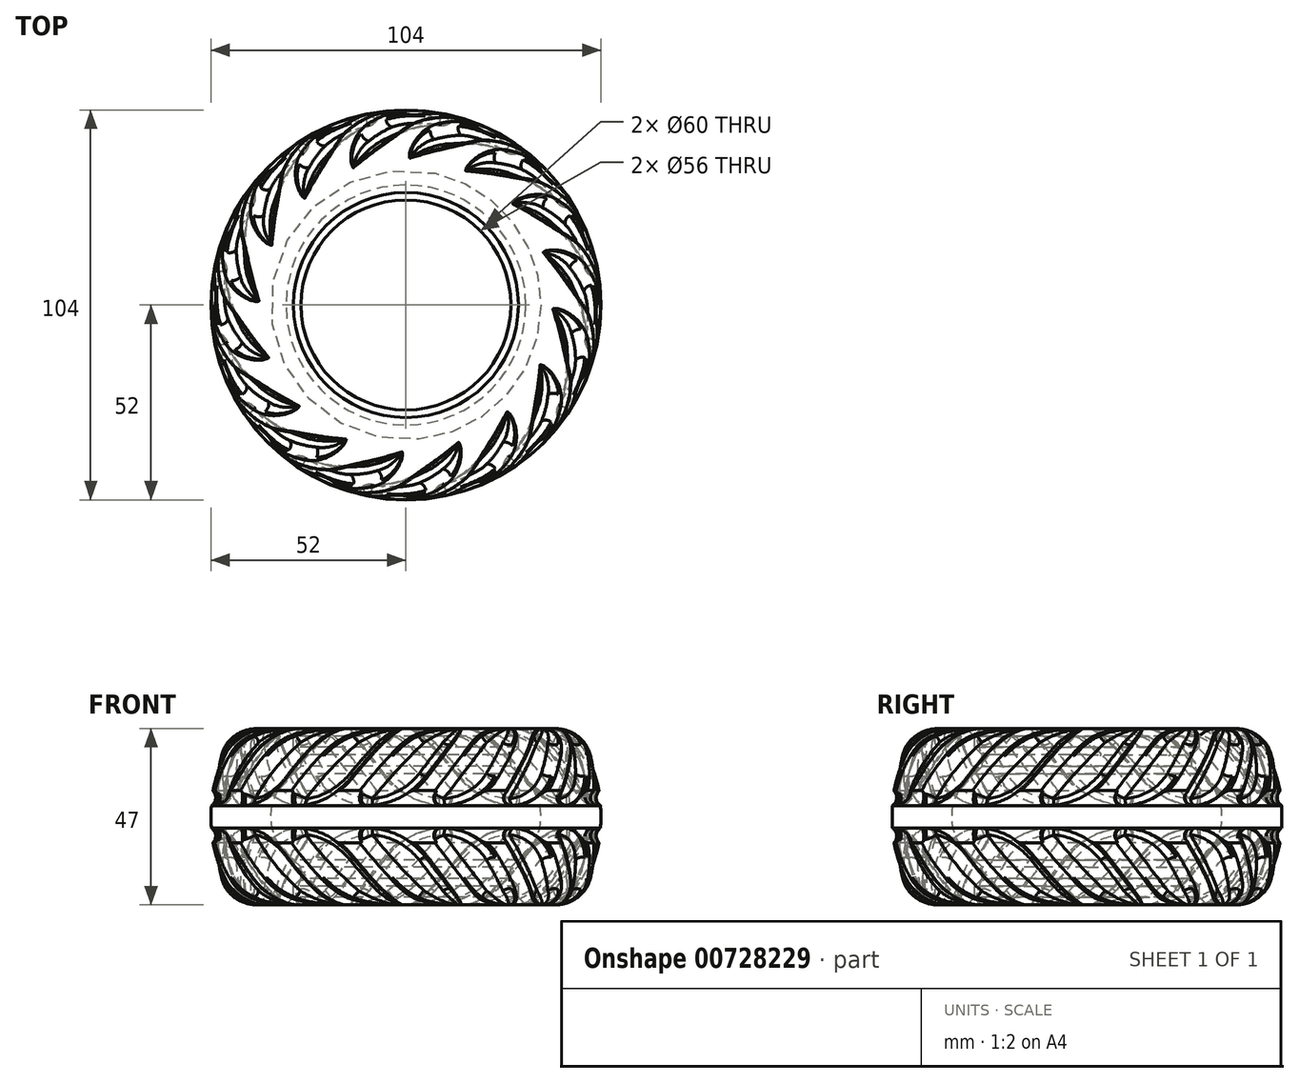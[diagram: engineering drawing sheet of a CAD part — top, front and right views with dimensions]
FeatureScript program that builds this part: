
annotation { "Feature Type Name" : "Feature", "Feature Type Description" : "" }
export const myFeature = defineFeature(function(context is Context, id is Id, definition is map)
    precondition{}
    {
        {
            var Q0;
            Q0=qCreatedBy(makeId("Front.planeOp"),FACE);
            var sketch = newSketch(context, id + "F0", { "sketchPlane" : qUnion([Q0])});
            skLineSegment(sketch, "E0", {"start": v(0, 0) * mm, "end": v(-62.9, 0) * mm, "construction": true});
            skCircle(sketch, "E1", {"center": v(-39.12, 17.25) * mm, "radius": 6.25 * mm});
            skCircle(sketch, "E2", {"center": v(0, 0) * mm, "radius": 55 * mm});
            skCircle(sketch, "E3", {"center": v(-39.12, -17.25) * mm, "radius": 6.25 * mm});
            skCircle(sketch, "E4", {"center": v(0, 0) * mm, "radius": 49 * mm});
            skLineSegment(sketch, "E5", {"start": v(-30, 23.5) * mm, "end": v(-39.12, 23.5) * mm});
            skLineSegment(sketch, "E6", {"start": v(-30, -23.5) * mm, "end": v(-39.12, -23.5) * mm});
            skLineSegment(sketch, "E7", {"start": v(0, 89.19) * mm, "end": v(0, -93.9) * mm, "construction": true});
            skLineSegment(sketch, "E8", {"start": v(-30, 23.5) * mm, "end": v(-30, 18.5) * mm});
            skLineSegment(sketch, "E9", {"start": v(-30, 18.5) * mm, "end": v(-28, 18.5) * mm});
            skLineSegment(sketch, "E10", {"start": v(-28, 18.5) * mm, "end": v(-28, 11.5) * mm});
            skLineSegment(sketch, "E11", {"start": v(-28, 11.5) * mm, "end": v(-30, 11.5) * mm});
            skLineSegment(sketch, "E12", {"start": v(-30, 11.5) * mm, "end": v(-30, -11.5) * mm});
            skLineSegment(sketch, "E13", {"start": v(-30, -11.5) * mm, "end": v(-28, -11.5) * mm});
            skLineSegment(sketch, "E14", {"start": v(-28, -11.5) * mm, "end": v(-28, -18.5) * mm});
            skLineSegment(sketch, "E15", {"start": v(-28, -18.5) * mm, "end": v(-30, -18.5) * mm});
            skLineSegment(sketch, "E16", {"start": v(-30, -18.5) * mm, "end": v(-30, -23.5) * mm});
            skArc(sketch, "E17", {"start": v(-30, 11.5) * mm, "mid": v(-36, 0) * mm, "end": v(-30, -11.5) * mm});
            skSolve(sketch);
        }
        {
            var Q0;
            {var subQ1=sQuery(id+"F0.wireOp",EDGE,"E5");Q0=makeQuery(id+"F0.imprint","IMPRINT",FACE,{"disambiguationData":[TD([[makeQuery(id+"F0.imprint","IMPRINT",EDGE,{"derivedFrom":subQ1}),1.0]])]});}
            var Q1;
            {var subQ0=sQuery(id+"F0.wireOp",EDGE,"E1");var subQ1=makeQuery(id+"F0.imprint","INTERSECT",VERTEX,{"derivedFrom":[subQ0,sQuery(id+"F0.wireOp",EDGE,"E5")]});Q1=makeQuery(id+"F0.imprint","IMPRINT",FACE,{"disambiguationData":[TD([[makeQuery(id+"F0.imprint","IMPRINT",EDGE,{"disambiguationData":[TD([[subQ1,-1.0]])],"derivedFrom":subQ0}),1.0]])]});}
            var Q2;
            {var subQ0=sQuery(id+"F0.wireOp",EDGE,"E3");var subQ1=makeQuery(id+"F0.imprint","INTERSECT",VERTEX,{"derivedFrom":[subQ0,sQuery(id+"F0.wireOp",EDGE,"E6")]});Q2=makeQuery(id+"F0.imprint","IMPRINT",FACE,{"disambiguationData":[TD([[makeQuery(id+"F0.imprint","IMPRINT",EDGE,{"disambiguationData":[TD([[subQ1,1.0]])],"derivedFrom":subQ0}),1.0]])]});}
            var Q3;
            Q3=sQuery(id+"F0.wireOp",EDGE,"E7");
            revolve(context, id + "F1", {"entities" : qUnion([Q0, Q1, Q2]), "axis" : qUnion([Q3]), "revolveType" : RevolveType.FULL});
        }
        {
            var Q0;
            Q0=qCreatedBy(makeId("Top.planeOp"),FACE);
            cPlane(context, id + "F2", {"entities" : qUnion([Q0]), "cplaneType" : CPlaneType.OFFSET, "offset" : 23.5 * mm, "width" : 150 * mm, "height" : 150 * mm});
        }
        {
            var Q0;
            Q0=qCreatedBy(makeId("Top.planeOp"),FACE);
            var sketch = newSketch(context, id + "F3", { "sketchPlane" : qUnion([Q0])});
            skLineSegment(sketch, "E18.bottom", {"start": v(-3, 40) * mm, "end": v(3, 40) * mm});
            skLineSegment(sketch, "E18.top", {"start": v(-3, 66) * mm, "end": v(3, 66) * mm});
            skLineSegment(sketch, "E18.left", {"start": v(-3, 40) * mm, "end": v(-3, 66) * mm});
            skLineSegment(sketch, "E18.right", {"start": v(3, 40) * mm, "end": v(3, 66) * mm});
            skLineSegment(sketch, "E19", {"start": v(0, 113.7) * mm, "end": v(0, -99.56) * mm, "construction": true});
            skLineSegment(sketch, "E20.1.0", {"start": v(-18.08, 35.8) * mm, "end": v(-28.03, 59.83) * mm});
            skLineSegment(sketch, "E20.1.1", {"start": v(-28.03, 59.83) * mm, "end": v(-22.49, 62.12) * mm});
            skLineSegment(sketch, "E20.1.2", {"start": v(-12.54, 38.1) * mm, "end": v(-22.49, 62.12) * mm});
            skLineSegment(sketch, "E20.1.3", {"start": v(-18.08, 35.8) * mm, "end": v(-12.54, 38.1) * mm});
            skLineSegment(sketch, "E20.2.0", {"start": v(-30.4, 26.16) * mm, "end": v(-48.8, 44.55) * mm});
            skLineSegment(sketch, "E20.2.1", {"start": v(-48.8, 44.55) * mm, "end": v(-44.55, 48.8) * mm});
            skLineSegment(sketch, "E20.2.2", {"start": v(-26.16, 30.4) * mm, "end": v(-44.55, 48.8) * mm});
            skLineSegment(sketch, "E20.2.3", {"start": v(-30.4, 26.16) * mm, "end": v(-26.16, 30.4) * mm});
            skLineSegment(sketch, "E20.3.0", {"start": v(-38.1, 12.54) * mm, "end": v(-62.12, 22.49) * mm});
            skLineSegment(sketch, "E20.3.1", {"start": v(-62.12, 22.49) * mm, "end": v(-59.83, 28.03) * mm});
            skLineSegment(sketch, "E20.3.2", {"start": v(-35.8, 18.08) * mm, "end": v(-59.83, 28.03) * mm});
            skLineSegment(sketch, "E20.3.3", {"start": v(-38.1, 12.54) * mm, "end": v(-35.8, 18.08) * mm});
            skLineSegment(sketch, "E20.4.0", {"start": v(-40, -3) * mm, "end": v(-66, -3) * mm});
            skLineSegment(sketch, "E20.4.1", {"start": v(-66, -3) * mm, "end": v(-66, 3) * mm});
            skLineSegment(sketch, "E20.4.2", {"start": v(-40, 3) * mm, "end": v(-66, 3) * mm});
            skLineSegment(sketch, "E20.4.3", {"start": v(-40, -3) * mm, "end": v(-40, 3) * mm});
            skLineSegment(sketch, "E20.5.0", {"start": v(-35.8, -18.08) * mm, "end": v(-59.83, -28.03) * mm});
            skLineSegment(sketch, "E20.5.1", {"start": v(-59.83, -28.03) * mm, "end": v(-62.12, -22.49) * mm});
            skLineSegment(sketch, "E20.5.2", {"start": v(-38.1, -12.54) * mm, "end": v(-62.12, -22.49) * mm});
            skLineSegment(sketch, "E20.5.3", {"start": v(-35.8, -18.08) * mm, "end": v(-38.1, -12.54) * mm});
            skLineSegment(sketch, "E20.6.0", {"start": v(-26.16, -30.4) * mm, "end": v(-44.55, -48.8) * mm});
            skLineSegment(sketch, "E20.6.1", {"start": v(-44.55, -48.8) * mm, "end": v(-48.8, -44.55) * mm});
            skLineSegment(sketch, "E20.6.2", {"start": v(-30.4, -26.16) * mm, "end": v(-48.8, -44.55) * mm});
            skLineSegment(sketch, "E20.6.3", {"start": v(-26.16, -30.4) * mm, "end": v(-30.4, -26.16) * mm});
            skLineSegment(sketch, "E20.7.0", {"start": v(-12.54, -38.1) * mm, "end": v(-22.49, -62.12) * mm});
            skLineSegment(sketch, "E20.7.1", {"start": v(-22.49, -62.12) * mm, "end": v(-28.03, -59.83) * mm});
            skLineSegment(sketch, "E20.7.2", {"start": v(-18.08, -35.8) * mm, "end": v(-28.03, -59.83) * mm});
            skLineSegment(sketch, "E20.7.3", {"start": v(-12.54, -38.1) * mm, "end": v(-18.08, -35.8) * mm});
            skLineSegment(sketch, "E20.8.0", {"start": v(3, -40) * mm, "end": v(3, -66) * mm});
            skLineSegment(sketch, "E20.8.1", {"start": v(3, -66) * mm, "end": v(-3, -66) * mm});
            skLineSegment(sketch, "E20.8.2", {"start": v(-3, -40) * mm, "end": v(-3, -66) * mm});
            skLineSegment(sketch, "E20.8.3", {"start": v(3, -40) * mm, "end": v(-3, -40) * mm});
            skLineSegment(sketch, "E20.9.0", {"start": v(18.08, -35.8) * mm, "end": v(28.03, -59.83) * mm});
            skLineSegment(sketch, "E20.9.1", {"start": v(28.03, -59.83) * mm, "end": v(22.49, -62.12) * mm});
            skLineSegment(sketch, "E20.9.2", {"start": v(12.54, -38.1) * mm, "end": v(22.49, -62.12) * mm});
            skLineSegment(sketch, "E20.9.3", {"start": v(18.08, -35.8) * mm, "end": v(12.54, -38.1) * mm});
            skLineSegment(sketch, "E20.10.0", {"start": v(30.4, -26.16) * mm, "end": v(48.8, -44.55) * mm});
            skLineSegment(sketch, "E20.10.1", {"start": v(48.8, -44.55) * mm, "end": v(44.55, -48.8) * mm});
            skLineSegment(sketch, "E20.10.2", {"start": v(26.16, -30.4) * mm, "end": v(44.55, -48.8) * mm});
            skLineSegment(sketch, "E20.10.3", {"start": v(30.4, -26.16) * mm, "end": v(26.16, -30.4) * mm});
            skLineSegment(sketch, "E20.11.0", {"start": v(38.1, -12.54) * mm, "end": v(62.12, -22.49) * mm});
            skLineSegment(sketch, "E20.11.1", {"start": v(62.12, -22.49) * mm, "end": v(59.83, -28.03) * mm});
            skLineSegment(sketch, "E20.11.2", {"start": v(35.8, -18.08) * mm, "end": v(59.83, -28.03) * mm});
            skLineSegment(sketch, "E20.11.3", {"start": v(38.1, -12.54) * mm, "end": v(35.8, -18.08) * mm});
            skLineSegment(sketch, "E20.12.0", {"start": v(40, 3) * mm, "end": v(66, 3) * mm});
            skLineSegment(sketch, "E20.12.1", {"start": v(66, 3) * mm, "end": v(66, -3) * mm});
            skLineSegment(sketch, "E20.12.2", {"start": v(40, -3) * mm, "end": v(66, -3) * mm});
            skLineSegment(sketch, "E20.12.3", {"start": v(40, 3) * mm, "end": v(40, -3) * mm});
            skLineSegment(sketch, "E20.13.0", {"start": v(35.8, 18.08) * mm, "end": v(59.83, 28.03) * mm});
            skLineSegment(sketch, "E20.13.1", {"start": v(59.83, 28.03) * mm, "end": v(62.12, 22.49) * mm});
            skLineSegment(sketch, "E20.13.2", {"start": v(38.1, 12.54) * mm, "end": v(62.12, 22.49) * mm});
            skLineSegment(sketch, "E20.13.3", {"start": v(35.8, 18.08) * mm, "end": v(38.1, 12.54) * mm});
            skLineSegment(sketch, "E20.14.0", {"start": v(26.16, 30.4) * mm, "end": v(44.55, 48.8) * mm});
            skLineSegment(sketch, "E20.14.1", {"start": v(44.55, 48.8) * mm, "end": v(48.8, 44.55) * mm});
            skLineSegment(sketch, "E20.14.2", {"start": v(30.4, 26.16) * mm, "end": v(48.8, 44.55) * mm});
            skLineSegment(sketch, "E20.14.3", {"start": v(26.16, 30.4) * mm, "end": v(30.4, 26.16) * mm});
            skLineSegment(sketch, "E20.15.0", {"start": v(12.54, 38.1) * mm, "end": v(22.49, 62.12) * mm});
            skLineSegment(sketch, "E20.15.1", {"start": v(22.49, 62.12) * mm, "end": v(28.03, 59.83) * mm});
            skLineSegment(sketch, "E20.15.2", {"start": v(18.08, 35.8) * mm, "end": v(28.03, 59.83) * mm});
            skLineSegment(sketch, "E20.15.3", {"start": v(12.54, 38.1) * mm, "end": v(18.08, 35.8) * mm});
            skPoint(sketch, "E20.center", {"position": v(0, 0) * mm});
            skSolve(sketch);
        }
        {
            var Q0;
            Q0=qCreatedBy(id+"F2.planeOp",FACE);
            var sketch = newSketch(context, id + "F4", { "sketchPlane" : qUnion([Q0])});
            skLineSegment(sketch, "E21", {"start": v(-21, 70) * mm, "end": v(-21, 30) * mm});
            skLineSegment(sketch, "E22", {"start": v(-21, 30) * mm, "end": v(-15, 30) * mm});
            skLineSegment(sketch, "E23", {"start": v(-21, 70) * mm, "end": v(-15, 70) * mm});
            skLineSegment(sketch, "E24", {"start": v(-15, 70) * mm, "end": v(-15, 30) * mm});
            skLineSegment(sketch, "E25", {"start": v(0, 99.7) * mm, "end": v(0, -107.8) * mm, "construction": true});
            skLineSegment(sketch, "E26.1.0", {"start": v(-46.19, 56.64) * mm, "end": v(-30.88, 19.68) * mm});
            skLineSegment(sketch, "E26.1.1", {"start": v(-40.65, 58.93) * mm, "end": v(-25.34, 21.98) * mm});
            skLineSegment(sketch, "E26.1.2", {"start": v(-30.88, 19.68) * mm, "end": v(-25.34, 21.98) * mm});
            skLineSegment(sketch, "E26.1.3", {"start": v(-46.19, 56.64) * mm, "end": v(-40.65, 58.93) * mm});
            skLineSegment(sketch, "E26.2.0", {"start": v(-64.35, 34.65) * mm, "end": v(-36.06, 6.36) * mm});
            skLineSegment(sketch, "E26.2.1", {"start": v(-60.1, 38.9) * mm, "end": v(-31.82, 10.6) * mm});
            skLineSegment(sketch, "E26.2.2", {"start": v(-36.06, 6.36) * mm, "end": v(-31.82, 10.6) * mm});
            skLineSegment(sketch, "E26.2.3", {"start": v(-64.35, 34.65) * mm, "end": v(-60.1, 38.9) * mm});
            skLineSegment(sketch, "E26.3.0", {"start": v(-72.7, 7.39) * mm, "end": v(-35.75, -7.92) * mm});
            skLineSegment(sketch, "E26.3.1", {"start": v(-70.41, 12.93) * mm, "end": v(-33.46, -2.38) * mm});
            skLineSegment(sketch, "E26.3.2", {"start": v(-35.75, -7.92) * mm, "end": v(-33.46, -2.38) * mm});
            skLineSegment(sketch, "E26.3.3", {"start": v(-72.7, 7.39) * mm, "end": v(-70.41, 12.93) * mm});
            skLineSegment(sketch, "E26.4.0", {"start": v(-70, -21) * mm, "end": v(-30, -21) * mm});
            skLineSegment(sketch, "E26.4.1", {"start": v(-70, -15) * mm, "end": v(-30, -15) * mm});
            skLineSegment(sketch, "E26.4.2", {"start": v(-30, -21) * mm, "end": v(-30, -15) * mm});
            skLineSegment(sketch, "E26.4.3", {"start": v(-70, -21) * mm, "end": v(-70, -15) * mm});
            skLineSegment(sketch, "E26.5.0", {"start": v(-56.64, -46.19) * mm, "end": v(-19.68, -30.88) * mm});
            skLineSegment(sketch, "E26.5.1", {"start": v(-58.93, -40.65) * mm, "end": v(-21.98, -25.34) * mm});
            skLineSegment(sketch, "E26.5.2", {"start": v(-19.68, -30.88) * mm, "end": v(-21.98, -25.34) * mm});
            skLineSegment(sketch, "E26.5.3", {"start": v(-56.64, -46.19) * mm, "end": v(-58.93, -40.65) * mm});
            skLineSegment(sketch, "E26.6.0", {"start": v(-34.65, -64.35) * mm, "end": v(-6.36, -36.06) * mm});
            skLineSegment(sketch, "E26.6.1", {"start": v(-38.9, -60.1) * mm, "end": v(-10.6, -31.82) * mm});
            skLineSegment(sketch, "E26.6.2", {"start": v(-6.36, -36.06) * mm, "end": v(-10.6, -31.82) * mm});
            skLineSegment(sketch, "E26.6.3", {"start": v(-34.65, -64.35) * mm, "end": v(-38.9, -60.1) * mm});
            skLineSegment(sketch, "E26.7.0", {"start": v(-7.39, -72.7) * mm, "end": v(7.92, -35.75) * mm});
            skLineSegment(sketch, "E26.7.1", {"start": v(-12.93, -70.41) * mm, "end": v(2.38, -33.46) * mm});
            skLineSegment(sketch, "E26.7.2", {"start": v(7.92, -35.75) * mm, "end": v(2.38, -33.46) * mm});
            skLineSegment(sketch, "E26.7.3", {"start": v(-7.39, -72.7) * mm, "end": v(-12.93, -70.41) * mm});
            skLineSegment(sketch, "E26.8.0", {"start": v(21, -70) * mm, "end": v(21, -30) * mm});
            skLineSegment(sketch, "E26.8.1", {"start": v(15, -70) * mm, "end": v(15, -30) * mm});
            skLineSegment(sketch, "E26.8.2", {"start": v(21, -30) * mm, "end": v(15, -30) * mm});
            skLineSegment(sketch, "E26.8.3", {"start": v(21, -70) * mm, "end": v(15, -70) * mm});
            skLineSegment(sketch, "E26.9.0", {"start": v(46.19, -56.64) * mm, "end": v(30.88, -19.68) * mm});
            skLineSegment(sketch, "E26.9.1", {"start": v(40.65, -58.93) * mm, "end": v(25.34, -21.98) * mm});
            skLineSegment(sketch, "E26.9.2", {"start": v(30.88, -19.68) * mm, "end": v(25.34, -21.98) * mm});
            skLineSegment(sketch, "E26.9.3", {"start": v(46.19, -56.64) * mm, "end": v(40.65, -58.93) * mm});
            skLineSegment(sketch, "E26.10.0", {"start": v(64.35, -34.65) * mm, "end": v(36.06, -6.36) * mm});
            skLineSegment(sketch, "E26.10.1", {"start": v(60.1, -38.9) * mm, "end": v(31.82, -10.6) * mm});
            skLineSegment(sketch, "E26.10.2", {"start": v(36.06, -6.36) * mm, "end": v(31.82, -10.6) * mm});
            skLineSegment(sketch, "E26.10.3", {"start": v(64.35, -34.65) * mm, "end": v(60.1, -38.9) * mm});
            skLineSegment(sketch, "E26.11.0", {"start": v(72.7, -7.39) * mm, "end": v(35.75, 7.92) * mm});
            skLineSegment(sketch, "E26.11.1", {"start": v(70.41, -12.93) * mm, "end": v(33.46, 2.38) * mm});
            skLineSegment(sketch, "E26.11.2", {"start": v(35.75, 7.92) * mm, "end": v(33.46, 2.38) * mm});
            skLineSegment(sketch, "E26.11.3", {"start": v(72.7, -7.39) * mm, "end": v(70.41, -12.93) * mm});
            skLineSegment(sketch, "E26.12.0", {"start": v(70, 21) * mm, "end": v(30, 21) * mm});
            skLineSegment(sketch, "E26.12.1", {"start": v(70, 15) * mm, "end": v(30, 15) * mm});
            skLineSegment(sketch, "E26.12.2", {"start": v(30, 21) * mm, "end": v(30, 15) * mm});
            skLineSegment(sketch, "E26.12.3", {"start": v(70, 21) * mm, "end": v(70, 15) * mm});
            skLineSegment(sketch, "E26.13.0", {"start": v(56.64, 46.19) * mm, "end": v(19.68, 30.88) * mm});
            skLineSegment(sketch, "E26.13.1", {"start": v(58.93, 40.65) * mm, "end": v(21.98, 25.34) * mm});
            skLineSegment(sketch, "E26.13.2", {"start": v(19.68, 30.88) * mm, "end": v(21.98, 25.34) * mm});
            skLineSegment(sketch, "E26.13.3", {"start": v(56.64, 46.19) * mm, "end": v(58.93, 40.65) * mm});
            skLineSegment(sketch, "E26.14.0", {"start": v(34.65, 64.35) * mm, "end": v(6.36, 36.06) * mm});
            skLineSegment(sketch, "E26.14.1", {"start": v(38.9, 60.1) * mm, "end": v(10.6, 31.82) * mm});
            skLineSegment(sketch, "E26.14.2", {"start": v(6.36, 36.06) * mm, "end": v(10.6, 31.82) * mm});
            skLineSegment(sketch, "E26.14.3", {"start": v(34.65, 64.35) * mm, "end": v(38.9, 60.1) * mm});
            skLineSegment(sketch, "E26.15.0", {"start": v(7.39, 72.7) * mm, "end": v(-7.92, 35.75) * mm});
            skLineSegment(sketch, "E26.15.1", {"start": v(12.93, 70.41) * mm, "end": v(-2.38, 33.46) * mm});
            skLineSegment(sketch, "E26.15.2", {"start": v(-7.92, 35.75) * mm, "end": v(-2.38, 33.46) * mm});
            skLineSegment(sketch, "E26.15.3", {"start": v(7.39, 72.7) * mm, "end": v(12.93, 70.41) * mm});
            skPoint(sketch, "E26.center", {"position": v(0, 0) * mm});
            skSolve(sketch);
        }
        {
            var Q2;
            Q2=makeQuery(id+"F3.imprint","IMPRINT",FACE,{"disambiguationData":[TD([[makeQuery(id+"F3.imprint","IMPRINT",EDGE,{"derivedFrom":sQuery(id+"F3.wireOp",EDGE,"E18.bottom")}),1.0]])]});
            var Q3;
            Q3=makeQuery(id+"F4.imprint","IMPRINT",FACE,{"disambiguationData":[TD([[makeQuery(id+"F4.imprint","IMPRINT",EDGE,{"derivedFrom":sQuery(id+"F4.wireOp",EDGE,"E21")}),1.0]])]});
            loft(context, id + "F5", {"operationType" : NewBodyOperationType.ADD, "sheetProfilesArray" : [{ "sheetProfileEntities" : qUnion([Q2]) }, { "sheetProfileEntities" : qUnion([Q3]) }]});
        }
        {
            var Q2;
            Q2=makeQuery(id+"F3.imprint","IMPRINT",FACE,{"disambiguationData":[TD([[makeQuery(id+"F3.imprint","IMPRINT",EDGE,{"derivedFrom":sQuery(id+"F3.wireOp",EDGE,"E20.15.0")}),-1.0]])]});
            var Q3;
            Q3=makeQuery(id+"F4.imprint","IMPRINT",FACE,{"disambiguationData":[TD([[makeQuery(id+"F4.imprint","IMPRINT",EDGE,{"derivedFrom":sQuery(id+"F4.wireOp",EDGE,"E26.15.0")}),1.0]])]});
            loft(context, id + "F6", {"operationType" : NewBodyOperationType.ADD, "sheetProfilesArray" : [{ "sheetProfileEntities" : qUnion([Q2]) }, { "sheetProfileEntities" : qUnion([Q3]) }]});
        }
        {
            var Q1;
            Q1=makeQuery(id+"F3.imprint","IMPRINT",FACE,{"disambiguationData":[TD([[makeQuery(id+"F3.imprint","IMPRINT",EDGE,{"derivedFrom":sQuery(id+"F3.wireOp",EDGE,"E20.14.0")}),-1.0]])]});
            var Q2;
            Q2=makeQuery(id+"F4.imprint","IMPRINT",FACE,{"disambiguationData":[TD([[makeQuery(id+"F4.imprint","IMPRINT",EDGE,{"derivedFrom":sQuery(id+"F4.wireOp",EDGE,"E26.14.0")}),1.0]])]});
            loft(context, id + "F7", {"operationType" : NewBodyOperationType.ADD, "sheetProfilesArray" : [{ "sheetProfileEntities" : qUnion([Q1]) }, { "sheetProfileEntities" : qUnion([Q2]) }]});
        }
        {
            var Q1;
            Q1=makeQuery(id+"F3.imprint","IMPRINT",FACE,{"disambiguationData":[TD([[makeQuery(id+"F3.imprint","IMPRINT",EDGE,{"derivedFrom":sQuery(id+"F3.wireOp",EDGE,"E20.13.0")}),-1.0]])]});
            var Q2;
            Q2=makeQuery(id+"F4.imprint","IMPRINT",FACE,{"disambiguationData":[TD([[makeQuery(id+"F4.imprint","IMPRINT",EDGE,{"derivedFrom":sQuery(id+"F4.wireOp",EDGE,"E26.13.0")}),1.0]])]});
            loft(context, id + "F8", {"operationType" : NewBodyOperationType.ADD, "sheetProfilesArray" : [{ "sheetProfileEntities" : qUnion([Q1]) }, { "sheetProfileEntities" : qUnion([Q2]) }]});
        }
        {
            var Q2;
            Q2=makeQuery(id+"F3.imprint","IMPRINT",FACE,{"disambiguationData":[TD([[makeQuery(id+"F3.imprint","IMPRINT",EDGE,{"derivedFrom":sQuery(id+"F3.wireOp",EDGE,"E20.12.0")}),-1.0]])]});
            var Q3;
            Q3=makeQuery(id+"F4.imprint","IMPRINT",FACE,{"disambiguationData":[TD([[makeQuery(id+"F4.imprint","IMPRINT",EDGE,{"derivedFrom":sQuery(id+"F4.wireOp",EDGE,"E26.12.0")}),1.0]])]});
            loft(context, id + "F9", {"operationType" : NewBodyOperationType.ADD, "sheetProfilesArray" : [{ "sheetProfileEntities" : qUnion([Q2]) }, { "sheetProfileEntities" : qUnion([Q3]) }]});
        }
        {
            var Q2;
            Q2=makeQuery(id+"F3.imprint","IMPRINT",FACE,{"disambiguationData":[TD([[makeQuery(id+"F3.imprint","IMPRINT",EDGE,{"derivedFrom":sQuery(id+"F3.wireOp",EDGE,"E20.11.0")}),-1.0]])]});
            var Q3;
            Q3=makeQuery(id+"F4.imprint","IMPRINT",FACE,{"disambiguationData":[TD([[makeQuery(id+"F4.imprint","IMPRINT",EDGE,{"derivedFrom":sQuery(id+"F4.wireOp",EDGE,"E26.11.0")}),1.0]])]});
            loft(context, id + "F10", {"operationType" : NewBodyOperationType.ADD, "sheetProfilesArray" : [{ "sheetProfileEntities" : qUnion([Q2]) }, { "sheetProfileEntities" : qUnion([Q3]) }]});
        }
        {
            var Q2;
            Q2=makeQuery(id+"F3.imprint","IMPRINT",FACE,{"disambiguationData":[TD([[makeQuery(id+"F3.imprint","IMPRINT",EDGE,{"derivedFrom":sQuery(id+"F3.wireOp",EDGE,"E20.10.0")}),-1.0]])]});
            var Q3;
            Q3=makeQuery(id+"F4.imprint","IMPRINT",FACE,{"disambiguationData":[TD([[makeQuery(id+"F4.imprint","IMPRINT",EDGE,{"derivedFrom":sQuery(id+"F4.wireOp",EDGE,"E26.10.0")}),1.0]])]});
            loft(context, id + "F11", {"operationType" : NewBodyOperationType.ADD, "sheetProfilesArray" : [{ "sheetProfileEntities" : qUnion([Q2]) }, { "sheetProfileEntities" : qUnion([Q3]) }]});
        }
        {
            var Q2;
            Q2=makeQuery(id+"F3.imprint","IMPRINT",FACE,{"disambiguationData":[TD([[makeQuery(id+"F3.imprint","IMPRINT",EDGE,{"derivedFrom":sQuery(id+"F3.wireOp",EDGE,"E20.9.0")}),-1.0]])]});
            var Q3;
            Q3=makeQuery(id+"F4.imprint","IMPRINT",FACE,{"disambiguationData":[TD([[makeQuery(id+"F4.imprint","IMPRINT",EDGE,{"derivedFrom":sQuery(id+"F4.wireOp",EDGE,"E26.9.0")}),1.0]])]});
            loft(context, id + "F12", {"operationType" : NewBodyOperationType.ADD, "sheetProfilesArray" : [{ "sheetProfileEntities" : qUnion([Q2]) }, { "sheetProfileEntities" : qUnion([Q3]) }]});
        }
        {
            var Q2;
            Q2=makeQuery(id+"F3.imprint","IMPRINT",FACE,{"disambiguationData":[TD([[makeQuery(id+"F3.imprint","IMPRINT",EDGE,{"derivedFrom":sQuery(id+"F3.wireOp",EDGE,"E20.8.0")}),-1.0]])]});
            var Q3;
            Q3=makeQuery(id+"F4.imprint","IMPRINT",FACE,{"disambiguationData":[TD([[makeQuery(id+"F4.imprint","IMPRINT",EDGE,{"derivedFrom":sQuery(id+"F4.wireOp",EDGE,"E26.8.0")}),1.0]])]});
            loft(context, id + "F13", {"operationType" : NewBodyOperationType.ADD, "sheetProfilesArray" : [{ "sheetProfileEntities" : qUnion([Q2]) }, { "sheetProfileEntities" : qUnion([Q3]) }]});
        }
        {
            var Q2;
            Q2=makeQuery(id+"F3.imprint","IMPRINT",FACE,{"disambiguationData":[TD([[makeQuery(id+"F3.imprint","IMPRINT",EDGE,{"derivedFrom":sQuery(id+"F3.wireOp",EDGE,"E20.7.0")}),-1.0]])]});
            var Q3;
            Q3=makeQuery(id+"F4.imprint","IMPRINT",FACE,{"disambiguationData":[TD([[makeQuery(id+"F4.imprint","IMPRINT",EDGE,{"derivedFrom":sQuery(id+"F4.wireOp",EDGE,"E26.7.0")}),1.0]])]});
            loft(context, id + "F14", {"operationType" : NewBodyOperationType.ADD, "sheetProfilesArray" : [{ "sheetProfileEntities" : qUnion([Q2]) }, { "sheetProfileEntities" : qUnion([Q3]) }]});
        }
        {
            var Q2;
            Q2=makeQuery(id+"F3.imprint","IMPRINT",FACE,{"disambiguationData":[TD([[makeQuery(id+"F3.imprint","IMPRINT",EDGE,{"derivedFrom":sQuery(id+"F3.wireOp",EDGE,"E20.6.0")}),-1.0]])]});
            var Q3;
            Q3=makeQuery(id+"F4.imprint","IMPRINT",FACE,{"disambiguationData":[TD([[makeQuery(id+"F4.imprint","IMPRINT",EDGE,{"derivedFrom":sQuery(id+"F4.wireOp",EDGE,"E26.6.0")}),1.0]])]});
            loft(context, id + "F15", {"operationType" : NewBodyOperationType.ADD, "sheetProfilesArray" : [{ "sheetProfileEntities" : qUnion([Q2]) }, { "sheetProfileEntities" : qUnion([Q3]) }]});
        }
        {
            var Q2;
            Q2=makeQuery(id+"F3.imprint","IMPRINT",FACE,{"disambiguationData":[TD([[makeQuery(id+"F3.imprint","IMPRINT",EDGE,{"derivedFrom":sQuery(id+"F3.wireOp",EDGE,"E20.5.0")}),-1.0]])]});
            var Q3;
            Q3=makeQuery(id+"F4.imprint","IMPRINT",FACE,{"disambiguationData":[TD([[makeQuery(id+"F4.imprint","IMPRINT",EDGE,{"derivedFrom":sQuery(id+"F4.wireOp",EDGE,"E26.5.0")}),1.0]])]});
            loft(context, id + "F16", {"operationType" : NewBodyOperationType.ADD, "sheetProfilesArray" : [{ "sheetProfileEntities" : qUnion([Q2]) }, { "sheetProfileEntities" : qUnion([Q3]) }]});
        }
        {
            var Q1;
            Q1=makeQuery(id+"F4.imprint","IMPRINT",FACE,{"disambiguationData":[TD([[makeQuery(id+"F4.imprint","IMPRINT",EDGE,{"derivedFrom":sQuery(id+"F4.wireOp",EDGE,"E26.4.0")}),1.0]])]});
            var Q2;
            Q2=makeQuery(id+"F3.imprint","IMPRINT",FACE,{"disambiguationData":[TD([[makeQuery(id+"F3.imprint","IMPRINT",EDGE,{"derivedFrom":sQuery(id+"F3.wireOp",EDGE,"E20.4.0")}),-1.0]])]});
            loft(context, id + "F17", {"operationType" : NewBodyOperationType.ADD, "sheetProfilesArray" : [{ "sheetProfileEntities" : qUnion([Q1]) }, { "sheetProfileEntities" : qUnion([Q2]) }]});
        }
        {
            var Q1;
            Q1=makeQuery(id+"F3.imprint","IMPRINT",FACE,{"disambiguationData":[TD([[makeQuery(id+"F3.imprint","IMPRINT",EDGE,{"derivedFrom":sQuery(id+"F3.wireOp",EDGE,"E20.3.0")}),-1.0]])]});
            var Q2;
            Q2=makeQuery(id+"F4.imprint","IMPRINT",FACE,{"disambiguationData":[TD([[makeQuery(id+"F4.imprint","IMPRINT",EDGE,{"derivedFrom":sQuery(id+"F4.wireOp",EDGE,"E26.3.0")}),1.0]])]});
            loft(context, id + "F18", {"operationType" : NewBodyOperationType.ADD, "sheetProfilesArray" : [{ "sheetProfileEntities" : qUnion([Q1]) }, { "sheetProfileEntities" : qUnion([Q2]) }]});
        }
        {
            var Q1;
            Q1=makeQuery(id+"F3.imprint","IMPRINT",FACE,{"disambiguationData":[TD([[makeQuery(id+"F3.imprint","IMPRINT",EDGE,{"derivedFrom":sQuery(id+"F3.wireOp",EDGE,"E20.2.0")}),-1.0]])]});
            var Q2;
            Q2=makeQuery(id+"F4.imprint","IMPRINT",FACE,{"disambiguationData":[TD([[makeQuery(id+"F4.imprint","IMPRINT",EDGE,{"derivedFrom":sQuery(id+"F4.wireOp",EDGE,"E26.2.0")}),1.0]])]});
            loft(context, id + "F19", {"operationType" : NewBodyOperationType.ADD, "sheetProfilesArray" : [{ "sheetProfileEntities" : qUnion([Q1]) }, { "sheetProfileEntities" : qUnion([Q2]) }]});
        }
        {
            var Q1;
            Q1=makeQuery(id+"F3.imprint","IMPRINT",FACE,{"disambiguationData":[TD([[makeQuery(id+"F3.imprint","IMPRINT",EDGE,{"derivedFrom":sQuery(id+"F3.wireOp",EDGE,"E20.1.0")}),-1.0]])]});
            var Q2;
            Q2=makeQuery(id+"F4.imprint","IMPRINT",FACE,{"disambiguationData":[TD([[makeQuery(id+"F4.imprint","IMPRINT",EDGE,{"derivedFrom":sQuery(id+"F4.wireOp",EDGE,"E26.1.0")}),1.0]])]});
            loft(context, id + "F20", {"operationType" : NewBodyOperationType.ADD, "sheetProfilesArray" : [{ "sheetProfileEntities" : qUnion([Q1]) }, { "sheetProfileEntities" : qUnion([Q2]) }]});
        }
        {
            var Q0;
            Q0=qCreatedBy(makeId("Top.planeOp"),FACE);
            cPlane(context, id + "F21", {"entities" : qUnion([Q0]), "cplaneType" : CPlaneType.OFFSET, "offset" : 23.5 * mm, "oppositeDirection" : true, "width" : 150 * mm, "height" : 150 * mm});
        }
        {
            var Q0;
            Q0=qCreatedBy(id+"F21.planeOp",FACE);
            var sketch = newSketch(context, id + "F22", { "sketchPlane" : qUnion([Q0])});
            skLineSegment(sketch, "E27.bottom", {"start": v(15, -70) * mm, "end": v(21, -70) * mm});
            skLineSegment(sketch, "E27.top", {"start": v(15, -30) * mm, "end": v(21, -30) * mm});
            skLineSegment(sketch, "E27.left", {"start": v(15, -70) * mm, "end": v(15, -30) * mm});
            skLineSegment(sketch, "E27.right", {"start": v(21, -70) * mm, "end": v(21, -30) * mm});
            skLineSegment(sketch, "E28.1.0", {"start": v(40.65, -58.93) * mm, "end": v(25.34, -21.98) * mm});
            skLineSegment(sketch, "E28.1.1", {"start": v(46.19, -56.64) * mm, "end": v(30.88, -19.68) * mm});
            skLineSegment(sketch, "E28.1.2", {"start": v(40.65, -58.93) * mm, "end": v(46.19, -56.64) * mm});
            skLineSegment(sketch, "E28.1.3", {"start": v(25.34, -21.98) * mm, "end": v(30.88, -19.68) * mm});
            skLineSegment(sketch, "E28.2.0", {"start": v(60.1, -38.9) * mm, "end": v(31.82, -10.6) * mm});
            skLineSegment(sketch, "E28.2.1", {"start": v(64.35, -34.65) * mm, "end": v(36.06, -6.36) * mm});
            skLineSegment(sketch, "E28.2.2", {"start": v(60.1, -38.9) * mm, "end": v(64.35, -34.65) * mm});
            skLineSegment(sketch, "E28.2.3", {"start": v(31.82, -10.6) * mm, "end": v(36.06, -6.36) * mm});
            skLineSegment(sketch, "E28.3.0", {"start": v(70.41, -12.93) * mm, "end": v(33.46, 2.38) * mm});
            skLineSegment(sketch, "E28.3.1", {"start": v(72.7, -7.39) * mm, "end": v(35.75, 7.92) * mm});
            skLineSegment(sketch, "E28.3.2", {"start": v(70.41, -12.93) * mm, "end": v(72.7, -7.39) * mm});
            skLineSegment(sketch, "E28.3.3", {"start": v(33.46, 2.38) * mm, "end": v(35.75, 7.92) * mm});
            skLineSegment(sketch, "E28.4.0", {"start": v(70, 15) * mm, "end": v(30, 15) * mm});
            skLineSegment(sketch, "E28.4.1", {"start": v(70, 21) * mm, "end": v(30, 21) * mm});
            skLineSegment(sketch, "E28.4.2", {"start": v(70, 15) * mm, "end": v(70, 21) * mm});
            skLineSegment(sketch, "E28.4.3", {"start": v(30, 15) * mm, "end": v(30, 21) * mm});
            skLineSegment(sketch, "E28.5.0", {"start": v(58.93, 40.65) * mm, "end": v(21.98, 25.34) * mm});
            skLineSegment(sketch, "E28.5.1", {"start": v(56.64, 46.19) * mm, "end": v(19.68, 30.88) * mm});
            skLineSegment(sketch, "E28.5.2", {"start": v(58.93, 40.65) * mm, "end": v(56.64, 46.19) * mm});
            skLineSegment(sketch, "E28.5.3", {"start": v(21.98, 25.34) * mm, "end": v(19.68, 30.88) * mm});
            skLineSegment(sketch, "E28.6.0", {"start": v(38.9, 60.1) * mm, "end": v(10.6, 31.82) * mm});
            skLineSegment(sketch, "E28.6.1", {"start": v(34.65, 64.35) * mm, "end": v(6.36, 36.06) * mm});
            skLineSegment(sketch, "E28.6.2", {"start": v(38.9, 60.1) * mm, "end": v(34.65, 64.35) * mm});
            skLineSegment(sketch, "E28.6.3", {"start": v(10.6, 31.82) * mm, "end": v(6.36, 36.06) * mm});
            skLineSegment(sketch, "E28.7.0", {"start": v(12.93, 70.41) * mm, "end": v(-2.38, 33.46) * mm});
            skLineSegment(sketch, "E28.7.1", {"start": v(7.39, 72.7) * mm, "end": v(-7.92, 35.75) * mm});
            skLineSegment(sketch, "E28.7.2", {"start": v(12.93, 70.41) * mm, "end": v(7.39, 72.7) * mm});
            skLineSegment(sketch, "E28.7.3", {"start": v(-2.38, 33.46) * mm, "end": v(-7.92, 35.75) * mm});
            skLineSegment(sketch, "E28.8.0", {"start": v(-15, 70) * mm, "end": v(-15, 30) * mm});
            skLineSegment(sketch, "E28.8.1", {"start": v(-21, 70) * mm, "end": v(-21, 30) * mm});
            skLineSegment(sketch, "E28.8.2", {"start": v(-15, 70) * mm, "end": v(-21, 70) * mm});
            skLineSegment(sketch, "E28.8.3", {"start": v(-15, 30) * mm, "end": v(-21, 30) * mm});
            skLineSegment(sketch, "E28.9.0", {"start": v(-40.65, 58.93) * mm, "end": v(-25.34, 21.98) * mm});
            skLineSegment(sketch, "E28.9.1", {"start": v(-46.19, 56.64) * mm, "end": v(-30.88, 19.68) * mm});
            skLineSegment(sketch, "E28.9.2", {"start": v(-40.65, 58.93) * mm, "end": v(-46.19, 56.64) * mm});
            skLineSegment(sketch, "E28.9.3", {"start": v(-25.34, 21.98) * mm, "end": v(-30.88, 19.68) * mm});
            skLineSegment(sketch, "E28.10.0", {"start": v(-60.1, 38.9) * mm, "end": v(-31.82, 10.6) * mm});
            skLineSegment(sketch, "E28.10.1", {"start": v(-64.35, 34.65) * mm, "end": v(-36.06, 6.36) * mm});
            skLineSegment(sketch, "E28.10.2", {"start": v(-60.1, 38.9) * mm, "end": v(-64.35, 34.65) * mm});
            skLineSegment(sketch, "E28.10.3", {"start": v(-31.82, 10.6) * mm, "end": v(-36.06, 6.36) * mm});
            skLineSegment(sketch, "E28.11.0", {"start": v(-70.41, 12.93) * mm, "end": v(-33.46, -2.38) * mm});
            skLineSegment(sketch, "E28.11.1", {"start": v(-72.7, 7.39) * mm, "end": v(-35.75, -7.92) * mm});
            skLineSegment(sketch, "E28.11.2", {"start": v(-70.41, 12.93) * mm, "end": v(-72.7, 7.39) * mm});
            skLineSegment(sketch, "E28.11.3", {"start": v(-33.46, -2.38) * mm, "end": v(-35.75, -7.92) * mm});
            skLineSegment(sketch, "E28.12.0", {"start": v(-70, -15) * mm, "end": v(-30, -15) * mm});
            skLineSegment(sketch, "E28.12.1", {"start": v(-70, -21) * mm, "end": v(-30, -21) * mm});
            skLineSegment(sketch, "E28.12.2", {"start": v(-70, -15) * mm, "end": v(-70, -21) * mm});
            skLineSegment(sketch, "E28.12.3", {"start": v(-30, -15) * mm, "end": v(-30, -21) * mm});
            skLineSegment(sketch, "E28.13.0", {"start": v(-58.93, -40.65) * mm, "end": v(-21.98, -25.34) * mm});
            skLineSegment(sketch, "E28.13.1", {"start": v(-56.64, -46.19) * mm, "end": v(-19.68, -30.88) * mm});
            skLineSegment(sketch, "E28.13.2", {"start": v(-58.93, -40.65) * mm, "end": v(-56.64, -46.19) * mm});
            skLineSegment(sketch, "E28.13.3", {"start": v(-21.98, -25.34) * mm, "end": v(-19.68, -30.88) * mm});
            skLineSegment(sketch, "E28.14.0", {"start": v(-38.9, -60.1) * mm, "end": v(-10.6, -31.82) * mm});
            skLineSegment(sketch, "E28.14.1", {"start": v(-34.65, -64.35) * mm, "end": v(-6.36, -36.06) * mm});
            skLineSegment(sketch, "E28.14.2", {"start": v(-38.9, -60.1) * mm, "end": v(-34.65, -64.35) * mm});
            skLineSegment(sketch, "E28.14.3", {"start": v(-10.6, -31.82) * mm, "end": v(-6.36, -36.06) * mm});
            skLineSegment(sketch, "E28.15.0", {"start": v(-12.93, -70.41) * mm, "end": v(2.38, -33.46) * mm});
            skLineSegment(sketch, "E28.15.1", {"start": v(-7.39, -72.7) * mm, "end": v(7.92, -35.75) * mm});
            skLineSegment(sketch, "E28.15.2", {"start": v(-12.93, -70.41) * mm, "end": v(-7.39, -72.7) * mm});
            skLineSegment(sketch, "E28.15.3", {"start": v(2.38, -33.46) * mm, "end": v(7.92, -35.75) * mm});
            skPoint(sketch, "E28.center", {"position": v(0, 0) * mm});
            skSolve(sketch);
        }
        {
            var Q1;
            Q1=makeQuery(id+"F22.imprint","IMPRINT",FACE,{"disambiguationData":[TD([[makeQuery(id+"F22.imprint","IMPRINT",EDGE,{"derivedFrom":sQuery(id+"F22.wireOp",EDGE,"E27.bottom")}),1.0]])]});
            var Q2;
            Q2=makeQuery(id+"F3.imprint","IMPRINT",FACE,{"disambiguationData":[TD([[makeQuery(id+"F3.imprint","IMPRINT",EDGE,{"derivedFrom":sQuery(id+"F3.wireOp",EDGE,"E20.8.0")}),-1.0]])]});
            loft(context, id + "F23", {"operationType" : NewBodyOperationType.ADD, "sheetProfilesArray" : [{ "sheetProfileEntities" : qUnion([Q1]) }, { "sheetProfileEntities" : qUnion([Q2]) }]});
        }
        {
            var Q1;
            Q1=makeQuery(id+"F22.imprint","IMPRINT",FACE,{"disambiguationData":[TD([[makeQuery(id+"F22.imprint","IMPRINT",EDGE,{"derivedFrom":sQuery(id+"F22.wireOp",EDGE,"E28.1.0")}),-1.0]])]});
            var Q2;
            Q2=makeQuery(id+"F3.imprint","IMPRINT",FACE,{"disambiguationData":[TD([[makeQuery(id+"F3.imprint","IMPRINT",EDGE,{"derivedFrom":sQuery(id+"F3.wireOp",EDGE,"E20.9.0")}),-1.0]])]});
            loft(context, id + "F24", {"operationType" : NewBodyOperationType.ADD, "sheetProfilesArray" : [{ "sheetProfileEntities" : qUnion([Q1]) }, { "sheetProfileEntities" : qUnion([Q2]) }]});
        }
        {
            var Q1;
            Q1=makeQuery(id+"F22.imprint","IMPRINT",FACE,{"disambiguationData":[TD([[makeQuery(id+"F22.imprint","IMPRINT",EDGE,{"derivedFrom":sQuery(id+"F22.wireOp",EDGE,"E28.2.0")}),-1.0]])]});
            var Q2;
            Q2=makeQuery(id+"F3.imprint","IMPRINT",FACE,{"disambiguationData":[TD([[makeQuery(id+"F3.imprint","IMPRINT",EDGE,{"derivedFrom":sQuery(id+"F3.wireOp",EDGE,"E20.10.0")}),-1.0]])]});
            loft(context, id + "F25", {"operationType" : NewBodyOperationType.ADD, "sheetProfilesArray" : [{ "sheetProfileEntities" : qUnion([Q1]) }, { "sheetProfileEntities" : qUnion([Q2]) }]});
        }
        {
            var Q1;
            Q1=makeQuery(id+"F22.imprint","IMPRINT",FACE,{"disambiguationData":[TD([[makeQuery(id+"F22.imprint","IMPRINT",EDGE,{"derivedFrom":sQuery(id+"F22.wireOp",EDGE,"E28.3.0")}),-1.0]])]});
            var Q2;
            Q2=makeQuery(id+"F3.imprint","IMPRINT",FACE,{"disambiguationData":[TD([[makeQuery(id+"F3.imprint","IMPRINT",EDGE,{"derivedFrom":sQuery(id+"F3.wireOp",EDGE,"E20.11.0")}),-1.0]])]});
            loft(context, id + "F26", {"operationType" : NewBodyOperationType.ADD, "sheetProfilesArray" : [{ "sheetProfileEntities" : qUnion([Q1]) }, { "sheetProfileEntities" : qUnion([Q2]) }]});
        }
        {
            var Q1;
            Q1=makeQuery(id+"F22.imprint","IMPRINT",FACE,{"disambiguationData":[TD([[makeQuery(id+"F22.imprint","IMPRINT",EDGE,{"derivedFrom":sQuery(id+"F22.wireOp",EDGE,"E28.4.0")}),-1.0]])]});
            var Q2;
            Q2=makeQuery(id+"F3.imprint","IMPRINT",FACE,{"disambiguationData":[TD([[makeQuery(id+"F3.imprint","IMPRINT",EDGE,{"derivedFrom":sQuery(id+"F3.wireOp",EDGE,"E20.12.0")}),-1.0]])]});
            loft(context, id + "F27", {"operationType" : NewBodyOperationType.ADD, "sheetProfilesArray" : [{ "sheetProfileEntities" : qUnion([Q1]) }, { "sheetProfileEntities" : qUnion([Q2]) }]});
        }
        {
            var Q1;
            Q1=makeQuery(id+"F22.imprint","IMPRINT",FACE,{"disambiguationData":[TD([[makeQuery(id+"F22.imprint","IMPRINT",EDGE,{"derivedFrom":sQuery(id+"F22.wireOp",EDGE,"E28.5.0")}),-1.0]])]});
            var Q2;
            Q2=makeQuery(id+"F3.imprint","IMPRINT",FACE,{"disambiguationData":[TD([[makeQuery(id+"F3.imprint","IMPRINT",EDGE,{"derivedFrom":sQuery(id+"F3.wireOp",EDGE,"E20.13.0")}),-1.0]])]});
            loft(context, id + "F28", {"operationType" : NewBodyOperationType.ADD, "sheetProfilesArray" : [{ "sheetProfileEntities" : qUnion([Q1]) }, { "sheetProfileEntities" : qUnion([Q2]) }]});
        }
        {
            var Q1;
            Q1=makeQuery(id+"F22.imprint","IMPRINT",FACE,{"disambiguationData":[TD([[makeQuery(id+"F22.imprint","IMPRINT",EDGE,{"derivedFrom":sQuery(id+"F22.wireOp",EDGE,"E28.6.0")}),-1.0]])]});
            var Q2;
            Q2=makeQuery(id+"F3.imprint","IMPRINT",FACE,{"disambiguationData":[TD([[makeQuery(id+"F3.imprint","IMPRINT",EDGE,{"derivedFrom":sQuery(id+"F3.wireOp",EDGE,"E20.14.0")}),-1.0]])]});
            loft(context, id + "F29", {"operationType" : NewBodyOperationType.ADD, "sheetProfilesArray" : [{ "sheetProfileEntities" : qUnion([Q1]) }, { "sheetProfileEntities" : qUnion([Q2]) }]});
        }
        {
            var Q1;
            Q1=makeQuery(id+"F22.imprint","IMPRINT",FACE,{"disambiguationData":[TD([[makeQuery(id+"F22.imprint","IMPRINT",EDGE,{"derivedFrom":sQuery(id+"F22.wireOp",EDGE,"E28.7.0")}),-1.0]])]});
            var Q2;
            Q2=makeQuery(id+"F3.imprint","IMPRINT",FACE,{"disambiguationData":[TD([[makeQuery(id+"F3.imprint","IMPRINT",EDGE,{"derivedFrom":sQuery(id+"F3.wireOp",EDGE,"E20.15.0")}),-1.0]])]});
            loft(context, id + "F30", {"operationType" : NewBodyOperationType.ADD, "sheetProfilesArray" : [{ "sheetProfileEntities" : qUnion([Q1]) }, { "sheetProfileEntities" : qUnion([Q2]) }]});
        }
        {
            var Q1;
            Q1=makeQuery(id+"F22.imprint","IMPRINT",FACE,{"disambiguationData":[TD([[makeQuery(id+"F22.imprint","IMPRINT",EDGE,{"derivedFrom":sQuery(id+"F22.wireOp",EDGE,"E28.8.0")}),-1.0]])]});
            var Q2;
            Q2=makeQuery(id+"F3.imprint","IMPRINT",FACE,{"disambiguationData":[TD([[makeQuery(id+"F3.imprint","IMPRINT",EDGE,{"derivedFrom":sQuery(id+"F3.wireOp",EDGE,"E18.bottom")}),1.0]])]});
            loft(context, id + "F31", {"operationType" : NewBodyOperationType.ADD, "sheetProfilesArray" : [{ "sheetProfileEntities" : qUnion([Q1]) }, { "sheetProfileEntities" : qUnion([Q2]) }]});
        }
        {
            var Q1;
            Q1=makeQuery(id+"F22.imprint","IMPRINT",FACE,{"disambiguationData":[TD([[makeQuery(id+"F22.imprint","IMPRINT",EDGE,{"derivedFrom":sQuery(id+"F22.wireOp",EDGE,"E28.9.0")}),-1.0]])]});
            var Q2;
            Q2=makeQuery(id+"F3.imprint","IMPRINT",FACE,{"disambiguationData":[TD([[makeQuery(id+"F3.imprint","IMPRINT",EDGE,{"derivedFrom":sQuery(id+"F3.wireOp",EDGE,"E20.1.0")}),-1.0]])]});
            loft(context, id + "F32", {"operationType" : NewBodyOperationType.ADD, "sheetProfilesArray" : [{ "sheetProfileEntities" : qUnion([Q1]) }, { "sheetProfileEntities" : qUnion([Q2]) }]});
        }
        {
            var Q1;
            Q1=makeQuery(id+"F22.imprint","IMPRINT",FACE,{"disambiguationData":[TD([[makeQuery(id+"F22.imprint","IMPRINT",EDGE,{"derivedFrom":sQuery(id+"F22.wireOp",EDGE,"E28.10.0")}),-1.0]])]});
            var Q2;
            Q2=makeQuery(id+"F3.imprint","IMPRINT",FACE,{"disambiguationData":[TD([[makeQuery(id+"F3.imprint","IMPRINT",EDGE,{"derivedFrom":sQuery(id+"F3.wireOp",EDGE,"E20.2.0")}),-1.0]])]});
            loft(context, id + "F33", {"operationType" : NewBodyOperationType.ADD, "sheetProfilesArray" : [{ "sheetProfileEntities" : qUnion([Q1]) }, { "sheetProfileEntities" : qUnion([Q2]) }]});
        }
        {
            var Q1;
            Q1=makeQuery(id+"F22.imprint","IMPRINT",FACE,{"disambiguationData":[TD([[makeQuery(id+"F22.imprint","IMPRINT",EDGE,{"derivedFrom":sQuery(id+"F22.wireOp",EDGE,"E28.11.0")}),-1.0]])]});
            var Q2;
            Q2=makeQuery(id+"F3.imprint","IMPRINT",FACE,{"disambiguationData":[TD([[makeQuery(id+"F3.imprint","IMPRINT",EDGE,{"derivedFrom":sQuery(id+"F3.wireOp",EDGE,"E20.3.0")}),-1.0]])]});
            loft(context, id + "F34", {"operationType" : NewBodyOperationType.ADD, "sheetProfilesArray" : [{ "sheetProfileEntities" : qUnion([Q1]) }, { "sheetProfileEntities" : qUnion([Q2]) }]});
        }
        {
            var Q1;
            Q1=makeQuery(id+"F22.imprint","IMPRINT",FACE,{"disambiguationData":[TD([[makeQuery(id+"F22.imprint","IMPRINT",EDGE,{"derivedFrom":sQuery(id+"F22.wireOp",EDGE,"E28.12.0")}),-1.0]])]});
            var Q2;
            Q2=makeQuery(id+"F3.imprint","IMPRINT",FACE,{"disambiguationData":[TD([[makeQuery(id+"F3.imprint","IMPRINT",EDGE,{"derivedFrom":sQuery(id+"F3.wireOp",EDGE,"E20.4.0")}),-1.0]])]});
            loft(context, id + "F35", {"operationType" : NewBodyOperationType.ADD, "sheetProfilesArray" : [{ "sheetProfileEntities" : qUnion([Q1]) }, { "sheetProfileEntities" : qUnion([Q2]) }]});
        }
        {
            var Q1;
            Q1=makeQuery(id+"F22.imprint","IMPRINT",FACE,{"disambiguationData":[TD([[makeQuery(id+"F22.imprint","IMPRINT",EDGE,{"derivedFrom":sQuery(id+"F22.wireOp",EDGE,"E28.13.0")}),-1.0]])]});
            var Q2;
            Q2=makeQuery(id+"F3.imprint","IMPRINT",FACE,{"disambiguationData":[TD([[makeQuery(id+"F3.imprint","IMPRINT",EDGE,{"derivedFrom":sQuery(id+"F3.wireOp",EDGE,"E20.5.0")}),-1.0]])]});
            loft(context, id + "F36", {"operationType" : NewBodyOperationType.ADD, "sheetProfilesArray" : [{ "sheetProfileEntities" : qUnion([Q1]) }, { "sheetProfileEntities" : qUnion([Q2]) }]});
        }
        {
            var Q1;
            Q1=makeQuery(id+"F22.imprint","IMPRINT",FACE,{"disambiguationData":[TD([[makeQuery(id+"F22.imprint","IMPRINT",EDGE,{"derivedFrom":sQuery(id+"F22.wireOp",EDGE,"E28.14.0")}),-1.0]])]});
            var Q2;
            Q2=makeQuery(id+"F3.imprint","IMPRINT",FACE,{"disambiguationData":[TD([[makeQuery(id+"F3.imprint","IMPRINT",EDGE,{"derivedFrom":sQuery(id+"F3.wireOp",EDGE,"E20.6.0")}),-1.0]])]});
            loft(context, id + "F37", {"operationType" : NewBodyOperationType.ADD, "sheetProfilesArray" : [{ "sheetProfileEntities" : qUnion([Q1]) }, { "sheetProfileEntities" : qUnion([Q2]) }]});
        }
        {
            var Q1;
            Q1=makeQuery(id+"F22.imprint","IMPRINT",FACE,{"disambiguationData":[TD([[makeQuery(id+"F22.imprint","IMPRINT",EDGE,{"derivedFrom":sQuery(id+"F22.wireOp",EDGE,"E28.15.0")}),-1.0]])]});
            var Q2;
            Q2=makeQuery(id+"F3.imprint","IMPRINT",FACE,{"disambiguationData":[TD([[makeQuery(id+"F3.imprint","IMPRINT",EDGE,{"derivedFrom":sQuery(id+"F3.wireOp",EDGE,"E20.7.0")}),-1.0]])]});
            loft(context, id + "F38", {"operationType" : NewBodyOperationType.ADD, "sheetProfilesArray" : [{ "sheetProfileEntities" : qUnion([Q1]) }, { "sheetProfileEntities" : qUnion([Q2]) }]});
        }
        {
            var Q0;
            Q0=qCreatedBy(makeId("Top.planeOp"),FACE);
            var sketch = newSketch(context, id + "F39", { "sketchPlane" : qUnion([Q0])});
            skCircle(sketch, "E29", {"center": v(0, 0) * mm, "radius": 47.5 * mm});
            skCircle(sketch, "E30", {"center": v(0, 0) * mm, "radius": 67.5 * mm});
            skSolve(sketch);
        }
        {
            var Q0;
            Q0=makeQuery(id+"F39.imprint","IMPRINT",FACE,{"disambiguationData":[TD([[makeQuery(id+"F39.imprint","IMPRINT",EDGE,{"derivedFrom":sQuery(id+"F39.wireOp",EDGE,"E29")}),-1.0]])]});
            extrude(context, id + "F40", {"entities" : qUnion([Q0]), "operationType" : NewBodyOperationType.ADD, "endBound" : BoundingType.SYMMETRIC, "depth" : 6 * mm});
        }
        {
            var Q0;
            Q0=qCreatedBy(makeId("Right.planeOp"),FACE);
            var sketch = newSketch(context, id + "F41", { "sketchPlane" : qUnion([Q0])});
            skLineSegment(sketch, "E31", {"start": v(0, 27) * mm, "end": v(0, -23.5) * mm, "construction": true});
            skCircle(sketch, "E32", {"center": v(0, 0) * mm, "radius": 52 * mm});
            skCircle(sketch, "E33", {"center": v(0, 0) * mm, "radius": 85 * mm});
            skLineSegment(sketch, "E34", {"start": v(0, 85) * mm, "end": v(0, -85) * mm});
            skLineSegment(sketch, "E35", {"start": v(51.53, 7) * mm, "end": v(48.91, 3) * mm});
            skLineSegment(sketch, "E36", {"start": v(48.91, 3) * mm, "end": v(51.91, 3) * mm});
            skLineSegment(sketch, "E37", {"start": v(51.91, -3) * mm, "end": v(48.91, -3) * mm});
            skLineSegment(sketch, "E38", {"start": v(48.91, -3) * mm, "end": v(51.53, -7) * mm});
            skSolve(sketch);
        }
        {
            var Q0;
            {var subQ0=sQuery(id+"F41.wireOp",EDGE,"E34");var subQ1=sQuery(id+"F41.wireOp",EDGE,"E32");var subQ2=makeQuery(id+"F41.imprint","INTERSECT",VERTEX,{"disambiguationData":[OD(0.0)],"derivedFrom":[subQ1,subQ0]});Q0=makeQuery(id+"F41.imprint","IMPRINT",FACE,{"disambiguationData":[TD([[makeQuery(id+"F41.imprint","IMPRINT",EDGE,{"disambiguationData":[TD([[subQ2,-1.0]])],"derivedFrom":subQ1}),-1.0]])]});}
            var Q1;
            {var subQ0=sQuery(id+"F41.wireOp",EDGE,"E37");Q1=makeQuery(id+"F41.imprint","IMPRINT",FACE,{"disambiguationData":[TD([[makeQuery(id+"F41.imprint","IMPRINT",EDGE,{"derivedFrom":subQ0}),1.0]])]});}
            var Q2;
            {var subQ0=sQuery(id+"F41.wireOp",EDGE,"E35");Q2=makeQuery(id+"F41.imprint","IMPRINT",FACE,{"disambiguationData":[TD([[makeQuery(id+"F41.imprint","IMPRINT",EDGE,{"derivedFrom":subQ0}),1.0]])]});}
            var Q3;
            Q3=sQuery(id+"F41.wireOp",EDGE,"E31");
            revolve(context, id + "F42", {"operationType" : NewBodyOperationType.REMOVE, "entities" : qUnion([Q0, Q1, Q2]), "axis" : qUnion([Q3]), "revolveType" : RevolveType.FULL, "oppositeDirection" : true});
        }
        {
            var Q0;
            Q0=makeQuery(id+"F42.boolean.opBoolean","INTERSECT",EDGE,{"disambiguationData":[OD(5.0)],"derivedFrom":[makeQuery(id+"F20.boolean.opBoolean","MERGE",FACE,{"derivedFrom":[makeQuery(id+"F19.boolean.opBoolean","MERGE",FACE,{"derivedFrom":[makeQuery(id+"F18.boolean.opBoolean","MERGE",FACE,{"derivedFrom":[makeQuery(id+"F17.boolean.opBoolean","MERGE",FACE,{"derivedFrom":[makeQuery(id+"F16.boolean.opBoolean","MERGE",FACE,{"derivedFrom":[makeQuery(id+"F15.boolean.opBoolean","MERGE",FACE,{"derivedFrom":[makeQuery(id+"F14.boolean.opBoolean","MERGE",FACE,{"derivedFrom":[makeQuery(id+"F13.boolean.opBoolean","MERGE",FACE,{"derivedFrom":[makeQuery(id+"F12.boolean.opBoolean","MERGE",FACE,{"derivedFrom":[makeQuery(id+"F11.boolean.opBoolean","MERGE",FACE,{"derivedFrom":[makeQuery(id+"F10.boolean.opBoolean","MERGE",FACE,{"derivedFrom":[makeQuery(id+"F9.boolean.opBoolean","MERGE",FACE,{"derivedFrom":[makeQuery(id+"F8.boolean.opBoolean","MERGE",FACE,{"derivedFrom":[makeQuery(id+"F7.boolean.opBoolean","MERGE",FACE,{"derivedFrom":[makeQuery(id+"F6.boolean.opBoolean","MERGE",FACE,{"derivedFrom":[makeQuery(id+"F5.boolean.opBoolean","MERGE",FACE,{"derivedFrom":[makeQuery(id+"F1.opRevolve","SWEPT_FACE",FACE,{"disambiguationData":[OSD([sQuery(id+"F0.wireOp",EDGE,"E5")])]}),makeQuery(id+"F5.opLoft","CAP_FACE",FACE,{"disambiguationData":[OSD([makeQuery(id+"F4.imprint","IMPRINT",FACE,{"disambiguationData":[TD([[makeQuery(id+"F4.imprint","IMPRINT",EDGE,{"derivedFrom":sQuery(id+"F4.wireOp",EDGE,"E21")}),1.0]])]})])],"isStart":true})]}),makeQuery(id+"F6.opLoft","CAP_FACE",FACE,{"disambiguationData":[OSD([makeQuery(id+"F4.imprint","IMPRINT",FACE,{"disambiguationData":[TD([[makeQuery(id+"F4.imprint","IMPRINT",EDGE,{"derivedFrom":sQuery(id+"F4.wireOp",EDGE,"E26.15.0")}),1.0]])]})])],"isStart":true})]}),makeQuery(id+"F7.opLoft","CAP_FACE",FACE,{"disambiguationData":[OSD([makeQuery(id+"F4.imprint","IMPRINT",FACE,{"disambiguationData":[TD([[makeQuery(id+"F4.imprint","IMPRINT",EDGE,{"derivedFrom":sQuery(id+"F4.wireOp",EDGE,"E26.14.0")}),1.0]])]})])],"isStart":true})]}),makeQuery(id+"F8.opLoft","CAP_FACE",FACE,{"disambiguationData":[OSD([makeQuery(id+"F4.imprint","IMPRINT",FACE,{"disambiguationData":[TD([[makeQuery(id+"F4.imprint","IMPRINT",EDGE,{"derivedFrom":sQuery(id+"F4.wireOp",EDGE,"E26.13.0")}),1.0]])]})])],"isStart":true})]}),makeQuery(id+"F9.opLoft","CAP_FACE",FACE,{"disambiguationData":[OSD([makeQuery(id+"F4.imprint","IMPRINT",FACE,{"disambiguationData":[TD([[makeQuery(id+"F4.imprint","IMPRINT",EDGE,{"derivedFrom":sQuery(id+"F4.wireOp",EDGE,"E26.12.0")}),1.0]])]})])],"isStart":true})]}),makeQuery(id+"F10.opLoft","CAP_FACE",FACE,{"disambiguationData":[OSD([makeQuery(id+"F4.imprint","IMPRINT",FACE,{"disambiguationData":[TD([[makeQuery(id+"F4.imprint","IMPRINT",EDGE,{"derivedFrom":sQuery(id+"F4.wireOp",EDGE,"E26.11.0")}),1.0]])]})])],"isStart":true})]}),makeQuery(id+"F11.opLoft","CAP_FACE",FACE,{"disambiguationData":[OSD([makeQuery(id+"F4.imprint","IMPRINT",FACE,{"disambiguationData":[TD([[makeQuery(id+"F4.imprint","IMPRINT",EDGE,{"derivedFrom":sQuery(id+"F4.wireOp",EDGE,"E26.10.0")}),1.0]])]})])],"isStart":true})]}),makeQuery(id+"F12.opLoft","CAP_FACE",FACE,{"disambiguationData":[OSD([makeQuery(id+"F4.imprint","IMPRINT",FACE,{"disambiguationData":[TD([[makeQuery(id+"F4.imprint","IMPRINT",EDGE,{"derivedFrom":sQuery(id+"F4.wireOp",EDGE,"E26.9.0")}),1.0]])]})])],"isStart":true})]}),makeQuery(id+"F13.opLoft","CAP_FACE",FACE,{"disambiguationData":[OSD([makeQuery(id+"F4.imprint","IMPRINT",FACE,{"disambiguationData":[TD([[makeQuery(id+"F4.imprint","IMPRINT",EDGE,{"derivedFrom":sQuery(id+"F4.wireOp",EDGE,"E26.8.0")}),1.0]])]})])],"isStart":true})]}),makeQuery(id+"F14.opLoft","CAP_FACE",FACE,{"disambiguationData":[OSD([makeQuery(id+"F4.imprint","IMPRINT",FACE,{"disambiguationData":[TD([[makeQuery(id+"F4.imprint","IMPRINT",EDGE,{"derivedFrom":sQuery(id+"F4.wireOp",EDGE,"E26.7.0")}),1.0]])]})])],"isStart":true})]}),makeQuery(id+"F15.opLoft","CAP_FACE",FACE,{"disambiguationData":[OSD([makeQuery(id+"F4.imprint","IMPRINT",FACE,{"disambiguationData":[TD([[makeQuery(id+"F4.imprint","IMPRINT",EDGE,{"derivedFrom":sQuery(id+"F4.wireOp",EDGE,"E26.6.0")}),1.0]])]})])],"isStart":true})]}),makeQuery(id+"F16.opLoft","CAP_FACE",FACE,{"disambiguationData":[OSD([makeQuery(id+"F4.imprint","IMPRINT",FACE,{"disambiguationData":[TD([[makeQuery(id+"F4.imprint","IMPRINT",EDGE,{"derivedFrom":sQuery(id+"F4.wireOp",EDGE,"E26.5.0")}),1.0]])]})])],"isStart":true})]}),makeQuery(id+"F17.opLoft","CAP_FACE",FACE,{"disambiguationData":[OSD([makeQuery(id+"F4.imprint","IMPRINT",FACE,{"disambiguationData":[TD([[makeQuery(id+"F4.imprint","IMPRINT",EDGE,{"derivedFrom":sQuery(id+"F4.wireOp",EDGE,"E26.4.0")}),1.0]])]})])],"isStart":true})]}),makeQuery(id+"F18.opLoft","CAP_FACE",FACE,{"disambiguationData":[OSD([makeQuery(id+"F4.imprint","IMPRINT",FACE,{"disambiguationData":[TD([[makeQuery(id+"F4.imprint","IMPRINT",EDGE,{"derivedFrom":sQuery(id+"F4.wireOp",EDGE,"E26.3.0")}),1.0]])]})])],"isStart":true})]}),makeQuery(id+"F19.opLoft","CAP_FACE",FACE,{"disambiguationData":[OSD([makeQuery(id+"F4.imprint","IMPRINT",FACE,{"disambiguationData":[TD([[makeQuery(id+"F4.imprint","IMPRINT",EDGE,{"derivedFrom":sQuery(id+"F4.wireOp",EDGE,"E26.2.0")}),1.0]])]})])],"isStart":true})]}),makeQuery(id+"F20.opLoft","CAP_FACE",FACE,{"disambiguationData":[OSD([makeQuery(id+"F4.imprint","IMPRINT",FACE,{"disambiguationData":[TD([[makeQuery(id+"F4.imprint","IMPRINT",EDGE,{"derivedFrom":sQuery(id+"F4.wireOp",EDGE,"E26.1.0")}),1.0]])]})])],"isStart":true})]}),makeQuery(id+"F42.opRevolve","SWEPT_FACE",FACE,{"disambiguationData":[OSD([sQuery(id+"F41.wireOp",EDGE,"E32")])]})]});
            var Q1;
            Q1=makeQuery(id+"F42.boolean.opBoolean","INTERSECT",EDGE,{"disambiguationData":[OD(4.0)],"derivedFrom":[makeQuery(id+"F20.boolean.opBoolean","MERGE",FACE,{"derivedFrom":[makeQuery(id+"F19.boolean.opBoolean","MERGE",FACE,{"derivedFrom":[makeQuery(id+"F18.boolean.opBoolean","MERGE",FACE,{"derivedFrom":[makeQuery(id+"F17.boolean.opBoolean","MERGE",FACE,{"derivedFrom":[makeQuery(id+"F16.boolean.opBoolean","MERGE",FACE,{"derivedFrom":[makeQuery(id+"F15.boolean.opBoolean","MERGE",FACE,{"derivedFrom":[makeQuery(id+"F14.boolean.opBoolean","MERGE",FACE,{"derivedFrom":[makeQuery(id+"F13.boolean.opBoolean","MERGE",FACE,{"derivedFrom":[makeQuery(id+"F12.boolean.opBoolean","MERGE",FACE,{"derivedFrom":[makeQuery(id+"F11.boolean.opBoolean","MERGE",FACE,{"derivedFrom":[makeQuery(id+"F10.boolean.opBoolean","MERGE",FACE,{"derivedFrom":[makeQuery(id+"F9.boolean.opBoolean","MERGE",FACE,{"derivedFrom":[makeQuery(id+"F8.boolean.opBoolean","MERGE",FACE,{"derivedFrom":[makeQuery(id+"F7.boolean.opBoolean","MERGE",FACE,{"derivedFrom":[makeQuery(id+"F6.boolean.opBoolean","MERGE",FACE,{"derivedFrom":[makeQuery(id+"F5.boolean.opBoolean","MERGE",FACE,{"derivedFrom":[makeQuery(id+"F1.opRevolve","SWEPT_FACE",FACE,{"disambiguationData":[OSD([sQuery(id+"F0.wireOp",EDGE,"E5")])]}),makeQuery(id+"F5.opLoft","CAP_FACE",FACE,{"disambiguationData":[OSD([makeQuery(id+"F4.imprint","IMPRINT",FACE,{"disambiguationData":[TD([[makeQuery(id+"F4.imprint","IMPRINT",EDGE,{"derivedFrom":sQuery(id+"F4.wireOp",EDGE,"E21")}),1.0]])]})])],"isStart":true})]}),makeQuery(id+"F6.opLoft","CAP_FACE",FACE,{"disambiguationData":[OSD([makeQuery(id+"F4.imprint","IMPRINT",FACE,{"disambiguationData":[TD([[makeQuery(id+"F4.imprint","IMPRINT",EDGE,{"derivedFrom":sQuery(id+"F4.wireOp",EDGE,"E26.15.0")}),1.0]])]})])],"isStart":true})]}),makeQuery(id+"F7.opLoft","CAP_FACE",FACE,{"disambiguationData":[OSD([makeQuery(id+"F4.imprint","IMPRINT",FACE,{"disambiguationData":[TD([[makeQuery(id+"F4.imprint","IMPRINT",EDGE,{"derivedFrom":sQuery(id+"F4.wireOp",EDGE,"E26.14.0")}),1.0]])]})])],"isStart":true})]}),makeQuery(id+"F8.opLoft","CAP_FACE",FACE,{"disambiguationData":[OSD([makeQuery(id+"F4.imprint","IMPRINT",FACE,{"disambiguationData":[TD([[makeQuery(id+"F4.imprint","IMPRINT",EDGE,{"derivedFrom":sQuery(id+"F4.wireOp",EDGE,"E26.13.0")}),1.0]])]})])],"isStart":true})]}),makeQuery(id+"F9.opLoft","CAP_FACE",FACE,{"disambiguationData":[OSD([makeQuery(id+"F4.imprint","IMPRINT",FACE,{"disambiguationData":[TD([[makeQuery(id+"F4.imprint","IMPRINT",EDGE,{"derivedFrom":sQuery(id+"F4.wireOp",EDGE,"E26.12.0")}),1.0]])]})])],"isStart":true})]}),makeQuery(id+"F10.opLoft","CAP_FACE",FACE,{"disambiguationData":[OSD([makeQuery(id+"F4.imprint","IMPRINT",FACE,{"disambiguationData":[TD([[makeQuery(id+"F4.imprint","IMPRINT",EDGE,{"derivedFrom":sQuery(id+"F4.wireOp",EDGE,"E26.11.0")}),1.0]])]})])],"isStart":true})]}),makeQuery(id+"F11.opLoft","CAP_FACE",FACE,{"disambiguationData":[OSD([makeQuery(id+"F4.imprint","IMPRINT",FACE,{"disambiguationData":[TD([[makeQuery(id+"F4.imprint","IMPRINT",EDGE,{"derivedFrom":sQuery(id+"F4.wireOp",EDGE,"E26.10.0")}),1.0]])]})])],"isStart":true})]}),makeQuery(id+"F12.opLoft","CAP_FACE",FACE,{"disambiguationData":[OSD([makeQuery(id+"F4.imprint","IMPRINT",FACE,{"disambiguationData":[TD([[makeQuery(id+"F4.imprint","IMPRINT",EDGE,{"derivedFrom":sQuery(id+"F4.wireOp",EDGE,"E26.9.0")}),1.0]])]})])],"isStart":true})]}),makeQuery(id+"F13.opLoft","CAP_FACE",FACE,{"disambiguationData":[OSD([makeQuery(id+"F4.imprint","IMPRINT",FACE,{"disambiguationData":[TD([[makeQuery(id+"F4.imprint","IMPRINT",EDGE,{"derivedFrom":sQuery(id+"F4.wireOp",EDGE,"E26.8.0")}),1.0]])]})])],"isStart":true})]}),makeQuery(id+"F14.opLoft","CAP_FACE",FACE,{"disambiguationData":[OSD([makeQuery(id+"F4.imprint","IMPRINT",FACE,{"disambiguationData":[TD([[makeQuery(id+"F4.imprint","IMPRINT",EDGE,{"derivedFrom":sQuery(id+"F4.wireOp",EDGE,"E26.7.0")}),1.0]])]})])],"isStart":true})]}),makeQuery(id+"F15.opLoft","CAP_FACE",FACE,{"disambiguationData":[OSD([makeQuery(id+"F4.imprint","IMPRINT",FACE,{"disambiguationData":[TD([[makeQuery(id+"F4.imprint","IMPRINT",EDGE,{"derivedFrom":sQuery(id+"F4.wireOp",EDGE,"E26.6.0")}),1.0]])]})])],"isStart":true})]}),makeQuery(id+"F16.opLoft","CAP_FACE",FACE,{"disambiguationData":[OSD([makeQuery(id+"F4.imprint","IMPRINT",FACE,{"disambiguationData":[TD([[makeQuery(id+"F4.imprint","IMPRINT",EDGE,{"derivedFrom":sQuery(id+"F4.wireOp",EDGE,"E26.5.0")}),1.0]])]})])],"isStart":true})]}),makeQuery(id+"F17.opLoft","CAP_FACE",FACE,{"disambiguationData":[OSD([makeQuery(id+"F4.imprint","IMPRINT",FACE,{"disambiguationData":[TD([[makeQuery(id+"F4.imprint","IMPRINT",EDGE,{"derivedFrom":sQuery(id+"F4.wireOp",EDGE,"E26.4.0")}),1.0]])]})])],"isStart":true})]}),makeQuery(id+"F18.opLoft","CAP_FACE",FACE,{"disambiguationData":[OSD([makeQuery(id+"F4.imprint","IMPRINT",FACE,{"disambiguationData":[TD([[makeQuery(id+"F4.imprint","IMPRINT",EDGE,{"derivedFrom":sQuery(id+"F4.wireOp",EDGE,"E26.3.0")}),1.0]])]})])],"isStart":true})]}),makeQuery(id+"F19.opLoft","CAP_FACE",FACE,{"disambiguationData":[OSD([makeQuery(id+"F4.imprint","IMPRINT",FACE,{"disambiguationData":[TD([[makeQuery(id+"F4.imprint","IMPRINT",EDGE,{"derivedFrom":sQuery(id+"F4.wireOp",EDGE,"E26.2.0")}),1.0]])]})])],"isStart":true})]}),makeQuery(id+"F20.opLoft","CAP_FACE",FACE,{"disambiguationData":[OSD([makeQuery(id+"F4.imprint","IMPRINT",FACE,{"disambiguationData":[TD([[makeQuery(id+"F4.imprint","IMPRINT",EDGE,{"derivedFrom":sQuery(id+"F4.wireOp",EDGE,"E26.1.0")}),1.0]])]})])],"isStart":true})]}),makeQuery(id+"F42.opRevolve","SWEPT_FACE",FACE,{"disambiguationData":[OSD([sQuery(id+"F41.wireOp",EDGE,"E32")])]})]});
            var Q2;
            Q2=makeQuery(id+"F42.boolean.opBoolean","INTERSECT",EDGE,{"disambiguationData":[OD(3.0)],"derivedFrom":[makeQuery(id+"F20.boolean.opBoolean","MERGE",FACE,{"derivedFrom":[makeQuery(id+"F19.boolean.opBoolean","MERGE",FACE,{"derivedFrom":[makeQuery(id+"F18.boolean.opBoolean","MERGE",FACE,{"derivedFrom":[makeQuery(id+"F17.boolean.opBoolean","MERGE",FACE,{"derivedFrom":[makeQuery(id+"F16.boolean.opBoolean","MERGE",FACE,{"derivedFrom":[makeQuery(id+"F15.boolean.opBoolean","MERGE",FACE,{"derivedFrom":[makeQuery(id+"F14.boolean.opBoolean","MERGE",FACE,{"derivedFrom":[makeQuery(id+"F13.boolean.opBoolean","MERGE",FACE,{"derivedFrom":[makeQuery(id+"F12.boolean.opBoolean","MERGE",FACE,{"derivedFrom":[makeQuery(id+"F11.boolean.opBoolean","MERGE",FACE,{"derivedFrom":[makeQuery(id+"F10.boolean.opBoolean","MERGE",FACE,{"derivedFrom":[makeQuery(id+"F9.boolean.opBoolean","MERGE",FACE,{"derivedFrom":[makeQuery(id+"F8.boolean.opBoolean","MERGE",FACE,{"derivedFrom":[makeQuery(id+"F7.boolean.opBoolean","MERGE",FACE,{"derivedFrom":[makeQuery(id+"F6.boolean.opBoolean","MERGE",FACE,{"derivedFrom":[makeQuery(id+"F5.boolean.opBoolean","MERGE",FACE,{"derivedFrom":[makeQuery(id+"F1.opRevolve","SWEPT_FACE",FACE,{"disambiguationData":[OSD([sQuery(id+"F0.wireOp",EDGE,"E5")])]}),makeQuery(id+"F5.opLoft","CAP_FACE",FACE,{"disambiguationData":[OSD([makeQuery(id+"F4.imprint","IMPRINT",FACE,{"disambiguationData":[TD([[makeQuery(id+"F4.imprint","IMPRINT",EDGE,{"derivedFrom":sQuery(id+"F4.wireOp",EDGE,"E21")}),1.0]])]})])],"isStart":true})]}),makeQuery(id+"F6.opLoft","CAP_FACE",FACE,{"disambiguationData":[OSD([makeQuery(id+"F4.imprint","IMPRINT",FACE,{"disambiguationData":[TD([[makeQuery(id+"F4.imprint","IMPRINT",EDGE,{"derivedFrom":sQuery(id+"F4.wireOp",EDGE,"E26.15.0")}),1.0]])]})])],"isStart":true})]}),makeQuery(id+"F7.opLoft","CAP_FACE",FACE,{"disambiguationData":[OSD([makeQuery(id+"F4.imprint","IMPRINT",FACE,{"disambiguationData":[TD([[makeQuery(id+"F4.imprint","IMPRINT",EDGE,{"derivedFrom":sQuery(id+"F4.wireOp",EDGE,"E26.14.0")}),1.0]])]})])],"isStart":true})]}),makeQuery(id+"F8.opLoft","CAP_FACE",FACE,{"disambiguationData":[OSD([makeQuery(id+"F4.imprint","IMPRINT",FACE,{"disambiguationData":[TD([[makeQuery(id+"F4.imprint","IMPRINT",EDGE,{"derivedFrom":sQuery(id+"F4.wireOp",EDGE,"E26.13.0")}),1.0]])]})])],"isStart":true})]}),makeQuery(id+"F9.opLoft","CAP_FACE",FACE,{"disambiguationData":[OSD([makeQuery(id+"F4.imprint","IMPRINT",FACE,{"disambiguationData":[TD([[makeQuery(id+"F4.imprint","IMPRINT",EDGE,{"derivedFrom":sQuery(id+"F4.wireOp",EDGE,"E26.12.0")}),1.0]])]})])],"isStart":true})]}),makeQuery(id+"F10.opLoft","CAP_FACE",FACE,{"disambiguationData":[OSD([makeQuery(id+"F4.imprint","IMPRINT",FACE,{"disambiguationData":[TD([[makeQuery(id+"F4.imprint","IMPRINT",EDGE,{"derivedFrom":sQuery(id+"F4.wireOp",EDGE,"E26.11.0")}),1.0]])]})])],"isStart":true})]}),makeQuery(id+"F11.opLoft","CAP_FACE",FACE,{"disambiguationData":[OSD([makeQuery(id+"F4.imprint","IMPRINT",FACE,{"disambiguationData":[TD([[makeQuery(id+"F4.imprint","IMPRINT",EDGE,{"derivedFrom":sQuery(id+"F4.wireOp",EDGE,"E26.10.0")}),1.0]])]})])],"isStart":true})]}),makeQuery(id+"F12.opLoft","CAP_FACE",FACE,{"disambiguationData":[OSD([makeQuery(id+"F4.imprint","IMPRINT",FACE,{"disambiguationData":[TD([[makeQuery(id+"F4.imprint","IMPRINT",EDGE,{"derivedFrom":sQuery(id+"F4.wireOp",EDGE,"E26.9.0")}),1.0]])]})])],"isStart":true})]}),makeQuery(id+"F13.opLoft","CAP_FACE",FACE,{"disambiguationData":[OSD([makeQuery(id+"F4.imprint","IMPRINT",FACE,{"disambiguationData":[TD([[makeQuery(id+"F4.imprint","IMPRINT",EDGE,{"derivedFrom":sQuery(id+"F4.wireOp",EDGE,"E26.8.0")}),1.0]])]})])],"isStart":true})]}),makeQuery(id+"F14.opLoft","CAP_FACE",FACE,{"disambiguationData":[OSD([makeQuery(id+"F4.imprint","IMPRINT",FACE,{"disambiguationData":[TD([[makeQuery(id+"F4.imprint","IMPRINT",EDGE,{"derivedFrom":sQuery(id+"F4.wireOp",EDGE,"E26.7.0")}),1.0]])]})])],"isStart":true})]}),makeQuery(id+"F15.opLoft","CAP_FACE",FACE,{"disambiguationData":[OSD([makeQuery(id+"F4.imprint","IMPRINT",FACE,{"disambiguationData":[TD([[makeQuery(id+"F4.imprint","IMPRINT",EDGE,{"derivedFrom":sQuery(id+"F4.wireOp",EDGE,"E26.6.0")}),1.0]])]})])],"isStart":true})]}),makeQuery(id+"F16.opLoft","CAP_FACE",FACE,{"disambiguationData":[OSD([makeQuery(id+"F4.imprint","IMPRINT",FACE,{"disambiguationData":[TD([[makeQuery(id+"F4.imprint","IMPRINT",EDGE,{"derivedFrom":sQuery(id+"F4.wireOp",EDGE,"E26.5.0")}),1.0]])]})])],"isStart":true})]}),makeQuery(id+"F17.opLoft","CAP_FACE",FACE,{"disambiguationData":[OSD([makeQuery(id+"F4.imprint","IMPRINT",FACE,{"disambiguationData":[TD([[makeQuery(id+"F4.imprint","IMPRINT",EDGE,{"derivedFrom":sQuery(id+"F4.wireOp",EDGE,"E26.4.0")}),1.0]])]})])],"isStart":true})]}),makeQuery(id+"F18.opLoft","CAP_FACE",FACE,{"disambiguationData":[OSD([makeQuery(id+"F4.imprint","IMPRINT",FACE,{"disambiguationData":[TD([[makeQuery(id+"F4.imprint","IMPRINT",EDGE,{"derivedFrom":sQuery(id+"F4.wireOp",EDGE,"E26.3.0")}),1.0]])]})])],"isStart":true})]}),makeQuery(id+"F19.opLoft","CAP_FACE",FACE,{"disambiguationData":[OSD([makeQuery(id+"F4.imprint","IMPRINT",FACE,{"disambiguationData":[TD([[makeQuery(id+"F4.imprint","IMPRINT",EDGE,{"derivedFrom":sQuery(id+"F4.wireOp",EDGE,"E26.2.0")}),1.0]])]})])],"isStart":true})]}),makeQuery(id+"F20.opLoft","CAP_FACE",FACE,{"disambiguationData":[OSD([makeQuery(id+"F4.imprint","IMPRINT",FACE,{"disambiguationData":[TD([[makeQuery(id+"F4.imprint","IMPRINT",EDGE,{"derivedFrom":sQuery(id+"F4.wireOp",EDGE,"E26.1.0")}),1.0]])]})])],"isStart":true})]}),makeQuery(id+"F42.opRevolve","SWEPT_FACE",FACE,{"disambiguationData":[OSD([sQuery(id+"F41.wireOp",EDGE,"E32")])]})]});
            var Q3;
            Q3=makeQuery(id+"F42.boolean.opBoolean","INTERSECT",EDGE,{"disambiguationData":[OD(2.0)],"derivedFrom":[makeQuery(id+"F20.boolean.opBoolean","MERGE",FACE,{"derivedFrom":[makeQuery(id+"F19.boolean.opBoolean","MERGE",FACE,{"derivedFrom":[makeQuery(id+"F18.boolean.opBoolean","MERGE",FACE,{"derivedFrom":[makeQuery(id+"F17.boolean.opBoolean","MERGE",FACE,{"derivedFrom":[makeQuery(id+"F16.boolean.opBoolean","MERGE",FACE,{"derivedFrom":[makeQuery(id+"F15.boolean.opBoolean","MERGE",FACE,{"derivedFrom":[makeQuery(id+"F14.boolean.opBoolean","MERGE",FACE,{"derivedFrom":[makeQuery(id+"F13.boolean.opBoolean","MERGE",FACE,{"derivedFrom":[makeQuery(id+"F12.boolean.opBoolean","MERGE",FACE,{"derivedFrom":[makeQuery(id+"F11.boolean.opBoolean","MERGE",FACE,{"derivedFrom":[makeQuery(id+"F10.boolean.opBoolean","MERGE",FACE,{"derivedFrom":[makeQuery(id+"F9.boolean.opBoolean","MERGE",FACE,{"derivedFrom":[makeQuery(id+"F8.boolean.opBoolean","MERGE",FACE,{"derivedFrom":[makeQuery(id+"F7.boolean.opBoolean","MERGE",FACE,{"derivedFrom":[makeQuery(id+"F6.boolean.opBoolean","MERGE",FACE,{"derivedFrom":[makeQuery(id+"F5.boolean.opBoolean","MERGE",FACE,{"derivedFrom":[makeQuery(id+"F1.opRevolve","SWEPT_FACE",FACE,{"disambiguationData":[OSD([sQuery(id+"F0.wireOp",EDGE,"E5")])]}),makeQuery(id+"F5.opLoft","CAP_FACE",FACE,{"disambiguationData":[OSD([makeQuery(id+"F4.imprint","IMPRINT",FACE,{"disambiguationData":[TD([[makeQuery(id+"F4.imprint","IMPRINT",EDGE,{"derivedFrom":sQuery(id+"F4.wireOp",EDGE,"E21")}),1.0]])]})])],"isStart":true})]}),makeQuery(id+"F6.opLoft","CAP_FACE",FACE,{"disambiguationData":[OSD([makeQuery(id+"F4.imprint","IMPRINT",FACE,{"disambiguationData":[TD([[makeQuery(id+"F4.imprint","IMPRINT",EDGE,{"derivedFrom":sQuery(id+"F4.wireOp",EDGE,"E26.15.0")}),1.0]])]})])],"isStart":true})]}),makeQuery(id+"F7.opLoft","CAP_FACE",FACE,{"disambiguationData":[OSD([makeQuery(id+"F4.imprint","IMPRINT",FACE,{"disambiguationData":[TD([[makeQuery(id+"F4.imprint","IMPRINT",EDGE,{"derivedFrom":sQuery(id+"F4.wireOp",EDGE,"E26.14.0")}),1.0]])]})])],"isStart":true})]}),makeQuery(id+"F8.opLoft","CAP_FACE",FACE,{"disambiguationData":[OSD([makeQuery(id+"F4.imprint","IMPRINT",FACE,{"disambiguationData":[TD([[makeQuery(id+"F4.imprint","IMPRINT",EDGE,{"derivedFrom":sQuery(id+"F4.wireOp",EDGE,"E26.13.0")}),1.0]])]})])],"isStart":true})]}),makeQuery(id+"F9.opLoft","CAP_FACE",FACE,{"disambiguationData":[OSD([makeQuery(id+"F4.imprint","IMPRINT",FACE,{"disambiguationData":[TD([[makeQuery(id+"F4.imprint","IMPRINT",EDGE,{"derivedFrom":sQuery(id+"F4.wireOp",EDGE,"E26.12.0")}),1.0]])]})])],"isStart":true})]}),makeQuery(id+"F10.opLoft","CAP_FACE",FACE,{"disambiguationData":[OSD([makeQuery(id+"F4.imprint","IMPRINT",FACE,{"disambiguationData":[TD([[makeQuery(id+"F4.imprint","IMPRINT",EDGE,{"derivedFrom":sQuery(id+"F4.wireOp",EDGE,"E26.11.0")}),1.0]])]})])],"isStart":true})]}),makeQuery(id+"F11.opLoft","CAP_FACE",FACE,{"disambiguationData":[OSD([makeQuery(id+"F4.imprint","IMPRINT",FACE,{"disambiguationData":[TD([[makeQuery(id+"F4.imprint","IMPRINT",EDGE,{"derivedFrom":sQuery(id+"F4.wireOp",EDGE,"E26.10.0")}),1.0]])]})])],"isStart":true})]}),makeQuery(id+"F12.opLoft","CAP_FACE",FACE,{"disambiguationData":[OSD([makeQuery(id+"F4.imprint","IMPRINT",FACE,{"disambiguationData":[TD([[makeQuery(id+"F4.imprint","IMPRINT",EDGE,{"derivedFrom":sQuery(id+"F4.wireOp",EDGE,"E26.9.0")}),1.0]])]})])],"isStart":true})]}),makeQuery(id+"F13.opLoft","CAP_FACE",FACE,{"disambiguationData":[OSD([makeQuery(id+"F4.imprint","IMPRINT",FACE,{"disambiguationData":[TD([[makeQuery(id+"F4.imprint","IMPRINT",EDGE,{"derivedFrom":sQuery(id+"F4.wireOp",EDGE,"E26.8.0")}),1.0]])]})])],"isStart":true})]}),makeQuery(id+"F14.opLoft","CAP_FACE",FACE,{"disambiguationData":[OSD([makeQuery(id+"F4.imprint","IMPRINT",FACE,{"disambiguationData":[TD([[makeQuery(id+"F4.imprint","IMPRINT",EDGE,{"derivedFrom":sQuery(id+"F4.wireOp",EDGE,"E26.7.0")}),1.0]])]})])],"isStart":true})]}),makeQuery(id+"F15.opLoft","CAP_FACE",FACE,{"disambiguationData":[OSD([makeQuery(id+"F4.imprint","IMPRINT",FACE,{"disambiguationData":[TD([[makeQuery(id+"F4.imprint","IMPRINT",EDGE,{"derivedFrom":sQuery(id+"F4.wireOp",EDGE,"E26.6.0")}),1.0]])]})])],"isStart":true})]}),makeQuery(id+"F16.opLoft","CAP_FACE",FACE,{"disambiguationData":[OSD([makeQuery(id+"F4.imprint","IMPRINT",FACE,{"disambiguationData":[TD([[makeQuery(id+"F4.imprint","IMPRINT",EDGE,{"derivedFrom":sQuery(id+"F4.wireOp",EDGE,"E26.5.0")}),1.0]])]})])],"isStart":true})]}),makeQuery(id+"F17.opLoft","CAP_FACE",FACE,{"disambiguationData":[OSD([makeQuery(id+"F4.imprint","IMPRINT",FACE,{"disambiguationData":[TD([[makeQuery(id+"F4.imprint","IMPRINT",EDGE,{"derivedFrom":sQuery(id+"F4.wireOp",EDGE,"E26.4.0")}),1.0]])]})])],"isStart":true})]}),makeQuery(id+"F18.opLoft","CAP_FACE",FACE,{"disambiguationData":[OSD([makeQuery(id+"F4.imprint","IMPRINT",FACE,{"disambiguationData":[TD([[makeQuery(id+"F4.imprint","IMPRINT",EDGE,{"derivedFrom":sQuery(id+"F4.wireOp",EDGE,"E26.3.0")}),1.0]])]})])],"isStart":true})]}),makeQuery(id+"F19.opLoft","CAP_FACE",FACE,{"disambiguationData":[OSD([makeQuery(id+"F4.imprint","IMPRINT",FACE,{"disambiguationData":[TD([[makeQuery(id+"F4.imprint","IMPRINT",EDGE,{"derivedFrom":sQuery(id+"F4.wireOp",EDGE,"E26.2.0")}),1.0]])]})])],"isStart":true})]}),makeQuery(id+"F20.opLoft","CAP_FACE",FACE,{"disambiguationData":[OSD([makeQuery(id+"F4.imprint","IMPRINT",FACE,{"disambiguationData":[TD([[makeQuery(id+"F4.imprint","IMPRINT",EDGE,{"derivedFrom":sQuery(id+"F4.wireOp",EDGE,"E26.1.0")}),1.0]])]})])],"isStart":true})]}),makeQuery(id+"F42.opRevolve","SWEPT_FACE",FACE,{"disambiguationData":[OSD([sQuery(id+"F41.wireOp",EDGE,"E32")])]})]});
            var Q4;
            Q4=makeQuery(id+"F42.boolean.opBoolean","INTERSECT",EDGE,{"disambiguationData":[OD(1.0)],"derivedFrom":[makeQuery(id+"F20.boolean.opBoolean","MERGE",FACE,{"derivedFrom":[makeQuery(id+"F19.boolean.opBoolean","MERGE",FACE,{"derivedFrom":[makeQuery(id+"F18.boolean.opBoolean","MERGE",FACE,{"derivedFrom":[makeQuery(id+"F17.boolean.opBoolean","MERGE",FACE,{"derivedFrom":[makeQuery(id+"F16.boolean.opBoolean","MERGE",FACE,{"derivedFrom":[makeQuery(id+"F15.boolean.opBoolean","MERGE",FACE,{"derivedFrom":[makeQuery(id+"F14.boolean.opBoolean","MERGE",FACE,{"derivedFrom":[makeQuery(id+"F13.boolean.opBoolean","MERGE",FACE,{"derivedFrom":[makeQuery(id+"F12.boolean.opBoolean","MERGE",FACE,{"derivedFrom":[makeQuery(id+"F11.boolean.opBoolean","MERGE",FACE,{"derivedFrom":[makeQuery(id+"F10.boolean.opBoolean","MERGE",FACE,{"derivedFrom":[makeQuery(id+"F9.boolean.opBoolean","MERGE",FACE,{"derivedFrom":[makeQuery(id+"F8.boolean.opBoolean","MERGE",FACE,{"derivedFrom":[makeQuery(id+"F7.boolean.opBoolean","MERGE",FACE,{"derivedFrom":[makeQuery(id+"F6.boolean.opBoolean","MERGE",FACE,{"derivedFrom":[makeQuery(id+"F5.boolean.opBoolean","MERGE",FACE,{"derivedFrom":[makeQuery(id+"F1.opRevolve","SWEPT_FACE",FACE,{"disambiguationData":[OSD([sQuery(id+"F0.wireOp",EDGE,"E5")])]}),makeQuery(id+"F5.opLoft","CAP_FACE",FACE,{"disambiguationData":[OSD([makeQuery(id+"F4.imprint","IMPRINT",FACE,{"disambiguationData":[TD([[makeQuery(id+"F4.imprint","IMPRINT",EDGE,{"derivedFrom":sQuery(id+"F4.wireOp",EDGE,"E21")}),1.0]])]})])],"isStart":true})]}),makeQuery(id+"F6.opLoft","CAP_FACE",FACE,{"disambiguationData":[OSD([makeQuery(id+"F4.imprint","IMPRINT",FACE,{"disambiguationData":[TD([[makeQuery(id+"F4.imprint","IMPRINT",EDGE,{"derivedFrom":sQuery(id+"F4.wireOp",EDGE,"E26.15.0")}),1.0]])]})])],"isStart":true})]}),makeQuery(id+"F7.opLoft","CAP_FACE",FACE,{"disambiguationData":[OSD([makeQuery(id+"F4.imprint","IMPRINT",FACE,{"disambiguationData":[TD([[makeQuery(id+"F4.imprint","IMPRINT",EDGE,{"derivedFrom":sQuery(id+"F4.wireOp",EDGE,"E26.14.0")}),1.0]])]})])],"isStart":true})]}),makeQuery(id+"F8.opLoft","CAP_FACE",FACE,{"disambiguationData":[OSD([makeQuery(id+"F4.imprint","IMPRINT",FACE,{"disambiguationData":[TD([[makeQuery(id+"F4.imprint","IMPRINT",EDGE,{"derivedFrom":sQuery(id+"F4.wireOp",EDGE,"E26.13.0")}),1.0]])]})])],"isStart":true})]}),makeQuery(id+"F9.opLoft","CAP_FACE",FACE,{"disambiguationData":[OSD([makeQuery(id+"F4.imprint","IMPRINT",FACE,{"disambiguationData":[TD([[makeQuery(id+"F4.imprint","IMPRINT",EDGE,{"derivedFrom":sQuery(id+"F4.wireOp",EDGE,"E26.12.0")}),1.0]])]})])],"isStart":true})]}),makeQuery(id+"F10.opLoft","CAP_FACE",FACE,{"disambiguationData":[OSD([makeQuery(id+"F4.imprint","IMPRINT",FACE,{"disambiguationData":[TD([[makeQuery(id+"F4.imprint","IMPRINT",EDGE,{"derivedFrom":sQuery(id+"F4.wireOp",EDGE,"E26.11.0")}),1.0]])]})])],"isStart":true})]}),makeQuery(id+"F11.opLoft","CAP_FACE",FACE,{"disambiguationData":[OSD([makeQuery(id+"F4.imprint","IMPRINT",FACE,{"disambiguationData":[TD([[makeQuery(id+"F4.imprint","IMPRINT",EDGE,{"derivedFrom":sQuery(id+"F4.wireOp",EDGE,"E26.10.0")}),1.0]])]})])],"isStart":true})]}),makeQuery(id+"F12.opLoft","CAP_FACE",FACE,{"disambiguationData":[OSD([makeQuery(id+"F4.imprint","IMPRINT",FACE,{"disambiguationData":[TD([[makeQuery(id+"F4.imprint","IMPRINT",EDGE,{"derivedFrom":sQuery(id+"F4.wireOp",EDGE,"E26.9.0")}),1.0]])]})])],"isStart":true})]}),makeQuery(id+"F13.opLoft","CAP_FACE",FACE,{"disambiguationData":[OSD([makeQuery(id+"F4.imprint","IMPRINT",FACE,{"disambiguationData":[TD([[makeQuery(id+"F4.imprint","IMPRINT",EDGE,{"derivedFrom":sQuery(id+"F4.wireOp",EDGE,"E26.8.0")}),1.0]])]})])],"isStart":true})]}),makeQuery(id+"F14.opLoft","CAP_FACE",FACE,{"disambiguationData":[OSD([makeQuery(id+"F4.imprint","IMPRINT",FACE,{"disambiguationData":[TD([[makeQuery(id+"F4.imprint","IMPRINT",EDGE,{"derivedFrom":sQuery(id+"F4.wireOp",EDGE,"E26.7.0")}),1.0]])]})])],"isStart":true})]}),makeQuery(id+"F15.opLoft","CAP_FACE",FACE,{"disambiguationData":[OSD([makeQuery(id+"F4.imprint","IMPRINT",FACE,{"disambiguationData":[TD([[makeQuery(id+"F4.imprint","IMPRINT",EDGE,{"derivedFrom":sQuery(id+"F4.wireOp",EDGE,"E26.6.0")}),1.0]])]})])],"isStart":true})]}),makeQuery(id+"F16.opLoft","CAP_FACE",FACE,{"disambiguationData":[OSD([makeQuery(id+"F4.imprint","IMPRINT",FACE,{"disambiguationData":[TD([[makeQuery(id+"F4.imprint","IMPRINT",EDGE,{"derivedFrom":sQuery(id+"F4.wireOp",EDGE,"E26.5.0")}),1.0]])]})])],"isStart":true})]}),makeQuery(id+"F17.opLoft","CAP_FACE",FACE,{"disambiguationData":[OSD([makeQuery(id+"F4.imprint","IMPRINT",FACE,{"disambiguationData":[TD([[makeQuery(id+"F4.imprint","IMPRINT",EDGE,{"derivedFrom":sQuery(id+"F4.wireOp",EDGE,"E26.4.0")}),1.0]])]})])],"isStart":true})]}),makeQuery(id+"F18.opLoft","CAP_FACE",FACE,{"disambiguationData":[OSD([makeQuery(id+"F4.imprint","IMPRINT",FACE,{"disambiguationData":[TD([[makeQuery(id+"F4.imprint","IMPRINT",EDGE,{"derivedFrom":sQuery(id+"F4.wireOp",EDGE,"E26.3.0")}),1.0]])]})])],"isStart":true})]}),makeQuery(id+"F19.opLoft","CAP_FACE",FACE,{"disambiguationData":[OSD([makeQuery(id+"F4.imprint","IMPRINT",FACE,{"disambiguationData":[TD([[makeQuery(id+"F4.imprint","IMPRINT",EDGE,{"derivedFrom":sQuery(id+"F4.wireOp",EDGE,"E26.2.0")}),1.0]])]})])],"isStart":true})]}),makeQuery(id+"F20.opLoft","CAP_FACE",FACE,{"disambiguationData":[OSD([makeQuery(id+"F4.imprint","IMPRINT",FACE,{"disambiguationData":[TD([[makeQuery(id+"F4.imprint","IMPRINT",EDGE,{"derivedFrom":sQuery(id+"F4.wireOp",EDGE,"E26.1.0")}),1.0]])]})])],"isStart":true})]}),makeQuery(id+"F42.opRevolve","SWEPT_FACE",FACE,{"disambiguationData":[OSD([sQuery(id+"F41.wireOp",EDGE,"E32")])]})]});
            var Q5;
            Q5=makeQuery(id+"F42.boolean.opBoolean","INTERSECT",EDGE,{"disambiguationData":[OD(0.0)],"derivedFrom":[makeQuery(id+"F20.boolean.opBoolean","MERGE",FACE,{"derivedFrom":[makeQuery(id+"F19.boolean.opBoolean","MERGE",FACE,{"derivedFrom":[makeQuery(id+"F18.boolean.opBoolean","MERGE",FACE,{"derivedFrom":[makeQuery(id+"F17.boolean.opBoolean","MERGE",FACE,{"derivedFrom":[makeQuery(id+"F16.boolean.opBoolean","MERGE",FACE,{"derivedFrom":[makeQuery(id+"F15.boolean.opBoolean","MERGE",FACE,{"derivedFrom":[makeQuery(id+"F14.boolean.opBoolean","MERGE",FACE,{"derivedFrom":[makeQuery(id+"F13.boolean.opBoolean","MERGE",FACE,{"derivedFrom":[makeQuery(id+"F12.boolean.opBoolean","MERGE",FACE,{"derivedFrom":[makeQuery(id+"F11.boolean.opBoolean","MERGE",FACE,{"derivedFrom":[makeQuery(id+"F10.boolean.opBoolean","MERGE",FACE,{"derivedFrom":[makeQuery(id+"F9.boolean.opBoolean","MERGE",FACE,{"derivedFrom":[makeQuery(id+"F8.boolean.opBoolean","MERGE",FACE,{"derivedFrom":[makeQuery(id+"F7.boolean.opBoolean","MERGE",FACE,{"derivedFrom":[makeQuery(id+"F6.boolean.opBoolean","MERGE",FACE,{"derivedFrom":[makeQuery(id+"F5.boolean.opBoolean","MERGE",FACE,{"derivedFrom":[makeQuery(id+"F1.opRevolve","SWEPT_FACE",FACE,{"disambiguationData":[OSD([sQuery(id+"F0.wireOp",EDGE,"E5")])]}),makeQuery(id+"F5.opLoft","CAP_FACE",FACE,{"disambiguationData":[OSD([makeQuery(id+"F4.imprint","IMPRINT",FACE,{"disambiguationData":[TD([[makeQuery(id+"F4.imprint","IMPRINT",EDGE,{"derivedFrom":sQuery(id+"F4.wireOp",EDGE,"E21")}),1.0]])]})])],"isStart":true})]}),makeQuery(id+"F6.opLoft","CAP_FACE",FACE,{"disambiguationData":[OSD([makeQuery(id+"F4.imprint","IMPRINT",FACE,{"disambiguationData":[TD([[makeQuery(id+"F4.imprint","IMPRINT",EDGE,{"derivedFrom":sQuery(id+"F4.wireOp",EDGE,"E26.15.0")}),1.0]])]})])],"isStart":true})]}),makeQuery(id+"F7.opLoft","CAP_FACE",FACE,{"disambiguationData":[OSD([makeQuery(id+"F4.imprint","IMPRINT",FACE,{"disambiguationData":[TD([[makeQuery(id+"F4.imprint","IMPRINT",EDGE,{"derivedFrom":sQuery(id+"F4.wireOp",EDGE,"E26.14.0")}),1.0]])]})])],"isStart":true})]}),makeQuery(id+"F8.opLoft","CAP_FACE",FACE,{"disambiguationData":[OSD([makeQuery(id+"F4.imprint","IMPRINT",FACE,{"disambiguationData":[TD([[makeQuery(id+"F4.imprint","IMPRINT",EDGE,{"derivedFrom":sQuery(id+"F4.wireOp",EDGE,"E26.13.0")}),1.0]])]})])],"isStart":true})]}),makeQuery(id+"F9.opLoft","CAP_FACE",FACE,{"disambiguationData":[OSD([makeQuery(id+"F4.imprint","IMPRINT",FACE,{"disambiguationData":[TD([[makeQuery(id+"F4.imprint","IMPRINT",EDGE,{"derivedFrom":sQuery(id+"F4.wireOp",EDGE,"E26.12.0")}),1.0]])]})])],"isStart":true})]}),makeQuery(id+"F10.opLoft","CAP_FACE",FACE,{"disambiguationData":[OSD([makeQuery(id+"F4.imprint","IMPRINT",FACE,{"disambiguationData":[TD([[makeQuery(id+"F4.imprint","IMPRINT",EDGE,{"derivedFrom":sQuery(id+"F4.wireOp",EDGE,"E26.11.0")}),1.0]])]})])],"isStart":true})]}),makeQuery(id+"F11.opLoft","CAP_FACE",FACE,{"disambiguationData":[OSD([makeQuery(id+"F4.imprint","IMPRINT",FACE,{"disambiguationData":[TD([[makeQuery(id+"F4.imprint","IMPRINT",EDGE,{"derivedFrom":sQuery(id+"F4.wireOp",EDGE,"E26.10.0")}),1.0]])]})])],"isStart":true})]}),makeQuery(id+"F12.opLoft","CAP_FACE",FACE,{"disambiguationData":[OSD([makeQuery(id+"F4.imprint","IMPRINT",FACE,{"disambiguationData":[TD([[makeQuery(id+"F4.imprint","IMPRINT",EDGE,{"derivedFrom":sQuery(id+"F4.wireOp",EDGE,"E26.9.0")}),1.0]])]})])],"isStart":true})]}),makeQuery(id+"F13.opLoft","CAP_FACE",FACE,{"disambiguationData":[OSD([makeQuery(id+"F4.imprint","IMPRINT",FACE,{"disambiguationData":[TD([[makeQuery(id+"F4.imprint","IMPRINT",EDGE,{"derivedFrom":sQuery(id+"F4.wireOp",EDGE,"E26.8.0")}),1.0]])]})])],"isStart":true})]}),makeQuery(id+"F14.opLoft","CAP_FACE",FACE,{"disambiguationData":[OSD([makeQuery(id+"F4.imprint","IMPRINT",FACE,{"disambiguationData":[TD([[makeQuery(id+"F4.imprint","IMPRINT",EDGE,{"derivedFrom":sQuery(id+"F4.wireOp",EDGE,"E26.7.0")}),1.0]])]})])],"isStart":true})]}),makeQuery(id+"F15.opLoft","CAP_FACE",FACE,{"disambiguationData":[OSD([makeQuery(id+"F4.imprint","IMPRINT",FACE,{"disambiguationData":[TD([[makeQuery(id+"F4.imprint","IMPRINT",EDGE,{"derivedFrom":sQuery(id+"F4.wireOp",EDGE,"E26.6.0")}),1.0]])]})])],"isStart":true})]}),makeQuery(id+"F16.opLoft","CAP_FACE",FACE,{"disambiguationData":[OSD([makeQuery(id+"F4.imprint","IMPRINT",FACE,{"disambiguationData":[TD([[makeQuery(id+"F4.imprint","IMPRINT",EDGE,{"derivedFrom":sQuery(id+"F4.wireOp",EDGE,"E26.5.0")}),1.0]])]})])],"isStart":true})]}),makeQuery(id+"F17.opLoft","CAP_FACE",FACE,{"disambiguationData":[OSD([makeQuery(id+"F4.imprint","IMPRINT",FACE,{"disambiguationData":[TD([[makeQuery(id+"F4.imprint","IMPRINT",EDGE,{"derivedFrom":sQuery(id+"F4.wireOp",EDGE,"E26.4.0")}),1.0]])]})])],"isStart":true})]}),makeQuery(id+"F18.opLoft","CAP_FACE",FACE,{"disambiguationData":[OSD([makeQuery(id+"F4.imprint","IMPRINT",FACE,{"disambiguationData":[TD([[makeQuery(id+"F4.imprint","IMPRINT",EDGE,{"derivedFrom":sQuery(id+"F4.wireOp",EDGE,"E26.3.0")}),1.0]])]})])],"isStart":true})]}),makeQuery(id+"F19.opLoft","CAP_FACE",FACE,{"disambiguationData":[OSD([makeQuery(id+"F4.imprint","IMPRINT",FACE,{"disambiguationData":[TD([[makeQuery(id+"F4.imprint","IMPRINT",EDGE,{"derivedFrom":sQuery(id+"F4.wireOp",EDGE,"E26.2.0")}),1.0]])]})])],"isStart":true})]}),makeQuery(id+"F20.opLoft","CAP_FACE",FACE,{"disambiguationData":[OSD([makeQuery(id+"F4.imprint","IMPRINT",FACE,{"disambiguationData":[TD([[makeQuery(id+"F4.imprint","IMPRINT",EDGE,{"derivedFrom":sQuery(id+"F4.wireOp",EDGE,"E26.1.0")}),1.0]])]})])],"isStart":true})]}),makeQuery(id+"F42.opRevolve","SWEPT_FACE",FACE,{"disambiguationData":[OSD([sQuery(id+"F41.wireOp",EDGE,"E32")])]})]});
            var Q6;
            Q6=makeQuery(id+"F42.boolean.opBoolean","INTERSECT",EDGE,{"disambiguationData":[OD(15.0)],"derivedFrom":[makeQuery(id+"F20.boolean.opBoolean","MERGE",FACE,{"derivedFrom":[makeQuery(id+"F19.boolean.opBoolean","MERGE",FACE,{"derivedFrom":[makeQuery(id+"F18.boolean.opBoolean","MERGE",FACE,{"derivedFrom":[makeQuery(id+"F17.boolean.opBoolean","MERGE",FACE,{"derivedFrom":[makeQuery(id+"F16.boolean.opBoolean","MERGE",FACE,{"derivedFrom":[makeQuery(id+"F15.boolean.opBoolean","MERGE",FACE,{"derivedFrom":[makeQuery(id+"F14.boolean.opBoolean","MERGE",FACE,{"derivedFrom":[makeQuery(id+"F13.boolean.opBoolean","MERGE",FACE,{"derivedFrom":[makeQuery(id+"F12.boolean.opBoolean","MERGE",FACE,{"derivedFrom":[makeQuery(id+"F11.boolean.opBoolean","MERGE",FACE,{"derivedFrom":[makeQuery(id+"F10.boolean.opBoolean","MERGE",FACE,{"derivedFrom":[makeQuery(id+"F9.boolean.opBoolean","MERGE",FACE,{"derivedFrom":[makeQuery(id+"F8.boolean.opBoolean","MERGE",FACE,{"derivedFrom":[makeQuery(id+"F7.boolean.opBoolean","MERGE",FACE,{"derivedFrom":[makeQuery(id+"F6.boolean.opBoolean","MERGE",FACE,{"derivedFrom":[makeQuery(id+"F5.boolean.opBoolean","MERGE",FACE,{"derivedFrom":[makeQuery(id+"F1.opRevolve","SWEPT_FACE",FACE,{"disambiguationData":[OSD([sQuery(id+"F0.wireOp",EDGE,"E5")])]}),makeQuery(id+"F5.opLoft","CAP_FACE",FACE,{"disambiguationData":[OSD([makeQuery(id+"F4.imprint","IMPRINT",FACE,{"disambiguationData":[TD([[makeQuery(id+"F4.imprint","IMPRINT",EDGE,{"derivedFrom":sQuery(id+"F4.wireOp",EDGE,"E21")}),1.0]])]})])],"isStart":true})]}),makeQuery(id+"F6.opLoft","CAP_FACE",FACE,{"disambiguationData":[OSD([makeQuery(id+"F4.imprint","IMPRINT",FACE,{"disambiguationData":[TD([[makeQuery(id+"F4.imprint","IMPRINT",EDGE,{"derivedFrom":sQuery(id+"F4.wireOp",EDGE,"E26.15.0")}),1.0]])]})])],"isStart":true})]}),makeQuery(id+"F7.opLoft","CAP_FACE",FACE,{"disambiguationData":[OSD([makeQuery(id+"F4.imprint","IMPRINT",FACE,{"disambiguationData":[TD([[makeQuery(id+"F4.imprint","IMPRINT",EDGE,{"derivedFrom":sQuery(id+"F4.wireOp",EDGE,"E26.14.0")}),1.0]])]})])],"isStart":true})]}),makeQuery(id+"F8.opLoft","CAP_FACE",FACE,{"disambiguationData":[OSD([makeQuery(id+"F4.imprint","IMPRINT",FACE,{"disambiguationData":[TD([[makeQuery(id+"F4.imprint","IMPRINT",EDGE,{"derivedFrom":sQuery(id+"F4.wireOp",EDGE,"E26.13.0")}),1.0]])]})])],"isStart":true})]}),makeQuery(id+"F9.opLoft","CAP_FACE",FACE,{"disambiguationData":[OSD([makeQuery(id+"F4.imprint","IMPRINT",FACE,{"disambiguationData":[TD([[makeQuery(id+"F4.imprint","IMPRINT",EDGE,{"derivedFrom":sQuery(id+"F4.wireOp",EDGE,"E26.12.0")}),1.0]])]})])],"isStart":true})]}),makeQuery(id+"F10.opLoft","CAP_FACE",FACE,{"disambiguationData":[OSD([makeQuery(id+"F4.imprint","IMPRINT",FACE,{"disambiguationData":[TD([[makeQuery(id+"F4.imprint","IMPRINT",EDGE,{"derivedFrom":sQuery(id+"F4.wireOp",EDGE,"E26.11.0")}),1.0]])]})])],"isStart":true})]}),makeQuery(id+"F11.opLoft","CAP_FACE",FACE,{"disambiguationData":[OSD([makeQuery(id+"F4.imprint","IMPRINT",FACE,{"disambiguationData":[TD([[makeQuery(id+"F4.imprint","IMPRINT",EDGE,{"derivedFrom":sQuery(id+"F4.wireOp",EDGE,"E26.10.0")}),1.0]])]})])],"isStart":true})]}),makeQuery(id+"F12.opLoft","CAP_FACE",FACE,{"disambiguationData":[OSD([makeQuery(id+"F4.imprint","IMPRINT",FACE,{"disambiguationData":[TD([[makeQuery(id+"F4.imprint","IMPRINT",EDGE,{"derivedFrom":sQuery(id+"F4.wireOp",EDGE,"E26.9.0")}),1.0]])]})])],"isStart":true})]}),makeQuery(id+"F13.opLoft","CAP_FACE",FACE,{"disambiguationData":[OSD([makeQuery(id+"F4.imprint","IMPRINT",FACE,{"disambiguationData":[TD([[makeQuery(id+"F4.imprint","IMPRINT",EDGE,{"derivedFrom":sQuery(id+"F4.wireOp",EDGE,"E26.8.0")}),1.0]])]})])],"isStart":true})]}),makeQuery(id+"F14.opLoft","CAP_FACE",FACE,{"disambiguationData":[OSD([makeQuery(id+"F4.imprint","IMPRINT",FACE,{"disambiguationData":[TD([[makeQuery(id+"F4.imprint","IMPRINT",EDGE,{"derivedFrom":sQuery(id+"F4.wireOp",EDGE,"E26.7.0")}),1.0]])]})])],"isStart":true})]}),makeQuery(id+"F15.opLoft","CAP_FACE",FACE,{"disambiguationData":[OSD([makeQuery(id+"F4.imprint","IMPRINT",FACE,{"disambiguationData":[TD([[makeQuery(id+"F4.imprint","IMPRINT",EDGE,{"derivedFrom":sQuery(id+"F4.wireOp",EDGE,"E26.6.0")}),1.0]])]})])],"isStart":true})]}),makeQuery(id+"F16.opLoft","CAP_FACE",FACE,{"disambiguationData":[OSD([makeQuery(id+"F4.imprint","IMPRINT",FACE,{"disambiguationData":[TD([[makeQuery(id+"F4.imprint","IMPRINT",EDGE,{"derivedFrom":sQuery(id+"F4.wireOp",EDGE,"E26.5.0")}),1.0]])]})])],"isStart":true})]}),makeQuery(id+"F17.opLoft","CAP_FACE",FACE,{"disambiguationData":[OSD([makeQuery(id+"F4.imprint","IMPRINT",FACE,{"disambiguationData":[TD([[makeQuery(id+"F4.imprint","IMPRINT",EDGE,{"derivedFrom":sQuery(id+"F4.wireOp",EDGE,"E26.4.0")}),1.0]])]})])],"isStart":true})]}),makeQuery(id+"F18.opLoft","CAP_FACE",FACE,{"disambiguationData":[OSD([makeQuery(id+"F4.imprint","IMPRINT",FACE,{"disambiguationData":[TD([[makeQuery(id+"F4.imprint","IMPRINT",EDGE,{"derivedFrom":sQuery(id+"F4.wireOp",EDGE,"E26.3.0")}),1.0]])]})])],"isStart":true})]}),makeQuery(id+"F19.opLoft","CAP_FACE",FACE,{"disambiguationData":[OSD([makeQuery(id+"F4.imprint","IMPRINT",FACE,{"disambiguationData":[TD([[makeQuery(id+"F4.imprint","IMPRINT",EDGE,{"derivedFrom":sQuery(id+"F4.wireOp",EDGE,"E26.2.0")}),1.0]])]})])],"isStart":true})]}),makeQuery(id+"F20.opLoft","CAP_FACE",FACE,{"disambiguationData":[OSD([makeQuery(id+"F4.imprint","IMPRINT",FACE,{"disambiguationData":[TD([[makeQuery(id+"F4.imprint","IMPRINT",EDGE,{"derivedFrom":sQuery(id+"F4.wireOp",EDGE,"E26.1.0")}),1.0]])]})])],"isStart":true})]}),makeQuery(id+"F42.opRevolve","SWEPT_FACE",FACE,{"disambiguationData":[OSD([sQuery(id+"F41.wireOp",EDGE,"E32")])]})]});
            var Q7;
            Q7=makeQuery(id+"F42.boolean.opBoolean","INTERSECT",EDGE,{"disambiguationData":[OD(14.0)],"derivedFrom":[makeQuery(id+"F20.boolean.opBoolean","MERGE",FACE,{"derivedFrom":[makeQuery(id+"F19.boolean.opBoolean","MERGE",FACE,{"derivedFrom":[makeQuery(id+"F18.boolean.opBoolean","MERGE",FACE,{"derivedFrom":[makeQuery(id+"F17.boolean.opBoolean","MERGE",FACE,{"derivedFrom":[makeQuery(id+"F16.boolean.opBoolean","MERGE",FACE,{"derivedFrom":[makeQuery(id+"F15.boolean.opBoolean","MERGE",FACE,{"derivedFrom":[makeQuery(id+"F14.boolean.opBoolean","MERGE",FACE,{"derivedFrom":[makeQuery(id+"F13.boolean.opBoolean","MERGE",FACE,{"derivedFrom":[makeQuery(id+"F12.boolean.opBoolean","MERGE",FACE,{"derivedFrom":[makeQuery(id+"F11.boolean.opBoolean","MERGE",FACE,{"derivedFrom":[makeQuery(id+"F10.boolean.opBoolean","MERGE",FACE,{"derivedFrom":[makeQuery(id+"F9.boolean.opBoolean","MERGE",FACE,{"derivedFrom":[makeQuery(id+"F8.boolean.opBoolean","MERGE",FACE,{"derivedFrom":[makeQuery(id+"F7.boolean.opBoolean","MERGE",FACE,{"derivedFrom":[makeQuery(id+"F6.boolean.opBoolean","MERGE",FACE,{"derivedFrom":[makeQuery(id+"F5.boolean.opBoolean","MERGE",FACE,{"derivedFrom":[makeQuery(id+"F1.opRevolve","SWEPT_FACE",FACE,{"disambiguationData":[OSD([sQuery(id+"F0.wireOp",EDGE,"E5")])]}),makeQuery(id+"F5.opLoft","CAP_FACE",FACE,{"disambiguationData":[OSD([makeQuery(id+"F4.imprint","IMPRINT",FACE,{"disambiguationData":[TD([[makeQuery(id+"F4.imprint","IMPRINT",EDGE,{"derivedFrom":sQuery(id+"F4.wireOp",EDGE,"E21")}),1.0]])]})])],"isStart":true})]}),makeQuery(id+"F6.opLoft","CAP_FACE",FACE,{"disambiguationData":[OSD([makeQuery(id+"F4.imprint","IMPRINT",FACE,{"disambiguationData":[TD([[makeQuery(id+"F4.imprint","IMPRINT",EDGE,{"derivedFrom":sQuery(id+"F4.wireOp",EDGE,"E26.15.0")}),1.0]])]})])],"isStart":true})]}),makeQuery(id+"F7.opLoft","CAP_FACE",FACE,{"disambiguationData":[OSD([makeQuery(id+"F4.imprint","IMPRINT",FACE,{"disambiguationData":[TD([[makeQuery(id+"F4.imprint","IMPRINT",EDGE,{"derivedFrom":sQuery(id+"F4.wireOp",EDGE,"E26.14.0")}),1.0]])]})])],"isStart":true})]}),makeQuery(id+"F8.opLoft","CAP_FACE",FACE,{"disambiguationData":[OSD([makeQuery(id+"F4.imprint","IMPRINT",FACE,{"disambiguationData":[TD([[makeQuery(id+"F4.imprint","IMPRINT",EDGE,{"derivedFrom":sQuery(id+"F4.wireOp",EDGE,"E26.13.0")}),1.0]])]})])],"isStart":true})]}),makeQuery(id+"F9.opLoft","CAP_FACE",FACE,{"disambiguationData":[OSD([makeQuery(id+"F4.imprint","IMPRINT",FACE,{"disambiguationData":[TD([[makeQuery(id+"F4.imprint","IMPRINT",EDGE,{"derivedFrom":sQuery(id+"F4.wireOp",EDGE,"E26.12.0")}),1.0]])]})])],"isStart":true})]}),makeQuery(id+"F10.opLoft","CAP_FACE",FACE,{"disambiguationData":[OSD([makeQuery(id+"F4.imprint","IMPRINT",FACE,{"disambiguationData":[TD([[makeQuery(id+"F4.imprint","IMPRINT",EDGE,{"derivedFrom":sQuery(id+"F4.wireOp",EDGE,"E26.11.0")}),1.0]])]})])],"isStart":true})]}),makeQuery(id+"F11.opLoft","CAP_FACE",FACE,{"disambiguationData":[OSD([makeQuery(id+"F4.imprint","IMPRINT",FACE,{"disambiguationData":[TD([[makeQuery(id+"F4.imprint","IMPRINT",EDGE,{"derivedFrom":sQuery(id+"F4.wireOp",EDGE,"E26.10.0")}),1.0]])]})])],"isStart":true})]}),makeQuery(id+"F12.opLoft","CAP_FACE",FACE,{"disambiguationData":[OSD([makeQuery(id+"F4.imprint","IMPRINT",FACE,{"disambiguationData":[TD([[makeQuery(id+"F4.imprint","IMPRINT",EDGE,{"derivedFrom":sQuery(id+"F4.wireOp",EDGE,"E26.9.0")}),1.0]])]})])],"isStart":true})]}),makeQuery(id+"F13.opLoft","CAP_FACE",FACE,{"disambiguationData":[OSD([makeQuery(id+"F4.imprint","IMPRINT",FACE,{"disambiguationData":[TD([[makeQuery(id+"F4.imprint","IMPRINT",EDGE,{"derivedFrom":sQuery(id+"F4.wireOp",EDGE,"E26.8.0")}),1.0]])]})])],"isStart":true})]}),makeQuery(id+"F14.opLoft","CAP_FACE",FACE,{"disambiguationData":[OSD([makeQuery(id+"F4.imprint","IMPRINT",FACE,{"disambiguationData":[TD([[makeQuery(id+"F4.imprint","IMPRINT",EDGE,{"derivedFrom":sQuery(id+"F4.wireOp",EDGE,"E26.7.0")}),1.0]])]})])],"isStart":true})]}),makeQuery(id+"F15.opLoft","CAP_FACE",FACE,{"disambiguationData":[OSD([makeQuery(id+"F4.imprint","IMPRINT",FACE,{"disambiguationData":[TD([[makeQuery(id+"F4.imprint","IMPRINT",EDGE,{"derivedFrom":sQuery(id+"F4.wireOp",EDGE,"E26.6.0")}),1.0]])]})])],"isStart":true})]}),makeQuery(id+"F16.opLoft","CAP_FACE",FACE,{"disambiguationData":[OSD([makeQuery(id+"F4.imprint","IMPRINT",FACE,{"disambiguationData":[TD([[makeQuery(id+"F4.imprint","IMPRINT",EDGE,{"derivedFrom":sQuery(id+"F4.wireOp",EDGE,"E26.5.0")}),1.0]])]})])],"isStart":true})]}),makeQuery(id+"F17.opLoft","CAP_FACE",FACE,{"disambiguationData":[OSD([makeQuery(id+"F4.imprint","IMPRINT",FACE,{"disambiguationData":[TD([[makeQuery(id+"F4.imprint","IMPRINT",EDGE,{"derivedFrom":sQuery(id+"F4.wireOp",EDGE,"E26.4.0")}),1.0]])]})])],"isStart":true})]}),makeQuery(id+"F18.opLoft","CAP_FACE",FACE,{"disambiguationData":[OSD([makeQuery(id+"F4.imprint","IMPRINT",FACE,{"disambiguationData":[TD([[makeQuery(id+"F4.imprint","IMPRINT",EDGE,{"derivedFrom":sQuery(id+"F4.wireOp",EDGE,"E26.3.0")}),1.0]])]})])],"isStart":true})]}),makeQuery(id+"F19.opLoft","CAP_FACE",FACE,{"disambiguationData":[OSD([makeQuery(id+"F4.imprint","IMPRINT",FACE,{"disambiguationData":[TD([[makeQuery(id+"F4.imprint","IMPRINT",EDGE,{"derivedFrom":sQuery(id+"F4.wireOp",EDGE,"E26.2.0")}),1.0]])]})])],"isStart":true})]}),makeQuery(id+"F20.opLoft","CAP_FACE",FACE,{"disambiguationData":[OSD([makeQuery(id+"F4.imprint","IMPRINT",FACE,{"disambiguationData":[TD([[makeQuery(id+"F4.imprint","IMPRINT",EDGE,{"derivedFrom":sQuery(id+"F4.wireOp",EDGE,"E26.1.0")}),1.0]])]})])],"isStart":true})]}),makeQuery(id+"F42.opRevolve","SWEPT_FACE",FACE,{"disambiguationData":[OSD([sQuery(id+"F41.wireOp",EDGE,"E32")])]})]});
            var Q8;
            Q8=makeQuery(id+"F42.boolean.opBoolean","INTERSECT",EDGE,{"disambiguationData":[OD(13.0)],"derivedFrom":[makeQuery(id+"F20.boolean.opBoolean","MERGE",FACE,{"derivedFrom":[makeQuery(id+"F19.boolean.opBoolean","MERGE",FACE,{"derivedFrom":[makeQuery(id+"F18.boolean.opBoolean","MERGE",FACE,{"derivedFrom":[makeQuery(id+"F17.boolean.opBoolean","MERGE",FACE,{"derivedFrom":[makeQuery(id+"F16.boolean.opBoolean","MERGE",FACE,{"derivedFrom":[makeQuery(id+"F15.boolean.opBoolean","MERGE",FACE,{"derivedFrom":[makeQuery(id+"F14.boolean.opBoolean","MERGE",FACE,{"derivedFrom":[makeQuery(id+"F13.boolean.opBoolean","MERGE",FACE,{"derivedFrom":[makeQuery(id+"F12.boolean.opBoolean","MERGE",FACE,{"derivedFrom":[makeQuery(id+"F11.boolean.opBoolean","MERGE",FACE,{"derivedFrom":[makeQuery(id+"F10.boolean.opBoolean","MERGE",FACE,{"derivedFrom":[makeQuery(id+"F9.boolean.opBoolean","MERGE",FACE,{"derivedFrom":[makeQuery(id+"F8.boolean.opBoolean","MERGE",FACE,{"derivedFrom":[makeQuery(id+"F7.boolean.opBoolean","MERGE",FACE,{"derivedFrom":[makeQuery(id+"F6.boolean.opBoolean","MERGE",FACE,{"derivedFrom":[makeQuery(id+"F5.boolean.opBoolean","MERGE",FACE,{"derivedFrom":[makeQuery(id+"F1.opRevolve","SWEPT_FACE",FACE,{"disambiguationData":[OSD([sQuery(id+"F0.wireOp",EDGE,"E5")])]}),makeQuery(id+"F5.opLoft","CAP_FACE",FACE,{"disambiguationData":[OSD([makeQuery(id+"F4.imprint","IMPRINT",FACE,{"disambiguationData":[TD([[makeQuery(id+"F4.imprint","IMPRINT",EDGE,{"derivedFrom":sQuery(id+"F4.wireOp",EDGE,"E21")}),1.0]])]})])],"isStart":true})]}),makeQuery(id+"F6.opLoft","CAP_FACE",FACE,{"disambiguationData":[OSD([makeQuery(id+"F4.imprint","IMPRINT",FACE,{"disambiguationData":[TD([[makeQuery(id+"F4.imprint","IMPRINT",EDGE,{"derivedFrom":sQuery(id+"F4.wireOp",EDGE,"E26.15.0")}),1.0]])]})])],"isStart":true})]}),makeQuery(id+"F7.opLoft","CAP_FACE",FACE,{"disambiguationData":[OSD([makeQuery(id+"F4.imprint","IMPRINT",FACE,{"disambiguationData":[TD([[makeQuery(id+"F4.imprint","IMPRINT",EDGE,{"derivedFrom":sQuery(id+"F4.wireOp",EDGE,"E26.14.0")}),1.0]])]})])],"isStart":true})]}),makeQuery(id+"F8.opLoft","CAP_FACE",FACE,{"disambiguationData":[OSD([makeQuery(id+"F4.imprint","IMPRINT",FACE,{"disambiguationData":[TD([[makeQuery(id+"F4.imprint","IMPRINT",EDGE,{"derivedFrom":sQuery(id+"F4.wireOp",EDGE,"E26.13.0")}),1.0]])]})])],"isStart":true})]}),makeQuery(id+"F9.opLoft","CAP_FACE",FACE,{"disambiguationData":[OSD([makeQuery(id+"F4.imprint","IMPRINT",FACE,{"disambiguationData":[TD([[makeQuery(id+"F4.imprint","IMPRINT",EDGE,{"derivedFrom":sQuery(id+"F4.wireOp",EDGE,"E26.12.0")}),1.0]])]})])],"isStart":true})]}),makeQuery(id+"F10.opLoft","CAP_FACE",FACE,{"disambiguationData":[OSD([makeQuery(id+"F4.imprint","IMPRINT",FACE,{"disambiguationData":[TD([[makeQuery(id+"F4.imprint","IMPRINT",EDGE,{"derivedFrom":sQuery(id+"F4.wireOp",EDGE,"E26.11.0")}),1.0]])]})])],"isStart":true})]}),makeQuery(id+"F11.opLoft","CAP_FACE",FACE,{"disambiguationData":[OSD([makeQuery(id+"F4.imprint","IMPRINT",FACE,{"disambiguationData":[TD([[makeQuery(id+"F4.imprint","IMPRINT",EDGE,{"derivedFrom":sQuery(id+"F4.wireOp",EDGE,"E26.10.0")}),1.0]])]})])],"isStart":true})]}),makeQuery(id+"F12.opLoft","CAP_FACE",FACE,{"disambiguationData":[OSD([makeQuery(id+"F4.imprint","IMPRINT",FACE,{"disambiguationData":[TD([[makeQuery(id+"F4.imprint","IMPRINT",EDGE,{"derivedFrom":sQuery(id+"F4.wireOp",EDGE,"E26.9.0")}),1.0]])]})])],"isStart":true})]}),makeQuery(id+"F13.opLoft","CAP_FACE",FACE,{"disambiguationData":[OSD([makeQuery(id+"F4.imprint","IMPRINT",FACE,{"disambiguationData":[TD([[makeQuery(id+"F4.imprint","IMPRINT",EDGE,{"derivedFrom":sQuery(id+"F4.wireOp",EDGE,"E26.8.0")}),1.0]])]})])],"isStart":true})]}),makeQuery(id+"F14.opLoft","CAP_FACE",FACE,{"disambiguationData":[OSD([makeQuery(id+"F4.imprint","IMPRINT",FACE,{"disambiguationData":[TD([[makeQuery(id+"F4.imprint","IMPRINT",EDGE,{"derivedFrom":sQuery(id+"F4.wireOp",EDGE,"E26.7.0")}),1.0]])]})])],"isStart":true})]}),makeQuery(id+"F15.opLoft","CAP_FACE",FACE,{"disambiguationData":[OSD([makeQuery(id+"F4.imprint","IMPRINT",FACE,{"disambiguationData":[TD([[makeQuery(id+"F4.imprint","IMPRINT",EDGE,{"derivedFrom":sQuery(id+"F4.wireOp",EDGE,"E26.6.0")}),1.0]])]})])],"isStart":true})]}),makeQuery(id+"F16.opLoft","CAP_FACE",FACE,{"disambiguationData":[OSD([makeQuery(id+"F4.imprint","IMPRINT",FACE,{"disambiguationData":[TD([[makeQuery(id+"F4.imprint","IMPRINT",EDGE,{"derivedFrom":sQuery(id+"F4.wireOp",EDGE,"E26.5.0")}),1.0]])]})])],"isStart":true})]}),makeQuery(id+"F17.opLoft","CAP_FACE",FACE,{"disambiguationData":[OSD([makeQuery(id+"F4.imprint","IMPRINT",FACE,{"disambiguationData":[TD([[makeQuery(id+"F4.imprint","IMPRINT",EDGE,{"derivedFrom":sQuery(id+"F4.wireOp",EDGE,"E26.4.0")}),1.0]])]})])],"isStart":true})]}),makeQuery(id+"F18.opLoft","CAP_FACE",FACE,{"disambiguationData":[OSD([makeQuery(id+"F4.imprint","IMPRINT",FACE,{"disambiguationData":[TD([[makeQuery(id+"F4.imprint","IMPRINT",EDGE,{"derivedFrom":sQuery(id+"F4.wireOp",EDGE,"E26.3.0")}),1.0]])]})])],"isStart":true})]}),makeQuery(id+"F19.opLoft","CAP_FACE",FACE,{"disambiguationData":[OSD([makeQuery(id+"F4.imprint","IMPRINT",FACE,{"disambiguationData":[TD([[makeQuery(id+"F4.imprint","IMPRINT",EDGE,{"derivedFrom":sQuery(id+"F4.wireOp",EDGE,"E26.2.0")}),1.0]])]})])],"isStart":true})]}),makeQuery(id+"F20.opLoft","CAP_FACE",FACE,{"disambiguationData":[OSD([makeQuery(id+"F4.imprint","IMPRINT",FACE,{"disambiguationData":[TD([[makeQuery(id+"F4.imprint","IMPRINT",EDGE,{"derivedFrom":sQuery(id+"F4.wireOp",EDGE,"E26.1.0")}),1.0]])]})])],"isStart":true})]}),makeQuery(id+"F42.opRevolve","SWEPT_FACE",FACE,{"disambiguationData":[OSD([sQuery(id+"F41.wireOp",EDGE,"E32")])]})]});
            var Q9;
            Q9=makeQuery(id+"F42.boolean.opBoolean","INTERSECT",EDGE,{"disambiguationData":[OD(12.0)],"derivedFrom":[makeQuery(id+"F20.boolean.opBoolean","MERGE",FACE,{"derivedFrom":[makeQuery(id+"F19.boolean.opBoolean","MERGE",FACE,{"derivedFrom":[makeQuery(id+"F18.boolean.opBoolean","MERGE",FACE,{"derivedFrom":[makeQuery(id+"F17.boolean.opBoolean","MERGE",FACE,{"derivedFrom":[makeQuery(id+"F16.boolean.opBoolean","MERGE",FACE,{"derivedFrom":[makeQuery(id+"F15.boolean.opBoolean","MERGE",FACE,{"derivedFrom":[makeQuery(id+"F14.boolean.opBoolean","MERGE",FACE,{"derivedFrom":[makeQuery(id+"F13.boolean.opBoolean","MERGE",FACE,{"derivedFrom":[makeQuery(id+"F12.boolean.opBoolean","MERGE",FACE,{"derivedFrom":[makeQuery(id+"F11.boolean.opBoolean","MERGE",FACE,{"derivedFrom":[makeQuery(id+"F10.boolean.opBoolean","MERGE",FACE,{"derivedFrom":[makeQuery(id+"F9.boolean.opBoolean","MERGE",FACE,{"derivedFrom":[makeQuery(id+"F8.boolean.opBoolean","MERGE",FACE,{"derivedFrom":[makeQuery(id+"F7.boolean.opBoolean","MERGE",FACE,{"derivedFrom":[makeQuery(id+"F6.boolean.opBoolean","MERGE",FACE,{"derivedFrom":[makeQuery(id+"F5.boolean.opBoolean","MERGE",FACE,{"derivedFrom":[makeQuery(id+"F1.opRevolve","SWEPT_FACE",FACE,{"disambiguationData":[OSD([sQuery(id+"F0.wireOp",EDGE,"E5")])]}),makeQuery(id+"F5.opLoft","CAP_FACE",FACE,{"disambiguationData":[OSD([makeQuery(id+"F4.imprint","IMPRINT",FACE,{"disambiguationData":[TD([[makeQuery(id+"F4.imprint","IMPRINT",EDGE,{"derivedFrom":sQuery(id+"F4.wireOp",EDGE,"E21")}),1.0]])]})])],"isStart":true})]}),makeQuery(id+"F6.opLoft","CAP_FACE",FACE,{"disambiguationData":[OSD([makeQuery(id+"F4.imprint","IMPRINT",FACE,{"disambiguationData":[TD([[makeQuery(id+"F4.imprint","IMPRINT",EDGE,{"derivedFrom":sQuery(id+"F4.wireOp",EDGE,"E26.15.0")}),1.0]])]})])],"isStart":true})]}),makeQuery(id+"F7.opLoft","CAP_FACE",FACE,{"disambiguationData":[OSD([makeQuery(id+"F4.imprint","IMPRINT",FACE,{"disambiguationData":[TD([[makeQuery(id+"F4.imprint","IMPRINT",EDGE,{"derivedFrom":sQuery(id+"F4.wireOp",EDGE,"E26.14.0")}),1.0]])]})])],"isStart":true})]}),makeQuery(id+"F8.opLoft","CAP_FACE",FACE,{"disambiguationData":[OSD([makeQuery(id+"F4.imprint","IMPRINT",FACE,{"disambiguationData":[TD([[makeQuery(id+"F4.imprint","IMPRINT",EDGE,{"derivedFrom":sQuery(id+"F4.wireOp",EDGE,"E26.13.0")}),1.0]])]})])],"isStart":true})]}),makeQuery(id+"F9.opLoft","CAP_FACE",FACE,{"disambiguationData":[OSD([makeQuery(id+"F4.imprint","IMPRINT",FACE,{"disambiguationData":[TD([[makeQuery(id+"F4.imprint","IMPRINT",EDGE,{"derivedFrom":sQuery(id+"F4.wireOp",EDGE,"E26.12.0")}),1.0]])]})])],"isStart":true})]}),makeQuery(id+"F10.opLoft","CAP_FACE",FACE,{"disambiguationData":[OSD([makeQuery(id+"F4.imprint","IMPRINT",FACE,{"disambiguationData":[TD([[makeQuery(id+"F4.imprint","IMPRINT",EDGE,{"derivedFrom":sQuery(id+"F4.wireOp",EDGE,"E26.11.0")}),1.0]])]})])],"isStart":true})]}),makeQuery(id+"F11.opLoft","CAP_FACE",FACE,{"disambiguationData":[OSD([makeQuery(id+"F4.imprint","IMPRINT",FACE,{"disambiguationData":[TD([[makeQuery(id+"F4.imprint","IMPRINT",EDGE,{"derivedFrom":sQuery(id+"F4.wireOp",EDGE,"E26.10.0")}),1.0]])]})])],"isStart":true})]}),makeQuery(id+"F12.opLoft","CAP_FACE",FACE,{"disambiguationData":[OSD([makeQuery(id+"F4.imprint","IMPRINT",FACE,{"disambiguationData":[TD([[makeQuery(id+"F4.imprint","IMPRINT",EDGE,{"derivedFrom":sQuery(id+"F4.wireOp",EDGE,"E26.9.0")}),1.0]])]})])],"isStart":true})]}),makeQuery(id+"F13.opLoft","CAP_FACE",FACE,{"disambiguationData":[OSD([makeQuery(id+"F4.imprint","IMPRINT",FACE,{"disambiguationData":[TD([[makeQuery(id+"F4.imprint","IMPRINT",EDGE,{"derivedFrom":sQuery(id+"F4.wireOp",EDGE,"E26.8.0")}),1.0]])]})])],"isStart":true})]}),makeQuery(id+"F14.opLoft","CAP_FACE",FACE,{"disambiguationData":[OSD([makeQuery(id+"F4.imprint","IMPRINT",FACE,{"disambiguationData":[TD([[makeQuery(id+"F4.imprint","IMPRINT",EDGE,{"derivedFrom":sQuery(id+"F4.wireOp",EDGE,"E26.7.0")}),1.0]])]})])],"isStart":true})]}),makeQuery(id+"F15.opLoft","CAP_FACE",FACE,{"disambiguationData":[OSD([makeQuery(id+"F4.imprint","IMPRINT",FACE,{"disambiguationData":[TD([[makeQuery(id+"F4.imprint","IMPRINT",EDGE,{"derivedFrom":sQuery(id+"F4.wireOp",EDGE,"E26.6.0")}),1.0]])]})])],"isStart":true})]}),makeQuery(id+"F16.opLoft","CAP_FACE",FACE,{"disambiguationData":[OSD([makeQuery(id+"F4.imprint","IMPRINT",FACE,{"disambiguationData":[TD([[makeQuery(id+"F4.imprint","IMPRINT",EDGE,{"derivedFrom":sQuery(id+"F4.wireOp",EDGE,"E26.5.0")}),1.0]])]})])],"isStart":true})]}),makeQuery(id+"F17.opLoft","CAP_FACE",FACE,{"disambiguationData":[OSD([makeQuery(id+"F4.imprint","IMPRINT",FACE,{"disambiguationData":[TD([[makeQuery(id+"F4.imprint","IMPRINT",EDGE,{"derivedFrom":sQuery(id+"F4.wireOp",EDGE,"E26.4.0")}),1.0]])]})])],"isStart":true})]}),makeQuery(id+"F18.opLoft","CAP_FACE",FACE,{"disambiguationData":[OSD([makeQuery(id+"F4.imprint","IMPRINT",FACE,{"disambiguationData":[TD([[makeQuery(id+"F4.imprint","IMPRINT",EDGE,{"derivedFrom":sQuery(id+"F4.wireOp",EDGE,"E26.3.0")}),1.0]])]})])],"isStart":true})]}),makeQuery(id+"F19.opLoft","CAP_FACE",FACE,{"disambiguationData":[OSD([makeQuery(id+"F4.imprint","IMPRINT",FACE,{"disambiguationData":[TD([[makeQuery(id+"F4.imprint","IMPRINT",EDGE,{"derivedFrom":sQuery(id+"F4.wireOp",EDGE,"E26.2.0")}),1.0]])]})])],"isStart":true})]}),makeQuery(id+"F20.opLoft","CAP_FACE",FACE,{"disambiguationData":[OSD([makeQuery(id+"F4.imprint","IMPRINT",FACE,{"disambiguationData":[TD([[makeQuery(id+"F4.imprint","IMPRINT",EDGE,{"derivedFrom":sQuery(id+"F4.wireOp",EDGE,"E26.1.0")}),1.0]])]})])],"isStart":true})]}),makeQuery(id+"F42.opRevolve","SWEPT_FACE",FACE,{"disambiguationData":[OSD([sQuery(id+"F41.wireOp",EDGE,"E32")])]})]});
            var Q10;
            Q10=makeQuery(id+"F42.boolean.opBoolean","INTERSECT",EDGE,{"disambiguationData":[OD(11.0)],"derivedFrom":[makeQuery(id+"F20.boolean.opBoolean","MERGE",FACE,{"derivedFrom":[makeQuery(id+"F19.boolean.opBoolean","MERGE",FACE,{"derivedFrom":[makeQuery(id+"F18.boolean.opBoolean","MERGE",FACE,{"derivedFrom":[makeQuery(id+"F17.boolean.opBoolean","MERGE",FACE,{"derivedFrom":[makeQuery(id+"F16.boolean.opBoolean","MERGE",FACE,{"derivedFrom":[makeQuery(id+"F15.boolean.opBoolean","MERGE",FACE,{"derivedFrom":[makeQuery(id+"F14.boolean.opBoolean","MERGE",FACE,{"derivedFrom":[makeQuery(id+"F13.boolean.opBoolean","MERGE",FACE,{"derivedFrom":[makeQuery(id+"F12.boolean.opBoolean","MERGE",FACE,{"derivedFrom":[makeQuery(id+"F11.boolean.opBoolean","MERGE",FACE,{"derivedFrom":[makeQuery(id+"F10.boolean.opBoolean","MERGE",FACE,{"derivedFrom":[makeQuery(id+"F9.boolean.opBoolean","MERGE",FACE,{"derivedFrom":[makeQuery(id+"F8.boolean.opBoolean","MERGE",FACE,{"derivedFrom":[makeQuery(id+"F7.boolean.opBoolean","MERGE",FACE,{"derivedFrom":[makeQuery(id+"F6.boolean.opBoolean","MERGE",FACE,{"derivedFrom":[makeQuery(id+"F5.boolean.opBoolean","MERGE",FACE,{"derivedFrom":[makeQuery(id+"F1.opRevolve","SWEPT_FACE",FACE,{"disambiguationData":[OSD([sQuery(id+"F0.wireOp",EDGE,"E5")])]}),makeQuery(id+"F5.opLoft","CAP_FACE",FACE,{"disambiguationData":[OSD([makeQuery(id+"F4.imprint","IMPRINT",FACE,{"disambiguationData":[TD([[makeQuery(id+"F4.imprint","IMPRINT",EDGE,{"derivedFrom":sQuery(id+"F4.wireOp",EDGE,"E21")}),1.0]])]})])],"isStart":true})]}),makeQuery(id+"F6.opLoft","CAP_FACE",FACE,{"disambiguationData":[OSD([makeQuery(id+"F4.imprint","IMPRINT",FACE,{"disambiguationData":[TD([[makeQuery(id+"F4.imprint","IMPRINT",EDGE,{"derivedFrom":sQuery(id+"F4.wireOp",EDGE,"E26.15.0")}),1.0]])]})])],"isStart":true})]}),makeQuery(id+"F7.opLoft","CAP_FACE",FACE,{"disambiguationData":[OSD([makeQuery(id+"F4.imprint","IMPRINT",FACE,{"disambiguationData":[TD([[makeQuery(id+"F4.imprint","IMPRINT",EDGE,{"derivedFrom":sQuery(id+"F4.wireOp",EDGE,"E26.14.0")}),1.0]])]})])],"isStart":true})]}),makeQuery(id+"F8.opLoft","CAP_FACE",FACE,{"disambiguationData":[OSD([makeQuery(id+"F4.imprint","IMPRINT",FACE,{"disambiguationData":[TD([[makeQuery(id+"F4.imprint","IMPRINT",EDGE,{"derivedFrom":sQuery(id+"F4.wireOp",EDGE,"E26.13.0")}),1.0]])]})])],"isStart":true})]}),makeQuery(id+"F9.opLoft","CAP_FACE",FACE,{"disambiguationData":[OSD([makeQuery(id+"F4.imprint","IMPRINT",FACE,{"disambiguationData":[TD([[makeQuery(id+"F4.imprint","IMPRINT",EDGE,{"derivedFrom":sQuery(id+"F4.wireOp",EDGE,"E26.12.0")}),1.0]])]})])],"isStart":true})]}),makeQuery(id+"F10.opLoft","CAP_FACE",FACE,{"disambiguationData":[OSD([makeQuery(id+"F4.imprint","IMPRINT",FACE,{"disambiguationData":[TD([[makeQuery(id+"F4.imprint","IMPRINT",EDGE,{"derivedFrom":sQuery(id+"F4.wireOp",EDGE,"E26.11.0")}),1.0]])]})])],"isStart":true})]}),makeQuery(id+"F11.opLoft","CAP_FACE",FACE,{"disambiguationData":[OSD([makeQuery(id+"F4.imprint","IMPRINT",FACE,{"disambiguationData":[TD([[makeQuery(id+"F4.imprint","IMPRINT",EDGE,{"derivedFrom":sQuery(id+"F4.wireOp",EDGE,"E26.10.0")}),1.0]])]})])],"isStart":true})]}),makeQuery(id+"F12.opLoft","CAP_FACE",FACE,{"disambiguationData":[OSD([makeQuery(id+"F4.imprint","IMPRINT",FACE,{"disambiguationData":[TD([[makeQuery(id+"F4.imprint","IMPRINT",EDGE,{"derivedFrom":sQuery(id+"F4.wireOp",EDGE,"E26.9.0")}),1.0]])]})])],"isStart":true})]}),makeQuery(id+"F13.opLoft","CAP_FACE",FACE,{"disambiguationData":[OSD([makeQuery(id+"F4.imprint","IMPRINT",FACE,{"disambiguationData":[TD([[makeQuery(id+"F4.imprint","IMPRINT",EDGE,{"derivedFrom":sQuery(id+"F4.wireOp",EDGE,"E26.8.0")}),1.0]])]})])],"isStart":true})]}),makeQuery(id+"F14.opLoft","CAP_FACE",FACE,{"disambiguationData":[OSD([makeQuery(id+"F4.imprint","IMPRINT",FACE,{"disambiguationData":[TD([[makeQuery(id+"F4.imprint","IMPRINT",EDGE,{"derivedFrom":sQuery(id+"F4.wireOp",EDGE,"E26.7.0")}),1.0]])]})])],"isStart":true})]}),makeQuery(id+"F15.opLoft","CAP_FACE",FACE,{"disambiguationData":[OSD([makeQuery(id+"F4.imprint","IMPRINT",FACE,{"disambiguationData":[TD([[makeQuery(id+"F4.imprint","IMPRINT",EDGE,{"derivedFrom":sQuery(id+"F4.wireOp",EDGE,"E26.6.0")}),1.0]])]})])],"isStart":true})]}),makeQuery(id+"F16.opLoft","CAP_FACE",FACE,{"disambiguationData":[OSD([makeQuery(id+"F4.imprint","IMPRINT",FACE,{"disambiguationData":[TD([[makeQuery(id+"F4.imprint","IMPRINT",EDGE,{"derivedFrom":sQuery(id+"F4.wireOp",EDGE,"E26.5.0")}),1.0]])]})])],"isStart":true})]}),makeQuery(id+"F17.opLoft","CAP_FACE",FACE,{"disambiguationData":[OSD([makeQuery(id+"F4.imprint","IMPRINT",FACE,{"disambiguationData":[TD([[makeQuery(id+"F4.imprint","IMPRINT",EDGE,{"derivedFrom":sQuery(id+"F4.wireOp",EDGE,"E26.4.0")}),1.0]])]})])],"isStart":true})]}),makeQuery(id+"F18.opLoft","CAP_FACE",FACE,{"disambiguationData":[OSD([makeQuery(id+"F4.imprint","IMPRINT",FACE,{"disambiguationData":[TD([[makeQuery(id+"F4.imprint","IMPRINT",EDGE,{"derivedFrom":sQuery(id+"F4.wireOp",EDGE,"E26.3.0")}),1.0]])]})])],"isStart":true})]}),makeQuery(id+"F19.opLoft","CAP_FACE",FACE,{"disambiguationData":[OSD([makeQuery(id+"F4.imprint","IMPRINT",FACE,{"disambiguationData":[TD([[makeQuery(id+"F4.imprint","IMPRINT",EDGE,{"derivedFrom":sQuery(id+"F4.wireOp",EDGE,"E26.2.0")}),1.0]])]})])],"isStart":true})]}),makeQuery(id+"F20.opLoft","CAP_FACE",FACE,{"disambiguationData":[OSD([makeQuery(id+"F4.imprint","IMPRINT",FACE,{"disambiguationData":[TD([[makeQuery(id+"F4.imprint","IMPRINT",EDGE,{"derivedFrom":sQuery(id+"F4.wireOp",EDGE,"E26.1.0")}),1.0]])]})])],"isStart":true})]}),makeQuery(id+"F42.opRevolve","SWEPT_FACE",FACE,{"disambiguationData":[OSD([sQuery(id+"F41.wireOp",EDGE,"E32")])]})]});
            var Q11;
            Q11=makeQuery(id+"F42.boolean.opBoolean","INTERSECT",EDGE,{"disambiguationData":[OD(10.0)],"derivedFrom":[makeQuery(id+"F20.boolean.opBoolean","MERGE",FACE,{"derivedFrom":[makeQuery(id+"F19.boolean.opBoolean","MERGE",FACE,{"derivedFrom":[makeQuery(id+"F18.boolean.opBoolean","MERGE",FACE,{"derivedFrom":[makeQuery(id+"F17.boolean.opBoolean","MERGE",FACE,{"derivedFrom":[makeQuery(id+"F16.boolean.opBoolean","MERGE",FACE,{"derivedFrom":[makeQuery(id+"F15.boolean.opBoolean","MERGE",FACE,{"derivedFrom":[makeQuery(id+"F14.boolean.opBoolean","MERGE",FACE,{"derivedFrom":[makeQuery(id+"F13.boolean.opBoolean","MERGE",FACE,{"derivedFrom":[makeQuery(id+"F12.boolean.opBoolean","MERGE",FACE,{"derivedFrom":[makeQuery(id+"F11.boolean.opBoolean","MERGE",FACE,{"derivedFrom":[makeQuery(id+"F10.boolean.opBoolean","MERGE",FACE,{"derivedFrom":[makeQuery(id+"F9.boolean.opBoolean","MERGE",FACE,{"derivedFrom":[makeQuery(id+"F8.boolean.opBoolean","MERGE",FACE,{"derivedFrom":[makeQuery(id+"F7.boolean.opBoolean","MERGE",FACE,{"derivedFrom":[makeQuery(id+"F6.boolean.opBoolean","MERGE",FACE,{"derivedFrom":[makeQuery(id+"F5.boolean.opBoolean","MERGE",FACE,{"derivedFrom":[makeQuery(id+"F1.opRevolve","SWEPT_FACE",FACE,{"disambiguationData":[OSD([sQuery(id+"F0.wireOp",EDGE,"E5")])]}),makeQuery(id+"F5.opLoft","CAP_FACE",FACE,{"disambiguationData":[OSD([makeQuery(id+"F4.imprint","IMPRINT",FACE,{"disambiguationData":[TD([[makeQuery(id+"F4.imprint","IMPRINT",EDGE,{"derivedFrom":sQuery(id+"F4.wireOp",EDGE,"E21")}),1.0]])]})])],"isStart":true})]}),makeQuery(id+"F6.opLoft","CAP_FACE",FACE,{"disambiguationData":[OSD([makeQuery(id+"F4.imprint","IMPRINT",FACE,{"disambiguationData":[TD([[makeQuery(id+"F4.imprint","IMPRINT",EDGE,{"derivedFrom":sQuery(id+"F4.wireOp",EDGE,"E26.15.0")}),1.0]])]})])],"isStart":true})]}),makeQuery(id+"F7.opLoft","CAP_FACE",FACE,{"disambiguationData":[OSD([makeQuery(id+"F4.imprint","IMPRINT",FACE,{"disambiguationData":[TD([[makeQuery(id+"F4.imprint","IMPRINT",EDGE,{"derivedFrom":sQuery(id+"F4.wireOp",EDGE,"E26.14.0")}),1.0]])]})])],"isStart":true})]}),makeQuery(id+"F8.opLoft","CAP_FACE",FACE,{"disambiguationData":[OSD([makeQuery(id+"F4.imprint","IMPRINT",FACE,{"disambiguationData":[TD([[makeQuery(id+"F4.imprint","IMPRINT",EDGE,{"derivedFrom":sQuery(id+"F4.wireOp",EDGE,"E26.13.0")}),1.0]])]})])],"isStart":true})]}),makeQuery(id+"F9.opLoft","CAP_FACE",FACE,{"disambiguationData":[OSD([makeQuery(id+"F4.imprint","IMPRINT",FACE,{"disambiguationData":[TD([[makeQuery(id+"F4.imprint","IMPRINT",EDGE,{"derivedFrom":sQuery(id+"F4.wireOp",EDGE,"E26.12.0")}),1.0]])]})])],"isStart":true})]}),makeQuery(id+"F10.opLoft","CAP_FACE",FACE,{"disambiguationData":[OSD([makeQuery(id+"F4.imprint","IMPRINT",FACE,{"disambiguationData":[TD([[makeQuery(id+"F4.imprint","IMPRINT",EDGE,{"derivedFrom":sQuery(id+"F4.wireOp",EDGE,"E26.11.0")}),1.0]])]})])],"isStart":true})]}),makeQuery(id+"F11.opLoft","CAP_FACE",FACE,{"disambiguationData":[OSD([makeQuery(id+"F4.imprint","IMPRINT",FACE,{"disambiguationData":[TD([[makeQuery(id+"F4.imprint","IMPRINT",EDGE,{"derivedFrom":sQuery(id+"F4.wireOp",EDGE,"E26.10.0")}),1.0]])]})])],"isStart":true})]}),makeQuery(id+"F12.opLoft","CAP_FACE",FACE,{"disambiguationData":[OSD([makeQuery(id+"F4.imprint","IMPRINT",FACE,{"disambiguationData":[TD([[makeQuery(id+"F4.imprint","IMPRINT",EDGE,{"derivedFrom":sQuery(id+"F4.wireOp",EDGE,"E26.9.0")}),1.0]])]})])],"isStart":true})]}),makeQuery(id+"F13.opLoft","CAP_FACE",FACE,{"disambiguationData":[OSD([makeQuery(id+"F4.imprint","IMPRINT",FACE,{"disambiguationData":[TD([[makeQuery(id+"F4.imprint","IMPRINT",EDGE,{"derivedFrom":sQuery(id+"F4.wireOp",EDGE,"E26.8.0")}),1.0]])]})])],"isStart":true})]}),makeQuery(id+"F14.opLoft","CAP_FACE",FACE,{"disambiguationData":[OSD([makeQuery(id+"F4.imprint","IMPRINT",FACE,{"disambiguationData":[TD([[makeQuery(id+"F4.imprint","IMPRINT",EDGE,{"derivedFrom":sQuery(id+"F4.wireOp",EDGE,"E26.7.0")}),1.0]])]})])],"isStart":true})]}),makeQuery(id+"F15.opLoft","CAP_FACE",FACE,{"disambiguationData":[OSD([makeQuery(id+"F4.imprint","IMPRINT",FACE,{"disambiguationData":[TD([[makeQuery(id+"F4.imprint","IMPRINT",EDGE,{"derivedFrom":sQuery(id+"F4.wireOp",EDGE,"E26.6.0")}),1.0]])]})])],"isStart":true})]}),makeQuery(id+"F16.opLoft","CAP_FACE",FACE,{"disambiguationData":[OSD([makeQuery(id+"F4.imprint","IMPRINT",FACE,{"disambiguationData":[TD([[makeQuery(id+"F4.imprint","IMPRINT",EDGE,{"derivedFrom":sQuery(id+"F4.wireOp",EDGE,"E26.5.0")}),1.0]])]})])],"isStart":true})]}),makeQuery(id+"F17.opLoft","CAP_FACE",FACE,{"disambiguationData":[OSD([makeQuery(id+"F4.imprint","IMPRINT",FACE,{"disambiguationData":[TD([[makeQuery(id+"F4.imprint","IMPRINT",EDGE,{"derivedFrom":sQuery(id+"F4.wireOp",EDGE,"E26.4.0")}),1.0]])]})])],"isStart":true})]}),makeQuery(id+"F18.opLoft","CAP_FACE",FACE,{"disambiguationData":[OSD([makeQuery(id+"F4.imprint","IMPRINT",FACE,{"disambiguationData":[TD([[makeQuery(id+"F4.imprint","IMPRINT",EDGE,{"derivedFrom":sQuery(id+"F4.wireOp",EDGE,"E26.3.0")}),1.0]])]})])],"isStart":true})]}),makeQuery(id+"F19.opLoft","CAP_FACE",FACE,{"disambiguationData":[OSD([makeQuery(id+"F4.imprint","IMPRINT",FACE,{"disambiguationData":[TD([[makeQuery(id+"F4.imprint","IMPRINT",EDGE,{"derivedFrom":sQuery(id+"F4.wireOp",EDGE,"E26.2.0")}),1.0]])]})])],"isStart":true})]}),makeQuery(id+"F20.opLoft","CAP_FACE",FACE,{"disambiguationData":[OSD([makeQuery(id+"F4.imprint","IMPRINT",FACE,{"disambiguationData":[TD([[makeQuery(id+"F4.imprint","IMPRINT",EDGE,{"derivedFrom":sQuery(id+"F4.wireOp",EDGE,"E26.1.0")}),1.0]])]})])],"isStart":true})]}),makeQuery(id+"F42.opRevolve","SWEPT_FACE",FACE,{"disambiguationData":[OSD([sQuery(id+"F41.wireOp",EDGE,"E32")])]})]});
            var Q12;
            Q12=makeQuery(id+"F42.boolean.opBoolean","INTERSECT",EDGE,{"disambiguationData":[OD(9.0)],"derivedFrom":[makeQuery(id+"F20.boolean.opBoolean","MERGE",FACE,{"derivedFrom":[makeQuery(id+"F19.boolean.opBoolean","MERGE",FACE,{"derivedFrom":[makeQuery(id+"F18.boolean.opBoolean","MERGE",FACE,{"derivedFrom":[makeQuery(id+"F17.boolean.opBoolean","MERGE",FACE,{"derivedFrom":[makeQuery(id+"F16.boolean.opBoolean","MERGE",FACE,{"derivedFrom":[makeQuery(id+"F15.boolean.opBoolean","MERGE",FACE,{"derivedFrom":[makeQuery(id+"F14.boolean.opBoolean","MERGE",FACE,{"derivedFrom":[makeQuery(id+"F13.boolean.opBoolean","MERGE",FACE,{"derivedFrom":[makeQuery(id+"F12.boolean.opBoolean","MERGE",FACE,{"derivedFrom":[makeQuery(id+"F11.boolean.opBoolean","MERGE",FACE,{"derivedFrom":[makeQuery(id+"F10.boolean.opBoolean","MERGE",FACE,{"derivedFrom":[makeQuery(id+"F9.boolean.opBoolean","MERGE",FACE,{"derivedFrom":[makeQuery(id+"F8.boolean.opBoolean","MERGE",FACE,{"derivedFrom":[makeQuery(id+"F7.boolean.opBoolean","MERGE",FACE,{"derivedFrom":[makeQuery(id+"F6.boolean.opBoolean","MERGE",FACE,{"derivedFrom":[makeQuery(id+"F5.boolean.opBoolean","MERGE",FACE,{"derivedFrom":[makeQuery(id+"F1.opRevolve","SWEPT_FACE",FACE,{"disambiguationData":[OSD([sQuery(id+"F0.wireOp",EDGE,"E5")])]}),makeQuery(id+"F5.opLoft","CAP_FACE",FACE,{"disambiguationData":[OSD([makeQuery(id+"F4.imprint","IMPRINT",FACE,{"disambiguationData":[TD([[makeQuery(id+"F4.imprint","IMPRINT",EDGE,{"derivedFrom":sQuery(id+"F4.wireOp",EDGE,"E21")}),1.0]])]})])],"isStart":true})]}),makeQuery(id+"F6.opLoft","CAP_FACE",FACE,{"disambiguationData":[OSD([makeQuery(id+"F4.imprint","IMPRINT",FACE,{"disambiguationData":[TD([[makeQuery(id+"F4.imprint","IMPRINT",EDGE,{"derivedFrom":sQuery(id+"F4.wireOp",EDGE,"E26.15.0")}),1.0]])]})])],"isStart":true})]}),makeQuery(id+"F7.opLoft","CAP_FACE",FACE,{"disambiguationData":[OSD([makeQuery(id+"F4.imprint","IMPRINT",FACE,{"disambiguationData":[TD([[makeQuery(id+"F4.imprint","IMPRINT",EDGE,{"derivedFrom":sQuery(id+"F4.wireOp",EDGE,"E26.14.0")}),1.0]])]})])],"isStart":true})]}),makeQuery(id+"F8.opLoft","CAP_FACE",FACE,{"disambiguationData":[OSD([makeQuery(id+"F4.imprint","IMPRINT",FACE,{"disambiguationData":[TD([[makeQuery(id+"F4.imprint","IMPRINT",EDGE,{"derivedFrom":sQuery(id+"F4.wireOp",EDGE,"E26.13.0")}),1.0]])]})])],"isStart":true})]}),makeQuery(id+"F9.opLoft","CAP_FACE",FACE,{"disambiguationData":[OSD([makeQuery(id+"F4.imprint","IMPRINT",FACE,{"disambiguationData":[TD([[makeQuery(id+"F4.imprint","IMPRINT",EDGE,{"derivedFrom":sQuery(id+"F4.wireOp",EDGE,"E26.12.0")}),1.0]])]})])],"isStart":true})]}),makeQuery(id+"F10.opLoft","CAP_FACE",FACE,{"disambiguationData":[OSD([makeQuery(id+"F4.imprint","IMPRINT",FACE,{"disambiguationData":[TD([[makeQuery(id+"F4.imprint","IMPRINT",EDGE,{"derivedFrom":sQuery(id+"F4.wireOp",EDGE,"E26.11.0")}),1.0]])]})])],"isStart":true})]}),makeQuery(id+"F11.opLoft","CAP_FACE",FACE,{"disambiguationData":[OSD([makeQuery(id+"F4.imprint","IMPRINT",FACE,{"disambiguationData":[TD([[makeQuery(id+"F4.imprint","IMPRINT",EDGE,{"derivedFrom":sQuery(id+"F4.wireOp",EDGE,"E26.10.0")}),1.0]])]})])],"isStart":true})]}),makeQuery(id+"F12.opLoft","CAP_FACE",FACE,{"disambiguationData":[OSD([makeQuery(id+"F4.imprint","IMPRINT",FACE,{"disambiguationData":[TD([[makeQuery(id+"F4.imprint","IMPRINT",EDGE,{"derivedFrom":sQuery(id+"F4.wireOp",EDGE,"E26.9.0")}),1.0]])]})])],"isStart":true})]}),makeQuery(id+"F13.opLoft","CAP_FACE",FACE,{"disambiguationData":[OSD([makeQuery(id+"F4.imprint","IMPRINT",FACE,{"disambiguationData":[TD([[makeQuery(id+"F4.imprint","IMPRINT",EDGE,{"derivedFrom":sQuery(id+"F4.wireOp",EDGE,"E26.8.0")}),1.0]])]})])],"isStart":true})]}),makeQuery(id+"F14.opLoft","CAP_FACE",FACE,{"disambiguationData":[OSD([makeQuery(id+"F4.imprint","IMPRINT",FACE,{"disambiguationData":[TD([[makeQuery(id+"F4.imprint","IMPRINT",EDGE,{"derivedFrom":sQuery(id+"F4.wireOp",EDGE,"E26.7.0")}),1.0]])]})])],"isStart":true})]}),makeQuery(id+"F15.opLoft","CAP_FACE",FACE,{"disambiguationData":[OSD([makeQuery(id+"F4.imprint","IMPRINT",FACE,{"disambiguationData":[TD([[makeQuery(id+"F4.imprint","IMPRINT",EDGE,{"derivedFrom":sQuery(id+"F4.wireOp",EDGE,"E26.6.0")}),1.0]])]})])],"isStart":true})]}),makeQuery(id+"F16.opLoft","CAP_FACE",FACE,{"disambiguationData":[OSD([makeQuery(id+"F4.imprint","IMPRINT",FACE,{"disambiguationData":[TD([[makeQuery(id+"F4.imprint","IMPRINT",EDGE,{"derivedFrom":sQuery(id+"F4.wireOp",EDGE,"E26.5.0")}),1.0]])]})])],"isStart":true})]}),makeQuery(id+"F17.opLoft","CAP_FACE",FACE,{"disambiguationData":[OSD([makeQuery(id+"F4.imprint","IMPRINT",FACE,{"disambiguationData":[TD([[makeQuery(id+"F4.imprint","IMPRINT",EDGE,{"derivedFrom":sQuery(id+"F4.wireOp",EDGE,"E26.4.0")}),1.0]])]})])],"isStart":true})]}),makeQuery(id+"F18.opLoft","CAP_FACE",FACE,{"disambiguationData":[OSD([makeQuery(id+"F4.imprint","IMPRINT",FACE,{"disambiguationData":[TD([[makeQuery(id+"F4.imprint","IMPRINT",EDGE,{"derivedFrom":sQuery(id+"F4.wireOp",EDGE,"E26.3.0")}),1.0]])]})])],"isStart":true})]}),makeQuery(id+"F19.opLoft","CAP_FACE",FACE,{"disambiguationData":[OSD([makeQuery(id+"F4.imprint","IMPRINT",FACE,{"disambiguationData":[TD([[makeQuery(id+"F4.imprint","IMPRINT",EDGE,{"derivedFrom":sQuery(id+"F4.wireOp",EDGE,"E26.2.0")}),1.0]])]})])],"isStart":true})]}),makeQuery(id+"F20.opLoft","CAP_FACE",FACE,{"disambiguationData":[OSD([makeQuery(id+"F4.imprint","IMPRINT",FACE,{"disambiguationData":[TD([[makeQuery(id+"F4.imprint","IMPRINT",EDGE,{"derivedFrom":sQuery(id+"F4.wireOp",EDGE,"E26.1.0")}),1.0]])]})])],"isStart":true})]}),makeQuery(id+"F42.opRevolve","SWEPT_FACE",FACE,{"disambiguationData":[OSD([sQuery(id+"F41.wireOp",EDGE,"E32")])]})]});
            var Q13;
            Q13=makeQuery(id+"F42.boolean.opBoolean","INTERSECT",EDGE,{"disambiguationData":[OD(8.0)],"derivedFrom":[makeQuery(id+"F20.boolean.opBoolean","MERGE",FACE,{"derivedFrom":[makeQuery(id+"F19.boolean.opBoolean","MERGE",FACE,{"derivedFrom":[makeQuery(id+"F18.boolean.opBoolean","MERGE",FACE,{"derivedFrom":[makeQuery(id+"F17.boolean.opBoolean","MERGE",FACE,{"derivedFrom":[makeQuery(id+"F16.boolean.opBoolean","MERGE",FACE,{"derivedFrom":[makeQuery(id+"F15.boolean.opBoolean","MERGE",FACE,{"derivedFrom":[makeQuery(id+"F14.boolean.opBoolean","MERGE",FACE,{"derivedFrom":[makeQuery(id+"F13.boolean.opBoolean","MERGE",FACE,{"derivedFrom":[makeQuery(id+"F12.boolean.opBoolean","MERGE",FACE,{"derivedFrom":[makeQuery(id+"F11.boolean.opBoolean","MERGE",FACE,{"derivedFrom":[makeQuery(id+"F10.boolean.opBoolean","MERGE",FACE,{"derivedFrom":[makeQuery(id+"F9.boolean.opBoolean","MERGE",FACE,{"derivedFrom":[makeQuery(id+"F8.boolean.opBoolean","MERGE",FACE,{"derivedFrom":[makeQuery(id+"F7.boolean.opBoolean","MERGE",FACE,{"derivedFrom":[makeQuery(id+"F6.boolean.opBoolean","MERGE",FACE,{"derivedFrom":[makeQuery(id+"F5.boolean.opBoolean","MERGE",FACE,{"derivedFrom":[makeQuery(id+"F1.opRevolve","SWEPT_FACE",FACE,{"disambiguationData":[OSD([sQuery(id+"F0.wireOp",EDGE,"E5")])]}),makeQuery(id+"F5.opLoft","CAP_FACE",FACE,{"disambiguationData":[OSD([makeQuery(id+"F4.imprint","IMPRINT",FACE,{"disambiguationData":[TD([[makeQuery(id+"F4.imprint","IMPRINT",EDGE,{"derivedFrom":sQuery(id+"F4.wireOp",EDGE,"E21")}),1.0]])]})])],"isStart":true})]}),makeQuery(id+"F6.opLoft","CAP_FACE",FACE,{"disambiguationData":[OSD([makeQuery(id+"F4.imprint","IMPRINT",FACE,{"disambiguationData":[TD([[makeQuery(id+"F4.imprint","IMPRINT",EDGE,{"derivedFrom":sQuery(id+"F4.wireOp",EDGE,"E26.15.0")}),1.0]])]})])],"isStart":true})]}),makeQuery(id+"F7.opLoft","CAP_FACE",FACE,{"disambiguationData":[OSD([makeQuery(id+"F4.imprint","IMPRINT",FACE,{"disambiguationData":[TD([[makeQuery(id+"F4.imprint","IMPRINT",EDGE,{"derivedFrom":sQuery(id+"F4.wireOp",EDGE,"E26.14.0")}),1.0]])]})])],"isStart":true})]}),makeQuery(id+"F8.opLoft","CAP_FACE",FACE,{"disambiguationData":[OSD([makeQuery(id+"F4.imprint","IMPRINT",FACE,{"disambiguationData":[TD([[makeQuery(id+"F4.imprint","IMPRINT",EDGE,{"derivedFrom":sQuery(id+"F4.wireOp",EDGE,"E26.13.0")}),1.0]])]})])],"isStart":true})]}),makeQuery(id+"F9.opLoft","CAP_FACE",FACE,{"disambiguationData":[OSD([makeQuery(id+"F4.imprint","IMPRINT",FACE,{"disambiguationData":[TD([[makeQuery(id+"F4.imprint","IMPRINT",EDGE,{"derivedFrom":sQuery(id+"F4.wireOp",EDGE,"E26.12.0")}),1.0]])]})])],"isStart":true})]}),makeQuery(id+"F10.opLoft","CAP_FACE",FACE,{"disambiguationData":[OSD([makeQuery(id+"F4.imprint","IMPRINT",FACE,{"disambiguationData":[TD([[makeQuery(id+"F4.imprint","IMPRINT",EDGE,{"derivedFrom":sQuery(id+"F4.wireOp",EDGE,"E26.11.0")}),1.0]])]})])],"isStart":true})]}),makeQuery(id+"F11.opLoft","CAP_FACE",FACE,{"disambiguationData":[OSD([makeQuery(id+"F4.imprint","IMPRINT",FACE,{"disambiguationData":[TD([[makeQuery(id+"F4.imprint","IMPRINT",EDGE,{"derivedFrom":sQuery(id+"F4.wireOp",EDGE,"E26.10.0")}),1.0]])]})])],"isStart":true})]}),makeQuery(id+"F12.opLoft","CAP_FACE",FACE,{"disambiguationData":[OSD([makeQuery(id+"F4.imprint","IMPRINT",FACE,{"disambiguationData":[TD([[makeQuery(id+"F4.imprint","IMPRINT",EDGE,{"derivedFrom":sQuery(id+"F4.wireOp",EDGE,"E26.9.0")}),1.0]])]})])],"isStart":true})]}),makeQuery(id+"F13.opLoft","CAP_FACE",FACE,{"disambiguationData":[OSD([makeQuery(id+"F4.imprint","IMPRINT",FACE,{"disambiguationData":[TD([[makeQuery(id+"F4.imprint","IMPRINT",EDGE,{"derivedFrom":sQuery(id+"F4.wireOp",EDGE,"E26.8.0")}),1.0]])]})])],"isStart":true})]}),makeQuery(id+"F14.opLoft","CAP_FACE",FACE,{"disambiguationData":[OSD([makeQuery(id+"F4.imprint","IMPRINT",FACE,{"disambiguationData":[TD([[makeQuery(id+"F4.imprint","IMPRINT",EDGE,{"derivedFrom":sQuery(id+"F4.wireOp",EDGE,"E26.7.0")}),1.0]])]})])],"isStart":true})]}),makeQuery(id+"F15.opLoft","CAP_FACE",FACE,{"disambiguationData":[OSD([makeQuery(id+"F4.imprint","IMPRINT",FACE,{"disambiguationData":[TD([[makeQuery(id+"F4.imprint","IMPRINT",EDGE,{"derivedFrom":sQuery(id+"F4.wireOp",EDGE,"E26.6.0")}),1.0]])]})])],"isStart":true})]}),makeQuery(id+"F16.opLoft","CAP_FACE",FACE,{"disambiguationData":[OSD([makeQuery(id+"F4.imprint","IMPRINT",FACE,{"disambiguationData":[TD([[makeQuery(id+"F4.imprint","IMPRINT",EDGE,{"derivedFrom":sQuery(id+"F4.wireOp",EDGE,"E26.5.0")}),1.0]])]})])],"isStart":true})]}),makeQuery(id+"F17.opLoft","CAP_FACE",FACE,{"disambiguationData":[OSD([makeQuery(id+"F4.imprint","IMPRINT",FACE,{"disambiguationData":[TD([[makeQuery(id+"F4.imprint","IMPRINT",EDGE,{"derivedFrom":sQuery(id+"F4.wireOp",EDGE,"E26.4.0")}),1.0]])]})])],"isStart":true})]}),makeQuery(id+"F18.opLoft","CAP_FACE",FACE,{"disambiguationData":[OSD([makeQuery(id+"F4.imprint","IMPRINT",FACE,{"disambiguationData":[TD([[makeQuery(id+"F4.imprint","IMPRINT",EDGE,{"derivedFrom":sQuery(id+"F4.wireOp",EDGE,"E26.3.0")}),1.0]])]})])],"isStart":true})]}),makeQuery(id+"F19.opLoft","CAP_FACE",FACE,{"disambiguationData":[OSD([makeQuery(id+"F4.imprint","IMPRINT",FACE,{"disambiguationData":[TD([[makeQuery(id+"F4.imprint","IMPRINT",EDGE,{"derivedFrom":sQuery(id+"F4.wireOp",EDGE,"E26.2.0")}),1.0]])]})])],"isStart":true})]}),makeQuery(id+"F20.opLoft","CAP_FACE",FACE,{"disambiguationData":[OSD([makeQuery(id+"F4.imprint","IMPRINT",FACE,{"disambiguationData":[TD([[makeQuery(id+"F4.imprint","IMPRINT",EDGE,{"derivedFrom":sQuery(id+"F4.wireOp",EDGE,"E26.1.0")}),1.0]])]})])],"isStart":true})]}),makeQuery(id+"F42.opRevolve","SWEPT_FACE",FACE,{"disambiguationData":[OSD([sQuery(id+"F41.wireOp",EDGE,"E32")])]})]});
            var Q14;
            Q14=makeQuery(id+"F42.boolean.opBoolean","INTERSECT",EDGE,{"disambiguationData":[OD(7.0)],"derivedFrom":[makeQuery(id+"F20.boolean.opBoolean","MERGE",FACE,{"derivedFrom":[makeQuery(id+"F19.boolean.opBoolean","MERGE",FACE,{"derivedFrom":[makeQuery(id+"F18.boolean.opBoolean","MERGE",FACE,{"derivedFrom":[makeQuery(id+"F17.boolean.opBoolean","MERGE",FACE,{"derivedFrom":[makeQuery(id+"F16.boolean.opBoolean","MERGE",FACE,{"derivedFrom":[makeQuery(id+"F15.boolean.opBoolean","MERGE",FACE,{"derivedFrom":[makeQuery(id+"F14.boolean.opBoolean","MERGE",FACE,{"derivedFrom":[makeQuery(id+"F13.boolean.opBoolean","MERGE",FACE,{"derivedFrom":[makeQuery(id+"F12.boolean.opBoolean","MERGE",FACE,{"derivedFrom":[makeQuery(id+"F11.boolean.opBoolean","MERGE",FACE,{"derivedFrom":[makeQuery(id+"F10.boolean.opBoolean","MERGE",FACE,{"derivedFrom":[makeQuery(id+"F9.boolean.opBoolean","MERGE",FACE,{"derivedFrom":[makeQuery(id+"F8.boolean.opBoolean","MERGE",FACE,{"derivedFrom":[makeQuery(id+"F7.boolean.opBoolean","MERGE",FACE,{"derivedFrom":[makeQuery(id+"F6.boolean.opBoolean","MERGE",FACE,{"derivedFrom":[makeQuery(id+"F5.boolean.opBoolean","MERGE",FACE,{"derivedFrom":[makeQuery(id+"F1.opRevolve","SWEPT_FACE",FACE,{"disambiguationData":[OSD([sQuery(id+"F0.wireOp",EDGE,"E5")])]}),makeQuery(id+"F5.opLoft","CAP_FACE",FACE,{"disambiguationData":[OSD([makeQuery(id+"F4.imprint","IMPRINT",FACE,{"disambiguationData":[TD([[makeQuery(id+"F4.imprint","IMPRINT",EDGE,{"derivedFrom":sQuery(id+"F4.wireOp",EDGE,"E21")}),1.0]])]})])],"isStart":true})]}),makeQuery(id+"F6.opLoft","CAP_FACE",FACE,{"disambiguationData":[OSD([makeQuery(id+"F4.imprint","IMPRINT",FACE,{"disambiguationData":[TD([[makeQuery(id+"F4.imprint","IMPRINT",EDGE,{"derivedFrom":sQuery(id+"F4.wireOp",EDGE,"E26.15.0")}),1.0]])]})])],"isStart":true})]}),makeQuery(id+"F7.opLoft","CAP_FACE",FACE,{"disambiguationData":[OSD([makeQuery(id+"F4.imprint","IMPRINT",FACE,{"disambiguationData":[TD([[makeQuery(id+"F4.imprint","IMPRINT",EDGE,{"derivedFrom":sQuery(id+"F4.wireOp",EDGE,"E26.14.0")}),1.0]])]})])],"isStart":true})]}),makeQuery(id+"F8.opLoft","CAP_FACE",FACE,{"disambiguationData":[OSD([makeQuery(id+"F4.imprint","IMPRINT",FACE,{"disambiguationData":[TD([[makeQuery(id+"F4.imprint","IMPRINT",EDGE,{"derivedFrom":sQuery(id+"F4.wireOp",EDGE,"E26.13.0")}),1.0]])]})])],"isStart":true})]}),makeQuery(id+"F9.opLoft","CAP_FACE",FACE,{"disambiguationData":[OSD([makeQuery(id+"F4.imprint","IMPRINT",FACE,{"disambiguationData":[TD([[makeQuery(id+"F4.imprint","IMPRINT",EDGE,{"derivedFrom":sQuery(id+"F4.wireOp",EDGE,"E26.12.0")}),1.0]])]})])],"isStart":true})]}),makeQuery(id+"F10.opLoft","CAP_FACE",FACE,{"disambiguationData":[OSD([makeQuery(id+"F4.imprint","IMPRINT",FACE,{"disambiguationData":[TD([[makeQuery(id+"F4.imprint","IMPRINT",EDGE,{"derivedFrom":sQuery(id+"F4.wireOp",EDGE,"E26.11.0")}),1.0]])]})])],"isStart":true})]}),makeQuery(id+"F11.opLoft","CAP_FACE",FACE,{"disambiguationData":[OSD([makeQuery(id+"F4.imprint","IMPRINT",FACE,{"disambiguationData":[TD([[makeQuery(id+"F4.imprint","IMPRINT",EDGE,{"derivedFrom":sQuery(id+"F4.wireOp",EDGE,"E26.10.0")}),1.0]])]})])],"isStart":true})]}),makeQuery(id+"F12.opLoft","CAP_FACE",FACE,{"disambiguationData":[OSD([makeQuery(id+"F4.imprint","IMPRINT",FACE,{"disambiguationData":[TD([[makeQuery(id+"F4.imprint","IMPRINT",EDGE,{"derivedFrom":sQuery(id+"F4.wireOp",EDGE,"E26.9.0")}),1.0]])]})])],"isStart":true})]}),makeQuery(id+"F13.opLoft","CAP_FACE",FACE,{"disambiguationData":[OSD([makeQuery(id+"F4.imprint","IMPRINT",FACE,{"disambiguationData":[TD([[makeQuery(id+"F4.imprint","IMPRINT",EDGE,{"derivedFrom":sQuery(id+"F4.wireOp",EDGE,"E26.8.0")}),1.0]])]})])],"isStart":true})]}),makeQuery(id+"F14.opLoft","CAP_FACE",FACE,{"disambiguationData":[OSD([makeQuery(id+"F4.imprint","IMPRINT",FACE,{"disambiguationData":[TD([[makeQuery(id+"F4.imprint","IMPRINT",EDGE,{"derivedFrom":sQuery(id+"F4.wireOp",EDGE,"E26.7.0")}),1.0]])]})])],"isStart":true})]}),makeQuery(id+"F15.opLoft","CAP_FACE",FACE,{"disambiguationData":[OSD([makeQuery(id+"F4.imprint","IMPRINT",FACE,{"disambiguationData":[TD([[makeQuery(id+"F4.imprint","IMPRINT",EDGE,{"derivedFrom":sQuery(id+"F4.wireOp",EDGE,"E26.6.0")}),1.0]])]})])],"isStart":true})]}),makeQuery(id+"F16.opLoft","CAP_FACE",FACE,{"disambiguationData":[OSD([makeQuery(id+"F4.imprint","IMPRINT",FACE,{"disambiguationData":[TD([[makeQuery(id+"F4.imprint","IMPRINT",EDGE,{"derivedFrom":sQuery(id+"F4.wireOp",EDGE,"E26.5.0")}),1.0]])]})])],"isStart":true})]}),makeQuery(id+"F17.opLoft","CAP_FACE",FACE,{"disambiguationData":[OSD([makeQuery(id+"F4.imprint","IMPRINT",FACE,{"disambiguationData":[TD([[makeQuery(id+"F4.imprint","IMPRINT",EDGE,{"derivedFrom":sQuery(id+"F4.wireOp",EDGE,"E26.4.0")}),1.0]])]})])],"isStart":true})]}),makeQuery(id+"F18.opLoft","CAP_FACE",FACE,{"disambiguationData":[OSD([makeQuery(id+"F4.imprint","IMPRINT",FACE,{"disambiguationData":[TD([[makeQuery(id+"F4.imprint","IMPRINT",EDGE,{"derivedFrom":sQuery(id+"F4.wireOp",EDGE,"E26.3.0")}),1.0]])]})])],"isStart":true})]}),makeQuery(id+"F19.opLoft","CAP_FACE",FACE,{"disambiguationData":[OSD([makeQuery(id+"F4.imprint","IMPRINT",FACE,{"disambiguationData":[TD([[makeQuery(id+"F4.imprint","IMPRINT",EDGE,{"derivedFrom":sQuery(id+"F4.wireOp",EDGE,"E26.2.0")}),1.0]])]})])],"isStart":true})]}),makeQuery(id+"F20.opLoft","CAP_FACE",FACE,{"disambiguationData":[OSD([makeQuery(id+"F4.imprint","IMPRINT",FACE,{"disambiguationData":[TD([[makeQuery(id+"F4.imprint","IMPRINT",EDGE,{"derivedFrom":sQuery(id+"F4.wireOp",EDGE,"E26.1.0")}),1.0]])]})])],"isStart":true})]}),makeQuery(id+"F42.opRevolve","SWEPT_FACE",FACE,{"disambiguationData":[OSD([sQuery(id+"F41.wireOp",EDGE,"E32")])]})]});
            var Q15;
            Q15=makeQuery(id+"F42.boolean.opBoolean","INTERSECT",EDGE,{"disambiguationData":[OD(6.0)],"derivedFrom":[makeQuery(id+"F20.boolean.opBoolean","MERGE",FACE,{"derivedFrom":[makeQuery(id+"F19.boolean.opBoolean","MERGE",FACE,{"derivedFrom":[makeQuery(id+"F18.boolean.opBoolean","MERGE",FACE,{"derivedFrom":[makeQuery(id+"F17.boolean.opBoolean","MERGE",FACE,{"derivedFrom":[makeQuery(id+"F16.boolean.opBoolean","MERGE",FACE,{"derivedFrom":[makeQuery(id+"F15.boolean.opBoolean","MERGE",FACE,{"derivedFrom":[makeQuery(id+"F14.boolean.opBoolean","MERGE",FACE,{"derivedFrom":[makeQuery(id+"F13.boolean.opBoolean","MERGE",FACE,{"derivedFrom":[makeQuery(id+"F12.boolean.opBoolean","MERGE",FACE,{"derivedFrom":[makeQuery(id+"F11.boolean.opBoolean","MERGE",FACE,{"derivedFrom":[makeQuery(id+"F10.boolean.opBoolean","MERGE",FACE,{"derivedFrom":[makeQuery(id+"F9.boolean.opBoolean","MERGE",FACE,{"derivedFrom":[makeQuery(id+"F8.boolean.opBoolean","MERGE",FACE,{"derivedFrom":[makeQuery(id+"F7.boolean.opBoolean","MERGE",FACE,{"derivedFrom":[makeQuery(id+"F6.boolean.opBoolean","MERGE",FACE,{"derivedFrom":[makeQuery(id+"F5.boolean.opBoolean","MERGE",FACE,{"derivedFrom":[makeQuery(id+"F1.opRevolve","SWEPT_FACE",FACE,{"disambiguationData":[OSD([sQuery(id+"F0.wireOp",EDGE,"E5")])]}),makeQuery(id+"F5.opLoft","CAP_FACE",FACE,{"disambiguationData":[OSD([makeQuery(id+"F4.imprint","IMPRINT",FACE,{"disambiguationData":[TD([[makeQuery(id+"F4.imprint","IMPRINT",EDGE,{"derivedFrom":sQuery(id+"F4.wireOp",EDGE,"E21")}),1.0]])]})])],"isStart":true})]}),makeQuery(id+"F6.opLoft","CAP_FACE",FACE,{"disambiguationData":[OSD([makeQuery(id+"F4.imprint","IMPRINT",FACE,{"disambiguationData":[TD([[makeQuery(id+"F4.imprint","IMPRINT",EDGE,{"derivedFrom":sQuery(id+"F4.wireOp",EDGE,"E26.15.0")}),1.0]])]})])],"isStart":true})]}),makeQuery(id+"F7.opLoft","CAP_FACE",FACE,{"disambiguationData":[OSD([makeQuery(id+"F4.imprint","IMPRINT",FACE,{"disambiguationData":[TD([[makeQuery(id+"F4.imprint","IMPRINT",EDGE,{"derivedFrom":sQuery(id+"F4.wireOp",EDGE,"E26.14.0")}),1.0]])]})])],"isStart":true})]}),makeQuery(id+"F8.opLoft","CAP_FACE",FACE,{"disambiguationData":[OSD([makeQuery(id+"F4.imprint","IMPRINT",FACE,{"disambiguationData":[TD([[makeQuery(id+"F4.imprint","IMPRINT",EDGE,{"derivedFrom":sQuery(id+"F4.wireOp",EDGE,"E26.13.0")}),1.0]])]})])],"isStart":true})]}),makeQuery(id+"F9.opLoft","CAP_FACE",FACE,{"disambiguationData":[OSD([makeQuery(id+"F4.imprint","IMPRINT",FACE,{"disambiguationData":[TD([[makeQuery(id+"F4.imprint","IMPRINT",EDGE,{"derivedFrom":sQuery(id+"F4.wireOp",EDGE,"E26.12.0")}),1.0]])]})])],"isStart":true})]}),makeQuery(id+"F10.opLoft","CAP_FACE",FACE,{"disambiguationData":[OSD([makeQuery(id+"F4.imprint","IMPRINT",FACE,{"disambiguationData":[TD([[makeQuery(id+"F4.imprint","IMPRINT",EDGE,{"derivedFrom":sQuery(id+"F4.wireOp",EDGE,"E26.11.0")}),1.0]])]})])],"isStart":true})]}),makeQuery(id+"F11.opLoft","CAP_FACE",FACE,{"disambiguationData":[OSD([makeQuery(id+"F4.imprint","IMPRINT",FACE,{"disambiguationData":[TD([[makeQuery(id+"F4.imprint","IMPRINT",EDGE,{"derivedFrom":sQuery(id+"F4.wireOp",EDGE,"E26.10.0")}),1.0]])]})])],"isStart":true})]}),makeQuery(id+"F12.opLoft","CAP_FACE",FACE,{"disambiguationData":[OSD([makeQuery(id+"F4.imprint","IMPRINT",FACE,{"disambiguationData":[TD([[makeQuery(id+"F4.imprint","IMPRINT",EDGE,{"derivedFrom":sQuery(id+"F4.wireOp",EDGE,"E26.9.0")}),1.0]])]})])],"isStart":true})]}),makeQuery(id+"F13.opLoft","CAP_FACE",FACE,{"disambiguationData":[OSD([makeQuery(id+"F4.imprint","IMPRINT",FACE,{"disambiguationData":[TD([[makeQuery(id+"F4.imprint","IMPRINT",EDGE,{"derivedFrom":sQuery(id+"F4.wireOp",EDGE,"E26.8.0")}),1.0]])]})])],"isStart":true})]}),makeQuery(id+"F14.opLoft","CAP_FACE",FACE,{"disambiguationData":[OSD([makeQuery(id+"F4.imprint","IMPRINT",FACE,{"disambiguationData":[TD([[makeQuery(id+"F4.imprint","IMPRINT",EDGE,{"derivedFrom":sQuery(id+"F4.wireOp",EDGE,"E26.7.0")}),1.0]])]})])],"isStart":true})]}),makeQuery(id+"F15.opLoft","CAP_FACE",FACE,{"disambiguationData":[OSD([makeQuery(id+"F4.imprint","IMPRINT",FACE,{"disambiguationData":[TD([[makeQuery(id+"F4.imprint","IMPRINT",EDGE,{"derivedFrom":sQuery(id+"F4.wireOp",EDGE,"E26.6.0")}),1.0]])]})])],"isStart":true})]}),makeQuery(id+"F16.opLoft","CAP_FACE",FACE,{"disambiguationData":[OSD([makeQuery(id+"F4.imprint","IMPRINT",FACE,{"disambiguationData":[TD([[makeQuery(id+"F4.imprint","IMPRINT",EDGE,{"derivedFrom":sQuery(id+"F4.wireOp",EDGE,"E26.5.0")}),1.0]])]})])],"isStart":true})]}),makeQuery(id+"F17.opLoft","CAP_FACE",FACE,{"disambiguationData":[OSD([makeQuery(id+"F4.imprint","IMPRINT",FACE,{"disambiguationData":[TD([[makeQuery(id+"F4.imprint","IMPRINT",EDGE,{"derivedFrom":sQuery(id+"F4.wireOp",EDGE,"E26.4.0")}),1.0]])]})])],"isStart":true})]}),makeQuery(id+"F18.opLoft","CAP_FACE",FACE,{"disambiguationData":[OSD([makeQuery(id+"F4.imprint","IMPRINT",FACE,{"disambiguationData":[TD([[makeQuery(id+"F4.imprint","IMPRINT",EDGE,{"derivedFrom":sQuery(id+"F4.wireOp",EDGE,"E26.3.0")}),1.0]])]})])],"isStart":true})]}),makeQuery(id+"F19.opLoft","CAP_FACE",FACE,{"disambiguationData":[OSD([makeQuery(id+"F4.imprint","IMPRINT",FACE,{"disambiguationData":[TD([[makeQuery(id+"F4.imprint","IMPRINT",EDGE,{"derivedFrom":sQuery(id+"F4.wireOp",EDGE,"E26.2.0")}),1.0]])]})])],"isStart":true})]}),makeQuery(id+"F20.opLoft","CAP_FACE",FACE,{"disambiguationData":[OSD([makeQuery(id+"F4.imprint","IMPRINT",FACE,{"disambiguationData":[TD([[makeQuery(id+"F4.imprint","IMPRINT",EDGE,{"derivedFrom":sQuery(id+"F4.wireOp",EDGE,"E26.1.0")}),1.0]])]})])],"isStart":true})]}),makeQuery(id+"F42.opRevolve","SWEPT_FACE",FACE,{"disambiguationData":[OSD([sQuery(id+"F41.wireOp",EDGE,"E32")])]})]});
            var Q16;
            Q16=makeQuery(id+"F42.boolean.opBoolean","INTERSECT",EDGE,{"derivedFrom":[makeQuery(id+"F27.opLoft","CAP_FACE",FACE,{"disambiguationData":[OSD([makeQuery(id+"F22.imprint","IMPRINT",FACE,{"disambiguationData":[TD([[makeQuery(id+"F22.imprint","IMPRINT",EDGE,{"derivedFrom":sQuery(id+"F22.wireOp",EDGE,"E28.4.0")}),-1.0]])]})])],"isStart":true}),makeQuery(id+"F42.opRevolve","SWEPT_FACE",FACE,{"disambiguationData":[OSD([sQuery(id+"F41.wireOp",EDGE,"E32")])]})]});
            var Q17;
            Q17=makeQuery(id+"F42.boolean.opBoolean","INTERSECT",EDGE,{"derivedFrom":[makeQuery(id+"F26.opLoft","CAP_FACE",FACE,{"disambiguationData":[OSD([makeQuery(id+"F22.imprint","IMPRINT",FACE,{"disambiguationData":[TD([[makeQuery(id+"F22.imprint","IMPRINT",EDGE,{"derivedFrom":sQuery(id+"F22.wireOp",EDGE,"E28.3.0")}),-1.0]])]})])],"isStart":true}),makeQuery(id+"F42.opRevolve","SWEPT_FACE",FACE,{"disambiguationData":[OSD([sQuery(id+"F41.wireOp",EDGE,"E32")])]})]});
            var Q18;
            Q18=makeQuery(id+"F42.boolean.opBoolean","INTERSECT",EDGE,{"derivedFrom":[makeQuery(id+"F25.opLoft","CAP_FACE",FACE,{"disambiguationData":[OSD([makeQuery(id+"F22.imprint","IMPRINT",FACE,{"disambiguationData":[TD([[makeQuery(id+"F22.imprint","IMPRINT",EDGE,{"derivedFrom":sQuery(id+"F22.wireOp",EDGE,"E28.2.0")}),-1.0]])]})])],"isStart":true}),makeQuery(id+"F42.opRevolve","SWEPT_FACE",FACE,{"disambiguationData":[OSD([sQuery(id+"F41.wireOp",EDGE,"E32")])]})]});
            var Q19;
            Q19=makeQuery(id+"F42.boolean.opBoolean","INTERSECT",EDGE,{"derivedFrom":[makeQuery(id+"F24.opLoft","CAP_FACE",FACE,{"disambiguationData":[OSD([makeQuery(id+"F22.imprint","IMPRINT",FACE,{"disambiguationData":[TD([[makeQuery(id+"F22.imprint","IMPRINT",EDGE,{"derivedFrom":sQuery(id+"F22.wireOp",EDGE,"E28.1.0")}),-1.0]])]})])],"isStart":true}),makeQuery(id+"F42.opRevolve","SWEPT_FACE",FACE,{"disambiguationData":[OSD([sQuery(id+"F41.wireOp",EDGE,"E32")])]})]});
            var Q20;
            Q20=makeQuery(id+"F42.boolean.opBoolean","INTERSECT",EDGE,{"derivedFrom":[makeQuery(id+"F23.opLoft","CAP_FACE",FACE,{"disambiguationData":[OSD([makeQuery(id+"F22.imprint","IMPRINT",FACE,{"disambiguationData":[TD([[makeQuery(id+"F22.imprint","IMPRINT",EDGE,{"derivedFrom":sQuery(id+"F22.wireOp",EDGE,"E27.bottom")}),1.0]])]})])],"isStart":true}),makeQuery(id+"F42.opRevolve","SWEPT_FACE",FACE,{"disambiguationData":[OSD([sQuery(id+"F41.wireOp",EDGE,"E32")])]})]});
            var Q21;
            Q21=makeQuery(id+"F42.boolean.opBoolean","INTERSECT",EDGE,{"derivedFrom":[makeQuery(id+"F38.opLoft","CAP_FACE",FACE,{"disambiguationData":[OSD([makeQuery(id+"F22.imprint","IMPRINT",FACE,{"disambiguationData":[TD([[makeQuery(id+"F22.imprint","IMPRINT",EDGE,{"derivedFrom":sQuery(id+"F22.wireOp",EDGE,"E28.15.0")}),-1.0]])]})])],"isStart":true}),makeQuery(id+"F42.opRevolve","SWEPT_FACE",FACE,{"disambiguationData":[OSD([sQuery(id+"F41.wireOp",EDGE,"E32")])]})]});
            var Q22;
            Q22=makeQuery(id+"F42.boolean.opBoolean","INTERSECT",EDGE,{"derivedFrom":[makeQuery(id+"F37.opLoft","CAP_FACE",FACE,{"disambiguationData":[OSD([makeQuery(id+"F22.imprint","IMPRINT",FACE,{"disambiguationData":[TD([[makeQuery(id+"F22.imprint","IMPRINT",EDGE,{"derivedFrom":sQuery(id+"F22.wireOp",EDGE,"E28.14.0")}),-1.0]])]})])],"isStart":true}),makeQuery(id+"F42.opRevolve","SWEPT_FACE",FACE,{"disambiguationData":[OSD([sQuery(id+"F41.wireOp",EDGE,"E32")])]})]});
            var Q23;
            Q23=makeQuery(id+"F42.boolean.opBoolean","INTERSECT",EDGE,{"derivedFrom":[makeQuery(id+"F36.opLoft","CAP_FACE",FACE,{"disambiguationData":[OSD([makeQuery(id+"F22.imprint","IMPRINT",FACE,{"disambiguationData":[TD([[makeQuery(id+"F22.imprint","IMPRINT",EDGE,{"derivedFrom":sQuery(id+"F22.wireOp",EDGE,"E28.13.0")}),-1.0]])]})])],"isStart":true}),makeQuery(id+"F42.opRevolve","SWEPT_FACE",FACE,{"disambiguationData":[OSD([sQuery(id+"F41.wireOp",EDGE,"E32")])]})]});
            var Q24;
            Q24=makeQuery(id+"F42.boolean.opBoolean","INTERSECT",EDGE,{"derivedFrom":[makeQuery(id+"F35.opLoft","CAP_FACE",FACE,{"disambiguationData":[OSD([makeQuery(id+"F22.imprint","IMPRINT",FACE,{"disambiguationData":[TD([[makeQuery(id+"F22.imprint","IMPRINT",EDGE,{"derivedFrom":sQuery(id+"F22.wireOp",EDGE,"E28.12.0")}),-1.0]])]})])],"isStart":true}),makeQuery(id+"F42.opRevolve","SWEPT_FACE",FACE,{"disambiguationData":[OSD([sQuery(id+"F41.wireOp",EDGE,"E32")])]})]});
            var Q25;
            Q25=makeQuery(id+"F42.boolean.opBoolean","INTERSECT",EDGE,{"derivedFrom":[makeQuery(id+"F34.opLoft","CAP_FACE",FACE,{"disambiguationData":[OSD([makeQuery(id+"F22.imprint","IMPRINT",FACE,{"disambiguationData":[TD([[makeQuery(id+"F22.imprint","IMPRINT",EDGE,{"derivedFrom":sQuery(id+"F22.wireOp",EDGE,"E28.11.0")}),-1.0]])]})])],"isStart":true}),makeQuery(id+"F42.opRevolve","SWEPT_FACE",FACE,{"disambiguationData":[OSD([sQuery(id+"F41.wireOp",EDGE,"E32")])]})]});
            var Q26;
            Q26=makeQuery(id+"F42.boolean.opBoolean","INTERSECT",EDGE,{"derivedFrom":[makeQuery(id+"F33.opLoft","CAP_FACE",FACE,{"disambiguationData":[OSD([makeQuery(id+"F22.imprint","IMPRINT",FACE,{"disambiguationData":[TD([[makeQuery(id+"F22.imprint","IMPRINT",EDGE,{"derivedFrom":sQuery(id+"F22.wireOp",EDGE,"E28.10.0")}),-1.0]])]})])],"isStart":true}),makeQuery(id+"F42.opRevolve","SWEPT_FACE",FACE,{"disambiguationData":[OSD([sQuery(id+"F41.wireOp",EDGE,"E32")])]})]});
            var Q27;
            Q27=makeQuery(id+"F42.boolean.opBoolean","INTERSECT",EDGE,{"derivedFrom":[makeQuery(id+"F32.opLoft","CAP_FACE",FACE,{"disambiguationData":[OSD([makeQuery(id+"F22.imprint","IMPRINT",FACE,{"disambiguationData":[TD([[makeQuery(id+"F22.imprint","IMPRINT",EDGE,{"derivedFrom":sQuery(id+"F22.wireOp",EDGE,"E28.9.0")}),-1.0]])]})])],"isStart":true}),makeQuery(id+"F42.opRevolve","SWEPT_FACE",FACE,{"disambiguationData":[OSD([sQuery(id+"F41.wireOp",EDGE,"E32")])]})]});
            var Q28;
            Q28=makeQuery(id+"F42.boolean.opBoolean","INTERSECT",EDGE,{"derivedFrom":[makeQuery(id+"F31.opLoft","CAP_FACE",FACE,{"disambiguationData":[OSD([makeQuery(id+"F22.imprint","IMPRINT",FACE,{"disambiguationData":[TD([[makeQuery(id+"F22.imprint","IMPRINT",EDGE,{"derivedFrom":sQuery(id+"F22.wireOp",EDGE,"E28.8.0")}),-1.0]])]})])],"isStart":true}),makeQuery(id+"F42.opRevolve","SWEPT_FACE",FACE,{"disambiguationData":[OSD([sQuery(id+"F41.wireOp",EDGE,"E32")])]})]});
            var Q29;
            Q29=makeQuery(id+"F42.boolean.opBoolean","INTERSECT",EDGE,{"derivedFrom":[makeQuery(id+"F30.opLoft","CAP_FACE",FACE,{"disambiguationData":[OSD([makeQuery(id+"F22.imprint","IMPRINT",FACE,{"disambiguationData":[TD([[makeQuery(id+"F22.imprint","IMPRINT",EDGE,{"derivedFrom":sQuery(id+"F22.wireOp",EDGE,"E28.7.0")}),-1.0]])]})])],"isStart":true}),makeQuery(id+"F42.opRevolve","SWEPT_FACE",FACE,{"disambiguationData":[OSD([sQuery(id+"F41.wireOp",EDGE,"E32")])]})]});
            var Q30;
            Q30=makeQuery(id+"F42.boolean.opBoolean","INTERSECT",EDGE,{"derivedFrom":[makeQuery(id+"F29.opLoft","CAP_FACE",FACE,{"disambiguationData":[OSD([makeQuery(id+"F22.imprint","IMPRINT",FACE,{"disambiguationData":[TD([[makeQuery(id+"F22.imprint","IMPRINT",EDGE,{"derivedFrom":sQuery(id+"F22.wireOp",EDGE,"E28.6.0")}),-1.0]])]})])],"isStart":true}),makeQuery(id+"F42.opRevolve","SWEPT_FACE",FACE,{"disambiguationData":[OSD([sQuery(id+"F41.wireOp",EDGE,"E32")])]})]});
            var Q31;
            Q31=makeQuery(id+"F42.boolean.opBoolean","INTERSECT",EDGE,{"derivedFrom":[makeQuery(id+"F28.opLoft","CAP_FACE",FACE,{"disambiguationData":[OSD([makeQuery(id+"F22.imprint","IMPRINT",FACE,{"disambiguationData":[TD([[makeQuery(id+"F22.imprint","IMPRINT",EDGE,{"derivedFrom":sQuery(id+"F22.wireOp",EDGE,"E28.5.0")}),-1.0]])]})])],"isStart":true}),makeQuery(id+"F42.opRevolve","SWEPT_FACE",FACE,{"disambiguationData":[OSD([sQuery(id+"F41.wireOp",EDGE,"E32")])]})]});
            fillet(context, id + "F43", {"entities" : qUnion([Q0, Q1, Q2, Q3, Q4, Q5, Q6, Q7, Q8, Q9, Q10, Q11, Q12, Q13, Q14, Q15, Q16, Q17, Q18, Q19, Q20, Q21, Q22, Q23, Q24, Q25, Q26, Q27, Q28, Q29, Q30, Q31]), "radius" : 10 * mm, "tangentPropagation" : true, "allowEdgeOverflow" : false});
        }
        {
            var Q0;
            Q0=makeQuery(id+"F40.boolean.opBoolean","INTERSECT",EDGE,{"derivedFrom":[makeQuery(id+"F20.opLoft","SWEPT_FACE",FACE,{"disambiguationData":[OSD([sQuery(id+"F3.wireOp",EDGE,"E20.1.1"),sQuery(id+"F3.wireOp",EDGE,"E20.1.2"),sQuery(id+"F3.wireOp",EDGE,"E20.1.3"),sQuery(id+"F4.wireOp",EDGE,"E26.1.1"),sQuery(id+"F4.wireOp",EDGE,"E26.1.2"),sQuery(id+"F4.wireOp",EDGE,"E26.1.3")])]}),makeQuery(id+"F40.opExtrude","CAP_FACE",FACE,{"disambiguationData":[OSD([sQuery(id+"F39.wireOp",EDGE,"E29"),sQuery(id+"F39.wireOp",EDGE,"E30")])],"isStart":false})]});
            var Q1;
            Q1=makeQuery(id+"F40.boolean.opBoolean","INTERSECT",EDGE,{"derivedFrom":[makeQuery(id+"F32.opLoft","SWEPT_FACE",FACE,{"disambiguationData":[OSD([sQuery(id+"F3.wireOp",EDGE,"E20.1.1"),sQuery(id+"F3.wireOp",EDGE,"E20.1.2"),sQuery(id+"F3.wireOp",EDGE,"E20.1.3"),sQuery(id+"F22.wireOp",EDGE,"E28.9.0"),sQuery(id+"F22.wireOp",EDGE,"E28.9.2"),sQuery(id+"F22.wireOp",EDGE,"E28.9.3")])]}),makeQuery(id+"F40.opExtrude","CAP_FACE",FACE,{"disambiguationData":[OSD([sQuery(id+"F39.wireOp",EDGE,"E29"),sQuery(id+"F39.wireOp",EDGE,"E30")])],"isStart":true})]});
            var Q2;
            Q2=makeQuery(id+"F40.boolean.opBoolean","INTERSECT",EDGE,{"derivedFrom":[makeQuery(id+"F5.opLoft","SWEPT_FACE",FACE,{"disambiguationData":[OSD([sQuery(id+"F3.wireOp",EDGE,"E18.bottom"),sQuery(id+"F3.wireOp",EDGE,"E18.top"),sQuery(id+"F3.wireOp",EDGE,"E18.right"),sQuery(id+"F4.wireOp",EDGE,"E22"),sQuery(id+"F4.wireOp",EDGE,"E23"),sQuery(id+"F4.wireOp",EDGE,"E24")])]}),makeQuery(id+"F40.opExtrude","CAP_FACE",FACE,{"disambiguationData":[OSD([sQuery(id+"F39.wireOp",EDGE,"E29"),sQuery(id+"F39.wireOp",EDGE,"E30")])],"isStart":false})]});
            var Q3;
            Q3=makeQuery(id+"F40.boolean.opBoolean","INTERSECT",EDGE,{"derivedFrom":[makeQuery(id+"F31.opLoft","SWEPT_FACE",FACE,{"disambiguationData":[OSD([sQuery(id+"F3.wireOp",EDGE,"E18.bottom"),sQuery(id+"F3.wireOp",EDGE,"E18.top"),sQuery(id+"F3.wireOp",EDGE,"E18.right"),sQuery(id+"F22.wireOp",EDGE,"E28.8.0"),sQuery(id+"F22.wireOp",EDGE,"E28.8.2"),sQuery(id+"F22.wireOp",EDGE,"E28.8.3")])]}),makeQuery(id+"F40.opExtrude","CAP_FACE",FACE,{"disambiguationData":[OSD([sQuery(id+"F39.wireOp",EDGE,"E29"),sQuery(id+"F39.wireOp",EDGE,"E30")])],"isStart":true})]});
            var Q4;
            Q4=makeQuery(id+"F40.boolean.opBoolean","INTERSECT",EDGE,{"derivedFrom":[makeQuery(id+"F6.opLoft","SWEPT_FACE",FACE,{"disambiguationData":[OSD([sQuery(id+"F3.wireOp",EDGE,"E20.15.1"),sQuery(id+"F3.wireOp",EDGE,"E20.15.2"),sQuery(id+"F3.wireOp",EDGE,"E20.15.3"),sQuery(id+"F4.wireOp",EDGE,"E26.15.1"),sQuery(id+"F4.wireOp",EDGE,"E26.15.2"),sQuery(id+"F4.wireOp",EDGE,"E26.15.3")])]}),makeQuery(id+"F40.opExtrude","CAP_FACE",FACE,{"disambiguationData":[OSD([sQuery(id+"F39.wireOp",EDGE,"E29"),sQuery(id+"F39.wireOp",EDGE,"E30")])],"isStart":false})]});
            var Q5;
            Q5=makeQuery(id+"F40.boolean.opBoolean","INTERSECT",EDGE,{"derivedFrom":[makeQuery(id+"F30.opLoft","SWEPT_FACE",FACE,{"disambiguationData":[OSD([sQuery(id+"F3.wireOp",EDGE,"E20.15.1"),sQuery(id+"F3.wireOp",EDGE,"E20.15.2"),sQuery(id+"F3.wireOp",EDGE,"E20.15.3"),sQuery(id+"F22.wireOp",EDGE,"E28.7.0"),sQuery(id+"F22.wireOp",EDGE,"E28.7.2"),sQuery(id+"F22.wireOp",EDGE,"E28.7.3")])]}),makeQuery(id+"F40.opExtrude","CAP_FACE",FACE,{"disambiguationData":[OSD([sQuery(id+"F39.wireOp",EDGE,"E29"),sQuery(id+"F39.wireOp",EDGE,"E30")])],"isStart":true})]});
            var Q6;
            Q6=makeQuery(id+"F40.boolean.opBoolean","INTERSECT",EDGE,{"derivedFrom":[makeQuery(id+"F29.opLoft","SWEPT_FACE",FACE,{"disambiguationData":[OSD([sQuery(id+"F3.wireOp",EDGE,"E20.14.1"),sQuery(id+"F3.wireOp",EDGE,"E20.14.2"),sQuery(id+"F3.wireOp",EDGE,"E20.14.3"),sQuery(id+"F22.wireOp",EDGE,"E28.6.0"),sQuery(id+"F22.wireOp",EDGE,"E28.6.2"),sQuery(id+"F22.wireOp",EDGE,"E28.6.3")])]}),makeQuery(id+"F40.opExtrude","CAP_FACE",FACE,{"disambiguationData":[OSD([sQuery(id+"F39.wireOp",EDGE,"E29"),sQuery(id+"F39.wireOp",EDGE,"E30")])],"isStart":true})]});
            var Q7;
            Q7=makeQuery(id+"F40.boolean.opBoolean","INTERSECT",EDGE,{"derivedFrom":[makeQuery(id+"F28.opLoft","SWEPT_FACE",FACE,{"disambiguationData":[OSD([sQuery(id+"F3.wireOp",EDGE,"E20.13.1"),sQuery(id+"F3.wireOp",EDGE,"E20.13.2"),sQuery(id+"F3.wireOp",EDGE,"E20.13.3"),sQuery(id+"F22.wireOp",EDGE,"E28.5.0"),sQuery(id+"F22.wireOp",EDGE,"E28.5.2"),sQuery(id+"F22.wireOp",EDGE,"E28.5.3")])]}),makeQuery(id+"F40.opExtrude","CAP_FACE",FACE,{"disambiguationData":[OSD([sQuery(id+"F39.wireOp",EDGE,"E29"),sQuery(id+"F39.wireOp",EDGE,"E30")])],"isStart":true})]});
            var Q8;
            Q8=makeQuery(id+"F40.boolean.opBoolean","INTERSECT",EDGE,{"derivedFrom":[makeQuery(id+"F27.opLoft","SWEPT_FACE",FACE,{"disambiguationData":[OSD([sQuery(id+"F3.wireOp",EDGE,"E20.12.1"),sQuery(id+"F3.wireOp",EDGE,"E20.12.2"),sQuery(id+"F3.wireOp",EDGE,"E20.12.3"),sQuery(id+"F22.wireOp",EDGE,"E28.4.0"),sQuery(id+"F22.wireOp",EDGE,"E28.4.2"),sQuery(id+"F22.wireOp",EDGE,"E28.4.3")])]}),makeQuery(id+"F40.opExtrude","CAP_FACE",FACE,{"disambiguationData":[OSD([sQuery(id+"F39.wireOp",EDGE,"E29"),sQuery(id+"F39.wireOp",EDGE,"E30")])],"isStart":true})]});
            var Q9;
            Q9=makeQuery(id+"F40.boolean.opBoolean","INTERSECT",EDGE,{"derivedFrom":[makeQuery(id+"F26.opLoft","SWEPT_FACE",FACE,{"disambiguationData":[OSD([sQuery(id+"F3.wireOp",EDGE,"E20.11.1"),sQuery(id+"F3.wireOp",EDGE,"E20.11.2"),sQuery(id+"F3.wireOp",EDGE,"E20.11.3"),sQuery(id+"F22.wireOp",EDGE,"E28.3.0"),sQuery(id+"F22.wireOp",EDGE,"E28.3.2"),sQuery(id+"F22.wireOp",EDGE,"E28.3.3")])]}),makeQuery(id+"F40.opExtrude","CAP_FACE",FACE,{"disambiguationData":[OSD([sQuery(id+"F39.wireOp",EDGE,"E29"),sQuery(id+"F39.wireOp",EDGE,"E30")])],"isStart":true})]});
            var Q10;
            Q10=makeQuery(id+"F40.boolean.opBoolean","INTERSECT",EDGE,{"derivedFrom":[makeQuery(id+"F25.opLoft","SWEPT_FACE",FACE,{"disambiguationData":[OSD([sQuery(id+"F3.wireOp",EDGE,"E20.10.1"),sQuery(id+"F3.wireOp",EDGE,"E20.10.2"),sQuery(id+"F3.wireOp",EDGE,"E20.10.3"),sQuery(id+"F22.wireOp",EDGE,"E28.2.0"),sQuery(id+"F22.wireOp",EDGE,"E28.2.2"),sQuery(id+"F22.wireOp",EDGE,"E28.2.3")])]}),makeQuery(id+"F40.opExtrude","CAP_FACE",FACE,{"disambiguationData":[OSD([sQuery(id+"F39.wireOp",EDGE,"E29"),sQuery(id+"F39.wireOp",EDGE,"E30")])],"isStart":true})]});
            var Q11;
            Q11=makeQuery(id+"F40.boolean.opBoolean","INTERSECT",EDGE,{"derivedFrom":[makeQuery(id+"F24.opLoft","SWEPT_FACE",FACE,{"disambiguationData":[OSD([sQuery(id+"F3.wireOp",EDGE,"E20.9.1"),sQuery(id+"F3.wireOp",EDGE,"E20.9.2"),sQuery(id+"F3.wireOp",EDGE,"E20.9.3"),sQuery(id+"F22.wireOp",EDGE,"E28.1.0"),sQuery(id+"F22.wireOp",EDGE,"E28.1.2"),sQuery(id+"F22.wireOp",EDGE,"E28.1.3")])]}),makeQuery(id+"F40.opExtrude","CAP_FACE",FACE,{"disambiguationData":[OSD([sQuery(id+"F39.wireOp",EDGE,"E29"),sQuery(id+"F39.wireOp",EDGE,"E30")])],"isStart":true})]});
            var Q12;
            Q12=makeQuery(id+"F40.boolean.opBoolean","INTERSECT",EDGE,{"derivedFrom":[makeQuery(id+"F23.opLoft","SWEPT_FACE",FACE,{"disambiguationData":[OSD([sQuery(id+"F3.wireOp",EDGE,"E20.8.1"),sQuery(id+"F3.wireOp",EDGE,"E20.8.2"),sQuery(id+"F3.wireOp",EDGE,"E20.8.3"),sQuery(id+"F22.wireOp",EDGE,"E27.bottom"),sQuery(id+"F22.wireOp",EDGE,"E27.top"),sQuery(id+"F22.wireOp",EDGE,"E27.left")])]}),makeQuery(id+"F40.opExtrude","CAP_FACE",FACE,{"disambiguationData":[OSD([sQuery(id+"F39.wireOp",EDGE,"E29"),sQuery(id+"F39.wireOp",EDGE,"E30")])],"isStart":true})]});
            var Q13;
            Q13=makeQuery(id+"F40.boolean.opBoolean","INTERSECT",EDGE,{"derivedFrom":[makeQuery(id+"F38.opLoft","SWEPT_FACE",FACE,{"disambiguationData":[OSD([sQuery(id+"F3.wireOp",EDGE,"E20.7.1"),sQuery(id+"F3.wireOp",EDGE,"E20.7.2"),sQuery(id+"F3.wireOp",EDGE,"E20.7.3"),sQuery(id+"F22.wireOp",EDGE,"E28.15.0"),sQuery(id+"F22.wireOp",EDGE,"E28.15.2"),sQuery(id+"F22.wireOp",EDGE,"E28.15.3")])]}),makeQuery(id+"F40.opExtrude","CAP_FACE",FACE,{"disambiguationData":[OSD([sQuery(id+"F39.wireOp",EDGE,"E29"),sQuery(id+"F39.wireOp",EDGE,"E30")])],"isStart":true})]});
            var Q14;
            Q14=makeQuery(id+"F40.boolean.opBoolean","INTERSECT",EDGE,{"derivedFrom":[makeQuery(id+"F37.opLoft","SWEPT_FACE",FACE,{"disambiguationData":[OSD([sQuery(id+"F3.wireOp",EDGE,"E20.6.1"),sQuery(id+"F3.wireOp",EDGE,"E20.6.2"),sQuery(id+"F3.wireOp",EDGE,"E20.6.3"),sQuery(id+"F22.wireOp",EDGE,"E28.14.0"),sQuery(id+"F22.wireOp",EDGE,"E28.14.2"),sQuery(id+"F22.wireOp",EDGE,"E28.14.3")])]}),makeQuery(id+"F40.opExtrude","CAP_FACE",FACE,{"disambiguationData":[OSD([sQuery(id+"F39.wireOp",EDGE,"E29"),sQuery(id+"F39.wireOp",EDGE,"E30")])],"isStart":true})]});
            var Q15;
            Q15=makeQuery(id+"F40.boolean.opBoolean","INTERSECT",EDGE,{"derivedFrom":[makeQuery(id+"F36.opLoft","SWEPT_FACE",FACE,{"disambiguationData":[OSD([sQuery(id+"F3.wireOp",EDGE,"E20.5.1"),sQuery(id+"F3.wireOp",EDGE,"E20.5.2"),sQuery(id+"F3.wireOp",EDGE,"E20.5.3"),sQuery(id+"F22.wireOp",EDGE,"E28.13.0"),sQuery(id+"F22.wireOp",EDGE,"E28.13.2"),sQuery(id+"F22.wireOp",EDGE,"E28.13.3")])]}),makeQuery(id+"F40.opExtrude","CAP_FACE",FACE,{"disambiguationData":[OSD([sQuery(id+"F39.wireOp",EDGE,"E29"),sQuery(id+"F39.wireOp",EDGE,"E30")])],"isStart":true})]});
            var Q16;
            Q16=makeQuery(id+"F40.boolean.opBoolean","INTERSECT",EDGE,{"derivedFrom":[makeQuery(id+"F35.opLoft","SWEPT_FACE",FACE,{"disambiguationData":[OSD([sQuery(id+"F3.wireOp",EDGE,"E20.4.1"),sQuery(id+"F3.wireOp",EDGE,"E20.4.2"),sQuery(id+"F3.wireOp",EDGE,"E20.4.3"),sQuery(id+"F22.wireOp",EDGE,"E28.12.0"),sQuery(id+"F22.wireOp",EDGE,"E28.12.2"),sQuery(id+"F22.wireOp",EDGE,"E28.12.3")])]}),makeQuery(id+"F40.opExtrude","CAP_FACE",FACE,{"disambiguationData":[OSD([sQuery(id+"F39.wireOp",EDGE,"E29"),sQuery(id+"F39.wireOp",EDGE,"E30")])],"isStart":true})]});
            var Q17;
            Q17=makeQuery(id+"F40.boolean.opBoolean","INTERSECT",EDGE,{"derivedFrom":[makeQuery(id+"F34.opLoft","SWEPT_FACE",FACE,{"disambiguationData":[OSD([sQuery(id+"F3.wireOp",EDGE,"E20.3.1"),sQuery(id+"F3.wireOp",EDGE,"E20.3.2"),sQuery(id+"F3.wireOp",EDGE,"E20.3.3"),sQuery(id+"F22.wireOp",EDGE,"E28.11.0"),sQuery(id+"F22.wireOp",EDGE,"E28.11.2"),sQuery(id+"F22.wireOp",EDGE,"E28.11.3")])]}),makeQuery(id+"F40.opExtrude","CAP_FACE",FACE,{"disambiguationData":[OSD([sQuery(id+"F39.wireOp",EDGE,"E29"),sQuery(id+"F39.wireOp",EDGE,"E30")])],"isStart":true})]});
            var Q18;
            Q18=makeQuery(id+"F40.boolean.opBoolean","INTERSECT",EDGE,{"derivedFrom":[makeQuery(id+"F33.opLoft","SWEPT_FACE",FACE,{"disambiguationData":[OSD([sQuery(id+"F3.wireOp",EDGE,"E20.2.1"),sQuery(id+"F3.wireOp",EDGE,"E20.2.2"),sQuery(id+"F3.wireOp",EDGE,"E20.2.3"),sQuery(id+"F22.wireOp",EDGE,"E28.10.0"),sQuery(id+"F22.wireOp",EDGE,"E28.10.2"),sQuery(id+"F22.wireOp",EDGE,"E28.10.3")])]}),makeQuery(id+"F40.opExtrude","CAP_FACE",FACE,{"disambiguationData":[OSD([sQuery(id+"F39.wireOp",EDGE,"E29"),sQuery(id+"F39.wireOp",EDGE,"E30")])],"isStart":true})]});
            var Q19;
            Q19=makeQuery(id+"F40.boolean.opBoolean","INTERSECT",EDGE,{"derivedFrom":[makeQuery(id+"F19.opLoft","SWEPT_FACE",FACE,{"disambiguationData":[OSD([sQuery(id+"F3.wireOp",EDGE,"E20.2.1"),sQuery(id+"F3.wireOp",EDGE,"E20.2.2"),sQuery(id+"F3.wireOp",EDGE,"E20.2.3"),sQuery(id+"F4.wireOp",EDGE,"E26.2.1"),sQuery(id+"F4.wireOp",EDGE,"E26.2.2"),sQuery(id+"F4.wireOp",EDGE,"E26.2.3")])]}),makeQuery(id+"F40.opExtrude","CAP_FACE",FACE,{"disambiguationData":[OSD([sQuery(id+"F39.wireOp",EDGE,"E29"),sQuery(id+"F39.wireOp",EDGE,"E30")])],"isStart":false})]});
            var Q20;
            Q20=makeQuery(id+"F40.boolean.opBoolean","INTERSECT",EDGE,{"derivedFrom":[makeQuery(id+"F18.opLoft","SWEPT_FACE",FACE,{"disambiguationData":[OSD([sQuery(id+"F3.wireOp",EDGE,"E20.3.1"),sQuery(id+"F3.wireOp",EDGE,"E20.3.2"),sQuery(id+"F3.wireOp",EDGE,"E20.3.3"),sQuery(id+"F4.wireOp",EDGE,"E26.3.1"),sQuery(id+"F4.wireOp",EDGE,"E26.3.2"),sQuery(id+"F4.wireOp",EDGE,"E26.3.3")])]}),makeQuery(id+"F40.opExtrude","CAP_FACE",FACE,{"disambiguationData":[OSD([sQuery(id+"F39.wireOp",EDGE,"E29"),sQuery(id+"F39.wireOp",EDGE,"E30")])],"isStart":false})]});
            var Q21;
            Q21=makeQuery(id+"F40.boolean.opBoolean","INTERSECT",EDGE,{"derivedFrom":[makeQuery(id+"F17.opLoft","SWEPT_FACE",FACE,{"disambiguationData":[OSD([sQuery(id+"F3.wireOp",EDGE,"E20.4.1"),sQuery(id+"F3.wireOp",EDGE,"E20.4.2"),sQuery(id+"F3.wireOp",EDGE,"E20.4.3"),sQuery(id+"F4.wireOp",EDGE,"E26.4.1"),sQuery(id+"F4.wireOp",EDGE,"E26.4.2"),sQuery(id+"F4.wireOp",EDGE,"E26.4.3")])]}),makeQuery(id+"F40.opExtrude","CAP_FACE",FACE,{"disambiguationData":[OSD([sQuery(id+"F39.wireOp",EDGE,"E29"),sQuery(id+"F39.wireOp",EDGE,"E30")])],"isStart":false})]});
            var Q22;
            Q22=makeQuery(id+"F40.boolean.opBoolean","INTERSECT",EDGE,{"derivedFrom":[makeQuery(id+"F16.opLoft","SWEPT_FACE",FACE,{"disambiguationData":[OSD([sQuery(id+"F3.wireOp",EDGE,"E20.5.1"),sQuery(id+"F3.wireOp",EDGE,"E20.5.2"),sQuery(id+"F3.wireOp",EDGE,"E20.5.3"),sQuery(id+"F4.wireOp",EDGE,"E26.5.1"),sQuery(id+"F4.wireOp",EDGE,"E26.5.2"),sQuery(id+"F4.wireOp",EDGE,"E26.5.3")])]}),makeQuery(id+"F40.opExtrude","CAP_FACE",FACE,{"disambiguationData":[OSD([sQuery(id+"F39.wireOp",EDGE,"E29"),sQuery(id+"F39.wireOp",EDGE,"E30")])],"isStart":false})]});
            var Q23;
            Q23=makeQuery(id+"F40.boolean.opBoolean","INTERSECT",EDGE,{"derivedFrom":[makeQuery(id+"F15.opLoft","SWEPT_FACE",FACE,{"disambiguationData":[OSD([sQuery(id+"F3.wireOp",EDGE,"E20.6.1"),sQuery(id+"F3.wireOp",EDGE,"E20.6.2"),sQuery(id+"F3.wireOp",EDGE,"E20.6.3"),sQuery(id+"F4.wireOp",EDGE,"E26.6.1"),sQuery(id+"F4.wireOp",EDGE,"E26.6.2"),sQuery(id+"F4.wireOp",EDGE,"E26.6.3")])]}),makeQuery(id+"F40.opExtrude","CAP_FACE",FACE,{"disambiguationData":[OSD([sQuery(id+"F39.wireOp",EDGE,"E29"),sQuery(id+"F39.wireOp",EDGE,"E30")])],"isStart":false})]});
            var Q24;
            Q24=makeQuery(id+"F40.boolean.opBoolean","INTERSECT",EDGE,{"derivedFrom":[makeQuery(id+"F14.opLoft","SWEPT_FACE",FACE,{"disambiguationData":[OSD([sQuery(id+"F3.wireOp",EDGE,"E20.7.1"),sQuery(id+"F3.wireOp",EDGE,"E20.7.2"),sQuery(id+"F3.wireOp",EDGE,"E20.7.3"),sQuery(id+"F4.wireOp",EDGE,"E26.7.1"),sQuery(id+"F4.wireOp",EDGE,"E26.7.2"),sQuery(id+"F4.wireOp",EDGE,"E26.7.3")])]}),makeQuery(id+"F40.opExtrude","CAP_FACE",FACE,{"disambiguationData":[OSD([sQuery(id+"F39.wireOp",EDGE,"E29"),sQuery(id+"F39.wireOp",EDGE,"E30")])],"isStart":false})]});
            var Q25;
            Q25=makeQuery(id+"F40.boolean.opBoolean","INTERSECT",EDGE,{"derivedFrom":[makeQuery(id+"F13.opLoft","SWEPT_FACE",FACE,{"disambiguationData":[OSD([sQuery(id+"F3.wireOp",EDGE,"E20.8.1"),sQuery(id+"F3.wireOp",EDGE,"E20.8.2"),sQuery(id+"F3.wireOp",EDGE,"E20.8.3"),sQuery(id+"F4.wireOp",EDGE,"E26.8.1"),sQuery(id+"F4.wireOp",EDGE,"E26.8.2"),sQuery(id+"F4.wireOp",EDGE,"E26.8.3")])]}),makeQuery(id+"F40.opExtrude","CAP_FACE",FACE,{"disambiguationData":[OSD([sQuery(id+"F39.wireOp",EDGE,"E29"),sQuery(id+"F39.wireOp",EDGE,"E30")])],"isStart":false})]});
            var Q26;
            Q26=makeQuery(id+"F40.boolean.opBoolean","INTERSECT",EDGE,{"derivedFrom":[makeQuery(id+"F12.opLoft","SWEPT_FACE",FACE,{"disambiguationData":[OSD([sQuery(id+"F3.wireOp",EDGE,"E20.9.1"),sQuery(id+"F3.wireOp",EDGE,"E20.9.2"),sQuery(id+"F3.wireOp",EDGE,"E20.9.3"),sQuery(id+"F4.wireOp",EDGE,"E26.9.1"),sQuery(id+"F4.wireOp",EDGE,"E26.9.2"),sQuery(id+"F4.wireOp",EDGE,"E26.9.3")])]}),makeQuery(id+"F40.opExtrude","CAP_FACE",FACE,{"disambiguationData":[OSD([sQuery(id+"F39.wireOp",EDGE,"E29"),sQuery(id+"F39.wireOp",EDGE,"E30")])],"isStart":false})]});
            var Q27;
            Q27=makeQuery(id+"F40.boolean.opBoolean","INTERSECT",EDGE,{"derivedFrom":[makeQuery(id+"F11.opLoft","SWEPT_FACE",FACE,{"disambiguationData":[OSD([sQuery(id+"F3.wireOp",EDGE,"E20.10.1"),sQuery(id+"F3.wireOp",EDGE,"E20.10.2"),sQuery(id+"F3.wireOp",EDGE,"E20.10.3"),sQuery(id+"F4.wireOp",EDGE,"E26.10.1"),sQuery(id+"F4.wireOp",EDGE,"E26.10.2"),sQuery(id+"F4.wireOp",EDGE,"E26.10.3")])]}),makeQuery(id+"F40.opExtrude","CAP_FACE",FACE,{"disambiguationData":[OSD([sQuery(id+"F39.wireOp",EDGE,"E29"),sQuery(id+"F39.wireOp",EDGE,"E30")])],"isStart":false})]});
            var Q28;
            Q28=makeQuery(id+"F40.boolean.opBoolean","INTERSECT",EDGE,{"derivedFrom":[makeQuery(id+"F10.opLoft","SWEPT_FACE",FACE,{"disambiguationData":[OSD([sQuery(id+"F3.wireOp",EDGE,"E20.11.1"),sQuery(id+"F3.wireOp",EDGE,"E20.11.2"),sQuery(id+"F3.wireOp",EDGE,"E20.11.3"),sQuery(id+"F4.wireOp",EDGE,"E26.11.1"),sQuery(id+"F4.wireOp",EDGE,"E26.11.2"),sQuery(id+"F4.wireOp",EDGE,"E26.11.3")])]}),makeQuery(id+"F40.opExtrude","CAP_FACE",FACE,{"disambiguationData":[OSD([sQuery(id+"F39.wireOp",EDGE,"E29"),sQuery(id+"F39.wireOp",EDGE,"E30")])],"isStart":false})]});
            var Q29;
            Q29=makeQuery(id+"F40.boolean.opBoolean","INTERSECT",EDGE,{"derivedFrom":[makeQuery(id+"F9.opLoft","SWEPT_FACE",FACE,{"disambiguationData":[OSD([sQuery(id+"F3.wireOp",EDGE,"E20.12.1"),sQuery(id+"F3.wireOp",EDGE,"E20.12.2"),sQuery(id+"F3.wireOp",EDGE,"E20.12.3"),sQuery(id+"F4.wireOp",EDGE,"E26.12.1"),sQuery(id+"F4.wireOp",EDGE,"E26.12.2"),sQuery(id+"F4.wireOp",EDGE,"E26.12.3")])]}),makeQuery(id+"F40.opExtrude","CAP_FACE",FACE,{"disambiguationData":[OSD([sQuery(id+"F39.wireOp",EDGE,"E29"),sQuery(id+"F39.wireOp",EDGE,"E30")])],"isStart":false})]});
            var Q30;
            Q30=makeQuery(id+"F40.boolean.opBoolean","INTERSECT",EDGE,{"derivedFrom":[makeQuery(id+"F8.opLoft","SWEPT_FACE",FACE,{"disambiguationData":[OSD([sQuery(id+"F3.wireOp",EDGE,"E20.13.1"),sQuery(id+"F3.wireOp",EDGE,"E20.13.2"),sQuery(id+"F3.wireOp",EDGE,"E20.13.3"),sQuery(id+"F4.wireOp",EDGE,"E26.13.1"),sQuery(id+"F4.wireOp",EDGE,"E26.13.2"),sQuery(id+"F4.wireOp",EDGE,"E26.13.3")])]}),makeQuery(id+"F40.opExtrude","CAP_FACE",FACE,{"disambiguationData":[OSD([sQuery(id+"F39.wireOp",EDGE,"E29"),sQuery(id+"F39.wireOp",EDGE,"E30")])],"isStart":false})]});
            var Q31;
            Q31=makeQuery(id+"F40.boolean.opBoolean","INTERSECT",EDGE,{"derivedFrom":[makeQuery(id+"F7.opLoft","SWEPT_FACE",FACE,{"disambiguationData":[OSD([sQuery(id+"F3.wireOp",EDGE,"E20.14.1"),sQuery(id+"F3.wireOp",EDGE,"E20.14.2"),sQuery(id+"F3.wireOp",EDGE,"E20.14.3"),sQuery(id+"F4.wireOp",EDGE,"E26.14.1"),sQuery(id+"F4.wireOp",EDGE,"E26.14.2"),sQuery(id+"F4.wireOp",EDGE,"E26.14.3")])]}),makeQuery(id+"F40.opExtrude","CAP_FACE",FACE,{"disambiguationData":[OSD([sQuery(id+"F39.wireOp",EDGE,"E29"),sQuery(id+"F39.wireOp",EDGE,"E30")])],"isStart":false})]});
            fillet(context, id + "F44", {"entities" : qUnion([Q0, Q1, Q2, Q3, Q4, Q5, Q6, Q7, Q8, Q9, Q10, Q11, Q12, Q13, Q14, Q15, Q16, Q17, Q18, Q19, Q20, Q21, Q22, Q23, Q24, Q25, Q26, Q27, Q28, Q29, Q30, Q31]), "radius" : 20 * mm, "tangentPropagation" : true, "allowEdgeOverflow" : false});
        }
        {
            var Q0;
            Q0=makeQuery(id+"F19.boolean.opBoolean","INTERSECT",EDGE,{"derivedFrom":[makeQuery(id+"F1.opRevolve","SWEPT_FACE",FACE,{"disambiguationData":[OSD([sQuery(id+"F0.wireOp",EDGE,"E4")])]}),makeQuery(id+"F19.opLoft","SWEPT_FACE",FACE,{"disambiguationData":[OSD([sQuery(id+"F3.wireOp",EDGE,"E20.2.0"),sQuery(id+"F3.wireOp",EDGE,"E20.2.1"),sQuery(id+"F3.wireOp",EDGE,"E20.2.3"),sQuery(id+"F4.wireOp",EDGE,"E26.2.0"),sQuery(id+"F4.wireOp",EDGE,"E26.2.2"),sQuery(id+"F4.wireOp",EDGE,"E26.2.3")])]})]});
            var Q1;
            Q1=makeQuery(id+"F20.boolean.opBoolean","INTERSECT",EDGE,{"derivedFrom":[makeQuery(id+"F1.opRevolve","SWEPT_FACE",FACE,{"disambiguationData":[OSD([sQuery(id+"F0.wireOp",EDGE,"E4")])]}),makeQuery(id+"F20.opLoft","SWEPT_FACE",FACE,{"disambiguationData":[OSD([sQuery(id+"F3.wireOp",EDGE,"E20.1.0"),sQuery(id+"F3.wireOp",EDGE,"E20.1.1"),sQuery(id+"F3.wireOp",EDGE,"E20.1.3"),sQuery(id+"F4.wireOp",EDGE,"E26.1.0"),sQuery(id+"F4.wireOp",EDGE,"E26.1.2"),sQuery(id+"F4.wireOp",EDGE,"E26.1.3")])]})]});
            var Q2;
            {var subQ0=sQuery(id+"F3.wireOp",EDGE,"E20.1.3");var subQ1=sQuery(id+"F3.wireOp",EDGE,"E20.1.1");var subQ2=sQuery(id+"F3.wireOp",EDGE,"E20.1.0");var subQ51=sQuery(id+"F3.wireOp",EDGE,"E18.bottom");var subQ62=sQuery(id+"F3.wireOp",EDGE,"E20.7.0");var subQ70=makeQuery(id+"F14.opLoft","CAP_FACE",FACE,{"disambiguationData":[OSD([makeQuery(id+"F3.imprint","IMPRINT",FACE,{"disambiguationData":[TD([[makeQuery(id+"F3.imprint","IMPRINT",EDGE,{"derivedFrom":subQ62}),-1.0]])]})])],"isStart":true});var subQ78=makeQuery(id+"F5.opLoft","CAP_FACE",FACE,{"disambiguationData":[OSD([makeQuery(id+"F3.imprint","IMPRINT",FACE,{"disambiguationData":[TD([[makeQuery(id+"F3.imprint","IMPRINT",EDGE,{"derivedFrom":subQ51}),1.0]])]})])],"isStart":true});Q2=makeQuery(id+"F32.boolean.opBoolean","INTERSECT",EDGE,{"derivedFrom":[makeQuery(id+"F31.boolean.opBoolean","SPLIT",FACE,{"disambiguationData":[TD([subQ70])],"derivedFrom":makeQuery(id+"F30.boolean.opBoolean","SPLIT",FACE,{"disambiguationData":[TD([subQ78])],"derivedFrom":makeQuery(id+"F29.boolean.opBoolean","SPLIT",FACE,{"disambiguationData":[TD([subQ78])],"derivedFrom":makeQuery(id+"F28.boolean.opBoolean","SPLIT",FACE,{"disambiguationData":[TD([subQ78])],"derivedFrom":makeQuery(id+"F27.boolean.opBoolean","SPLIT",FACE,{"disambiguationData":[TD([subQ78])],"derivedFrom":makeQuery(id+"F26.boolean.opBoolean","SPLIT",FACE,{"disambiguationData":[TD([subQ78])],"derivedFrom":makeQuery(id+"F25.boolean.opBoolean","SPLIT",FACE,{"disambiguationData":[TD([subQ78])],"derivedFrom":makeQuery(id+"F24.boolean.opBoolean","SPLIT",FACE,{"disambiguationData":[TD([subQ78])],"derivedFrom":makeQuery(id+"F1.opRevolve","SWEPT_FACE",FACE,{"disambiguationData":[OSD([sQuery(id+"F0.wireOp",EDGE,"E4")])]})})})})})})})})}),makeQuery(id+"F32.opLoft","SWEPT_FACE",FACE,{"disambiguationData":[OSD([subQ2,subQ1,subQ0,sQuery(id+"F22.wireOp",EDGE,"E28.9.1"),sQuery(id+"F22.wireOp",EDGE,"E28.9.2"),sQuery(id+"F22.wireOp",EDGE,"E28.9.3")])]})]});}
            var Q3;
            {var subQ0=sQuery(id+"F3.wireOp",EDGE,"E20.2.3");var subQ1=sQuery(id+"F3.wireOp",EDGE,"E20.2.1");var subQ2=sQuery(id+"F3.wireOp",EDGE,"E20.2.0");var subQ51=sQuery(id+"F3.wireOp",EDGE,"E20.7.0");var subQ60=makeQuery(id+"F14.opLoft","CAP_FACE",FACE,{"disambiguationData":[OSD([makeQuery(id+"F3.imprint","IMPRINT",FACE,{"disambiguationData":[TD([[makeQuery(id+"F3.imprint","IMPRINT",EDGE,{"derivedFrom":subQ51}),-1.0]])]})])],"isStart":true});var subQ73=sQuery(id+"F3.wireOp",EDGE,"E18.bottom");var subQ78=makeQuery(id+"F5.opLoft","CAP_FACE",FACE,{"disambiguationData":[OSD([makeQuery(id+"F3.imprint","IMPRINT",FACE,{"disambiguationData":[TD([[makeQuery(id+"F3.imprint","IMPRINT",EDGE,{"derivedFrom":subQ73}),1.0]])]})])],"isStart":true});Q3=makeQuery(id+"F33.boolean.opBoolean","INTERSECT",EDGE,{"derivedFrom":[makeQuery(id+"F32.boolean.opBoolean","SPLIT",FACE,{"disambiguationData":[TD([subQ60])],"derivedFrom":makeQuery(id+"F31.boolean.opBoolean","SPLIT",FACE,{"disambiguationData":[TD([subQ60])],"derivedFrom":makeQuery(id+"F30.boolean.opBoolean","SPLIT",FACE,{"disambiguationData":[TD([subQ78])],"derivedFrom":makeQuery(id+"F29.boolean.opBoolean","SPLIT",FACE,{"disambiguationData":[TD([subQ78])],"derivedFrom":makeQuery(id+"F28.boolean.opBoolean","SPLIT",FACE,{"disambiguationData":[TD([subQ78])],"derivedFrom":makeQuery(id+"F27.boolean.opBoolean","SPLIT",FACE,{"disambiguationData":[TD([subQ78])],"derivedFrom":makeQuery(id+"F26.boolean.opBoolean","SPLIT",FACE,{"disambiguationData":[TD([subQ78])],"derivedFrom":makeQuery(id+"F25.boolean.opBoolean","SPLIT",FACE,{"disambiguationData":[TD([subQ78])],"derivedFrom":makeQuery(id+"F24.boolean.opBoolean","SPLIT",FACE,{"disambiguationData":[TD([subQ78])],"derivedFrom":makeQuery(id+"F1.opRevolve","SWEPT_FACE",FACE,{"disambiguationData":[OSD([sQuery(id+"F0.wireOp",EDGE,"E4")])]})})})})})})})})})}),makeQuery(id+"F33.opLoft","SWEPT_FACE",FACE,{"disambiguationData":[OSD([subQ2,subQ1,subQ0,sQuery(id+"F22.wireOp",EDGE,"E28.10.1"),sQuery(id+"F22.wireOp",EDGE,"E28.10.2"),sQuery(id+"F22.wireOp",EDGE,"E28.10.3")])]})]});}
            var Q4;
            {var subQ0=sQuery(id+"F3.wireOp",EDGE,"E20.3.3");var subQ1=sQuery(id+"F3.wireOp",EDGE,"E20.3.1");var subQ2=sQuery(id+"F3.wireOp",EDGE,"E20.3.0");var subQ22=sQuery(id+"F3.wireOp",EDGE,"E20.7.0");var subQ26=makeQuery(id+"F14.opLoft","CAP_FACE",FACE,{"disambiguationData":[OSD([makeQuery(id+"F3.imprint","IMPRINT",FACE,{"disambiguationData":[TD([[makeQuery(id+"F3.imprint","IMPRINT",EDGE,{"derivedFrom":subQ22}),-1.0]])]})])],"isStart":true});var subQ73=sQuery(id+"F3.wireOp",EDGE,"E18.bottom");var subQ78=makeQuery(id+"F5.opLoft","CAP_FACE",FACE,{"disambiguationData":[OSD([makeQuery(id+"F3.imprint","IMPRINT",FACE,{"disambiguationData":[TD([[makeQuery(id+"F3.imprint","IMPRINT",EDGE,{"derivedFrom":subQ73}),1.0]])]})])],"isStart":true});Q4=makeQuery(id+"F34.boolean.opBoolean","INTERSECT",EDGE,{"derivedFrom":[makeQuery(id+"F33.boolean.opBoolean","SPLIT",FACE,{"disambiguationData":[TD([subQ26])],"derivedFrom":makeQuery(id+"F32.boolean.opBoolean","SPLIT",FACE,{"disambiguationData":[TD([subQ26])],"derivedFrom":makeQuery(id+"F31.boolean.opBoolean","SPLIT",FACE,{"disambiguationData":[TD([subQ26])],"derivedFrom":makeQuery(id+"F30.boolean.opBoolean","SPLIT",FACE,{"disambiguationData":[TD([subQ78])],"derivedFrom":makeQuery(id+"F29.boolean.opBoolean","SPLIT",FACE,{"disambiguationData":[TD([subQ78])],"derivedFrom":makeQuery(id+"F28.boolean.opBoolean","SPLIT",FACE,{"disambiguationData":[TD([subQ78])],"derivedFrom":makeQuery(id+"F27.boolean.opBoolean","SPLIT",FACE,{"disambiguationData":[TD([subQ78])],"derivedFrom":makeQuery(id+"F26.boolean.opBoolean","SPLIT",FACE,{"disambiguationData":[TD([subQ78])],"derivedFrom":makeQuery(id+"F25.boolean.opBoolean","SPLIT",FACE,{"disambiguationData":[TD([subQ78])],"derivedFrom":makeQuery(id+"F24.boolean.opBoolean","SPLIT",FACE,{"disambiguationData":[TD([subQ78])],"derivedFrom":makeQuery(id+"F1.opRevolve","SWEPT_FACE",FACE,{"disambiguationData":[OSD([sQuery(id+"F0.wireOp",EDGE,"E4")])]})})})})})})})})})})}),makeQuery(id+"F34.opLoft","SWEPT_FACE",FACE,{"disambiguationData":[OSD([subQ2,subQ1,subQ0,sQuery(id+"F22.wireOp",EDGE,"E28.11.1"),sQuery(id+"F22.wireOp",EDGE,"E28.11.2"),sQuery(id+"F22.wireOp",EDGE,"E28.11.3")])]})]});}
            var Q5;
            {var subQ0=sQuery(id+"F3.wireOp",EDGE,"E20.4.3");var subQ1=sQuery(id+"F3.wireOp",EDGE,"E20.4.1");var subQ2=sQuery(id+"F3.wireOp",EDGE,"E20.4.0");var subQ19=sQuery(id+"F3.wireOp",EDGE,"E20.7.0");var subQ23=makeQuery(id+"F14.opLoft","CAP_FACE",FACE,{"disambiguationData":[OSD([makeQuery(id+"F3.imprint","IMPRINT",FACE,{"disambiguationData":[TD([[makeQuery(id+"F3.imprint","IMPRINT",EDGE,{"derivedFrom":subQ19}),-1.0]])]})])],"isStart":true});var subQ73=sQuery(id+"F3.wireOp",EDGE,"E18.bottom");var subQ78=makeQuery(id+"F5.opLoft","CAP_FACE",FACE,{"disambiguationData":[OSD([makeQuery(id+"F3.imprint","IMPRINT",FACE,{"disambiguationData":[TD([[makeQuery(id+"F3.imprint","IMPRINT",EDGE,{"derivedFrom":subQ73}),1.0]])]})])],"isStart":true});Q5=makeQuery(id+"F35.boolean.opBoolean","INTERSECT",EDGE,{"derivedFrom":[makeQuery(id+"F34.boolean.opBoolean","SPLIT",FACE,{"disambiguationData":[TD([subQ23])],"derivedFrom":makeQuery(id+"F33.boolean.opBoolean","SPLIT",FACE,{"disambiguationData":[TD([subQ23])],"derivedFrom":makeQuery(id+"F32.boolean.opBoolean","SPLIT",FACE,{"disambiguationData":[TD([subQ23])],"derivedFrom":makeQuery(id+"F31.boolean.opBoolean","SPLIT",FACE,{"disambiguationData":[TD([subQ23])],"derivedFrom":makeQuery(id+"F30.boolean.opBoolean","SPLIT",FACE,{"disambiguationData":[TD([subQ78])],"derivedFrom":makeQuery(id+"F29.boolean.opBoolean","SPLIT",FACE,{"disambiguationData":[TD([subQ78])],"derivedFrom":makeQuery(id+"F28.boolean.opBoolean","SPLIT",FACE,{"disambiguationData":[TD([subQ78])],"derivedFrom":makeQuery(id+"F27.boolean.opBoolean","SPLIT",FACE,{"disambiguationData":[TD([subQ78])],"derivedFrom":makeQuery(id+"F26.boolean.opBoolean","SPLIT",FACE,{"disambiguationData":[TD([subQ78])],"derivedFrom":makeQuery(id+"F25.boolean.opBoolean","SPLIT",FACE,{"disambiguationData":[TD([subQ78])],"derivedFrom":makeQuery(id+"F24.boolean.opBoolean","SPLIT",FACE,{"disambiguationData":[TD([subQ78])],"derivedFrom":makeQuery(id+"F1.opRevolve","SWEPT_FACE",FACE,{"disambiguationData":[OSD([sQuery(id+"F0.wireOp",EDGE,"E4")])]})})})})})})})})})})})}),makeQuery(id+"F35.opLoft","SWEPT_FACE",FACE,{"disambiguationData":[OSD([subQ2,subQ1,subQ0,sQuery(id+"F22.wireOp",EDGE,"E28.12.1"),sQuery(id+"F22.wireOp",EDGE,"E28.12.2"),sQuery(id+"F22.wireOp",EDGE,"E28.12.3")])]})]});}
            var Q6;
            {var subQ0=sQuery(id+"F3.wireOp",EDGE,"E20.5.3");var subQ1=sQuery(id+"F3.wireOp",EDGE,"E20.5.1");var subQ2=sQuery(id+"F3.wireOp",EDGE,"E20.5.0");var subQ14=sQuery(id+"F3.wireOp",EDGE,"E20.7.0");var subQ18=makeQuery(id+"F14.opLoft","CAP_FACE",FACE,{"disambiguationData":[OSD([makeQuery(id+"F3.imprint","IMPRINT",FACE,{"disambiguationData":[TD([[makeQuery(id+"F3.imprint","IMPRINT",EDGE,{"derivedFrom":subQ14}),-1.0]])]})])],"isStart":true});var subQ73=sQuery(id+"F3.wireOp",EDGE,"E18.bottom");var subQ78=makeQuery(id+"F5.opLoft","CAP_FACE",FACE,{"disambiguationData":[OSD([makeQuery(id+"F3.imprint","IMPRINT",FACE,{"disambiguationData":[TD([[makeQuery(id+"F3.imprint","IMPRINT",EDGE,{"derivedFrom":subQ73}),1.0]])]})])],"isStart":true});Q6=makeQuery(id+"F36.boolean.opBoolean","INTERSECT",EDGE,{"derivedFrom":[makeQuery(id+"F35.boolean.opBoolean","SPLIT",FACE,{"disambiguationData":[TD([subQ18])],"derivedFrom":makeQuery(id+"F34.boolean.opBoolean","SPLIT",FACE,{"disambiguationData":[TD([subQ18])],"derivedFrom":makeQuery(id+"F33.boolean.opBoolean","SPLIT",FACE,{"disambiguationData":[TD([subQ18])],"derivedFrom":makeQuery(id+"F32.boolean.opBoolean","SPLIT",FACE,{"disambiguationData":[TD([subQ18])],"derivedFrom":makeQuery(id+"F31.boolean.opBoolean","SPLIT",FACE,{"disambiguationData":[TD([subQ18])],"derivedFrom":makeQuery(id+"F30.boolean.opBoolean","SPLIT",FACE,{"disambiguationData":[TD([subQ78])],"derivedFrom":makeQuery(id+"F29.boolean.opBoolean","SPLIT",FACE,{"disambiguationData":[TD([subQ78])],"derivedFrom":makeQuery(id+"F28.boolean.opBoolean","SPLIT",FACE,{"disambiguationData":[TD([subQ78])],"derivedFrom":makeQuery(id+"F27.boolean.opBoolean","SPLIT",FACE,{"disambiguationData":[TD([subQ78])],"derivedFrom":makeQuery(id+"F26.boolean.opBoolean","SPLIT",FACE,{"disambiguationData":[TD([subQ78])],"derivedFrom":makeQuery(id+"F25.boolean.opBoolean","SPLIT",FACE,{"disambiguationData":[TD([subQ78])],"derivedFrom":makeQuery(id+"F24.boolean.opBoolean","SPLIT",FACE,{"disambiguationData":[TD([subQ78])],"derivedFrom":makeQuery(id+"F1.opRevolve","SWEPT_FACE",FACE,{"disambiguationData":[OSD([sQuery(id+"F0.wireOp",EDGE,"E4")])]})})})})})})})})})})})})}),makeQuery(id+"F36.opLoft","SWEPT_FACE",FACE,{"disambiguationData":[OSD([subQ2,subQ1,subQ0,sQuery(id+"F22.wireOp",EDGE,"E28.13.1"),sQuery(id+"F22.wireOp",EDGE,"E28.13.2"),sQuery(id+"F22.wireOp",EDGE,"E28.13.3")])]})]});}
            var Q7;
            {var subQ0=sQuery(id+"F3.wireOp",EDGE,"E20.6.3");var subQ1=sQuery(id+"F3.wireOp",EDGE,"E20.6.1");var subQ2=sQuery(id+"F3.wireOp",EDGE,"E20.6.0");var subQ14=sQuery(id+"F3.wireOp",EDGE,"E20.7.0");var subQ18=makeQuery(id+"F14.opLoft","CAP_FACE",FACE,{"disambiguationData":[OSD([makeQuery(id+"F3.imprint","IMPRINT",FACE,{"disambiguationData":[TD([[makeQuery(id+"F3.imprint","IMPRINT",EDGE,{"derivedFrom":subQ14}),-1.0]])]})])],"isStart":true});var subQ73=sQuery(id+"F3.wireOp",EDGE,"E18.bottom");var subQ78=makeQuery(id+"F5.opLoft","CAP_FACE",FACE,{"disambiguationData":[OSD([makeQuery(id+"F3.imprint","IMPRINT",FACE,{"disambiguationData":[TD([[makeQuery(id+"F3.imprint","IMPRINT",EDGE,{"derivedFrom":subQ73}),1.0]])]})])],"isStart":true});Q7=makeQuery(id+"F37.boolean.opBoolean","INTERSECT",EDGE,{"derivedFrom":[makeQuery(id+"F36.boolean.opBoolean","SPLIT",FACE,{"disambiguationData":[TD([subQ18])],"derivedFrom":makeQuery(id+"F35.boolean.opBoolean","SPLIT",FACE,{"disambiguationData":[TD([subQ18])],"derivedFrom":makeQuery(id+"F34.boolean.opBoolean","SPLIT",FACE,{"disambiguationData":[TD([subQ18])],"derivedFrom":makeQuery(id+"F33.boolean.opBoolean","SPLIT",FACE,{"disambiguationData":[TD([subQ18])],"derivedFrom":makeQuery(id+"F32.boolean.opBoolean","SPLIT",FACE,{"disambiguationData":[TD([subQ18])],"derivedFrom":makeQuery(id+"F31.boolean.opBoolean","SPLIT",FACE,{"disambiguationData":[TD([subQ18])],"derivedFrom":makeQuery(id+"F30.boolean.opBoolean","SPLIT",FACE,{"disambiguationData":[TD([subQ78])],"derivedFrom":makeQuery(id+"F29.boolean.opBoolean","SPLIT",FACE,{"disambiguationData":[TD([subQ78])],"derivedFrom":makeQuery(id+"F28.boolean.opBoolean","SPLIT",FACE,{"disambiguationData":[TD([subQ78])],"derivedFrom":makeQuery(id+"F27.boolean.opBoolean","SPLIT",FACE,{"disambiguationData":[TD([subQ78])],"derivedFrom":makeQuery(id+"F26.boolean.opBoolean","SPLIT",FACE,{"disambiguationData":[TD([subQ78])],"derivedFrom":makeQuery(id+"F25.boolean.opBoolean","SPLIT",FACE,{"disambiguationData":[TD([subQ78])],"derivedFrom":makeQuery(id+"F24.boolean.opBoolean","SPLIT",FACE,{"disambiguationData":[TD([subQ78])],"derivedFrom":makeQuery(id+"F1.opRevolve","SWEPT_FACE",FACE,{"disambiguationData":[OSD([sQuery(id+"F0.wireOp",EDGE,"E4")])]})})})})})})})})})})})})})}),makeQuery(id+"F37.opLoft","SWEPT_FACE",FACE,{"disambiguationData":[OSD([subQ2,subQ1,subQ0,sQuery(id+"F22.wireOp",EDGE,"E28.14.1"),sQuery(id+"F22.wireOp",EDGE,"E28.14.2"),sQuery(id+"F22.wireOp",EDGE,"E28.14.3")])]})]});}
            var Q8;
            {var subQ0=sQuery(id+"F3.wireOp",EDGE,"E20.7.3");var subQ1=sQuery(id+"F3.wireOp",EDGE,"E20.7.1");var subQ2=sQuery(id+"F3.wireOp",EDGE,"E20.7.0");var subQ14=makeQuery(id+"F14.opLoft","CAP_FACE",FACE,{"disambiguationData":[OSD([makeQuery(id+"F3.imprint","IMPRINT",FACE,{"disambiguationData":[TD([[makeQuery(id+"F3.imprint","IMPRINT",EDGE,{"derivedFrom":subQ2}),-1.0]])]})])],"isStart":true});var subQ73=sQuery(id+"F3.wireOp",EDGE,"E18.bottom");var subQ78=makeQuery(id+"F5.opLoft","CAP_FACE",FACE,{"disambiguationData":[OSD([makeQuery(id+"F3.imprint","IMPRINT",FACE,{"disambiguationData":[TD([[makeQuery(id+"F3.imprint","IMPRINT",EDGE,{"derivedFrom":subQ73}),1.0]])]})])],"isStart":true});Q8=makeQuery(id+"F38.boolean.opBoolean","INTERSECT",EDGE,{"derivedFrom":[makeQuery(id+"F37.boolean.opBoolean","SPLIT",FACE,{"disambiguationData":[TD([subQ14])],"derivedFrom":makeQuery(id+"F36.boolean.opBoolean","SPLIT",FACE,{"disambiguationData":[TD([subQ14])],"derivedFrom":makeQuery(id+"F35.boolean.opBoolean","SPLIT",FACE,{"disambiguationData":[TD([subQ14])],"derivedFrom":makeQuery(id+"F34.boolean.opBoolean","SPLIT",FACE,{"disambiguationData":[TD([subQ14])],"derivedFrom":makeQuery(id+"F33.boolean.opBoolean","SPLIT",FACE,{"disambiguationData":[TD([subQ14])],"derivedFrom":makeQuery(id+"F32.boolean.opBoolean","SPLIT",FACE,{"disambiguationData":[TD([subQ14])],"derivedFrom":makeQuery(id+"F31.boolean.opBoolean","SPLIT",FACE,{"disambiguationData":[TD([subQ14])],"derivedFrom":makeQuery(id+"F30.boolean.opBoolean","SPLIT",FACE,{"disambiguationData":[TD([subQ78])],"derivedFrom":makeQuery(id+"F29.boolean.opBoolean","SPLIT",FACE,{"disambiguationData":[TD([subQ78])],"derivedFrom":makeQuery(id+"F28.boolean.opBoolean","SPLIT",FACE,{"disambiguationData":[TD([subQ78])],"derivedFrom":makeQuery(id+"F27.boolean.opBoolean","SPLIT",FACE,{"disambiguationData":[TD([subQ78])],"derivedFrom":makeQuery(id+"F26.boolean.opBoolean","SPLIT",FACE,{"disambiguationData":[TD([subQ78])],"derivedFrom":makeQuery(id+"F25.boolean.opBoolean","SPLIT",FACE,{"disambiguationData":[TD([subQ78])],"derivedFrom":makeQuery(id+"F24.boolean.opBoolean","SPLIT",FACE,{"disambiguationData":[TD([subQ78])],"derivedFrom":makeQuery(id+"F1.opRevolve","SWEPT_FACE",FACE,{"disambiguationData":[OSD([sQuery(id+"F0.wireOp",EDGE,"E4")])]})})})})})})})})})})})})})})}),makeQuery(id+"F38.opLoft","SWEPT_FACE",FACE,{"disambiguationData":[OSD([subQ2,subQ1,subQ0,sQuery(id+"F22.wireOp",EDGE,"E28.15.1"),sQuery(id+"F22.wireOp",EDGE,"E28.15.2"),sQuery(id+"F22.wireOp",EDGE,"E28.15.3")])]})]});}
            var Q9;
            Q9=makeQuery(id+"F23.boolean.opBoolean","INTERSECT",EDGE,{"derivedFrom":[makeQuery(id+"F1.opRevolve","SWEPT_FACE",FACE,{"disambiguationData":[OSD([sQuery(id+"F0.wireOp",EDGE,"E4")])]}),makeQuery(id+"F23.opLoft","SWEPT_FACE",FACE,{"disambiguationData":[OSD([sQuery(id+"F3.wireOp",EDGE,"E20.8.0"),sQuery(id+"F3.wireOp",EDGE,"E20.8.1"),sQuery(id+"F3.wireOp",EDGE,"E20.8.3"),sQuery(id+"F22.wireOp",EDGE,"E27.bottom"),sQuery(id+"F22.wireOp",EDGE,"E27.top"),sQuery(id+"F22.wireOp",EDGE,"E27.right")])]})]});
            var Q10;
            Q10=makeQuery(id+"F24.boolean.opBoolean","INTERSECT",EDGE,{"derivedFrom":[makeQuery(id+"F1.opRevolve","SWEPT_FACE",FACE,{"disambiguationData":[OSD([sQuery(id+"F0.wireOp",EDGE,"E4")])]}),makeQuery(id+"F24.opLoft","SWEPT_FACE",FACE,{"disambiguationData":[OSD([sQuery(id+"F3.wireOp",EDGE,"E20.9.0"),sQuery(id+"F3.wireOp",EDGE,"E20.9.1"),sQuery(id+"F3.wireOp",EDGE,"E20.9.3"),sQuery(id+"F22.wireOp",EDGE,"E28.1.1"),sQuery(id+"F22.wireOp",EDGE,"E28.1.2"),sQuery(id+"F22.wireOp",EDGE,"E28.1.3")])]})]});
            var Q11;
            {var subQ0=sQuery(id+"F3.wireOp",EDGE,"E20.10.3");var subQ1=sQuery(id+"F3.wireOp",EDGE,"E20.10.1");var subQ2=sQuery(id+"F3.wireOp",EDGE,"E20.10.0");var subQ81=sQuery(id+"F3.wireOp",EDGE,"E18.bottom");Q11=makeQuery(id+"F25.boolean.opBoolean","INTERSECT",EDGE,{"derivedFrom":[makeQuery(id+"F24.boolean.opBoolean","SPLIT",FACE,{"disambiguationData":[TD([makeQuery(id+"F5.opLoft","CAP_FACE",FACE,{"disambiguationData":[OSD([makeQuery(id+"F3.imprint","IMPRINT",FACE,{"disambiguationData":[TD([[makeQuery(id+"F3.imprint","IMPRINT",EDGE,{"derivedFrom":subQ81}),1.0]])]})])],"isStart":true})])],"derivedFrom":makeQuery(id+"F1.opRevolve","SWEPT_FACE",FACE,{"disambiguationData":[OSD([sQuery(id+"F0.wireOp",EDGE,"E4")])]})}),makeQuery(id+"F25.opLoft","SWEPT_FACE",FACE,{"disambiguationData":[OSD([subQ2,subQ1,subQ0,sQuery(id+"F22.wireOp",EDGE,"E28.2.1"),sQuery(id+"F22.wireOp",EDGE,"E28.2.2"),sQuery(id+"F22.wireOp",EDGE,"E28.2.3")])]})]});}
            var Q12;
            {var subQ0=sQuery(id+"F3.wireOp",EDGE,"E20.11.3");var subQ1=sQuery(id+"F3.wireOp",EDGE,"E20.11.1");var subQ2=sQuery(id+"F3.wireOp",EDGE,"E20.11.0");var subQ74=sQuery(id+"F3.wireOp",EDGE,"E18.bottom");var subQ77=makeQuery(id+"F5.opLoft","CAP_FACE",FACE,{"disambiguationData":[OSD([makeQuery(id+"F3.imprint","IMPRINT",FACE,{"disambiguationData":[TD([[makeQuery(id+"F3.imprint","IMPRINT",EDGE,{"derivedFrom":subQ74}),1.0]])]})])],"isStart":true});Q12=makeQuery(id+"F26.boolean.opBoolean","INTERSECT",EDGE,{"derivedFrom":[makeQuery(id+"F25.boolean.opBoolean","SPLIT",FACE,{"disambiguationData":[TD([subQ77])],"derivedFrom":makeQuery(id+"F24.boolean.opBoolean","SPLIT",FACE,{"disambiguationData":[TD([subQ77])],"derivedFrom":makeQuery(id+"F1.opRevolve","SWEPT_FACE",FACE,{"disambiguationData":[OSD([sQuery(id+"F0.wireOp",EDGE,"E4")])]})})}),makeQuery(id+"F26.opLoft","SWEPT_FACE",FACE,{"disambiguationData":[OSD([subQ2,subQ1,subQ0,sQuery(id+"F22.wireOp",EDGE,"E28.3.1"),sQuery(id+"F22.wireOp",EDGE,"E28.3.2"),sQuery(id+"F22.wireOp",EDGE,"E28.3.3")])]})]});}
            var Q13;
            {var subQ0=sQuery(id+"F3.wireOp",EDGE,"E20.12.3");var subQ1=sQuery(id+"F3.wireOp",EDGE,"E20.12.1");var subQ2=sQuery(id+"F3.wireOp",EDGE,"E20.12.0");var subQ70=sQuery(id+"F3.wireOp",EDGE,"E18.bottom");var subQ73=makeQuery(id+"F5.opLoft","CAP_FACE",FACE,{"disambiguationData":[OSD([makeQuery(id+"F3.imprint","IMPRINT",FACE,{"disambiguationData":[TD([[makeQuery(id+"F3.imprint","IMPRINT",EDGE,{"derivedFrom":subQ70}),1.0]])]})])],"isStart":true});Q13=makeQuery(id+"F27.boolean.opBoolean","INTERSECT",EDGE,{"derivedFrom":[makeQuery(id+"F26.boolean.opBoolean","SPLIT",FACE,{"disambiguationData":[TD([subQ73])],"derivedFrom":makeQuery(id+"F25.boolean.opBoolean","SPLIT",FACE,{"disambiguationData":[TD([subQ73])],"derivedFrom":makeQuery(id+"F24.boolean.opBoolean","SPLIT",FACE,{"disambiguationData":[TD([subQ73])],"derivedFrom":makeQuery(id+"F1.opRevolve","SWEPT_FACE",FACE,{"disambiguationData":[OSD([sQuery(id+"F0.wireOp",EDGE,"E4")])]})})})}),makeQuery(id+"F27.opLoft","SWEPT_FACE",FACE,{"disambiguationData":[OSD([subQ2,subQ1,subQ0,sQuery(id+"F22.wireOp",EDGE,"E28.4.1"),sQuery(id+"F22.wireOp",EDGE,"E28.4.2"),sQuery(id+"F22.wireOp",EDGE,"E28.4.3")])]})]});}
            var Q14;
            {var subQ0=sQuery(id+"F3.wireOp",EDGE,"E20.13.3");var subQ1=sQuery(id+"F3.wireOp",EDGE,"E20.13.1");var subQ2=sQuery(id+"F3.wireOp",EDGE,"E20.13.0");var subQ52=sQuery(id+"F3.wireOp",EDGE,"E18.bottom");var subQ55=makeQuery(id+"F5.opLoft","CAP_FACE",FACE,{"disambiguationData":[OSD([makeQuery(id+"F3.imprint","IMPRINT",FACE,{"disambiguationData":[TD([[makeQuery(id+"F3.imprint","IMPRINT",EDGE,{"derivedFrom":subQ52}),1.0]])]})])],"isStart":true});Q14=makeQuery(id+"F28.boolean.opBoolean","INTERSECT",EDGE,{"derivedFrom":[makeQuery(id+"F27.boolean.opBoolean","SPLIT",FACE,{"disambiguationData":[TD([subQ55])],"derivedFrom":makeQuery(id+"F26.boolean.opBoolean","SPLIT",FACE,{"disambiguationData":[TD([subQ55])],"derivedFrom":makeQuery(id+"F25.boolean.opBoolean","SPLIT",FACE,{"disambiguationData":[TD([subQ55])],"derivedFrom":makeQuery(id+"F24.boolean.opBoolean","SPLIT",FACE,{"disambiguationData":[TD([subQ55])],"derivedFrom":makeQuery(id+"F1.opRevolve","SWEPT_FACE",FACE,{"disambiguationData":[OSD([sQuery(id+"F0.wireOp",EDGE,"E4")])]})})})})}),makeQuery(id+"F28.opLoft","SWEPT_FACE",FACE,{"disambiguationData":[OSD([subQ2,subQ1,subQ0,sQuery(id+"F22.wireOp",EDGE,"E28.5.1"),sQuery(id+"F22.wireOp",EDGE,"E28.5.2"),sQuery(id+"F22.wireOp",EDGE,"E28.5.3")])]})]});}
            var Q15;
            {var subQ0=sQuery(id+"F3.wireOp",EDGE,"E20.14.3");var subQ1=sQuery(id+"F3.wireOp",EDGE,"E20.14.1");var subQ2=sQuery(id+"F3.wireOp",EDGE,"E20.14.0");var subQ41=sQuery(id+"F3.wireOp",EDGE,"E18.bottom");var subQ44=makeQuery(id+"F5.opLoft","CAP_FACE",FACE,{"disambiguationData":[OSD([makeQuery(id+"F3.imprint","IMPRINT",FACE,{"disambiguationData":[TD([[makeQuery(id+"F3.imprint","IMPRINT",EDGE,{"derivedFrom":subQ41}),1.0]])]})])],"isStart":true});Q15=makeQuery(id+"F29.boolean.opBoolean","INTERSECT",EDGE,{"derivedFrom":[makeQuery(id+"F28.boolean.opBoolean","SPLIT",FACE,{"disambiguationData":[TD([subQ44])],"derivedFrom":makeQuery(id+"F27.boolean.opBoolean","SPLIT",FACE,{"disambiguationData":[TD([subQ44])],"derivedFrom":makeQuery(id+"F26.boolean.opBoolean","SPLIT",FACE,{"disambiguationData":[TD([subQ44])],"derivedFrom":makeQuery(id+"F25.boolean.opBoolean","SPLIT",FACE,{"disambiguationData":[TD([subQ44])],"derivedFrom":makeQuery(id+"F24.boolean.opBoolean","SPLIT",FACE,{"disambiguationData":[TD([subQ44])],"derivedFrom":makeQuery(id+"F1.opRevolve","SWEPT_FACE",FACE,{"disambiguationData":[OSD([sQuery(id+"F0.wireOp",EDGE,"E4")])]})})})})})}),makeQuery(id+"F29.opLoft","SWEPT_FACE",FACE,{"disambiguationData":[OSD([subQ2,subQ1,subQ0,sQuery(id+"F22.wireOp",EDGE,"E28.6.1"),sQuery(id+"F22.wireOp",EDGE,"E28.6.2"),sQuery(id+"F22.wireOp",EDGE,"E28.6.3")])]})]});}
            var Q16;
            {var subQ0=sQuery(id+"F3.wireOp",EDGE,"E20.15.3");var subQ1=sQuery(id+"F3.wireOp",EDGE,"E20.15.1");var subQ2=sQuery(id+"F3.wireOp",EDGE,"E20.15.0");var subQ34=sQuery(id+"F3.wireOp",EDGE,"E18.bottom");var subQ37=makeQuery(id+"F5.opLoft","CAP_FACE",FACE,{"disambiguationData":[OSD([makeQuery(id+"F3.imprint","IMPRINT",FACE,{"disambiguationData":[TD([[makeQuery(id+"F3.imprint","IMPRINT",EDGE,{"derivedFrom":subQ34}),1.0]])]})])],"isStart":true});Q16=makeQuery(id+"F30.boolean.opBoolean","INTERSECT",EDGE,{"derivedFrom":[makeQuery(id+"F29.boolean.opBoolean","SPLIT",FACE,{"disambiguationData":[TD([subQ37])],"derivedFrom":makeQuery(id+"F28.boolean.opBoolean","SPLIT",FACE,{"disambiguationData":[TD([subQ37])],"derivedFrom":makeQuery(id+"F27.boolean.opBoolean","SPLIT",FACE,{"disambiguationData":[TD([subQ37])],"derivedFrom":makeQuery(id+"F26.boolean.opBoolean","SPLIT",FACE,{"disambiguationData":[TD([subQ37])],"derivedFrom":makeQuery(id+"F25.boolean.opBoolean","SPLIT",FACE,{"disambiguationData":[TD([subQ37])],"derivedFrom":makeQuery(id+"F24.boolean.opBoolean","SPLIT",FACE,{"disambiguationData":[TD([subQ37])],"derivedFrom":makeQuery(id+"F1.opRevolve","SWEPT_FACE",FACE,{"disambiguationData":[OSD([sQuery(id+"F0.wireOp",EDGE,"E4")])]})})})})})})}),makeQuery(id+"F30.opLoft","SWEPT_FACE",FACE,{"disambiguationData":[OSD([subQ2,subQ1,subQ0,sQuery(id+"F22.wireOp",EDGE,"E28.7.1"),sQuery(id+"F22.wireOp",EDGE,"E28.7.2"),sQuery(id+"F22.wireOp",EDGE,"E28.7.3")])]})]});}
            var Q17;
            {var subQ0=sQuery(id+"F3.wireOp",EDGE,"E18.left");var subQ1=sQuery(id+"F3.wireOp",EDGE,"E18.top");var subQ2=sQuery(id+"F3.wireOp",EDGE,"E18.bottom");var subQ48=makeQuery(id+"F5.opLoft","CAP_FACE",FACE,{"disambiguationData":[OSD([makeQuery(id+"F3.imprint","IMPRINT",FACE,{"disambiguationData":[TD([[makeQuery(id+"F3.imprint","IMPRINT",EDGE,{"derivedFrom":subQ2}),1.0]])]})])],"isStart":true});Q17=makeQuery(id+"F31.boolean.opBoolean","INTERSECT",EDGE,{"derivedFrom":[makeQuery(id+"F30.boolean.opBoolean","SPLIT",FACE,{"disambiguationData":[TD([subQ48])],"derivedFrom":makeQuery(id+"F29.boolean.opBoolean","SPLIT",FACE,{"disambiguationData":[TD([subQ48])],"derivedFrom":makeQuery(id+"F28.boolean.opBoolean","SPLIT",FACE,{"disambiguationData":[TD([subQ48])],"derivedFrom":makeQuery(id+"F27.boolean.opBoolean","SPLIT",FACE,{"disambiguationData":[TD([subQ48])],"derivedFrom":makeQuery(id+"F26.boolean.opBoolean","SPLIT",FACE,{"disambiguationData":[TD([subQ48])],"derivedFrom":makeQuery(id+"F25.boolean.opBoolean","SPLIT",FACE,{"disambiguationData":[TD([subQ48])],"derivedFrom":makeQuery(id+"F24.boolean.opBoolean","SPLIT",FACE,{"disambiguationData":[TD([subQ48])],"derivedFrom":makeQuery(id+"F1.opRevolve","SWEPT_FACE",FACE,{"disambiguationData":[OSD([sQuery(id+"F0.wireOp",EDGE,"E4")])]})})})})})})})}),makeQuery(id+"F31.opLoft","SWEPT_FACE",FACE,{"disambiguationData":[OSD([subQ2,subQ1,subQ0,sQuery(id+"F22.wireOp",EDGE,"E28.8.1"),sQuery(id+"F22.wireOp",EDGE,"E28.8.2"),sQuery(id+"F22.wireOp",EDGE,"E28.8.3")])]})]});}
            var Q18;
            Q18=makeQuery(id+"F5.boolean.opBoolean","INTERSECT",EDGE,{"derivedFrom":[makeQuery(id+"F1.opRevolve","SWEPT_FACE",FACE,{"disambiguationData":[OSD([sQuery(id+"F0.wireOp",EDGE,"E4")])]}),makeQuery(id+"F5.opLoft","SWEPT_FACE",FACE,{"disambiguationData":[OSD([sQuery(id+"F3.wireOp",EDGE,"E18.bottom"),sQuery(id+"F3.wireOp",EDGE,"E18.top"),sQuery(id+"F3.wireOp",EDGE,"E18.left"),sQuery(id+"F4.wireOp",EDGE,"E21"),sQuery(id+"F4.wireOp",EDGE,"E22"),sQuery(id+"F4.wireOp",EDGE,"E23")])]})]});
            var Q19;
            Q19=makeQuery(id+"F6.boolean.opBoolean","INTERSECT",EDGE,{"derivedFrom":[makeQuery(id+"F1.opRevolve","SWEPT_FACE",FACE,{"disambiguationData":[OSD([sQuery(id+"F0.wireOp",EDGE,"E4")])]}),makeQuery(id+"F6.opLoft","SWEPT_FACE",FACE,{"disambiguationData":[OSD([sQuery(id+"F3.wireOp",EDGE,"E20.15.0"),sQuery(id+"F3.wireOp",EDGE,"E20.15.1"),sQuery(id+"F3.wireOp",EDGE,"E20.15.3"),sQuery(id+"F4.wireOp",EDGE,"E26.15.0"),sQuery(id+"F4.wireOp",EDGE,"E26.15.2"),sQuery(id+"F4.wireOp",EDGE,"E26.15.3")])]})]});
            var Q20;
            Q20=makeQuery(id+"F7.boolean.opBoolean","INTERSECT",EDGE,{"derivedFrom":[makeQuery(id+"F1.opRevolve","SWEPT_FACE",FACE,{"disambiguationData":[OSD([sQuery(id+"F0.wireOp",EDGE,"E4")])]}),makeQuery(id+"F7.opLoft","SWEPT_FACE",FACE,{"disambiguationData":[OSD([sQuery(id+"F3.wireOp",EDGE,"E20.14.0"),sQuery(id+"F3.wireOp",EDGE,"E20.14.1"),sQuery(id+"F3.wireOp",EDGE,"E20.14.3"),sQuery(id+"F4.wireOp",EDGE,"E26.14.0"),sQuery(id+"F4.wireOp",EDGE,"E26.14.2"),sQuery(id+"F4.wireOp",EDGE,"E26.14.3")])]})]});
            var Q21;
            Q21=makeQuery(id+"F8.boolean.opBoolean","INTERSECT",EDGE,{"derivedFrom":[makeQuery(id+"F1.opRevolve","SWEPT_FACE",FACE,{"disambiguationData":[OSD([sQuery(id+"F0.wireOp",EDGE,"E4")])]}),makeQuery(id+"F8.opLoft","SWEPT_FACE",FACE,{"disambiguationData":[OSD([sQuery(id+"F3.wireOp",EDGE,"E20.13.0"),sQuery(id+"F3.wireOp",EDGE,"E20.13.1"),sQuery(id+"F3.wireOp",EDGE,"E20.13.3"),sQuery(id+"F4.wireOp",EDGE,"E26.13.0"),sQuery(id+"F4.wireOp",EDGE,"E26.13.2"),sQuery(id+"F4.wireOp",EDGE,"E26.13.3")])]})]});
            var Q22;
            Q22=makeQuery(id+"F9.boolean.opBoolean","INTERSECT",EDGE,{"derivedFrom":[makeQuery(id+"F1.opRevolve","SWEPT_FACE",FACE,{"disambiguationData":[OSD([sQuery(id+"F0.wireOp",EDGE,"E4")])]}),makeQuery(id+"F9.opLoft","SWEPT_FACE",FACE,{"disambiguationData":[OSD([sQuery(id+"F3.wireOp",EDGE,"E20.12.0"),sQuery(id+"F3.wireOp",EDGE,"E20.12.1"),sQuery(id+"F3.wireOp",EDGE,"E20.12.3"),sQuery(id+"F4.wireOp",EDGE,"E26.12.0"),sQuery(id+"F4.wireOp",EDGE,"E26.12.2"),sQuery(id+"F4.wireOp",EDGE,"E26.12.3")])]})]});
            var Q23;
            Q23=makeQuery(id+"F10.boolean.opBoolean","INTERSECT",EDGE,{"derivedFrom":[makeQuery(id+"F1.opRevolve","SWEPT_FACE",FACE,{"disambiguationData":[OSD([sQuery(id+"F0.wireOp",EDGE,"E4")])]}),makeQuery(id+"F10.opLoft","SWEPT_FACE",FACE,{"disambiguationData":[OSD([sQuery(id+"F3.wireOp",EDGE,"E20.11.0"),sQuery(id+"F3.wireOp",EDGE,"E20.11.1"),sQuery(id+"F3.wireOp",EDGE,"E20.11.3"),sQuery(id+"F4.wireOp",EDGE,"E26.11.0"),sQuery(id+"F4.wireOp",EDGE,"E26.11.2"),sQuery(id+"F4.wireOp",EDGE,"E26.11.3")])]})]});
            var Q24;
            Q24=makeQuery(id+"F11.boolean.opBoolean","INTERSECT",EDGE,{"derivedFrom":[makeQuery(id+"F1.opRevolve","SWEPT_FACE",FACE,{"disambiguationData":[OSD([sQuery(id+"F0.wireOp",EDGE,"E4")])]}),makeQuery(id+"F11.opLoft","SWEPT_FACE",FACE,{"disambiguationData":[OSD([sQuery(id+"F3.wireOp",EDGE,"E20.10.0"),sQuery(id+"F3.wireOp",EDGE,"E20.10.1"),sQuery(id+"F3.wireOp",EDGE,"E20.10.3"),sQuery(id+"F4.wireOp",EDGE,"E26.10.0"),sQuery(id+"F4.wireOp",EDGE,"E26.10.2"),sQuery(id+"F4.wireOp",EDGE,"E26.10.3")])]})]});
            var Q25;
            Q25=makeQuery(id+"F12.boolean.opBoolean","INTERSECT",EDGE,{"derivedFrom":[makeQuery(id+"F1.opRevolve","SWEPT_FACE",FACE,{"disambiguationData":[OSD([sQuery(id+"F0.wireOp",EDGE,"E4")])]}),makeQuery(id+"F12.opLoft","SWEPT_FACE",FACE,{"disambiguationData":[OSD([sQuery(id+"F3.wireOp",EDGE,"E20.9.0"),sQuery(id+"F3.wireOp",EDGE,"E20.9.1"),sQuery(id+"F3.wireOp",EDGE,"E20.9.3"),sQuery(id+"F4.wireOp",EDGE,"E26.9.0"),sQuery(id+"F4.wireOp",EDGE,"E26.9.2"),sQuery(id+"F4.wireOp",EDGE,"E26.9.3")])]})]});
            var Q26;
            Q26=makeQuery(id+"F13.boolean.opBoolean","INTERSECT",EDGE,{"derivedFrom":[makeQuery(id+"F1.opRevolve","SWEPT_FACE",FACE,{"disambiguationData":[OSD([sQuery(id+"F0.wireOp",EDGE,"E4")])]}),makeQuery(id+"F13.opLoft","SWEPT_FACE",FACE,{"disambiguationData":[OSD([sQuery(id+"F3.wireOp",EDGE,"E20.8.0"),sQuery(id+"F3.wireOp",EDGE,"E20.8.1"),sQuery(id+"F3.wireOp",EDGE,"E20.8.3"),sQuery(id+"F4.wireOp",EDGE,"E26.8.0"),sQuery(id+"F4.wireOp",EDGE,"E26.8.2"),sQuery(id+"F4.wireOp",EDGE,"E26.8.3")])]})]});
            var Q27;
            Q27=makeQuery(id+"F14.boolean.opBoolean","INTERSECT",EDGE,{"derivedFrom":[makeQuery(id+"F1.opRevolve","SWEPT_FACE",FACE,{"disambiguationData":[OSD([sQuery(id+"F0.wireOp",EDGE,"E4")])]}),makeQuery(id+"F14.opLoft","SWEPT_FACE",FACE,{"disambiguationData":[OSD([sQuery(id+"F3.wireOp",EDGE,"E20.7.0"),sQuery(id+"F3.wireOp",EDGE,"E20.7.1"),sQuery(id+"F3.wireOp",EDGE,"E20.7.3"),sQuery(id+"F4.wireOp",EDGE,"E26.7.0"),sQuery(id+"F4.wireOp",EDGE,"E26.7.2"),sQuery(id+"F4.wireOp",EDGE,"E26.7.3")])]})]});
            var Q28;
            Q28=makeQuery(id+"F15.boolean.opBoolean","INTERSECT",EDGE,{"derivedFrom":[makeQuery(id+"F1.opRevolve","SWEPT_FACE",FACE,{"disambiguationData":[OSD([sQuery(id+"F0.wireOp",EDGE,"E4")])]}),makeQuery(id+"F15.opLoft","SWEPT_FACE",FACE,{"disambiguationData":[OSD([sQuery(id+"F3.wireOp",EDGE,"E20.6.0"),sQuery(id+"F3.wireOp",EDGE,"E20.6.1"),sQuery(id+"F3.wireOp",EDGE,"E20.6.3"),sQuery(id+"F4.wireOp",EDGE,"E26.6.0"),sQuery(id+"F4.wireOp",EDGE,"E26.6.2"),sQuery(id+"F4.wireOp",EDGE,"E26.6.3")])]})]});
            var Q29;
            Q29=makeQuery(id+"F16.boolean.opBoolean","INTERSECT",EDGE,{"derivedFrom":[makeQuery(id+"F1.opRevolve","SWEPT_FACE",FACE,{"disambiguationData":[OSD([sQuery(id+"F0.wireOp",EDGE,"E4")])]}),makeQuery(id+"F16.opLoft","SWEPT_FACE",FACE,{"disambiguationData":[OSD([sQuery(id+"F3.wireOp",EDGE,"E20.5.0"),sQuery(id+"F3.wireOp",EDGE,"E20.5.1"),sQuery(id+"F3.wireOp",EDGE,"E20.5.3"),sQuery(id+"F4.wireOp",EDGE,"E26.5.0"),sQuery(id+"F4.wireOp",EDGE,"E26.5.2"),sQuery(id+"F4.wireOp",EDGE,"E26.5.3")])]})]});
            var Q30;
            Q30=makeQuery(id+"F17.boolean.opBoolean","INTERSECT",EDGE,{"derivedFrom":[makeQuery(id+"F1.opRevolve","SWEPT_FACE",FACE,{"disambiguationData":[OSD([sQuery(id+"F0.wireOp",EDGE,"E4")])]}),makeQuery(id+"F17.opLoft","SWEPT_FACE",FACE,{"disambiguationData":[OSD([sQuery(id+"F3.wireOp",EDGE,"E20.4.0"),sQuery(id+"F3.wireOp",EDGE,"E20.4.1"),sQuery(id+"F3.wireOp",EDGE,"E20.4.3"),sQuery(id+"F4.wireOp",EDGE,"E26.4.0"),sQuery(id+"F4.wireOp",EDGE,"E26.4.2"),sQuery(id+"F4.wireOp",EDGE,"E26.4.3")])]})]});
            var Q31;
            Q31=makeQuery(id+"F18.boolean.opBoolean","INTERSECT",EDGE,{"derivedFrom":[makeQuery(id+"F1.opRevolve","SWEPT_FACE",FACE,{"disambiguationData":[OSD([sQuery(id+"F0.wireOp",EDGE,"E4")])]}),makeQuery(id+"F18.opLoft","SWEPT_FACE",FACE,{"disambiguationData":[OSD([sQuery(id+"F3.wireOp",EDGE,"E20.3.0"),sQuery(id+"F3.wireOp",EDGE,"E20.3.1"),sQuery(id+"F3.wireOp",EDGE,"E20.3.3"),sQuery(id+"F4.wireOp",EDGE,"E26.3.0"),sQuery(id+"F4.wireOp",EDGE,"E26.3.2"),sQuery(id+"F4.wireOp",EDGE,"E26.3.3")])]})]});
            fillet(context, id + "F45", {"entities" : qUnion([Q0, Q1, Q2, Q3, Q4, Q5, Q6, Q7, Q8, Q9, Q10, Q11, Q12, Q13, Q14, Q15, Q16, Q17, Q18, Q19, Q20, Q21, Q22, Q23, Q24, Q25, Q26, Q27, Q28, Q29, Q30, Q31]), "radius" : 3 * mm, "tangentPropagation" : true, "allowEdgeOverflow" : false});
        }
        {
            var Q0;
            Q0=makeQuery(id+"F1.opRevolve","SWEPT_EDGE",EDGE,{"disambiguationData":[OSD([sQuery(id+"F0.wireOp",EDGE,"M0De9DZ8-1zJs-ubri-npQ8-jmgKs2AWA0kd"),sQuery(id+"F0.wireOp",EDGE,"E5")])]});
            var Q1;
            Q1=makeQuery(id+"F1.opRevolve","SWEPT_EDGE",EDGE,{"disambiguationData":[OSD([sQuery(id+"F0.wireOp",EDGE,"cHHVOKxT-xBtR-EdTY-fGsc-esJYpbiU2zwx"),sQuery(id+"F0.wireOp",EDGE,"E6")])]});
            chamfer(context, id + "F46", {"entities" : qUnion([Q0, Q1]), "width" : 2 * mm, "tangentPropagation" : true});
        }
        {
            var Q0;
            {var subQ0=sQuery(id+"F41.wireOp",EDGE,"E35");var subQ1=sQuery(id+"F4.wireOp",EDGE,"E26.3.3");var subQ2=sQuery(id+"F4.wireOp",EDGE,"E26.3.2");var subQ3=sQuery(id+"F3.wireOp",EDGE,"E20.3.3");var subQ4=sQuery(id+"F3.wireOp",EDGE,"E20.3.1");var subQ5=sQuery(id+"F41.wireOp",EDGE,"E36");Q0=makeQuery(id+"F42.boolean.opBoolean","COPY",EDGE,{"disambiguationData":[TD([makeQuery(id+"F18.opLoft","SWEPT_FACE",FACE,{"disambiguationData":[OSD([sQuery(id+"F3.wireOp",EDGE,"E20.3.0"),subQ4,subQ3,sQuery(id+"F4.wireOp",EDGE,"E26.3.0"),subQ2,subQ1])]})])],"derivedFrom":makeQuery(id+"F42.opRevolve","SWEPT_EDGE",EDGE,{"disambiguationData":[OSD([subQ0,subQ5])]})});}
            var Q1;
            {var subQ0=sQuery(id+"F4.wireOp",EDGE,"E26.2.3");var subQ1=sQuery(id+"F4.wireOp",EDGE,"E26.2.2");var subQ2=sQuery(id+"F3.wireOp",EDGE,"E20.2.3");var subQ3=sQuery(id+"F3.wireOp",EDGE,"E20.2.1");var subQ4=sQuery(id+"F41.wireOp",EDGE,"E36");var subQ5=sQuery(id+"F41.wireOp",EDGE,"E35");Q1=makeQuery(id+"F42.boolean.opBoolean","COPY",EDGE,{"disambiguationData":[TD([makeQuery(id+"F19.opLoft","SWEPT_FACE",FACE,{"disambiguationData":[OSD([sQuery(id+"F3.wireOp",EDGE,"E20.2.0"),subQ3,subQ2,sQuery(id+"F4.wireOp",EDGE,"E26.2.0"),subQ1,subQ0])]})])],"derivedFrom":makeQuery(id+"F42.opRevolve","SWEPT_EDGE",EDGE,{"disambiguationData":[OSD([subQ5,subQ4])]})});}
            var Q2;
            {var subQ0=sQuery(id+"F4.wireOp",EDGE,"E26.1.3");var subQ1=sQuery(id+"F4.wireOp",EDGE,"E26.1.2");var subQ2=sQuery(id+"F3.wireOp",EDGE,"E20.1.3");var subQ3=sQuery(id+"F3.wireOp",EDGE,"E20.1.1");var subQ4=sQuery(id+"F41.wireOp",EDGE,"E35");var subQ5=sQuery(id+"F41.wireOp",EDGE,"E36");Q2=makeQuery(id+"F42.boolean.opBoolean","COPY",EDGE,{"disambiguationData":[TD([makeQuery(id+"F20.opLoft","SWEPT_FACE",FACE,{"disambiguationData":[OSD([sQuery(id+"F3.wireOp",EDGE,"E20.1.0"),subQ3,subQ2,sQuery(id+"F4.wireOp",EDGE,"E26.1.0"),subQ1,subQ0])]})])],"derivedFrom":makeQuery(id+"F42.opRevolve","SWEPT_EDGE",EDGE,{"disambiguationData":[OSD([subQ4,subQ5])]})});}
            var Q3;
            {var subQ0=sQuery(id+"F41.wireOp",EDGE,"E35");var subQ1=sQuery(id+"F4.wireOp",EDGE,"E23");var subQ2=sQuery(id+"F4.wireOp",EDGE,"E22");var subQ3=sQuery(id+"F3.wireOp",EDGE,"E18.top");var subQ4=sQuery(id+"F3.wireOp",EDGE,"E18.bottom");var subQ5=sQuery(id+"F41.wireOp",EDGE,"E36");Q3=makeQuery(id+"F42.boolean.opBoolean","COPY",EDGE,{"disambiguationData":[TD([makeQuery(id+"F5.opLoft","SWEPT_FACE",FACE,{"disambiguationData":[OSD([subQ4,subQ3,sQuery(id+"F3.wireOp",EDGE,"E18.left"),sQuery(id+"F4.wireOp",EDGE,"E21"),subQ2,subQ1])]})])],"derivedFrom":makeQuery(id+"F42.opRevolve","SWEPT_EDGE",EDGE,{"disambiguationData":[OSD([subQ0,subQ5])]})});}
            var Q4;
            {var subQ0=sQuery(id+"F41.wireOp",EDGE,"E35");var subQ1=sQuery(id+"F4.wireOp",EDGE,"E26.4.3");var subQ2=sQuery(id+"F4.wireOp",EDGE,"E26.4.2");var subQ3=sQuery(id+"F3.wireOp",EDGE,"E20.4.3");var subQ4=sQuery(id+"F3.wireOp",EDGE,"E20.4.1");var subQ5=sQuery(id+"F41.wireOp",EDGE,"E36");Q4=makeQuery(id+"F42.boolean.opBoolean","COPY",EDGE,{"disambiguationData":[TD([makeQuery(id+"F17.opLoft","SWEPT_FACE",FACE,{"disambiguationData":[OSD([sQuery(id+"F3.wireOp",EDGE,"E20.4.0"),subQ4,subQ3,sQuery(id+"F4.wireOp",EDGE,"E26.4.0"),subQ2,subQ1])]})])],"derivedFrom":makeQuery(id+"F42.opRevolve","SWEPT_EDGE",EDGE,{"disambiguationData":[OSD([subQ0,subQ5])]})});}
            var Q5;
            {var subQ0=sQuery(id+"F41.wireOp",EDGE,"E35");var subQ1=sQuery(id+"F4.wireOp",EDGE,"E26.5.3");var subQ2=sQuery(id+"F4.wireOp",EDGE,"E26.5.2");var subQ3=sQuery(id+"F3.wireOp",EDGE,"E20.5.3");var subQ4=sQuery(id+"F3.wireOp",EDGE,"E20.5.1");var subQ5=sQuery(id+"F41.wireOp",EDGE,"E36");Q5=makeQuery(id+"F42.boolean.opBoolean","COPY",EDGE,{"disambiguationData":[TD([makeQuery(id+"F16.opLoft","SWEPT_FACE",FACE,{"disambiguationData":[OSD([sQuery(id+"F3.wireOp",EDGE,"E20.5.0"),subQ4,subQ3,sQuery(id+"F4.wireOp",EDGE,"E26.5.0"),subQ2,subQ1])]})])],"derivedFrom":makeQuery(id+"F42.opRevolve","SWEPT_EDGE",EDGE,{"disambiguationData":[OSD([subQ0,subQ5])]})});}
            var Q6;
            {var subQ0=sQuery(id+"F41.wireOp",EDGE,"E35");var subQ1=sQuery(id+"F4.wireOp",EDGE,"E26.6.3");var subQ2=sQuery(id+"F4.wireOp",EDGE,"E26.6.2");var subQ3=sQuery(id+"F3.wireOp",EDGE,"E20.6.3");var subQ4=sQuery(id+"F3.wireOp",EDGE,"E20.6.1");var subQ5=sQuery(id+"F41.wireOp",EDGE,"E36");Q6=makeQuery(id+"F42.boolean.opBoolean","COPY",EDGE,{"disambiguationData":[TD([makeQuery(id+"F15.opLoft","SWEPT_FACE",FACE,{"disambiguationData":[OSD([sQuery(id+"F3.wireOp",EDGE,"E20.6.0"),subQ4,subQ3,sQuery(id+"F4.wireOp",EDGE,"E26.6.0"),subQ2,subQ1])]})])],"derivedFrom":makeQuery(id+"F42.opRevolve","SWEPT_EDGE",EDGE,{"disambiguationData":[OSD([subQ0,subQ5])]})});}
            var Q7;
            {var subQ0=sQuery(id+"F41.wireOp",EDGE,"E35");var subQ1=sQuery(id+"F4.wireOp",EDGE,"E26.7.3");var subQ2=sQuery(id+"F4.wireOp",EDGE,"E26.7.2");var subQ3=sQuery(id+"F3.wireOp",EDGE,"E20.7.3");var subQ4=sQuery(id+"F3.wireOp",EDGE,"E20.7.1");var subQ5=sQuery(id+"F41.wireOp",EDGE,"E36");Q7=makeQuery(id+"F42.boolean.opBoolean","COPY",EDGE,{"disambiguationData":[TD([makeQuery(id+"F14.opLoft","SWEPT_FACE",FACE,{"disambiguationData":[OSD([sQuery(id+"F3.wireOp",EDGE,"E20.7.0"),subQ4,subQ3,sQuery(id+"F4.wireOp",EDGE,"E26.7.0"),subQ2,subQ1])]})])],"derivedFrom":makeQuery(id+"F42.opRevolve","SWEPT_EDGE",EDGE,{"disambiguationData":[OSD([subQ0,subQ5])]})});}
            var Q8;
            {var subQ0=sQuery(id+"F41.wireOp",EDGE,"E35");var subQ1=sQuery(id+"F4.wireOp",EDGE,"E26.8.3");var subQ2=sQuery(id+"F4.wireOp",EDGE,"E26.8.2");var subQ3=sQuery(id+"F3.wireOp",EDGE,"E20.8.3");var subQ4=sQuery(id+"F3.wireOp",EDGE,"E20.8.1");var subQ5=sQuery(id+"F41.wireOp",EDGE,"E36");Q8=makeQuery(id+"F42.boolean.opBoolean","COPY",EDGE,{"disambiguationData":[TD([makeQuery(id+"F13.opLoft","SWEPT_FACE",FACE,{"disambiguationData":[OSD([sQuery(id+"F3.wireOp",EDGE,"E20.8.0"),subQ4,subQ3,sQuery(id+"F4.wireOp",EDGE,"E26.8.0"),subQ2,subQ1])]})])],"derivedFrom":makeQuery(id+"F42.opRevolve","SWEPT_EDGE",EDGE,{"disambiguationData":[OSD([subQ0,subQ5])]})});}
            var Q9;
            {var subQ0=sQuery(id+"F41.wireOp",EDGE,"E35");var subQ1=sQuery(id+"F4.wireOp",EDGE,"E26.9.3");var subQ2=sQuery(id+"F4.wireOp",EDGE,"E26.9.2");var subQ3=sQuery(id+"F3.wireOp",EDGE,"E20.9.3");var subQ4=sQuery(id+"F3.wireOp",EDGE,"E20.9.1");var subQ5=sQuery(id+"F41.wireOp",EDGE,"E36");Q9=makeQuery(id+"F42.boolean.opBoolean","COPY",EDGE,{"disambiguationData":[TD([makeQuery(id+"F12.opLoft","SWEPT_FACE",FACE,{"disambiguationData":[OSD([sQuery(id+"F3.wireOp",EDGE,"E20.9.0"),subQ4,subQ3,sQuery(id+"F4.wireOp",EDGE,"E26.9.0"),subQ2,subQ1])]})])],"derivedFrom":makeQuery(id+"F42.opRevolve","SWEPT_EDGE",EDGE,{"disambiguationData":[OSD([subQ0,subQ5])]})});}
            var Q10;
            {var subQ0=sQuery(id+"F41.wireOp",EDGE,"E35");var subQ1=sQuery(id+"F4.wireOp",EDGE,"E26.10.3");var subQ2=sQuery(id+"F4.wireOp",EDGE,"E26.10.2");var subQ3=sQuery(id+"F3.wireOp",EDGE,"E20.10.3");var subQ4=sQuery(id+"F3.wireOp",EDGE,"E20.10.1");var subQ5=sQuery(id+"F41.wireOp",EDGE,"E36");Q10=makeQuery(id+"F42.boolean.opBoolean","COPY",EDGE,{"disambiguationData":[TD([makeQuery(id+"F11.opLoft","SWEPT_FACE",FACE,{"disambiguationData":[OSD([sQuery(id+"F3.wireOp",EDGE,"E20.10.0"),subQ4,subQ3,sQuery(id+"F4.wireOp",EDGE,"E26.10.0"),subQ2,subQ1])]})])],"derivedFrom":makeQuery(id+"F42.opRevolve","SWEPT_EDGE",EDGE,{"disambiguationData":[OSD([subQ0,subQ5])]})});}
            var Q11;
            {var subQ0=sQuery(id+"F4.wireOp",EDGE,"E26.11.3");var subQ1=sQuery(id+"F4.wireOp",EDGE,"E26.11.2");var subQ2=sQuery(id+"F3.wireOp",EDGE,"E20.11.3");var subQ3=sQuery(id+"F3.wireOp",EDGE,"E20.11.1");var subQ4=sQuery(id+"F41.wireOp",EDGE,"E35");var subQ5=sQuery(id+"F41.wireOp",EDGE,"E36");Q11=makeQuery(id+"F42.boolean.opBoolean","COPY",EDGE,{"disambiguationData":[TD([makeQuery(id+"F10.opLoft","SWEPT_FACE",FACE,{"disambiguationData":[OSD([sQuery(id+"F3.wireOp",EDGE,"E20.11.0"),subQ3,subQ2,sQuery(id+"F4.wireOp",EDGE,"E26.11.0"),subQ1,subQ0])]})])],"derivedFrom":makeQuery(id+"F42.opRevolve","SWEPT_EDGE",EDGE,{"disambiguationData":[OSD([subQ4,subQ5])]})});}
            var Q12;
            {var subQ0=sQuery(id+"F4.wireOp",EDGE,"E26.12.3");var subQ1=sQuery(id+"F4.wireOp",EDGE,"E26.12.2");var subQ2=sQuery(id+"F3.wireOp",EDGE,"E20.12.3");var subQ3=sQuery(id+"F3.wireOp",EDGE,"E20.12.1");var subQ4=sQuery(id+"F41.wireOp",EDGE,"E35");var subQ5=sQuery(id+"F41.wireOp",EDGE,"E36");Q12=makeQuery(id+"F42.boolean.opBoolean","COPY",EDGE,{"disambiguationData":[TD([makeQuery(id+"F9.opLoft","SWEPT_FACE",FACE,{"disambiguationData":[OSD([sQuery(id+"F3.wireOp",EDGE,"E20.12.0"),subQ3,subQ2,sQuery(id+"F4.wireOp",EDGE,"E26.12.0"),subQ1,subQ0])]})])],"derivedFrom":makeQuery(id+"F42.opRevolve","SWEPT_EDGE",EDGE,{"disambiguationData":[OSD([subQ4,subQ5])]})});}
            var Q13;
            {var subQ0=sQuery(id+"F41.wireOp",EDGE,"E35");var subQ1=sQuery(id+"F4.wireOp",EDGE,"E26.13.3");var subQ2=sQuery(id+"F4.wireOp",EDGE,"E26.13.2");var subQ3=sQuery(id+"F3.wireOp",EDGE,"E20.13.3");var subQ4=sQuery(id+"F3.wireOp",EDGE,"E20.13.1");var subQ5=sQuery(id+"F41.wireOp",EDGE,"E36");Q13=makeQuery(id+"F42.boolean.opBoolean","COPY",EDGE,{"disambiguationData":[TD([makeQuery(id+"F8.opLoft","SWEPT_FACE",FACE,{"disambiguationData":[OSD([sQuery(id+"F3.wireOp",EDGE,"E20.13.0"),subQ4,subQ3,sQuery(id+"F4.wireOp",EDGE,"E26.13.0"),subQ2,subQ1])]})])],"derivedFrom":makeQuery(id+"F42.opRevolve","SWEPT_EDGE",EDGE,{"disambiguationData":[OSD([subQ0,subQ5])]})});}
            var Q14;
            {var subQ0=sQuery(id+"F41.wireOp",EDGE,"E35");var subQ1=sQuery(id+"F4.wireOp",EDGE,"E26.14.3");var subQ2=sQuery(id+"F4.wireOp",EDGE,"E26.14.2");var subQ3=sQuery(id+"F3.wireOp",EDGE,"E20.14.3");var subQ4=sQuery(id+"F3.wireOp",EDGE,"E20.14.1");var subQ5=sQuery(id+"F41.wireOp",EDGE,"E36");Q14=makeQuery(id+"F42.boolean.opBoolean","COPY",EDGE,{"disambiguationData":[TD([makeQuery(id+"F7.opLoft","SWEPT_FACE",FACE,{"disambiguationData":[OSD([sQuery(id+"F3.wireOp",EDGE,"E20.14.0"),subQ4,subQ3,sQuery(id+"F4.wireOp",EDGE,"E26.14.0"),subQ2,subQ1])]})])],"derivedFrom":makeQuery(id+"F42.opRevolve","SWEPT_EDGE",EDGE,{"disambiguationData":[OSD([subQ0,subQ5])]})});}
            var Q15;
            {var subQ0=sQuery(id+"F4.wireOp",EDGE,"E26.15.3");var subQ1=sQuery(id+"F4.wireOp",EDGE,"E26.15.2");var subQ2=sQuery(id+"F3.wireOp",EDGE,"E20.15.3");var subQ3=sQuery(id+"F3.wireOp",EDGE,"E20.15.1");var subQ4=sQuery(id+"F41.wireOp",EDGE,"E35");var subQ5=sQuery(id+"F41.wireOp",EDGE,"E36");Q15=makeQuery(id+"F42.boolean.opBoolean","COPY",EDGE,{"disambiguationData":[TD([makeQuery(id+"F6.opLoft","SWEPT_FACE",FACE,{"disambiguationData":[OSD([sQuery(id+"F3.wireOp",EDGE,"E20.15.0"),subQ3,subQ2,sQuery(id+"F4.wireOp",EDGE,"E26.15.0"),subQ1,subQ0])]})])],"derivedFrom":makeQuery(id+"F42.opRevolve","SWEPT_EDGE",EDGE,{"disambiguationData":[OSD([subQ4,subQ5])]})});}
            var Q16;
            {var subQ0=sQuery(id+"F41.wireOp",EDGE,"E37");var subQ1=sQuery(id+"F22.wireOp",EDGE,"E28.7.3");var subQ2=sQuery(id+"F22.wireOp",EDGE,"E28.7.2");var subQ3=sQuery(id+"F3.wireOp",EDGE,"E20.15.3");var subQ4=sQuery(id+"F3.wireOp",EDGE,"E20.15.1");var subQ5=sQuery(id+"F41.wireOp",EDGE,"E38");Q16=makeQuery(id+"F42.boolean.opBoolean","COPY",EDGE,{"disambiguationData":[TD([makeQuery(id+"F30.opLoft","SWEPT_FACE",FACE,{"disambiguationData":[OSD([sQuery(id+"F3.wireOp",EDGE,"E20.15.0"),subQ4,subQ3,sQuery(id+"F22.wireOp",EDGE,"E28.7.1"),subQ2,subQ1])]})])],"derivedFrom":makeQuery(id+"F42.opRevolve","SWEPT_EDGE",EDGE,{"disambiguationData":[OSD([subQ0,subQ5])]})});}
            var Q17;
            {var subQ0=sQuery(id+"F41.wireOp",EDGE,"E37");var subQ1=sQuery(id+"F22.wireOp",EDGE,"E28.6.3");var subQ2=sQuery(id+"F22.wireOp",EDGE,"E28.6.2");var subQ3=sQuery(id+"F3.wireOp",EDGE,"E20.14.3");var subQ4=sQuery(id+"F3.wireOp",EDGE,"E20.14.1");var subQ5=sQuery(id+"F41.wireOp",EDGE,"E38");Q17=makeQuery(id+"F42.boolean.opBoolean","COPY",EDGE,{"disambiguationData":[TD([makeQuery(id+"F29.opLoft","SWEPT_FACE",FACE,{"disambiguationData":[OSD([sQuery(id+"F3.wireOp",EDGE,"E20.14.0"),subQ4,subQ3,sQuery(id+"F22.wireOp",EDGE,"E28.6.1"),subQ2,subQ1])]})])],"derivedFrom":makeQuery(id+"F42.opRevolve","SWEPT_EDGE",EDGE,{"disambiguationData":[OSD([subQ0,subQ5])]})});}
            var Q18;
            {var subQ0=sQuery(id+"F41.wireOp",EDGE,"E37");var subQ1=sQuery(id+"F22.wireOp",EDGE,"E28.5.3");var subQ2=sQuery(id+"F22.wireOp",EDGE,"E28.5.2");var subQ3=sQuery(id+"F3.wireOp",EDGE,"E20.13.3");var subQ4=sQuery(id+"F3.wireOp",EDGE,"E20.13.1");var subQ5=sQuery(id+"F41.wireOp",EDGE,"E38");Q18=makeQuery(id+"F42.boolean.opBoolean","COPY",EDGE,{"disambiguationData":[TD([makeQuery(id+"F28.opLoft","SWEPT_FACE",FACE,{"disambiguationData":[OSD([sQuery(id+"F3.wireOp",EDGE,"E20.13.0"),subQ4,subQ3,sQuery(id+"F22.wireOp",EDGE,"E28.5.1"),subQ2,subQ1])]})])],"derivedFrom":makeQuery(id+"F42.opRevolve","SWEPT_EDGE",EDGE,{"disambiguationData":[OSD([subQ0,subQ5])]})});}
            var Q19;
            {var subQ0=sQuery(id+"F41.wireOp",EDGE,"E37");var subQ1=sQuery(id+"F22.wireOp",EDGE,"E28.4.3");var subQ2=sQuery(id+"F22.wireOp",EDGE,"E28.4.2");var subQ3=sQuery(id+"F3.wireOp",EDGE,"E20.12.3");var subQ4=sQuery(id+"F3.wireOp",EDGE,"E20.12.1");var subQ5=sQuery(id+"F41.wireOp",EDGE,"E38");Q19=makeQuery(id+"F42.boolean.opBoolean","COPY",EDGE,{"disambiguationData":[TD([makeQuery(id+"F27.opLoft","SWEPT_FACE",FACE,{"disambiguationData":[OSD([sQuery(id+"F3.wireOp",EDGE,"E20.12.0"),subQ4,subQ3,sQuery(id+"F22.wireOp",EDGE,"E28.4.1"),subQ2,subQ1])]})])],"derivedFrom":makeQuery(id+"F42.opRevolve","SWEPT_EDGE",EDGE,{"disambiguationData":[OSD([subQ0,subQ5])]})});}
            var Q20;
            {var subQ0=sQuery(id+"F41.wireOp",EDGE,"E37");var subQ1=sQuery(id+"F22.wireOp",EDGE,"E28.3.3");var subQ2=sQuery(id+"F22.wireOp",EDGE,"E28.3.2");var subQ3=sQuery(id+"F3.wireOp",EDGE,"E20.11.3");var subQ4=sQuery(id+"F3.wireOp",EDGE,"E20.11.1");var subQ5=sQuery(id+"F41.wireOp",EDGE,"E38");Q20=makeQuery(id+"F42.boolean.opBoolean","COPY",EDGE,{"disambiguationData":[TD([makeQuery(id+"F26.opLoft","SWEPT_FACE",FACE,{"disambiguationData":[OSD([sQuery(id+"F3.wireOp",EDGE,"E20.11.0"),subQ4,subQ3,sQuery(id+"F22.wireOp",EDGE,"E28.3.1"),subQ2,subQ1])]})])],"derivedFrom":makeQuery(id+"F42.opRevolve","SWEPT_EDGE",EDGE,{"disambiguationData":[OSD([subQ0,subQ5])]})});}
            var Q21;
            {var subQ0=sQuery(id+"F41.wireOp",EDGE,"E37");var subQ1=sQuery(id+"F22.wireOp",EDGE,"E28.2.3");var subQ2=sQuery(id+"F22.wireOp",EDGE,"E28.2.2");var subQ3=sQuery(id+"F3.wireOp",EDGE,"E20.10.3");var subQ4=sQuery(id+"F3.wireOp",EDGE,"E20.10.1");var subQ5=sQuery(id+"F41.wireOp",EDGE,"E38");Q21=makeQuery(id+"F42.boolean.opBoolean","COPY",EDGE,{"disambiguationData":[TD([makeQuery(id+"F25.opLoft","SWEPT_FACE",FACE,{"disambiguationData":[OSD([sQuery(id+"F3.wireOp",EDGE,"E20.10.0"),subQ4,subQ3,sQuery(id+"F22.wireOp",EDGE,"E28.2.1"),subQ2,subQ1])]})])],"derivedFrom":makeQuery(id+"F42.opRevolve","SWEPT_EDGE",EDGE,{"disambiguationData":[OSD([subQ0,subQ5])]})});}
            var Q22;
            {var subQ0=sQuery(id+"F41.wireOp",EDGE,"E37");var subQ1=sQuery(id+"F22.wireOp",EDGE,"E28.1.3");var subQ2=sQuery(id+"F22.wireOp",EDGE,"E28.1.2");var subQ3=sQuery(id+"F3.wireOp",EDGE,"E20.9.3");var subQ4=sQuery(id+"F3.wireOp",EDGE,"E20.9.1");var subQ5=sQuery(id+"F41.wireOp",EDGE,"E38");Q22=makeQuery(id+"F42.boolean.opBoolean","COPY",EDGE,{"disambiguationData":[TD([makeQuery(id+"F24.opLoft","SWEPT_FACE",FACE,{"disambiguationData":[OSD([sQuery(id+"F3.wireOp",EDGE,"E20.9.0"),subQ4,subQ3,sQuery(id+"F22.wireOp",EDGE,"E28.1.1"),subQ2,subQ1])]})])],"derivedFrom":makeQuery(id+"F42.opRevolve","SWEPT_EDGE",EDGE,{"disambiguationData":[OSD([subQ0,subQ5])]})});}
            var Q23;
            {var subQ0=sQuery(id+"F22.wireOp",EDGE,"E27.top");var subQ1=sQuery(id+"F22.wireOp",EDGE,"E27.bottom");var subQ2=sQuery(id+"F3.wireOp",EDGE,"E20.8.3");var subQ3=sQuery(id+"F3.wireOp",EDGE,"E20.8.1");var subQ4=sQuery(id+"F41.wireOp",EDGE,"E37");var subQ5=sQuery(id+"F41.wireOp",EDGE,"E38");Q23=makeQuery(id+"F42.boolean.opBoolean","COPY",EDGE,{"disambiguationData":[TD([makeQuery(id+"F23.opLoft","SWEPT_FACE",FACE,{"disambiguationData":[OSD([sQuery(id+"F3.wireOp",EDGE,"E20.8.0"),subQ3,subQ2,subQ1,subQ0,sQuery(id+"F22.wireOp",EDGE,"E27.right")])]})])],"derivedFrom":makeQuery(id+"F42.opRevolve","SWEPT_EDGE",EDGE,{"disambiguationData":[OSD([subQ4,subQ5])]})});}
            var Q24;
            {var subQ0=sQuery(id+"F41.wireOp",EDGE,"E37");var subQ1=sQuery(id+"F22.wireOp",EDGE,"E28.15.3");var subQ2=sQuery(id+"F22.wireOp",EDGE,"E28.15.2");var subQ3=sQuery(id+"F3.wireOp",EDGE,"E20.7.3");var subQ4=sQuery(id+"F3.wireOp",EDGE,"E20.7.1");var subQ5=sQuery(id+"F41.wireOp",EDGE,"E38");Q24=makeQuery(id+"F42.boolean.opBoolean","COPY",EDGE,{"disambiguationData":[TD([makeQuery(id+"F38.opLoft","SWEPT_FACE",FACE,{"disambiguationData":[OSD([sQuery(id+"F3.wireOp",EDGE,"E20.7.0"),subQ4,subQ3,sQuery(id+"F22.wireOp",EDGE,"E28.15.1"),subQ2,subQ1])]})])],"derivedFrom":makeQuery(id+"F42.opRevolve","SWEPT_EDGE",EDGE,{"disambiguationData":[OSD([subQ0,subQ5])]})});}
            var Q25;
            {var subQ0=sQuery(id+"F41.wireOp",EDGE,"E37");var subQ1=sQuery(id+"F22.wireOp",EDGE,"E28.14.3");var subQ2=sQuery(id+"F22.wireOp",EDGE,"E28.14.2");var subQ3=sQuery(id+"F3.wireOp",EDGE,"E20.6.3");var subQ4=sQuery(id+"F3.wireOp",EDGE,"E20.6.1");var subQ5=sQuery(id+"F41.wireOp",EDGE,"E38");Q25=makeQuery(id+"F42.boolean.opBoolean","COPY",EDGE,{"disambiguationData":[TD([makeQuery(id+"F37.opLoft","SWEPT_FACE",FACE,{"disambiguationData":[OSD([sQuery(id+"F3.wireOp",EDGE,"E20.6.0"),subQ4,subQ3,sQuery(id+"F22.wireOp",EDGE,"E28.14.1"),subQ2,subQ1])]})])],"derivedFrom":makeQuery(id+"F42.opRevolve","SWEPT_EDGE",EDGE,{"disambiguationData":[OSD([subQ0,subQ5])]})});}
            var Q26;
            {var subQ0=sQuery(id+"F41.wireOp",EDGE,"E37");var subQ1=sQuery(id+"F22.wireOp",EDGE,"E28.13.3");var subQ2=sQuery(id+"F22.wireOp",EDGE,"E28.13.2");var subQ3=sQuery(id+"F3.wireOp",EDGE,"E20.5.3");var subQ4=sQuery(id+"F3.wireOp",EDGE,"E20.5.1");var subQ5=sQuery(id+"F41.wireOp",EDGE,"E38");Q26=makeQuery(id+"F42.boolean.opBoolean","COPY",EDGE,{"disambiguationData":[TD([makeQuery(id+"F36.opLoft","SWEPT_FACE",FACE,{"disambiguationData":[OSD([sQuery(id+"F3.wireOp",EDGE,"E20.5.0"),subQ4,subQ3,sQuery(id+"F22.wireOp",EDGE,"E28.13.1"),subQ2,subQ1])]})])],"derivedFrom":makeQuery(id+"F42.opRevolve","SWEPT_EDGE",EDGE,{"disambiguationData":[OSD([subQ0,subQ5])]})});}
            var Q27;
            {var subQ0=sQuery(id+"F41.wireOp",EDGE,"E37");var subQ1=sQuery(id+"F22.wireOp",EDGE,"E28.12.3");var subQ2=sQuery(id+"F22.wireOp",EDGE,"E28.12.2");var subQ3=sQuery(id+"F3.wireOp",EDGE,"E20.4.3");var subQ4=sQuery(id+"F3.wireOp",EDGE,"E20.4.1");var subQ5=sQuery(id+"F41.wireOp",EDGE,"E38");Q27=makeQuery(id+"F42.boolean.opBoolean","COPY",EDGE,{"disambiguationData":[TD([makeQuery(id+"F35.opLoft","SWEPT_FACE",FACE,{"disambiguationData":[OSD([sQuery(id+"F3.wireOp",EDGE,"E20.4.0"),subQ4,subQ3,sQuery(id+"F22.wireOp",EDGE,"E28.12.1"),subQ2,subQ1])]})])],"derivedFrom":makeQuery(id+"F42.opRevolve","SWEPT_EDGE",EDGE,{"disambiguationData":[OSD([subQ0,subQ5])]})});}
            var Q28;
            {var subQ0=sQuery(id+"F41.wireOp",EDGE,"E37");var subQ1=sQuery(id+"F22.wireOp",EDGE,"E28.11.3");var subQ2=sQuery(id+"F22.wireOp",EDGE,"E28.11.2");var subQ3=sQuery(id+"F3.wireOp",EDGE,"E20.3.3");var subQ4=sQuery(id+"F3.wireOp",EDGE,"E20.3.1");var subQ5=sQuery(id+"F41.wireOp",EDGE,"E38");Q28=makeQuery(id+"F42.boolean.opBoolean","COPY",EDGE,{"disambiguationData":[TD([makeQuery(id+"F34.opLoft","SWEPT_FACE",FACE,{"disambiguationData":[OSD([sQuery(id+"F3.wireOp",EDGE,"E20.3.0"),subQ4,subQ3,sQuery(id+"F22.wireOp",EDGE,"E28.11.1"),subQ2,subQ1])]})])],"derivedFrom":makeQuery(id+"F42.opRevolve","SWEPT_EDGE",EDGE,{"disambiguationData":[OSD([subQ0,subQ5])]})});}
            var Q29;
            {var subQ0=sQuery(id+"F41.wireOp",EDGE,"E37");var subQ1=sQuery(id+"F22.wireOp",EDGE,"E28.10.3");var subQ2=sQuery(id+"F22.wireOp",EDGE,"E28.10.2");var subQ3=sQuery(id+"F3.wireOp",EDGE,"E20.2.3");var subQ4=sQuery(id+"F3.wireOp",EDGE,"E20.2.1");var subQ5=sQuery(id+"F41.wireOp",EDGE,"E38");Q29=makeQuery(id+"F42.boolean.opBoolean","COPY",EDGE,{"disambiguationData":[TD([makeQuery(id+"F33.opLoft","SWEPT_FACE",FACE,{"disambiguationData":[OSD([sQuery(id+"F3.wireOp",EDGE,"E20.2.0"),subQ4,subQ3,sQuery(id+"F22.wireOp",EDGE,"E28.10.1"),subQ2,subQ1])]})])],"derivedFrom":makeQuery(id+"F42.opRevolve","SWEPT_EDGE",EDGE,{"disambiguationData":[OSD([subQ0,subQ5])]})});}
            var Q30;
            {var subQ0=sQuery(id+"F22.wireOp",EDGE,"E28.9.3");var subQ1=sQuery(id+"F22.wireOp",EDGE,"E28.9.2");var subQ2=sQuery(id+"F3.wireOp",EDGE,"E20.1.3");var subQ3=sQuery(id+"F3.wireOp",EDGE,"E20.1.1");var subQ4=sQuery(id+"F41.wireOp",EDGE,"E37");var subQ5=sQuery(id+"F41.wireOp",EDGE,"E38");Q30=makeQuery(id+"F42.boolean.opBoolean","COPY",EDGE,{"disambiguationData":[TD([makeQuery(id+"F32.opLoft","SWEPT_FACE",FACE,{"disambiguationData":[OSD([sQuery(id+"F3.wireOp",EDGE,"E20.1.0"),subQ3,subQ2,sQuery(id+"F22.wireOp",EDGE,"E28.9.1"),subQ1,subQ0])]})])],"derivedFrom":makeQuery(id+"F42.opRevolve","SWEPT_EDGE",EDGE,{"disambiguationData":[OSD([subQ4,subQ5])]})});}
            var Q31;
            {var subQ0=sQuery(id+"F22.wireOp",EDGE,"E28.8.3");var subQ1=sQuery(id+"F22.wireOp",EDGE,"E28.8.2");var subQ2=sQuery(id+"F3.wireOp",EDGE,"E18.top");var subQ3=sQuery(id+"F3.wireOp",EDGE,"E18.bottom");var subQ4=sQuery(id+"F41.wireOp",EDGE,"E37");var subQ5=sQuery(id+"F41.wireOp",EDGE,"E38");Q31=makeQuery(id+"F42.boolean.opBoolean","COPY",EDGE,{"disambiguationData":[TD([makeQuery(id+"F31.opLoft","SWEPT_FACE",FACE,{"disambiguationData":[OSD([subQ3,subQ2,sQuery(id+"F3.wireOp",EDGE,"E18.left"),sQuery(id+"F22.wireOp",EDGE,"E28.8.1"),subQ1,subQ0])]})])],"derivedFrom":makeQuery(id+"F42.opRevolve","SWEPT_EDGE",EDGE,{"disambiguationData":[OSD([subQ4,subQ5])]})});}
            fillet(context, id + "F47", {"entities" : qUnion([Q0, Q1, Q2, Q3, Q4, Q5, Q6, Q7, Q8, Q9, Q10, Q11, Q12, Q13, Q14, Q15, Q16, Q17, Q18, Q19, Q20, Q21, Q22, Q23, Q24, Q25, Q26, Q27, Q28, Q29, Q30, Q31]), "radius" : 2.5 * mm, "tangentPropagation" : true, "allowEdgeOverflow" : false});
        }
        {
            var Q0;
            {var subQ0=makeQuery(id+"F1.opRevolve","SWEPT_FACE",FACE,{"disambiguationData":[OSD([sQuery(id+"F0.wireOp",EDGE,"E1")])]});var subQ1=sQuery(id+"F3.wireOp",EDGE,"E20.9.3");var subQ2=sQuery(id+"F3.wireOp",EDGE,"E20.9.2");var subQ3=sQuery(id+"F3.wireOp",EDGE,"E20.9.1");var subQ4=makeQuery(id+"F12.opLoft","SWEPT_FACE",FACE,{"disambiguationData":[OSD([subQ3,subQ2,subQ1,sQuery(id+"F4.wireOp",EDGE,"E26.9.1"),sQuery(id+"F4.wireOp",EDGE,"E26.9.2"),sQuery(id+"F4.wireOp",EDGE,"E26.9.3")])]});var subQ9=makeQuery(id+"F40.opExtrude","CAP_FACE",FACE,{"disambiguationData":[OSD([sQuery(id+"F39.wireOp",EDGE,"E29"),sQuery(id+"F39.wireOp",EDGE,"E30")])],"isStart":false});Q0=makeQuery(id+"F44.opFillet","BLEND_EDGE",EDGE,{"blendedFrom":[makeQuery(id+"F40.boolean.opBoolean","INTERSECT",EDGE,{"derivedFrom":[subQ4,subQ9]}),makeQuery(id+"F40.boolean.opBoolean","SPLIT",FACE,{"disambiguationData":[TD([subQ0])],"derivedFrom":makeQuery(id+"F24.boolean.opBoolean","SPLIT",FACE,{"disambiguationData":[TD([subQ4])],"derivedFrom":makeQuery(id+"F1.opRevolve","SWEPT_FACE",FACE,{"disambiguationData":[OSD([sQuery(id+"F0.wireOp",EDGE,"E4")])]})})})],"blendedInto":[makeQuery(id+"F40.boolean.opBoolean","SPLIT",FACE,{"disambiguationData":[TD([subQ0])],"derivedFrom":makeQuery(id+"F24.boolean.opBoolean","SPLIT",FACE,{"disambiguationData":[TD([subQ4])],"derivedFrom":makeQuery(id+"F1.opRevolve","SWEPT_FACE",FACE,{"disambiguationData":[OSD([sQuery(id+"F0.wireOp",EDGE,"E4")])]})})})]});}
            var Q1;
            {var subQ0=makeQuery(id+"F1.opRevolve","SWEPT_FACE",FACE,{"disambiguationData":[OSD([sQuery(id+"F0.wireOp",EDGE,"E1")])]});var subQ1=sQuery(id+"F4.wireOp",EDGE,"E26.10.3");var subQ2=sQuery(id+"F4.wireOp",EDGE,"E26.10.2");var subQ3=sQuery(id+"F3.wireOp",EDGE,"E20.10.3");var subQ4=sQuery(id+"F3.wireOp",EDGE,"E20.10.2");var subQ5=sQuery(id+"F3.wireOp",EDGE,"E20.10.1");var subQ6=makeQuery(id+"F11.opLoft","SWEPT_FACE",FACE,{"disambiguationData":[OSD([subQ5,subQ4,subQ3,sQuery(id+"F4.wireOp",EDGE,"E26.10.1"),subQ2,subQ1])]});var subQ11=makeQuery(id+"F40.opExtrude","CAP_FACE",FACE,{"disambiguationData":[OSD([sQuery(id+"F39.wireOp",EDGE,"E29"),sQuery(id+"F39.wireOp",EDGE,"E30")])],"isStart":false});var subQ89=sQuery(id+"F3.wireOp",EDGE,"E18.bottom");Q1=makeQuery(id+"F44.opFillet","BLEND_EDGE",EDGE,{"blendedFrom":[makeQuery(id+"F40.boolean.opBoolean","INTERSECT",EDGE,{"derivedFrom":[subQ6,subQ11]}),makeQuery(id+"F40.boolean.opBoolean","SPLIT",FACE,{"disambiguationData":[TD([subQ0])],"derivedFrom":makeQuery(id+"F25.boolean.opBoolean","SPLIT",FACE,{"disambiguationData":[TD([subQ6])],"derivedFrom":makeQuery(id+"F24.boolean.opBoolean","SPLIT",FACE,{"disambiguationData":[TD([makeQuery(id+"F5.opLoft","CAP_FACE",FACE,{"disambiguationData":[OSD([makeQuery(id+"F3.imprint","IMPRINT",FACE,{"disambiguationData":[TD([[makeQuery(id+"F3.imprint","IMPRINT",EDGE,{"derivedFrom":subQ89}),1.0]])]})])],"isStart":true})])],"derivedFrom":makeQuery(id+"F1.opRevolve","SWEPT_FACE",FACE,{"disambiguationData":[OSD([sQuery(id+"F0.wireOp",EDGE,"E4")])]})})})})],"blendedInto":[makeQuery(id+"F40.boolean.opBoolean","SPLIT",FACE,{"disambiguationData":[TD([subQ0])],"derivedFrom":makeQuery(id+"F25.boolean.opBoolean","SPLIT",FACE,{"disambiguationData":[TD([subQ6])],"derivedFrom":makeQuery(id+"F24.boolean.opBoolean","SPLIT",FACE,{"disambiguationData":[TD([makeQuery(id+"F5.opLoft","CAP_FACE",FACE,{"disambiguationData":[OSD([makeQuery(id+"F3.imprint","IMPRINT",FACE,{"disambiguationData":[TD([[makeQuery(id+"F3.imprint","IMPRINT",EDGE,{"derivedFrom":subQ89}),1.0]])]})])],"isStart":true})])],"derivedFrom":makeQuery(id+"F1.opRevolve","SWEPT_FACE",FACE,{"disambiguationData":[OSD([sQuery(id+"F0.wireOp",EDGE,"E4")])]})})})})]});}
            var Q2;
            {var subQ0=makeQuery(id+"F1.opRevolve","SWEPT_FACE",FACE,{"disambiguationData":[OSD([sQuery(id+"F0.wireOp",EDGE,"E1")])]});var subQ1=sQuery(id+"F4.wireOp",EDGE,"E26.11.3");var subQ2=sQuery(id+"F4.wireOp",EDGE,"E26.11.2");var subQ3=sQuery(id+"F3.wireOp",EDGE,"E20.11.3");var subQ4=sQuery(id+"F3.wireOp",EDGE,"E20.11.2");var subQ5=sQuery(id+"F3.wireOp",EDGE,"E20.11.1");var subQ6=makeQuery(id+"F10.opLoft","SWEPT_FACE",FACE,{"disambiguationData":[OSD([subQ5,subQ4,subQ3,sQuery(id+"F4.wireOp",EDGE,"E26.11.1"),subQ2,subQ1])]});var subQ13=makeQuery(id+"F40.opExtrude","CAP_FACE",FACE,{"disambiguationData":[OSD([sQuery(id+"F39.wireOp",EDGE,"E29"),sQuery(id+"F39.wireOp",EDGE,"E30")])],"isStart":false});var subQ79=sQuery(id+"F3.wireOp",EDGE,"E18.bottom");var subQ82=makeQuery(id+"F5.opLoft","CAP_FACE",FACE,{"disambiguationData":[OSD([makeQuery(id+"F3.imprint","IMPRINT",FACE,{"disambiguationData":[TD([[makeQuery(id+"F3.imprint","IMPRINT",EDGE,{"derivedFrom":subQ79}),1.0]])]})])],"isStart":true});Q2=makeQuery(id+"F44.opFillet","BLEND_EDGE",EDGE,{"blendedFrom":[makeQuery(id+"F40.boolean.opBoolean","INTERSECT",EDGE,{"derivedFrom":[subQ6,subQ13]}),makeQuery(id+"F40.boolean.opBoolean","SPLIT",FACE,{"disambiguationData":[TD([subQ0])],"derivedFrom":makeQuery(id+"F26.boolean.opBoolean","SPLIT",FACE,{"disambiguationData":[TD([subQ6])],"derivedFrom":makeQuery(id+"F25.boolean.opBoolean","SPLIT",FACE,{"disambiguationData":[TD([subQ82])],"derivedFrom":makeQuery(id+"F24.boolean.opBoolean","SPLIT",FACE,{"disambiguationData":[TD([subQ82])],"derivedFrom":makeQuery(id+"F1.opRevolve","SWEPT_FACE",FACE,{"disambiguationData":[OSD([sQuery(id+"F0.wireOp",EDGE,"E4")])]})})})})})],"blendedInto":[makeQuery(id+"F40.boolean.opBoolean","SPLIT",FACE,{"disambiguationData":[TD([subQ0])],"derivedFrom":makeQuery(id+"F26.boolean.opBoolean","SPLIT",FACE,{"disambiguationData":[TD([subQ6])],"derivedFrom":makeQuery(id+"F25.boolean.opBoolean","SPLIT",FACE,{"disambiguationData":[TD([subQ82])],"derivedFrom":makeQuery(id+"F24.boolean.opBoolean","SPLIT",FACE,{"disambiguationData":[TD([subQ82])],"derivedFrom":makeQuery(id+"F1.opRevolve","SWEPT_FACE",FACE,{"disambiguationData":[OSD([sQuery(id+"F0.wireOp",EDGE,"E4")])]})})})})})]});}
            var Q3;
            {var subQ0=makeQuery(id+"F1.opRevolve","SWEPT_FACE",FACE,{"disambiguationData":[OSD([sQuery(id+"F0.wireOp",EDGE,"E1")])]});var subQ1=sQuery(id+"F4.wireOp",EDGE,"E26.12.3");var subQ2=sQuery(id+"F4.wireOp",EDGE,"E26.12.2");var subQ3=sQuery(id+"F3.wireOp",EDGE,"E20.12.3");var subQ4=sQuery(id+"F3.wireOp",EDGE,"E20.12.2");var subQ5=sQuery(id+"F3.wireOp",EDGE,"E20.12.1");var subQ6=makeQuery(id+"F9.opLoft","SWEPT_FACE",FACE,{"disambiguationData":[OSD([subQ5,subQ4,subQ3,sQuery(id+"F4.wireOp",EDGE,"E26.12.1"),subQ2,subQ1])]});var subQ7=makeQuery(id+"F40.opExtrude","CAP_FACE",FACE,{"disambiguationData":[OSD([sQuery(id+"F39.wireOp",EDGE,"E29"),sQuery(id+"F39.wireOp",EDGE,"E30")])],"isStart":false});var subQ74=sQuery(id+"F3.wireOp",EDGE,"E18.bottom");var subQ77=makeQuery(id+"F5.opLoft","CAP_FACE",FACE,{"disambiguationData":[OSD([makeQuery(id+"F3.imprint","IMPRINT",FACE,{"disambiguationData":[TD([[makeQuery(id+"F3.imprint","IMPRINT",EDGE,{"derivedFrom":subQ74}),1.0]])]})])],"isStart":true});Q3=makeQuery(id+"F44.opFillet","BLEND_EDGE",EDGE,{"blendedFrom":[makeQuery(id+"F40.boolean.opBoolean","INTERSECT",EDGE,{"derivedFrom":[subQ6,subQ7]}),makeQuery(id+"F40.boolean.opBoolean","SPLIT",FACE,{"disambiguationData":[TD([subQ0])],"derivedFrom":makeQuery(id+"F27.boolean.opBoolean","SPLIT",FACE,{"disambiguationData":[TD([subQ6])],"derivedFrom":makeQuery(id+"F26.boolean.opBoolean","SPLIT",FACE,{"disambiguationData":[TD([subQ77])],"derivedFrom":makeQuery(id+"F25.boolean.opBoolean","SPLIT",FACE,{"disambiguationData":[TD([subQ77])],"derivedFrom":makeQuery(id+"F24.boolean.opBoolean","SPLIT",FACE,{"disambiguationData":[TD([subQ77])],"derivedFrom":makeQuery(id+"F1.opRevolve","SWEPT_FACE",FACE,{"disambiguationData":[OSD([sQuery(id+"F0.wireOp",EDGE,"E4")])]})})})})})})],"blendedInto":[makeQuery(id+"F40.boolean.opBoolean","SPLIT",FACE,{"disambiguationData":[TD([subQ0])],"derivedFrom":makeQuery(id+"F27.boolean.opBoolean","SPLIT",FACE,{"disambiguationData":[TD([subQ6])],"derivedFrom":makeQuery(id+"F26.boolean.opBoolean","SPLIT",FACE,{"disambiguationData":[TD([subQ77])],"derivedFrom":makeQuery(id+"F25.boolean.opBoolean","SPLIT",FACE,{"disambiguationData":[TD([subQ77])],"derivedFrom":makeQuery(id+"F24.boolean.opBoolean","SPLIT",FACE,{"disambiguationData":[TD([subQ77])],"derivedFrom":makeQuery(id+"F1.opRevolve","SWEPT_FACE",FACE,{"disambiguationData":[OSD([sQuery(id+"F0.wireOp",EDGE,"E4")])]})})})})})})]});}
            var Q4;
            {var subQ0=makeQuery(id+"F1.opRevolve","SWEPT_FACE",FACE,{"disambiguationData":[OSD([sQuery(id+"F0.wireOp",EDGE,"E1")])]});var subQ1=sQuery(id+"F4.wireOp",EDGE,"E26.13.3");var subQ2=sQuery(id+"F4.wireOp",EDGE,"E26.13.2");var subQ3=sQuery(id+"F3.wireOp",EDGE,"E20.13.3");var subQ4=sQuery(id+"F3.wireOp",EDGE,"E20.13.2");var subQ5=sQuery(id+"F3.wireOp",EDGE,"E20.13.1");var subQ6=makeQuery(id+"F8.opLoft","SWEPT_FACE",FACE,{"disambiguationData":[OSD([subQ5,subQ4,subQ3,sQuery(id+"F4.wireOp",EDGE,"E26.13.1"),subQ2,subQ1])]});var subQ13=makeQuery(id+"F40.opExtrude","CAP_FACE",FACE,{"disambiguationData":[OSD([sQuery(id+"F39.wireOp",EDGE,"E29"),sQuery(id+"F39.wireOp",EDGE,"E30")])],"isStart":false});var subQ56=sQuery(id+"F3.wireOp",EDGE,"E18.bottom");var subQ59=makeQuery(id+"F5.opLoft","CAP_FACE",FACE,{"disambiguationData":[OSD([makeQuery(id+"F3.imprint","IMPRINT",FACE,{"disambiguationData":[TD([[makeQuery(id+"F3.imprint","IMPRINT",EDGE,{"derivedFrom":subQ56}),1.0]])]})])],"isStart":true});Q4=makeQuery(id+"F44.opFillet","BLEND_EDGE",EDGE,{"blendedFrom":[makeQuery(id+"F40.boolean.opBoolean","INTERSECT",EDGE,{"derivedFrom":[subQ6,subQ13]}),makeQuery(id+"F40.boolean.opBoolean","SPLIT",FACE,{"disambiguationData":[TD([subQ0])],"derivedFrom":makeQuery(id+"F28.boolean.opBoolean","SPLIT",FACE,{"disambiguationData":[TD([subQ6])],"derivedFrom":makeQuery(id+"F27.boolean.opBoolean","SPLIT",FACE,{"disambiguationData":[TD([subQ59])],"derivedFrom":makeQuery(id+"F26.boolean.opBoolean","SPLIT",FACE,{"disambiguationData":[TD([subQ59])],"derivedFrom":makeQuery(id+"F25.boolean.opBoolean","SPLIT",FACE,{"disambiguationData":[TD([subQ59])],"derivedFrom":makeQuery(id+"F24.boolean.opBoolean","SPLIT",FACE,{"disambiguationData":[TD([subQ59])],"derivedFrom":makeQuery(id+"F1.opRevolve","SWEPT_FACE",FACE,{"disambiguationData":[OSD([sQuery(id+"F0.wireOp",EDGE,"E4")])]})})})})})})})],"blendedInto":[makeQuery(id+"F40.boolean.opBoolean","SPLIT",FACE,{"disambiguationData":[TD([subQ0])],"derivedFrom":makeQuery(id+"F28.boolean.opBoolean","SPLIT",FACE,{"disambiguationData":[TD([subQ6])],"derivedFrom":makeQuery(id+"F27.boolean.opBoolean","SPLIT",FACE,{"disambiguationData":[TD([subQ59])],"derivedFrom":makeQuery(id+"F26.boolean.opBoolean","SPLIT",FACE,{"disambiguationData":[TD([subQ59])],"derivedFrom":makeQuery(id+"F25.boolean.opBoolean","SPLIT",FACE,{"disambiguationData":[TD([subQ59])],"derivedFrom":makeQuery(id+"F24.boolean.opBoolean","SPLIT",FACE,{"disambiguationData":[TD([subQ59])],"derivedFrom":makeQuery(id+"F1.opRevolve","SWEPT_FACE",FACE,{"disambiguationData":[OSD([sQuery(id+"F0.wireOp",EDGE,"E4")])]})})})})})})})]});}
            var Q5;
            {var subQ0=makeQuery(id+"F1.opRevolve","SWEPT_FACE",FACE,{"disambiguationData":[OSD([sQuery(id+"F0.wireOp",EDGE,"E1")])]});var subQ1=sQuery(id+"F4.wireOp",EDGE,"E26.14.3");var subQ2=sQuery(id+"F4.wireOp",EDGE,"E26.14.2");var subQ3=sQuery(id+"F3.wireOp",EDGE,"E20.14.3");var subQ4=sQuery(id+"F3.wireOp",EDGE,"E20.14.2");var subQ5=sQuery(id+"F3.wireOp",EDGE,"E20.14.1");var subQ6=makeQuery(id+"F7.opLoft","SWEPT_FACE",FACE,{"disambiguationData":[OSD([subQ5,subQ4,subQ3,sQuery(id+"F4.wireOp",EDGE,"E26.14.1"),subQ2,subQ1])]});var subQ13=makeQuery(id+"F40.opExtrude","CAP_FACE",FACE,{"disambiguationData":[OSD([sQuery(id+"F39.wireOp",EDGE,"E29"),sQuery(id+"F39.wireOp",EDGE,"E30")])],"isStart":false});var subQ48=sQuery(id+"F3.wireOp",EDGE,"E18.bottom");var subQ51=makeQuery(id+"F5.opLoft","CAP_FACE",FACE,{"disambiguationData":[OSD([makeQuery(id+"F3.imprint","IMPRINT",FACE,{"disambiguationData":[TD([[makeQuery(id+"F3.imprint","IMPRINT",EDGE,{"derivedFrom":subQ48}),1.0]])]})])],"isStart":true});Q5=makeQuery(id+"F44.opFillet","BLEND_EDGE",EDGE,{"blendedFrom":[makeQuery(id+"F40.boolean.opBoolean","INTERSECT",EDGE,{"derivedFrom":[subQ6,subQ13]}),makeQuery(id+"F40.boolean.opBoolean","SPLIT",FACE,{"disambiguationData":[TD([subQ0])],"derivedFrom":makeQuery(id+"F29.boolean.opBoolean","SPLIT",FACE,{"disambiguationData":[TD([subQ6])],"derivedFrom":makeQuery(id+"F28.boolean.opBoolean","SPLIT",FACE,{"disambiguationData":[TD([subQ51])],"derivedFrom":makeQuery(id+"F27.boolean.opBoolean","SPLIT",FACE,{"disambiguationData":[TD([subQ51])],"derivedFrom":makeQuery(id+"F26.boolean.opBoolean","SPLIT",FACE,{"disambiguationData":[TD([subQ51])],"derivedFrom":makeQuery(id+"F25.boolean.opBoolean","SPLIT",FACE,{"disambiguationData":[TD([subQ51])],"derivedFrom":makeQuery(id+"F24.boolean.opBoolean","SPLIT",FACE,{"disambiguationData":[TD([subQ51])],"derivedFrom":makeQuery(id+"F1.opRevolve","SWEPT_FACE",FACE,{"disambiguationData":[OSD([sQuery(id+"F0.wireOp",EDGE,"E4")])]})})})})})})})})],"blendedInto":[makeQuery(id+"F40.boolean.opBoolean","SPLIT",FACE,{"disambiguationData":[TD([subQ0])],"derivedFrom":makeQuery(id+"F29.boolean.opBoolean","SPLIT",FACE,{"disambiguationData":[TD([subQ6])],"derivedFrom":makeQuery(id+"F28.boolean.opBoolean","SPLIT",FACE,{"disambiguationData":[TD([subQ51])],"derivedFrom":makeQuery(id+"F27.boolean.opBoolean","SPLIT",FACE,{"disambiguationData":[TD([subQ51])],"derivedFrom":makeQuery(id+"F26.boolean.opBoolean","SPLIT",FACE,{"disambiguationData":[TD([subQ51])],"derivedFrom":makeQuery(id+"F25.boolean.opBoolean","SPLIT",FACE,{"disambiguationData":[TD([subQ51])],"derivedFrom":makeQuery(id+"F24.boolean.opBoolean","SPLIT",FACE,{"disambiguationData":[TD([subQ51])],"derivedFrom":makeQuery(id+"F1.opRevolve","SWEPT_FACE",FACE,{"disambiguationData":[OSD([sQuery(id+"F0.wireOp",EDGE,"E4")])]})})})})})})})})]});}
            var Q6;
            {var subQ0=makeQuery(id+"F1.opRevolve","SWEPT_FACE",FACE,{"disambiguationData":[OSD([sQuery(id+"F0.wireOp",EDGE,"E1")])]});var subQ7=sQuery(id+"F4.wireOp",EDGE,"E26.15.3");var subQ8=sQuery(id+"F4.wireOp",EDGE,"E26.15.2");var subQ9=sQuery(id+"F3.wireOp",EDGE,"E20.15.3");var subQ10=sQuery(id+"F3.wireOp",EDGE,"E20.15.2");var subQ11=sQuery(id+"F3.wireOp",EDGE,"E20.15.1");var subQ12=makeQuery(id+"F6.opLoft","SWEPT_FACE",FACE,{"disambiguationData":[OSD([subQ11,subQ10,subQ9,sQuery(id+"F4.wireOp",EDGE,"E26.15.1"),subQ8,subQ7])]});var subQ13=makeQuery(id+"F40.opExtrude","CAP_FACE",FACE,{"disambiguationData":[OSD([sQuery(id+"F39.wireOp",EDGE,"E29"),sQuery(id+"F39.wireOp",EDGE,"E30")])],"isStart":false});var subQ47=sQuery(id+"F3.wireOp",EDGE,"E18.bottom");var subQ50=makeQuery(id+"F5.opLoft","CAP_FACE",FACE,{"disambiguationData":[OSD([makeQuery(id+"F3.imprint","IMPRINT",FACE,{"disambiguationData":[TD([[makeQuery(id+"F3.imprint","IMPRINT",EDGE,{"derivedFrom":subQ47}),1.0]])]})])],"isStart":true});Q6=makeQuery(id+"F44.opFillet","BLEND_EDGE",EDGE,{"blendedFrom":[makeQuery(id+"F40.boolean.opBoolean","INTERSECT",EDGE,{"derivedFrom":[subQ12,subQ13]}),makeQuery(id+"F40.boolean.opBoolean","SPLIT",FACE,{"disambiguationData":[TD([subQ0])],"derivedFrom":makeQuery(id+"F30.boolean.opBoolean","SPLIT",FACE,{"disambiguationData":[TD([subQ12])],"derivedFrom":makeQuery(id+"F29.boolean.opBoolean","SPLIT",FACE,{"disambiguationData":[TD([subQ50])],"derivedFrom":makeQuery(id+"F28.boolean.opBoolean","SPLIT",FACE,{"disambiguationData":[TD([subQ50])],"derivedFrom":makeQuery(id+"F27.boolean.opBoolean","SPLIT",FACE,{"disambiguationData":[TD([subQ50])],"derivedFrom":makeQuery(id+"F26.boolean.opBoolean","SPLIT",FACE,{"disambiguationData":[TD([subQ50])],"derivedFrom":makeQuery(id+"F25.boolean.opBoolean","SPLIT",FACE,{"disambiguationData":[TD([subQ50])],"derivedFrom":makeQuery(id+"F24.boolean.opBoolean","SPLIT",FACE,{"disambiguationData":[TD([subQ50])],"derivedFrom":makeQuery(id+"F1.opRevolve","SWEPT_FACE",FACE,{"disambiguationData":[OSD([sQuery(id+"F0.wireOp",EDGE,"E4")])]})})})})})})})})})],"blendedInto":[makeQuery(id+"F40.boolean.opBoolean","SPLIT",FACE,{"disambiguationData":[TD([subQ0])],"derivedFrom":makeQuery(id+"F30.boolean.opBoolean","SPLIT",FACE,{"disambiguationData":[TD([subQ12])],"derivedFrom":makeQuery(id+"F29.boolean.opBoolean","SPLIT",FACE,{"disambiguationData":[TD([subQ50])],"derivedFrom":makeQuery(id+"F28.boolean.opBoolean","SPLIT",FACE,{"disambiguationData":[TD([subQ50])],"derivedFrom":makeQuery(id+"F27.boolean.opBoolean","SPLIT",FACE,{"disambiguationData":[TD([subQ50])],"derivedFrom":makeQuery(id+"F26.boolean.opBoolean","SPLIT",FACE,{"disambiguationData":[TD([subQ50])],"derivedFrom":makeQuery(id+"F25.boolean.opBoolean","SPLIT",FACE,{"disambiguationData":[TD([subQ50])],"derivedFrom":makeQuery(id+"F24.boolean.opBoolean","SPLIT",FACE,{"disambiguationData":[TD([subQ50])],"derivedFrom":makeQuery(id+"F1.opRevolve","SWEPT_FACE",FACE,{"disambiguationData":[OSD([sQuery(id+"F0.wireOp",EDGE,"E4")])]})})})})})})})})})]});}
            var Q7;
            {var subQ0=makeQuery(id+"F1.opRevolve","SWEPT_FACE",FACE,{"disambiguationData":[OSD([sQuery(id+"F0.wireOp",EDGE,"E1")])]});var subQ1=sQuery(id+"F4.wireOp",EDGE,"E23");var subQ2=sQuery(id+"F4.wireOp",EDGE,"E22");var subQ3=sQuery(id+"F3.wireOp",EDGE,"E18.right");var subQ4=sQuery(id+"F3.wireOp",EDGE,"E18.top");var subQ5=sQuery(id+"F3.wireOp",EDGE,"E18.bottom");var subQ6=makeQuery(id+"F5.opLoft","SWEPT_FACE",FACE,{"disambiguationData":[OSD([subQ5,subQ4,subQ3,subQ2,subQ1,sQuery(id+"F4.wireOp",EDGE,"E24")])]});var subQ13=makeQuery(id+"F40.opExtrude","CAP_FACE",FACE,{"disambiguationData":[OSD([sQuery(id+"F39.wireOp",EDGE,"E29"),sQuery(id+"F39.wireOp",EDGE,"E30")])],"isStart":false});var subQ58=makeQuery(id+"F5.opLoft","CAP_FACE",FACE,{"disambiguationData":[OSD([makeQuery(id+"F3.imprint","IMPRINT",FACE,{"disambiguationData":[TD([[makeQuery(id+"F3.imprint","IMPRINT",EDGE,{"derivedFrom":subQ5}),1.0]])]})])],"isStart":true});Q7=makeQuery(id+"F44.opFillet","BLEND_EDGE",EDGE,{"blendedFrom":[makeQuery(id+"F40.boolean.opBoolean","INTERSECT",EDGE,{"derivedFrom":[subQ6,subQ13]}),makeQuery(id+"F40.boolean.opBoolean","SPLIT",FACE,{"disambiguationData":[TD([subQ0])],"derivedFrom":makeQuery(id+"F31.boolean.opBoolean","SPLIT",FACE,{"disambiguationData":[TD([subQ6])],"derivedFrom":makeQuery(id+"F30.boolean.opBoolean","SPLIT",FACE,{"disambiguationData":[TD([subQ58])],"derivedFrom":makeQuery(id+"F29.boolean.opBoolean","SPLIT",FACE,{"disambiguationData":[TD([subQ58])],"derivedFrom":makeQuery(id+"F28.boolean.opBoolean","SPLIT",FACE,{"disambiguationData":[TD([subQ58])],"derivedFrom":makeQuery(id+"F27.boolean.opBoolean","SPLIT",FACE,{"disambiguationData":[TD([subQ58])],"derivedFrom":makeQuery(id+"F26.boolean.opBoolean","SPLIT",FACE,{"disambiguationData":[TD([subQ58])],"derivedFrom":makeQuery(id+"F25.boolean.opBoolean","SPLIT",FACE,{"disambiguationData":[TD([subQ58])],"derivedFrom":makeQuery(id+"F24.boolean.opBoolean","SPLIT",FACE,{"disambiguationData":[TD([subQ58])],"derivedFrom":makeQuery(id+"F1.opRevolve","SWEPT_FACE",FACE,{"disambiguationData":[OSD([sQuery(id+"F0.wireOp",EDGE,"E4")])]})})})})})})})})})})],"blendedInto":[makeQuery(id+"F40.boolean.opBoolean","SPLIT",FACE,{"disambiguationData":[TD([subQ0])],"derivedFrom":makeQuery(id+"F31.boolean.opBoolean","SPLIT",FACE,{"disambiguationData":[TD([subQ6])],"derivedFrom":makeQuery(id+"F30.boolean.opBoolean","SPLIT",FACE,{"disambiguationData":[TD([subQ58])],"derivedFrom":makeQuery(id+"F29.boolean.opBoolean","SPLIT",FACE,{"disambiguationData":[TD([subQ58])],"derivedFrom":makeQuery(id+"F28.boolean.opBoolean","SPLIT",FACE,{"disambiguationData":[TD([subQ58])],"derivedFrom":makeQuery(id+"F27.boolean.opBoolean","SPLIT",FACE,{"disambiguationData":[TD([subQ58])],"derivedFrom":makeQuery(id+"F26.boolean.opBoolean","SPLIT",FACE,{"disambiguationData":[TD([subQ58])],"derivedFrom":makeQuery(id+"F25.boolean.opBoolean","SPLIT",FACE,{"disambiguationData":[TD([subQ58])],"derivedFrom":makeQuery(id+"F24.boolean.opBoolean","SPLIT",FACE,{"disambiguationData":[TD([subQ58])],"derivedFrom":makeQuery(id+"F1.opRevolve","SWEPT_FACE",FACE,{"disambiguationData":[OSD([sQuery(id+"F0.wireOp",EDGE,"E4")])]})})})})})})})})})})]});}
            var Q8;
            {var subQ0=makeQuery(id+"F1.opRevolve","SWEPT_FACE",FACE,{"disambiguationData":[OSD([sQuery(id+"F0.wireOp",EDGE,"E1")])]});var subQ1=sQuery(id+"F4.wireOp",EDGE,"E23");var subQ2=sQuery(id+"F4.wireOp",EDGE,"E22");var subQ3=sQuery(id+"F3.wireOp",EDGE,"E18.left");var subQ4=sQuery(id+"F3.wireOp",EDGE,"E18.top");var subQ5=sQuery(id+"F3.wireOp",EDGE,"E18.bottom");var subQ6=makeQuery(id+"F5.opLoft","SWEPT_FACE",FACE,{"disambiguationData":[OSD([subQ5,subQ4,subQ3,sQuery(id+"F4.wireOp",EDGE,"E21"),subQ2,subQ1])]});var subQ7=sQuery(id+"F4.wireOp",EDGE,"E26.1.3");var subQ8=sQuery(id+"F4.wireOp",EDGE,"E26.1.2");var subQ9=sQuery(id+"F3.wireOp",EDGE,"E20.1.3");var subQ10=sQuery(id+"F3.wireOp",EDGE,"E20.1.2");var subQ11=sQuery(id+"F3.wireOp",EDGE,"E20.1.1");var subQ12=makeQuery(id+"F20.opLoft","SWEPT_FACE",FACE,{"disambiguationData":[OSD([subQ11,subQ10,subQ9,sQuery(id+"F4.wireOp",EDGE,"E26.1.1"),subQ8,subQ7])]});var subQ13=makeQuery(id+"F40.opExtrude","CAP_FACE",FACE,{"disambiguationData":[OSD([sQuery(id+"F39.wireOp",EDGE,"E29"),sQuery(id+"F39.wireOp",EDGE,"E30")])],"isStart":false});var subQ64=sQuery(id+"F3.wireOp",EDGE,"E20.7.0");var subQ72=makeQuery(id+"F14.opLoft","CAP_FACE",FACE,{"disambiguationData":[OSD([makeQuery(id+"F3.imprint","IMPRINT",FACE,{"disambiguationData":[TD([[makeQuery(id+"F3.imprint","IMPRINT",EDGE,{"derivedFrom":subQ64}),-1.0]])]})])],"isStart":true});var subQ80=makeQuery(id+"F5.opLoft","CAP_FACE",FACE,{"disambiguationData":[OSD([makeQuery(id+"F3.imprint","IMPRINT",FACE,{"disambiguationData":[TD([[makeQuery(id+"F3.imprint","IMPRINT",EDGE,{"derivedFrom":subQ5}),1.0]])]})])],"isStart":true});Q8=makeQuery(id+"F44.opFillet","BLEND_EDGE",EDGE,{"blendedFrom":[makeQuery(id+"F40.boolean.opBoolean","INTERSECT",EDGE,{"derivedFrom":[subQ12,subQ13]}),makeQuery(id+"F40.boolean.opBoolean","SPLIT",FACE,{"disambiguationData":[TD([subQ0])],"derivedFrom":makeQuery(id+"F32.boolean.opBoolean","SPLIT",FACE,{"disambiguationData":[TD([subQ6])],"derivedFrom":makeQuery(id+"F31.boolean.opBoolean","SPLIT",FACE,{"disambiguationData":[TD([subQ72])],"derivedFrom":makeQuery(id+"F30.boolean.opBoolean","SPLIT",FACE,{"disambiguationData":[TD([subQ80])],"derivedFrom":makeQuery(id+"F29.boolean.opBoolean","SPLIT",FACE,{"disambiguationData":[TD([subQ80])],"derivedFrom":makeQuery(id+"F28.boolean.opBoolean","SPLIT",FACE,{"disambiguationData":[TD([subQ80])],"derivedFrom":makeQuery(id+"F27.boolean.opBoolean","SPLIT",FACE,{"disambiguationData":[TD([subQ80])],"derivedFrom":makeQuery(id+"F26.boolean.opBoolean","SPLIT",FACE,{"disambiguationData":[TD([subQ80])],"derivedFrom":makeQuery(id+"F25.boolean.opBoolean","SPLIT",FACE,{"disambiguationData":[TD([subQ80])],"derivedFrom":makeQuery(id+"F24.boolean.opBoolean","SPLIT",FACE,{"disambiguationData":[TD([subQ80])],"derivedFrom":makeQuery(id+"F1.opRevolve","SWEPT_FACE",FACE,{"disambiguationData":[OSD([sQuery(id+"F0.wireOp",EDGE,"E4")])]})})})})})})})})})})})],"blendedInto":[makeQuery(id+"F40.boolean.opBoolean","SPLIT",FACE,{"disambiguationData":[TD([subQ0])],"derivedFrom":makeQuery(id+"F32.boolean.opBoolean","SPLIT",FACE,{"disambiguationData":[TD([subQ6])],"derivedFrom":makeQuery(id+"F31.boolean.opBoolean","SPLIT",FACE,{"disambiguationData":[TD([subQ72])],"derivedFrom":makeQuery(id+"F30.boolean.opBoolean","SPLIT",FACE,{"disambiguationData":[TD([subQ80])],"derivedFrom":makeQuery(id+"F29.boolean.opBoolean","SPLIT",FACE,{"disambiguationData":[TD([subQ80])],"derivedFrom":makeQuery(id+"F28.boolean.opBoolean","SPLIT",FACE,{"disambiguationData":[TD([subQ80])],"derivedFrom":makeQuery(id+"F27.boolean.opBoolean","SPLIT",FACE,{"disambiguationData":[TD([subQ80])],"derivedFrom":makeQuery(id+"F26.boolean.opBoolean","SPLIT",FACE,{"disambiguationData":[TD([subQ80])],"derivedFrom":makeQuery(id+"F25.boolean.opBoolean","SPLIT",FACE,{"disambiguationData":[TD([subQ80])],"derivedFrom":makeQuery(id+"F24.boolean.opBoolean","SPLIT",FACE,{"disambiguationData":[TD([subQ80])],"derivedFrom":makeQuery(id+"F1.opRevolve","SWEPT_FACE",FACE,{"disambiguationData":[OSD([sQuery(id+"F0.wireOp",EDGE,"E4")])]})})})})})})})})})})})]});}
            var Q9;
            {var subQ0=makeQuery(id+"F1.opRevolve","SWEPT_FACE",FACE,{"disambiguationData":[OSD([sQuery(id+"F0.wireOp",EDGE,"E1")])]});var subQ1=sQuery(id+"F4.wireOp",EDGE,"E26.2.3");var subQ2=sQuery(id+"F4.wireOp",EDGE,"E26.2.2");var subQ3=sQuery(id+"F3.wireOp",EDGE,"E20.2.3");var subQ4=sQuery(id+"F3.wireOp",EDGE,"E20.2.2");var subQ5=sQuery(id+"F3.wireOp",EDGE,"E20.2.1");var subQ6=makeQuery(id+"F19.opLoft","SWEPT_FACE",FACE,{"disambiguationData":[OSD([subQ5,subQ4,subQ3,sQuery(id+"F4.wireOp",EDGE,"E26.2.1"),subQ2,subQ1])]});var subQ13=makeQuery(id+"F40.opExtrude","CAP_FACE",FACE,{"disambiguationData":[OSD([sQuery(id+"F39.wireOp",EDGE,"E29"),sQuery(id+"F39.wireOp",EDGE,"E30")])],"isStart":false});var subQ55=sQuery(id+"F3.wireOp",EDGE,"E20.7.0");var subQ62=makeQuery(id+"F14.opLoft","CAP_FACE",FACE,{"disambiguationData":[OSD([makeQuery(id+"F3.imprint","IMPRINT",FACE,{"disambiguationData":[TD([[makeQuery(id+"F3.imprint","IMPRINT",EDGE,{"derivedFrom":subQ55}),-1.0]])]})])],"isStart":true});var subQ75=sQuery(id+"F3.wireOp",EDGE,"E18.bottom");var subQ80=makeQuery(id+"F5.opLoft","CAP_FACE",FACE,{"disambiguationData":[OSD([makeQuery(id+"F3.imprint","IMPRINT",FACE,{"disambiguationData":[TD([[makeQuery(id+"F3.imprint","IMPRINT",EDGE,{"derivedFrom":subQ75}),1.0]])]})])],"isStart":true});Q9=makeQuery(id+"F44.opFillet","BLEND_EDGE",EDGE,{"blendedFrom":[makeQuery(id+"F40.boolean.opBoolean","INTERSECT",EDGE,{"derivedFrom":[subQ6,subQ13]}),makeQuery(id+"F40.boolean.opBoolean","SPLIT",FACE,{"disambiguationData":[TD([subQ0])],"derivedFrom":makeQuery(id+"F33.boolean.opBoolean","SPLIT",FACE,{"disambiguationData":[TD([subQ6])],"derivedFrom":makeQuery(id+"F32.boolean.opBoolean","SPLIT",FACE,{"disambiguationData":[TD([subQ62])],"derivedFrom":makeQuery(id+"F31.boolean.opBoolean","SPLIT",FACE,{"disambiguationData":[TD([subQ62])],"derivedFrom":makeQuery(id+"F30.boolean.opBoolean","SPLIT",FACE,{"disambiguationData":[TD([subQ80])],"derivedFrom":makeQuery(id+"F29.boolean.opBoolean","SPLIT",FACE,{"disambiguationData":[TD([subQ80])],"derivedFrom":makeQuery(id+"F28.boolean.opBoolean","SPLIT",FACE,{"disambiguationData":[TD([subQ80])],"derivedFrom":makeQuery(id+"F27.boolean.opBoolean","SPLIT",FACE,{"disambiguationData":[TD([subQ80])],"derivedFrom":makeQuery(id+"F26.boolean.opBoolean","SPLIT",FACE,{"disambiguationData":[TD([subQ80])],"derivedFrom":makeQuery(id+"F25.boolean.opBoolean","SPLIT",FACE,{"disambiguationData":[TD([subQ80])],"derivedFrom":makeQuery(id+"F24.boolean.opBoolean","SPLIT",FACE,{"disambiguationData":[TD([subQ80])],"derivedFrom":makeQuery(id+"F1.opRevolve","SWEPT_FACE",FACE,{"disambiguationData":[OSD([sQuery(id+"F0.wireOp",EDGE,"E4")])]})})})})})})})})})})})})],"blendedInto":[makeQuery(id+"F40.boolean.opBoolean","SPLIT",FACE,{"disambiguationData":[TD([subQ0])],"derivedFrom":makeQuery(id+"F33.boolean.opBoolean","SPLIT",FACE,{"disambiguationData":[TD([subQ6])],"derivedFrom":makeQuery(id+"F32.boolean.opBoolean","SPLIT",FACE,{"disambiguationData":[TD([subQ62])],"derivedFrom":makeQuery(id+"F31.boolean.opBoolean","SPLIT",FACE,{"disambiguationData":[TD([subQ62])],"derivedFrom":makeQuery(id+"F30.boolean.opBoolean","SPLIT",FACE,{"disambiguationData":[TD([subQ80])],"derivedFrom":makeQuery(id+"F29.boolean.opBoolean","SPLIT",FACE,{"disambiguationData":[TD([subQ80])],"derivedFrom":makeQuery(id+"F28.boolean.opBoolean","SPLIT",FACE,{"disambiguationData":[TD([subQ80])],"derivedFrom":makeQuery(id+"F27.boolean.opBoolean","SPLIT",FACE,{"disambiguationData":[TD([subQ80])],"derivedFrom":makeQuery(id+"F26.boolean.opBoolean","SPLIT",FACE,{"disambiguationData":[TD([subQ80])],"derivedFrom":makeQuery(id+"F25.boolean.opBoolean","SPLIT",FACE,{"disambiguationData":[TD([subQ80])],"derivedFrom":makeQuery(id+"F24.boolean.opBoolean","SPLIT",FACE,{"disambiguationData":[TD([subQ80])],"derivedFrom":makeQuery(id+"F1.opRevolve","SWEPT_FACE",FACE,{"disambiguationData":[OSD([sQuery(id+"F0.wireOp",EDGE,"E4")])]})})})})})})})})})})})})]});}
            var Q10;
            {var subQ0=makeQuery(id+"F1.opRevolve","SWEPT_FACE",FACE,{"disambiguationData":[OSD([sQuery(id+"F0.wireOp",EDGE,"E1")])]});var subQ1=sQuery(id+"F4.wireOp",EDGE,"E26.3.3");var subQ2=sQuery(id+"F4.wireOp",EDGE,"E26.3.2");var subQ3=sQuery(id+"F3.wireOp",EDGE,"E20.3.3");var subQ4=sQuery(id+"F3.wireOp",EDGE,"E20.3.2");var subQ5=sQuery(id+"F3.wireOp",EDGE,"E20.3.1");var subQ6=makeQuery(id+"F18.opLoft","SWEPT_FACE",FACE,{"disambiguationData":[OSD([subQ5,subQ4,subQ3,sQuery(id+"F4.wireOp",EDGE,"E26.3.1"),subQ2,subQ1])]});var subQ13=makeQuery(id+"F40.opExtrude","CAP_FACE",FACE,{"disambiguationData":[OSD([sQuery(id+"F39.wireOp",EDGE,"E29"),sQuery(id+"F39.wireOp",EDGE,"E30")])],"isStart":false});var subQ35=sQuery(id+"F3.wireOp",EDGE,"E20.7.0");var subQ39=makeQuery(id+"F14.opLoft","CAP_FACE",FACE,{"disambiguationData":[OSD([makeQuery(id+"F3.imprint","IMPRINT",FACE,{"disambiguationData":[TD([[makeQuery(id+"F3.imprint","IMPRINT",EDGE,{"derivedFrom":subQ35}),-1.0]])]})])],"isStart":true});var subQ75=sQuery(id+"F3.wireOp",EDGE,"E18.bottom");var subQ80=makeQuery(id+"F5.opLoft","CAP_FACE",FACE,{"disambiguationData":[OSD([makeQuery(id+"F3.imprint","IMPRINT",FACE,{"disambiguationData":[TD([[makeQuery(id+"F3.imprint","IMPRINT",EDGE,{"derivedFrom":subQ75}),1.0]])]})])],"isStart":true});Q10=makeQuery(id+"F44.opFillet","BLEND_EDGE",EDGE,{"blendedFrom":[makeQuery(id+"F40.boolean.opBoolean","INTERSECT",EDGE,{"derivedFrom":[subQ6,subQ13]}),makeQuery(id+"F40.boolean.opBoolean","SPLIT",FACE,{"disambiguationData":[TD([subQ0])],"derivedFrom":makeQuery(id+"F34.boolean.opBoolean","SPLIT",FACE,{"disambiguationData":[TD([subQ6])],"derivedFrom":makeQuery(id+"F33.boolean.opBoolean","SPLIT",FACE,{"disambiguationData":[TD([subQ39])],"derivedFrom":makeQuery(id+"F32.boolean.opBoolean","SPLIT",FACE,{"disambiguationData":[TD([subQ39])],"derivedFrom":makeQuery(id+"F31.boolean.opBoolean","SPLIT",FACE,{"disambiguationData":[TD([subQ39])],"derivedFrom":makeQuery(id+"F30.boolean.opBoolean","SPLIT",FACE,{"disambiguationData":[TD([subQ80])],"derivedFrom":makeQuery(id+"F29.boolean.opBoolean","SPLIT",FACE,{"disambiguationData":[TD([subQ80])],"derivedFrom":makeQuery(id+"F28.boolean.opBoolean","SPLIT",FACE,{"disambiguationData":[TD([subQ80])],"derivedFrom":makeQuery(id+"F27.boolean.opBoolean","SPLIT",FACE,{"disambiguationData":[TD([subQ80])],"derivedFrom":makeQuery(id+"F26.boolean.opBoolean","SPLIT",FACE,{"disambiguationData":[TD([subQ80])],"derivedFrom":makeQuery(id+"F25.boolean.opBoolean","SPLIT",FACE,{"disambiguationData":[TD([subQ80])],"derivedFrom":makeQuery(id+"F24.boolean.opBoolean","SPLIT",FACE,{"disambiguationData":[TD([subQ80])],"derivedFrom":makeQuery(id+"F1.opRevolve","SWEPT_FACE",FACE,{"disambiguationData":[OSD([sQuery(id+"F0.wireOp",EDGE,"E4")])]})})})})})})})})})})})})})],"blendedInto":[makeQuery(id+"F40.boolean.opBoolean","SPLIT",FACE,{"disambiguationData":[TD([subQ0])],"derivedFrom":makeQuery(id+"F34.boolean.opBoolean","SPLIT",FACE,{"disambiguationData":[TD([subQ6])],"derivedFrom":makeQuery(id+"F33.boolean.opBoolean","SPLIT",FACE,{"disambiguationData":[TD([subQ39])],"derivedFrom":makeQuery(id+"F32.boolean.opBoolean","SPLIT",FACE,{"disambiguationData":[TD([subQ39])],"derivedFrom":makeQuery(id+"F31.boolean.opBoolean","SPLIT",FACE,{"disambiguationData":[TD([subQ39])],"derivedFrom":makeQuery(id+"F30.boolean.opBoolean","SPLIT",FACE,{"disambiguationData":[TD([subQ80])],"derivedFrom":makeQuery(id+"F29.boolean.opBoolean","SPLIT",FACE,{"disambiguationData":[TD([subQ80])],"derivedFrom":makeQuery(id+"F28.boolean.opBoolean","SPLIT",FACE,{"disambiguationData":[TD([subQ80])],"derivedFrom":makeQuery(id+"F27.boolean.opBoolean","SPLIT",FACE,{"disambiguationData":[TD([subQ80])],"derivedFrom":makeQuery(id+"F26.boolean.opBoolean","SPLIT",FACE,{"disambiguationData":[TD([subQ80])],"derivedFrom":makeQuery(id+"F25.boolean.opBoolean","SPLIT",FACE,{"disambiguationData":[TD([subQ80])],"derivedFrom":makeQuery(id+"F24.boolean.opBoolean","SPLIT",FACE,{"disambiguationData":[TD([subQ80])],"derivedFrom":makeQuery(id+"F1.opRevolve","SWEPT_FACE",FACE,{"disambiguationData":[OSD([sQuery(id+"F0.wireOp",EDGE,"E4")])]})})})})})})})})})})})})})]});}
            var Q11;
            {var subQ0=makeQuery(id+"F1.opRevolve","SWEPT_FACE",FACE,{"disambiguationData":[OSD([sQuery(id+"F0.wireOp",EDGE,"E1")])]});var subQ7=sQuery(id+"F4.wireOp",EDGE,"E26.4.3");var subQ8=sQuery(id+"F4.wireOp",EDGE,"E26.4.2");var subQ9=sQuery(id+"F3.wireOp",EDGE,"E20.4.3");var subQ10=sQuery(id+"F3.wireOp",EDGE,"E20.4.2");var subQ11=sQuery(id+"F3.wireOp",EDGE,"E20.4.1");var subQ12=makeQuery(id+"F17.opLoft","SWEPT_FACE",FACE,{"disambiguationData":[OSD([subQ11,subQ10,subQ9,sQuery(id+"F4.wireOp",EDGE,"E26.4.1"),subQ8,subQ7])]});var subQ13=makeQuery(id+"F40.opExtrude","CAP_FACE",FACE,{"disambiguationData":[OSD([sQuery(id+"F39.wireOp",EDGE,"E29"),sQuery(id+"F39.wireOp",EDGE,"E30")])],"isStart":false});var subQ32=sQuery(id+"F3.wireOp",EDGE,"E20.7.0");var subQ36=makeQuery(id+"F14.opLoft","CAP_FACE",FACE,{"disambiguationData":[OSD([makeQuery(id+"F3.imprint","IMPRINT",FACE,{"disambiguationData":[TD([[makeQuery(id+"F3.imprint","IMPRINT",EDGE,{"derivedFrom":subQ32}),-1.0]])]})])],"isStart":true});var subQ75=sQuery(id+"F3.wireOp",EDGE,"E18.bottom");var subQ80=makeQuery(id+"F5.opLoft","CAP_FACE",FACE,{"disambiguationData":[OSD([makeQuery(id+"F3.imprint","IMPRINT",FACE,{"disambiguationData":[TD([[makeQuery(id+"F3.imprint","IMPRINT",EDGE,{"derivedFrom":subQ75}),1.0]])]})])],"isStart":true});Q11=makeQuery(id+"F44.opFillet","BLEND_EDGE",EDGE,{"blendedFrom":[makeQuery(id+"F40.boolean.opBoolean","INTERSECT",EDGE,{"derivedFrom":[subQ12,subQ13]}),makeQuery(id+"F40.boolean.opBoolean","SPLIT",FACE,{"disambiguationData":[TD([subQ0])],"derivedFrom":makeQuery(id+"F35.boolean.opBoolean","SPLIT",FACE,{"disambiguationData":[TD([subQ12])],"derivedFrom":makeQuery(id+"F34.boolean.opBoolean","SPLIT",FACE,{"disambiguationData":[TD([subQ36])],"derivedFrom":makeQuery(id+"F33.boolean.opBoolean","SPLIT",FACE,{"disambiguationData":[TD([subQ36])],"derivedFrom":makeQuery(id+"F32.boolean.opBoolean","SPLIT",FACE,{"disambiguationData":[TD([subQ36])],"derivedFrom":makeQuery(id+"F31.boolean.opBoolean","SPLIT",FACE,{"disambiguationData":[TD([subQ36])],"derivedFrom":makeQuery(id+"F30.boolean.opBoolean","SPLIT",FACE,{"disambiguationData":[TD([subQ80])],"derivedFrom":makeQuery(id+"F29.boolean.opBoolean","SPLIT",FACE,{"disambiguationData":[TD([subQ80])],"derivedFrom":makeQuery(id+"F28.boolean.opBoolean","SPLIT",FACE,{"disambiguationData":[TD([subQ80])],"derivedFrom":makeQuery(id+"F27.boolean.opBoolean","SPLIT",FACE,{"disambiguationData":[TD([subQ80])],"derivedFrom":makeQuery(id+"F26.boolean.opBoolean","SPLIT",FACE,{"disambiguationData":[TD([subQ80])],"derivedFrom":makeQuery(id+"F25.boolean.opBoolean","SPLIT",FACE,{"disambiguationData":[TD([subQ80])],"derivedFrom":makeQuery(id+"F24.boolean.opBoolean","SPLIT",FACE,{"disambiguationData":[TD([subQ80])],"derivedFrom":makeQuery(id+"F1.opRevolve","SWEPT_FACE",FACE,{"disambiguationData":[OSD([sQuery(id+"F0.wireOp",EDGE,"E4")])]})})})})})})})})})})})})})})],"blendedInto":[makeQuery(id+"F40.boolean.opBoolean","SPLIT",FACE,{"disambiguationData":[TD([subQ0])],"derivedFrom":makeQuery(id+"F35.boolean.opBoolean","SPLIT",FACE,{"disambiguationData":[TD([subQ12])],"derivedFrom":makeQuery(id+"F34.boolean.opBoolean","SPLIT",FACE,{"disambiguationData":[TD([subQ36])],"derivedFrom":makeQuery(id+"F33.boolean.opBoolean","SPLIT",FACE,{"disambiguationData":[TD([subQ36])],"derivedFrom":makeQuery(id+"F32.boolean.opBoolean","SPLIT",FACE,{"disambiguationData":[TD([subQ36])],"derivedFrom":makeQuery(id+"F31.boolean.opBoolean","SPLIT",FACE,{"disambiguationData":[TD([subQ36])],"derivedFrom":makeQuery(id+"F30.boolean.opBoolean","SPLIT",FACE,{"disambiguationData":[TD([subQ80])],"derivedFrom":makeQuery(id+"F29.boolean.opBoolean","SPLIT",FACE,{"disambiguationData":[TD([subQ80])],"derivedFrom":makeQuery(id+"F28.boolean.opBoolean","SPLIT",FACE,{"disambiguationData":[TD([subQ80])],"derivedFrom":makeQuery(id+"F27.boolean.opBoolean","SPLIT",FACE,{"disambiguationData":[TD([subQ80])],"derivedFrom":makeQuery(id+"F26.boolean.opBoolean","SPLIT",FACE,{"disambiguationData":[TD([subQ80])],"derivedFrom":makeQuery(id+"F25.boolean.opBoolean","SPLIT",FACE,{"disambiguationData":[TD([subQ80])],"derivedFrom":makeQuery(id+"F24.boolean.opBoolean","SPLIT",FACE,{"disambiguationData":[TD([subQ80])],"derivedFrom":makeQuery(id+"F1.opRevolve","SWEPT_FACE",FACE,{"disambiguationData":[OSD([sQuery(id+"F0.wireOp",EDGE,"E4")])]})})})})})})})})})})})})})})]});}
            var Q12;
            {var subQ0=makeQuery(id+"F1.opRevolve","SWEPT_FACE",FACE,{"disambiguationData":[OSD([sQuery(id+"F0.wireOp",EDGE,"E1")])]});var subQ7=sQuery(id+"F4.wireOp",EDGE,"E26.5.3");var subQ8=sQuery(id+"F4.wireOp",EDGE,"E26.5.2");var subQ9=sQuery(id+"F3.wireOp",EDGE,"E20.5.3");var subQ10=sQuery(id+"F3.wireOp",EDGE,"E20.5.2");var subQ11=sQuery(id+"F3.wireOp",EDGE,"E20.5.1");var subQ12=makeQuery(id+"F16.opLoft","SWEPT_FACE",FACE,{"disambiguationData":[OSD([subQ11,subQ10,subQ9,sQuery(id+"F4.wireOp",EDGE,"E26.5.1"),subQ8,subQ7])]});var subQ13=makeQuery(id+"F40.opExtrude","CAP_FACE",FACE,{"disambiguationData":[OSD([sQuery(id+"F39.wireOp",EDGE,"E29"),sQuery(id+"F39.wireOp",EDGE,"E30")])],"isStart":false});var subQ26=sQuery(id+"F3.wireOp",EDGE,"E20.7.0");var subQ30=makeQuery(id+"F14.opLoft","CAP_FACE",FACE,{"disambiguationData":[OSD([makeQuery(id+"F3.imprint","IMPRINT",FACE,{"disambiguationData":[TD([[makeQuery(id+"F3.imprint","IMPRINT",EDGE,{"derivedFrom":subQ26}),-1.0]])]})])],"isStart":true});var subQ75=sQuery(id+"F3.wireOp",EDGE,"E18.bottom");var subQ80=makeQuery(id+"F5.opLoft","CAP_FACE",FACE,{"disambiguationData":[OSD([makeQuery(id+"F3.imprint","IMPRINT",FACE,{"disambiguationData":[TD([[makeQuery(id+"F3.imprint","IMPRINT",EDGE,{"derivedFrom":subQ75}),1.0]])]})])],"isStart":true});Q12=makeQuery(id+"F44.opFillet","BLEND_EDGE",EDGE,{"blendedFrom":[makeQuery(id+"F40.boolean.opBoolean","INTERSECT",EDGE,{"derivedFrom":[subQ12,subQ13]}),makeQuery(id+"F40.boolean.opBoolean","SPLIT",FACE,{"disambiguationData":[TD([subQ0])],"derivedFrom":makeQuery(id+"F36.boolean.opBoolean","SPLIT",FACE,{"disambiguationData":[TD([subQ12])],"derivedFrom":makeQuery(id+"F35.boolean.opBoolean","SPLIT",FACE,{"disambiguationData":[TD([subQ30])],"derivedFrom":makeQuery(id+"F34.boolean.opBoolean","SPLIT",FACE,{"disambiguationData":[TD([subQ30])],"derivedFrom":makeQuery(id+"F33.boolean.opBoolean","SPLIT",FACE,{"disambiguationData":[TD([subQ30])],"derivedFrom":makeQuery(id+"F32.boolean.opBoolean","SPLIT",FACE,{"disambiguationData":[TD([subQ30])],"derivedFrom":makeQuery(id+"F31.boolean.opBoolean","SPLIT",FACE,{"disambiguationData":[TD([subQ30])],"derivedFrom":makeQuery(id+"F30.boolean.opBoolean","SPLIT",FACE,{"disambiguationData":[TD([subQ80])],"derivedFrom":makeQuery(id+"F29.boolean.opBoolean","SPLIT",FACE,{"disambiguationData":[TD([subQ80])],"derivedFrom":makeQuery(id+"F28.boolean.opBoolean","SPLIT",FACE,{"disambiguationData":[TD([subQ80])],"derivedFrom":makeQuery(id+"F27.boolean.opBoolean","SPLIT",FACE,{"disambiguationData":[TD([subQ80])],"derivedFrom":makeQuery(id+"F26.boolean.opBoolean","SPLIT",FACE,{"disambiguationData":[TD([subQ80])],"derivedFrom":makeQuery(id+"F25.boolean.opBoolean","SPLIT",FACE,{"disambiguationData":[TD([subQ80])],"derivedFrom":makeQuery(id+"F24.boolean.opBoolean","SPLIT",FACE,{"disambiguationData":[TD([subQ80])],"derivedFrom":makeQuery(id+"F1.opRevolve","SWEPT_FACE",FACE,{"disambiguationData":[OSD([sQuery(id+"F0.wireOp",EDGE,"E4")])]})})})})})})})})})})})})})})})],"blendedInto":[makeQuery(id+"F40.boolean.opBoolean","SPLIT",FACE,{"disambiguationData":[TD([subQ0])],"derivedFrom":makeQuery(id+"F36.boolean.opBoolean","SPLIT",FACE,{"disambiguationData":[TD([subQ12])],"derivedFrom":makeQuery(id+"F35.boolean.opBoolean","SPLIT",FACE,{"disambiguationData":[TD([subQ30])],"derivedFrom":makeQuery(id+"F34.boolean.opBoolean","SPLIT",FACE,{"disambiguationData":[TD([subQ30])],"derivedFrom":makeQuery(id+"F33.boolean.opBoolean","SPLIT",FACE,{"disambiguationData":[TD([subQ30])],"derivedFrom":makeQuery(id+"F32.boolean.opBoolean","SPLIT",FACE,{"disambiguationData":[TD([subQ30])],"derivedFrom":makeQuery(id+"F31.boolean.opBoolean","SPLIT",FACE,{"disambiguationData":[TD([subQ30])],"derivedFrom":makeQuery(id+"F30.boolean.opBoolean","SPLIT",FACE,{"disambiguationData":[TD([subQ80])],"derivedFrom":makeQuery(id+"F29.boolean.opBoolean","SPLIT",FACE,{"disambiguationData":[TD([subQ80])],"derivedFrom":makeQuery(id+"F28.boolean.opBoolean","SPLIT",FACE,{"disambiguationData":[TD([subQ80])],"derivedFrom":makeQuery(id+"F27.boolean.opBoolean","SPLIT",FACE,{"disambiguationData":[TD([subQ80])],"derivedFrom":makeQuery(id+"F26.boolean.opBoolean","SPLIT",FACE,{"disambiguationData":[TD([subQ80])],"derivedFrom":makeQuery(id+"F25.boolean.opBoolean","SPLIT",FACE,{"disambiguationData":[TD([subQ80])],"derivedFrom":makeQuery(id+"F24.boolean.opBoolean","SPLIT",FACE,{"disambiguationData":[TD([subQ80])],"derivedFrom":makeQuery(id+"F1.opRevolve","SWEPT_FACE",FACE,{"disambiguationData":[OSD([sQuery(id+"F0.wireOp",EDGE,"E4")])]})})})})})})})})})})})})})})})]});}
            var Q13;
            {var subQ0=makeQuery(id+"F1.opRevolve","SWEPT_FACE",FACE,{"disambiguationData":[OSD([sQuery(id+"F0.wireOp",EDGE,"E1")])]});var subQ1=sQuery(id+"F4.wireOp",EDGE,"E26.6.3");var subQ2=sQuery(id+"F4.wireOp",EDGE,"E26.6.2");var subQ3=sQuery(id+"F3.wireOp",EDGE,"E20.6.3");var subQ4=sQuery(id+"F3.wireOp",EDGE,"E20.6.2");var subQ5=sQuery(id+"F3.wireOp",EDGE,"E20.6.1");var subQ6=makeQuery(id+"F15.opLoft","SWEPT_FACE",FACE,{"disambiguationData":[OSD([subQ5,subQ4,subQ3,sQuery(id+"F4.wireOp",EDGE,"E26.6.1"),subQ2,subQ1])]});var subQ13=makeQuery(id+"F40.opExtrude","CAP_FACE",FACE,{"disambiguationData":[OSD([sQuery(id+"F39.wireOp",EDGE,"E29"),sQuery(id+"F39.wireOp",EDGE,"E30")])],"isStart":false});var subQ19=sQuery(id+"F3.wireOp",EDGE,"E20.7.0");var subQ23=makeQuery(id+"F14.opLoft","CAP_FACE",FACE,{"disambiguationData":[OSD([makeQuery(id+"F3.imprint","IMPRINT",FACE,{"disambiguationData":[TD([[makeQuery(id+"F3.imprint","IMPRINT",EDGE,{"derivedFrom":subQ19}),-1.0]])]})])],"isStart":true});var subQ75=sQuery(id+"F3.wireOp",EDGE,"E18.bottom");var subQ80=makeQuery(id+"F5.opLoft","CAP_FACE",FACE,{"disambiguationData":[OSD([makeQuery(id+"F3.imprint","IMPRINT",FACE,{"disambiguationData":[TD([[makeQuery(id+"F3.imprint","IMPRINT",EDGE,{"derivedFrom":subQ75}),1.0]])]})])],"isStart":true});Q13=makeQuery(id+"F44.opFillet","BLEND_EDGE",EDGE,{"blendedFrom":[makeQuery(id+"F40.boolean.opBoolean","INTERSECT",EDGE,{"derivedFrom":[subQ6,subQ13]}),makeQuery(id+"F40.boolean.opBoolean","SPLIT",FACE,{"disambiguationData":[TD([subQ0])],"derivedFrom":makeQuery(id+"F37.boolean.opBoolean","SPLIT",FACE,{"disambiguationData":[TD([subQ6])],"derivedFrom":makeQuery(id+"F36.boolean.opBoolean","SPLIT",FACE,{"disambiguationData":[TD([subQ23])],"derivedFrom":makeQuery(id+"F35.boolean.opBoolean","SPLIT",FACE,{"disambiguationData":[TD([subQ23])],"derivedFrom":makeQuery(id+"F34.boolean.opBoolean","SPLIT",FACE,{"disambiguationData":[TD([subQ23])],"derivedFrom":makeQuery(id+"F33.boolean.opBoolean","SPLIT",FACE,{"disambiguationData":[TD([subQ23])],"derivedFrom":makeQuery(id+"F32.boolean.opBoolean","SPLIT",FACE,{"disambiguationData":[TD([subQ23])],"derivedFrom":makeQuery(id+"F31.boolean.opBoolean","SPLIT",FACE,{"disambiguationData":[TD([subQ23])],"derivedFrom":makeQuery(id+"F30.boolean.opBoolean","SPLIT",FACE,{"disambiguationData":[TD([subQ80])],"derivedFrom":makeQuery(id+"F29.boolean.opBoolean","SPLIT",FACE,{"disambiguationData":[TD([subQ80])],"derivedFrom":makeQuery(id+"F28.boolean.opBoolean","SPLIT",FACE,{"disambiguationData":[TD([subQ80])],"derivedFrom":makeQuery(id+"F27.boolean.opBoolean","SPLIT",FACE,{"disambiguationData":[TD([subQ80])],"derivedFrom":makeQuery(id+"F26.boolean.opBoolean","SPLIT",FACE,{"disambiguationData":[TD([subQ80])],"derivedFrom":makeQuery(id+"F25.boolean.opBoolean","SPLIT",FACE,{"disambiguationData":[TD([subQ80])],"derivedFrom":makeQuery(id+"F24.boolean.opBoolean","SPLIT",FACE,{"disambiguationData":[TD([subQ80])],"derivedFrom":makeQuery(id+"F1.opRevolve","SWEPT_FACE",FACE,{"disambiguationData":[OSD([sQuery(id+"F0.wireOp",EDGE,"E4")])]})})})})})})})})})})})})})})})})],"blendedInto":[makeQuery(id+"F40.boolean.opBoolean","SPLIT",FACE,{"disambiguationData":[TD([subQ0])],"derivedFrom":makeQuery(id+"F37.boolean.opBoolean","SPLIT",FACE,{"disambiguationData":[TD([subQ6])],"derivedFrom":makeQuery(id+"F36.boolean.opBoolean","SPLIT",FACE,{"disambiguationData":[TD([subQ23])],"derivedFrom":makeQuery(id+"F35.boolean.opBoolean","SPLIT",FACE,{"disambiguationData":[TD([subQ23])],"derivedFrom":makeQuery(id+"F34.boolean.opBoolean","SPLIT",FACE,{"disambiguationData":[TD([subQ23])],"derivedFrom":makeQuery(id+"F33.boolean.opBoolean","SPLIT",FACE,{"disambiguationData":[TD([subQ23])],"derivedFrom":makeQuery(id+"F32.boolean.opBoolean","SPLIT",FACE,{"disambiguationData":[TD([subQ23])],"derivedFrom":makeQuery(id+"F31.boolean.opBoolean","SPLIT",FACE,{"disambiguationData":[TD([subQ23])],"derivedFrom":makeQuery(id+"F30.boolean.opBoolean","SPLIT",FACE,{"disambiguationData":[TD([subQ80])],"derivedFrom":makeQuery(id+"F29.boolean.opBoolean","SPLIT",FACE,{"disambiguationData":[TD([subQ80])],"derivedFrom":makeQuery(id+"F28.boolean.opBoolean","SPLIT",FACE,{"disambiguationData":[TD([subQ80])],"derivedFrom":makeQuery(id+"F27.boolean.opBoolean","SPLIT",FACE,{"disambiguationData":[TD([subQ80])],"derivedFrom":makeQuery(id+"F26.boolean.opBoolean","SPLIT",FACE,{"disambiguationData":[TD([subQ80])],"derivedFrom":makeQuery(id+"F25.boolean.opBoolean","SPLIT",FACE,{"disambiguationData":[TD([subQ80])],"derivedFrom":makeQuery(id+"F24.boolean.opBoolean","SPLIT",FACE,{"disambiguationData":[TD([subQ80])],"derivedFrom":makeQuery(id+"F1.opRevolve","SWEPT_FACE",FACE,{"disambiguationData":[OSD([sQuery(id+"F0.wireOp",EDGE,"E4")])]})})})})})})})})})})})})})})})})]});}
            var Q14;
            {var subQ0=makeQuery(id+"F1.opRevolve","SWEPT_FACE",FACE,{"disambiguationData":[OSD([sQuery(id+"F0.wireOp",EDGE,"E1")])]});var subQ7=sQuery(id+"F4.wireOp",EDGE,"E26.5.3");var subQ8=sQuery(id+"F4.wireOp",EDGE,"E26.5.2");var subQ9=sQuery(id+"F3.wireOp",EDGE,"E20.5.3");var subQ10=sQuery(id+"F3.wireOp",EDGE,"E20.5.2");var subQ11=sQuery(id+"F3.wireOp",EDGE,"E20.5.1");var subQ12=makeQuery(id+"F16.opLoft","SWEPT_FACE",FACE,{"disambiguationData":[OSD([subQ11,subQ10,subQ9,sQuery(id+"F4.wireOp",EDGE,"E26.5.1"),subQ8,subQ7])]});var subQ13=makeQuery(id+"F40.opExtrude","CAP_FACE",FACE,{"disambiguationData":[OSD([sQuery(id+"F39.wireOp",EDGE,"E29"),sQuery(id+"F39.wireOp",EDGE,"E30")])],"isStart":false});var subQ26=sQuery(id+"F3.wireOp",EDGE,"E20.7.0");var subQ30=makeQuery(id+"F14.opLoft","CAP_FACE",FACE,{"disambiguationData":[OSD([makeQuery(id+"F3.imprint","IMPRINT",FACE,{"disambiguationData":[TD([[makeQuery(id+"F3.imprint","IMPRINT",EDGE,{"derivedFrom":subQ26}),-1.0]])]})])],"isStart":true});var subQ75=sQuery(id+"F3.wireOp",EDGE,"E18.bottom");var subQ80=makeQuery(id+"F5.opLoft","CAP_FACE",FACE,{"disambiguationData":[OSD([makeQuery(id+"F3.imprint","IMPRINT",FACE,{"disambiguationData":[TD([[makeQuery(id+"F3.imprint","IMPRINT",EDGE,{"derivedFrom":subQ75}),1.0]])]})])],"isStart":true});Q14=makeQuery(id+"F44.opFillet","BLEND_EDGE",EDGE,{"blendedFrom":[makeQuery(id+"F40.boolean.opBoolean","INTERSECT",EDGE,{"derivedFrom":[subQ12,subQ13]}),makeQuery(id+"F40.boolean.opBoolean","SPLIT",FACE,{"disambiguationData":[TD([subQ0])],"derivedFrom":makeQuery(id+"F36.boolean.opBoolean","SPLIT",FACE,{"disambiguationData":[TD([subQ12])],"derivedFrom":makeQuery(id+"F35.boolean.opBoolean","SPLIT",FACE,{"disambiguationData":[TD([subQ30])],"derivedFrom":makeQuery(id+"F34.boolean.opBoolean","SPLIT",FACE,{"disambiguationData":[TD([subQ30])],"derivedFrom":makeQuery(id+"F33.boolean.opBoolean","SPLIT",FACE,{"disambiguationData":[TD([subQ30])],"derivedFrom":makeQuery(id+"F32.boolean.opBoolean","SPLIT",FACE,{"disambiguationData":[TD([subQ30])],"derivedFrom":makeQuery(id+"F31.boolean.opBoolean","SPLIT",FACE,{"disambiguationData":[TD([subQ30])],"derivedFrom":makeQuery(id+"F30.boolean.opBoolean","SPLIT",FACE,{"disambiguationData":[TD([subQ80])],"derivedFrom":makeQuery(id+"F29.boolean.opBoolean","SPLIT",FACE,{"disambiguationData":[TD([subQ80])],"derivedFrom":makeQuery(id+"F28.boolean.opBoolean","SPLIT",FACE,{"disambiguationData":[TD([subQ80])],"derivedFrom":makeQuery(id+"F27.boolean.opBoolean","SPLIT",FACE,{"disambiguationData":[TD([subQ80])],"derivedFrom":makeQuery(id+"F26.boolean.opBoolean","SPLIT",FACE,{"disambiguationData":[TD([subQ80])],"derivedFrom":makeQuery(id+"F25.boolean.opBoolean","SPLIT",FACE,{"disambiguationData":[TD([subQ80])],"derivedFrom":makeQuery(id+"F24.boolean.opBoolean","SPLIT",FACE,{"disambiguationData":[TD([subQ80])],"derivedFrom":makeQuery(id+"F1.opRevolve","SWEPT_FACE",FACE,{"disambiguationData":[OSD([sQuery(id+"F0.wireOp",EDGE,"E4")])]})})})})})})})})})})})})})})})],"blendedInto":[makeQuery(id+"F40.boolean.opBoolean","SPLIT",FACE,{"disambiguationData":[TD([subQ0])],"derivedFrom":makeQuery(id+"F36.boolean.opBoolean","SPLIT",FACE,{"disambiguationData":[TD([subQ12])],"derivedFrom":makeQuery(id+"F35.boolean.opBoolean","SPLIT",FACE,{"disambiguationData":[TD([subQ30])],"derivedFrom":makeQuery(id+"F34.boolean.opBoolean","SPLIT",FACE,{"disambiguationData":[TD([subQ30])],"derivedFrom":makeQuery(id+"F33.boolean.opBoolean","SPLIT",FACE,{"disambiguationData":[TD([subQ30])],"derivedFrom":makeQuery(id+"F32.boolean.opBoolean","SPLIT",FACE,{"disambiguationData":[TD([subQ30])],"derivedFrom":makeQuery(id+"F31.boolean.opBoolean","SPLIT",FACE,{"disambiguationData":[TD([subQ30])],"derivedFrom":makeQuery(id+"F30.boolean.opBoolean","SPLIT",FACE,{"disambiguationData":[TD([subQ80])],"derivedFrom":makeQuery(id+"F29.boolean.opBoolean","SPLIT",FACE,{"disambiguationData":[TD([subQ80])],"derivedFrom":makeQuery(id+"F28.boolean.opBoolean","SPLIT",FACE,{"disambiguationData":[TD([subQ80])],"derivedFrom":makeQuery(id+"F27.boolean.opBoolean","SPLIT",FACE,{"disambiguationData":[TD([subQ80])],"derivedFrom":makeQuery(id+"F26.boolean.opBoolean","SPLIT",FACE,{"disambiguationData":[TD([subQ80])],"derivedFrom":makeQuery(id+"F25.boolean.opBoolean","SPLIT",FACE,{"disambiguationData":[TD([subQ80])],"derivedFrom":makeQuery(id+"F24.boolean.opBoolean","SPLIT",FACE,{"disambiguationData":[TD([subQ80])],"derivedFrom":makeQuery(id+"F1.opRevolve","SWEPT_FACE",FACE,{"disambiguationData":[OSD([sQuery(id+"F0.wireOp",EDGE,"E4")])]})})})})})})})})})})})})})})})]});}
            var Q15;
            {var subQ0=makeQuery(id+"F1.opRevolve","SWEPT_FACE",FACE,{"disambiguationData":[OSD([sQuery(id+"F0.wireOp",EDGE,"E1")])]});var subQ1=sQuery(id+"F4.wireOp",EDGE,"E26.7.3");var subQ2=sQuery(id+"F4.wireOp",EDGE,"E26.7.2");var subQ3=sQuery(id+"F3.wireOp",EDGE,"E20.7.3");var subQ4=sQuery(id+"F3.wireOp",EDGE,"E20.7.2");var subQ5=sQuery(id+"F3.wireOp",EDGE,"E20.7.1");var subQ6=makeQuery(id+"F14.opLoft","SWEPT_FACE",FACE,{"disambiguationData":[OSD([subQ5,subQ4,subQ3,sQuery(id+"F4.wireOp",EDGE,"E26.7.1"),subQ2,subQ1])]});var subQ13=makeQuery(id+"F40.opExtrude","CAP_FACE",FACE,{"disambiguationData":[OSD([sQuery(id+"F39.wireOp",EDGE,"E29"),sQuery(id+"F39.wireOp",EDGE,"E30")])],"isStart":false});var subQ20=sQuery(id+"F3.wireOp",EDGE,"E20.7.0");var subQ22=makeQuery(id+"F14.opLoft","CAP_FACE",FACE,{"disambiguationData":[OSD([makeQuery(id+"F3.imprint","IMPRINT",FACE,{"disambiguationData":[TD([[makeQuery(id+"F3.imprint","IMPRINT",EDGE,{"derivedFrom":subQ20}),-1.0]])]})])],"isStart":true});var subQ75=sQuery(id+"F3.wireOp",EDGE,"E18.bottom");var subQ80=makeQuery(id+"F5.opLoft","CAP_FACE",FACE,{"disambiguationData":[OSD([makeQuery(id+"F3.imprint","IMPRINT",FACE,{"disambiguationData":[TD([[makeQuery(id+"F3.imprint","IMPRINT",EDGE,{"derivedFrom":subQ75}),1.0]])]})])],"isStart":true});Q15=makeQuery(id+"F44.opFillet","BLEND_EDGE",EDGE,{"blendedFrom":[makeQuery(id+"F40.boolean.opBoolean","INTERSECT",EDGE,{"derivedFrom":[subQ6,subQ13]}),makeQuery(id+"F40.boolean.opBoolean","SPLIT",FACE,{"disambiguationData":[TD([subQ0])],"derivedFrom":makeQuery(id+"F38.boolean.opBoolean","SPLIT",FACE,{"disambiguationData":[TD([subQ6])],"derivedFrom":makeQuery(id+"F37.boolean.opBoolean","SPLIT",FACE,{"disambiguationData":[TD([subQ22])],"derivedFrom":makeQuery(id+"F36.boolean.opBoolean","SPLIT",FACE,{"disambiguationData":[TD([subQ22])],"derivedFrom":makeQuery(id+"F35.boolean.opBoolean","SPLIT",FACE,{"disambiguationData":[TD([subQ22])],"derivedFrom":makeQuery(id+"F34.boolean.opBoolean","SPLIT",FACE,{"disambiguationData":[TD([subQ22])],"derivedFrom":makeQuery(id+"F33.boolean.opBoolean","SPLIT",FACE,{"disambiguationData":[TD([subQ22])],"derivedFrom":makeQuery(id+"F32.boolean.opBoolean","SPLIT",FACE,{"disambiguationData":[TD([subQ22])],"derivedFrom":makeQuery(id+"F31.boolean.opBoolean","SPLIT",FACE,{"disambiguationData":[TD([subQ22])],"derivedFrom":makeQuery(id+"F30.boolean.opBoolean","SPLIT",FACE,{"disambiguationData":[TD([subQ80])],"derivedFrom":makeQuery(id+"F29.boolean.opBoolean","SPLIT",FACE,{"disambiguationData":[TD([subQ80])],"derivedFrom":makeQuery(id+"F28.boolean.opBoolean","SPLIT",FACE,{"disambiguationData":[TD([subQ80])],"derivedFrom":makeQuery(id+"F27.boolean.opBoolean","SPLIT",FACE,{"disambiguationData":[TD([subQ80])],"derivedFrom":makeQuery(id+"F26.boolean.opBoolean","SPLIT",FACE,{"disambiguationData":[TD([subQ80])],"derivedFrom":makeQuery(id+"F25.boolean.opBoolean","SPLIT",FACE,{"disambiguationData":[TD([subQ80])],"derivedFrom":makeQuery(id+"F24.boolean.opBoolean","SPLIT",FACE,{"disambiguationData":[TD([subQ80])],"derivedFrom":makeQuery(id+"F1.opRevolve","SWEPT_FACE",FACE,{"disambiguationData":[OSD([sQuery(id+"F0.wireOp",EDGE,"E4")])]})})})})})})})})})})})})})})})})})],"blendedInto":[makeQuery(id+"F40.boolean.opBoolean","SPLIT",FACE,{"disambiguationData":[TD([subQ0])],"derivedFrom":makeQuery(id+"F38.boolean.opBoolean","SPLIT",FACE,{"disambiguationData":[TD([subQ6])],"derivedFrom":makeQuery(id+"F37.boolean.opBoolean","SPLIT",FACE,{"disambiguationData":[TD([subQ22])],"derivedFrom":makeQuery(id+"F36.boolean.opBoolean","SPLIT",FACE,{"disambiguationData":[TD([subQ22])],"derivedFrom":makeQuery(id+"F35.boolean.opBoolean","SPLIT",FACE,{"disambiguationData":[TD([subQ22])],"derivedFrom":makeQuery(id+"F34.boolean.opBoolean","SPLIT",FACE,{"disambiguationData":[TD([subQ22])],"derivedFrom":makeQuery(id+"F33.boolean.opBoolean","SPLIT",FACE,{"disambiguationData":[TD([subQ22])],"derivedFrom":makeQuery(id+"F32.boolean.opBoolean","SPLIT",FACE,{"disambiguationData":[TD([subQ22])],"derivedFrom":makeQuery(id+"F31.boolean.opBoolean","SPLIT",FACE,{"disambiguationData":[TD([subQ22])],"derivedFrom":makeQuery(id+"F30.boolean.opBoolean","SPLIT",FACE,{"disambiguationData":[TD([subQ80])],"derivedFrom":makeQuery(id+"F29.boolean.opBoolean","SPLIT",FACE,{"disambiguationData":[TD([subQ80])],"derivedFrom":makeQuery(id+"F28.boolean.opBoolean","SPLIT",FACE,{"disambiguationData":[TD([subQ80])],"derivedFrom":makeQuery(id+"F27.boolean.opBoolean","SPLIT",FACE,{"disambiguationData":[TD([subQ80])],"derivedFrom":makeQuery(id+"F26.boolean.opBoolean","SPLIT",FACE,{"disambiguationData":[TD([subQ80])],"derivedFrom":makeQuery(id+"F25.boolean.opBoolean","SPLIT",FACE,{"disambiguationData":[TD([subQ80])],"derivedFrom":makeQuery(id+"F24.boolean.opBoolean","SPLIT",FACE,{"disambiguationData":[TD([subQ80])],"derivedFrom":makeQuery(id+"F1.opRevolve","SWEPT_FACE",FACE,{"disambiguationData":[OSD([sQuery(id+"F0.wireOp",EDGE,"E4")])]})})})})})})})})})})})})})})})})})]});}
            var Q16;
            {var subQ0=makeQuery(id+"F1.opRevolve","SWEPT_FACE",FACE,{"disambiguationData":[OSD([sQuery(id+"F0.wireOp",EDGE,"E1")])]});var subQ1=sQuery(id+"F3.wireOp",EDGE,"E20.8.3");var subQ2=sQuery(id+"F3.wireOp",EDGE,"E20.8.2");var subQ3=sQuery(id+"F3.wireOp",EDGE,"E20.8.1");var subQ4=makeQuery(id+"F13.opLoft","SWEPT_FACE",FACE,{"disambiguationData":[OSD([subQ3,subQ2,subQ1,sQuery(id+"F4.wireOp",EDGE,"E26.8.1"),sQuery(id+"F4.wireOp",EDGE,"E26.8.2"),sQuery(id+"F4.wireOp",EDGE,"E26.8.3")])]});var subQ5=makeQuery(id+"F40.opExtrude","CAP_FACE",FACE,{"disambiguationData":[OSD([sQuery(id+"F39.wireOp",EDGE,"E29"),sQuery(id+"F39.wireOp",EDGE,"E30")])],"isStart":false});var subQ10=sQuery(id+"F3.wireOp",EDGE,"E20.7.0");var subQ16=makeQuery(id+"F14.opLoft","CAP_FACE",FACE,{"disambiguationData":[OSD([makeQuery(id+"F3.imprint","IMPRINT",FACE,{"disambiguationData":[TD([[makeQuery(id+"F3.imprint","IMPRINT",EDGE,{"derivedFrom":subQ10}),-1.0]])]})])],"isStart":true});var subQ74=sQuery(id+"F3.wireOp",EDGE,"E18.bottom");var subQ79=makeQuery(id+"F5.opLoft","CAP_FACE",FACE,{"disambiguationData":[OSD([makeQuery(id+"F3.imprint","IMPRINT",FACE,{"disambiguationData":[TD([[makeQuery(id+"F3.imprint","IMPRINT",EDGE,{"derivedFrom":subQ74}),1.0]])]})])],"isStart":true});Q16=makeQuery(id+"F44.opFillet","BLEND_EDGE",EDGE,{"blendedFrom":[makeQuery(id+"F40.boolean.opBoolean","INTERSECT",EDGE,{"derivedFrom":[subQ4,subQ5]}),makeQuery(id+"F40.boolean.opBoolean","SPLIT",FACE,{"disambiguationData":[TD([subQ0])],"derivedFrom":makeQuery(id+"F38.boolean.opBoolean","SPLIT",FACE,{"disambiguationData":[TD([subQ4])],"derivedFrom":makeQuery(id+"F37.boolean.opBoolean","SPLIT",FACE,{"disambiguationData":[TD([subQ16])],"derivedFrom":makeQuery(id+"F36.boolean.opBoolean","SPLIT",FACE,{"disambiguationData":[TD([subQ16])],"derivedFrom":makeQuery(id+"F35.boolean.opBoolean","SPLIT",FACE,{"disambiguationData":[TD([subQ16])],"derivedFrom":makeQuery(id+"F34.boolean.opBoolean","SPLIT",FACE,{"disambiguationData":[TD([subQ16])],"derivedFrom":makeQuery(id+"F33.boolean.opBoolean","SPLIT",FACE,{"disambiguationData":[TD([subQ16])],"derivedFrom":makeQuery(id+"F32.boolean.opBoolean","SPLIT",FACE,{"disambiguationData":[TD([subQ16])],"derivedFrom":makeQuery(id+"F31.boolean.opBoolean","SPLIT",FACE,{"disambiguationData":[TD([subQ16])],"derivedFrom":makeQuery(id+"F30.boolean.opBoolean","SPLIT",FACE,{"disambiguationData":[TD([subQ79])],"derivedFrom":makeQuery(id+"F29.boolean.opBoolean","SPLIT",FACE,{"disambiguationData":[TD([subQ79])],"derivedFrom":makeQuery(id+"F28.boolean.opBoolean","SPLIT",FACE,{"disambiguationData":[TD([subQ79])],"derivedFrom":makeQuery(id+"F27.boolean.opBoolean","SPLIT",FACE,{"disambiguationData":[TD([subQ79])],"derivedFrom":makeQuery(id+"F26.boolean.opBoolean","SPLIT",FACE,{"disambiguationData":[TD([subQ79])],"derivedFrom":makeQuery(id+"F25.boolean.opBoolean","SPLIT",FACE,{"disambiguationData":[TD([subQ79])],"derivedFrom":makeQuery(id+"F24.boolean.opBoolean","SPLIT",FACE,{"disambiguationData":[TD([subQ79])],"derivedFrom":makeQuery(id+"F1.opRevolve","SWEPT_FACE",FACE,{"disambiguationData":[OSD([sQuery(id+"F0.wireOp",EDGE,"E4")])]})})})})})})})})})})})})})})})})})],"blendedInto":[makeQuery(id+"F40.boolean.opBoolean","SPLIT",FACE,{"disambiguationData":[TD([subQ0])],"derivedFrom":makeQuery(id+"F38.boolean.opBoolean","SPLIT",FACE,{"disambiguationData":[TD([subQ4])],"derivedFrom":makeQuery(id+"F37.boolean.opBoolean","SPLIT",FACE,{"disambiguationData":[TD([subQ16])],"derivedFrom":makeQuery(id+"F36.boolean.opBoolean","SPLIT",FACE,{"disambiguationData":[TD([subQ16])],"derivedFrom":makeQuery(id+"F35.boolean.opBoolean","SPLIT",FACE,{"disambiguationData":[TD([subQ16])],"derivedFrom":makeQuery(id+"F34.boolean.opBoolean","SPLIT",FACE,{"disambiguationData":[TD([subQ16])],"derivedFrom":makeQuery(id+"F33.boolean.opBoolean","SPLIT",FACE,{"disambiguationData":[TD([subQ16])],"derivedFrom":makeQuery(id+"F32.boolean.opBoolean","SPLIT",FACE,{"disambiguationData":[TD([subQ16])],"derivedFrom":makeQuery(id+"F31.boolean.opBoolean","SPLIT",FACE,{"disambiguationData":[TD([subQ16])],"derivedFrom":makeQuery(id+"F30.boolean.opBoolean","SPLIT",FACE,{"disambiguationData":[TD([subQ79])],"derivedFrom":makeQuery(id+"F29.boolean.opBoolean","SPLIT",FACE,{"disambiguationData":[TD([subQ79])],"derivedFrom":makeQuery(id+"F28.boolean.opBoolean","SPLIT",FACE,{"disambiguationData":[TD([subQ79])],"derivedFrom":makeQuery(id+"F27.boolean.opBoolean","SPLIT",FACE,{"disambiguationData":[TD([subQ79])],"derivedFrom":makeQuery(id+"F26.boolean.opBoolean","SPLIT",FACE,{"disambiguationData":[TD([subQ79])],"derivedFrom":makeQuery(id+"F25.boolean.opBoolean","SPLIT",FACE,{"disambiguationData":[TD([subQ79])],"derivedFrom":makeQuery(id+"F24.boolean.opBoolean","SPLIT",FACE,{"disambiguationData":[TD([subQ79])],"derivedFrom":makeQuery(id+"F1.opRevolve","SWEPT_FACE",FACE,{"disambiguationData":[OSD([sQuery(id+"F0.wireOp",EDGE,"E4")])]})})})})})})})})})})})})})})})})})]});}
            var Q17;
            {var subQ0=makeQuery(id+"F1.opRevolve","SWEPT_FACE",FACE,{"disambiguationData":[OSD([sQuery(id+"F0.wireOp",EDGE,"E3")])]});var subQ1=sQuery(id+"F3.wireOp",EDGE,"E20.8.3");var subQ2=sQuery(id+"F3.wireOp",EDGE,"E20.8.2");var subQ3=sQuery(id+"F3.wireOp",EDGE,"E20.8.1");var subQ4=makeQuery(id+"F23.opLoft","SWEPT_FACE",FACE,{"disambiguationData":[OSD([subQ3,subQ2,subQ1,sQuery(id+"F22.wireOp",EDGE,"E27.bottom"),sQuery(id+"F22.wireOp",EDGE,"E27.top"),sQuery(id+"F22.wireOp",EDGE,"E27.left")])]});var subQ7=sQuery(id+"F3.wireOp",EDGE,"E20.7.0");var subQ9=makeQuery(id+"F40.opExtrude","CAP_FACE",FACE,{"disambiguationData":[OSD([sQuery(id+"F39.wireOp",EDGE,"E29"),sQuery(id+"F39.wireOp",EDGE,"E30")])],"isStart":true});var subQ10=makeQuery(id+"F13.opLoft","SWEPT_FACE",FACE,{"disambiguationData":[OSD([subQ3,subQ2,subQ1,sQuery(id+"F4.wireOp",EDGE,"E26.8.1"),sQuery(id+"F4.wireOp",EDGE,"E26.8.2"),sQuery(id+"F4.wireOp",EDGE,"E26.8.3")])]});var subQ17=makeQuery(id+"F14.opLoft","CAP_FACE",FACE,{"disambiguationData":[OSD([makeQuery(id+"F3.imprint","IMPRINT",FACE,{"disambiguationData":[TD([[makeQuery(id+"F3.imprint","IMPRINT",EDGE,{"derivedFrom":subQ7}),-1.0]])]})])],"isStart":true});var subQ75=sQuery(id+"F3.wireOp",EDGE,"E18.bottom");var subQ80=makeQuery(id+"F5.opLoft","CAP_FACE",FACE,{"disambiguationData":[OSD([makeQuery(id+"F3.imprint","IMPRINT",FACE,{"disambiguationData":[TD([[makeQuery(id+"F3.imprint","IMPRINT",EDGE,{"derivedFrom":subQ75}),1.0]])]})])],"isStart":true});Q17=makeQuery(id+"F44.opFillet","BLEND_EDGE",EDGE,{"blendedFrom":[makeQuery(id+"F40.boolean.opBoolean","INTERSECT",EDGE,{"derivedFrom":[subQ4,subQ9]}),makeQuery(id+"F40.boolean.opBoolean","SPLIT",FACE,{"disambiguationData":[TD([subQ0])],"derivedFrom":makeQuery(id+"F38.boolean.opBoolean","SPLIT",FACE,{"disambiguationData":[TD([subQ10])],"derivedFrom":makeQuery(id+"F37.boolean.opBoolean","SPLIT",FACE,{"disambiguationData":[TD([subQ17])],"derivedFrom":makeQuery(id+"F36.boolean.opBoolean","SPLIT",FACE,{"disambiguationData":[TD([subQ17])],"derivedFrom":makeQuery(id+"F35.boolean.opBoolean","SPLIT",FACE,{"disambiguationData":[TD([subQ17])],"derivedFrom":makeQuery(id+"F34.boolean.opBoolean","SPLIT",FACE,{"disambiguationData":[TD([subQ17])],"derivedFrom":makeQuery(id+"F33.boolean.opBoolean","SPLIT",FACE,{"disambiguationData":[TD([subQ17])],"derivedFrom":makeQuery(id+"F32.boolean.opBoolean","SPLIT",FACE,{"disambiguationData":[TD([subQ17])],"derivedFrom":makeQuery(id+"F31.boolean.opBoolean","SPLIT",FACE,{"disambiguationData":[TD([subQ17])],"derivedFrom":makeQuery(id+"F30.boolean.opBoolean","SPLIT",FACE,{"disambiguationData":[TD([subQ80])],"derivedFrom":makeQuery(id+"F29.boolean.opBoolean","SPLIT",FACE,{"disambiguationData":[TD([subQ80])],"derivedFrom":makeQuery(id+"F28.boolean.opBoolean","SPLIT",FACE,{"disambiguationData":[TD([subQ80])],"derivedFrom":makeQuery(id+"F27.boolean.opBoolean","SPLIT",FACE,{"disambiguationData":[TD([subQ80])],"derivedFrom":makeQuery(id+"F26.boolean.opBoolean","SPLIT",FACE,{"disambiguationData":[TD([subQ80])],"derivedFrom":makeQuery(id+"F25.boolean.opBoolean","SPLIT",FACE,{"disambiguationData":[TD([subQ80])],"derivedFrom":makeQuery(id+"F24.boolean.opBoolean","SPLIT",FACE,{"disambiguationData":[TD([subQ80])],"derivedFrom":makeQuery(id+"F1.opRevolve","SWEPT_FACE",FACE,{"disambiguationData":[OSD([sQuery(id+"F0.wireOp",EDGE,"E4")])]})})})})})})})})})})})})})})})})})],"blendedInto":[makeQuery(id+"F40.boolean.opBoolean","SPLIT",FACE,{"disambiguationData":[TD([subQ0])],"derivedFrom":makeQuery(id+"F38.boolean.opBoolean","SPLIT",FACE,{"disambiguationData":[TD([subQ10])],"derivedFrom":makeQuery(id+"F37.boolean.opBoolean","SPLIT",FACE,{"disambiguationData":[TD([subQ17])],"derivedFrom":makeQuery(id+"F36.boolean.opBoolean","SPLIT",FACE,{"disambiguationData":[TD([subQ17])],"derivedFrom":makeQuery(id+"F35.boolean.opBoolean","SPLIT",FACE,{"disambiguationData":[TD([subQ17])],"derivedFrom":makeQuery(id+"F34.boolean.opBoolean","SPLIT",FACE,{"disambiguationData":[TD([subQ17])],"derivedFrom":makeQuery(id+"F33.boolean.opBoolean","SPLIT",FACE,{"disambiguationData":[TD([subQ17])],"derivedFrom":makeQuery(id+"F32.boolean.opBoolean","SPLIT",FACE,{"disambiguationData":[TD([subQ17])],"derivedFrom":makeQuery(id+"F31.boolean.opBoolean","SPLIT",FACE,{"disambiguationData":[TD([subQ17])],"derivedFrom":makeQuery(id+"F30.boolean.opBoolean","SPLIT",FACE,{"disambiguationData":[TD([subQ80])],"derivedFrom":makeQuery(id+"F29.boolean.opBoolean","SPLIT",FACE,{"disambiguationData":[TD([subQ80])],"derivedFrom":makeQuery(id+"F28.boolean.opBoolean","SPLIT",FACE,{"disambiguationData":[TD([subQ80])],"derivedFrom":makeQuery(id+"F27.boolean.opBoolean","SPLIT",FACE,{"disambiguationData":[TD([subQ80])],"derivedFrom":makeQuery(id+"F26.boolean.opBoolean","SPLIT",FACE,{"disambiguationData":[TD([subQ80])],"derivedFrom":makeQuery(id+"F25.boolean.opBoolean","SPLIT",FACE,{"disambiguationData":[TD([subQ80])],"derivedFrom":makeQuery(id+"F24.boolean.opBoolean","SPLIT",FACE,{"disambiguationData":[TD([subQ80])],"derivedFrom":makeQuery(id+"F1.opRevolve","SWEPT_FACE",FACE,{"disambiguationData":[OSD([sQuery(id+"F0.wireOp",EDGE,"E4")])]})})})})})})})})})})})})})})})})})]});}
            var Q18;
            {var subQ0=makeQuery(id+"F1.opRevolve","SWEPT_FACE",FACE,{"disambiguationData":[OSD([sQuery(id+"F0.wireOp",EDGE,"E3")])]});var subQ5=sQuery(id+"F3.wireOp",EDGE,"E20.7.3");var subQ6=sQuery(id+"F3.wireOp",EDGE,"E20.7.2");var subQ7=sQuery(id+"F3.wireOp",EDGE,"E20.7.1");var subQ8=makeQuery(id+"F38.opLoft","SWEPT_FACE",FACE,{"disambiguationData":[OSD([subQ7,subQ6,subQ5,sQuery(id+"F22.wireOp",EDGE,"E28.15.0"),sQuery(id+"F22.wireOp",EDGE,"E28.15.2"),sQuery(id+"F22.wireOp",EDGE,"E28.15.3")])]});var subQ9=makeQuery(id+"F40.opExtrude","CAP_FACE",FACE,{"disambiguationData":[OSD([sQuery(id+"F39.wireOp",EDGE,"E29"),sQuery(id+"F39.wireOp",EDGE,"E30")])],"isStart":true});var subQ13=sQuery(id+"F4.wireOp",EDGE,"E26.7.3");var subQ14=sQuery(id+"F4.wireOp",EDGE,"E26.7.2");var subQ15=makeQuery(id+"F14.opLoft","SWEPT_FACE",FACE,{"disambiguationData":[OSD([subQ7,subQ6,subQ5,sQuery(id+"F4.wireOp",EDGE,"E26.7.1"),subQ14,subQ13])]});var subQ21=sQuery(id+"F3.wireOp",EDGE,"E20.7.0");var subQ23=makeQuery(id+"F14.opLoft","CAP_FACE",FACE,{"disambiguationData":[OSD([makeQuery(id+"F3.imprint","IMPRINT",FACE,{"disambiguationData":[TD([[makeQuery(id+"F3.imprint","IMPRINT",EDGE,{"derivedFrom":subQ21}),-1.0]])]})])],"isStart":true});var subQ76=sQuery(id+"F3.wireOp",EDGE,"E18.bottom");var subQ81=makeQuery(id+"F5.opLoft","CAP_FACE",FACE,{"disambiguationData":[OSD([makeQuery(id+"F3.imprint","IMPRINT",FACE,{"disambiguationData":[TD([[makeQuery(id+"F3.imprint","IMPRINT",EDGE,{"derivedFrom":subQ76}),1.0]])]})])],"isStart":true});Q18=makeQuery(id+"F44.opFillet","BLEND_EDGE",EDGE,{"blendedFrom":[makeQuery(id+"F40.boolean.opBoolean","INTERSECT",EDGE,{"derivedFrom":[subQ8,subQ9]}),makeQuery(id+"F40.boolean.opBoolean","SPLIT",FACE,{"disambiguationData":[TD([subQ0])],"derivedFrom":makeQuery(id+"F38.boolean.opBoolean","SPLIT",FACE,{"disambiguationData":[TD([subQ15])],"derivedFrom":makeQuery(id+"F37.boolean.opBoolean","SPLIT",FACE,{"disambiguationData":[TD([subQ23])],"derivedFrom":makeQuery(id+"F36.boolean.opBoolean","SPLIT",FACE,{"disambiguationData":[TD([subQ23])],"derivedFrom":makeQuery(id+"F35.boolean.opBoolean","SPLIT",FACE,{"disambiguationData":[TD([subQ23])],"derivedFrom":makeQuery(id+"F34.boolean.opBoolean","SPLIT",FACE,{"disambiguationData":[TD([subQ23])],"derivedFrom":makeQuery(id+"F33.boolean.opBoolean","SPLIT",FACE,{"disambiguationData":[TD([subQ23])],"derivedFrom":makeQuery(id+"F32.boolean.opBoolean","SPLIT",FACE,{"disambiguationData":[TD([subQ23])],"derivedFrom":makeQuery(id+"F31.boolean.opBoolean","SPLIT",FACE,{"disambiguationData":[TD([subQ23])],"derivedFrom":makeQuery(id+"F30.boolean.opBoolean","SPLIT",FACE,{"disambiguationData":[TD([subQ81])],"derivedFrom":makeQuery(id+"F29.boolean.opBoolean","SPLIT",FACE,{"disambiguationData":[TD([subQ81])],"derivedFrom":makeQuery(id+"F28.boolean.opBoolean","SPLIT",FACE,{"disambiguationData":[TD([subQ81])],"derivedFrom":makeQuery(id+"F27.boolean.opBoolean","SPLIT",FACE,{"disambiguationData":[TD([subQ81])],"derivedFrom":makeQuery(id+"F26.boolean.opBoolean","SPLIT",FACE,{"disambiguationData":[TD([subQ81])],"derivedFrom":makeQuery(id+"F25.boolean.opBoolean","SPLIT",FACE,{"disambiguationData":[TD([subQ81])],"derivedFrom":makeQuery(id+"F24.boolean.opBoolean","SPLIT",FACE,{"disambiguationData":[TD([subQ81])],"derivedFrom":makeQuery(id+"F1.opRevolve","SWEPT_FACE",FACE,{"disambiguationData":[OSD([sQuery(id+"F0.wireOp",EDGE,"E4")])]})})})})})})})})})})})})})})})})})],"blendedInto":[makeQuery(id+"F40.boolean.opBoolean","SPLIT",FACE,{"disambiguationData":[TD([subQ0])],"derivedFrom":makeQuery(id+"F38.boolean.opBoolean","SPLIT",FACE,{"disambiguationData":[TD([subQ15])],"derivedFrom":makeQuery(id+"F37.boolean.opBoolean","SPLIT",FACE,{"disambiguationData":[TD([subQ23])],"derivedFrom":makeQuery(id+"F36.boolean.opBoolean","SPLIT",FACE,{"disambiguationData":[TD([subQ23])],"derivedFrom":makeQuery(id+"F35.boolean.opBoolean","SPLIT",FACE,{"disambiguationData":[TD([subQ23])],"derivedFrom":makeQuery(id+"F34.boolean.opBoolean","SPLIT",FACE,{"disambiguationData":[TD([subQ23])],"derivedFrom":makeQuery(id+"F33.boolean.opBoolean","SPLIT",FACE,{"disambiguationData":[TD([subQ23])],"derivedFrom":makeQuery(id+"F32.boolean.opBoolean","SPLIT",FACE,{"disambiguationData":[TD([subQ23])],"derivedFrom":makeQuery(id+"F31.boolean.opBoolean","SPLIT",FACE,{"disambiguationData":[TD([subQ23])],"derivedFrom":makeQuery(id+"F30.boolean.opBoolean","SPLIT",FACE,{"disambiguationData":[TD([subQ81])],"derivedFrom":makeQuery(id+"F29.boolean.opBoolean","SPLIT",FACE,{"disambiguationData":[TD([subQ81])],"derivedFrom":makeQuery(id+"F28.boolean.opBoolean","SPLIT",FACE,{"disambiguationData":[TD([subQ81])],"derivedFrom":makeQuery(id+"F27.boolean.opBoolean","SPLIT",FACE,{"disambiguationData":[TD([subQ81])],"derivedFrom":makeQuery(id+"F26.boolean.opBoolean","SPLIT",FACE,{"disambiguationData":[TD([subQ81])],"derivedFrom":makeQuery(id+"F25.boolean.opBoolean","SPLIT",FACE,{"disambiguationData":[TD([subQ81])],"derivedFrom":makeQuery(id+"F24.boolean.opBoolean","SPLIT",FACE,{"disambiguationData":[TD([subQ81])],"derivedFrom":makeQuery(id+"F1.opRevolve","SWEPT_FACE",FACE,{"disambiguationData":[OSD([sQuery(id+"F0.wireOp",EDGE,"E4")])]})})})})})})})})})})})})})})})})})]});}
            var Q19;
            {var subQ0=makeQuery(id+"F1.opRevolve","SWEPT_FACE",FACE,{"disambiguationData":[OSD([sQuery(id+"F0.wireOp",EDGE,"E3")])]});var subQ5=sQuery(id+"F3.wireOp",EDGE,"E20.6.3");var subQ6=sQuery(id+"F3.wireOp",EDGE,"E20.6.2");var subQ7=sQuery(id+"F3.wireOp",EDGE,"E20.6.1");var subQ8=makeQuery(id+"F37.opLoft","SWEPT_FACE",FACE,{"disambiguationData":[OSD([subQ7,subQ6,subQ5,sQuery(id+"F22.wireOp",EDGE,"E28.14.0"),sQuery(id+"F22.wireOp",EDGE,"E28.14.2"),sQuery(id+"F22.wireOp",EDGE,"E28.14.3")])]});var subQ9=makeQuery(id+"F40.opExtrude","CAP_FACE",FACE,{"disambiguationData":[OSD([sQuery(id+"F39.wireOp",EDGE,"E29"),sQuery(id+"F39.wireOp",EDGE,"E30")])],"isStart":true});var subQ13=sQuery(id+"F4.wireOp",EDGE,"E26.6.3");var subQ14=sQuery(id+"F4.wireOp",EDGE,"E26.6.2");var subQ15=makeQuery(id+"F15.opLoft","SWEPT_FACE",FACE,{"disambiguationData":[OSD([subQ7,subQ6,subQ5,sQuery(id+"F4.wireOp",EDGE,"E26.6.1"),subQ14,subQ13])]});var subQ20=sQuery(id+"F3.wireOp",EDGE,"E20.7.0");var subQ24=makeQuery(id+"F14.opLoft","CAP_FACE",FACE,{"disambiguationData":[OSD([makeQuery(id+"F3.imprint","IMPRINT",FACE,{"disambiguationData":[TD([[makeQuery(id+"F3.imprint","IMPRINT",EDGE,{"derivedFrom":subQ20}),-1.0]])]})])],"isStart":true});var subQ76=sQuery(id+"F3.wireOp",EDGE,"E18.bottom");var subQ81=makeQuery(id+"F5.opLoft","CAP_FACE",FACE,{"disambiguationData":[OSD([makeQuery(id+"F3.imprint","IMPRINT",FACE,{"disambiguationData":[TD([[makeQuery(id+"F3.imprint","IMPRINT",EDGE,{"derivedFrom":subQ76}),1.0]])]})])],"isStart":true});Q19=makeQuery(id+"F44.opFillet","BLEND_EDGE",EDGE,{"blendedFrom":[makeQuery(id+"F40.boolean.opBoolean","INTERSECT",EDGE,{"derivedFrom":[subQ8,subQ9]}),makeQuery(id+"F40.boolean.opBoolean","SPLIT",FACE,{"disambiguationData":[TD([subQ0])],"derivedFrom":makeQuery(id+"F37.boolean.opBoolean","SPLIT",FACE,{"disambiguationData":[TD([subQ15])],"derivedFrom":makeQuery(id+"F36.boolean.opBoolean","SPLIT",FACE,{"disambiguationData":[TD([subQ24])],"derivedFrom":makeQuery(id+"F35.boolean.opBoolean","SPLIT",FACE,{"disambiguationData":[TD([subQ24])],"derivedFrom":makeQuery(id+"F34.boolean.opBoolean","SPLIT",FACE,{"disambiguationData":[TD([subQ24])],"derivedFrom":makeQuery(id+"F33.boolean.opBoolean","SPLIT",FACE,{"disambiguationData":[TD([subQ24])],"derivedFrom":makeQuery(id+"F32.boolean.opBoolean","SPLIT",FACE,{"disambiguationData":[TD([subQ24])],"derivedFrom":makeQuery(id+"F31.boolean.opBoolean","SPLIT",FACE,{"disambiguationData":[TD([subQ24])],"derivedFrom":makeQuery(id+"F30.boolean.opBoolean","SPLIT",FACE,{"disambiguationData":[TD([subQ81])],"derivedFrom":makeQuery(id+"F29.boolean.opBoolean","SPLIT",FACE,{"disambiguationData":[TD([subQ81])],"derivedFrom":makeQuery(id+"F28.boolean.opBoolean","SPLIT",FACE,{"disambiguationData":[TD([subQ81])],"derivedFrom":makeQuery(id+"F27.boolean.opBoolean","SPLIT",FACE,{"disambiguationData":[TD([subQ81])],"derivedFrom":makeQuery(id+"F26.boolean.opBoolean","SPLIT",FACE,{"disambiguationData":[TD([subQ81])],"derivedFrom":makeQuery(id+"F25.boolean.opBoolean","SPLIT",FACE,{"disambiguationData":[TD([subQ81])],"derivedFrom":makeQuery(id+"F24.boolean.opBoolean","SPLIT",FACE,{"disambiguationData":[TD([subQ81])],"derivedFrom":makeQuery(id+"F1.opRevolve","SWEPT_FACE",FACE,{"disambiguationData":[OSD([sQuery(id+"F0.wireOp",EDGE,"E4")])]})})})})})})})})})})})})})})})})],"blendedInto":[makeQuery(id+"F40.boolean.opBoolean","SPLIT",FACE,{"disambiguationData":[TD([subQ0])],"derivedFrom":makeQuery(id+"F37.boolean.opBoolean","SPLIT",FACE,{"disambiguationData":[TD([subQ15])],"derivedFrom":makeQuery(id+"F36.boolean.opBoolean","SPLIT",FACE,{"disambiguationData":[TD([subQ24])],"derivedFrom":makeQuery(id+"F35.boolean.opBoolean","SPLIT",FACE,{"disambiguationData":[TD([subQ24])],"derivedFrom":makeQuery(id+"F34.boolean.opBoolean","SPLIT",FACE,{"disambiguationData":[TD([subQ24])],"derivedFrom":makeQuery(id+"F33.boolean.opBoolean","SPLIT",FACE,{"disambiguationData":[TD([subQ24])],"derivedFrom":makeQuery(id+"F32.boolean.opBoolean","SPLIT",FACE,{"disambiguationData":[TD([subQ24])],"derivedFrom":makeQuery(id+"F31.boolean.opBoolean","SPLIT",FACE,{"disambiguationData":[TD([subQ24])],"derivedFrom":makeQuery(id+"F30.boolean.opBoolean","SPLIT",FACE,{"disambiguationData":[TD([subQ81])],"derivedFrom":makeQuery(id+"F29.boolean.opBoolean","SPLIT",FACE,{"disambiguationData":[TD([subQ81])],"derivedFrom":makeQuery(id+"F28.boolean.opBoolean","SPLIT",FACE,{"disambiguationData":[TD([subQ81])],"derivedFrom":makeQuery(id+"F27.boolean.opBoolean","SPLIT",FACE,{"disambiguationData":[TD([subQ81])],"derivedFrom":makeQuery(id+"F26.boolean.opBoolean","SPLIT",FACE,{"disambiguationData":[TD([subQ81])],"derivedFrom":makeQuery(id+"F25.boolean.opBoolean","SPLIT",FACE,{"disambiguationData":[TD([subQ81])],"derivedFrom":makeQuery(id+"F24.boolean.opBoolean","SPLIT",FACE,{"disambiguationData":[TD([subQ81])],"derivedFrom":makeQuery(id+"F1.opRevolve","SWEPT_FACE",FACE,{"disambiguationData":[OSD([sQuery(id+"F0.wireOp",EDGE,"E4")])]})})})})})})})})})})})})})})})})]});}
            var Q20;
            {var subQ0=makeQuery(id+"F1.opRevolve","SWEPT_FACE",FACE,{"disambiguationData":[OSD([sQuery(id+"F0.wireOp",EDGE,"E3")])]});var subQ1=sQuery(id+"F3.wireOp",EDGE,"E20.5.3");var subQ2=sQuery(id+"F3.wireOp",EDGE,"E20.5.2");var subQ3=sQuery(id+"F3.wireOp",EDGE,"E20.5.1");var subQ4=makeQuery(id+"F36.opLoft","SWEPT_FACE",FACE,{"disambiguationData":[OSD([subQ3,subQ2,subQ1,sQuery(id+"F22.wireOp",EDGE,"E28.13.0"),sQuery(id+"F22.wireOp",EDGE,"E28.13.2"),sQuery(id+"F22.wireOp",EDGE,"E28.13.3")])]});var subQ9=makeQuery(id+"F40.opExtrude","CAP_FACE",FACE,{"disambiguationData":[OSD([sQuery(id+"F39.wireOp",EDGE,"E29"),sQuery(id+"F39.wireOp",EDGE,"E30")])],"isStart":true});var subQ10=sQuery(id+"F4.wireOp",EDGE,"E26.5.3");var subQ11=sQuery(id+"F4.wireOp",EDGE,"E26.5.2");var subQ12=makeQuery(id+"F16.opLoft","SWEPT_FACE",FACE,{"disambiguationData":[OSD([subQ3,subQ2,subQ1,sQuery(id+"F4.wireOp",EDGE,"E26.5.1"),subQ11,subQ10])]});var subQ27=sQuery(id+"F3.wireOp",EDGE,"E20.7.0");var subQ31=makeQuery(id+"F14.opLoft","CAP_FACE",FACE,{"disambiguationData":[OSD([makeQuery(id+"F3.imprint","IMPRINT",FACE,{"disambiguationData":[TD([[makeQuery(id+"F3.imprint","IMPRINT",EDGE,{"derivedFrom":subQ27}),-1.0]])]})])],"isStart":true});var subQ76=sQuery(id+"F3.wireOp",EDGE,"E18.bottom");var subQ81=makeQuery(id+"F5.opLoft","CAP_FACE",FACE,{"disambiguationData":[OSD([makeQuery(id+"F3.imprint","IMPRINT",FACE,{"disambiguationData":[TD([[makeQuery(id+"F3.imprint","IMPRINT",EDGE,{"derivedFrom":subQ76}),1.0]])]})])],"isStart":true});Q20=makeQuery(id+"F44.opFillet","BLEND_EDGE",EDGE,{"blendedFrom":[makeQuery(id+"F40.boolean.opBoolean","INTERSECT",EDGE,{"derivedFrom":[subQ4,subQ9]}),makeQuery(id+"F40.boolean.opBoolean","SPLIT",FACE,{"disambiguationData":[TD([subQ0])],"derivedFrom":makeQuery(id+"F36.boolean.opBoolean","SPLIT",FACE,{"disambiguationData":[TD([subQ12])],"derivedFrom":makeQuery(id+"F35.boolean.opBoolean","SPLIT",FACE,{"disambiguationData":[TD([subQ31])],"derivedFrom":makeQuery(id+"F34.boolean.opBoolean","SPLIT",FACE,{"disambiguationData":[TD([subQ31])],"derivedFrom":makeQuery(id+"F33.boolean.opBoolean","SPLIT",FACE,{"disambiguationData":[TD([subQ31])],"derivedFrom":makeQuery(id+"F32.boolean.opBoolean","SPLIT",FACE,{"disambiguationData":[TD([subQ31])],"derivedFrom":makeQuery(id+"F31.boolean.opBoolean","SPLIT",FACE,{"disambiguationData":[TD([subQ31])],"derivedFrom":makeQuery(id+"F30.boolean.opBoolean","SPLIT",FACE,{"disambiguationData":[TD([subQ81])],"derivedFrom":makeQuery(id+"F29.boolean.opBoolean","SPLIT",FACE,{"disambiguationData":[TD([subQ81])],"derivedFrom":makeQuery(id+"F28.boolean.opBoolean","SPLIT",FACE,{"disambiguationData":[TD([subQ81])],"derivedFrom":makeQuery(id+"F27.boolean.opBoolean","SPLIT",FACE,{"disambiguationData":[TD([subQ81])],"derivedFrom":makeQuery(id+"F26.boolean.opBoolean","SPLIT",FACE,{"disambiguationData":[TD([subQ81])],"derivedFrom":makeQuery(id+"F25.boolean.opBoolean","SPLIT",FACE,{"disambiguationData":[TD([subQ81])],"derivedFrom":makeQuery(id+"F24.boolean.opBoolean","SPLIT",FACE,{"disambiguationData":[TD([subQ81])],"derivedFrom":makeQuery(id+"F1.opRevolve","SWEPT_FACE",FACE,{"disambiguationData":[OSD([sQuery(id+"F0.wireOp",EDGE,"E4")])]})})})})})})})})})})})})})})})],"blendedInto":[makeQuery(id+"F40.boolean.opBoolean","SPLIT",FACE,{"disambiguationData":[TD([subQ0])],"derivedFrom":makeQuery(id+"F36.boolean.opBoolean","SPLIT",FACE,{"disambiguationData":[TD([subQ12])],"derivedFrom":makeQuery(id+"F35.boolean.opBoolean","SPLIT",FACE,{"disambiguationData":[TD([subQ31])],"derivedFrom":makeQuery(id+"F34.boolean.opBoolean","SPLIT",FACE,{"disambiguationData":[TD([subQ31])],"derivedFrom":makeQuery(id+"F33.boolean.opBoolean","SPLIT",FACE,{"disambiguationData":[TD([subQ31])],"derivedFrom":makeQuery(id+"F32.boolean.opBoolean","SPLIT",FACE,{"disambiguationData":[TD([subQ31])],"derivedFrom":makeQuery(id+"F31.boolean.opBoolean","SPLIT",FACE,{"disambiguationData":[TD([subQ31])],"derivedFrom":makeQuery(id+"F30.boolean.opBoolean","SPLIT",FACE,{"disambiguationData":[TD([subQ81])],"derivedFrom":makeQuery(id+"F29.boolean.opBoolean","SPLIT",FACE,{"disambiguationData":[TD([subQ81])],"derivedFrom":makeQuery(id+"F28.boolean.opBoolean","SPLIT",FACE,{"disambiguationData":[TD([subQ81])],"derivedFrom":makeQuery(id+"F27.boolean.opBoolean","SPLIT",FACE,{"disambiguationData":[TD([subQ81])],"derivedFrom":makeQuery(id+"F26.boolean.opBoolean","SPLIT",FACE,{"disambiguationData":[TD([subQ81])],"derivedFrom":makeQuery(id+"F25.boolean.opBoolean","SPLIT",FACE,{"disambiguationData":[TD([subQ81])],"derivedFrom":makeQuery(id+"F24.boolean.opBoolean","SPLIT",FACE,{"disambiguationData":[TD([subQ81])],"derivedFrom":makeQuery(id+"F1.opRevolve","SWEPT_FACE",FACE,{"disambiguationData":[OSD([sQuery(id+"F0.wireOp",EDGE,"E4")])]})})})})})})})})})})})})})})})]});}
            var Q21;
            {var subQ0=makeQuery(id+"F1.opRevolve","SWEPT_FACE",FACE,{"disambiguationData":[OSD([sQuery(id+"F0.wireOp",EDGE,"E3")])]});var subQ5=sQuery(id+"F3.wireOp",EDGE,"E20.4.3");var subQ6=sQuery(id+"F3.wireOp",EDGE,"E20.4.2");var subQ7=sQuery(id+"F3.wireOp",EDGE,"E20.4.1");var subQ8=makeQuery(id+"F35.opLoft","SWEPT_FACE",FACE,{"disambiguationData":[OSD([subQ7,subQ6,subQ5,sQuery(id+"F22.wireOp",EDGE,"E28.12.0"),sQuery(id+"F22.wireOp",EDGE,"E28.12.2"),sQuery(id+"F22.wireOp",EDGE,"E28.12.3")])]});var subQ9=makeQuery(id+"F40.opExtrude","CAP_FACE",FACE,{"disambiguationData":[OSD([sQuery(id+"F39.wireOp",EDGE,"E29"),sQuery(id+"F39.wireOp",EDGE,"E30")])],"isStart":true});var subQ10=sQuery(id+"F4.wireOp",EDGE,"E26.4.3");var subQ11=sQuery(id+"F4.wireOp",EDGE,"E26.4.2");var subQ12=makeQuery(id+"F17.opLoft","SWEPT_FACE",FACE,{"disambiguationData":[OSD([subQ7,subQ6,subQ5,sQuery(id+"F4.wireOp",EDGE,"E26.4.1"),subQ11,subQ10])]});var subQ33=sQuery(id+"F3.wireOp",EDGE,"E20.7.0");var subQ37=makeQuery(id+"F14.opLoft","CAP_FACE",FACE,{"disambiguationData":[OSD([makeQuery(id+"F3.imprint","IMPRINT",FACE,{"disambiguationData":[TD([[makeQuery(id+"F3.imprint","IMPRINT",EDGE,{"derivedFrom":subQ33}),-1.0]])]})])],"isStart":true});var subQ76=sQuery(id+"F3.wireOp",EDGE,"E18.bottom");var subQ81=makeQuery(id+"F5.opLoft","CAP_FACE",FACE,{"disambiguationData":[OSD([makeQuery(id+"F3.imprint","IMPRINT",FACE,{"disambiguationData":[TD([[makeQuery(id+"F3.imprint","IMPRINT",EDGE,{"derivedFrom":subQ76}),1.0]])]})])],"isStart":true});Q21=makeQuery(id+"F44.opFillet","BLEND_EDGE",EDGE,{"blendedFrom":[makeQuery(id+"F40.boolean.opBoolean","INTERSECT",EDGE,{"derivedFrom":[subQ8,subQ9]}),makeQuery(id+"F40.boolean.opBoolean","SPLIT",FACE,{"disambiguationData":[TD([subQ0])],"derivedFrom":makeQuery(id+"F35.boolean.opBoolean","SPLIT",FACE,{"disambiguationData":[TD([subQ12])],"derivedFrom":makeQuery(id+"F34.boolean.opBoolean","SPLIT",FACE,{"disambiguationData":[TD([subQ37])],"derivedFrom":makeQuery(id+"F33.boolean.opBoolean","SPLIT",FACE,{"disambiguationData":[TD([subQ37])],"derivedFrom":makeQuery(id+"F32.boolean.opBoolean","SPLIT",FACE,{"disambiguationData":[TD([subQ37])],"derivedFrom":makeQuery(id+"F31.boolean.opBoolean","SPLIT",FACE,{"disambiguationData":[TD([subQ37])],"derivedFrom":makeQuery(id+"F30.boolean.opBoolean","SPLIT",FACE,{"disambiguationData":[TD([subQ81])],"derivedFrom":makeQuery(id+"F29.boolean.opBoolean","SPLIT",FACE,{"disambiguationData":[TD([subQ81])],"derivedFrom":makeQuery(id+"F28.boolean.opBoolean","SPLIT",FACE,{"disambiguationData":[TD([subQ81])],"derivedFrom":makeQuery(id+"F27.boolean.opBoolean","SPLIT",FACE,{"disambiguationData":[TD([subQ81])],"derivedFrom":makeQuery(id+"F26.boolean.opBoolean","SPLIT",FACE,{"disambiguationData":[TD([subQ81])],"derivedFrom":makeQuery(id+"F25.boolean.opBoolean","SPLIT",FACE,{"disambiguationData":[TD([subQ81])],"derivedFrom":makeQuery(id+"F24.boolean.opBoolean","SPLIT",FACE,{"disambiguationData":[TD([subQ81])],"derivedFrom":makeQuery(id+"F1.opRevolve","SWEPT_FACE",FACE,{"disambiguationData":[OSD([sQuery(id+"F0.wireOp",EDGE,"E4")])]})})})})})})})})})})})})})})],"blendedInto":[makeQuery(id+"F40.boolean.opBoolean","SPLIT",FACE,{"disambiguationData":[TD([subQ0])],"derivedFrom":makeQuery(id+"F35.boolean.opBoolean","SPLIT",FACE,{"disambiguationData":[TD([subQ12])],"derivedFrom":makeQuery(id+"F34.boolean.opBoolean","SPLIT",FACE,{"disambiguationData":[TD([subQ37])],"derivedFrom":makeQuery(id+"F33.boolean.opBoolean","SPLIT",FACE,{"disambiguationData":[TD([subQ37])],"derivedFrom":makeQuery(id+"F32.boolean.opBoolean","SPLIT",FACE,{"disambiguationData":[TD([subQ37])],"derivedFrom":makeQuery(id+"F31.boolean.opBoolean","SPLIT",FACE,{"disambiguationData":[TD([subQ37])],"derivedFrom":makeQuery(id+"F30.boolean.opBoolean","SPLIT",FACE,{"disambiguationData":[TD([subQ81])],"derivedFrom":makeQuery(id+"F29.boolean.opBoolean","SPLIT",FACE,{"disambiguationData":[TD([subQ81])],"derivedFrom":makeQuery(id+"F28.boolean.opBoolean","SPLIT",FACE,{"disambiguationData":[TD([subQ81])],"derivedFrom":makeQuery(id+"F27.boolean.opBoolean","SPLIT",FACE,{"disambiguationData":[TD([subQ81])],"derivedFrom":makeQuery(id+"F26.boolean.opBoolean","SPLIT",FACE,{"disambiguationData":[TD([subQ81])],"derivedFrom":makeQuery(id+"F25.boolean.opBoolean","SPLIT",FACE,{"disambiguationData":[TD([subQ81])],"derivedFrom":makeQuery(id+"F24.boolean.opBoolean","SPLIT",FACE,{"disambiguationData":[TD([subQ81])],"derivedFrom":makeQuery(id+"F1.opRevolve","SWEPT_FACE",FACE,{"disambiguationData":[OSD([sQuery(id+"F0.wireOp",EDGE,"E4")])]})})})})})})})})})})})})})})]});}
            var Q22;
            {var subQ0=makeQuery(id+"F1.opRevolve","SWEPT_FACE",FACE,{"disambiguationData":[OSD([sQuery(id+"F0.wireOp",EDGE,"E3")])]});var subQ5=makeQuery(id+"F40.opExtrude","CAP_FACE",FACE,{"disambiguationData":[OSD([sQuery(id+"F39.wireOp",EDGE,"E29"),sQuery(id+"F39.wireOp",EDGE,"E30")])],"isStart":true});var subQ6=sQuery(id+"F3.wireOp",EDGE,"E20.3.3");var subQ7=sQuery(id+"F3.wireOp",EDGE,"E20.3.2");var subQ8=sQuery(id+"F3.wireOp",EDGE,"E20.3.1");var subQ9=makeQuery(id+"F34.opLoft","SWEPT_FACE",FACE,{"disambiguationData":[OSD([subQ8,subQ7,subQ6,sQuery(id+"F22.wireOp",EDGE,"E28.11.0"),sQuery(id+"F22.wireOp",EDGE,"E28.11.2"),sQuery(id+"F22.wireOp",EDGE,"E28.11.3")])]});var subQ13=sQuery(id+"F4.wireOp",EDGE,"E26.3.3");var subQ14=sQuery(id+"F4.wireOp",EDGE,"E26.3.2");var subQ15=makeQuery(id+"F18.opLoft","SWEPT_FACE",FACE,{"disambiguationData":[OSD([subQ8,subQ7,subQ6,sQuery(id+"F4.wireOp",EDGE,"E26.3.1"),subQ14,subQ13])]});var subQ36=sQuery(id+"F3.wireOp",EDGE,"E20.7.0");var subQ40=makeQuery(id+"F14.opLoft","CAP_FACE",FACE,{"disambiguationData":[OSD([makeQuery(id+"F3.imprint","IMPRINT",FACE,{"disambiguationData":[TD([[makeQuery(id+"F3.imprint","IMPRINT",EDGE,{"derivedFrom":subQ36}),-1.0]])]})])],"isStart":true});var subQ76=sQuery(id+"F3.wireOp",EDGE,"E18.bottom");var subQ81=makeQuery(id+"F5.opLoft","CAP_FACE",FACE,{"disambiguationData":[OSD([makeQuery(id+"F3.imprint","IMPRINT",FACE,{"disambiguationData":[TD([[makeQuery(id+"F3.imprint","IMPRINT",EDGE,{"derivedFrom":subQ76}),1.0]])]})])],"isStart":true});Q22=makeQuery(id+"F44.opFillet","BLEND_EDGE",EDGE,{"blendedFrom":[makeQuery(id+"F40.boolean.opBoolean","INTERSECT",EDGE,{"derivedFrom":[subQ9,subQ5]}),makeQuery(id+"F40.boolean.opBoolean","SPLIT",FACE,{"disambiguationData":[TD([subQ0])],"derivedFrom":makeQuery(id+"F34.boolean.opBoolean","SPLIT",FACE,{"disambiguationData":[TD([subQ15])],"derivedFrom":makeQuery(id+"F33.boolean.opBoolean","SPLIT",FACE,{"disambiguationData":[TD([subQ40])],"derivedFrom":makeQuery(id+"F32.boolean.opBoolean","SPLIT",FACE,{"disambiguationData":[TD([subQ40])],"derivedFrom":makeQuery(id+"F31.boolean.opBoolean","SPLIT",FACE,{"disambiguationData":[TD([subQ40])],"derivedFrom":makeQuery(id+"F30.boolean.opBoolean","SPLIT",FACE,{"disambiguationData":[TD([subQ81])],"derivedFrom":makeQuery(id+"F29.boolean.opBoolean","SPLIT",FACE,{"disambiguationData":[TD([subQ81])],"derivedFrom":makeQuery(id+"F28.boolean.opBoolean","SPLIT",FACE,{"disambiguationData":[TD([subQ81])],"derivedFrom":makeQuery(id+"F27.boolean.opBoolean","SPLIT",FACE,{"disambiguationData":[TD([subQ81])],"derivedFrom":makeQuery(id+"F26.boolean.opBoolean","SPLIT",FACE,{"disambiguationData":[TD([subQ81])],"derivedFrom":makeQuery(id+"F25.boolean.opBoolean","SPLIT",FACE,{"disambiguationData":[TD([subQ81])],"derivedFrom":makeQuery(id+"F24.boolean.opBoolean","SPLIT",FACE,{"disambiguationData":[TD([subQ81])],"derivedFrom":makeQuery(id+"F1.opRevolve","SWEPT_FACE",FACE,{"disambiguationData":[OSD([sQuery(id+"F0.wireOp",EDGE,"E4")])]})})})})})})})})})})})})})],"blendedInto":[makeQuery(id+"F40.boolean.opBoolean","SPLIT",FACE,{"disambiguationData":[TD([subQ0])],"derivedFrom":makeQuery(id+"F34.boolean.opBoolean","SPLIT",FACE,{"disambiguationData":[TD([subQ15])],"derivedFrom":makeQuery(id+"F33.boolean.opBoolean","SPLIT",FACE,{"disambiguationData":[TD([subQ40])],"derivedFrom":makeQuery(id+"F32.boolean.opBoolean","SPLIT",FACE,{"disambiguationData":[TD([subQ40])],"derivedFrom":makeQuery(id+"F31.boolean.opBoolean","SPLIT",FACE,{"disambiguationData":[TD([subQ40])],"derivedFrom":makeQuery(id+"F30.boolean.opBoolean","SPLIT",FACE,{"disambiguationData":[TD([subQ81])],"derivedFrom":makeQuery(id+"F29.boolean.opBoolean","SPLIT",FACE,{"disambiguationData":[TD([subQ81])],"derivedFrom":makeQuery(id+"F28.boolean.opBoolean","SPLIT",FACE,{"disambiguationData":[TD([subQ81])],"derivedFrom":makeQuery(id+"F27.boolean.opBoolean","SPLIT",FACE,{"disambiguationData":[TD([subQ81])],"derivedFrom":makeQuery(id+"F26.boolean.opBoolean","SPLIT",FACE,{"disambiguationData":[TD([subQ81])],"derivedFrom":makeQuery(id+"F25.boolean.opBoolean","SPLIT",FACE,{"disambiguationData":[TD([subQ81])],"derivedFrom":makeQuery(id+"F24.boolean.opBoolean","SPLIT",FACE,{"disambiguationData":[TD([subQ81])],"derivedFrom":makeQuery(id+"F1.opRevolve","SWEPT_FACE",FACE,{"disambiguationData":[OSD([sQuery(id+"F0.wireOp",EDGE,"E4")])]})})})})})})})})})})})})})]});}
            var Q23;
            {var subQ0=makeQuery(id+"F1.opRevolve","SWEPT_FACE",FACE,{"disambiguationData":[OSD([sQuery(id+"F0.wireOp",EDGE,"E3")])]});var subQ5=sQuery(id+"F3.wireOp",EDGE,"E20.2.3");var subQ6=sQuery(id+"F3.wireOp",EDGE,"E20.2.2");var subQ7=sQuery(id+"F3.wireOp",EDGE,"E20.2.1");var subQ8=makeQuery(id+"F33.opLoft","SWEPT_FACE",FACE,{"disambiguationData":[OSD([subQ7,subQ6,subQ5,sQuery(id+"F22.wireOp",EDGE,"E28.10.0"),sQuery(id+"F22.wireOp",EDGE,"E28.10.2"),sQuery(id+"F22.wireOp",EDGE,"E28.10.3")])]});var subQ9=makeQuery(id+"F40.opExtrude","CAP_FACE",FACE,{"disambiguationData":[OSD([sQuery(id+"F39.wireOp",EDGE,"E29"),sQuery(id+"F39.wireOp",EDGE,"E30")])],"isStart":true});var subQ13=sQuery(id+"F4.wireOp",EDGE,"E26.2.3");var subQ14=sQuery(id+"F4.wireOp",EDGE,"E26.2.2");var subQ15=makeQuery(id+"F19.opLoft","SWEPT_FACE",FACE,{"disambiguationData":[OSD([subQ7,subQ6,subQ5,sQuery(id+"F4.wireOp",EDGE,"E26.2.1"),subQ14,subQ13])]});var subQ56=sQuery(id+"F3.wireOp",EDGE,"E20.7.0");var subQ63=makeQuery(id+"F14.opLoft","CAP_FACE",FACE,{"disambiguationData":[OSD([makeQuery(id+"F3.imprint","IMPRINT",FACE,{"disambiguationData":[TD([[makeQuery(id+"F3.imprint","IMPRINT",EDGE,{"derivedFrom":subQ56}),-1.0]])]})])],"isStart":true});var subQ76=sQuery(id+"F3.wireOp",EDGE,"E18.bottom");var subQ81=makeQuery(id+"F5.opLoft","CAP_FACE",FACE,{"disambiguationData":[OSD([makeQuery(id+"F3.imprint","IMPRINT",FACE,{"disambiguationData":[TD([[makeQuery(id+"F3.imprint","IMPRINT",EDGE,{"derivedFrom":subQ76}),1.0]])]})])],"isStart":true});Q23=makeQuery(id+"F44.opFillet","BLEND_EDGE",EDGE,{"blendedFrom":[makeQuery(id+"F40.boolean.opBoolean","INTERSECT",EDGE,{"derivedFrom":[subQ8,subQ9]}),makeQuery(id+"F40.boolean.opBoolean","SPLIT",FACE,{"disambiguationData":[TD([subQ0])],"derivedFrom":makeQuery(id+"F33.boolean.opBoolean","SPLIT",FACE,{"disambiguationData":[TD([subQ15])],"derivedFrom":makeQuery(id+"F32.boolean.opBoolean","SPLIT",FACE,{"disambiguationData":[TD([subQ63])],"derivedFrom":makeQuery(id+"F31.boolean.opBoolean","SPLIT",FACE,{"disambiguationData":[TD([subQ63])],"derivedFrom":makeQuery(id+"F30.boolean.opBoolean","SPLIT",FACE,{"disambiguationData":[TD([subQ81])],"derivedFrom":makeQuery(id+"F29.boolean.opBoolean","SPLIT",FACE,{"disambiguationData":[TD([subQ81])],"derivedFrom":makeQuery(id+"F28.boolean.opBoolean","SPLIT",FACE,{"disambiguationData":[TD([subQ81])],"derivedFrom":makeQuery(id+"F27.boolean.opBoolean","SPLIT",FACE,{"disambiguationData":[TD([subQ81])],"derivedFrom":makeQuery(id+"F26.boolean.opBoolean","SPLIT",FACE,{"disambiguationData":[TD([subQ81])],"derivedFrom":makeQuery(id+"F25.boolean.opBoolean","SPLIT",FACE,{"disambiguationData":[TD([subQ81])],"derivedFrom":makeQuery(id+"F24.boolean.opBoolean","SPLIT",FACE,{"disambiguationData":[TD([subQ81])],"derivedFrom":makeQuery(id+"F1.opRevolve","SWEPT_FACE",FACE,{"disambiguationData":[OSD([sQuery(id+"F0.wireOp",EDGE,"E4")])]})})})})})})})})})})})})],"blendedInto":[makeQuery(id+"F40.boolean.opBoolean","SPLIT",FACE,{"disambiguationData":[TD([subQ0])],"derivedFrom":makeQuery(id+"F33.boolean.opBoolean","SPLIT",FACE,{"disambiguationData":[TD([subQ15])],"derivedFrom":makeQuery(id+"F32.boolean.opBoolean","SPLIT",FACE,{"disambiguationData":[TD([subQ63])],"derivedFrom":makeQuery(id+"F31.boolean.opBoolean","SPLIT",FACE,{"disambiguationData":[TD([subQ63])],"derivedFrom":makeQuery(id+"F30.boolean.opBoolean","SPLIT",FACE,{"disambiguationData":[TD([subQ81])],"derivedFrom":makeQuery(id+"F29.boolean.opBoolean","SPLIT",FACE,{"disambiguationData":[TD([subQ81])],"derivedFrom":makeQuery(id+"F28.boolean.opBoolean","SPLIT",FACE,{"disambiguationData":[TD([subQ81])],"derivedFrom":makeQuery(id+"F27.boolean.opBoolean","SPLIT",FACE,{"disambiguationData":[TD([subQ81])],"derivedFrom":makeQuery(id+"F26.boolean.opBoolean","SPLIT",FACE,{"disambiguationData":[TD([subQ81])],"derivedFrom":makeQuery(id+"F25.boolean.opBoolean","SPLIT",FACE,{"disambiguationData":[TD([subQ81])],"derivedFrom":makeQuery(id+"F24.boolean.opBoolean","SPLIT",FACE,{"disambiguationData":[TD([subQ81])],"derivedFrom":makeQuery(id+"F1.opRevolve","SWEPT_FACE",FACE,{"disambiguationData":[OSD([sQuery(id+"F0.wireOp",EDGE,"E4")])]})})})})})})})})})})})})]});}
            var Q24;
            {var subQ0=makeQuery(id+"F1.opRevolve","SWEPT_FACE",FACE,{"disambiguationData":[OSD([sQuery(id+"F0.wireOp",EDGE,"E3")])]});var subQ1=sQuery(id+"F3.wireOp",EDGE,"E20.1.3");var subQ2=sQuery(id+"F3.wireOp",EDGE,"E20.1.2");var subQ3=sQuery(id+"F3.wireOp",EDGE,"E20.1.1");var subQ4=makeQuery(id+"F32.opLoft","SWEPT_FACE",FACE,{"disambiguationData":[OSD([subQ3,subQ2,subQ1,sQuery(id+"F22.wireOp",EDGE,"E28.9.0"),sQuery(id+"F22.wireOp",EDGE,"E28.9.2"),sQuery(id+"F22.wireOp",EDGE,"E28.9.3")])]});var subQ5=sQuery(id+"F3.wireOp",EDGE,"E18.left");var subQ6=sQuery(id+"F3.wireOp",EDGE,"E18.top");var subQ7=sQuery(id+"F3.wireOp",EDGE,"E18.bottom");var subQ9=makeQuery(id+"F40.opExtrude","CAP_FACE",FACE,{"disambiguationData":[OSD([sQuery(id+"F39.wireOp",EDGE,"E29"),sQuery(id+"F39.wireOp",EDGE,"E30")])],"isStart":true});var subQ13=sQuery(id+"F4.wireOp",EDGE,"E23");var subQ14=sQuery(id+"F4.wireOp",EDGE,"E22");var subQ15=makeQuery(id+"F5.opLoft","SWEPT_FACE",FACE,{"disambiguationData":[OSD([subQ7,subQ6,subQ5,sQuery(id+"F4.wireOp",EDGE,"E21"),subQ14,subQ13])]});var subQ65=sQuery(id+"F3.wireOp",EDGE,"E20.7.0");var subQ73=makeQuery(id+"F14.opLoft","CAP_FACE",FACE,{"disambiguationData":[OSD([makeQuery(id+"F3.imprint","IMPRINT",FACE,{"disambiguationData":[TD([[makeQuery(id+"F3.imprint","IMPRINT",EDGE,{"derivedFrom":subQ65}),-1.0]])]})])],"isStart":true});var subQ81=makeQuery(id+"F5.opLoft","CAP_FACE",FACE,{"disambiguationData":[OSD([makeQuery(id+"F3.imprint","IMPRINT",FACE,{"disambiguationData":[TD([[makeQuery(id+"F3.imprint","IMPRINT",EDGE,{"derivedFrom":subQ7}),1.0]])]})])],"isStart":true});Q24=makeQuery(id+"F44.opFillet","BLEND_EDGE",EDGE,{"blendedFrom":[makeQuery(id+"F40.boolean.opBoolean","INTERSECT",EDGE,{"derivedFrom":[subQ4,subQ9]}),makeQuery(id+"F40.boolean.opBoolean","SPLIT",FACE,{"disambiguationData":[TD([subQ0])],"derivedFrom":makeQuery(id+"F32.boolean.opBoolean","SPLIT",FACE,{"disambiguationData":[TD([subQ15])],"derivedFrom":makeQuery(id+"F31.boolean.opBoolean","SPLIT",FACE,{"disambiguationData":[TD([subQ73])],"derivedFrom":makeQuery(id+"F30.boolean.opBoolean","SPLIT",FACE,{"disambiguationData":[TD([subQ81])],"derivedFrom":makeQuery(id+"F29.boolean.opBoolean","SPLIT",FACE,{"disambiguationData":[TD([subQ81])],"derivedFrom":makeQuery(id+"F28.boolean.opBoolean","SPLIT",FACE,{"disambiguationData":[TD([subQ81])],"derivedFrom":makeQuery(id+"F27.boolean.opBoolean","SPLIT",FACE,{"disambiguationData":[TD([subQ81])],"derivedFrom":makeQuery(id+"F26.boolean.opBoolean","SPLIT",FACE,{"disambiguationData":[TD([subQ81])],"derivedFrom":makeQuery(id+"F25.boolean.opBoolean","SPLIT",FACE,{"disambiguationData":[TD([subQ81])],"derivedFrom":makeQuery(id+"F24.boolean.opBoolean","SPLIT",FACE,{"disambiguationData":[TD([subQ81])],"derivedFrom":makeQuery(id+"F1.opRevolve","SWEPT_FACE",FACE,{"disambiguationData":[OSD([sQuery(id+"F0.wireOp",EDGE,"E4")])]})})})})})})})})})})})],"blendedInto":[makeQuery(id+"F40.boolean.opBoolean","SPLIT",FACE,{"disambiguationData":[TD([subQ0])],"derivedFrom":makeQuery(id+"F32.boolean.opBoolean","SPLIT",FACE,{"disambiguationData":[TD([subQ15])],"derivedFrom":makeQuery(id+"F31.boolean.opBoolean","SPLIT",FACE,{"disambiguationData":[TD([subQ73])],"derivedFrom":makeQuery(id+"F30.boolean.opBoolean","SPLIT",FACE,{"disambiguationData":[TD([subQ81])],"derivedFrom":makeQuery(id+"F29.boolean.opBoolean","SPLIT",FACE,{"disambiguationData":[TD([subQ81])],"derivedFrom":makeQuery(id+"F28.boolean.opBoolean","SPLIT",FACE,{"disambiguationData":[TD([subQ81])],"derivedFrom":makeQuery(id+"F27.boolean.opBoolean","SPLIT",FACE,{"disambiguationData":[TD([subQ81])],"derivedFrom":makeQuery(id+"F26.boolean.opBoolean","SPLIT",FACE,{"disambiguationData":[TD([subQ81])],"derivedFrom":makeQuery(id+"F25.boolean.opBoolean","SPLIT",FACE,{"disambiguationData":[TD([subQ81])],"derivedFrom":makeQuery(id+"F24.boolean.opBoolean","SPLIT",FACE,{"disambiguationData":[TD([subQ81])],"derivedFrom":makeQuery(id+"F1.opRevolve","SWEPT_FACE",FACE,{"disambiguationData":[OSD([sQuery(id+"F0.wireOp",EDGE,"E4")])]})})})})})})})})})})})]});}
            var Q25;
            {var subQ0=makeQuery(id+"F1.opRevolve","SWEPT_FACE",FACE,{"disambiguationData":[OSD([sQuery(id+"F0.wireOp",EDGE,"E3")])]});var subQ1=sQuery(id+"F3.wireOp",EDGE,"E18.right");var subQ2=sQuery(id+"F3.wireOp",EDGE,"E18.top");var subQ3=sQuery(id+"F3.wireOp",EDGE,"E18.bottom");var subQ4=makeQuery(id+"F31.opLoft","SWEPT_FACE",FACE,{"disambiguationData":[OSD([subQ3,subQ2,subQ1,sQuery(id+"F22.wireOp",EDGE,"E28.8.0"),sQuery(id+"F22.wireOp",EDGE,"E28.8.2"),sQuery(id+"F22.wireOp",EDGE,"E28.8.3")])]});var subQ9=makeQuery(id+"F40.opExtrude","CAP_FACE",FACE,{"disambiguationData":[OSD([sQuery(id+"F39.wireOp",EDGE,"E29"),sQuery(id+"F39.wireOp",EDGE,"E30")])],"isStart":true});var subQ13=sQuery(id+"F4.wireOp",EDGE,"E23");var subQ14=sQuery(id+"F4.wireOp",EDGE,"E22");var subQ15=makeQuery(id+"F5.opLoft","SWEPT_FACE",FACE,{"disambiguationData":[OSD([subQ3,subQ2,subQ1,subQ14,subQ13,sQuery(id+"F4.wireOp",EDGE,"E24")])]});var subQ59=makeQuery(id+"F5.opLoft","CAP_FACE",FACE,{"disambiguationData":[OSD([makeQuery(id+"F3.imprint","IMPRINT",FACE,{"disambiguationData":[TD([[makeQuery(id+"F3.imprint","IMPRINT",EDGE,{"derivedFrom":subQ3}),1.0]])]})])],"isStart":true});Q25=makeQuery(id+"F44.opFillet","BLEND_EDGE",EDGE,{"blendedFrom":[makeQuery(id+"F40.boolean.opBoolean","INTERSECT",EDGE,{"derivedFrom":[subQ4,subQ9]}),makeQuery(id+"F40.boolean.opBoolean","SPLIT",FACE,{"disambiguationData":[TD([subQ0])],"derivedFrom":makeQuery(id+"F31.boolean.opBoolean","SPLIT",FACE,{"disambiguationData":[TD([subQ15])],"derivedFrom":makeQuery(id+"F30.boolean.opBoolean","SPLIT",FACE,{"disambiguationData":[TD([subQ59])],"derivedFrom":makeQuery(id+"F29.boolean.opBoolean","SPLIT",FACE,{"disambiguationData":[TD([subQ59])],"derivedFrom":makeQuery(id+"F28.boolean.opBoolean","SPLIT",FACE,{"disambiguationData":[TD([subQ59])],"derivedFrom":makeQuery(id+"F27.boolean.opBoolean","SPLIT",FACE,{"disambiguationData":[TD([subQ59])],"derivedFrom":makeQuery(id+"F26.boolean.opBoolean","SPLIT",FACE,{"disambiguationData":[TD([subQ59])],"derivedFrom":makeQuery(id+"F25.boolean.opBoolean","SPLIT",FACE,{"disambiguationData":[TD([subQ59])],"derivedFrom":makeQuery(id+"F24.boolean.opBoolean","SPLIT",FACE,{"disambiguationData":[TD([subQ59])],"derivedFrom":makeQuery(id+"F1.opRevolve","SWEPT_FACE",FACE,{"disambiguationData":[OSD([sQuery(id+"F0.wireOp",EDGE,"E4")])]})})})})})})})})})})],"blendedInto":[makeQuery(id+"F40.boolean.opBoolean","SPLIT",FACE,{"disambiguationData":[TD([subQ0])],"derivedFrom":makeQuery(id+"F31.boolean.opBoolean","SPLIT",FACE,{"disambiguationData":[TD([subQ15])],"derivedFrom":makeQuery(id+"F30.boolean.opBoolean","SPLIT",FACE,{"disambiguationData":[TD([subQ59])],"derivedFrom":makeQuery(id+"F29.boolean.opBoolean","SPLIT",FACE,{"disambiguationData":[TD([subQ59])],"derivedFrom":makeQuery(id+"F28.boolean.opBoolean","SPLIT",FACE,{"disambiguationData":[TD([subQ59])],"derivedFrom":makeQuery(id+"F27.boolean.opBoolean","SPLIT",FACE,{"disambiguationData":[TD([subQ59])],"derivedFrom":makeQuery(id+"F26.boolean.opBoolean","SPLIT",FACE,{"disambiguationData":[TD([subQ59])],"derivedFrom":makeQuery(id+"F25.boolean.opBoolean","SPLIT",FACE,{"disambiguationData":[TD([subQ59])],"derivedFrom":makeQuery(id+"F24.boolean.opBoolean","SPLIT",FACE,{"disambiguationData":[TD([subQ59])],"derivedFrom":makeQuery(id+"F1.opRevolve","SWEPT_FACE",FACE,{"disambiguationData":[OSD([sQuery(id+"F0.wireOp",EDGE,"E4")])]})})})})})})})})})})]});}
            var Q26;
            {var subQ0=makeQuery(id+"F1.opRevolve","SWEPT_FACE",FACE,{"disambiguationData":[OSD([sQuery(id+"F0.wireOp",EDGE,"E3")])]});var subQ5=sQuery(id+"F3.wireOp",EDGE,"E20.15.3");var subQ6=sQuery(id+"F3.wireOp",EDGE,"E20.15.2");var subQ7=sQuery(id+"F3.wireOp",EDGE,"E20.15.1");var subQ8=makeQuery(id+"F30.opLoft","SWEPT_FACE",FACE,{"disambiguationData":[OSD([subQ7,subQ6,subQ5,sQuery(id+"F22.wireOp",EDGE,"E28.7.0"),sQuery(id+"F22.wireOp",EDGE,"E28.7.2"),sQuery(id+"F22.wireOp",EDGE,"E28.7.3")])]});var subQ9=makeQuery(id+"F40.opExtrude","CAP_FACE",FACE,{"disambiguationData":[OSD([sQuery(id+"F39.wireOp",EDGE,"E29"),sQuery(id+"F39.wireOp",EDGE,"E30")])],"isStart":true});var subQ10=sQuery(id+"F4.wireOp",EDGE,"E26.15.3");var subQ11=sQuery(id+"F4.wireOp",EDGE,"E26.15.2");var subQ12=makeQuery(id+"F6.opLoft","SWEPT_FACE",FACE,{"disambiguationData":[OSD([subQ7,subQ6,subQ5,sQuery(id+"F4.wireOp",EDGE,"E26.15.1"),subQ11,subQ10])]});var subQ48=sQuery(id+"F3.wireOp",EDGE,"E18.bottom");var subQ51=makeQuery(id+"F5.opLoft","CAP_FACE",FACE,{"disambiguationData":[OSD([makeQuery(id+"F3.imprint","IMPRINT",FACE,{"disambiguationData":[TD([[makeQuery(id+"F3.imprint","IMPRINT",EDGE,{"derivedFrom":subQ48}),1.0]])]})])],"isStart":true});Q26=makeQuery(id+"F44.opFillet","BLEND_EDGE",EDGE,{"blendedFrom":[makeQuery(id+"F40.boolean.opBoolean","INTERSECT",EDGE,{"derivedFrom":[subQ8,subQ9]}),makeQuery(id+"F40.boolean.opBoolean","SPLIT",FACE,{"disambiguationData":[TD([subQ0])],"derivedFrom":makeQuery(id+"F30.boolean.opBoolean","SPLIT",FACE,{"disambiguationData":[TD([subQ12])],"derivedFrom":makeQuery(id+"F29.boolean.opBoolean","SPLIT",FACE,{"disambiguationData":[TD([subQ51])],"derivedFrom":makeQuery(id+"F28.boolean.opBoolean","SPLIT",FACE,{"disambiguationData":[TD([subQ51])],"derivedFrom":makeQuery(id+"F27.boolean.opBoolean","SPLIT",FACE,{"disambiguationData":[TD([subQ51])],"derivedFrom":makeQuery(id+"F26.boolean.opBoolean","SPLIT",FACE,{"disambiguationData":[TD([subQ51])],"derivedFrom":makeQuery(id+"F25.boolean.opBoolean","SPLIT",FACE,{"disambiguationData":[TD([subQ51])],"derivedFrom":makeQuery(id+"F24.boolean.opBoolean","SPLIT",FACE,{"disambiguationData":[TD([subQ51])],"derivedFrom":makeQuery(id+"F1.opRevolve","SWEPT_FACE",FACE,{"disambiguationData":[OSD([sQuery(id+"F0.wireOp",EDGE,"E4")])]})})})})})})})})})],"blendedInto":[makeQuery(id+"F40.boolean.opBoolean","SPLIT",FACE,{"disambiguationData":[TD([subQ0])],"derivedFrom":makeQuery(id+"F30.boolean.opBoolean","SPLIT",FACE,{"disambiguationData":[TD([subQ12])],"derivedFrom":makeQuery(id+"F29.boolean.opBoolean","SPLIT",FACE,{"disambiguationData":[TD([subQ51])],"derivedFrom":makeQuery(id+"F28.boolean.opBoolean","SPLIT",FACE,{"disambiguationData":[TD([subQ51])],"derivedFrom":makeQuery(id+"F27.boolean.opBoolean","SPLIT",FACE,{"disambiguationData":[TD([subQ51])],"derivedFrom":makeQuery(id+"F26.boolean.opBoolean","SPLIT",FACE,{"disambiguationData":[TD([subQ51])],"derivedFrom":makeQuery(id+"F25.boolean.opBoolean","SPLIT",FACE,{"disambiguationData":[TD([subQ51])],"derivedFrom":makeQuery(id+"F24.boolean.opBoolean","SPLIT",FACE,{"disambiguationData":[TD([subQ51])],"derivedFrom":makeQuery(id+"F1.opRevolve","SWEPT_FACE",FACE,{"disambiguationData":[OSD([sQuery(id+"F0.wireOp",EDGE,"E4")])]})})})})})})})})})]});}
            var Q27;
            {var subQ0=makeQuery(id+"F1.opRevolve","SWEPT_FACE",FACE,{"disambiguationData":[OSD([sQuery(id+"F0.wireOp",EDGE,"E3")])]});var subQ5=sQuery(id+"F3.wireOp",EDGE,"E20.14.3");var subQ6=sQuery(id+"F3.wireOp",EDGE,"E20.14.2");var subQ7=sQuery(id+"F3.wireOp",EDGE,"E20.14.1");var subQ8=makeQuery(id+"F29.opLoft","SWEPT_FACE",FACE,{"disambiguationData":[OSD([subQ7,subQ6,subQ5,sQuery(id+"F22.wireOp",EDGE,"E28.6.0"),sQuery(id+"F22.wireOp",EDGE,"E28.6.2"),sQuery(id+"F22.wireOp",EDGE,"E28.6.3")])]});var subQ9=makeQuery(id+"F40.opExtrude","CAP_FACE",FACE,{"disambiguationData":[OSD([sQuery(id+"F39.wireOp",EDGE,"E29"),sQuery(id+"F39.wireOp",EDGE,"E30")])],"isStart":true});var subQ13=sQuery(id+"F4.wireOp",EDGE,"E26.14.3");var subQ14=sQuery(id+"F4.wireOp",EDGE,"E26.14.2");var subQ15=makeQuery(id+"F7.opLoft","SWEPT_FACE",FACE,{"disambiguationData":[OSD([subQ7,subQ6,subQ5,sQuery(id+"F4.wireOp",EDGE,"E26.14.1"),subQ14,subQ13])]});var subQ49=sQuery(id+"F3.wireOp",EDGE,"E18.bottom");var subQ52=makeQuery(id+"F5.opLoft","CAP_FACE",FACE,{"disambiguationData":[OSD([makeQuery(id+"F3.imprint","IMPRINT",FACE,{"disambiguationData":[TD([[makeQuery(id+"F3.imprint","IMPRINT",EDGE,{"derivedFrom":subQ49}),1.0]])]})])],"isStart":true});Q27=makeQuery(id+"F44.opFillet","BLEND_EDGE",EDGE,{"blendedFrom":[makeQuery(id+"F40.boolean.opBoolean","INTERSECT",EDGE,{"derivedFrom":[subQ8,subQ9]}),makeQuery(id+"F40.boolean.opBoolean","SPLIT",FACE,{"disambiguationData":[TD([subQ0])],"derivedFrom":makeQuery(id+"F29.boolean.opBoolean","SPLIT",FACE,{"disambiguationData":[TD([subQ15])],"derivedFrom":makeQuery(id+"F28.boolean.opBoolean","SPLIT",FACE,{"disambiguationData":[TD([subQ52])],"derivedFrom":makeQuery(id+"F27.boolean.opBoolean","SPLIT",FACE,{"disambiguationData":[TD([subQ52])],"derivedFrom":makeQuery(id+"F26.boolean.opBoolean","SPLIT",FACE,{"disambiguationData":[TD([subQ52])],"derivedFrom":makeQuery(id+"F25.boolean.opBoolean","SPLIT",FACE,{"disambiguationData":[TD([subQ52])],"derivedFrom":makeQuery(id+"F24.boolean.opBoolean","SPLIT",FACE,{"disambiguationData":[TD([subQ52])],"derivedFrom":makeQuery(id+"F1.opRevolve","SWEPT_FACE",FACE,{"disambiguationData":[OSD([sQuery(id+"F0.wireOp",EDGE,"E4")])]})})})})})})})})],"blendedInto":[makeQuery(id+"F40.boolean.opBoolean","SPLIT",FACE,{"disambiguationData":[TD([subQ0])],"derivedFrom":makeQuery(id+"F29.boolean.opBoolean","SPLIT",FACE,{"disambiguationData":[TD([subQ15])],"derivedFrom":makeQuery(id+"F28.boolean.opBoolean","SPLIT",FACE,{"disambiguationData":[TD([subQ52])],"derivedFrom":makeQuery(id+"F27.boolean.opBoolean","SPLIT",FACE,{"disambiguationData":[TD([subQ52])],"derivedFrom":makeQuery(id+"F26.boolean.opBoolean","SPLIT",FACE,{"disambiguationData":[TD([subQ52])],"derivedFrom":makeQuery(id+"F25.boolean.opBoolean","SPLIT",FACE,{"disambiguationData":[TD([subQ52])],"derivedFrom":makeQuery(id+"F24.boolean.opBoolean","SPLIT",FACE,{"disambiguationData":[TD([subQ52])],"derivedFrom":makeQuery(id+"F1.opRevolve","SWEPT_FACE",FACE,{"disambiguationData":[OSD([sQuery(id+"F0.wireOp",EDGE,"E4")])]})})})})})})})})]});}
            var Q28;
            {var subQ0=makeQuery(id+"F1.opRevolve","SWEPT_FACE",FACE,{"disambiguationData":[OSD([sQuery(id+"F0.wireOp",EDGE,"E3")])]});var subQ5=sQuery(id+"F3.wireOp",EDGE,"E20.13.3");var subQ6=sQuery(id+"F3.wireOp",EDGE,"E20.13.2");var subQ7=sQuery(id+"F3.wireOp",EDGE,"E20.13.1");var subQ8=makeQuery(id+"F28.opLoft","SWEPT_FACE",FACE,{"disambiguationData":[OSD([subQ7,subQ6,subQ5,sQuery(id+"F22.wireOp",EDGE,"E28.5.0"),sQuery(id+"F22.wireOp",EDGE,"E28.5.2"),sQuery(id+"F22.wireOp",EDGE,"E28.5.3")])]});var subQ9=makeQuery(id+"F40.opExtrude","CAP_FACE",FACE,{"disambiguationData":[OSD([sQuery(id+"F39.wireOp",EDGE,"E29"),sQuery(id+"F39.wireOp",EDGE,"E30")])],"isStart":true});var subQ13=sQuery(id+"F4.wireOp",EDGE,"E26.13.3");var subQ14=sQuery(id+"F4.wireOp",EDGE,"E26.13.2");var subQ15=makeQuery(id+"F8.opLoft","SWEPT_FACE",FACE,{"disambiguationData":[OSD([subQ7,subQ6,subQ5,sQuery(id+"F4.wireOp",EDGE,"E26.13.1"),subQ14,subQ13])]});var subQ57=sQuery(id+"F3.wireOp",EDGE,"E18.bottom");var subQ60=makeQuery(id+"F5.opLoft","CAP_FACE",FACE,{"disambiguationData":[OSD([makeQuery(id+"F3.imprint","IMPRINT",FACE,{"disambiguationData":[TD([[makeQuery(id+"F3.imprint","IMPRINT",EDGE,{"derivedFrom":subQ57}),1.0]])]})])],"isStart":true});Q28=makeQuery(id+"F44.opFillet","BLEND_EDGE",EDGE,{"blendedFrom":[makeQuery(id+"F40.boolean.opBoolean","INTERSECT",EDGE,{"derivedFrom":[subQ8,subQ9]}),makeQuery(id+"F40.boolean.opBoolean","SPLIT",FACE,{"disambiguationData":[TD([subQ0])],"derivedFrom":makeQuery(id+"F28.boolean.opBoolean","SPLIT",FACE,{"disambiguationData":[TD([subQ15])],"derivedFrom":makeQuery(id+"F27.boolean.opBoolean","SPLIT",FACE,{"disambiguationData":[TD([subQ60])],"derivedFrom":makeQuery(id+"F26.boolean.opBoolean","SPLIT",FACE,{"disambiguationData":[TD([subQ60])],"derivedFrom":makeQuery(id+"F25.boolean.opBoolean","SPLIT",FACE,{"disambiguationData":[TD([subQ60])],"derivedFrom":makeQuery(id+"F24.boolean.opBoolean","SPLIT",FACE,{"disambiguationData":[TD([subQ60])],"derivedFrom":makeQuery(id+"F1.opRevolve","SWEPT_FACE",FACE,{"disambiguationData":[OSD([sQuery(id+"F0.wireOp",EDGE,"E4")])]})})})})})})})],"blendedInto":[makeQuery(id+"F40.boolean.opBoolean","SPLIT",FACE,{"disambiguationData":[TD([subQ0])],"derivedFrom":makeQuery(id+"F28.boolean.opBoolean","SPLIT",FACE,{"disambiguationData":[TD([subQ15])],"derivedFrom":makeQuery(id+"F27.boolean.opBoolean","SPLIT",FACE,{"disambiguationData":[TD([subQ60])],"derivedFrom":makeQuery(id+"F26.boolean.opBoolean","SPLIT",FACE,{"disambiguationData":[TD([subQ60])],"derivedFrom":makeQuery(id+"F25.boolean.opBoolean","SPLIT",FACE,{"disambiguationData":[TD([subQ60])],"derivedFrom":makeQuery(id+"F24.boolean.opBoolean","SPLIT",FACE,{"disambiguationData":[TD([subQ60])],"derivedFrom":makeQuery(id+"F1.opRevolve","SWEPT_FACE",FACE,{"disambiguationData":[OSD([sQuery(id+"F0.wireOp",EDGE,"E4")])]})})})})})})})]});}
            var Q29;
            {var subQ0=makeQuery(id+"F1.opRevolve","SWEPT_FACE",FACE,{"disambiguationData":[OSD([sQuery(id+"F0.wireOp",EDGE,"E3")])]});var subQ5=sQuery(id+"F3.wireOp",EDGE,"E20.12.3");var subQ6=sQuery(id+"F3.wireOp",EDGE,"E20.12.2");var subQ7=sQuery(id+"F3.wireOp",EDGE,"E20.12.1");var subQ8=makeQuery(id+"F27.opLoft","SWEPT_FACE",FACE,{"disambiguationData":[OSD([subQ7,subQ6,subQ5,sQuery(id+"F22.wireOp",EDGE,"E28.4.0"),sQuery(id+"F22.wireOp",EDGE,"E28.4.2"),sQuery(id+"F22.wireOp",EDGE,"E28.4.3")])]});var subQ9=makeQuery(id+"F40.opExtrude","CAP_FACE",FACE,{"disambiguationData":[OSD([sQuery(id+"F39.wireOp",EDGE,"E29"),sQuery(id+"F39.wireOp",EDGE,"E30")])],"isStart":true});var subQ13=sQuery(id+"F4.wireOp",EDGE,"E26.12.3");var subQ14=sQuery(id+"F4.wireOp",EDGE,"E26.12.2");var subQ15=makeQuery(id+"F9.opLoft","SWEPT_FACE",FACE,{"disambiguationData":[OSD([subQ7,subQ6,subQ5,sQuery(id+"F4.wireOp",EDGE,"E26.12.1"),subQ14,subQ13])]});var subQ75=sQuery(id+"F3.wireOp",EDGE,"E18.bottom");var subQ78=makeQuery(id+"F5.opLoft","CAP_FACE",FACE,{"disambiguationData":[OSD([makeQuery(id+"F3.imprint","IMPRINT",FACE,{"disambiguationData":[TD([[makeQuery(id+"F3.imprint","IMPRINT",EDGE,{"derivedFrom":subQ75}),1.0]])]})])],"isStart":true});Q29=makeQuery(id+"F44.opFillet","BLEND_EDGE",EDGE,{"blendedFrom":[makeQuery(id+"F40.boolean.opBoolean","INTERSECT",EDGE,{"derivedFrom":[subQ8,subQ9]}),makeQuery(id+"F40.boolean.opBoolean","SPLIT",FACE,{"disambiguationData":[TD([subQ0])],"derivedFrom":makeQuery(id+"F27.boolean.opBoolean","SPLIT",FACE,{"disambiguationData":[TD([subQ15])],"derivedFrom":makeQuery(id+"F26.boolean.opBoolean","SPLIT",FACE,{"disambiguationData":[TD([subQ78])],"derivedFrom":makeQuery(id+"F25.boolean.opBoolean","SPLIT",FACE,{"disambiguationData":[TD([subQ78])],"derivedFrom":makeQuery(id+"F24.boolean.opBoolean","SPLIT",FACE,{"disambiguationData":[TD([subQ78])],"derivedFrom":makeQuery(id+"F1.opRevolve","SWEPT_FACE",FACE,{"disambiguationData":[OSD([sQuery(id+"F0.wireOp",EDGE,"E4")])]})})})})})})],"blendedInto":[makeQuery(id+"F40.boolean.opBoolean","SPLIT",FACE,{"disambiguationData":[TD([subQ0])],"derivedFrom":makeQuery(id+"F27.boolean.opBoolean","SPLIT",FACE,{"disambiguationData":[TD([subQ15])],"derivedFrom":makeQuery(id+"F26.boolean.opBoolean","SPLIT",FACE,{"disambiguationData":[TD([subQ78])],"derivedFrom":makeQuery(id+"F25.boolean.opBoolean","SPLIT",FACE,{"disambiguationData":[TD([subQ78])],"derivedFrom":makeQuery(id+"F24.boolean.opBoolean","SPLIT",FACE,{"disambiguationData":[TD([subQ78])],"derivedFrom":makeQuery(id+"F1.opRevolve","SWEPT_FACE",FACE,{"disambiguationData":[OSD([sQuery(id+"F0.wireOp",EDGE,"E4")])]})})})})})})]});}
            var Q30;
            {var subQ0=makeQuery(id+"F1.opRevolve","SWEPT_FACE",FACE,{"disambiguationData":[OSD([sQuery(id+"F0.wireOp",EDGE,"E3")])]});var subQ5=sQuery(id+"F3.wireOp",EDGE,"E20.11.3");var subQ6=sQuery(id+"F3.wireOp",EDGE,"E20.11.2");var subQ7=sQuery(id+"F3.wireOp",EDGE,"E20.11.1");var subQ8=makeQuery(id+"F26.opLoft","SWEPT_FACE",FACE,{"disambiguationData":[OSD([subQ7,subQ6,subQ5,sQuery(id+"F22.wireOp",EDGE,"E28.3.0"),sQuery(id+"F22.wireOp",EDGE,"E28.3.2"),sQuery(id+"F22.wireOp",EDGE,"E28.3.3")])]});var subQ9=makeQuery(id+"F40.opExtrude","CAP_FACE",FACE,{"disambiguationData":[OSD([sQuery(id+"F39.wireOp",EDGE,"E29"),sQuery(id+"F39.wireOp",EDGE,"E30")])],"isStart":true});var subQ13=sQuery(id+"F4.wireOp",EDGE,"E26.11.3");var subQ14=sQuery(id+"F4.wireOp",EDGE,"E26.11.2");var subQ15=makeQuery(id+"F10.opLoft","SWEPT_FACE",FACE,{"disambiguationData":[OSD([subQ7,subQ6,subQ5,sQuery(id+"F4.wireOp",EDGE,"E26.11.1"),subQ14,subQ13])]});var subQ80=sQuery(id+"F3.wireOp",EDGE,"E18.bottom");var subQ83=makeQuery(id+"F5.opLoft","CAP_FACE",FACE,{"disambiguationData":[OSD([makeQuery(id+"F3.imprint","IMPRINT",FACE,{"disambiguationData":[TD([[makeQuery(id+"F3.imprint","IMPRINT",EDGE,{"derivedFrom":subQ80}),1.0]])]})])],"isStart":true});Q30=makeQuery(id+"F44.opFillet","BLEND_EDGE",EDGE,{"blendedFrom":[makeQuery(id+"F40.boolean.opBoolean","INTERSECT",EDGE,{"derivedFrom":[subQ8,subQ9]}),makeQuery(id+"F40.boolean.opBoolean","SPLIT",FACE,{"disambiguationData":[TD([subQ0])],"derivedFrom":makeQuery(id+"F26.boolean.opBoolean","SPLIT",FACE,{"disambiguationData":[TD([subQ15])],"derivedFrom":makeQuery(id+"F25.boolean.opBoolean","SPLIT",FACE,{"disambiguationData":[TD([subQ83])],"derivedFrom":makeQuery(id+"F24.boolean.opBoolean","SPLIT",FACE,{"disambiguationData":[TD([subQ83])],"derivedFrom":makeQuery(id+"F1.opRevolve","SWEPT_FACE",FACE,{"disambiguationData":[OSD([sQuery(id+"F0.wireOp",EDGE,"E4")])]})})})})})],"blendedInto":[makeQuery(id+"F40.boolean.opBoolean","SPLIT",FACE,{"disambiguationData":[TD([subQ0])],"derivedFrom":makeQuery(id+"F26.boolean.opBoolean","SPLIT",FACE,{"disambiguationData":[TD([subQ15])],"derivedFrom":makeQuery(id+"F25.boolean.opBoolean","SPLIT",FACE,{"disambiguationData":[TD([subQ83])],"derivedFrom":makeQuery(id+"F24.boolean.opBoolean","SPLIT",FACE,{"disambiguationData":[TD([subQ83])],"derivedFrom":makeQuery(id+"F1.opRevolve","SWEPT_FACE",FACE,{"disambiguationData":[OSD([sQuery(id+"F0.wireOp",EDGE,"E4")])]})})})})})]});}
            var Q31;
            {var subQ0=makeQuery(id+"F1.opRevolve","SWEPT_FACE",FACE,{"disambiguationData":[OSD([sQuery(id+"F0.wireOp",EDGE,"E3")])]});var subQ5=sQuery(id+"F3.wireOp",EDGE,"E20.10.3");var subQ6=sQuery(id+"F3.wireOp",EDGE,"E20.10.2");var subQ7=sQuery(id+"F3.wireOp",EDGE,"E20.10.1");var subQ8=makeQuery(id+"F25.opLoft","SWEPT_FACE",FACE,{"disambiguationData":[OSD([subQ7,subQ6,subQ5,sQuery(id+"F22.wireOp",EDGE,"E28.2.0"),sQuery(id+"F22.wireOp",EDGE,"E28.2.2"),sQuery(id+"F22.wireOp",EDGE,"E28.2.3")])]});var subQ9=makeQuery(id+"F40.opExtrude","CAP_FACE",FACE,{"disambiguationData":[OSD([sQuery(id+"F39.wireOp",EDGE,"E29"),sQuery(id+"F39.wireOp",EDGE,"E30")])],"isStart":true});var subQ12=sQuery(id+"F4.wireOp",EDGE,"E26.10.3");var subQ13=sQuery(id+"F4.wireOp",EDGE,"E26.10.2");var subQ14=makeQuery(id+"F11.opLoft","SWEPT_FACE",FACE,{"disambiguationData":[OSD([subQ7,subQ6,subQ5,sQuery(id+"F4.wireOp",EDGE,"E26.10.1"),subQ13,subQ12])]});var subQ90=sQuery(id+"F3.wireOp",EDGE,"E18.bottom");Q31=makeQuery(id+"F44.opFillet","BLEND_EDGE",EDGE,{"blendedFrom":[makeQuery(id+"F40.boolean.opBoolean","INTERSECT",EDGE,{"derivedFrom":[subQ8,subQ9]}),makeQuery(id+"F40.boolean.opBoolean","SPLIT",FACE,{"disambiguationData":[TD([subQ0])],"derivedFrom":makeQuery(id+"F25.boolean.opBoolean","SPLIT",FACE,{"disambiguationData":[TD([subQ14])],"derivedFrom":makeQuery(id+"F24.boolean.opBoolean","SPLIT",FACE,{"disambiguationData":[TD([makeQuery(id+"F5.opLoft","CAP_FACE",FACE,{"disambiguationData":[OSD([makeQuery(id+"F3.imprint","IMPRINT",FACE,{"disambiguationData":[TD([[makeQuery(id+"F3.imprint","IMPRINT",EDGE,{"derivedFrom":subQ90}),1.0]])]})])],"isStart":true})])],"derivedFrom":makeQuery(id+"F1.opRevolve","SWEPT_FACE",FACE,{"disambiguationData":[OSD([sQuery(id+"F0.wireOp",EDGE,"E4")])]})})})})],"blendedInto":[makeQuery(id+"F40.boolean.opBoolean","SPLIT",FACE,{"disambiguationData":[TD([subQ0])],"derivedFrom":makeQuery(id+"F25.boolean.opBoolean","SPLIT",FACE,{"disambiguationData":[TD([subQ14])],"derivedFrom":makeQuery(id+"F24.boolean.opBoolean","SPLIT",FACE,{"disambiguationData":[TD([makeQuery(id+"F5.opLoft","CAP_FACE",FACE,{"disambiguationData":[OSD([makeQuery(id+"F3.imprint","IMPRINT",FACE,{"disambiguationData":[TD([[makeQuery(id+"F3.imprint","IMPRINT",EDGE,{"derivedFrom":subQ90}),1.0]])]})])],"isStart":true})])],"derivedFrom":makeQuery(id+"F1.opRevolve","SWEPT_FACE",FACE,{"disambiguationData":[OSD([sQuery(id+"F0.wireOp",EDGE,"E4")])]})})})})]});}
            var Q32;
            {var subQ0=makeQuery(id+"F1.opRevolve","SWEPT_FACE",FACE,{"disambiguationData":[OSD([sQuery(id+"F0.wireOp",EDGE,"E3")])]});var subQ1=sQuery(id+"F3.wireOp",EDGE,"E20.9.3");var subQ2=sQuery(id+"F3.wireOp",EDGE,"E20.9.2");var subQ3=sQuery(id+"F3.wireOp",EDGE,"E20.9.1");var subQ4=makeQuery(id+"F24.opLoft","SWEPT_FACE",FACE,{"disambiguationData":[OSD([subQ3,subQ2,subQ1,sQuery(id+"F22.wireOp",EDGE,"E28.1.0"),sQuery(id+"F22.wireOp",EDGE,"E28.1.2"),sQuery(id+"F22.wireOp",EDGE,"E28.1.3")])]});var subQ9=makeQuery(id+"F40.opExtrude","CAP_FACE",FACE,{"disambiguationData":[OSD([sQuery(id+"F39.wireOp",EDGE,"E29"),sQuery(id+"F39.wireOp",EDGE,"E30")])],"isStart":true});Q32=makeQuery(id+"F44.opFillet","BLEND_EDGE",EDGE,{"blendedFrom":[makeQuery(id+"F40.boolean.opBoolean","INTERSECT",EDGE,{"derivedFrom":[subQ4,subQ9]}),makeQuery(id+"F40.boolean.opBoolean","SPLIT",FACE,{"disambiguationData":[TD([subQ0])],"derivedFrom":makeQuery(id+"F24.boolean.opBoolean","SPLIT",FACE,{"disambiguationData":[TD([makeQuery(id+"F12.opLoft","SWEPT_FACE",FACE,{"disambiguationData":[OSD([subQ3,subQ2,subQ1,sQuery(id+"F4.wireOp",EDGE,"E26.9.1"),sQuery(id+"F4.wireOp",EDGE,"E26.9.2"),sQuery(id+"F4.wireOp",EDGE,"E26.9.3")])]})])],"derivedFrom":makeQuery(id+"F1.opRevolve","SWEPT_FACE",FACE,{"disambiguationData":[OSD([sQuery(id+"F0.wireOp",EDGE,"E4")])]})})})],"blendedInto":[makeQuery(id+"F40.boolean.opBoolean","SPLIT",FACE,{"disambiguationData":[TD([subQ0])],"derivedFrom":makeQuery(id+"F24.boolean.opBoolean","SPLIT",FACE,{"disambiguationData":[TD([makeQuery(id+"F12.opLoft","SWEPT_FACE",FACE,{"disambiguationData":[OSD([subQ3,subQ2,subQ1,sQuery(id+"F4.wireOp",EDGE,"E26.9.1"),sQuery(id+"F4.wireOp",EDGE,"E26.9.2"),sQuery(id+"F4.wireOp",EDGE,"E26.9.3")])]})])],"derivedFrom":makeQuery(id+"F1.opRevolve","SWEPT_FACE",FACE,{"disambiguationData":[OSD([sQuery(id+"F0.wireOp",EDGE,"E4")])]})})})]});}
            fillet(context, id + "F48", {"entities" : qUnion([Q0, Q1, Q2, Q3, Q4, Q5, Q6, Q7, Q8, Q9, Q10, Q11, Q12, Q13, Q14, Q15, Q16, Q17, Q18, Q19, Q20, Q21, Q22, Q23, Q24, Q25, Q26, Q27, Q28, Q29, Q30, Q31, Q32]), "radius" : 2 * mm, "tangentPropagation" : true, "allowEdgeOverflow" : false});
        }
        {
            var Q0;
            {var subQ0=sQuery(id+"F41.wireOp",EDGE,"E34");var subQ1=sQuery(id+"F41.wireOp",EDGE,"E32");Q0=makeQuery(id+"F42.boolean.opBoolean","INTERSECT",EDGE,{"derivedFrom":[makeQuery(id+"F35.opLoft","SWEPT_FACE",FACE,{"disambiguationData":[OSD([sQuery(id+"F3.wireOp",EDGE,"E20.4.0"),sQuery(id+"F3.wireOp",EDGE,"E20.4.1"),sQuery(id+"F3.wireOp",EDGE,"E20.4.3"),sQuery(id+"F22.wireOp",EDGE,"E28.12.1"),sQuery(id+"F22.wireOp",EDGE,"E28.12.2"),sQuery(id+"F22.wireOp",EDGE,"E28.12.3")])]}),makeQuery(id+"F42.opRevolve","SWEPT_FACE",FACE,{"disambiguationData":[OSD([subQ1]),TDD([makeQuery(id+"F41.imprint","IMPRINT",EDGE,{"disambiguationData":[TD([[makeQuery(id+"F41.imprint","INTERSECT",VERTEX,{"disambiguationData":[OD(0.0)],"derivedFrom":[subQ1,subQ0]}),-1.0]])],"derivedFrom":subQ1})])]})]});}
            var Q1;
            {var subQ0=sQuery(id+"F22.wireOp",EDGE,"E28.12.3");var subQ1=sQuery(id+"F22.wireOp",EDGE,"E28.12.2");var subQ2=sQuery(id+"F22.wireOp",EDGE,"E28.12.0");var subQ3=sQuery(id+"F3.wireOp",EDGE,"E20.4.3");var subQ4=sQuery(id+"F3.wireOp",EDGE,"E20.4.1");var subQ5=makeQuery(id+"F35.opLoft","SWEPT_FACE",FACE,{"disambiguationData":[OSD([subQ4,sQuery(id+"F3.wireOp",EDGE,"E20.4.2"),subQ3,subQ2,subQ1,subQ0])]});var subQ6=sQuery(id+"F22.wireOp",EDGE,"E28.12.1");var subQ7=sQuery(id+"F41.wireOp",EDGE,"E34");var subQ8=sQuery(id+"F41.wireOp",EDGE,"E32");Q1=makeQuery(id+"F44.opFillet","BLEND_EDGE",EDGE,{"blendedFrom":[makeQuery(id+"F40.boolean.opBoolean","INTERSECT",EDGE,{"derivedFrom":[subQ5,makeQuery(id+"F40.opExtrude","CAP_FACE",FACE,{"disambiguationData":[OSD([sQuery(id+"F39.wireOp",EDGE,"E29"),sQuery(id+"F39.wireOp",EDGE,"E30")])],"isStart":true})]}),makeQuery(id+"F42.boolean.opBoolean","COPY",FACE,{"disambiguationData":[TD([makeQuery(id+"F35.opLoft","SWEPT_FACE",FACE,{"disambiguationData":[OSD([sQuery(id+"F3.wireOp",EDGE,"E20.4.0"),subQ4,subQ3,subQ6,subQ1,subQ0])]})])],"derivedFrom":makeQuery(id+"F42.opRevolve","SWEPT_FACE",FACE,{"disambiguationData":[OSD([subQ8]),TDD([makeQuery(id+"F41.imprint","IMPRINT",EDGE,{"disambiguationData":[TD([[makeQuery(id+"F41.imprint","INTERSECT",VERTEX,{"disambiguationData":[OD(0.0)],"derivedFrom":[subQ8,subQ7]}),-1.0]])],"derivedFrom":subQ8})])]})})],"blendedInto":[makeQuery(id+"F42.boolean.opBoolean","COPY",FACE,{"disambiguationData":[TD([makeQuery(id+"F35.opLoft","SWEPT_FACE",FACE,{"disambiguationData":[OSD([sQuery(id+"F3.wireOp",EDGE,"E20.4.0"),subQ4,subQ3,subQ6,subQ1,subQ0])]})])],"derivedFrom":makeQuery(id+"F42.opRevolve","SWEPT_FACE",FACE,{"disambiguationData":[OSD([subQ8]),TDD([makeQuery(id+"F41.imprint","IMPRINT",EDGE,{"disambiguationData":[TD([[makeQuery(id+"F41.imprint","INTERSECT",VERTEX,{"disambiguationData":[OD(0.0)],"derivedFrom":[subQ8,subQ7]}),-1.0]])],"derivedFrom":subQ8})])]})})]});}
            var Q2;
            {var subQ0=sQuery(id+"F41.wireOp",EDGE,"E37");var subQ1=makeQuery(id+"F42.opRevolve","SWEPT_FACE",FACE,{"disambiguationData":[OSD([subQ0])]});var subQ2=makeQuery(id+"F40.opExtrude","CAP_FACE",FACE,{"disambiguationData":[OSD([sQuery(id+"F39.wireOp",EDGE,"E29"),sQuery(id+"F39.wireOp",EDGE,"E30")])],"isStart":true});var subQ3=sQuery(id+"F22.wireOp",EDGE,"E28.15.3");var subQ4=sQuery(id+"F22.wireOp",EDGE,"E28.15.2");var subQ5=sQuery(id+"F3.wireOp",EDGE,"E20.7.3");var subQ7=sQuery(id+"F3.wireOp",EDGE,"E20.7.1");var subQ8=sQuery(id+"F3.wireOp",EDGE,"E20.7.0");var subQ9=sQuery(id+"F41.wireOp",EDGE,"E38");var subQ10=makeQuery(id+"F42.opRevolve","SWEPT_FACE",FACE,{"disambiguationData":[OSD([subQ9])]});var subQ11=makeQuery(id+"F42.opRevolve","SWEPT_EDGE",EDGE,{"disambiguationData":[OSD([subQ0,subQ9])]});var subQ12=sQuery(id+"F22.wireOp",EDGE,"E28.14.3");var subQ13=sQuery(id+"F22.wireOp",EDGE,"E28.14.2");var subQ14=sQuery(id+"F3.wireOp",EDGE,"E20.6.3");var subQ15=sQuery(id+"F3.wireOp",EDGE,"E20.6.1");var subQ16=sQuery(id+"F3.wireOp",EDGE,"E20.6.0");var subQ18=sQuery(id+"F22.wireOp",EDGE,"E28.13.3");var subQ19=sQuery(id+"F22.wireOp",EDGE,"E28.13.2");var subQ20=sQuery(id+"F3.wireOp",EDGE,"E20.5.3");var subQ22=sQuery(id+"F3.wireOp",EDGE,"E20.5.1");var subQ23=sQuery(id+"F3.wireOp",EDGE,"E20.5.0");var subQ24=sQuery(id+"F22.wireOp",EDGE,"E28.12.3");var subQ25=sQuery(id+"F22.wireOp",EDGE,"E28.12.2");var subQ26=sQuery(id+"F3.wireOp",EDGE,"E20.4.3");var subQ28=sQuery(id+"F3.wireOp",EDGE,"E20.4.1");var subQ30=sQuery(id+"F3.wireOp",EDGE,"E20.4.0");var subQ31=makeQuery(id+"F35.opLoft","SWEPT_FACE",FACE,{"disambiguationData":[OSD([subQ30,subQ28,subQ26,sQuery(id+"F22.wireOp",EDGE,"E28.12.1"),subQ25,subQ24])]});var subQ32=sQuery(id+"F22.wireOp",EDGE,"E28.11.3");var subQ33=sQuery(id+"F22.wireOp",EDGE,"E28.11.2");var subQ34=sQuery(id+"F3.wireOp",EDGE,"E20.3.3");var subQ36=sQuery(id+"F3.wireOp",EDGE,"E20.3.1");var subQ37=sQuery(id+"F3.wireOp",EDGE,"E20.3.0");var subQ38=makeQuery(id+"F34.opLoft","SWEPT_FACE",FACE,{"disambiguationData":[OSD([subQ37,subQ36,subQ34,sQuery(id+"F22.wireOp",EDGE,"E28.11.1"),subQ33,subQ32])]});var subQ39=sQuery(id+"F22.wireOp",EDGE,"E28.10.3");var subQ40=sQuery(id+"F22.wireOp",EDGE,"E28.10.2");var subQ41=sQuery(id+"F3.wireOp",EDGE,"E20.2.3");var subQ43=sQuery(id+"F3.wireOp",EDGE,"E20.2.1");var subQ44=sQuery(id+"F3.wireOp",EDGE,"E20.2.0");var subQ45=makeQuery(id+"F33.opLoft","SWEPT_FACE",FACE,{"disambiguationData":[OSD([subQ44,subQ43,subQ41,sQuery(id+"F22.wireOp",EDGE,"E28.10.1"),subQ40,subQ39])]});var subQ46=sQuery(id+"F22.wireOp",EDGE,"E28.9.3");var subQ47=sQuery(id+"F22.wireOp",EDGE,"E28.9.2");var subQ48=sQuery(id+"F3.wireOp",EDGE,"E20.1.3");var subQ50=sQuery(id+"F3.wireOp",EDGE,"E20.1.1");var subQ51=sQuery(id+"F3.wireOp",EDGE,"E20.1.0");var subQ52=makeQuery(id+"F32.opLoft","SWEPT_FACE",FACE,{"disambiguationData":[OSD([subQ51,subQ50,subQ48,sQuery(id+"F22.wireOp",EDGE,"E28.9.1"),subQ47,subQ46])]});var subQ53=sQuery(id+"F22.wireOp",EDGE,"E28.8.3");var subQ54=sQuery(id+"F22.wireOp",EDGE,"E28.8.2");var subQ56=sQuery(id+"F3.wireOp",EDGE,"E18.top");var subQ57=sQuery(id+"F3.wireOp",EDGE,"E18.bottom");var subQ58=sQuery(id+"F3.wireOp",EDGE,"E18.left");var subQ59=makeQuery(id+"F31.opLoft","SWEPT_FACE",FACE,{"disambiguationData":[OSD([subQ57,subQ56,subQ58,sQuery(id+"F22.wireOp",EDGE,"E28.8.1"),subQ54,subQ53])]});var subQ60=sQuery(id+"F22.wireOp",EDGE,"E28.7.3");var subQ61=sQuery(id+"F22.wireOp",EDGE,"E28.7.2");var subQ62=sQuery(id+"F3.wireOp",EDGE,"E20.15.3");var subQ63=sQuery(id+"F3.wireOp",EDGE,"E20.15.1");var subQ64=sQuery(id+"F3.wireOp",EDGE,"E20.15.0");var subQ65=makeQuery(id+"F30.opLoft","SWEPT_FACE",FACE,{"disambiguationData":[OSD([subQ64,subQ63,subQ62,sQuery(id+"F22.wireOp",EDGE,"E28.7.1"),subQ61,subQ60])]});var subQ67=sQuery(id+"F22.wireOp",EDGE,"E28.6.3");var subQ68=sQuery(id+"F22.wireOp",EDGE,"E28.6.2");var subQ69=sQuery(id+"F3.wireOp",EDGE,"E20.14.3");var subQ71=sQuery(id+"F3.wireOp",EDGE,"E20.14.1");var subQ72=sQuery(id+"F3.wireOp",EDGE,"E20.14.0");var subQ73=makeQuery(id+"F29.opLoft","SWEPT_FACE",FACE,{"disambiguationData":[OSD([subQ72,subQ71,subQ69,sQuery(id+"F22.wireOp",EDGE,"E28.6.1"),subQ68,subQ67])]});var subQ74=sQuery(id+"F22.wireOp",EDGE,"E28.5.3");var subQ75=sQuery(id+"F22.wireOp",EDGE,"E28.5.2");var subQ76=sQuery(id+"F3.wireOp",EDGE,"E20.13.3");var subQ78=sQuery(id+"F3.wireOp",EDGE,"E20.13.1");var subQ79=sQuery(id+"F3.wireOp",EDGE,"E20.13.0");var subQ80=makeQuery(id+"F28.opLoft","SWEPT_FACE",FACE,{"disambiguationData":[OSD([subQ79,subQ78,subQ76,sQuery(id+"F22.wireOp",EDGE,"E28.5.1"),subQ75,subQ74])]});var subQ81=sQuery(id+"F22.wireOp",EDGE,"E28.4.3");var subQ82=sQuery(id+"F22.wireOp",EDGE,"E28.4.2");var subQ83=sQuery(id+"F3.wireOp",EDGE,"E20.12.3");var subQ85=sQuery(id+"F3.wireOp",EDGE,"E20.12.1");var subQ86=sQuery(id+"F3.wireOp",EDGE,"E20.12.0");var subQ87=makeQuery(id+"F27.opLoft","SWEPT_FACE",FACE,{"disambiguationData":[OSD([subQ86,subQ85,subQ83,sQuery(id+"F22.wireOp",EDGE,"E28.4.1"),subQ82,subQ81])]});var subQ88=sQuery(id+"F22.wireOp",EDGE,"E28.3.3");var subQ89=sQuery(id+"F22.wireOp",EDGE,"E28.3.2");var subQ90=sQuery(id+"F3.wireOp",EDGE,"E20.11.3");var subQ92=sQuery(id+"F3.wireOp",EDGE,"E20.11.1");var subQ93=sQuery(id+"F3.wireOp",EDGE,"E20.11.0");var subQ94=makeQuery(id+"F26.opLoft","SWEPT_FACE",FACE,{"disambiguationData":[OSD([subQ93,subQ92,subQ90,sQuery(id+"F22.wireOp",EDGE,"E28.3.1"),subQ89,subQ88])]});var subQ95=sQuery(id+"F22.wireOp",EDGE,"E28.2.3");var subQ96=sQuery(id+"F22.wireOp",EDGE,"E28.2.2");var subQ97=sQuery(id+"F3.wireOp",EDGE,"E20.10.3");var subQ98=sQuery(id+"F3.wireOp",EDGE,"E20.10.1");var subQ99=sQuery(id+"F3.wireOp",EDGE,"E20.10.0");var subQ100=makeQuery(id+"F25.opLoft","SWEPT_FACE",FACE,{"disambiguationData":[OSD([subQ99,subQ98,subQ97,sQuery(id+"F22.wireOp",EDGE,"E28.2.1"),subQ96,subQ95])]});var subQ102=sQuery(id+"F22.wireOp",EDGE,"E28.1.3");var subQ103=sQuery(id+"F22.wireOp",EDGE,"E28.1.2");var subQ104=sQuery(id+"F3.wireOp",EDGE,"E20.9.3");var subQ105=sQuery(id+"F3.wireOp",EDGE,"E20.9.1");var subQ106=sQuery(id+"F3.wireOp",EDGE,"E20.9.0");var subQ107=makeQuery(id+"F24.opLoft","SWEPT_FACE",FACE,{"disambiguationData":[OSD([subQ106,subQ105,subQ104,sQuery(id+"F22.wireOp",EDGE,"E28.1.1"),subQ103,subQ102])]});var subQ108=sQuery(id+"F22.wireOp",EDGE,"E27.top");var subQ109=sQuery(id+"F22.wireOp",EDGE,"E27.bottom");var subQ110=sQuery(id+"F3.wireOp",EDGE,"E20.8.3");var subQ112=sQuery(id+"F3.wireOp",EDGE,"E20.8.1");var subQ116=makeQuery(id+"F42.boolean.opBoolean","COPY",FACE,{"disambiguationData":[TD([subQ31])],"derivedFrom":subQ10});var subQ125=makeQuery(id+"F14.opLoft","CAP_FACE",FACE,{"disambiguationData":[OSD([makeQuery(id+"F3.imprint","IMPRINT",FACE,{"disambiguationData":[TD([[makeQuery(id+"F3.imprint","IMPRINT",EDGE,{"derivedFrom":subQ8}),-1.0]])]})])],"isStart":true});var subQ159=makeQuery(id+"F5.opLoft","CAP_FACE",FACE,{"disambiguationData":[OSD([makeQuery(id+"F3.imprint","IMPRINT",FACE,{"disambiguationData":[TD([[makeQuery(id+"F3.imprint","IMPRINT",EDGE,{"derivedFrom":subQ57}),1.0]])]})])],"isStart":true});var subQ188=makeQuery(id+"F35.boolean.opBoolean","INTERSECT",EDGE,{"derivedFrom":[makeQuery(id+"F34.boolean.opBoolean","SPLIT",FACE,{"disambiguationData":[TD([subQ125])],"derivedFrom":makeQuery(id+"F33.boolean.opBoolean","SPLIT",FACE,{"disambiguationData":[TD([subQ125])],"derivedFrom":makeQuery(id+"F32.boolean.opBoolean","SPLIT",FACE,{"disambiguationData":[TD([subQ125])],"derivedFrom":makeQuery(id+"F31.boolean.opBoolean","SPLIT",FACE,{"disambiguationData":[TD([subQ125])],"derivedFrom":makeQuery(id+"F30.boolean.opBoolean","SPLIT",FACE,{"disambiguationData":[TD([subQ159])],"derivedFrom":makeQuery(id+"F29.boolean.opBoolean","SPLIT",FACE,{"disambiguationData":[TD([subQ159])],"derivedFrom":makeQuery(id+"F28.boolean.opBoolean","SPLIT",FACE,{"disambiguationData":[TD([subQ159])],"derivedFrom":makeQuery(id+"F27.boolean.opBoolean","SPLIT",FACE,{"disambiguationData":[TD([subQ159])],"derivedFrom":makeQuery(id+"F26.boolean.opBoolean","SPLIT",FACE,{"disambiguationData":[TD([subQ159])],"derivedFrom":makeQuery(id+"F25.boolean.opBoolean","SPLIT",FACE,{"disambiguationData":[TD([subQ159])],"derivedFrom":makeQuery(id+"F24.boolean.opBoolean","SPLIT",FACE,{"disambiguationData":[TD([subQ159])],"derivedFrom":makeQuery(id+"F1.opRevolve","SWEPT_FACE",FACE,{"disambiguationData":[OSD([sQuery(id+"F0.wireOp",EDGE,"E4")])]})})})})})})})})})})})}),subQ31]});Q2=makeQuery(id+"F48.opFillet","BLEND_EDGE",EDGE,{"blendedFrom":[makeQuery(id+"F47.opFillet","TWEAK_EDGE",EDGE,{"derivedFrom":[makeQuery(id+"F45.opFillet","BLEND_VERTEX",VERTEX,{"blendedFrom":[subQ188,subQ31,subQ116],"blendedInto":[subQ31,subQ116]}),makeQuery(id+"F45.opFillet","BLEND_VERTEX",VERTEX,{"blendedFrom":[subQ188,makeQuery(id+"F42.boolean.opBoolean","MERGE",FACE,{"derivedFrom":[subQ2,subQ1]}),subQ116],"blendedInto":[makeQuery(id+"F42.boolean.opBoolean","MERGE",FACE,{"derivedFrom":[subQ2,subQ1]}),subQ116]})]}),makeQuery(id+"F47.opFillet","BLEND_FACE",FACE,{"disambiguationData":[OSD([subQ0,subQ9]),TDD([makeQuery(id+"F42.boolean.opBoolean","COPY",EDGE,{"disambiguationData":[TD([makeQuery(id+"F23.opLoft","SWEPT_FACE",FACE,{"disambiguationData":[OSD([sQuery(id+"F3.wireOp",EDGE,"E20.8.0"),subQ112,subQ110,subQ109,subQ108,sQuery(id+"F22.wireOp",EDGE,"E27.right")])]})])],"derivedFrom":subQ11})])]}),makeQuery(id+"F47.opFillet","BLEND_FACE",FACE,{"disambiguationData":[OSD([subQ0,subQ9]),TDD([makeQuery(id+"F42.boolean.opBoolean","COPY",EDGE,{"disambiguationData":[TD([subQ107])],"derivedFrom":subQ11})])]}),makeQuery(id+"F47.opFillet","BLEND_FACE",FACE,{"disambiguationData":[OSD([subQ0,subQ9]),TDD([makeQuery(id+"F42.boolean.opBoolean","COPY",EDGE,{"disambiguationData":[TD([subQ100])],"derivedFrom":subQ11})])]}),makeQuery(id+"F47.opFillet","BLEND_FACE",FACE,{"disambiguationData":[OSD([subQ0,subQ9]),TDD([makeQuery(id+"F42.boolean.opBoolean","COPY",EDGE,{"disambiguationData":[TD([subQ94])],"derivedFrom":subQ11})])]}),makeQuery(id+"F47.opFillet","BLEND_FACE",FACE,{"disambiguationData":[OSD([subQ0,subQ9]),TDD([makeQuery(id+"F42.boolean.opBoolean","COPY",EDGE,{"disambiguationData":[TD([subQ87])],"derivedFrom":subQ11})])]}),makeQuery(id+"F47.opFillet","BLEND_FACE",FACE,{"disambiguationData":[OSD([subQ0,subQ9]),TDD([makeQuery(id+"F42.boolean.opBoolean","COPY",EDGE,{"disambiguationData":[TD([subQ80])],"derivedFrom":subQ11})])]}),makeQuery(id+"F47.opFillet","BLEND_FACE",FACE,{"disambiguationData":[OSD([subQ0,subQ9]),TDD([makeQuery(id+"F42.boolean.opBoolean","COPY",EDGE,{"disambiguationData":[TD([subQ73])],"derivedFrom":subQ11})])]}),makeQuery(id+"F47.opFillet","BLEND_FACE",FACE,{"disambiguationData":[OSD([subQ0,subQ9]),TDD([makeQuery(id+"F42.boolean.opBoolean","COPY",EDGE,{"disambiguationData":[TD([subQ65])],"derivedFrom":subQ11})])]}),makeQuery(id+"F47.opFillet","BLEND_FACE",FACE,{"disambiguationData":[OSD([subQ0,subQ9]),TDD([makeQuery(id+"F42.boolean.opBoolean","COPY",EDGE,{"disambiguationData":[TD([subQ59])],"derivedFrom":subQ11})])]}),makeQuery(id+"F47.opFillet","BLEND_FACE",FACE,{"disambiguationData":[OSD([subQ0,subQ9]),TDD([makeQuery(id+"F42.boolean.opBoolean","COPY",EDGE,{"disambiguationData":[TD([subQ52])],"derivedFrom":subQ11})])]}),makeQuery(id+"F47.opFillet","BLEND_FACE",FACE,{"disambiguationData":[OSD([subQ0,subQ9]),TDD([makeQuery(id+"F42.boolean.opBoolean","COPY",EDGE,{"disambiguationData":[TD([subQ45])],"derivedFrom":subQ11})])]}),makeQuery(id+"F47.opFillet","BLEND_FACE",FACE,{"disambiguationData":[OSD([subQ0,subQ9]),TDD([makeQuery(id+"F42.boolean.opBoolean","COPY",EDGE,{"disambiguationData":[TD([subQ38])],"derivedFrom":subQ11})])]}),makeQuery(id+"F47.opFillet","BLEND_FACE",FACE,{"disambiguationData":[OSD([subQ0,subQ9]),TDD([makeQuery(id+"F42.boolean.opBoolean","COPY",EDGE,{"disambiguationData":[TD([subQ31])],"derivedFrom":subQ11})])]}),makeQuery(id+"F47.opFillet","BLEND_FACE",FACE,{"disambiguationData":[OSD([subQ0,subQ9]),TDD([makeQuery(id+"F42.boolean.opBoolean","COPY",EDGE,{"disambiguationData":[TD([makeQuery(id+"F36.opLoft","SWEPT_FACE",FACE,{"disambiguationData":[OSD([subQ23,subQ22,subQ20,sQuery(id+"F22.wireOp",EDGE,"E28.13.1"),subQ19,subQ18])]})])],"derivedFrom":subQ11})])]}),makeQuery(id+"F47.opFillet","BLEND_FACE",FACE,{"disambiguationData":[OSD([subQ0,subQ9]),TDD([makeQuery(id+"F42.boolean.opBoolean","COPY",EDGE,{"disambiguationData":[TD([makeQuery(id+"F37.opLoft","SWEPT_FACE",FACE,{"disambiguationData":[OSD([subQ16,subQ15,subQ14,sQuery(id+"F22.wireOp",EDGE,"E28.14.1"),subQ13,subQ12])]})])],"derivedFrom":subQ11})])]}),makeQuery(id+"F47.opFillet","BLEND_FACE",FACE,{"disambiguationData":[OSD([subQ0,subQ9]),TDD([makeQuery(id+"F42.boolean.opBoolean","COPY",EDGE,{"disambiguationData":[TD([makeQuery(id+"F38.opLoft","SWEPT_FACE",FACE,{"disambiguationData":[OSD([subQ8,subQ7,subQ5,sQuery(id+"F22.wireOp",EDGE,"E28.15.1"),subQ4,subQ3])]})])],"derivedFrom":subQ11})])]})],"blendedInto":[makeQuery(id+"F47.opFillet","BLEND_FACE",FACE,{"disambiguationData":[OSD([subQ0,subQ9]),TDD([makeQuery(id+"F42.boolean.opBoolean","COPY",EDGE,{"disambiguationData":[TD([makeQuery(id+"F23.opLoft","SWEPT_FACE",FACE,{"disambiguationData":[OSD([sQuery(id+"F3.wireOp",EDGE,"E20.8.0"),subQ112,subQ110,subQ109,subQ108,sQuery(id+"F22.wireOp",EDGE,"E27.right")])]})])],"derivedFrom":subQ11})])]}),makeQuery(id+"F47.opFillet","BLEND_FACE",FACE,{"disambiguationData":[OSD([subQ0,subQ9]),TDD([makeQuery(id+"F42.boolean.opBoolean","COPY",EDGE,{"disambiguationData":[TD([subQ107])],"derivedFrom":subQ11})])]}),makeQuery(id+"F47.opFillet","BLEND_FACE",FACE,{"disambiguationData":[OSD([subQ0,subQ9]),TDD([makeQuery(id+"F42.boolean.opBoolean","COPY",EDGE,{"disambiguationData":[TD([subQ100])],"derivedFrom":subQ11})])]}),makeQuery(id+"F47.opFillet","BLEND_FACE",FACE,{"disambiguationData":[OSD([subQ0,subQ9]),TDD([makeQuery(id+"F42.boolean.opBoolean","COPY",EDGE,{"disambiguationData":[TD([subQ94])],"derivedFrom":subQ11})])]}),makeQuery(id+"F47.opFillet","BLEND_FACE",FACE,{"disambiguationData":[OSD([subQ0,subQ9]),TDD([makeQuery(id+"F42.boolean.opBoolean","COPY",EDGE,{"disambiguationData":[TD([subQ87])],"derivedFrom":subQ11})])]}),makeQuery(id+"F47.opFillet","BLEND_FACE",FACE,{"disambiguationData":[OSD([subQ0,subQ9]),TDD([makeQuery(id+"F42.boolean.opBoolean","COPY",EDGE,{"disambiguationData":[TD([subQ80])],"derivedFrom":subQ11})])]}),makeQuery(id+"F47.opFillet","BLEND_FACE",FACE,{"disambiguationData":[OSD([subQ0,subQ9]),TDD([makeQuery(id+"F42.boolean.opBoolean","COPY",EDGE,{"disambiguationData":[TD([subQ73])],"derivedFrom":subQ11})])]}),makeQuery(id+"F47.opFillet","BLEND_FACE",FACE,{"disambiguationData":[OSD([subQ0,subQ9]),TDD([makeQuery(id+"F42.boolean.opBoolean","COPY",EDGE,{"disambiguationData":[TD([subQ65])],"derivedFrom":subQ11})])]}),makeQuery(id+"F47.opFillet","BLEND_FACE",FACE,{"disambiguationData":[OSD([subQ0,subQ9]),TDD([makeQuery(id+"F42.boolean.opBoolean","COPY",EDGE,{"disambiguationData":[TD([subQ59])],"derivedFrom":subQ11})])]}),makeQuery(id+"F47.opFillet","BLEND_FACE",FACE,{"disambiguationData":[OSD([subQ0,subQ9]),TDD([makeQuery(id+"F42.boolean.opBoolean","COPY",EDGE,{"disambiguationData":[TD([subQ52])],"derivedFrom":subQ11})])]}),makeQuery(id+"F47.opFillet","BLEND_FACE",FACE,{"disambiguationData":[OSD([subQ0,subQ9]),TDD([makeQuery(id+"F42.boolean.opBoolean","COPY",EDGE,{"disambiguationData":[TD([subQ45])],"derivedFrom":subQ11})])]}),makeQuery(id+"F47.opFillet","BLEND_FACE",FACE,{"disambiguationData":[OSD([subQ0,subQ9]),TDD([makeQuery(id+"F42.boolean.opBoolean","COPY",EDGE,{"disambiguationData":[TD([subQ38])],"derivedFrom":subQ11})])]}),makeQuery(id+"F47.opFillet","BLEND_FACE",FACE,{"disambiguationData":[OSD([subQ0,subQ9]),TDD([makeQuery(id+"F42.boolean.opBoolean","COPY",EDGE,{"disambiguationData":[TD([subQ31])],"derivedFrom":subQ11})])]}),makeQuery(id+"F47.opFillet","BLEND_FACE",FACE,{"disambiguationData":[OSD([subQ0,subQ9]),TDD([makeQuery(id+"F42.boolean.opBoolean","COPY",EDGE,{"disambiguationData":[TD([makeQuery(id+"F36.opLoft","SWEPT_FACE",FACE,{"disambiguationData":[OSD([subQ23,subQ22,subQ20,sQuery(id+"F22.wireOp",EDGE,"E28.13.1"),subQ19,subQ18])]})])],"derivedFrom":subQ11})])]}),makeQuery(id+"F47.opFillet","BLEND_FACE",FACE,{"disambiguationData":[OSD([subQ0,subQ9]),TDD([makeQuery(id+"F42.boolean.opBoolean","COPY",EDGE,{"disambiguationData":[TD([makeQuery(id+"F37.opLoft","SWEPT_FACE",FACE,{"disambiguationData":[OSD([subQ16,subQ15,subQ14,sQuery(id+"F22.wireOp",EDGE,"E28.14.1"),subQ13,subQ12])]})])],"derivedFrom":subQ11})])]}),makeQuery(id+"F47.opFillet","BLEND_FACE",FACE,{"disambiguationData":[OSD([subQ0,subQ9]),TDD([makeQuery(id+"F42.boolean.opBoolean","COPY",EDGE,{"disambiguationData":[TD([makeQuery(id+"F38.opLoft","SWEPT_FACE",FACE,{"disambiguationData":[OSD([subQ8,subQ7,subQ5,sQuery(id+"F22.wireOp",EDGE,"E28.15.1"),subQ4,subQ3])]})])],"derivedFrom":subQ11})])]})]});}
            var Q3;
            {var subQ0=sQuery(id+"F22.wireOp",EDGE,"E28.13.3");var subQ1=sQuery(id+"F22.wireOp",EDGE,"E28.13.2");var subQ2=sQuery(id+"F22.wireOp",EDGE,"E28.13.0");var subQ3=sQuery(id+"F3.wireOp",EDGE,"E20.5.3");var subQ4=sQuery(id+"F3.wireOp",EDGE,"E20.5.1");var subQ5=makeQuery(id+"F36.opLoft","SWEPT_FACE",FACE,{"disambiguationData":[OSD([subQ4,sQuery(id+"F3.wireOp",EDGE,"E20.5.2"),subQ3,subQ2,subQ1,subQ0])]});var subQ6=sQuery(id+"F22.wireOp",EDGE,"E28.13.1");var subQ7=sQuery(id+"F41.wireOp",EDGE,"E34");var subQ8=sQuery(id+"F41.wireOp",EDGE,"E32");Q3=makeQuery(id+"F44.opFillet","BLEND_EDGE",EDGE,{"blendedFrom":[makeQuery(id+"F40.boolean.opBoolean","INTERSECT",EDGE,{"derivedFrom":[subQ5,makeQuery(id+"F40.opExtrude","CAP_FACE",FACE,{"disambiguationData":[OSD([sQuery(id+"F39.wireOp",EDGE,"E29"),sQuery(id+"F39.wireOp",EDGE,"E30")])],"isStart":true})]}),makeQuery(id+"F42.boolean.opBoolean","COPY",FACE,{"disambiguationData":[TD([makeQuery(id+"F36.opLoft","SWEPT_FACE",FACE,{"disambiguationData":[OSD([sQuery(id+"F3.wireOp",EDGE,"E20.5.0"),subQ4,subQ3,subQ6,subQ1,subQ0])]})])],"derivedFrom":makeQuery(id+"F42.opRevolve","SWEPT_FACE",FACE,{"disambiguationData":[OSD([subQ8]),TDD([makeQuery(id+"F41.imprint","IMPRINT",EDGE,{"disambiguationData":[TD([[makeQuery(id+"F41.imprint","INTERSECT",VERTEX,{"disambiguationData":[OD(0.0)],"derivedFrom":[subQ8,subQ7]}),-1.0]])],"derivedFrom":subQ8})])]})})],"blendedInto":[makeQuery(id+"F42.boolean.opBoolean","COPY",FACE,{"disambiguationData":[TD([makeQuery(id+"F36.opLoft","SWEPT_FACE",FACE,{"disambiguationData":[OSD([sQuery(id+"F3.wireOp",EDGE,"E20.5.0"),subQ4,subQ3,subQ6,subQ1,subQ0])]})])],"derivedFrom":makeQuery(id+"F42.opRevolve","SWEPT_FACE",FACE,{"disambiguationData":[OSD([subQ8]),TDD([makeQuery(id+"F41.imprint","IMPRINT",EDGE,{"disambiguationData":[TD([[makeQuery(id+"F41.imprint","INTERSECT",VERTEX,{"disambiguationData":[OD(0.0)],"derivedFrom":[subQ8,subQ7]}),-1.0]])],"derivedFrom":subQ8})])]})})]});}
            var Q4;
            {var subQ0=sQuery(id+"F41.wireOp",EDGE,"E34");var subQ1=sQuery(id+"F41.wireOp",EDGE,"E32");Q4=makeQuery(id+"F42.boolean.opBoolean","INTERSECT",EDGE,{"derivedFrom":[makeQuery(id+"F36.opLoft","SWEPT_FACE",FACE,{"disambiguationData":[OSD([sQuery(id+"F3.wireOp",EDGE,"E20.5.0"),sQuery(id+"F3.wireOp",EDGE,"E20.5.1"),sQuery(id+"F3.wireOp",EDGE,"E20.5.3"),sQuery(id+"F22.wireOp",EDGE,"E28.13.1"),sQuery(id+"F22.wireOp",EDGE,"E28.13.2"),sQuery(id+"F22.wireOp",EDGE,"E28.13.3")])]}),makeQuery(id+"F42.opRevolve","SWEPT_FACE",FACE,{"disambiguationData":[OSD([subQ1]),TDD([makeQuery(id+"F41.imprint","IMPRINT",EDGE,{"disambiguationData":[TD([[makeQuery(id+"F41.imprint","INTERSECT",VERTEX,{"disambiguationData":[OD(0.0)],"derivedFrom":[subQ1,subQ0]}),-1.0]])],"derivedFrom":subQ1})])]})]});}
            var Q5;
            {var subQ0=sQuery(id+"F41.wireOp",EDGE,"E37");var subQ1=makeQuery(id+"F42.opRevolve","SWEPT_FACE",FACE,{"disambiguationData":[OSD([subQ0])]});var subQ2=makeQuery(id+"F40.opExtrude","CAP_FACE",FACE,{"disambiguationData":[OSD([sQuery(id+"F39.wireOp",EDGE,"E29"),sQuery(id+"F39.wireOp",EDGE,"E30")])],"isStart":true});var subQ3=sQuery(id+"F22.wireOp",EDGE,"E28.15.3");var subQ4=sQuery(id+"F22.wireOp",EDGE,"E28.15.2");var subQ5=sQuery(id+"F3.wireOp",EDGE,"E20.7.3");var subQ7=sQuery(id+"F3.wireOp",EDGE,"E20.7.1");var subQ8=sQuery(id+"F3.wireOp",EDGE,"E20.7.0");var subQ9=sQuery(id+"F41.wireOp",EDGE,"E38");var subQ10=makeQuery(id+"F42.opRevolve","SWEPT_FACE",FACE,{"disambiguationData":[OSD([subQ9])]});var subQ11=makeQuery(id+"F42.opRevolve","SWEPT_EDGE",EDGE,{"disambiguationData":[OSD([subQ0,subQ9])]});var subQ12=sQuery(id+"F22.wireOp",EDGE,"E28.14.3");var subQ13=sQuery(id+"F22.wireOp",EDGE,"E28.14.2");var subQ14=sQuery(id+"F3.wireOp",EDGE,"E20.6.3");var subQ15=sQuery(id+"F3.wireOp",EDGE,"E20.6.1");var subQ16=sQuery(id+"F3.wireOp",EDGE,"E20.6.0");var subQ18=sQuery(id+"F22.wireOp",EDGE,"E28.13.3");var subQ19=sQuery(id+"F22.wireOp",EDGE,"E28.13.2");var subQ20=sQuery(id+"F3.wireOp",EDGE,"E20.5.3");var subQ22=sQuery(id+"F3.wireOp",EDGE,"E20.5.1");var subQ24=sQuery(id+"F3.wireOp",EDGE,"E20.5.0");var subQ25=makeQuery(id+"F36.opLoft","SWEPT_FACE",FACE,{"disambiguationData":[OSD([subQ24,subQ22,subQ20,sQuery(id+"F22.wireOp",EDGE,"E28.13.1"),subQ19,subQ18])]});var subQ26=sQuery(id+"F22.wireOp",EDGE,"E28.12.3");var subQ27=sQuery(id+"F22.wireOp",EDGE,"E28.12.2");var subQ28=sQuery(id+"F3.wireOp",EDGE,"E20.4.3");var subQ30=sQuery(id+"F3.wireOp",EDGE,"E20.4.1");var subQ31=sQuery(id+"F3.wireOp",EDGE,"E20.4.0");var subQ32=makeQuery(id+"F35.opLoft","SWEPT_FACE",FACE,{"disambiguationData":[OSD([subQ31,subQ30,subQ28,sQuery(id+"F22.wireOp",EDGE,"E28.12.1"),subQ27,subQ26])]});var subQ33=sQuery(id+"F22.wireOp",EDGE,"E28.11.3");var subQ34=sQuery(id+"F22.wireOp",EDGE,"E28.11.2");var subQ35=sQuery(id+"F3.wireOp",EDGE,"E20.3.3");var subQ37=sQuery(id+"F3.wireOp",EDGE,"E20.3.1");var subQ38=sQuery(id+"F3.wireOp",EDGE,"E20.3.0");var subQ39=makeQuery(id+"F34.opLoft","SWEPT_FACE",FACE,{"disambiguationData":[OSD([subQ38,subQ37,subQ35,sQuery(id+"F22.wireOp",EDGE,"E28.11.1"),subQ34,subQ33])]});var subQ40=sQuery(id+"F22.wireOp",EDGE,"E28.10.3");var subQ41=sQuery(id+"F22.wireOp",EDGE,"E28.10.2");var subQ42=sQuery(id+"F3.wireOp",EDGE,"E20.2.3");var subQ44=sQuery(id+"F3.wireOp",EDGE,"E20.2.1");var subQ45=sQuery(id+"F3.wireOp",EDGE,"E20.2.0");var subQ46=makeQuery(id+"F33.opLoft","SWEPT_FACE",FACE,{"disambiguationData":[OSD([subQ45,subQ44,subQ42,sQuery(id+"F22.wireOp",EDGE,"E28.10.1"),subQ41,subQ40])]});var subQ47=sQuery(id+"F22.wireOp",EDGE,"E28.9.3");var subQ48=sQuery(id+"F22.wireOp",EDGE,"E28.9.2");var subQ49=sQuery(id+"F3.wireOp",EDGE,"E20.1.3");var subQ51=sQuery(id+"F3.wireOp",EDGE,"E20.1.1");var subQ52=sQuery(id+"F3.wireOp",EDGE,"E20.1.0");var subQ53=makeQuery(id+"F32.opLoft","SWEPT_FACE",FACE,{"disambiguationData":[OSD([subQ52,subQ51,subQ49,sQuery(id+"F22.wireOp",EDGE,"E28.9.1"),subQ48,subQ47])]});var subQ54=sQuery(id+"F22.wireOp",EDGE,"E28.8.3");var subQ55=sQuery(id+"F22.wireOp",EDGE,"E28.8.2");var subQ57=sQuery(id+"F3.wireOp",EDGE,"E18.top");var subQ58=sQuery(id+"F3.wireOp",EDGE,"E18.bottom");var subQ59=sQuery(id+"F3.wireOp",EDGE,"E18.left");var subQ60=makeQuery(id+"F31.opLoft","SWEPT_FACE",FACE,{"disambiguationData":[OSD([subQ58,subQ57,subQ59,sQuery(id+"F22.wireOp",EDGE,"E28.8.1"),subQ55,subQ54])]});var subQ61=sQuery(id+"F22.wireOp",EDGE,"E28.7.3");var subQ62=sQuery(id+"F22.wireOp",EDGE,"E28.7.2");var subQ63=sQuery(id+"F3.wireOp",EDGE,"E20.15.3");var subQ64=sQuery(id+"F3.wireOp",EDGE,"E20.15.1");var subQ65=sQuery(id+"F3.wireOp",EDGE,"E20.15.0");var subQ66=makeQuery(id+"F30.opLoft","SWEPT_FACE",FACE,{"disambiguationData":[OSD([subQ65,subQ64,subQ63,sQuery(id+"F22.wireOp",EDGE,"E28.7.1"),subQ62,subQ61])]});var subQ68=sQuery(id+"F22.wireOp",EDGE,"E28.6.3");var subQ69=sQuery(id+"F22.wireOp",EDGE,"E28.6.2");var subQ70=sQuery(id+"F3.wireOp",EDGE,"E20.14.3");var subQ72=sQuery(id+"F3.wireOp",EDGE,"E20.14.1");var subQ73=sQuery(id+"F3.wireOp",EDGE,"E20.14.0");var subQ74=makeQuery(id+"F29.opLoft","SWEPT_FACE",FACE,{"disambiguationData":[OSD([subQ73,subQ72,subQ70,sQuery(id+"F22.wireOp",EDGE,"E28.6.1"),subQ69,subQ68])]});var subQ75=sQuery(id+"F22.wireOp",EDGE,"E28.5.3");var subQ76=sQuery(id+"F22.wireOp",EDGE,"E28.5.2");var subQ77=sQuery(id+"F3.wireOp",EDGE,"E20.13.3");var subQ79=sQuery(id+"F3.wireOp",EDGE,"E20.13.1");var subQ80=sQuery(id+"F3.wireOp",EDGE,"E20.13.0");var subQ81=makeQuery(id+"F28.opLoft","SWEPT_FACE",FACE,{"disambiguationData":[OSD([subQ80,subQ79,subQ77,sQuery(id+"F22.wireOp",EDGE,"E28.5.1"),subQ76,subQ75])]});var subQ82=sQuery(id+"F22.wireOp",EDGE,"E28.4.3");var subQ83=sQuery(id+"F22.wireOp",EDGE,"E28.4.2");var subQ84=sQuery(id+"F3.wireOp",EDGE,"E20.12.3");var subQ86=sQuery(id+"F3.wireOp",EDGE,"E20.12.1");var subQ87=sQuery(id+"F3.wireOp",EDGE,"E20.12.0");var subQ88=makeQuery(id+"F27.opLoft","SWEPT_FACE",FACE,{"disambiguationData":[OSD([subQ87,subQ86,subQ84,sQuery(id+"F22.wireOp",EDGE,"E28.4.1"),subQ83,subQ82])]});var subQ89=sQuery(id+"F22.wireOp",EDGE,"E28.3.3");var subQ90=sQuery(id+"F22.wireOp",EDGE,"E28.3.2");var subQ91=sQuery(id+"F3.wireOp",EDGE,"E20.11.3");var subQ93=sQuery(id+"F3.wireOp",EDGE,"E20.11.1");var subQ94=sQuery(id+"F3.wireOp",EDGE,"E20.11.0");var subQ95=makeQuery(id+"F26.opLoft","SWEPT_FACE",FACE,{"disambiguationData":[OSD([subQ94,subQ93,subQ91,sQuery(id+"F22.wireOp",EDGE,"E28.3.1"),subQ90,subQ89])]});var subQ96=sQuery(id+"F22.wireOp",EDGE,"E28.2.3");var subQ97=sQuery(id+"F22.wireOp",EDGE,"E28.2.2");var subQ98=sQuery(id+"F3.wireOp",EDGE,"E20.10.3");var subQ99=sQuery(id+"F3.wireOp",EDGE,"E20.10.1");var subQ100=sQuery(id+"F3.wireOp",EDGE,"E20.10.0");var subQ101=makeQuery(id+"F25.opLoft","SWEPT_FACE",FACE,{"disambiguationData":[OSD([subQ100,subQ99,subQ98,sQuery(id+"F22.wireOp",EDGE,"E28.2.1"),subQ97,subQ96])]});var subQ103=sQuery(id+"F22.wireOp",EDGE,"E28.1.3");var subQ104=sQuery(id+"F22.wireOp",EDGE,"E28.1.2");var subQ105=sQuery(id+"F3.wireOp",EDGE,"E20.9.3");var subQ106=sQuery(id+"F3.wireOp",EDGE,"E20.9.1");var subQ107=sQuery(id+"F3.wireOp",EDGE,"E20.9.0");var subQ108=makeQuery(id+"F24.opLoft","SWEPT_FACE",FACE,{"disambiguationData":[OSD([subQ107,subQ106,subQ105,sQuery(id+"F22.wireOp",EDGE,"E28.1.1"),subQ104,subQ103])]});var subQ109=sQuery(id+"F22.wireOp",EDGE,"E27.top");var subQ110=sQuery(id+"F22.wireOp",EDGE,"E27.bottom");var subQ111=sQuery(id+"F3.wireOp",EDGE,"E20.8.3");var subQ113=sQuery(id+"F3.wireOp",EDGE,"E20.8.1");var subQ117=makeQuery(id+"F42.boolean.opBoolean","COPY",FACE,{"disambiguationData":[TD([subQ25])],"derivedFrom":subQ10});var subQ125=makeQuery(id+"F14.opLoft","CAP_FACE",FACE,{"disambiguationData":[OSD([makeQuery(id+"F3.imprint","IMPRINT",FACE,{"disambiguationData":[TD([[makeQuery(id+"F3.imprint","IMPRINT",EDGE,{"derivedFrom":subQ8}),-1.0]])]})])],"isStart":true});var subQ160=makeQuery(id+"F5.opLoft","CAP_FACE",FACE,{"disambiguationData":[OSD([makeQuery(id+"F3.imprint","IMPRINT",FACE,{"disambiguationData":[TD([[makeQuery(id+"F3.imprint","IMPRINT",EDGE,{"derivedFrom":subQ58}),1.0]])]})])],"isStart":true});var subQ189=makeQuery(id+"F36.boolean.opBoolean","INTERSECT",EDGE,{"derivedFrom":[makeQuery(id+"F35.boolean.opBoolean","SPLIT",FACE,{"disambiguationData":[TD([subQ125])],"derivedFrom":makeQuery(id+"F34.boolean.opBoolean","SPLIT",FACE,{"disambiguationData":[TD([subQ125])],"derivedFrom":makeQuery(id+"F33.boolean.opBoolean","SPLIT",FACE,{"disambiguationData":[TD([subQ125])],"derivedFrom":makeQuery(id+"F32.boolean.opBoolean","SPLIT",FACE,{"disambiguationData":[TD([subQ125])],"derivedFrom":makeQuery(id+"F31.boolean.opBoolean","SPLIT",FACE,{"disambiguationData":[TD([subQ125])],"derivedFrom":makeQuery(id+"F30.boolean.opBoolean","SPLIT",FACE,{"disambiguationData":[TD([subQ160])],"derivedFrom":makeQuery(id+"F29.boolean.opBoolean","SPLIT",FACE,{"disambiguationData":[TD([subQ160])],"derivedFrom":makeQuery(id+"F28.boolean.opBoolean","SPLIT",FACE,{"disambiguationData":[TD([subQ160])],"derivedFrom":makeQuery(id+"F27.boolean.opBoolean","SPLIT",FACE,{"disambiguationData":[TD([subQ160])],"derivedFrom":makeQuery(id+"F26.boolean.opBoolean","SPLIT",FACE,{"disambiguationData":[TD([subQ160])],"derivedFrom":makeQuery(id+"F25.boolean.opBoolean","SPLIT",FACE,{"disambiguationData":[TD([subQ160])],"derivedFrom":makeQuery(id+"F24.boolean.opBoolean","SPLIT",FACE,{"disambiguationData":[TD([subQ160])],"derivedFrom":makeQuery(id+"F1.opRevolve","SWEPT_FACE",FACE,{"disambiguationData":[OSD([sQuery(id+"F0.wireOp",EDGE,"E4")])]})})})})})})})})})})})})}),subQ25]});Q5=makeQuery(id+"F48.opFillet","BLEND_EDGE",EDGE,{"blendedFrom":[makeQuery(id+"F47.opFillet","TWEAK_EDGE",EDGE,{"derivedFrom":[makeQuery(id+"F45.opFillet","BLEND_VERTEX",VERTEX,{"blendedFrom":[subQ189,subQ25,subQ117],"blendedInto":[subQ25,subQ117]}),makeQuery(id+"F45.opFillet","BLEND_VERTEX",VERTEX,{"blendedFrom":[subQ189,makeQuery(id+"F42.boolean.opBoolean","MERGE",FACE,{"derivedFrom":[subQ2,subQ1]}),subQ117],"blendedInto":[makeQuery(id+"F42.boolean.opBoolean","MERGE",FACE,{"derivedFrom":[subQ2,subQ1]}),subQ117]})]}),makeQuery(id+"F47.opFillet","BLEND_FACE",FACE,{"disambiguationData":[OSD([subQ0,subQ9]),TDD([makeQuery(id+"F42.boolean.opBoolean","COPY",EDGE,{"disambiguationData":[TD([makeQuery(id+"F23.opLoft","SWEPT_FACE",FACE,{"disambiguationData":[OSD([sQuery(id+"F3.wireOp",EDGE,"E20.8.0"),subQ113,subQ111,subQ110,subQ109,sQuery(id+"F22.wireOp",EDGE,"E27.right")])]})])],"derivedFrom":subQ11})])]}),makeQuery(id+"F47.opFillet","BLEND_FACE",FACE,{"disambiguationData":[OSD([subQ0,subQ9]),TDD([makeQuery(id+"F42.boolean.opBoolean","COPY",EDGE,{"disambiguationData":[TD([subQ108])],"derivedFrom":subQ11})])]}),makeQuery(id+"F47.opFillet","BLEND_FACE",FACE,{"disambiguationData":[OSD([subQ0,subQ9]),TDD([makeQuery(id+"F42.boolean.opBoolean","COPY",EDGE,{"disambiguationData":[TD([subQ101])],"derivedFrom":subQ11})])]}),makeQuery(id+"F47.opFillet","BLEND_FACE",FACE,{"disambiguationData":[OSD([subQ0,subQ9]),TDD([makeQuery(id+"F42.boolean.opBoolean","COPY",EDGE,{"disambiguationData":[TD([subQ95])],"derivedFrom":subQ11})])]}),makeQuery(id+"F47.opFillet","BLEND_FACE",FACE,{"disambiguationData":[OSD([subQ0,subQ9]),TDD([makeQuery(id+"F42.boolean.opBoolean","COPY",EDGE,{"disambiguationData":[TD([subQ88])],"derivedFrom":subQ11})])]}),makeQuery(id+"F47.opFillet","BLEND_FACE",FACE,{"disambiguationData":[OSD([subQ0,subQ9]),TDD([makeQuery(id+"F42.boolean.opBoolean","COPY",EDGE,{"disambiguationData":[TD([subQ81])],"derivedFrom":subQ11})])]}),makeQuery(id+"F47.opFillet","BLEND_FACE",FACE,{"disambiguationData":[OSD([subQ0,subQ9]),TDD([makeQuery(id+"F42.boolean.opBoolean","COPY",EDGE,{"disambiguationData":[TD([subQ74])],"derivedFrom":subQ11})])]}),makeQuery(id+"F47.opFillet","BLEND_FACE",FACE,{"disambiguationData":[OSD([subQ0,subQ9]),TDD([makeQuery(id+"F42.boolean.opBoolean","COPY",EDGE,{"disambiguationData":[TD([subQ66])],"derivedFrom":subQ11})])]}),makeQuery(id+"F47.opFillet","BLEND_FACE",FACE,{"disambiguationData":[OSD([subQ0,subQ9]),TDD([makeQuery(id+"F42.boolean.opBoolean","COPY",EDGE,{"disambiguationData":[TD([subQ60])],"derivedFrom":subQ11})])]}),makeQuery(id+"F47.opFillet","BLEND_FACE",FACE,{"disambiguationData":[OSD([subQ0,subQ9]),TDD([makeQuery(id+"F42.boolean.opBoolean","COPY",EDGE,{"disambiguationData":[TD([subQ53])],"derivedFrom":subQ11})])]}),makeQuery(id+"F47.opFillet","BLEND_FACE",FACE,{"disambiguationData":[OSD([subQ0,subQ9]),TDD([makeQuery(id+"F42.boolean.opBoolean","COPY",EDGE,{"disambiguationData":[TD([subQ46])],"derivedFrom":subQ11})])]}),makeQuery(id+"F47.opFillet","BLEND_FACE",FACE,{"disambiguationData":[OSD([subQ0,subQ9]),TDD([makeQuery(id+"F42.boolean.opBoolean","COPY",EDGE,{"disambiguationData":[TD([subQ39])],"derivedFrom":subQ11})])]}),makeQuery(id+"F47.opFillet","BLEND_FACE",FACE,{"disambiguationData":[OSD([subQ0,subQ9]),TDD([makeQuery(id+"F42.boolean.opBoolean","COPY",EDGE,{"disambiguationData":[TD([subQ32])],"derivedFrom":subQ11})])]}),makeQuery(id+"F47.opFillet","BLEND_FACE",FACE,{"disambiguationData":[OSD([subQ0,subQ9]),TDD([makeQuery(id+"F42.boolean.opBoolean","COPY",EDGE,{"disambiguationData":[TD([subQ25])],"derivedFrom":subQ11})])]}),makeQuery(id+"F47.opFillet","BLEND_FACE",FACE,{"disambiguationData":[OSD([subQ0,subQ9]),TDD([makeQuery(id+"F42.boolean.opBoolean","COPY",EDGE,{"disambiguationData":[TD([makeQuery(id+"F37.opLoft","SWEPT_FACE",FACE,{"disambiguationData":[OSD([subQ16,subQ15,subQ14,sQuery(id+"F22.wireOp",EDGE,"E28.14.1"),subQ13,subQ12])]})])],"derivedFrom":subQ11})])]}),makeQuery(id+"F47.opFillet","BLEND_FACE",FACE,{"disambiguationData":[OSD([subQ0,subQ9]),TDD([makeQuery(id+"F42.boolean.opBoolean","COPY",EDGE,{"disambiguationData":[TD([makeQuery(id+"F38.opLoft","SWEPT_FACE",FACE,{"disambiguationData":[OSD([subQ8,subQ7,subQ5,sQuery(id+"F22.wireOp",EDGE,"E28.15.1"),subQ4,subQ3])]})])],"derivedFrom":subQ11})])]})],"blendedInto":[makeQuery(id+"F47.opFillet","BLEND_FACE",FACE,{"disambiguationData":[OSD([subQ0,subQ9]),TDD([makeQuery(id+"F42.boolean.opBoolean","COPY",EDGE,{"disambiguationData":[TD([makeQuery(id+"F23.opLoft","SWEPT_FACE",FACE,{"disambiguationData":[OSD([sQuery(id+"F3.wireOp",EDGE,"E20.8.0"),subQ113,subQ111,subQ110,subQ109,sQuery(id+"F22.wireOp",EDGE,"E27.right")])]})])],"derivedFrom":subQ11})])]}),makeQuery(id+"F47.opFillet","BLEND_FACE",FACE,{"disambiguationData":[OSD([subQ0,subQ9]),TDD([makeQuery(id+"F42.boolean.opBoolean","COPY",EDGE,{"disambiguationData":[TD([subQ108])],"derivedFrom":subQ11})])]}),makeQuery(id+"F47.opFillet","BLEND_FACE",FACE,{"disambiguationData":[OSD([subQ0,subQ9]),TDD([makeQuery(id+"F42.boolean.opBoolean","COPY",EDGE,{"disambiguationData":[TD([subQ101])],"derivedFrom":subQ11})])]}),makeQuery(id+"F47.opFillet","BLEND_FACE",FACE,{"disambiguationData":[OSD([subQ0,subQ9]),TDD([makeQuery(id+"F42.boolean.opBoolean","COPY",EDGE,{"disambiguationData":[TD([subQ95])],"derivedFrom":subQ11})])]}),makeQuery(id+"F47.opFillet","BLEND_FACE",FACE,{"disambiguationData":[OSD([subQ0,subQ9]),TDD([makeQuery(id+"F42.boolean.opBoolean","COPY",EDGE,{"disambiguationData":[TD([subQ88])],"derivedFrom":subQ11})])]}),makeQuery(id+"F47.opFillet","BLEND_FACE",FACE,{"disambiguationData":[OSD([subQ0,subQ9]),TDD([makeQuery(id+"F42.boolean.opBoolean","COPY",EDGE,{"disambiguationData":[TD([subQ81])],"derivedFrom":subQ11})])]}),makeQuery(id+"F47.opFillet","BLEND_FACE",FACE,{"disambiguationData":[OSD([subQ0,subQ9]),TDD([makeQuery(id+"F42.boolean.opBoolean","COPY",EDGE,{"disambiguationData":[TD([subQ74])],"derivedFrom":subQ11})])]}),makeQuery(id+"F47.opFillet","BLEND_FACE",FACE,{"disambiguationData":[OSD([subQ0,subQ9]),TDD([makeQuery(id+"F42.boolean.opBoolean","COPY",EDGE,{"disambiguationData":[TD([subQ66])],"derivedFrom":subQ11})])]}),makeQuery(id+"F47.opFillet","BLEND_FACE",FACE,{"disambiguationData":[OSD([subQ0,subQ9]),TDD([makeQuery(id+"F42.boolean.opBoolean","COPY",EDGE,{"disambiguationData":[TD([subQ60])],"derivedFrom":subQ11})])]}),makeQuery(id+"F47.opFillet","BLEND_FACE",FACE,{"disambiguationData":[OSD([subQ0,subQ9]),TDD([makeQuery(id+"F42.boolean.opBoolean","COPY",EDGE,{"disambiguationData":[TD([subQ53])],"derivedFrom":subQ11})])]}),makeQuery(id+"F47.opFillet","BLEND_FACE",FACE,{"disambiguationData":[OSD([subQ0,subQ9]),TDD([makeQuery(id+"F42.boolean.opBoolean","COPY",EDGE,{"disambiguationData":[TD([subQ46])],"derivedFrom":subQ11})])]}),makeQuery(id+"F47.opFillet","BLEND_FACE",FACE,{"disambiguationData":[OSD([subQ0,subQ9]),TDD([makeQuery(id+"F42.boolean.opBoolean","COPY",EDGE,{"disambiguationData":[TD([subQ39])],"derivedFrom":subQ11})])]}),makeQuery(id+"F47.opFillet","BLEND_FACE",FACE,{"disambiguationData":[OSD([subQ0,subQ9]),TDD([makeQuery(id+"F42.boolean.opBoolean","COPY",EDGE,{"disambiguationData":[TD([subQ32])],"derivedFrom":subQ11})])]}),makeQuery(id+"F47.opFillet","BLEND_FACE",FACE,{"disambiguationData":[OSD([subQ0,subQ9]),TDD([makeQuery(id+"F42.boolean.opBoolean","COPY",EDGE,{"disambiguationData":[TD([subQ25])],"derivedFrom":subQ11})])]}),makeQuery(id+"F47.opFillet","BLEND_FACE",FACE,{"disambiguationData":[OSD([subQ0,subQ9]),TDD([makeQuery(id+"F42.boolean.opBoolean","COPY",EDGE,{"disambiguationData":[TD([makeQuery(id+"F37.opLoft","SWEPT_FACE",FACE,{"disambiguationData":[OSD([subQ16,subQ15,subQ14,sQuery(id+"F22.wireOp",EDGE,"E28.14.1"),subQ13,subQ12])]})])],"derivedFrom":subQ11})])]}),makeQuery(id+"F47.opFillet","BLEND_FACE",FACE,{"disambiguationData":[OSD([subQ0,subQ9]),TDD([makeQuery(id+"F42.boolean.opBoolean","COPY",EDGE,{"disambiguationData":[TD([makeQuery(id+"F38.opLoft","SWEPT_FACE",FACE,{"disambiguationData":[OSD([subQ8,subQ7,subQ5,sQuery(id+"F22.wireOp",EDGE,"E28.15.1"),subQ4,subQ3])]})])],"derivedFrom":subQ11})])]})]});}
            var Q6;
            {var subQ0=sQuery(id+"F22.wireOp",EDGE,"E28.14.0");var subQ1=sQuery(id+"F22.wireOp",EDGE,"E28.14.3");var subQ2=sQuery(id+"F22.wireOp",EDGE,"E28.14.1");var subQ3=sQuery(id+"F22.wireOp",EDGE,"E28.14.2");var subQ4=sQuery(id+"F3.wireOp",EDGE,"E20.6.3");var subQ5=sQuery(id+"F3.wireOp",EDGE,"E20.6.1");var subQ6=makeQuery(id+"F37.opLoft","SWEPT_FACE",FACE,{"disambiguationData":[OSD([subQ5,sQuery(id+"F3.wireOp",EDGE,"E20.6.2"),subQ4,subQ0,subQ3,subQ1])]});var subQ7=sQuery(id+"F41.wireOp",EDGE,"E34");var subQ8=sQuery(id+"F41.wireOp",EDGE,"E32");Q6=makeQuery(id+"F44.opFillet","BLEND_EDGE",EDGE,{"blendedFrom":[makeQuery(id+"F40.boolean.opBoolean","INTERSECT",EDGE,{"derivedFrom":[subQ6,makeQuery(id+"F40.opExtrude","CAP_FACE",FACE,{"disambiguationData":[OSD([sQuery(id+"F39.wireOp",EDGE,"E29"),sQuery(id+"F39.wireOp",EDGE,"E30")])],"isStart":true})]}),makeQuery(id+"F42.boolean.opBoolean","COPY",FACE,{"disambiguationData":[TD([makeQuery(id+"F37.opLoft","SWEPT_FACE",FACE,{"disambiguationData":[OSD([sQuery(id+"F3.wireOp",EDGE,"E20.6.0"),subQ5,subQ4,subQ2,subQ3,subQ1])]})])],"derivedFrom":makeQuery(id+"F42.opRevolve","SWEPT_FACE",FACE,{"disambiguationData":[OSD([subQ8]),TDD([makeQuery(id+"F41.imprint","IMPRINT",EDGE,{"disambiguationData":[TD([[makeQuery(id+"F41.imprint","INTERSECT",VERTEX,{"disambiguationData":[OD(0.0)],"derivedFrom":[subQ8,subQ7]}),-1.0]])],"derivedFrom":subQ8})])]})})],"blendedInto":[makeQuery(id+"F42.boolean.opBoolean","COPY",FACE,{"disambiguationData":[TD([makeQuery(id+"F37.opLoft","SWEPT_FACE",FACE,{"disambiguationData":[OSD([sQuery(id+"F3.wireOp",EDGE,"E20.6.0"),subQ5,subQ4,subQ2,subQ3,subQ1])]})])],"derivedFrom":makeQuery(id+"F42.opRevolve","SWEPT_FACE",FACE,{"disambiguationData":[OSD([subQ8]),TDD([makeQuery(id+"F41.imprint","IMPRINT",EDGE,{"disambiguationData":[TD([[makeQuery(id+"F41.imprint","INTERSECT",VERTEX,{"disambiguationData":[OD(0.0)],"derivedFrom":[subQ8,subQ7]}),-1.0]])],"derivedFrom":subQ8})])]})})]});}
            var Q7;
            {var subQ0=sQuery(id+"F41.wireOp",EDGE,"E37");var subQ1=makeQuery(id+"F42.opRevolve","SWEPT_FACE",FACE,{"disambiguationData":[OSD([subQ0])]});var subQ2=makeQuery(id+"F40.opExtrude","CAP_FACE",FACE,{"disambiguationData":[OSD([sQuery(id+"F39.wireOp",EDGE,"E29"),sQuery(id+"F39.wireOp",EDGE,"E30")])],"isStart":true});var subQ3=sQuery(id+"F22.wireOp",EDGE,"E28.15.3");var subQ4=sQuery(id+"F22.wireOp",EDGE,"E28.15.2");var subQ5=sQuery(id+"F3.wireOp",EDGE,"E20.7.3");var subQ7=sQuery(id+"F3.wireOp",EDGE,"E20.7.1");var subQ8=sQuery(id+"F3.wireOp",EDGE,"E20.7.0");var subQ9=sQuery(id+"F41.wireOp",EDGE,"E38");var subQ10=makeQuery(id+"F42.opRevolve","SWEPT_FACE",FACE,{"disambiguationData":[OSD([subQ9])]});var subQ11=makeQuery(id+"F42.opRevolve","SWEPT_EDGE",EDGE,{"disambiguationData":[OSD([subQ0,subQ9])]});var subQ12=sQuery(id+"F22.wireOp",EDGE,"E28.14.3");var subQ13=sQuery(id+"F22.wireOp",EDGE,"E28.14.2");var subQ14=sQuery(id+"F3.wireOp",EDGE,"E20.6.3");var subQ15=sQuery(id+"F3.wireOp",EDGE,"E20.6.1");var subQ16=sQuery(id+"F3.wireOp",EDGE,"E20.6.0");var subQ18=sQuery(id+"F22.wireOp",EDGE,"E28.13.3");var subQ19=sQuery(id+"F22.wireOp",EDGE,"E28.13.2");var subQ20=sQuery(id+"F3.wireOp",EDGE,"E20.5.3");var subQ22=sQuery(id+"F3.wireOp",EDGE,"E20.5.1");var subQ23=sQuery(id+"F3.wireOp",EDGE,"E20.5.0");var subQ24=sQuery(id+"F22.wireOp",EDGE,"E28.12.3");var subQ25=sQuery(id+"F22.wireOp",EDGE,"E28.12.2");var subQ26=sQuery(id+"F3.wireOp",EDGE,"E20.4.3");var subQ28=sQuery(id+"F3.wireOp",EDGE,"E20.4.1");var subQ29=sQuery(id+"F3.wireOp",EDGE,"E20.4.0");var subQ30=sQuery(id+"F22.wireOp",EDGE,"E28.11.3");var subQ31=sQuery(id+"F22.wireOp",EDGE,"E28.11.2");var subQ32=sQuery(id+"F3.wireOp",EDGE,"E20.3.3");var subQ34=sQuery(id+"F3.wireOp",EDGE,"E20.3.1");var subQ36=sQuery(id+"F3.wireOp",EDGE,"E20.3.0");var subQ37=makeQuery(id+"F34.opLoft","SWEPT_FACE",FACE,{"disambiguationData":[OSD([subQ36,subQ34,subQ32,sQuery(id+"F22.wireOp",EDGE,"E28.11.1"),subQ31,subQ30])]});var subQ38=sQuery(id+"F22.wireOp",EDGE,"E28.10.3");var subQ39=sQuery(id+"F22.wireOp",EDGE,"E28.10.2");var subQ40=sQuery(id+"F3.wireOp",EDGE,"E20.2.3");var subQ42=sQuery(id+"F3.wireOp",EDGE,"E20.2.1");var subQ43=sQuery(id+"F3.wireOp",EDGE,"E20.2.0");var subQ44=makeQuery(id+"F33.opLoft","SWEPT_FACE",FACE,{"disambiguationData":[OSD([subQ43,subQ42,subQ40,sQuery(id+"F22.wireOp",EDGE,"E28.10.1"),subQ39,subQ38])]});var subQ45=sQuery(id+"F22.wireOp",EDGE,"E28.9.3");var subQ46=sQuery(id+"F22.wireOp",EDGE,"E28.9.2");var subQ47=sQuery(id+"F3.wireOp",EDGE,"E20.1.3");var subQ49=sQuery(id+"F3.wireOp",EDGE,"E20.1.1");var subQ50=sQuery(id+"F3.wireOp",EDGE,"E20.1.0");var subQ51=makeQuery(id+"F32.opLoft","SWEPT_FACE",FACE,{"disambiguationData":[OSD([subQ50,subQ49,subQ47,sQuery(id+"F22.wireOp",EDGE,"E28.9.1"),subQ46,subQ45])]});var subQ52=sQuery(id+"F22.wireOp",EDGE,"E28.8.3");var subQ53=sQuery(id+"F22.wireOp",EDGE,"E28.8.2");var subQ55=sQuery(id+"F3.wireOp",EDGE,"E18.top");var subQ56=sQuery(id+"F3.wireOp",EDGE,"E18.bottom");var subQ57=sQuery(id+"F3.wireOp",EDGE,"E18.left");var subQ58=makeQuery(id+"F31.opLoft","SWEPT_FACE",FACE,{"disambiguationData":[OSD([subQ56,subQ55,subQ57,sQuery(id+"F22.wireOp",EDGE,"E28.8.1"),subQ53,subQ52])]});var subQ59=sQuery(id+"F22.wireOp",EDGE,"E28.7.3");var subQ60=sQuery(id+"F22.wireOp",EDGE,"E28.7.2");var subQ61=sQuery(id+"F3.wireOp",EDGE,"E20.15.3");var subQ62=sQuery(id+"F3.wireOp",EDGE,"E20.15.1");var subQ63=sQuery(id+"F3.wireOp",EDGE,"E20.15.0");var subQ64=makeQuery(id+"F30.opLoft","SWEPT_FACE",FACE,{"disambiguationData":[OSD([subQ63,subQ62,subQ61,sQuery(id+"F22.wireOp",EDGE,"E28.7.1"),subQ60,subQ59])]});var subQ66=sQuery(id+"F22.wireOp",EDGE,"E28.6.3");var subQ67=sQuery(id+"F22.wireOp",EDGE,"E28.6.2");var subQ68=sQuery(id+"F3.wireOp",EDGE,"E20.14.3");var subQ70=sQuery(id+"F3.wireOp",EDGE,"E20.14.1");var subQ71=sQuery(id+"F3.wireOp",EDGE,"E20.14.0");var subQ72=makeQuery(id+"F29.opLoft","SWEPT_FACE",FACE,{"disambiguationData":[OSD([subQ71,subQ70,subQ68,sQuery(id+"F22.wireOp",EDGE,"E28.6.1"),subQ67,subQ66])]});var subQ73=sQuery(id+"F22.wireOp",EDGE,"E28.5.3");var subQ74=sQuery(id+"F22.wireOp",EDGE,"E28.5.2");var subQ75=sQuery(id+"F3.wireOp",EDGE,"E20.13.3");var subQ77=sQuery(id+"F3.wireOp",EDGE,"E20.13.1");var subQ78=sQuery(id+"F3.wireOp",EDGE,"E20.13.0");var subQ79=makeQuery(id+"F28.opLoft","SWEPT_FACE",FACE,{"disambiguationData":[OSD([subQ78,subQ77,subQ75,sQuery(id+"F22.wireOp",EDGE,"E28.5.1"),subQ74,subQ73])]});var subQ80=sQuery(id+"F22.wireOp",EDGE,"E28.4.3");var subQ81=sQuery(id+"F22.wireOp",EDGE,"E28.4.2");var subQ82=sQuery(id+"F3.wireOp",EDGE,"E20.12.3");var subQ84=sQuery(id+"F3.wireOp",EDGE,"E20.12.1");var subQ85=sQuery(id+"F3.wireOp",EDGE,"E20.12.0");var subQ86=makeQuery(id+"F27.opLoft","SWEPT_FACE",FACE,{"disambiguationData":[OSD([subQ85,subQ84,subQ82,sQuery(id+"F22.wireOp",EDGE,"E28.4.1"),subQ81,subQ80])]});var subQ87=sQuery(id+"F22.wireOp",EDGE,"E28.3.3");var subQ88=sQuery(id+"F22.wireOp",EDGE,"E28.3.2");var subQ89=sQuery(id+"F3.wireOp",EDGE,"E20.11.3");var subQ91=sQuery(id+"F3.wireOp",EDGE,"E20.11.1");var subQ92=sQuery(id+"F3.wireOp",EDGE,"E20.11.0");var subQ93=makeQuery(id+"F26.opLoft","SWEPT_FACE",FACE,{"disambiguationData":[OSD([subQ92,subQ91,subQ89,sQuery(id+"F22.wireOp",EDGE,"E28.3.1"),subQ88,subQ87])]});var subQ94=sQuery(id+"F22.wireOp",EDGE,"E28.2.3");var subQ95=sQuery(id+"F22.wireOp",EDGE,"E28.2.2");var subQ96=sQuery(id+"F3.wireOp",EDGE,"E20.10.3");var subQ97=sQuery(id+"F3.wireOp",EDGE,"E20.10.1");var subQ98=sQuery(id+"F3.wireOp",EDGE,"E20.10.0");var subQ99=makeQuery(id+"F25.opLoft","SWEPT_FACE",FACE,{"disambiguationData":[OSD([subQ98,subQ97,subQ96,sQuery(id+"F22.wireOp",EDGE,"E28.2.1"),subQ95,subQ94])]});var subQ101=sQuery(id+"F22.wireOp",EDGE,"E28.1.3");var subQ102=sQuery(id+"F22.wireOp",EDGE,"E28.1.2");var subQ103=sQuery(id+"F3.wireOp",EDGE,"E20.9.3");var subQ104=sQuery(id+"F3.wireOp",EDGE,"E20.9.1");var subQ105=sQuery(id+"F3.wireOp",EDGE,"E20.9.0");var subQ106=makeQuery(id+"F24.opLoft","SWEPT_FACE",FACE,{"disambiguationData":[OSD([subQ105,subQ104,subQ103,sQuery(id+"F22.wireOp",EDGE,"E28.1.1"),subQ102,subQ101])]});var subQ107=sQuery(id+"F22.wireOp",EDGE,"E27.top");var subQ108=sQuery(id+"F22.wireOp",EDGE,"E27.bottom");var subQ109=sQuery(id+"F3.wireOp",EDGE,"E20.8.3");var subQ111=sQuery(id+"F3.wireOp",EDGE,"E20.8.1");var subQ115=makeQuery(id+"F42.boolean.opBoolean","COPY",FACE,{"disambiguationData":[TD([subQ37])],"derivedFrom":subQ10});var subQ124=makeQuery(id+"F14.opLoft","CAP_FACE",FACE,{"disambiguationData":[OSD([makeQuery(id+"F3.imprint","IMPRINT",FACE,{"disambiguationData":[TD([[makeQuery(id+"F3.imprint","IMPRINT",EDGE,{"derivedFrom":subQ8}),-1.0]])]})])],"isStart":true});var subQ158=makeQuery(id+"F5.opLoft","CAP_FACE",FACE,{"disambiguationData":[OSD([makeQuery(id+"F3.imprint","IMPRINT",FACE,{"disambiguationData":[TD([[makeQuery(id+"F3.imprint","IMPRINT",EDGE,{"derivedFrom":subQ56}),1.0]])]})])],"isStart":true});var subQ187=makeQuery(id+"F34.boolean.opBoolean","INTERSECT",EDGE,{"derivedFrom":[makeQuery(id+"F33.boolean.opBoolean","SPLIT",FACE,{"disambiguationData":[TD([subQ124])],"derivedFrom":makeQuery(id+"F32.boolean.opBoolean","SPLIT",FACE,{"disambiguationData":[TD([subQ124])],"derivedFrom":makeQuery(id+"F31.boolean.opBoolean","SPLIT",FACE,{"disambiguationData":[TD([subQ124])],"derivedFrom":makeQuery(id+"F30.boolean.opBoolean","SPLIT",FACE,{"disambiguationData":[TD([subQ158])],"derivedFrom":makeQuery(id+"F29.boolean.opBoolean","SPLIT",FACE,{"disambiguationData":[TD([subQ158])],"derivedFrom":makeQuery(id+"F28.boolean.opBoolean","SPLIT",FACE,{"disambiguationData":[TD([subQ158])],"derivedFrom":makeQuery(id+"F27.boolean.opBoolean","SPLIT",FACE,{"disambiguationData":[TD([subQ158])],"derivedFrom":makeQuery(id+"F26.boolean.opBoolean","SPLIT",FACE,{"disambiguationData":[TD([subQ158])],"derivedFrom":makeQuery(id+"F25.boolean.opBoolean","SPLIT",FACE,{"disambiguationData":[TD([subQ158])],"derivedFrom":makeQuery(id+"F24.boolean.opBoolean","SPLIT",FACE,{"disambiguationData":[TD([subQ158])],"derivedFrom":makeQuery(id+"F1.opRevolve","SWEPT_FACE",FACE,{"disambiguationData":[OSD([sQuery(id+"F0.wireOp",EDGE,"E4")])]})})})})})})})})})})}),subQ37]});Q7=makeQuery(id+"F48.opFillet","BLEND_EDGE",EDGE,{"blendedFrom":[makeQuery(id+"F47.opFillet","TWEAK_EDGE",EDGE,{"derivedFrom":[makeQuery(id+"F45.opFillet","BLEND_VERTEX",VERTEX,{"blendedFrom":[subQ187,subQ37,subQ115],"blendedInto":[subQ37,subQ115]}),makeQuery(id+"F45.opFillet","BLEND_VERTEX",VERTEX,{"blendedFrom":[subQ187,makeQuery(id+"F42.boolean.opBoolean","MERGE",FACE,{"derivedFrom":[subQ2,subQ1]}),subQ115],"blendedInto":[makeQuery(id+"F42.boolean.opBoolean","MERGE",FACE,{"derivedFrom":[subQ2,subQ1]}),subQ115]})]}),makeQuery(id+"F47.opFillet","BLEND_FACE",FACE,{"disambiguationData":[OSD([subQ0,subQ9]),TDD([makeQuery(id+"F42.boolean.opBoolean","COPY",EDGE,{"disambiguationData":[TD([makeQuery(id+"F23.opLoft","SWEPT_FACE",FACE,{"disambiguationData":[OSD([sQuery(id+"F3.wireOp",EDGE,"E20.8.0"),subQ111,subQ109,subQ108,subQ107,sQuery(id+"F22.wireOp",EDGE,"E27.right")])]})])],"derivedFrom":subQ11})])]}),makeQuery(id+"F47.opFillet","BLEND_FACE",FACE,{"disambiguationData":[OSD([subQ0,subQ9]),TDD([makeQuery(id+"F42.boolean.opBoolean","COPY",EDGE,{"disambiguationData":[TD([subQ106])],"derivedFrom":subQ11})])]}),makeQuery(id+"F47.opFillet","BLEND_FACE",FACE,{"disambiguationData":[OSD([subQ0,subQ9]),TDD([makeQuery(id+"F42.boolean.opBoolean","COPY",EDGE,{"disambiguationData":[TD([subQ99])],"derivedFrom":subQ11})])]}),makeQuery(id+"F47.opFillet","BLEND_FACE",FACE,{"disambiguationData":[OSD([subQ0,subQ9]),TDD([makeQuery(id+"F42.boolean.opBoolean","COPY",EDGE,{"disambiguationData":[TD([subQ93])],"derivedFrom":subQ11})])]}),makeQuery(id+"F47.opFillet","BLEND_FACE",FACE,{"disambiguationData":[OSD([subQ0,subQ9]),TDD([makeQuery(id+"F42.boolean.opBoolean","COPY",EDGE,{"disambiguationData":[TD([subQ86])],"derivedFrom":subQ11})])]}),makeQuery(id+"F47.opFillet","BLEND_FACE",FACE,{"disambiguationData":[OSD([subQ0,subQ9]),TDD([makeQuery(id+"F42.boolean.opBoolean","COPY",EDGE,{"disambiguationData":[TD([subQ79])],"derivedFrom":subQ11})])]}),makeQuery(id+"F47.opFillet","BLEND_FACE",FACE,{"disambiguationData":[OSD([subQ0,subQ9]),TDD([makeQuery(id+"F42.boolean.opBoolean","COPY",EDGE,{"disambiguationData":[TD([subQ72])],"derivedFrom":subQ11})])]}),makeQuery(id+"F47.opFillet","BLEND_FACE",FACE,{"disambiguationData":[OSD([subQ0,subQ9]),TDD([makeQuery(id+"F42.boolean.opBoolean","COPY",EDGE,{"disambiguationData":[TD([subQ64])],"derivedFrom":subQ11})])]}),makeQuery(id+"F47.opFillet","BLEND_FACE",FACE,{"disambiguationData":[OSD([subQ0,subQ9]),TDD([makeQuery(id+"F42.boolean.opBoolean","COPY",EDGE,{"disambiguationData":[TD([subQ58])],"derivedFrom":subQ11})])]}),makeQuery(id+"F47.opFillet","BLEND_FACE",FACE,{"disambiguationData":[OSD([subQ0,subQ9]),TDD([makeQuery(id+"F42.boolean.opBoolean","COPY",EDGE,{"disambiguationData":[TD([subQ51])],"derivedFrom":subQ11})])]}),makeQuery(id+"F47.opFillet","BLEND_FACE",FACE,{"disambiguationData":[OSD([subQ0,subQ9]),TDD([makeQuery(id+"F42.boolean.opBoolean","COPY",EDGE,{"disambiguationData":[TD([subQ44])],"derivedFrom":subQ11})])]}),makeQuery(id+"F47.opFillet","BLEND_FACE",FACE,{"disambiguationData":[OSD([subQ0,subQ9]),TDD([makeQuery(id+"F42.boolean.opBoolean","COPY",EDGE,{"disambiguationData":[TD([subQ37])],"derivedFrom":subQ11})])]}),makeQuery(id+"F47.opFillet","BLEND_FACE",FACE,{"disambiguationData":[OSD([subQ0,subQ9]),TDD([makeQuery(id+"F42.boolean.opBoolean","COPY",EDGE,{"disambiguationData":[TD([makeQuery(id+"F35.opLoft","SWEPT_FACE",FACE,{"disambiguationData":[OSD([subQ29,subQ28,subQ26,sQuery(id+"F22.wireOp",EDGE,"E28.12.1"),subQ25,subQ24])]})])],"derivedFrom":subQ11})])]}),makeQuery(id+"F47.opFillet","BLEND_FACE",FACE,{"disambiguationData":[OSD([subQ0,subQ9]),TDD([makeQuery(id+"F42.boolean.opBoolean","COPY",EDGE,{"disambiguationData":[TD([makeQuery(id+"F36.opLoft","SWEPT_FACE",FACE,{"disambiguationData":[OSD([subQ23,subQ22,subQ20,sQuery(id+"F22.wireOp",EDGE,"E28.13.1"),subQ19,subQ18])]})])],"derivedFrom":subQ11})])]}),makeQuery(id+"F47.opFillet","BLEND_FACE",FACE,{"disambiguationData":[OSD([subQ0,subQ9]),TDD([makeQuery(id+"F42.boolean.opBoolean","COPY",EDGE,{"disambiguationData":[TD([makeQuery(id+"F37.opLoft","SWEPT_FACE",FACE,{"disambiguationData":[OSD([subQ16,subQ15,subQ14,sQuery(id+"F22.wireOp",EDGE,"E28.14.1"),subQ13,subQ12])]})])],"derivedFrom":subQ11})])]}),makeQuery(id+"F47.opFillet","BLEND_FACE",FACE,{"disambiguationData":[OSD([subQ0,subQ9]),TDD([makeQuery(id+"F42.boolean.opBoolean","COPY",EDGE,{"disambiguationData":[TD([makeQuery(id+"F38.opLoft","SWEPT_FACE",FACE,{"disambiguationData":[OSD([subQ8,subQ7,subQ5,sQuery(id+"F22.wireOp",EDGE,"E28.15.1"),subQ4,subQ3])]})])],"derivedFrom":subQ11})])]})],"blendedInto":[makeQuery(id+"F47.opFillet","BLEND_FACE",FACE,{"disambiguationData":[OSD([subQ0,subQ9]),TDD([makeQuery(id+"F42.boolean.opBoolean","COPY",EDGE,{"disambiguationData":[TD([makeQuery(id+"F23.opLoft","SWEPT_FACE",FACE,{"disambiguationData":[OSD([sQuery(id+"F3.wireOp",EDGE,"E20.8.0"),subQ111,subQ109,subQ108,subQ107,sQuery(id+"F22.wireOp",EDGE,"E27.right")])]})])],"derivedFrom":subQ11})])]}),makeQuery(id+"F47.opFillet","BLEND_FACE",FACE,{"disambiguationData":[OSD([subQ0,subQ9]),TDD([makeQuery(id+"F42.boolean.opBoolean","COPY",EDGE,{"disambiguationData":[TD([subQ106])],"derivedFrom":subQ11})])]}),makeQuery(id+"F47.opFillet","BLEND_FACE",FACE,{"disambiguationData":[OSD([subQ0,subQ9]),TDD([makeQuery(id+"F42.boolean.opBoolean","COPY",EDGE,{"disambiguationData":[TD([subQ99])],"derivedFrom":subQ11})])]}),makeQuery(id+"F47.opFillet","BLEND_FACE",FACE,{"disambiguationData":[OSD([subQ0,subQ9]),TDD([makeQuery(id+"F42.boolean.opBoolean","COPY",EDGE,{"disambiguationData":[TD([subQ93])],"derivedFrom":subQ11})])]}),makeQuery(id+"F47.opFillet","BLEND_FACE",FACE,{"disambiguationData":[OSD([subQ0,subQ9]),TDD([makeQuery(id+"F42.boolean.opBoolean","COPY",EDGE,{"disambiguationData":[TD([subQ86])],"derivedFrom":subQ11})])]}),makeQuery(id+"F47.opFillet","BLEND_FACE",FACE,{"disambiguationData":[OSD([subQ0,subQ9]),TDD([makeQuery(id+"F42.boolean.opBoolean","COPY",EDGE,{"disambiguationData":[TD([subQ79])],"derivedFrom":subQ11})])]}),makeQuery(id+"F47.opFillet","BLEND_FACE",FACE,{"disambiguationData":[OSD([subQ0,subQ9]),TDD([makeQuery(id+"F42.boolean.opBoolean","COPY",EDGE,{"disambiguationData":[TD([subQ72])],"derivedFrom":subQ11})])]}),makeQuery(id+"F47.opFillet","BLEND_FACE",FACE,{"disambiguationData":[OSD([subQ0,subQ9]),TDD([makeQuery(id+"F42.boolean.opBoolean","COPY",EDGE,{"disambiguationData":[TD([subQ64])],"derivedFrom":subQ11})])]}),makeQuery(id+"F47.opFillet","BLEND_FACE",FACE,{"disambiguationData":[OSD([subQ0,subQ9]),TDD([makeQuery(id+"F42.boolean.opBoolean","COPY",EDGE,{"disambiguationData":[TD([subQ58])],"derivedFrom":subQ11})])]}),makeQuery(id+"F47.opFillet","BLEND_FACE",FACE,{"disambiguationData":[OSD([subQ0,subQ9]),TDD([makeQuery(id+"F42.boolean.opBoolean","COPY",EDGE,{"disambiguationData":[TD([subQ51])],"derivedFrom":subQ11})])]}),makeQuery(id+"F47.opFillet","BLEND_FACE",FACE,{"disambiguationData":[OSD([subQ0,subQ9]),TDD([makeQuery(id+"F42.boolean.opBoolean","COPY",EDGE,{"disambiguationData":[TD([subQ44])],"derivedFrom":subQ11})])]}),makeQuery(id+"F47.opFillet","BLEND_FACE",FACE,{"disambiguationData":[OSD([subQ0,subQ9]),TDD([makeQuery(id+"F42.boolean.opBoolean","COPY",EDGE,{"disambiguationData":[TD([subQ37])],"derivedFrom":subQ11})])]}),makeQuery(id+"F47.opFillet","BLEND_FACE",FACE,{"disambiguationData":[OSD([subQ0,subQ9]),TDD([makeQuery(id+"F42.boolean.opBoolean","COPY",EDGE,{"disambiguationData":[TD([makeQuery(id+"F35.opLoft","SWEPT_FACE",FACE,{"disambiguationData":[OSD([subQ29,subQ28,subQ26,sQuery(id+"F22.wireOp",EDGE,"E28.12.1"),subQ25,subQ24])]})])],"derivedFrom":subQ11})])]}),makeQuery(id+"F47.opFillet","BLEND_FACE",FACE,{"disambiguationData":[OSD([subQ0,subQ9]),TDD([makeQuery(id+"F42.boolean.opBoolean","COPY",EDGE,{"disambiguationData":[TD([makeQuery(id+"F36.opLoft","SWEPT_FACE",FACE,{"disambiguationData":[OSD([subQ23,subQ22,subQ20,sQuery(id+"F22.wireOp",EDGE,"E28.13.1"),subQ19,subQ18])]})])],"derivedFrom":subQ11})])]}),makeQuery(id+"F47.opFillet","BLEND_FACE",FACE,{"disambiguationData":[OSD([subQ0,subQ9]),TDD([makeQuery(id+"F42.boolean.opBoolean","COPY",EDGE,{"disambiguationData":[TD([makeQuery(id+"F37.opLoft","SWEPT_FACE",FACE,{"disambiguationData":[OSD([subQ16,subQ15,subQ14,sQuery(id+"F22.wireOp",EDGE,"E28.14.1"),subQ13,subQ12])]})])],"derivedFrom":subQ11})])]}),makeQuery(id+"F47.opFillet","BLEND_FACE",FACE,{"disambiguationData":[OSD([subQ0,subQ9]),TDD([makeQuery(id+"F42.boolean.opBoolean","COPY",EDGE,{"disambiguationData":[TD([makeQuery(id+"F38.opLoft","SWEPT_FACE",FACE,{"disambiguationData":[OSD([subQ8,subQ7,subQ5,sQuery(id+"F22.wireOp",EDGE,"E28.15.1"),subQ4,subQ3])]})])],"derivedFrom":subQ11})])]})]});}
            var Q8;
            {var subQ0=sQuery(id+"F41.wireOp",EDGE,"E34");var subQ1=sQuery(id+"F41.wireOp",EDGE,"E32");Q8=makeQuery(id+"F42.boolean.opBoolean","INTERSECT",EDGE,{"derivedFrom":[makeQuery(id+"F34.opLoft","SWEPT_FACE",FACE,{"disambiguationData":[OSD([sQuery(id+"F3.wireOp",EDGE,"E20.3.0"),sQuery(id+"F3.wireOp",EDGE,"E20.3.1"),sQuery(id+"F3.wireOp",EDGE,"E20.3.3"),sQuery(id+"F22.wireOp",EDGE,"E28.11.1"),sQuery(id+"F22.wireOp",EDGE,"E28.11.2"),sQuery(id+"F22.wireOp",EDGE,"E28.11.3")])]}),makeQuery(id+"F42.opRevolve","SWEPT_FACE",FACE,{"disambiguationData":[OSD([subQ1]),TDD([makeQuery(id+"F41.imprint","IMPRINT",EDGE,{"disambiguationData":[TD([[makeQuery(id+"F41.imprint","INTERSECT",VERTEX,{"disambiguationData":[OD(0.0)],"derivedFrom":[subQ1,subQ0]}),-1.0]])],"derivedFrom":subQ1})])]})]});}
            var Q9;
            {var subQ0=sQuery(id+"F22.wireOp",EDGE,"E28.11.3");var subQ1=sQuery(id+"F22.wireOp",EDGE,"E28.11.2");var subQ2=sQuery(id+"F22.wireOp",EDGE,"E28.11.0");var subQ3=sQuery(id+"F3.wireOp",EDGE,"E20.3.3");var subQ4=sQuery(id+"F3.wireOp",EDGE,"E20.3.1");var subQ5=makeQuery(id+"F34.opLoft","SWEPT_FACE",FACE,{"disambiguationData":[OSD([subQ4,sQuery(id+"F3.wireOp",EDGE,"E20.3.2"),subQ3,subQ2,subQ1,subQ0])]});var subQ6=sQuery(id+"F22.wireOp",EDGE,"E28.11.1");var subQ7=sQuery(id+"F41.wireOp",EDGE,"E34");var subQ8=sQuery(id+"F41.wireOp",EDGE,"E32");Q9=makeQuery(id+"F44.opFillet","BLEND_EDGE",EDGE,{"blendedFrom":[makeQuery(id+"F40.boolean.opBoolean","INTERSECT",EDGE,{"derivedFrom":[subQ5,makeQuery(id+"F40.opExtrude","CAP_FACE",FACE,{"disambiguationData":[OSD([sQuery(id+"F39.wireOp",EDGE,"E29"),sQuery(id+"F39.wireOp",EDGE,"E30")])],"isStart":true})]}),makeQuery(id+"F42.boolean.opBoolean","COPY",FACE,{"disambiguationData":[TD([makeQuery(id+"F34.opLoft","SWEPT_FACE",FACE,{"disambiguationData":[OSD([sQuery(id+"F3.wireOp",EDGE,"E20.3.0"),subQ4,subQ3,subQ6,subQ1,subQ0])]})])],"derivedFrom":makeQuery(id+"F42.opRevolve","SWEPT_FACE",FACE,{"disambiguationData":[OSD([subQ8]),TDD([makeQuery(id+"F41.imprint","IMPRINT",EDGE,{"disambiguationData":[TD([[makeQuery(id+"F41.imprint","INTERSECT",VERTEX,{"disambiguationData":[OD(0.0)],"derivedFrom":[subQ8,subQ7]}),-1.0]])],"derivedFrom":subQ8})])]})})],"blendedInto":[makeQuery(id+"F42.boolean.opBoolean","COPY",FACE,{"disambiguationData":[TD([makeQuery(id+"F34.opLoft","SWEPT_FACE",FACE,{"disambiguationData":[OSD([sQuery(id+"F3.wireOp",EDGE,"E20.3.0"),subQ4,subQ3,subQ6,subQ1,subQ0])]})])],"derivedFrom":makeQuery(id+"F42.opRevolve","SWEPT_FACE",FACE,{"disambiguationData":[OSD([subQ8]),TDD([makeQuery(id+"F41.imprint","IMPRINT",EDGE,{"disambiguationData":[TD([[makeQuery(id+"F41.imprint","INTERSECT",VERTEX,{"disambiguationData":[OD(0.0)],"derivedFrom":[subQ8,subQ7]}),-1.0]])],"derivedFrom":subQ8})])]})})]});}
            var Q10;
            {var subQ0=sQuery(id+"F3.wireOp",EDGE,"E20.2.3");var subQ1=sQuery(id+"F3.wireOp",EDGE,"E20.2.1");var subQ2=sQuery(id+"F3.wireOp",EDGE,"E20.2.0");var subQ3=makeQuery(id+"F33.opLoft","SWEPT_FACE",FACE,{"disambiguationData":[OSD([subQ2,subQ1,subQ0,sQuery(id+"F22.wireOp",EDGE,"E28.10.1"),sQuery(id+"F22.wireOp",EDGE,"E28.10.2"),sQuery(id+"F22.wireOp",EDGE,"E28.10.3")])]});var subQ52=sQuery(id+"F3.wireOp",EDGE,"E20.7.0");var subQ61=makeQuery(id+"F14.opLoft","CAP_FACE",FACE,{"disambiguationData":[OSD([makeQuery(id+"F3.imprint","IMPRINT",FACE,{"disambiguationData":[TD([[makeQuery(id+"F3.imprint","IMPRINT",EDGE,{"derivedFrom":subQ52}),-1.0]])]})])],"isStart":true});var subQ74=sQuery(id+"F3.wireOp",EDGE,"E18.bottom");var subQ79=makeQuery(id+"F5.opLoft","CAP_FACE",FACE,{"disambiguationData":[OSD([makeQuery(id+"F3.imprint","IMPRINT",FACE,{"disambiguationData":[TD([[makeQuery(id+"F3.imprint","IMPRINT",EDGE,{"derivedFrom":subQ74}),1.0]])]})])],"isStart":true});Q10=makeQuery(id+"F45.opFillet","BLEND_EDGE",EDGE,{"blendedFrom":[makeQuery(id+"F33.boolean.opBoolean","INTERSECT",EDGE,{"derivedFrom":[makeQuery(id+"F32.boolean.opBoolean","SPLIT",FACE,{"disambiguationData":[TD([subQ61])],"derivedFrom":makeQuery(id+"F31.boolean.opBoolean","SPLIT",FACE,{"disambiguationData":[TD([subQ61])],"derivedFrom":makeQuery(id+"F30.boolean.opBoolean","SPLIT",FACE,{"disambiguationData":[TD([subQ79])],"derivedFrom":makeQuery(id+"F29.boolean.opBoolean","SPLIT",FACE,{"disambiguationData":[TD([subQ79])],"derivedFrom":makeQuery(id+"F28.boolean.opBoolean","SPLIT",FACE,{"disambiguationData":[TD([subQ79])],"derivedFrom":makeQuery(id+"F27.boolean.opBoolean","SPLIT",FACE,{"disambiguationData":[TD([subQ79])],"derivedFrom":makeQuery(id+"F26.boolean.opBoolean","SPLIT",FACE,{"disambiguationData":[TD([subQ79])],"derivedFrom":makeQuery(id+"F25.boolean.opBoolean","SPLIT",FACE,{"disambiguationData":[TD([subQ79])],"derivedFrom":makeQuery(id+"F24.boolean.opBoolean","SPLIT",FACE,{"disambiguationData":[TD([subQ79])],"derivedFrom":makeQuery(id+"F1.opRevolve","SWEPT_FACE",FACE,{"disambiguationData":[OSD([sQuery(id+"F0.wireOp",EDGE,"E4")])]})})})})})})})})})}),subQ3]}),subQ3],"blendedInto":[subQ3]});}
            var Q11;
            {var subQ0=sQuery(id+"F41.wireOp",EDGE,"E37");var subQ1=makeQuery(id+"F42.opRevolve","SWEPT_FACE",FACE,{"disambiguationData":[OSD([subQ0])]});var subQ2=makeQuery(id+"F40.opExtrude","CAP_FACE",FACE,{"disambiguationData":[OSD([sQuery(id+"F39.wireOp",EDGE,"E29"),sQuery(id+"F39.wireOp",EDGE,"E30")])],"isStart":true});var subQ3=sQuery(id+"F22.wireOp",EDGE,"E28.15.3");var subQ4=sQuery(id+"F22.wireOp",EDGE,"E28.15.2");var subQ5=sQuery(id+"F3.wireOp",EDGE,"E20.7.3");var subQ7=sQuery(id+"F3.wireOp",EDGE,"E20.7.1");var subQ8=sQuery(id+"F3.wireOp",EDGE,"E20.7.0");var subQ9=sQuery(id+"F41.wireOp",EDGE,"E38");var subQ10=makeQuery(id+"F42.opRevolve","SWEPT_FACE",FACE,{"disambiguationData":[OSD([subQ9])]});var subQ11=makeQuery(id+"F42.opRevolve","SWEPT_EDGE",EDGE,{"disambiguationData":[OSD([subQ0,subQ9])]});var subQ12=sQuery(id+"F22.wireOp",EDGE,"E28.14.3");var subQ13=sQuery(id+"F22.wireOp",EDGE,"E28.14.2");var subQ14=sQuery(id+"F3.wireOp",EDGE,"E20.6.3");var subQ15=sQuery(id+"F3.wireOp",EDGE,"E20.6.1");var subQ16=sQuery(id+"F3.wireOp",EDGE,"E20.6.0");var subQ18=sQuery(id+"F22.wireOp",EDGE,"E28.13.3");var subQ19=sQuery(id+"F22.wireOp",EDGE,"E28.13.2");var subQ20=sQuery(id+"F3.wireOp",EDGE,"E20.5.3");var subQ22=sQuery(id+"F3.wireOp",EDGE,"E20.5.1");var subQ23=sQuery(id+"F3.wireOp",EDGE,"E20.5.0");var subQ24=sQuery(id+"F22.wireOp",EDGE,"E28.12.3");var subQ25=sQuery(id+"F22.wireOp",EDGE,"E28.12.2");var subQ26=sQuery(id+"F3.wireOp",EDGE,"E20.4.3");var subQ28=sQuery(id+"F3.wireOp",EDGE,"E20.4.1");var subQ29=sQuery(id+"F3.wireOp",EDGE,"E20.4.0");var subQ30=sQuery(id+"F22.wireOp",EDGE,"E28.11.3");var subQ31=sQuery(id+"F22.wireOp",EDGE,"E28.11.2");var subQ32=sQuery(id+"F3.wireOp",EDGE,"E20.3.3");var subQ34=sQuery(id+"F3.wireOp",EDGE,"E20.3.1");var subQ35=sQuery(id+"F3.wireOp",EDGE,"E20.3.0");var subQ36=sQuery(id+"F22.wireOp",EDGE,"E28.10.3");var subQ37=sQuery(id+"F22.wireOp",EDGE,"E28.10.2");var subQ38=sQuery(id+"F3.wireOp",EDGE,"E20.2.3");var subQ40=sQuery(id+"F3.wireOp",EDGE,"E20.2.1");var subQ42=sQuery(id+"F3.wireOp",EDGE,"E20.2.0");var subQ43=makeQuery(id+"F33.opLoft","SWEPT_FACE",FACE,{"disambiguationData":[OSD([subQ42,subQ40,subQ38,sQuery(id+"F22.wireOp",EDGE,"E28.10.1"),subQ37,subQ36])]});var subQ44=sQuery(id+"F22.wireOp",EDGE,"E28.9.3");var subQ45=sQuery(id+"F22.wireOp",EDGE,"E28.9.2");var subQ46=sQuery(id+"F3.wireOp",EDGE,"E20.1.3");var subQ48=sQuery(id+"F3.wireOp",EDGE,"E20.1.1");var subQ49=sQuery(id+"F3.wireOp",EDGE,"E20.1.0");var subQ50=makeQuery(id+"F32.opLoft","SWEPT_FACE",FACE,{"disambiguationData":[OSD([subQ49,subQ48,subQ46,sQuery(id+"F22.wireOp",EDGE,"E28.9.1"),subQ45,subQ44])]});var subQ51=sQuery(id+"F22.wireOp",EDGE,"E28.8.3");var subQ52=sQuery(id+"F22.wireOp",EDGE,"E28.8.2");var subQ54=sQuery(id+"F3.wireOp",EDGE,"E18.top");var subQ55=sQuery(id+"F3.wireOp",EDGE,"E18.bottom");var subQ56=sQuery(id+"F3.wireOp",EDGE,"E18.left");var subQ57=makeQuery(id+"F31.opLoft","SWEPT_FACE",FACE,{"disambiguationData":[OSD([subQ55,subQ54,subQ56,sQuery(id+"F22.wireOp",EDGE,"E28.8.1"),subQ52,subQ51])]});var subQ58=sQuery(id+"F22.wireOp",EDGE,"E28.7.3");var subQ59=sQuery(id+"F22.wireOp",EDGE,"E28.7.2");var subQ60=sQuery(id+"F3.wireOp",EDGE,"E20.15.3");var subQ61=sQuery(id+"F3.wireOp",EDGE,"E20.15.1");var subQ62=sQuery(id+"F3.wireOp",EDGE,"E20.15.0");var subQ63=makeQuery(id+"F30.opLoft","SWEPT_FACE",FACE,{"disambiguationData":[OSD([subQ62,subQ61,subQ60,sQuery(id+"F22.wireOp",EDGE,"E28.7.1"),subQ59,subQ58])]});var subQ65=sQuery(id+"F22.wireOp",EDGE,"E28.6.3");var subQ66=sQuery(id+"F22.wireOp",EDGE,"E28.6.2");var subQ67=sQuery(id+"F3.wireOp",EDGE,"E20.14.3");var subQ69=sQuery(id+"F3.wireOp",EDGE,"E20.14.1");var subQ70=sQuery(id+"F3.wireOp",EDGE,"E20.14.0");var subQ71=makeQuery(id+"F29.opLoft","SWEPT_FACE",FACE,{"disambiguationData":[OSD([subQ70,subQ69,subQ67,sQuery(id+"F22.wireOp",EDGE,"E28.6.1"),subQ66,subQ65])]});var subQ72=sQuery(id+"F22.wireOp",EDGE,"E28.5.3");var subQ73=sQuery(id+"F22.wireOp",EDGE,"E28.5.2");var subQ74=sQuery(id+"F3.wireOp",EDGE,"E20.13.3");var subQ76=sQuery(id+"F3.wireOp",EDGE,"E20.13.1");var subQ77=sQuery(id+"F3.wireOp",EDGE,"E20.13.0");var subQ78=makeQuery(id+"F28.opLoft","SWEPT_FACE",FACE,{"disambiguationData":[OSD([subQ77,subQ76,subQ74,sQuery(id+"F22.wireOp",EDGE,"E28.5.1"),subQ73,subQ72])]});var subQ79=sQuery(id+"F22.wireOp",EDGE,"E28.4.3");var subQ80=sQuery(id+"F22.wireOp",EDGE,"E28.4.2");var subQ81=sQuery(id+"F3.wireOp",EDGE,"E20.12.3");var subQ83=sQuery(id+"F3.wireOp",EDGE,"E20.12.1");var subQ84=sQuery(id+"F3.wireOp",EDGE,"E20.12.0");var subQ85=makeQuery(id+"F27.opLoft","SWEPT_FACE",FACE,{"disambiguationData":[OSD([subQ84,subQ83,subQ81,sQuery(id+"F22.wireOp",EDGE,"E28.4.1"),subQ80,subQ79])]});var subQ86=sQuery(id+"F22.wireOp",EDGE,"E28.3.3");var subQ87=sQuery(id+"F22.wireOp",EDGE,"E28.3.2");var subQ88=sQuery(id+"F3.wireOp",EDGE,"E20.11.3");var subQ90=sQuery(id+"F3.wireOp",EDGE,"E20.11.1");var subQ91=sQuery(id+"F3.wireOp",EDGE,"E20.11.0");var subQ92=makeQuery(id+"F26.opLoft","SWEPT_FACE",FACE,{"disambiguationData":[OSD([subQ91,subQ90,subQ88,sQuery(id+"F22.wireOp",EDGE,"E28.3.1"),subQ87,subQ86])]});var subQ93=sQuery(id+"F22.wireOp",EDGE,"E28.2.3");var subQ94=sQuery(id+"F22.wireOp",EDGE,"E28.2.2");var subQ95=sQuery(id+"F3.wireOp",EDGE,"E20.10.3");var subQ96=sQuery(id+"F3.wireOp",EDGE,"E20.10.1");var subQ97=sQuery(id+"F3.wireOp",EDGE,"E20.10.0");var subQ98=makeQuery(id+"F25.opLoft","SWEPT_FACE",FACE,{"disambiguationData":[OSD([subQ97,subQ96,subQ95,sQuery(id+"F22.wireOp",EDGE,"E28.2.1"),subQ94,subQ93])]});var subQ100=sQuery(id+"F22.wireOp",EDGE,"E28.1.3");var subQ101=sQuery(id+"F22.wireOp",EDGE,"E28.1.2");var subQ102=sQuery(id+"F3.wireOp",EDGE,"E20.9.3");var subQ103=sQuery(id+"F3.wireOp",EDGE,"E20.9.1");var subQ104=sQuery(id+"F3.wireOp",EDGE,"E20.9.0");var subQ105=makeQuery(id+"F24.opLoft","SWEPT_FACE",FACE,{"disambiguationData":[OSD([subQ104,subQ103,subQ102,sQuery(id+"F22.wireOp",EDGE,"E28.1.1"),subQ101,subQ100])]});var subQ106=sQuery(id+"F22.wireOp",EDGE,"E27.top");var subQ107=sQuery(id+"F22.wireOp",EDGE,"E27.bottom");var subQ108=sQuery(id+"F3.wireOp",EDGE,"E20.8.3");var subQ110=sQuery(id+"F3.wireOp",EDGE,"E20.8.1");var subQ114=makeQuery(id+"F42.boolean.opBoolean","COPY",FACE,{"disambiguationData":[TD([subQ43])],"derivedFrom":subQ10});var subQ146=makeQuery(id+"F14.opLoft","CAP_FACE",FACE,{"disambiguationData":[OSD([makeQuery(id+"F3.imprint","IMPRINT",FACE,{"disambiguationData":[TD([[makeQuery(id+"F3.imprint","IMPRINT",EDGE,{"derivedFrom":subQ8}),-1.0]])]})])],"isStart":true});var subQ157=makeQuery(id+"F5.opLoft","CAP_FACE",FACE,{"disambiguationData":[OSD([makeQuery(id+"F3.imprint","IMPRINT",FACE,{"disambiguationData":[TD([[makeQuery(id+"F3.imprint","IMPRINT",EDGE,{"derivedFrom":subQ55}),1.0]])]})])],"isStart":true});var subQ186=makeQuery(id+"F33.boolean.opBoolean","INTERSECT",EDGE,{"derivedFrom":[makeQuery(id+"F32.boolean.opBoolean","SPLIT",FACE,{"disambiguationData":[TD([subQ146])],"derivedFrom":makeQuery(id+"F31.boolean.opBoolean","SPLIT",FACE,{"disambiguationData":[TD([subQ146])],"derivedFrom":makeQuery(id+"F30.boolean.opBoolean","SPLIT",FACE,{"disambiguationData":[TD([subQ157])],"derivedFrom":makeQuery(id+"F29.boolean.opBoolean","SPLIT",FACE,{"disambiguationData":[TD([subQ157])],"derivedFrom":makeQuery(id+"F28.boolean.opBoolean","SPLIT",FACE,{"disambiguationData":[TD([subQ157])],"derivedFrom":makeQuery(id+"F27.boolean.opBoolean","SPLIT",FACE,{"disambiguationData":[TD([subQ157])],"derivedFrom":makeQuery(id+"F26.boolean.opBoolean","SPLIT",FACE,{"disambiguationData":[TD([subQ157])],"derivedFrom":makeQuery(id+"F25.boolean.opBoolean","SPLIT",FACE,{"disambiguationData":[TD([subQ157])],"derivedFrom":makeQuery(id+"F24.boolean.opBoolean","SPLIT",FACE,{"disambiguationData":[TD([subQ157])],"derivedFrom":makeQuery(id+"F1.opRevolve","SWEPT_FACE",FACE,{"disambiguationData":[OSD([sQuery(id+"F0.wireOp",EDGE,"E4")])]})})})})})})})})})}),subQ43]});Q11=makeQuery(id+"F48.opFillet","BLEND_EDGE",EDGE,{"blendedFrom":[makeQuery(id+"F47.opFillet","TWEAK_EDGE",EDGE,{"derivedFrom":[makeQuery(id+"F45.opFillet","BLEND_VERTEX",VERTEX,{"blendedFrom":[subQ186,subQ43,subQ114],"blendedInto":[subQ43,subQ114]}),makeQuery(id+"F45.opFillet","BLEND_VERTEX",VERTEX,{"blendedFrom":[subQ186,makeQuery(id+"F42.boolean.opBoolean","MERGE",FACE,{"derivedFrom":[subQ2,subQ1]}),subQ114],"blendedInto":[makeQuery(id+"F42.boolean.opBoolean","MERGE",FACE,{"derivedFrom":[subQ2,subQ1]}),subQ114]})]}),makeQuery(id+"F47.opFillet","BLEND_FACE",FACE,{"disambiguationData":[OSD([subQ0,subQ9]),TDD([makeQuery(id+"F42.boolean.opBoolean","COPY",EDGE,{"disambiguationData":[TD([makeQuery(id+"F23.opLoft","SWEPT_FACE",FACE,{"disambiguationData":[OSD([sQuery(id+"F3.wireOp",EDGE,"E20.8.0"),subQ110,subQ108,subQ107,subQ106,sQuery(id+"F22.wireOp",EDGE,"E27.right")])]})])],"derivedFrom":subQ11})])]}),makeQuery(id+"F47.opFillet","BLEND_FACE",FACE,{"disambiguationData":[OSD([subQ0,subQ9]),TDD([makeQuery(id+"F42.boolean.opBoolean","COPY",EDGE,{"disambiguationData":[TD([subQ105])],"derivedFrom":subQ11})])]}),makeQuery(id+"F47.opFillet","BLEND_FACE",FACE,{"disambiguationData":[OSD([subQ0,subQ9]),TDD([makeQuery(id+"F42.boolean.opBoolean","COPY",EDGE,{"disambiguationData":[TD([subQ98])],"derivedFrom":subQ11})])]}),makeQuery(id+"F47.opFillet","BLEND_FACE",FACE,{"disambiguationData":[OSD([subQ0,subQ9]),TDD([makeQuery(id+"F42.boolean.opBoolean","COPY",EDGE,{"disambiguationData":[TD([subQ92])],"derivedFrom":subQ11})])]}),makeQuery(id+"F47.opFillet","BLEND_FACE",FACE,{"disambiguationData":[OSD([subQ0,subQ9]),TDD([makeQuery(id+"F42.boolean.opBoolean","COPY",EDGE,{"disambiguationData":[TD([subQ85])],"derivedFrom":subQ11})])]}),makeQuery(id+"F47.opFillet","BLEND_FACE",FACE,{"disambiguationData":[OSD([subQ0,subQ9]),TDD([makeQuery(id+"F42.boolean.opBoolean","COPY",EDGE,{"disambiguationData":[TD([subQ78])],"derivedFrom":subQ11})])]}),makeQuery(id+"F47.opFillet","BLEND_FACE",FACE,{"disambiguationData":[OSD([subQ0,subQ9]),TDD([makeQuery(id+"F42.boolean.opBoolean","COPY",EDGE,{"disambiguationData":[TD([subQ71])],"derivedFrom":subQ11})])]}),makeQuery(id+"F47.opFillet","BLEND_FACE",FACE,{"disambiguationData":[OSD([subQ0,subQ9]),TDD([makeQuery(id+"F42.boolean.opBoolean","COPY",EDGE,{"disambiguationData":[TD([subQ63])],"derivedFrom":subQ11})])]}),makeQuery(id+"F47.opFillet","BLEND_FACE",FACE,{"disambiguationData":[OSD([subQ0,subQ9]),TDD([makeQuery(id+"F42.boolean.opBoolean","COPY",EDGE,{"disambiguationData":[TD([subQ57])],"derivedFrom":subQ11})])]}),makeQuery(id+"F47.opFillet","BLEND_FACE",FACE,{"disambiguationData":[OSD([subQ0,subQ9]),TDD([makeQuery(id+"F42.boolean.opBoolean","COPY",EDGE,{"disambiguationData":[TD([subQ50])],"derivedFrom":subQ11})])]}),makeQuery(id+"F47.opFillet","BLEND_FACE",FACE,{"disambiguationData":[OSD([subQ0,subQ9]),TDD([makeQuery(id+"F42.boolean.opBoolean","COPY",EDGE,{"disambiguationData":[TD([subQ43])],"derivedFrom":subQ11})])]}),makeQuery(id+"F47.opFillet","BLEND_FACE",FACE,{"disambiguationData":[OSD([subQ0,subQ9]),TDD([makeQuery(id+"F42.boolean.opBoolean","COPY",EDGE,{"disambiguationData":[TD([makeQuery(id+"F34.opLoft","SWEPT_FACE",FACE,{"disambiguationData":[OSD([subQ35,subQ34,subQ32,sQuery(id+"F22.wireOp",EDGE,"E28.11.1"),subQ31,subQ30])]})])],"derivedFrom":subQ11})])]}),makeQuery(id+"F47.opFillet","BLEND_FACE",FACE,{"disambiguationData":[OSD([subQ0,subQ9]),TDD([makeQuery(id+"F42.boolean.opBoolean","COPY",EDGE,{"disambiguationData":[TD([makeQuery(id+"F35.opLoft","SWEPT_FACE",FACE,{"disambiguationData":[OSD([subQ29,subQ28,subQ26,sQuery(id+"F22.wireOp",EDGE,"E28.12.1"),subQ25,subQ24])]})])],"derivedFrom":subQ11})])]}),makeQuery(id+"F47.opFillet","BLEND_FACE",FACE,{"disambiguationData":[OSD([subQ0,subQ9]),TDD([makeQuery(id+"F42.boolean.opBoolean","COPY",EDGE,{"disambiguationData":[TD([makeQuery(id+"F36.opLoft","SWEPT_FACE",FACE,{"disambiguationData":[OSD([subQ23,subQ22,subQ20,sQuery(id+"F22.wireOp",EDGE,"E28.13.1"),subQ19,subQ18])]})])],"derivedFrom":subQ11})])]}),makeQuery(id+"F47.opFillet","BLEND_FACE",FACE,{"disambiguationData":[OSD([subQ0,subQ9]),TDD([makeQuery(id+"F42.boolean.opBoolean","COPY",EDGE,{"disambiguationData":[TD([makeQuery(id+"F37.opLoft","SWEPT_FACE",FACE,{"disambiguationData":[OSD([subQ16,subQ15,subQ14,sQuery(id+"F22.wireOp",EDGE,"E28.14.1"),subQ13,subQ12])]})])],"derivedFrom":subQ11})])]}),makeQuery(id+"F47.opFillet","BLEND_FACE",FACE,{"disambiguationData":[OSD([subQ0,subQ9]),TDD([makeQuery(id+"F42.boolean.opBoolean","COPY",EDGE,{"disambiguationData":[TD([makeQuery(id+"F38.opLoft","SWEPT_FACE",FACE,{"disambiguationData":[OSD([subQ8,subQ7,subQ5,sQuery(id+"F22.wireOp",EDGE,"E28.15.1"),subQ4,subQ3])]})])],"derivedFrom":subQ11})])]})],"blendedInto":[makeQuery(id+"F47.opFillet","BLEND_FACE",FACE,{"disambiguationData":[OSD([subQ0,subQ9]),TDD([makeQuery(id+"F42.boolean.opBoolean","COPY",EDGE,{"disambiguationData":[TD([makeQuery(id+"F23.opLoft","SWEPT_FACE",FACE,{"disambiguationData":[OSD([sQuery(id+"F3.wireOp",EDGE,"E20.8.0"),subQ110,subQ108,subQ107,subQ106,sQuery(id+"F22.wireOp",EDGE,"E27.right")])]})])],"derivedFrom":subQ11})])]}),makeQuery(id+"F47.opFillet","BLEND_FACE",FACE,{"disambiguationData":[OSD([subQ0,subQ9]),TDD([makeQuery(id+"F42.boolean.opBoolean","COPY",EDGE,{"disambiguationData":[TD([subQ105])],"derivedFrom":subQ11})])]}),makeQuery(id+"F47.opFillet","BLEND_FACE",FACE,{"disambiguationData":[OSD([subQ0,subQ9]),TDD([makeQuery(id+"F42.boolean.opBoolean","COPY",EDGE,{"disambiguationData":[TD([subQ98])],"derivedFrom":subQ11})])]}),makeQuery(id+"F47.opFillet","BLEND_FACE",FACE,{"disambiguationData":[OSD([subQ0,subQ9]),TDD([makeQuery(id+"F42.boolean.opBoolean","COPY",EDGE,{"disambiguationData":[TD([subQ92])],"derivedFrom":subQ11})])]}),makeQuery(id+"F47.opFillet","BLEND_FACE",FACE,{"disambiguationData":[OSD([subQ0,subQ9]),TDD([makeQuery(id+"F42.boolean.opBoolean","COPY",EDGE,{"disambiguationData":[TD([subQ85])],"derivedFrom":subQ11})])]}),makeQuery(id+"F47.opFillet","BLEND_FACE",FACE,{"disambiguationData":[OSD([subQ0,subQ9]),TDD([makeQuery(id+"F42.boolean.opBoolean","COPY",EDGE,{"disambiguationData":[TD([subQ78])],"derivedFrom":subQ11})])]}),makeQuery(id+"F47.opFillet","BLEND_FACE",FACE,{"disambiguationData":[OSD([subQ0,subQ9]),TDD([makeQuery(id+"F42.boolean.opBoolean","COPY",EDGE,{"disambiguationData":[TD([subQ71])],"derivedFrom":subQ11})])]}),makeQuery(id+"F47.opFillet","BLEND_FACE",FACE,{"disambiguationData":[OSD([subQ0,subQ9]),TDD([makeQuery(id+"F42.boolean.opBoolean","COPY",EDGE,{"disambiguationData":[TD([subQ63])],"derivedFrom":subQ11})])]}),makeQuery(id+"F47.opFillet","BLEND_FACE",FACE,{"disambiguationData":[OSD([subQ0,subQ9]),TDD([makeQuery(id+"F42.boolean.opBoolean","COPY",EDGE,{"disambiguationData":[TD([subQ57])],"derivedFrom":subQ11})])]}),makeQuery(id+"F47.opFillet","BLEND_FACE",FACE,{"disambiguationData":[OSD([subQ0,subQ9]),TDD([makeQuery(id+"F42.boolean.opBoolean","COPY",EDGE,{"disambiguationData":[TD([subQ50])],"derivedFrom":subQ11})])]}),makeQuery(id+"F47.opFillet","BLEND_FACE",FACE,{"disambiguationData":[OSD([subQ0,subQ9]),TDD([makeQuery(id+"F42.boolean.opBoolean","COPY",EDGE,{"disambiguationData":[TD([subQ43])],"derivedFrom":subQ11})])]}),makeQuery(id+"F47.opFillet","BLEND_FACE",FACE,{"disambiguationData":[OSD([subQ0,subQ9]),TDD([makeQuery(id+"F42.boolean.opBoolean","COPY",EDGE,{"disambiguationData":[TD([makeQuery(id+"F34.opLoft","SWEPT_FACE",FACE,{"disambiguationData":[OSD([subQ35,subQ34,subQ32,sQuery(id+"F22.wireOp",EDGE,"E28.11.1"),subQ31,subQ30])]})])],"derivedFrom":subQ11})])]}),makeQuery(id+"F47.opFillet","BLEND_FACE",FACE,{"disambiguationData":[OSD([subQ0,subQ9]),TDD([makeQuery(id+"F42.boolean.opBoolean","COPY",EDGE,{"disambiguationData":[TD([makeQuery(id+"F35.opLoft","SWEPT_FACE",FACE,{"disambiguationData":[OSD([subQ29,subQ28,subQ26,sQuery(id+"F22.wireOp",EDGE,"E28.12.1"),subQ25,subQ24])]})])],"derivedFrom":subQ11})])]}),makeQuery(id+"F47.opFillet","BLEND_FACE",FACE,{"disambiguationData":[OSD([subQ0,subQ9]),TDD([makeQuery(id+"F42.boolean.opBoolean","COPY",EDGE,{"disambiguationData":[TD([makeQuery(id+"F36.opLoft","SWEPT_FACE",FACE,{"disambiguationData":[OSD([subQ23,subQ22,subQ20,sQuery(id+"F22.wireOp",EDGE,"E28.13.1"),subQ19,subQ18])]})])],"derivedFrom":subQ11})])]}),makeQuery(id+"F47.opFillet","BLEND_FACE",FACE,{"disambiguationData":[OSD([subQ0,subQ9]),TDD([makeQuery(id+"F42.boolean.opBoolean","COPY",EDGE,{"disambiguationData":[TD([makeQuery(id+"F37.opLoft","SWEPT_FACE",FACE,{"disambiguationData":[OSD([subQ16,subQ15,subQ14,sQuery(id+"F22.wireOp",EDGE,"E28.14.1"),subQ13,subQ12])]})])],"derivedFrom":subQ11})])]}),makeQuery(id+"F47.opFillet","BLEND_FACE",FACE,{"disambiguationData":[OSD([subQ0,subQ9]),TDD([makeQuery(id+"F42.boolean.opBoolean","COPY",EDGE,{"disambiguationData":[TD([makeQuery(id+"F38.opLoft","SWEPT_FACE",FACE,{"disambiguationData":[OSD([subQ8,subQ7,subQ5,sQuery(id+"F22.wireOp",EDGE,"E28.15.1"),subQ4,subQ3])]})])],"derivedFrom":subQ11})])]})]});}
            var Q12;
            {var subQ0=sQuery(id+"F22.wireOp",EDGE,"E28.10.0");var subQ1=sQuery(id+"F22.wireOp",EDGE,"E28.10.1");var subQ2=sQuery(id+"F22.wireOp",EDGE,"E28.10.2");var subQ3=sQuery(id+"F22.wireOp",EDGE,"E28.10.3");var subQ4=sQuery(id+"F3.wireOp",EDGE,"E20.2.3");var subQ5=sQuery(id+"F3.wireOp",EDGE,"E20.2.1");var subQ6=makeQuery(id+"F33.opLoft","SWEPT_FACE",FACE,{"disambiguationData":[OSD([subQ5,sQuery(id+"F3.wireOp",EDGE,"E20.2.2"),subQ4,subQ0,subQ2,subQ3])]});var subQ7=sQuery(id+"F41.wireOp",EDGE,"E34");var subQ8=sQuery(id+"F41.wireOp",EDGE,"E32");Q12=makeQuery(id+"F44.opFillet","BLEND_EDGE",EDGE,{"blendedFrom":[makeQuery(id+"F40.boolean.opBoolean","INTERSECT",EDGE,{"derivedFrom":[subQ6,makeQuery(id+"F40.opExtrude","CAP_FACE",FACE,{"disambiguationData":[OSD([sQuery(id+"F39.wireOp",EDGE,"E29"),sQuery(id+"F39.wireOp",EDGE,"E30")])],"isStart":true})]}),makeQuery(id+"F42.boolean.opBoolean","COPY",FACE,{"disambiguationData":[TD([makeQuery(id+"F33.opLoft","SWEPT_FACE",FACE,{"disambiguationData":[OSD([sQuery(id+"F3.wireOp",EDGE,"E20.2.0"),subQ5,subQ4,subQ1,subQ2,subQ3])]})])],"derivedFrom":makeQuery(id+"F42.opRevolve","SWEPT_FACE",FACE,{"disambiguationData":[OSD([subQ8]),TDD([makeQuery(id+"F41.imprint","IMPRINT",EDGE,{"disambiguationData":[TD([[makeQuery(id+"F41.imprint","INTERSECT",VERTEX,{"disambiguationData":[OD(0.0)],"derivedFrom":[subQ8,subQ7]}),-1.0]])],"derivedFrom":subQ8})])]})})],"blendedInto":[makeQuery(id+"F42.boolean.opBoolean","COPY",FACE,{"disambiguationData":[TD([makeQuery(id+"F33.opLoft","SWEPT_FACE",FACE,{"disambiguationData":[OSD([sQuery(id+"F3.wireOp",EDGE,"E20.2.0"),subQ5,subQ4,subQ1,subQ2,subQ3])]})])],"derivedFrom":makeQuery(id+"F42.opRevolve","SWEPT_FACE",FACE,{"disambiguationData":[OSD([subQ8]),TDD([makeQuery(id+"F41.imprint","IMPRINT",EDGE,{"disambiguationData":[TD([[makeQuery(id+"F41.imprint","INTERSECT",VERTEX,{"disambiguationData":[OD(0.0)],"derivedFrom":[subQ8,subQ7]}),-1.0]])],"derivedFrom":subQ8})])]})})]});}
            var Q13;
            {var subQ0=sQuery(id+"F41.wireOp",EDGE,"E34");var subQ1=sQuery(id+"F41.wireOp",EDGE,"E32");Q13=makeQuery(id+"F42.boolean.opBoolean","INTERSECT",EDGE,{"derivedFrom":[makeQuery(id+"F32.opLoft","SWEPT_FACE",FACE,{"disambiguationData":[OSD([sQuery(id+"F3.wireOp",EDGE,"E20.1.0"),sQuery(id+"F3.wireOp",EDGE,"E20.1.1"),sQuery(id+"F3.wireOp",EDGE,"E20.1.3"),sQuery(id+"F22.wireOp",EDGE,"E28.9.1"),sQuery(id+"F22.wireOp",EDGE,"E28.9.2"),sQuery(id+"F22.wireOp",EDGE,"E28.9.3")])]}),makeQuery(id+"F42.opRevolve","SWEPT_FACE",FACE,{"disambiguationData":[OSD([subQ1]),TDD([makeQuery(id+"F41.imprint","IMPRINT",EDGE,{"disambiguationData":[TD([[makeQuery(id+"F41.imprint","INTERSECT",VERTEX,{"disambiguationData":[OD(0.0)],"derivedFrom":[subQ1,subQ0]}),-1.0]])],"derivedFrom":subQ1})])]})]});}
            var Q14;
            {var subQ0=sQuery(id+"F41.wireOp",EDGE,"E37");var subQ1=makeQuery(id+"F42.opRevolve","SWEPT_FACE",FACE,{"disambiguationData":[OSD([subQ0])]});var subQ2=makeQuery(id+"F40.opExtrude","CAP_FACE",FACE,{"disambiguationData":[OSD([sQuery(id+"F39.wireOp",EDGE,"E29"),sQuery(id+"F39.wireOp",EDGE,"E30")])],"isStart":true});var subQ3=sQuery(id+"F22.wireOp",EDGE,"E28.15.3");var subQ4=sQuery(id+"F22.wireOp",EDGE,"E28.15.2");var subQ5=sQuery(id+"F3.wireOp",EDGE,"E20.7.3");var subQ7=sQuery(id+"F3.wireOp",EDGE,"E20.7.1");var subQ8=sQuery(id+"F3.wireOp",EDGE,"E20.7.0");var subQ9=sQuery(id+"F41.wireOp",EDGE,"E38");var subQ10=makeQuery(id+"F42.opRevolve","SWEPT_FACE",FACE,{"disambiguationData":[OSD([subQ9])]});var subQ11=makeQuery(id+"F42.opRevolve","SWEPT_EDGE",EDGE,{"disambiguationData":[OSD([subQ0,subQ9])]});var subQ12=sQuery(id+"F22.wireOp",EDGE,"E28.14.3");var subQ13=sQuery(id+"F22.wireOp",EDGE,"E28.14.2");var subQ14=sQuery(id+"F3.wireOp",EDGE,"E20.6.3");var subQ15=sQuery(id+"F3.wireOp",EDGE,"E20.6.1");var subQ16=sQuery(id+"F3.wireOp",EDGE,"E20.6.0");var subQ18=sQuery(id+"F22.wireOp",EDGE,"E28.13.3");var subQ19=sQuery(id+"F22.wireOp",EDGE,"E28.13.2");var subQ20=sQuery(id+"F3.wireOp",EDGE,"E20.5.3");var subQ22=sQuery(id+"F3.wireOp",EDGE,"E20.5.1");var subQ23=sQuery(id+"F3.wireOp",EDGE,"E20.5.0");var subQ24=sQuery(id+"F22.wireOp",EDGE,"E28.12.3");var subQ25=sQuery(id+"F22.wireOp",EDGE,"E28.12.2");var subQ26=sQuery(id+"F3.wireOp",EDGE,"E20.4.3");var subQ28=sQuery(id+"F3.wireOp",EDGE,"E20.4.1");var subQ29=sQuery(id+"F3.wireOp",EDGE,"E20.4.0");var subQ30=sQuery(id+"F22.wireOp",EDGE,"E28.11.3");var subQ31=sQuery(id+"F22.wireOp",EDGE,"E28.11.2");var subQ32=sQuery(id+"F3.wireOp",EDGE,"E20.3.3");var subQ34=sQuery(id+"F3.wireOp",EDGE,"E20.3.1");var subQ35=sQuery(id+"F3.wireOp",EDGE,"E20.3.0");var subQ36=sQuery(id+"F22.wireOp",EDGE,"E28.10.3");var subQ37=sQuery(id+"F22.wireOp",EDGE,"E28.10.2");var subQ38=sQuery(id+"F3.wireOp",EDGE,"E20.2.3");var subQ40=sQuery(id+"F3.wireOp",EDGE,"E20.2.1");var subQ41=sQuery(id+"F3.wireOp",EDGE,"E20.2.0");var subQ42=sQuery(id+"F22.wireOp",EDGE,"E28.9.3");var subQ43=sQuery(id+"F22.wireOp",EDGE,"E28.9.2");var subQ44=sQuery(id+"F3.wireOp",EDGE,"E20.1.3");var subQ46=sQuery(id+"F3.wireOp",EDGE,"E20.1.1");var subQ48=sQuery(id+"F3.wireOp",EDGE,"E20.1.0");var subQ49=makeQuery(id+"F32.opLoft","SWEPT_FACE",FACE,{"disambiguationData":[OSD([subQ48,subQ46,subQ44,sQuery(id+"F22.wireOp",EDGE,"E28.9.1"),subQ43,subQ42])]});var subQ50=sQuery(id+"F22.wireOp",EDGE,"E28.8.3");var subQ51=sQuery(id+"F22.wireOp",EDGE,"E28.8.2");var subQ53=sQuery(id+"F3.wireOp",EDGE,"E18.top");var subQ54=sQuery(id+"F3.wireOp",EDGE,"E18.bottom");var subQ55=sQuery(id+"F3.wireOp",EDGE,"E18.left");var subQ56=makeQuery(id+"F31.opLoft","SWEPT_FACE",FACE,{"disambiguationData":[OSD([subQ54,subQ53,subQ55,sQuery(id+"F22.wireOp",EDGE,"E28.8.1"),subQ51,subQ50])]});var subQ57=sQuery(id+"F22.wireOp",EDGE,"E28.7.3");var subQ58=sQuery(id+"F22.wireOp",EDGE,"E28.7.2");var subQ59=sQuery(id+"F3.wireOp",EDGE,"E20.15.3");var subQ60=sQuery(id+"F3.wireOp",EDGE,"E20.15.1");var subQ61=sQuery(id+"F3.wireOp",EDGE,"E20.15.0");var subQ62=makeQuery(id+"F30.opLoft","SWEPT_FACE",FACE,{"disambiguationData":[OSD([subQ61,subQ60,subQ59,sQuery(id+"F22.wireOp",EDGE,"E28.7.1"),subQ58,subQ57])]});var subQ64=sQuery(id+"F22.wireOp",EDGE,"E28.6.3");var subQ65=sQuery(id+"F22.wireOp",EDGE,"E28.6.2");var subQ66=sQuery(id+"F3.wireOp",EDGE,"E20.14.3");var subQ68=sQuery(id+"F3.wireOp",EDGE,"E20.14.1");var subQ69=sQuery(id+"F3.wireOp",EDGE,"E20.14.0");var subQ70=makeQuery(id+"F29.opLoft","SWEPT_FACE",FACE,{"disambiguationData":[OSD([subQ69,subQ68,subQ66,sQuery(id+"F22.wireOp",EDGE,"E28.6.1"),subQ65,subQ64])]});var subQ71=sQuery(id+"F22.wireOp",EDGE,"E28.5.3");var subQ72=sQuery(id+"F22.wireOp",EDGE,"E28.5.2");var subQ73=sQuery(id+"F3.wireOp",EDGE,"E20.13.3");var subQ75=sQuery(id+"F3.wireOp",EDGE,"E20.13.1");var subQ76=sQuery(id+"F3.wireOp",EDGE,"E20.13.0");var subQ77=makeQuery(id+"F28.opLoft","SWEPT_FACE",FACE,{"disambiguationData":[OSD([subQ76,subQ75,subQ73,sQuery(id+"F22.wireOp",EDGE,"E28.5.1"),subQ72,subQ71])]});var subQ78=sQuery(id+"F22.wireOp",EDGE,"E28.4.3");var subQ79=sQuery(id+"F22.wireOp",EDGE,"E28.4.2");var subQ80=sQuery(id+"F3.wireOp",EDGE,"E20.12.3");var subQ82=sQuery(id+"F3.wireOp",EDGE,"E20.12.1");var subQ83=sQuery(id+"F3.wireOp",EDGE,"E20.12.0");var subQ84=makeQuery(id+"F27.opLoft","SWEPT_FACE",FACE,{"disambiguationData":[OSD([subQ83,subQ82,subQ80,sQuery(id+"F22.wireOp",EDGE,"E28.4.1"),subQ79,subQ78])]});var subQ85=sQuery(id+"F22.wireOp",EDGE,"E28.3.3");var subQ86=sQuery(id+"F22.wireOp",EDGE,"E28.3.2");var subQ87=sQuery(id+"F3.wireOp",EDGE,"E20.11.3");var subQ89=sQuery(id+"F3.wireOp",EDGE,"E20.11.1");var subQ90=sQuery(id+"F3.wireOp",EDGE,"E20.11.0");var subQ91=makeQuery(id+"F26.opLoft","SWEPT_FACE",FACE,{"disambiguationData":[OSD([subQ90,subQ89,subQ87,sQuery(id+"F22.wireOp",EDGE,"E28.3.1"),subQ86,subQ85])]});var subQ92=sQuery(id+"F22.wireOp",EDGE,"E28.2.3");var subQ93=sQuery(id+"F22.wireOp",EDGE,"E28.2.2");var subQ94=sQuery(id+"F3.wireOp",EDGE,"E20.10.3");var subQ95=sQuery(id+"F3.wireOp",EDGE,"E20.10.1");var subQ96=sQuery(id+"F3.wireOp",EDGE,"E20.10.0");var subQ97=makeQuery(id+"F25.opLoft","SWEPT_FACE",FACE,{"disambiguationData":[OSD([subQ96,subQ95,subQ94,sQuery(id+"F22.wireOp",EDGE,"E28.2.1"),subQ93,subQ92])]});var subQ99=sQuery(id+"F22.wireOp",EDGE,"E28.1.3");var subQ100=sQuery(id+"F22.wireOp",EDGE,"E28.1.2");var subQ101=sQuery(id+"F3.wireOp",EDGE,"E20.9.3");var subQ102=sQuery(id+"F3.wireOp",EDGE,"E20.9.1");var subQ103=sQuery(id+"F3.wireOp",EDGE,"E20.9.0");var subQ104=makeQuery(id+"F24.opLoft","SWEPT_FACE",FACE,{"disambiguationData":[OSD([subQ103,subQ102,subQ101,sQuery(id+"F22.wireOp",EDGE,"E28.1.1"),subQ100,subQ99])]});var subQ105=sQuery(id+"F22.wireOp",EDGE,"E27.top");var subQ106=sQuery(id+"F22.wireOp",EDGE,"E27.bottom");var subQ107=sQuery(id+"F3.wireOp",EDGE,"E20.8.3");var subQ109=sQuery(id+"F3.wireOp",EDGE,"E20.8.1");var subQ113=makeQuery(id+"F42.boolean.opBoolean","COPY",FACE,{"disambiguationData":[TD([subQ49])],"derivedFrom":subQ10});var subQ151=makeQuery(id+"F14.opLoft","CAP_FACE",FACE,{"disambiguationData":[OSD([makeQuery(id+"F3.imprint","IMPRINT",FACE,{"disambiguationData":[TD([[makeQuery(id+"F3.imprint","IMPRINT",EDGE,{"derivedFrom":subQ8}),-1.0]])]})])],"isStart":true});var subQ156=makeQuery(id+"F5.opLoft","CAP_FACE",FACE,{"disambiguationData":[OSD([makeQuery(id+"F3.imprint","IMPRINT",FACE,{"disambiguationData":[TD([[makeQuery(id+"F3.imprint","IMPRINT",EDGE,{"derivedFrom":subQ54}),1.0]])]})])],"isStart":true});var subQ185=makeQuery(id+"F32.boolean.opBoolean","INTERSECT",EDGE,{"derivedFrom":[makeQuery(id+"F31.boolean.opBoolean","SPLIT",FACE,{"disambiguationData":[TD([subQ151])],"derivedFrom":makeQuery(id+"F30.boolean.opBoolean","SPLIT",FACE,{"disambiguationData":[TD([subQ156])],"derivedFrom":makeQuery(id+"F29.boolean.opBoolean","SPLIT",FACE,{"disambiguationData":[TD([subQ156])],"derivedFrom":makeQuery(id+"F28.boolean.opBoolean","SPLIT",FACE,{"disambiguationData":[TD([subQ156])],"derivedFrom":makeQuery(id+"F27.boolean.opBoolean","SPLIT",FACE,{"disambiguationData":[TD([subQ156])],"derivedFrom":makeQuery(id+"F26.boolean.opBoolean","SPLIT",FACE,{"disambiguationData":[TD([subQ156])],"derivedFrom":makeQuery(id+"F25.boolean.opBoolean","SPLIT",FACE,{"disambiguationData":[TD([subQ156])],"derivedFrom":makeQuery(id+"F24.boolean.opBoolean","SPLIT",FACE,{"disambiguationData":[TD([subQ156])],"derivedFrom":makeQuery(id+"F1.opRevolve","SWEPT_FACE",FACE,{"disambiguationData":[OSD([sQuery(id+"F0.wireOp",EDGE,"E4")])]})})})})})})})})}),subQ49]});Q14=makeQuery(id+"F48.opFillet","BLEND_EDGE",EDGE,{"blendedFrom":[makeQuery(id+"F47.opFillet","TWEAK_EDGE",EDGE,{"derivedFrom":[makeQuery(id+"F45.opFillet","BLEND_VERTEX",VERTEX,{"blendedFrom":[subQ185,subQ49,subQ113],"blendedInto":[subQ49,subQ113]}),makeQuery(id+"F45.opFillet","BLEND_VERTEX",VERTEX,{"blendedFrom":[subQ185,makeQuery(id+"F42.boolean.opBoolean","MERGE",FACE,{"derivedFrom":[subQ2,subQ1]}),subQ113],"blendedInto":[makeQuery(id+"F42.boolean.opBoolean","MERGE",FACE,{"derivedFrom":[subQ2,subQ1]}),subQ113]})]}),makeQuery(id+"F47.opFillet","BLEND_FACE",FACE,{"disambiguationData":[OSD([subQ0,subQ9]),TDD([makeQuery(id+"F42.boolean.opBoolean","COPY",EDGE,{"disambiguationData":[TD([makeQuery(id+"F23.opLoft","SWEPT_FACE",FACE,{"disambiguationData":[OSD([sQuery(id+"F3.wireOp",EDGE,"E20.8.0"),subQ109,subQ107,subQ106,subQ105,sQuery(id+"F22.wireOp",EDGE,"E27.right")])]})])],"derivedFrom":subQ11})])]}),makeQuery(id+"F47.opFillet","BLEND_FACE",FACE,{"disambiguationData":[OSD([subQ0,subQ9]),TDD([makeQuery(id+"F42.boolean.opBoolean","COPY",EDGE,{"disambiguationData":[TD([subQ104])],"derivedFrom":subQ11})])]}),makeQuery(id+"F47.opFillet","BLEND_FACE",FACE,{"disambiguationData":[OSD([subQ0,subQ9]),TDD([makeQuery(id+"F42.boolean.opBoolean","COPY",EDGE,{"disambiguationData":[TD([subQ97])],"derivedFrom":subQ11})])]}),makeQuery(id+"F47.opFillet","BLEND_FACE",FACE,{"disambiguationData":[OSD([subQ0,subQ9]),TDD([makeQuery(id+"F42.boolean.opBoolean","COPY",EDGE,{"disambiguationData":[TD([subQ91])],"derivedFrom":subQ11})])]}),makeQuery(id+"F47.opFillet","BLEND_FACE",FACE,{"disambiguationData":[OSD([subQ0,subQ9]),TDD([makeQuery(id+"F42.boolean.opBoolean","COPY",EDGE,{"disambiguationData":[TD([subQ84])],"derivedFrom":subQ11})])]}),makeQuery(id+"F47.opFillet","BLEND_FACE",FACE,{"disambiguationData":[OSD([subQ0,subQ9]),TDD([makeQuery(id+"F42.boolean.opBoolean","COPY",EDGE,{"disambiguationData":[TD([subQ77])],"derivedFrom":subQ11})])]}),makeQuery(id+"F47.opFillet","BLEND_FACE",FACE,{"disambiguationData":[OSD([subQ0,subQ9]),TDD([makeQuery(id+"F42.boolean.opBoolean","COPY",EDGE,{"disambiguationData":[TD([subQ70])],"derivedFrom":subQ11})])]}),makeQuery(id+"F47.opFillet","BLEND_FACE",FACE,{"disambiguationData":[OSD([subQ0,subQ9]),TDD([makeQuery(id+"F42.boolean.opBoolean","COPY",EDGE,{"disambiguationData":[TD([subQ62])],"derivedFrom":subQ11})])]}),makeQuery(id+"F47.opFillet","BLEND_FACE",FACE,{"disambiguationData":[OSD([subQ0,subQ9]),TDD([makeQuery(id+"F42.boolean.opBoolean","COPY",EDGE,{"disambiguationData":[TD([subQ56])],"derivedFrom":subQ11})])]}),makeQuery(id+"F47.opFillet","BLEND_FACE",FACE,{"disambiguationData":[OSD([subQ0,subQ9]),TDD([makeQuery(id+"F42.boolean.opBoolean","COPY",EDGE,{"disambiguationData":[TD([subQ49])],"derivedFrom":subQ11})])]}),makeQuery(id+"F47.opFillet","BLEND_FACE",FACE,{"disambiguationData":[OSD([subQ0,subQ9]),TDD([makeQuery(id+"F42.boolean.opBoolean","COPY",EDGE,{"disambiguationData":[TD([makeQuery(id+"F33.opLoft","SWEPT_FACE",FACE,{"disambiguationData":[OSD([subQ41,subQ40,subQ38,sQuery(id+"F22.wireOp",EDGE,"E28.10.1"),subQ37,subQ36])]})])],"derivedFrom":subQ11})])]}),makeQuery(id+"F47.opFillet","BLEND_FACE",FACE,{"disambiguationData":[OSD([subQ0,subQ9]),TDD([makeQuery(id+"F42.boolean.opBoolean","COPY",EDGE,{"disambiguationData":[TD([makeQuery(id+"F34.opLoft","SWEPT_FACE",FACE,{"disambiguationData":[OSD([subQ35,subQ34,subQ32,sQuery(id+"F22.wireOp",EDGE,"E28.11.1"),subQ31,subQ30])]})])],"derivedFrom":subQ11})])]}),makeQuery(id+"F47.opFillet","BLEND_FACE",FACE,{"disambiguationData":[OSD([subQ0,subQ9]),TDD([makeQuery(id+"F42.boolean.opBoolean","COPY",EDGE,{"disambiguationData":[TD([makeQuery(id+"F35.opLoft","SWEPT_FACE",FACE,{"disambiguationData":[OSD([subQ29,subQ28,subQ26,sQuery(id+"F22.wireOp",EDGE,"E28.12.1"),subQ25,subQ24])]})])],"derivedFrom":subQ11})])]}),makeQuery(id+"F47.opFillet","BLEND_FACE",FACE,{"disambiguationData":[OSD([subQ0,subQ9]),TDD([makeQuery(id+"F42.boolean.opBoolean","COPY",EDGE,{"disambiguationData":[TD([makeQuery(id+"F36.opLoft","SWEPT_FACE",FACE,{"disambiguationData":[OSD([subQ23,subQ22,subQ20,sQuery(id+"F22.wireOp",EDGE,"E28.13.1"),subQ19,subQ18])]})])],"derivedFrom":subQ11})])]}),makeQuery(id+"F47.opFillet","BLEND_FACE",FACE,{"disambiguationData":[OSD([subQ0,subQ9]),TDD([makeQuery(id+"F42.boolean.opBoolean","COPY",EDGE,{"disambiguationData":[TD([makeQuery(id+"F37.opLoft","SWEPT_FACE",FACE,{"disambiguationData":[OSD([subQ16,subQ15,subQ14,sQuery(id+"F22.wireOp",EDGE,"E28.14.1"),subQ13,subQ12])]})])],"derivedFrom":subQ11})])]}),makeQuery(id+"F47.opFillet","BLEND_FACE",FACE,{"disambiguationData":[OSD([subQ0,subQ9]),TDD([makeQuery(id+"F42.boolean.opBoolean","COPY",EDGE,{"disambiguationData":[TD([makeQuery(id+"F38.opLoft","SWEPT_FACE",FACE,{"disambiguationData":[OSD([subQ8,subQ7,subQ5,sQuery(id+"F22.wireOp",EDGE,"E28.15.1"),subQ4,subQ3])]})])],"derivedFrom":subQ11})])]})],"blendedInto":[makeQuery(id+"F47.opFillet","BLEND_FACE",FACE,{"disambiguationData":[OSD([subQ0,subQ9]),TDD([makeQuery(id+"F42.boolean.opBoolean","COPY",EDGE,{"disambiguationData":[TD([makeQuery(id+"F23.opLoft","SWEPT_FACE",FACE,{"disambiguationData":[OSD([sQuery(id+"F3.wireOp",EDGE,"E20.8.0"),subQ109,subQ107,subQ106,subQ105,sQuery(id+"F22.wireOp",EDGE,"E27.right")])]})])],"derivedFrom":subQ11})])]}),makeQuery(id+"F47.opFillet","BLEND_FACE",FACE,{"disambiguationData":[OSD([subQ0,subQ9]),TDD([makeQuery(id+"F42.boolean.opBoolean","COPY",EDGE,{"disambiguationData":[TD([subQ104])],"derivedFrom":subQ11})])]}),makeQuery(id+"F47.opFillet","BLEND_FACE",FACE,{"disambiguationData":[OSD([subQ0,subQ9]),TDD([makeQuery(id+"F42.boolean.opBoolean","COPY",EDGE,{"disambiguationData":[TD([subQ97])],"derivedFrom":subQ11})])]}),makeQuery(id+"F47.opFillet","BLEND_FACE",FACE,{"disambiguationData":[OSD([subQ0,subQ9]),TDD([makeQuery(id+"F42.boolean.opBoolean","COPY",EDGE,{"disambiguationData":[TD([subQ91])],"derivedFrom":subQ11})])]}),makeQuery(id+"F47.opFillet","BLEND_FACE",FACE,{"disambiguationData":[OSD([subQ0,subQ9]),TDD([makeQuery(id+"F42.boolean.opBoolean","COPY",EDGE,{"disambiguationData":[TD([subQ84])],"derivedFrom":subQ11})])]}),makeQuery(id+"F47.opFillet","BLEND_FACE",FACE,{"disambiguationData":[OSD([subQ0,subQ9]),TDD([makeQuery(id+"F42.boolean.opBoolean","COPY",EDGE,{"disambiguationData":[TD([subQ77])],"derivedFrom":subQ11})])]}),makeQuery(id+"F47.opFillet","BLEND_FACE",FACE,{"disambiguationData":[OSD([subQ0,subQ9]),TDD([makeQuery(id+"F42.boolean.opBoolean","COPY",EDGE,{"disambiguationData":[TD([subQ70])],"derivedFrom":subQ11})])]}),makeQuery(id+"F47.opFillet","BLEND_FACE",FACE,{"disambiguationData":[OSD([subQ0,subQ9]),TDD([makeQuery(id+"F42.boolean.opBoolean","COPY",EDGE,{"disambiguationData":[TD([subQ62])],"derivedFrom":subQ11})])]}),makeQuery(id+"F47.opFillet","BLEND_FACE",FACE,{"disambiguationData":[OSD([subQ0,subQ9]),TDD([makeQuery(id+"F42.boolean.opBoolean","COPY",EDGE,{"disambiguationData":[TD([subQ56])],"derivedFrom":subQ11})])]}),makeQuery(id+"F47.opFillet","BLEND_FACE",FACE,{"disambiguationData":[OSD([subQ0,subQ9]),TDD([makeQuery(id+"F42.boolean.opBoolean","COPY",EDGE,{"disambiguationData":[TD([subQ49])],"derivedFrom":subQ11})])]}),makeQuery(id+"F47.opFillet","BLEND_FACE",FACE,{"disambiguationData":[OSD([subQ0,subQ9]),TDD([makeQuery(id+"F42.boolean.opBoolean","COPY",EDGE,{"disambiguationData":[TD([makeQuery(id+"F33.opLoft","SWEPT_FACE",FACE,{"disambiguationData":[OSD([subQ41,subQ40,subQ38,sQuery(id+"F22.wireOp",EDGE,"E28.10.1"),subQ37,subQ36])]})])],"derivedFrom":subQ11})])]}),makeQuery(id+"F47.opFillet","BLEND_FACE",FACE,{"disambiguationData":[OSD([subQ0,subQ9]),TDD([makeQuery(id+"F42.boolean.opBoolean","COPY",EDGE,{"disambiguationData":[TD([makeQuery(id+"F34.opLoft","SWEPT_FACE",FACE,{"disambiguationData":[OSD([subQ35,subQ34,subQ32,sQuery(id+"F22.wireOp",EDGE,"E28.11.1"),subQ31,subQ30])]})])],"derivedFrom":subQ11})])]}),makeQuery(id+"F47.opFillet","BLEND_FACE",FACE,{"disambiguationData":[OSD([subQ0,subQ9]),TDD([makeQuery(id+"F42.boolean.opBoolean","COPY",EDGE,{"disambiguationData":[TD([makeQuery(id+"F35.opLoft","SWEPT_FACE",FACE,{"disambiguationData":[OSD([subQ29,subQ28,subQ26,sQuery(id+"F22.wireOp",EDGE,"E28.12.1"),subQ25,subQ24])]})])],"derivedFrom":subQ11})])]}),makeQuery(id+"F47.opFillet","BLEND_FACE",FACE,{"disambiguationData":[OSD([subQ0,subQ9]),TDD([makeQuery(id+"F42.boolean.opBoolean","COPY",EDGE,{"disambiguationData":[TD([makeQuery(id+"F36.opLoft","SWEPT_FACE",FACE,{"disambiguationData":[OSD([subQ23,subQ22,subQ20,sQuery(id+"F22.wireOp",EDGE,"E28.13.1"),subQ19,subQ18])]})])],"derivedFrom":subQ11})])]}),makeQuery(id+"F47.opFillet","BLEND_FACE",FACE,{"disambiguationData":[OSD([subQ0,subQ9]),TDD([makeQuery(id+"F42.boolean.opBoolean","COPY",EDGE,{"disambiguationData":[TD([makeQuery(id+"F37.opLoft","SWEPT_FACE",FACE,{"disambiguationData":[OSD([subQ16,subQ15,subQ14,sQuery(id+"F22.wireOp",EDGE,"E28.14.1"),subQ13,subQ12])]})])],"derivedFrom":subQ11})])]}),makeQuery(id+"F47.opFillet","BLEND_FACE",FACE,{"disambiguationData":[OSD([subQ0,subQ9]),TDD([makeQuery(id+"F42.boolean.opBoolean","COPY",EDGE,{"disambiguationData":[TD([makeQuery(id+"F38.opLoft","SWEPT_FACE",FACE,{"disambiguationData":[OSD([subQ8,subQ7,subQ5,sQuery(id+"F22.wireOp",EDGE,"E28.15.1"),subQ4,subQ3])]})])],"derivedFrom":subQ11})])]})]});}
            var Q15;
            {var subQ0=sQuery(id+"F41.wireOp",EDGE,"E37");var subQ1=makeQuery(id+"F42.opRevolve","SWEPT_FACE",FACE,{"disambiguationData":[OSD([subQ0])]});var subQ2=makeQuery(id+"F40.opExtrude","CAP_FACE",FACE,{"disambiguationData":[OSD([sQuery(id+"F39.wireOp",EDGE,"E29"),sQuery(id+"F39.wireOp",EDGE,"E30")])],"isStart":true});var subQ3=sQuery(id+"F22.wireOp",EDGE,"E28.15.3");var subQ4=sQuery(id+"F22.wireOp",EDGE,"E28.15.2");var subQ5=sQuery(id+"F3.wireOp",EDGE,"E20.7.3");var subQ7=sQuery(id+"F3.wireOp",EDGE,"E20.7.1");var subQ8=sQuery(id+"F3.wireOp",EDGE,"E20.7.0");var subQ9=sQuery(id+"F41.wireOp",EDGE,"E38");var subQ10=makeQuery(id+"F42.opRevolve","SWEPT_FACE",FACE,{"disambiguationData":[OSD([subQ9])]});var subQ11=makeQuery(id+"F42.opRevolve","SWEPT_EDGE",EDGE,{"disambiguationData":[OSD([subQ0,subQ9])]});var subQ12=sQuery(id+"F22.wireOp",EDGE,"E28.14.3");var subQ13=sQuery(id+"F22.wireOp",EDGE,"E28.14.2");var subQ14=sQuery(id+"F3.wireOp",EDGE,"E20.6.3");var subQ15=sQuery(id+"F3.wireOp",EDGE,"E20.6.1");var subQ16=sQuery(id+"F3.wireOp",EDGE,"E20.6.0");var subQ18=sQuery(id+"F22.wireOp",EDGE,"E28.13.3");var subQ19=sQuery(id+"F22.wireOp",EDGE,"E28.13.2");var subQ20=sQuery(id+"F3.wireOp",EDGE,"E20.5.3");var subQ22=sQuery(id+"F3.wireOp",EDGE,"E20.5.1");var subQ23=sQuery(id+"F3.wireOp",EDGE,"E20.5.0");var subQ24=sQuery(id+"F22.wireOp",EDGE,"E28.12.3");var subQ25=sQuery(id+"F22.wireOp",EDGE,"E28.12.2");var subQ26=sQuery(id+"F3.wireOp",EDGE,"E20.4.3");var subQ28=sQuery(id+"F3.wireOp",EDGE,"E20.4.1");var subQ29=sQuery(id+"F3.wireOp",EDGE,"E20.4.0");var subQ30=sQuery(id+"F22.wireOp",EDGE,"E28.11.3");var subQ31=sQuery(id+"F22.wireOp",EDGE,"E28.11.2");var subQ32=sQuery(id+"F3.wireOp",EDGE,"E20.3.3");var subQ34=sQuery(id+"F3.wireOp",EDGE,"E20.3.1");var subQ35=sQuery(id+"F3.wireOp",EDGE,"E20.3.0");var subQ36=sQuery(id+"F22.wireOp",EDGE,"E28.10.3");var subQ37=sQuery(id+"F22.wireOp",EDGE,"E28.10.2");var subQ38=sQuery(id+"F3.wireOp",EDGE,"E20.2.3");var subQ40=sQuery(id+"F3.wireOp",EDGE,"E20.2.1");var subQ41=sQuery(id+"F3.wireOp",EDGE,"E20.2.0");var subQ42=sQuery(id+"F22.wireOp",EDGE,"E28.9.3");var subQ43=sQuery(id+"F22.wireOp",EDGE,"E28.9.2");var subQ44=sQuery(id+"F3.wireOp",EDGE,"E20.1.3");var subQ46=sQuery(id+"F3.wireOp",EDGE,"E20.1.1");var subQ47=sQuery(id+"F3.wireOp",EDGE,"E20.1.0");var subQ48=sQuery(id+"F22.wireOp",EDGE,"E28.8.3");var subQ49=sQuery(id+"F22.wireOp",EDGE,"E28.8.2");var subQ51=sQuery(id+"F3.wireOp",EDGE,"E18.top");var subQ52=sQuery(id+"F3.wireOp",EDGE,"E18.bottom");var subQ54=sQuery(id+"F3.wireOp",EDGE,"E18.left");var subQ55=makeQuery(id+"F31.opLoft","SWEPT_FACE",FACE,{"disambiguationData":[OSD([subQ52,subQ51,subQ54,sQuery(id+"F22.wireOp",EDGE,"E28.8.1"),subQ49,subQ48])]});var subQ56=sQuery(id+"F22.wireOp",EDGE,"E28.7.3");var subQ57=sQuery(id+"F22.wireOp",EDGE,"E28.7.2");var subQ58=sQuery(id+"F3.wireOp",EDGE,"E20.15.3");var subQ59=sQuery(id+"F3.wireOp",EDGE,"E20.15.1");var subQ60=sQuery(id+"F3.wireOp",EDGE,"E20.15.0");var subQ61=makeQuery(id+"F30.opLoft","SWEPT_FACE",FACE,{"disambiguationData":[OSD([subQ60,subQ59,subQ58,sQuery(id+"F22.wireOp",EDGE,"E28.7.1"),subQ57,subQ56])]});var subQ63=sQuery(id+"F22.wireOp",EDGE,"E28.6.3");var subQ64=sQuery(id+"F22.wireOp",EDGE,"E28.6.2");var subQ65=sQuery(id+"F3.wireOp",EDGE,"E20.14.3");var subQ67=sQuery(id+"F3.wireOp",EDGE,"E20.14.1");var subQ68=sQuery(id+"F3.wireOp",EDGE,"E20.14.0");var subQ69=makeQuery(id+"F29.opLoft","SWEPT_FACE",FACE,{"disambiguationData":[OSD([subQ68,subQ67,subQ65,sQuery(id+"F22.wireOp",EDGE,"E28.6.1"),subQ64,subQ63])]});var subQ70=sQuery(id+"F22.wireOp",EDGE,"E28.5.3");var subQ71=sQuery(id+"F22.wireOp",EDGE,"E28.5.2");var subQ72=sQuery(id+"F3.wireOp",EDGE,"E20.13.3");var subQ74=sQuery(id+"F3.wireOp",EDGE,"E20.13.1");var subQ75=sQuery(id+"F3.wireOp",EDGE,"E20.13.0");var subQ76=makeQuery(id+"F28.opLoft","SWEPT_FACE",FACE,{"disambiguationData":[OSD([subQ75,subQ74,subQ72,sQuery(id+"F22.wireOp",EDGE,"E28.5.1"),subQ71,subQ70])]});var subQ77=sQuery(id+"F22.wireOp",EDGE,"E28.4.3");var subQ78=sQuery(id+"F22.wireOp",EDGE,"E28.4.2");var subQ79=sQuery(id+"F3.wireOp",EDGE,"E20.12.3");var subQ81=sQuery(id+"F3.wireOp",EDGE,"E20.12.1");var subQ82=sQuery(id+"F3.wireOp",EDGE,"E20.12.0");var subQ83=makeQuery(id+"F27.opLoft","SWEPT_FACE",FACE,{"disambiguationData":[OSD([subQ82,subQ81,subQ79,sQuery(id+"F22.wireOp",EDGE,"E28.4.1"),subQ78,subQ77])]});var subQ84=sQuery(id+"F22.wireOp",EDGE,"E28.3.3");var subQ85=sQuery(id+"F22.wireOp",EDGE,"E28.3.2");var subQ86=sQuery(id+"F3.wireOp",EDGE,"E20.11.3");var subQ88=sQuery(id+"F3.wireOp",EDGE,"E20.11.1");var subQ89=sQuery(id+"F3.wireOp",EDGE,"E20.11.0");var subQ90=makeQuery(id+"F26.opLoft","SWEPT_FACE",FACE,{"disambiguationData":[OSD([subQ89,subQ88,subQ86,sQuery(id+"F22.wireOp",EDGE,"E28.3.1"),subQ85,subQ84])]});var subQ91=sQuery(id+"F22.wireOp",EDGE,"E28.2.3");var subQ92=sQuery(id+"F22.wireOp",EDGE,"E28.2.2");var subQ93=sQuery(id+"F3.wireOp",EDGE,"E20.10.3");var subQ94=sQuery(id+"F3.wireOp",EDGE,"E20.10.1");var subQ95=sQuery(id+"F3.wireOp",EDGE,"E20.10.0");var subQ96=makeQuery(id+"F25.opLoft","SWEPT_FACE",FACE,{"disambiguationData":[OSD([subQ95,subQ94,subQ93,sQuery(id+"F22.wireOp",EDGE,"E28.2.1"),subQ92,subQ91])]});var subQ98=sQuery(id+"F22.wireOp",EDGE,"E28.1.3");var subQ99=sQuery(id+"F22.wireOp",EDGE,"E28.1.2");var subQ100=sQuery(id+"F3.wireOp",EDGE,"E20.9.3");var subQ101=sQuery(id+"F3.wireOp",EDGE,"E20.9.1");var subQ102=sQuery(id+"F3.wireOp",EDGE,"E20.9.0");var subQ103=makeQuery(id+"F24.opLoft","SWEPT_FACE",FACE,{"disambiguationData":[OSD([subQ102,subQ101,subQ100,sQuery(id+"F22.wireOp",EDGE,"E28.1.1"),subQ99,subQ98])]});var subQ104=sQuery(id+"F22.wireOp",EDGE,"E27.top");var subQ105=sQuery(id+"F22.wireOp",EDGE,"E27.bottom");var subQ106=sQuery(id+"F3.wireOp",EDGE,"E20.8.3");var subQ108=sQuery(id+"F3.wireOp",EDGE,"E20.8.1");var subQ112=makeQuery(id+"F42.boolean.opBoolean","COPY",FACE,{"disambiguationData":[TD([subQ55])],"derivedFrom":subQ10});var subQ138=makeQuery(id+"F5.opLoft","CAP_FACE",FACE,{"disambiguationData":[OSD([makeQuery(id+"F3.imprint","IMPRINT",FACE,{"disambiguationData":[TD([[makeQuery(id+"F3.imprint","IMPRINT",EDGE,{"derivedFrom":subQ52}),1.0]])]})])],"isStart":true});var subQ184=makeQuery(id+"F31.boolean.opBoolean","INTERSECT",EDGE,{"derivedFrom":[makeQuery(id+"F30.boolean.opBoolean","SPLIT",FACE,{"disambiguationData":[TD([subQ138])],"derivedFrom":makeQuery(id+"F29.boolean.opBoolean","SPLIT",FACE,{"disambiguationData":[TD([subQ138])],"derivedFrom":makeQuery(id+"F28.boolean.opBoolean","SPLIT",FACE,{"disambiguationData":[TD([subQ138])],"derivedFrom":makeQuery(id+"F27.boolean.opBoolean","SPLIT",FACE,{"disambiguationData":[TD([subQ138])],"derivedFrom":makeQuery(id+"F26.boolean.opBoolean","SPLIT",FACE,{"disambiguationData":[TD([subQ138])],"derivedFrom":makeQuery(id+"F25.boolean.opBoolean","SPLIT",FACE,{"disambiguationData":[TD([subQ138])],"derivedFrom":makeQuery(id+"F24.boolean.opBoolean","SPLIT",FACE,{"disambiguationData":[TD([subQ138])],"derivedFrom":makeQuery(id+"F1.opRevolve","SWEPT_FACE",FACE,{"disambiguationData":[OSD([sQuery(id+"F0.wireOp",EDGE,"E4")])]})})})})})})})}),subQ55]});Q15=makeQuery(id+"F48.opFillet","BLEND_EDGE",EDGE,{"blendedFrom":[makeQuery(id+"F47.opFillet","TWEAK_EDGE",EDGE,{"derivedFrom":[makeQuery(id+"F45.opFillet","BLEND_VERTEX",VERTEX,{"blendedFrom":[subQ184,subQ55,subQ112],"blendedInto":[subQ55,subQ112]}),makeQuery(id+"F45.opFillet","BLEND_VERTEX",VERTEX,{"blendedFrom":[subQ184,makeQuery(id+"F42.boolean.opBoolean","MERGE",FACE,{"derivedFrom":[subQ2,subQ1]}),subQ112],"blendedInto":[makeQuery(id+"F42.boolean.opBoolean","MERGE",FACE,{"derivedFrom":[subQ2,subQ1]}),subQ112]})]}),makeQuery(id+"F47.opFillet","BLEND_FACE",FACE,{"disambiguationData":[OSD([subQ0,subQ9]),TDD([makeQuery(id+"F42.boolean.opBoolean","COPY",EDGE,{"disambiguationData":[TD([makeQuery(id+"F23.opLoft","SWEPT_FACE",FACE,{"disambiguationData":[OSD([sQuery(id+"F3.wireOp",EDGE,"E20.8.0"),subQ108,subQ106,subQ105,subQ104,sQuery(id+"F22.wireOp",EDGE,"E27.right")])]})])],"derivedFrom":subQ11})])]}),makeQuery(id+"F47.opFillet","BLEND_FACE",FACE,{"disambiguationData":[OSD([subQ0,subQ9]),TDD([makeQuery(id+"F42.boolean.opBoolean","COPY",EDGE,{"disambiguationData":[TD([subQ103])],"derivedFrom":subQ11})])]}),makeQuery(id+"F47.opFillet","BLEND_FACE",FACE,{"disambiguationData":[OSD([subQ0,subQ9]),TDD([makeQuery(id+"F42.boolean.opBoolean","COPY",EDGE,{"disambiguationData":[TD([subQ96])],"derivedFrom":subQ11})])]}),makeQuery(id+"F47.opFillet","BLEND_FACE",FACE,{"disambiguationData":[OSD([subQ0,subQ9]),TDD([makeQuery(id+"F42.boolean.opBoolean","COPY",EDGE,{"disambiguationData":[TD([subQ90])],"derivedFrom":subQ11})])]}),makeQuery(id+"F47.opFillet","BLEND_FACE",FACE,{"disambiguationData":[OSD([subQ0,subQ9]),TDD([makeQuery(id+"F42.boolean.opBoolean","COPY",EDGE,{"disambiguationData":[TD([subQ83])],"derivedFrom":subQ11})])]}),makeQuery(id+"F47.opFillet","BLEND_FACE",FACE,{"disambiguationData":[OSD([subQ0,subQ9]),TDD([makeQuery(id+"F42.boolean.opBoolean","COPY",EDGE,{"disambiguationData":[TD([subQ76])],"derivedFrom":subQ11})])]}),makeQuery(id+"F47.opFillet","BLEND_FACE",FACE,{"disambiguationData":[OSD([subQ0,subQ9]),TDD([makeQuery(id+"F42.boolean.opBoolean","COPY",EDGE,{"disambiguationData":[TD([subQ69])],"derivedFrom":subQ11})])]}),makeQuery(id+"F47.opFillet","BLEND_FACE",FACE,{"disambiguationData":[OSD([subQ0,subQ9]),TDD([makeQuery(id+"F42.boolean.opBoolean","COPY",EDGE,{"disambiguationData":[TD([subQ61])],"derivedFrom":subQ11})])]}),makeQuery(id+"F47.opFillet","BLEND_FACE",FACE,{"disambiguationData":[OSD([subQ0,subQ9]),TDD([makeQuery(id+"F42.boolean.opBoolean","COPY",EDGE,{"disambiguationData":[TD([subQ55])],"derivedFrom":subQ11})])]}),makeQuery(id+"F47.opFillet","BLEND_FACE",FACE,{"disambiguationData":[OSD([subQ0,subQ9]),TDD([makeQuery(id+"F42.boolean.opBoolean","COPY",EDGE,{"disambiguationData":[TD([makeQuery(id+"F32.opLoft","SWEPT_FACE",FACE,{"disambiguationData":[OSD([subQ47,subQ46,subQ44,sQuery(id+"F22.wireOp",EDGE,"E28.9.1"),subQ43,subQ42])]})])],"derivedFrom":subQ11})])]}),makeQuery(id+"F47.opFillet","BLEND_FACE",FACE,{"disambiguationData":[OSD([subQ0,subQ9]),TDD([makeQuery(id+"F42.boolean.opBoolean","COPY",EDGE,{"disambiguationData":[TD([makeQuery(id+"F33.opLoft","SWEPT_FACE",FACE,{"disambiguationData":[OSD([subQ41,subQ40,subQ38,sQuery(id+"F22.wireOp",EDGE,"E28.10.1"),subQ37,subQ36])]})])],"derivedFrom":subQ11})])]}),makeQuery(id+"F47.opFillet","BLEND_FACE",FACE,{"disambiguationData":[OSD([subQ0,subQ9]),TDD([makeQuery(id+"F42.boolean.opBoolean","COPY",EDGE,{"disambiguationData":[TD([makeQuery(id+"F34.opLoft","SWEPT_FACE",FACE,{"disambiguationData":[OSD([subQ35,subQ34,subQ32,sQuery(id+"F22.wireOp",EDGE,"E28.11.1"),subQ31,subQ30])]})])],"derivedFrom":subQ11})])]}),makeQuery(id+"F47.opFillet","BLEND_FACE",FACE,{"disambiguationData":[OSD([subQ0,subQ9]),TDD([makeQuery(id+"F42.boolean.opBoolean","COPY",EDGE,{"disambiguationData":[TD([makeQuery(id+"F35.opLoft","SWEPT_FACE",FACE,{"disambiguationData":[OSD([subQ29,subQ28,subQ26,sQuery(id+"F22.wireOp",EDGE,"E28.12.1"),subQ25,subQ24])]})])],"derivedFrom":subQ11})])]}),makeQuery(id+"F47.opFillet","BLEND_FACE",FACE,{"disambiguationData":[OSD([subQ0,subQ9]),TDD([makeQuery(id+"F42.boolean.opBoolean","COPY",EDGE,{"disambiguationData":[TD([makeQuery(id+"F36.opLoft","SWEPT_FACE",FACE,{"disambiguationData":[OSD([subQ23,subQ22,subQ20,sQuery(id+"F22.wireOp",EDGE,"E28.13.1"),subQ19,subQ18])]})])],"derivedFrom":subQ11})])]}),makeQuery(id+"F47.opFillet","BLEND_FACE",FACE,{"disambiguationData":[OSD([subQ0,subQ9]),TDD([makeQuery(id+"F42.boolean.opBoolean","COPY",EDGE,{"disambiguationData":[TD([makeQuery(id+"F37.opLoft","SWEPT_FACE",FACE,{"disambiguationData":[OSD([subQ16,subQ15,subQ14,sQuery(id+"F22.wireOp",EDGE,"E28.14.1"),subQ13,subQ12])]})])],"derivedFrom":subQ11})])]}),makeQuery(id+"F47.opFillet","BLEND_FACE",FACE,{"disambiguationData":[OSD([subQ0,subQ9]),TDD([makeQuery(id+"F42.boolean.opBoolean","COPY",EDGE,{"disambiguationData":[TD([makeQuery(id+"F38.opLoft","SWEPT_FACE",FACE,{"disambiguationData":[OSD([subQ8,subQ7,subQ5,sQuery(id+"F22.wireOp",EDGE,"E28.15.1"),subQ4,subQ3])]})])],"derivedFrom":subQ11})])]})],"blendedInto":[makeQuery(id+"F47.opFillet","BLEND_FACE",FACE,{"disambiguationData":[OSD([subQ0,subQ9]),TDD([makeQuery(id+"F42.boolean.opBoolean","COPY",EDGE,{"disambiguationData":[TD([makeQuery(id+"F23.opLoft","SWEPT_FACE",FACE,{"disambiguationData":[OSD([sQuery(id+"F3.wireOp",EDGE,"E20.8.0"),subQ108,subQ106,subQ105,subQ104,sQuery(id+"F22.wireOp",EDGE,"E27.right")])]})])],"derivedFrom":subQ11})])]}),makeQuery(id+"F47.opFillet","BLEND_FACE",FACE,{"disambiguationData":[OSD([subQ0,subQ9]),TDD([makeQuery(id+"F42.boolean.opBoolean","COPY",EDGE,{"disambiguationData":[TD([subQ103])],"derivedFrom":subQ11})])]}),makeQuery(id+"F47.opFillet","BLEND_FACE",FACE,{"disambiguationData":[OSD([subQ0,subQ9]),TDD([makeQuery(id+"F42.boolean.opBoolean","COPY",EDGE,{"disambiguationData":[TD([subQ96])],"derivedFrom":subQ11})])]}),makeQuery(id+"F47.opFillet","BLEND_FACE",FACE,{"disambiguationData":[OSD([subQ0,subQ9]),TDD([makeQuery(id+"F42.boolean.opBoolean","COPY",EDGE,{"disambiguationData":[TD([subQ90])],"derivedFrom":subQ11})])]}),makeQuery(id+"F47.opFillet","BLEND_FACE",FACE,{"disambiguationData":[OSD([subQ0,subQ9]),TDD([makeQuery(id+"F42.boolean.opBoolean","COPY",EDGE,{"disambiguationData":[TD([subQ83])],"derivedFrom":subQ11})])]}),makeQuery(id+"F47.opFillet","BLEND_FACE",FACE,{"disambiguationData":[OSD([subQ0,subQ9]),TDD([makeQuery(id+"F42.boolean.opBoolean","COPY",EDGE,{"disambiguationData":[TD([subQ76])],"derivedFrom":subQ11})])]}),makeQuery(id+"F47.opFillet","BLEND_FACE",FACE,{"disambiguationData":[OSD([subQ0,subQ9]),TDD([makeQuery(id+"F42.boolean.opBoolean","COPY",EDGE,{"disambiguationData":[TD([subQ69])],"derivedFrom":subQ11})])]}),makeQuery(id+"F47.opFillet","BLEND_FACE",FACE,{"disambiguationData":[OSD([subQ0,subQ9]),TDD([makeQuery(id+"F42.boolean.opBoolean","COPY",EDGE,{"disambiguationData":[TD([subQ61])],"derivedFrom":subQ11})])]}),makeQuery(id+"F47.opFillet","BLEND_FACE",FACE,{"disambiguationData":[OSD([subQ0,subQ9]),TDD([makeQuery(id+"F42.boolean.opBoolean","COPY",EDGE,{"disambiguationData":[TD([subQ55])],"derivedFrom":subQ11})])]}),makeQuery(id+"F47.opFillet","BLEND_FACE",FACE,{"disambiguationData":[OSD([subQ0,subQ9]),TDD([makeQuery(id+"F42.boolean.opBoolean","COPY",EDGE,{"disambiguationData":[TD([makeQuery(id+"F32.opLoft","SWEPT_FACE",FACE,{"disambiguationData":[OSD([subQ47,subQ46,subQ44,sQuery(id+"F22.wireOp",EDGE,"E28.9.1"),subQ43,subQ42])]})])],"derivedFrom":subQ11})])]}),makeQuery(id+"F47.opFillet","BLEND_FACE",FACE,{"disambiguationData":[OSD([subQ0,subQ9]),TDD([makeQuery(id+"F42.boolean.opBoolean","COPY",EDGE,{"disambiguationData":[TD([makeQuery(id+"F33.opLoft","SWEPT_FACE",FACE,{"disambiguationData":[OSD([subQ41,subQ40,subQ38,sQuery(id+"F22.wireOp",EDGE,"E28.10.1"),subQ37,subQ36])]})])],"derivedFrom":subQ11})])]}),makeQuery(id+"F47.opFillet","BLEND_FACE",FACE,{"disambiguationData":[OSD([subQ0,subQ9]),TDD([makeQuery(id+"F42.boolean.opBoolean","COPY",EDGE,{"disambiguationData":[TD([makeQuery(id+"F34.opLoft","SWEPT_FACE",FACE,{"disambiguationData":[OSD([subQ35,subQ34,subQ32,sQuery(id+"F22.wireOp",EDGE,"E28.11.1"),subQ31,subQ30])]})])],"derivedFrom":subQ11})])]}),makeQuery(id+"F47.opFillet","BLEND_FACE",FACE,{"disambiguationData":[OSD([subQ0,subQ9]),TDD([makeQuery(id+"F42.boolean.opBoolean","COPY",EDGE,{"disambiguationData":[TD([makeQuery(id+"F35.opLoft","SWEPT_FACE",FACE,{"disambiguationData":[OSD([subQ29,subQ28,subQ26,sQuery(id+"F22.wireOp",EDGE,"E28.12.1"),subQ25,subQ24])]})])],"derivedFrom":subQ11})])]}),makeQuery(id+"F47.opFillet","BLEND_FACE",FACE,{"disambiguationData":[OSD([subQ0,subQ9]),TDD([makeQuery(id+"F42.boolean.opBoolean","COPY",EDGE,{"disambiguationData":[TD([makeQuery(id+"F36.opLoft","SWEPT_FACE",FACE,{"disambiguationData":[OSD([subQ23,subQ22,subQ20,sQuery(id+"F22.wireOp",EDGE,"E28.13.1"),subQ19,subQ18])]})])],"derivedFrom":subQ11})])]}),makeQuery(id+"F47.opFillet","BLEND_FACE",FACE,{"disambiguationData":[OSD([subQ0,subQ9]),TDD([makeQuery(id+"F42.boolean.opBoolean","COPY",EDGE,{"disambiguationData":[TD([makeQuery(id+"F37.opLoft","SWEPT_FACE",FACE,{"disambiguationData":[OSD([subQ16,subQ15,subQ14,sQuery(id+"F22.wireOp",EDGE,"E28.14.1"),subQ13,subQ12])]})])],"derivedFrom":subQ11})])]}),makeQuery(id+"F47.opFillet","BLEND_FACE",FACE,{"disambiguationData":[OSD([subQ0,subQ9]),TDD([makeQuery(id+"F42.boolean.opBoolean","COPY",EDGE,{"disambiguationData":[TD([makeQuery(id+"F38.opLoft","SWEPT_FACE",FACE,{"disambiguationData":[OSD([subQ8,subQ7,subQ5,sQuery(id+"F22.wireOp",EDGE,"E28.15.1"),subQ4,subQ3])]})])],"derivedFrom":subQ11})])]})]});}
            var Q16;
            {var subQ0=sQuery(id+"F22.wireOp",EDGE,"E28.9.3");var subQ1=sQuery(id+"F22.wireOp",EDGE,"E28.9.2");var subQ2=sQuery(id+"F22.wireOp",EDGE,"E28.9.1");var subQ3=sQuery(id+"F3.wireOp",EDGE,"E20.1.3");var subQ4=sQuery(id+"F3.wireOp",EDGE,"E20.1.1");var subQ5=sQuery(id+"F22.wireOp",EDGE,"E28.9.0");var subQ6=makeQuery(id+"F32.opLoft","SWEPT_FACE",FACE,{"disambiguationData":[OSD([subQ4,sQuery(id+"F3.wireOp",EDGE,"E20.1.2"),subQ3,subQ5,subQ1,subQ0])]});var subQ7=sQuery(id+"F41.wireOp",EDGE,"E34");var subQ8=sQuery(id+"F41.wireOp",EDGE,"E32");Q16=makeQuery(id+"F44.opFillet","BLEND_EDGE",EDGE,{"blendedFrom":[makeQuery(id+"F40.boolean.opBoolean","INTERSECT",EDGE,{"derivedFrom":[subQ6,makeQuery(id+"F40.opExtrude","CAP_FACE",FACE,{"disambiguationData":[OSD([sQuery(id+"F39.wireOp",EDGE,"E29"),sQuery(id+"F39.wireOp",EDGE,"E30")])],"isStart":true})]}),makeQuery(id+"F42.boolean.opBoolean","COPY",FACE,{"disambiguationData":[TD([makeQuery(id+"F32.opLoft","SWEPT_FACE",FACE,{"disambiguationData":[OSD([sQuery(id+"F3.wireOp",EDGE,"E20.1.0"),subQ4,subQ3,subQ2,subQ1,subQ0])]})])],"derivedFrom":makeQuery(id+"F42.opRevolve","SWEPT_FACE",FACE,{"disambiguationData":[OSD([subQ8]),TDD([makeQuery(id+"F41.imprint","IMPRINT",EDGE,{"disambiguationData":[TD([[makeQuery(id+"F41.imprint","INTERSECT",VERTEX,{"disambiguationData":[OD(0.0)],"derivedFrom":[subQ8,subQ7]}),-1.0]])],"derivedFrom":subQ8})])]})})],"blendedInto":[makeQuery(id+"F42.boolean.opBoolean","COPY",FACE,{"disambiguationData":[TD([makeQuery(id+"F32.opLoft","SWEPT_FACE",FACE,{"disambiguationData":[OSD([sQuery(id+"F3.wireOp",EDGE,"E20.1.0"),subQ4,subQ3,subQ2,subQ1,subQ0])]})])],"derivedFrom":makeQuery(id+"F42.opRevolve","SWEPT_FACE",FACE,{"disambiguationData":[OSD([subQ8]),TDD([makeQuery(id+"F41.imprint","IMPRINT",EDGE,{"disambiguationData":[TD([[makeQuery(id+"F41.imprint","INTERSECT",VERTEX,{"disambiguationData":[OD(0.0)],"derivedFrom":[subQ8,subQ7]}),-1.0]])],"derivedFrom":subQ8})])]})})]});}
            var Q17;
            {var subQ0=sQuery(id+"F41.wireOp",EDGE,"E34");var subQ1=sQuery(id+"F41.wireOp",EDGE,"E32");Q17=makeQuery(id+"F42.boolean.opBoolean","INTERSECT",EDGE,{"derivedFrom":[makeQuery(id+"F31.opLoft","SWEPT_FACE",FACE,{"disambiguationData":[OSD([sQuery(id+"F3.wireOp",EDGE,"E18.bottom"),sQuery(id+"F3.wireOp",EDGE,"E18.top"),sQuery(id+"F3.wireOp",EDGE,"E18.left"),sQuery(id+"F22.wireOp",EDGE,"E28.8.1"),sQuery(id+"F22.wireOp",EDGE,"E28.8.2"),sQuery(id+"F22.wireOp",EDGE,"E28.8.3")])]}),makeQuery(id+"F42.opRevolve","SWEPT_FACE",FACE,{"disambiguationData":[OSD([subQ1]),TDD([makeQuery(id+"F41.imprint","IMPRINT",EDGE,{"disambiguationData":[TD([[makeQuery(id+"F41.imprint","INTERSECT",VERTEX,{"disambiguationData":[OD(0.0)],"derivedFrom":[subQ1,subQ0]}),-1.0]])],"derivedFrom":subQ1})])]})]});}
            var Q18;
            {var subQ0=sQuery(id+"F22.wireOp",EDGE,"E28.8.3");var subQ1=sQuery(id+"F22.wireOp",EDGE,"E28.8.2");var subQ2=sQuery(id+"F22.wireOp",EDGE,"E28.8.1");var subQ3=sQuery(id+"F3.wireOp",EDGE,"E18.top");var subQ4=sQuery(id+"F3.wireOp",EDGE,"E18.bottom");var subQ5=sQuery(id+"F22.wireOp",EDGE,"E28.8.0");var subQ6=makeQuery(id+"F31.opLoft","SWEPT_FACE",FACE,{"disambiguationData":[OSD([subQ4,subQ3,sQuery(id+"F3.wireOp",EDGE,"E18.right"),subQ5,subQ1,subQ0])]});var subQ7=sQuery(id+"F41.wireOp",EDGE,"E34");var subQ8=sQuery(id+"F41.wireOp",EDGE,"E32");Q18=makeQuery(id+"F44.opFillet","BLEND_EDGE",EDGE,{"blendedFrom":[makeQuery(id+"F40.boolean.opBoolean","INTERSECT",EDGE,{"derivedFrom":[subQ6,makeQuery(id+"F40.opExtrude","CAP_FACE",FACE,{"disambiguationData":[OSD([sQuery(id+"F39.wireOp",EDGE,"E29"),sQuery(id+"F39.wireOp",EDGE,"E30")])],"isStart":true})]}),makeQuery(id+"F42.boolean.opBoolean","COPY",FACE,{"disambiguationData":[TD([makeQuery(id+"F31.opLoft","SWEPT_FACE",FACE,{"disambiguationData":[OSD([subQ4,subQ3,sQuery(id+"F3.wireOp",EDGE,"E18.left"),subQ2,subQ1,subQ0])]})])],"derivedFrom":makeQuery(id+"F42.opRevolve","SWEPT_FACE",FACE,{"disambiguationData":[OSD([subQ8]),TDD([makeQuery(id+"F41.imprint","IMPRINT",EDGE,{"disambiguationData":[TD([[makeQuery(id+"F41.imprint","INTERSECT",VERTEX,{"disambiguationData":[OD(0.0)],"derivedFrom":[subQ8,subQ7]}),-1.0]])],"derivedFrom":subQ8})])]})})],"blendedInto":[makeQuery(id+"F42.boolean.opBoolean","COPY",FACE,{"disambiguationData":[TD([makeQuery(id+"F31.opLoft","SWEPT_FACE",FACE,{"disambiguationData":[OSD([subQ4,subQ3,sQuery(id+"F3.wireOp",EDGE,"E18.left"),subQ2,subQ1,subQ0])]})])],"derivedFrom":makeQuery(id+"F42.opRevolve","SWEPT_FACE",FACE,{"disambiguationData":[OSD([subQ8]),TDD([makeQuery(id+"F41.imprint","IMPRINT",EDGE,{"disambiguationData":[TD([[makeQuery(id+"F41.imprint","INTERSECT",VERTEX,{"disambiguationData":[OD(0.0)],"derivedFrom":[subQ8,subQ7]}),-1.0]])],"derivedFrom":subQ8})])]})})]});}
            var Q19;
            {var subQ0=sQuery(id+"F41.wireOp",EDGE,"E37");var subQ1=makeQuery(id+"F42.opRevolve","SWEPT_FACE",FACE,{"disambiguationData":[OSD([subQ0])]});var subQ2=makeQuery(id+"F40.opExtrude","CAP_FACE",FACE,{"disambiguationData":[OSD([sQuery(id+"F39.wireOp",EDGE,"E29"),sQuery(id+"F39.wireOp",EDGE,"E30")])],"isStart":true});var subQ3=sQuery(id+"F22.wireOp",EDGE,"E28.15.3");var subQ4=sQuery(id+"F22.wireOp",EDGE,"E28.15.2");var subQ5=sQuery(id+"F3.wireOp",EDGE,"E20.7.3");var subQ7=sQuery(id+"F3.wireOp",EDGE,"E20.7.1");var subQ8=sQuery(id+"F3.wireOp",EDGE,"E20.7.0");var subQ9=sQuery(id+"F41.wireOp",EDGE,"E38");var subQ10=makeQuery(id+"F42.opRevolve","SWEPT_FACE",FACE,{"disambiguationData":[OSD([subQ9])]});var subQ11=makeQuery(id+"F42.opRevolve","SWEPT_EDGE",EDGE,{"disambiguationData":[OSD([subQ0,subQ9])]});var subQ12=sQuery(id+"F22.wireOp",EDGE,"E28.14.3");var subQ13=sQuery(id+"F22.wireOp",EDGE,"E28.14.2");var subQ14=sQuery(id+"F3.wireOp",EDGE,"E20.6.3");var subQ15=sQuery(id+"F3.wireOp",EDGE,"E20.6.1");var subQ16=sQuery(id+"F3.wireOp",EDGE,"E20.6.0");var subQ18=sQuery(id+"F22.wireOp",EDGE,"E28.13.3");var subQ19=sQuery(id+"F22.wireOp",EDGE,"E28.13.2");var subQ20=sQuery(id+"F3.wireOp",EDGE,"E20.5.3");var subQ22=sQuery(id+"F3.wireOp",EDGE,"E20.5.1");var subQ23=sQuery(id+"F3.wireOp",EDGE,"E20.5.0");var subQ24=sQuery(id+"F22.wireOp",EDGE,"E28.12.3");var subQ25=sQuery(id+"F22.wireOp",EDGE,"E28.12.2");var subQ26=sQuery(id+"F3.wireOp",EDGE,"E20.4.3");var subQ28=sQuery(id+"F3.wireOp",EDGE,"E20.4.1");var subQ29=sQuery(id+"F3.wireOp",EDGE,"E20.4.0");var subQ30=sQuery(id+"F22.wireOp",EDGE,"E28.11.3");var subQ31=sQuery(id+"F22.wireOp",EDGE,"E28.11.2");var subQ32=sQuery(id+"F3.wireOp",EDGE,"E20.3.3");var subQ34=sQuery(id+"F3.wireOp",EDGE,"E20.3.1");var subQ35=sQuery(id+"F3.wireOp",EDGE,"E20.3.0");var subQ36=sQuery(id+"F22.wireOp",EDGE,"E28.10.3");var subQ37=sQuery(id+"F22.wireOp",EDGE,"E28.10.2");var subQ38=sQuery(id+"F3.wireOp",EDGE,"E20.2.3");var subQ40=sQuery(id+"F3.wireOp",EDGE,"E20.2.1");var subQ41=sQuery(id+"F3.wireOp",EDGE,"E20.2.0");var subQ42=sQuery(id+"F22.wireOp",EDGE,"E28.9.3");var subQ43=sQuery(id+"F22.wireOp",EDGE,"E28.9.2");var subQ44=sQuery(id+"F3.wireOp",EDGE,"E20.1.3");var subQ46=sQuery(id+"F3.wireOp",EDGE,"E20.1.1");var subQ47=sQuery(id+"F3.wireOp",EDGE,"E20.1.0");var subQ48=sQuery(id+"F22.wireOp",EDGE,"E28.8.3");var subQ49=sQuery(id+"F22.wireOp",EDGE,"E28.8.2");var subQ51=sQuery(id+"F3.wireOp",EDGE,"E18.top");var subQ52=sQuery(id+"F3.wireOp",EDGE,"E18.bottom");var subQ53=sQuery(id+"F3.wireOp",EDGE,"E18.left");var subQ54=sQuery(id+"F22.wireOp",EDGE,"E28.7.3");var subQ55=sQuery(id+"F22.wireOp",EDGE,"E28.7.2");var subQ56=sQuery(id+"F3.wireOp",EDGE,"E20.15.3");var subQ57=sQuery(id+"F3.wireOp",EDGE,"E20.15.1");var subQ58=sQuery(id+"F3.wireOp",EDGE,"E20.15.0");var subQ59=makeQuery(id+"F30.opLoft","SWEPT_FACE",FACE,{"disambiguationData":[OSD([subQ58,subQ57,subQ56,sQuery(id+"F22.wireOp",EDGE,"E28.7.1"),subQ55,subQ54])]});var subQ62=sQuery(id+"F22.wireOp",EDGE,"E28.6.3");var subQ63=sQuery(id+"F22.wireOp",EDGE,"E28.6.2");var subQ64=sQuery(id+"F3.wireOp",EDGE,"E20.14.3");var subQ66=sQuery(id+"F3.wireOp",EDGE,"E20.14.1");var subQ67=sQuery(id+"F3.wireOp",EDGE,"E20.14.0");var subQ68=makeQuery(id+"F29.opLoft","SWEPT_FACE",FACE,{"disambiguationData":[OSD([subQ67,subQ66,subQ64,sQuery(id+"F22.wireOp",EDGE,"E28.6.1"),subQ63,subQ62])]});var subQ69=sQuery(id+"F22.wireOp",EDGE,"E28.5.3");var subQ70=sQuery(id+"F22.wireOp",EDGE,"E28.5.2");var subQ71=sQuery(id+"F3.wireOp",EDGE,"E20.13.3");var subQ73=sQuery(id+"F3.wireOp",EDGE,"E20.13.1");var subQ74=sQuery(id+"F3.wireOp",EDGE,"E20.13.0");var subQ75=makeQuery(id+"F28.opLoft","SWEPT_FACE",FACE,{"disambiguationData":[OSD([subQ74,subQ73,subQ71,sQuery(id+"F22.wireOp",EDGE,"E28.5.1"),subQ70,subQ69])]});var subQ76=sQuery(id+"F22.wireOp",EDGE,"E28.4.3");var subQ77=sQuery(id+"F22.wireOp",EDGE,"E28.4.2");var subQ78=sQuery(id+"F3.wireOp",EDGE,"E20.12.3");var subQ80=sQuery(id+"F3.wireOp",EDGE,"E20.12.1");var subQ81=sQuery(id+"F3.wireOp",EDGE,"E20.12.0");var subQ82=makeQuery(id+"F27.opLoft","SWEPT_FACE",FACE,{"disambiguationData":[OSD([subQ81,subQ80,subQ78,sQuery(id+"F22.wireOp",EDGE,"E28.4.1"),subQ77,subQ76])]});var subQ83=sQuery(id+"F22.wireOp",EDGE,"E28.3.3");var subQ84=sQuery(id+"F22.wireOp",EDGE,"E28.3.2");var subQ85=sQuery(id+"F3.wireOp",EDGE,"E20.11.3");var subQ87=sQuery(id+"F3.wireOp",EDGE,"E20.11.1");var subQ88=sQuery(id+"F3.wireOp",EDGE,"E20.11.0");var subQ89=makeQuery(id+"F26.opLoft","SWEPT_FACE",FACE,{"disambiguationData":[OSD([subQ88,subQ87,subQ85,sQuery(id+"F22.wireOp",EDGE,"E28.3.1"),subQ84,subQ83])]});var subQ90=sQuery(id+"F22.wireOp",EDGE,"E28.2.3");var subQ91=sQuery(id+"F22.wireOp",EDGE,"E28.2.2");var subQ92=sQuery(id+"F3.wireOp",EDGE,"E20.10.3");var subQ93=sQuery(id+"F3.wireOp",EDGE,"E20.10.1");var subQ94=sQuery(id+"F3.wireOp",EDGE,"E20.10.0");var subQ95=makeQuery(id+"F25.opLoft","SWEPT_FACE",FACE,{"disambiguationData":[OSD([subQ94,subQ93,subQ92,sQuery(id+"F22.wireOp",EDGE,"E28.2.1"),subQ91,subQ90])]});var subQ97=sQuery(id+"F22.wireOp",EDGE,"E28.1.3");var subQ98=sQuery(id+"F22.wireOp",EDGE,"E28.1.2");var subQ99=sQuery(id+"F3.wireOp",EDGE,"E20.9.3");var subQ100=sQuery(id+"F3.wireOp",EDGE,"E20.9.1");var subQ101=sQuery(id+"F3.wireOp",EDGE,"E20.9.0");var subQ102=makeQuery(id+"F24.opLoft","SWEPT_FACE",FACE,{"disambiguationData":[OSD([subQ101,subQ100,subQ99,sQuery(id+"F22.wireOp",EDGE,"E28.1.1"),subQ98,subQ97])]});var subQ103=sQuery(id+"F22.wireOp",EDGE,"E27.top");var subQ104=sQuery(id+"F22.wireOp",EDGE,"E27.bottom");var subQ105=sQuery(id+"F3.wireOp",EDGE,"E20.8.3");var subQ107=sQuery(id+"F3.wireOp",EDGE,"E20.8.1");var subQ111=makeQuery(id+"F42.boolean.opBoolean","COPY",FACE,{"disambiguationData":[TD([subQ59])],"derivedFrom":subQ10});var subQ127=makeQuery(id+"F5.opLoft","CAP_FACE",FACE,{"disambiguationData":[OSD([makeQuery(id+"F3.imprint","IMPRINT",FACE,{"disambiguationData":[TD([[makeQuery(id+"F3.imprint","IMPRINT",EDGE,{"derivedFrom":subQ52}),1.0]])]})])],"isStart":true});var subQ183=makeQuery(id+"F30.boolean.opBoolean","INTERSECT",EDGE,{"derivedFrom":[makeQuery(id+"F29.boolean.opBoolean","SPLIT",FACE,{"disambiguationData":[TD([subQ127])],"derivedFrom":makeQuery(id+"F28.boolean.opBoolean","SPLIT",FACE,{"disambiguationData":[TD([subQ127])],"derivedFrom":makeQuery(id+"F27.boolean.opBoolean","SPLIT",FACE,{"disambiguationData":[TD([subQ127])],"derivedFrom":makeQuery(id+"F26.boolean.opBoolean","SPLIT",FACE,{"disambiguationData":[TD([subQ127])],"derivedFrom":makeQuery(id+"F25.boolean.opBoolean","SPLIT",FACE,{"disambiguationData":[TD([subQ127])],"derivedFrom":makeQuery(id+"F24.boolean.opBoolean","SPLIT",FACE,{"disambiguationData":[TD([subQ127])],"derivedFrom":makeQuery(id+"F1.opRevolve","SWEPT_FACE",FACE,{"disambiguationData":[OSD([sQuery(id+"F0.wireOp",EDGE,"E4")])]})})})})})})}),subQ59]});Q19=makeQuery(id+"F48.opFillet","BLEND_EDGE",EDGE,{"blendedFrom":[makeQuery(id+"F47.opFillet","TWEAK_EDGE",EDGE,{"derivedFrom":[makeQuery(id+"F45.opFillet","BLEND_VERTEX",VERTEX,{"blendedFrom":[subQ183,subQ59,subQ111],"blendedInto":[subQ59,subQ111]}),makeQuery(id+"F45.opFillet","BLEND_VERTEX",VERTEX,{"blendedFrom":[subQ183,makeQuery(id+"F42.boolean.opBoolean","MERGE",FACE,{"derivedFrom":[subQ2,subQ1]}),subQ111],"blendedInto":[makeQuery(id+"F42.boolean.opBoolean","MERGE",FACE,{"derivedFrom":[subQ2,subQ1]}),subQ111]})]}),makeQuery(id+"F47.opFillet","BLEND_FACE",FACE,{"disambiguationData":[OSD([subQ0,subQ9]),TDD([makeQuery(id+"F42.boolean.opBoolean","COPY",EDGE,{"disambiguationData":[TD([makeQuery(id+"F23.opLoft","SWEPT_FACE",FACE,{"disambiguationData":[OSD([sQuery(id+"F3.wireOp",EDGE,"E20.8.0"),subQ107,subQ105,subQ104,subQ103,sQuery(id+"F22.wireOp",EDGE,"E27.right")])]})])],"derivedFrom":subQ11})])]}),makeQuery(id+"F47.opFillet","BLEND_FACE",FACE,{"disambiguationData":[OSD([subQ0,subQ9]),TDD([makeQuery(id+"F42.boolean.opBoolean","COPY",EDGE,{"disambiguationData":[TD([subQ102])],"derivedFrom":subQ11})])]}),makeQuery(id+"F47.opFillet","BLEND_FACE",FACE,{"disambiguationData":[OSD([subQ0,subQ9]),TDD([makeQuery(id+"F42.boolean.opBoolean","COPY",EDGE,{"disambiguationData":[TD([subQ95])],"derivedFrom":subQ11})])]}),makeQuery(id+"F47.opFillet","BLEND_FACE",FACE,{"disambiguationData":[OSD([subQ0,subQ9]),TDD([makeQuery(id+"F42.boolean.opBoolean","COPY",EDGE,{"disambiguationData":[TD([subQ89])],"derivedFrom":subQ11})])]}),makeQuery(id+"F47.opFillet","BLEND_FACE",FACE,{"disambiguationData":[OSD([subQ0,subQ9]),TDD([makeQuery(id+"F42.boolean.opBoolean","COPY",EDGE,{"disambiguationData":[TD([subQ82])],"derivedFrom":subQ11})])]}),makeQuery(id+"F47.opFillet","BLEND_FACE",FACE,{"disambiguationData":[OSD([subQ0,subQ9]),TDD([makeQuery(id+"F42.boolean.opBoolean","COPY",EDGE,{"disambiguationData":[TD([subQ75])],"derivedFrom":subQ11})])]}),makeQuery(id+"F47.opFillet","BLEND_FACE",FACE,{"disambiguationData":[OSD([subQ0,subQ9]),TDD([makeQuery(id+"F42.boolean.opBoolean","COPY",EDGE,{"disambiguationData":[TD([subQ68])],"derivedFrom":subQ11})])]}),makeQuery(id+"F47.opFillet","BLEND_FACE",FACE,{"disambiguationData":[OSD([subQ0,subQ9]),TDD([makeQuery(id+"F42.boolean.opBoolean","COPY",EDGE,{"disambiguationData":[TD([subQ59])],"derivedFrom":subQ11})])]}),makeQuery(id+"F47.opFillet","BLEND_FACE",FACE,{"disambiguationData":[OSD([subQ0,subQ9]),TDD([makeQuery(id+"F42.boolean.opBoolean","COPY",EDGE,{"disambiguationData":[TD([makeQuery(id+"F31.opLoft","SWEPT_FACE",FACE,{"disambiguationData":[OSD([subQ52,subQ51,subQ53,sQuery(id+"F22.wireOp",EDGE,"E28.8.1"),subQ49,subQ48])]})])],"derivedFrom":subQ11})])]}),makeQuery(id+"F47.opFillet","BLEND_FACE",FACE,{"disambiguationData":[OSD([subQ0,subQ9]),TDD([makeQuery(id+"F42.boolean.opBoolean","COPY",EDGE,{"disambiguationData":[TD([makeQuery(id+"F32.opLoft","SWEPT_FACE",FACE,{"disambiguationData":[OSD([subQ47,subQ46,subQ44,sQuery(id+"F22.wireOp",EDGE,"E28.9.1"),subQ43,subQ42])]})])],"derivedFrom":subQ11})])]}),makeQuery(id+"F47.opFillet","BLEND_FACE",FACE,{"disambiguationData":[OSD([subQ0,subQ9]),TDD([makeQuery(id+"F42.boolean.opBoolean","COPY",EDGE,{"disambiguationData":[TD([makeQuery(id+"F33.opLoft","SWEPT_FACE",FACE,{"disambiguationData":[OSD([subQ41,subQ40,subQ38,sQuery(id+"F22.wireOp",EDGE,"E28.10.1"),subQ37,subQ36])]})])],"derivedFrom":subQ11})])]}),makeQuery(id+"F47.opFillet","BLEND_FACE",FACE,{"disambiguationData":[OSD([subQ0,subQ9]),TDD([makeQuery(id+"F42.boolean.opBoolean","COPY",EDGE,{"disambiguationData":[TD([makeQuery(id+"F34.opLoft","SWEPT_FACE",FACE,{"disambiguationData":[OSD([subQ35,subQ34,subQ32,sQuery(id+"F22.wireOp",EDGE,"E28.11.1"),subQ31,subQ30])]})])],"derivedFrom":subQ11})])]}),makeQuery(id+"F47.opFillet","BLEND_FACE",FACE,{"disambiguationData":[OSD([subQ0,subQ9]),TDD([makeQuery(id+"F42.boolean.opBoolean","COPY",EDGE,{"disambiguationData":[TD([makeQuery(id+"F35.opLoft","SWEPT_FACE",FACE,{"disambiguationData":[OSD([subQ29,subQ28,subQ26,sQuery(id+"F22.wireOp",EDGE,"E28.12.1"),subQ25,subQ24])]})])],"derivedFrom":subQ11})])]}),makeQuery(id+"F47.opFillet","BLEND_FACE",FACE,{"disambiguationData":[OSD([subQ0,subQ9]),TDD([makeQuery(id+"F42.boolean.opBoolean","COPY",EDGE,{"disambiguationData":[TD([makeQuery(id+"F36.opLoft","SWEPT_FACE",FACE,{"disambiguationData":[OSD([subQ23,subQ22,subQ20,sQuery(id+"F22.wireOp",EDGE,"E28.13.1"),subQ19,subQ18])]})])],"derivedFrom":subQ11})])]}),makeQuery(id+"F47.opFillet","BLEND_FACE",FACE,{"disambiguationData":[OSD([subQ0,subQ9]),TDD([makeQuery(id+"F42.boolean.opBoolean","COPY",EDGE,{"disambiguationData":[TD([makeQuery(id+"F37.opLoft","SWEPT_FACE",FACE,{"disambiguationData":[OSD([subQ16,subQ15,subQ14,sQuery(id+"F22.wireOp",EDGE,"E28.14.1"),subQ13,subQ12])]})])],"derivedFrom":subQ11})])]}),makeQuery(id+"F47.opFillet","BLEND_FACE",FACE,{"disambiguationData":[OSD([subQ0,subQ9]),TDD([makeQuery(id+"F42.boolean.opBoolean","COPY",EDGE,{"disambiguationData":[TD([makeQuery(id+"F38.opLoft","SWEPT_FACE",FACE,{"disambiguationData":[OSD([subQ8,subQ7,subQ5,sQuery(id+"F22.wireOp",EDGE,"E28.15.1"),subQ4,subQ3])]})])],"derivedFrom":subQ11})])]})],"blendedInto":[makeQuery(id+"F47.opFillet","BLEND_FACE",FACE,{"disambiguationData":[OSD([subQ0,subQ9]),TDD([makeQuery(id+"F42.boolean.opBoolean","COPY",EDGE,{"disambiguationData":[TD([makeQuery(id+"F23.opLoft","SWEPT_FACE",FACE,{"disambiguationData":[OSD([sQuery(id+"F3.wireOp",EDGE,"E20.8.0"),subQ107,subQ105,subQ104,subQ103,sQuery(id+"F22.wireOp",EDGE,"E27.right")])]})])],"derivedFrom":subQ11})])]}),makeQuery(id+"F47.opFillet","BLEND_FACE",FACE,{"disambiguationData":[OSD([subQ0,subQ9]),TDD([makeQuery(id+"F42.boolean.opBoolean","COPY",EDGE,{"disambiguationData":[TD([subQ102])],"derivedFrom":subQ11})])]}),makeQuery(id+"F47.opFillet","BLEND_FACE",FACE,{"disambiguationData":[OSD([subQ0,subQ9]),TDD([makeQuery(id+"F42.boolean.opBoolean","COPY",EDGE,{"disambiguationData":[TD([subQ95])],"derivedFrom":subQ11})])]}),makeQuery(id+"F47.opFillet","BLEND_FACE",FACE,{"disambiguationData":[OSD([subQ0,subQ9]),TDD([makeQuery(id+"F42.boolean.opBoolean","COPY",EDGE,{"disambiguationData":[TD([subQ89])],"derivedFrom":subQ11})])]}),makeQuery(id+"F47.opFillet","BLEND_FACE",FACE,{"disambiguationData":[OSD([subQ0,subQ9]),TDD([makeQuery(id+"F42.boolean.opBoolean","COPY",EDGE,{"disambiguationData":[TD([subQ82])],"derivedFrom":subQ11})])]}),makeQuery(id+"F47.opFillet","BLEND_FACE",FACE,{"disambiguationData":[OSD([subQ0,subQ9]),TDD([makeQuery(id+"F42.boolean.opBoolean","COPY",EDGE,{"disambiguationData":[TD([subQ75])],"derivedFrom":subQ11})])]}),makeQuery(id+"F47.opFillet","BLEND_FACE",FACE,{"disambiguationData":[OSD([subQ0,subQ9]),TDD([makeQuery(id+"F42.boolean.opBoolean","COPY",EDGE,{"disambiguationData":[TD([subQ68])],"derivedFrom":subQ11})])]}),makeQuery(id+"F47.opFillet","BLEND_FACE",FACE,{"disambiguationData":[OSD([subQ0,subQ9]),TDD([makeQuery(id+"F42.boolean.opBoolean","COPY",EDGE,{"disambiguationData":[TD([subQ59])],"derivedFrom":subQ11})])]}),makeQuery(id+"F47.opFillet","BLEND_FACE",FACE,{"disambiguationData":[OSD([subQ0,subQ9]),TDD([makeQuery(id+"F42.boolean.opBoolean","COPY",EDGE,{"disambiguationData":[TD([makeQuery(id+"F31.opLoft","SWEPT_FACE",FACE,{"disambiguationData":[OSD([subQ52,subQ51,subQ53,sQuery(id+"F22.wireOp",EDGE,"E28.8.1"),subQ49,subQ48])]})])],"derivedFrom":subQ11})])]}),makeQuery(id+"F47.opFillet","BLEND_FACE",FACE,{"disambiguationData":[OSD([subQ0,subQ9]),TDD([makeQuery(id+"F42.boolean.opBoolean","COPY",EDGE,{"disambiguationData":[TD([makeQuery(id+"F32.opLoft","SWEPT_FACE",FACE,{"disambiguationData":[OSD([subQ47,subQ46,subQ44,sQuery(id+"F22.wireOp",EDGE,"E28.9.1"),subQ43,subQ42])]})])],"derivedFrom":subQ11})])]}),makeQuery(id+"F47.opFillet","BLEND_FACE",FACE,{"disambiguationData":[OSD([subQ0,subQ9]),TDD([makeQuery(id+"F42.boolean.opBoolean","COPY",EDGE,{"disambiguationData":[TD([makeQuery(id+"F33.opLoft","SWEPT_FACE",FACE,{"disambiguationData":[OSD([subQ41,subQ40,subQ38,sQuery(id+"F22.wireOp",EDGE,"E28.10.1"),subQ37,subQ36])]})])],"derivedFrom":subQ11})])]}),makeQuery(id+"F47.opFillet","BLEND_FACE",FACE,{"disambiguationData":[OSD([subQ0,subQ9]),TDD([makeQuery(id+"F42.boolean.opBoolean","COPY",EDGE,{"disambiguationData":[TD([makeQuery(id+"F34.opLoft","SWEPT_FACE",FACE,{"disambiguationData":[OSD([subQ35,subQ34,subQ32,sQuery(id+"F22.wireOp",EDGE,"E28.11.1"),subQ31,subQ30])]})])],"derivedFrom":subQ11})])]}),makeQuery(id+"F47.opFillet","BLEND_FACE",FACE,{"disambiguationData":[OSD([subQ0,subQ9]),TDD([makeQuery(id+"F42.boolean.opBoolean","COPY",EDGE,{"disambiguationData":[TD([makeQuery(id+"F35.opLoft","SWEPT_FACE",FACE,{"disambiguationData":[OSD([subQ29,subQ28,subQ26,sQuery(id+"F22.wireOp",EDGE,"E28.12.1"),subQ25,subQ24])]})])],"derivedFrom":subQ11})])]}),makeQuery(id+"F47.opFillet","BLEND_FACE",FACE,{"disambiguationData":[OSD([subQ0,subQ9]),TDD([makeQuery(id+"F42.boolean.opBoolean","COPY",EDGE,{"disambiguationData":[TD([makeQuery(id+"F36.opLoft","SWEPT_FACE",FACE,{"disambiguationData":[OSD([subQ23,subQ22,subQ20,sQuery(id+"F22.wireOp",EDGE,"E28.13.1"),subQ19,subQ18])]})])],"derivedFrom":subQ11})])]}),makeQuery(id+"F47.opFillet","BLEND_FACE",FACE,{"disambiguationData":[OSD([subQ0,subQ9]),TDD([makeQuery(id+"F42.boolean.opBoolean","COPY",EDGE,{"disambiguationData":[TD([makeQuery(id+"F37.opLoft","SWEPT_FACE",FACE,{"disambiguationData":[OSD([subQ16,subQ15,subQ14,sQuery(id+"F22.wireOp",EDGE,"E28.14.1"),subQ13,subQ12])]})])],"derivedFrom":subQ11})])]}),makeQuery(id+"F47.opFillet","BLEND_FACE",FACE,{"disambiguationData":[OSD([subQ0,subQ9]),TDD([makeQuery(id+"F42.boolean.opBoolean","COPY",EDGE,{"disambiguationData":[TD([makeQuery(id+"F38.opLoft","SWEPT_FACE",FACE,{"disambiguationData":[OSD([subQ8,subQ7,subQ5,sQuery(id+"F22.wireOp",EDGE,"E28.15.1"),subQ4,subQ3])]})])],"derivedFrom":subQ11})])]})]});}
            var Q20;
            {var subQ0=sQuery(id+"F41.wireOp",EDGE,"E34");var subQ1=sQuery(id+"F41.wireOp",EDGE,"E32");Q20=makeQuery(id+"F42.boolean.opBoolean","INTERSECT",EDGE,{"derivedFrom":[makeQuery(id+"F30.opLoft","SWEPT_FACE",FACE,{"disambiguationData":[OSD([sQuery(id+"F3.wireOp",EDGE,"E20.15.0"),sQuery(id+"F3.wireOp",EDGE,"E20.15.1"),sQuery(id+"F3.wireOp",EDGE,"E20.15.3"),sQuery(id+"F22.wireOp",EDGE,"E28.7.1"),sQuery(id+"F22.wireOp",EDGE,"E28.7.2"),sQuery(id+"F22.wireOp",EDGE,"E28.7.3")])]}),makeQuery(id+"F42.opRevolve","SWEPT_FACE",FACE,{"disambiguationData":[OSD([subQ1]),TDD([makeQuery(id+"F41.imprint","IMPRINT",EDGE,{"disambiguationData":[TD([[makeQuery(id+"F41.imprint","INTERSECT",VERTEX,{"disambiguationData":[OD(0.0)],"derivedFrom":[subQ1,subQ0]}),-1.0]])],"derivedFrom":subQ1})])]})]});}
            var Q21;
            {var subQ0=sQuery(id+"F22.wireOp",EDGE,"E28.7.3");var subQ1=sQuery(id+"F22.wireOp",EDGE,"E28.7.2");var subQ2=sQuery(id+"F22.wireOp",EDGE,"E28.7.0");var subQ3=sQuery(id+"F3.wireOp",EDGE,"E20.15.3");var subQ4=sQuery(id+"F3.wireOp",EDGE,"E20.15.1");var subQ5=makeQuery(id+"F30.opLoft","SWEPT_FACE",FACE,{"disambiguationData":[OSD([subQ4,sQuery(id+"F3.wireOp",EDGE,"E20.15.2"),subQ3,subQ2,subQ1,subQ0])]});var subQ6=sQuery(id+"F22.wireOp",EDGE,"E28.7.1");var subQ7=sQuery(id+"F41.wireOp",EDGE,"E34");var subQ8=sQuery(id+"F41.wireOp",EDGE,"E32");Q21=makeQuery(id+"F44.opFillet","BLEND_EDGE",EDGE,{"blendedFrom":[makeQuery(id+"F40.boolean.opBoolean","INTERSECT",EDGE,{"derivedFrom":[subQ5,makeQuery(id+"F40.opExtrude","CAP_FACE",FACE,{"disambiguationData":[OSD([sQuery(id+"F39.wireOp",EDGE,"E29"),sQuery(id+"F39.wireOp",EDGE,"E30")])],"isStart":true})]}),makeQuery(id+"F42.boolean.opBoolean","COPY",FACE,{"disambiguationData":[TD([makeQuery(id+"F30.opLoft","SWEPT_FACE",FACE,{"disambiguationData":[OSD([sQuery(id+"F3.wireOp",EDGE,"E20.15.0"),subQ4,subQ3,subQ6,subQ1,subQ0])]})])],"derivedFrom":makeQuery(id+"F42.opRevolve","SWEPT_FACE",FACE,{"disambiguationData":[OSD([subQ8]),TDD([makeQuery(id+"F41.imprint","IMPRINT",EDGE,{"disambiguationData":[TD([[makeQuery(id+"F41.imprint","INTERSECT",VERTEX,{"disambiguationData":[OD(0.0)],"derivedFrom":[subQ8,subQ7]}),-1.0]])],"derivedFrom":subQ8})])]})})],"blendedInto":[makeQuery(id+"F42.boolean.opBoolean","COPY",FACE,{"disambiguationData":[TD([makeQuery(id+"F30.opLoft","SWEPT_FACE",FACE,{"disambiguationData":[OSD([sQuery(id+"F3.wireOp",EDGE,"E20.15.0"),subQ4,subQ3,subQ6,subQ1,subQ0])]})])],"derivedFrom":makeQuery(id+"F42.opRevolve","SWEPT_FACE",FACE,{"disambiguationData":[OSD([subQ8]),TDD([makeQuery(id+"F41.imprint","IMPRINT",EDGE,{"disambiguationData":[TD([[makeQuery(id+"F41.imprint","INTERSECT",VERTEX,{"disambiguationData":[OD(0.0)],"derivedFrom":[subQ8,subQ7]}),-1.0]])],"derivedFrom":subQ8})])]})})]});}
            var Q22;
            {var subQ0=sQuery(id+"F41.wireOp",EDGE,"E34");var subQ1=sQuery(id+"F41.wireOp",EDGE,"E32");Q22=makeQuery(id+"F42.boolean.opBoolean","INTERSECT",EDGE,{"derivedFrom":[makeQuery(id+"F29.opLoft","SWEPT_FACE",FACE,{"disambiguationData":[OSD([sQuery(id+"F3.wireOp",EDGE,"E20.14.0"),sQuery(id+"F3.wireOp",EDGE,"E20.14.1"),sQuery(id+"F3.wireOp",EDGE,"E20.14.3"),sQuery(id+"F22.wireOp",EDGE,"E28.6.1"),sQuery(id+"F22.wireOp",EDGE,"E28.6.2"),sQuery(id+"F22.wireOp",EDGE,"E28.6.3")])]}),makeQuery(id+"F42.opRevolve","SWEPT_FACE",FACE,{"disambiguationData":[OSD([subQ1]),TDD([makeQuery(id+"F41.imprint","IMPRINT",EDGE,{"disambiguationData":[TD([[makeQuery(id+"F41.imprint","INTERSECT",VERTEX,{"disambiguationData":[OD(0.0)],"derivedFrom":[subQ1,subQ0]}),-1.0]])],"derivedFrom":subQ1})])]})]});}
            var Q23;
            {var subQ0=sQuery(id+"F41.wireOp",EDGE,"E37");var subQ1=makeQuery(id+"F42.opRevolve","SWEPT_FACE",FACE,{"disambiguationData":[OSD([subQ0])]});var subQ2=makeQuery(id+"F40.opExtrude","CAP_FACE",FACE,{"disambiguationData":[OSD([sQuery(id+"F39.wireOp",EDGE,"E29"),sQuery(id+"F39.wireOp",EDGE,"E30")])],"isStart":true});var subQ3=sQuery(id+"F22.wireOp",EDGE,"E28.15.3");var subQ4=sQuery(id+"F22.wireOp",EDGE,"E28.15.2");var subQ5=sQuery(id+"F3.wireOp",EDGE,"E20.7.3");var subQ7=sQuery(id+"F3.wireOp",EDGE,"E20.7.1");var subQ8=sQuery(id+"F3.wireOp",EDGE,"E20.7.0");var subQ9=sQuery(id+"F41.wireOp",EDGE,"E38");var subQ10=makeQuery(id+"F42.opRevolve","SWEPT_FACE",FACE,{"disambiguationData":[OSD([subQ9])]});var subQ11=makeQuery(id+"F42.opRevolve","SWEPT_EDGE",EDGE,{"disambiguationData":[OSD([subQ0,subQ9])]});var subQ12=sQuery(id+"F22.wireOp",EDGE,"E28.14.3");var subQ13=sQuery(id+"F22.wireOp",EDGE,"E28.14.2");var subQ14=sQuery(id+"F3.wireOp",EDGE,"E20.6.3");var subQ15=sQuery(id+"F3.wireOp",EDGE,"E20.6.1");var subQ16=sQuery(id+"F3.wireOp",EDGE,"E20.6.0");var subQ18=sQuery(id+"F22.wireOp",EDGE,"E28.13.3");var subQ19=sQuery(id+"F22.wireOp",EDGE,"E28.13.2");var subQ20=sQuery(id+"F3.wireOp",EDGE,"E20.5.3");var subQ22=sQuery(id+"F3.wireOp",EDGE,"E20.5.1");var subQ23=sQuery(id+"F3.wireOp",EDGE,"E20.5.0");var subQ24=sQuery(id+"F22.wireOp",EDGE,"E28.12.3");var subQ25=sQuery(id+"F22.wireOp",EDGE,"E28.12.2");var subQ26=sQuery(id+"F3.wireOp",EDGE,"E20.4.3");var subQ28=sQuery(id+"F3.wireOp",EDGE,"E20.4.1");var subQ29=sQuery(id+"F3.wireOp",EDGE,"E20.4.0");var subQ30=sQuery(id+"F22.wireOp",EDGE,"E28.11.3");var subQ31=sQuery(id+"F22.wireOp",EDGE,"E28.11.2");var subQ32=sQuery(id+"F3.wireOp",EDGE,"E20.3.3");var subQ34=sQuery(id+"F3.wireOp",EDGE,"E20.3.1");var subQ35=sQuery(id+"F3.wireOp",EDGE,"E20.3.0");var subQ36=sQuery(id+"F22.wireOp",EDGE,"E28.10.3");var subQ37=sQuery(id+"F22.wireOp",EDGE,"E28.10.2");var subQ38=sQuery(id+"F3.wireOp",EDGE,"E20.2.3");var subQ40=sQuery(id+"F3.wireOp",EDGE,"E20.2.1");var subQ41=sQuery(id+"F3.wireOp",EDGE,"E20.2.0");var subQ42=sQuery(id+"F22.wireOp",EDGE,"E28.9.3");var subQ43=sQuery(id+"F22.wireOp",EDGE,"E28.9.2");var subQ44=sQuery(id+"F3.wireOp",EDGE,"E20.1.3");var subQ46=sQuery(id+"F3.wireOp",EDGE,"E20.1.1");var subQ47=sQuery(id+"F3.wireOp",EDGE,"E20.1.0");var subQ48=sQuery(id+"F22.wireOp",EDGE,"E28.8.3");var subQ49=sQuery(id+"F22.wireOp",EDGE,"E28.8.2");var subQ51=sQuery(id+"F3.wireOp",EDGE,"E18.top");var subQ52=sQuery(id+"F3.wireOp",EDGE,"E18.bottom");var subQ53=sQuery(id+"F3.wireOp",EDGE,"E18.left");var subQ54=sQuery(id+"F22.wireOp",EDGE,"E28.7.3");var subQ55=sQuery(id+"F22.wireOp",EDGE,"E28.7.2");var subQ56=sQuery(id+"F3.wireOp",EDGE,"E20.15.3");var subQ57=sQuery(id+"F3.wireOp",EDGE,"E20.15.1");var subQ58=sQuery(id+"F3.wireOp",EDGE,"E20.15.0");var subQ60=sQuery(id+"F22.wireOp",EDGE,"E28.6.3");var subQ61=sQuery(id+"F22.wireOp",EDGE,"E28.6.2");var subQ62=sQuery(id+"F3.wireOp",EDGE,"E20.14.3");var subQ64=sQuery(id+"F3.wireOp",EDGE,"E20.14.1");var subQ66=sQuery(id+"F3.wireOp",EDGE,"E20.14.0");var subQ67=makeQuery(id+"F29.opLoft","SWEPT_FACE",FACE,{"disambiguationData":[OSD([subQ66,subQ64,subQ62,sQuery(id+"F22.wireOp",EDGE,"E28.6.1"),subQ61,subQ60])]});var subQ68=sQuery(id+"F22.wireOp",EDGE,"E28.5.3");var subQ69=sQuery(id+"F22.wireOp",EDGE,"E28.5.2");var subQ70=sQuery(id+"F3.wireOp",EDGE,"E20.13.3");var subQ72=sQuery(id+"F3.wireOp",EDGE,"E20.13.1");var subQ73=sQuery(id+"F3.wireOp",EDGE,"E20.13.0");var subQ74=makeQuery(id+"F28.opLoft","SWEPT_FACE",FACE,{"disambiguationData":[OSD([subQ73,subQ72,subQ70,sQuery(id+"F22.wireOp",EDGE,"E28.5.1"),subQ69,subQ68])]});var subQ75=sQuery(id+"F22.wireOp",EDGE,"E28.4.3");var subQ76=sQuery(id+"F22.wireOp",EDGE,"E28.4.2");var subQ77=sQuery(id+"F3.wireOp",EDGE,"E20.12.3");var subQ79=sQuery(id+"F3.wireOp",EDGE,"E20.12.1");var subQ80=sQuery(id+"F3.wireOp",EDGE,"E20.12.0");var subQ81=makeQuery(id+"F27.opLoft","SWEPT_FACE",FACE,{"disambiguationData":[OSD([subQ80,subQ79,subQ77,sQuery(id+"F22.wireOp",EDGE,"E28.4.1"),subQ76,subQ75])]});var subQ82=sQuery(id+"F22.wireOp",EDGE,"E28.3.3");var subQ83=sQuery(id+"F22.wireOp",EDGE,"E28.3.2");var subQ84=sQuery(id+"F3.wireOp",EDGE,"E20.11.3");var subQ86=sQuery(id+"F3.wireOp",EDGE,"E20.11.1");var subQ87=sQuery(id+"F3.wireOp",EDGE,"E20.11.0");var subQ88=makeQuery(id+"F26.opLoft","SWEPT_FACE",FACE,{"disambiguationData":[OSD([subQ87,subQ86,subQ84,sQuery(id+"F22.wireOp",EDGE,"E28.3.1"),subQ83,subQ82])]});var subQ89=sQuery(id+"F22.wireOp",EDGE,"E28.2.3");var subQ90=sQuery(id+"F22.wireOp",EDGE,"E28.2.2");var subQ91=sQuery(id+"F3.wireOp",EDGE,"E20.10.3");var subQ92=sQuery(id+"F3.wireOp",EDGE,"E20.10.1");var subQ93=sQuery(id+"F3.wireOp",EDGE,"E20.10.0");var subQ94=makeQuery(id+"F25.opLoft","SWEPT_FACE",FACE,{"disambiguationData":[OSD([subQ93,subQ92,subQ91,sQuery(id+"F22.wireOp",EDGE,"E28.2.1"),subQ90,subQ89])]});var subQ96=sQuery(id+"F22.wireOp",EDGE,"E28.1.3");var subQ97=sQuery(id+"F22.wireOp",EDGE,"E28.1.2");var subQ98=sQuery(id+"F3.wireOp",EDGE,"E20.9.3");var subQ99=sQuery(id+"F3.wireOp",EDGE,"E20.9.1");var subQ100=sQuery(id+"F3.wireOp",EDGE,"E20.9.0");var subQ101=makeQuery(id+"F24.opLoft","SWEPT_FACE",FACE,{"disambiguationData":[OSD([subQ100,subQ99,subQ98,sQuery(id+"F22.wireOp",EDGE,"E28.1.1"),subQ97,subQ96])]});var subQ102=sQuery(id+"F22.wireOp",EDGE,"E27.top");var subQ103=sQuery(id+"F22.wireOp",EDGE,"E27.bottom");var subQ104=sQuery(id+"F3.wireOp",EDGE,"E20.8.3");var subQ106=sQuery(id+"F3.wireOp",EDGE,"E20.8.1");var subQ110=makeQuery(id+"F42.boolean.opBoolean","COPY",FACE,{"disambiguationData":[TD([subQ67])],"derivedFrom":subQ10});var subQ130=makeQuery(id+"F5.opLoft","CAP_FACE",FACE,{"disambiguationData":[OSD([makeQuery(id+"F3.imprint","IMPRINT",FACE,{"disambiguationData":[TD([[makeQuery(id+"F3.imprint","IMPRINT",EDGE,{"derivedFrom":subQ52}),1.0]])]})])],"isStart":true});var subQ182=makeQuery(id+"F29.boolean.opBoolean","INTERSECT",EDGE,{"derivedFrom":[makeQuery(id+"F28.boolean.opBoolean","SPLIT",FACE,{"disambiguationData":[TD([subQ130])],"derivedFrom":makeQuery(id+"F27.boolean.opBoolean","SPLIT",FACE,{"disambiguationData":[TD([subQ130])],"derivedFrom":makeQuery(id+"F26.boolean.opBoolean","SPLIT",FACE,{"disambiguationData":[TD([subQ130])],"derivedFrom":makeQuery(id+"F25.boolean.opBoolean","SPLIT",FACE,{"disambiguationData":[TD([subQ130])],"derivedFrom":makeQuery(id+"F24.boolean.opBoolean","SPLIT",FACE,{"disambiguationData":[TD([subQ130])],"derivedFrom":makeQuery(id+"F1.opRevolve","SWEPT_FACE",FACE,{"disambiguationData":[OSD([sQuery(id+"F0.wireOp",EDGE,"E4")])]})})})})})}),subQ67]});Q23=makeQuery(id+"F48.opFillet","BLEND_EDGE",EDGE,{"blendedFrom":[makeQuery(id+"F47.opFillet","TWEAK_EDGE",EDGE,{"derivedFrom":[makeQuery(id+"F45.opFillet","BLEND_VERTEX",VERTEX,{"blendedFrom":[subQ182,subQ67,subQ110],"blendedInto":[subQ67,subQ110]}),makeQuery(id+"F45.opFillet","BLEND_VERTEX",VERTEX,{"blendedFrom":[subQ182,makeQuery(id+"F42.boolean.opBoolean","MERGE",FACE,{"derivedFrom":[subQ2,subQ1]}),subQ110],"blendedInto":[makeQuery(id+"F42.boolean.opBoolean","MERGE",FACE,{"derivedFrom":[subQ2,subQ1]}),subQ110]})]}),makeQuery(id+"F47.opFillet","BLEND_FACE",FACE,{"disambiguationData":[OSD([subQ0,subQ9]),TDD([makeQuery(id+"F42.boolean.opBoolean","COPY",EDGE,{"disambiguationData":[TD([makeQuery(id+"F23.opLoft","SWEPT_FACE",FACE,{"disambiguationData":[OSD([sQuery(id+"F3.wireOp",EDGE,"E20.8.0"),subQ106,subQ104,subQ103,subQ102,sQuery(id+"F22.wireOp",EDGE,"E27.right")])]})])],"derivedFrom":subQ11})])]}),makeQuery(id+"F47.opFillet","BLEND_FACE",FACE,{"disambiguationData":[OSD([subQ0,subQ9]),TDD([makeQuery(id+"F42.boolean.opBoolean","COPY",EDGE,{"disambiguationData":[TD([subQ101])],"derivedFrom":subQ11})])]}),makeQuery(id+"F47.opFillet","BLEND_FACE",FACE,{"disambiguationData":[OSD([subQ0,subQ9]),TDD([makeQuery(id+"F42.boolean.opBoolean","COPY",EDGE,{"disambiguationData":[TD([subQ94])],"derivedFrom":subQ11})])]}),makeQuery(id+"F47.opFillet","BLEND_FACE",FACE,{"disambiguationData":[OSD([subQ0,subQ9]),TDD([makeQuery(id+"F42.boolean.opBoolean","COPY",EDGE,{"disambiguationData":[TD([subQ88])],"derivedFrom":subQ11})])]}),makeQuery(id+"F47.opFillet","BLEND_FACE",FACE,{"disambiguationData":[OSD([subQ0,subQ9]),TDD([makeQuery(id+"F42.boolean.opBoolean","COPY",EDGE,{"disambiguationData":[TD([subQ81])],"derivedFrom":subQ11})])]}),makeQuery(id+"F47.opFillet","BLEND_FACE",FACE,{"disambiguationData":[OSD([subQ0,subQ9]),TDD([makeQuery(id+"F42.boolean.opBoolean","COPY",EDGE,{"disambiguationData":[TD([subQ74])],"derivedFrom":subQ11})])]}),makeQuery(id+"F47.opFillet","BLEND_FACE",FACE,{"disambiguationData":[OSD([subQ0,subQ9]),TDD([makeQuery(id+"F42.boolean.opBoolean","COPY",EDGE,{"disambiguationData":[TD([subQ67])],"derivedFrom":subQ11})])]}),makeQuery(id+"F47.opFillet","BLEND_FACE",FACE,{"disambiguationData":[OSD([subQ0,subQ9]),TDD([makeQuery(id+"F42.boolean.opBoolean","COPY",EDGE,{"disambiguationData":[TD([makeQuery(id+"F30.opLoft","SWEPT_FACE",FACE,{"disambiguationData":[OSD([subQ58,subQ57,subQ56,sQuery(id+"F22.wireOp",EDGE,"E28.7.1"),subQ55,subQ54])]})])],"derivedFrom":subQ11})])]}),makeQuery(id+"F47.opFillet","BLEND_FACE",FACE,{"disambiguationData":[OSD([subQ0,subQ9]),TDD([makeQuery(id+"F42.boolean.opBoolean","COPY",EDGE,{"disambiguationData":[TD([makeQuery(id+"F31.opLoft","SWEPT_FACE",FACE,{"disambiguationData":[OSD([subQ52,subQ51,subQ53,sQuery(id+"F22.wireOp",EDGE,"E28.8.1"),subQ49,subQ48])]})])],"derivedFrom":subQ11})])]}),makeQuery(id+"F47.opFillet","BLEND_FACE",FACE,{"disambiguationData":[OSD([subQ0,subQ9]),TDD([makeQuery(id+"F42.boolean.opBoolean","COPY",EDGE,{"disambiguationData":[TD([makeQuery(id+"F32.opLoft","SWEPT_FACE",FACE,{"disambiguationData":[OSD([subQ47,subQ46,subQ44,sQuery(id+"F22.wireOp",EDGE,"E28.9.1"),subQ43,subQ42])]})])],"derivedFrom":subQ11})])]}),makeQuery(id+"F47.opFillet","BLEND_FACE",FACE,{"disambiguationData":[OSD([subQ0,subQ9]),TDD([makeQuery(id+"F42.boolean.opBoolean","COPY",EDGE,{"disambiguationData":[TD([makeQuery(id+"F33.opLoft","SWEPT_FACE",FACE,{"disambiguationData":[OSD([subQ41,subQ40,subQ38,sQuery(id+"F22.wireOp",EDGE,"E28.10.1"),subQ37,subQ36])]})])],"derivedFrom":subQ11})])]}),makeQuery(id+"F47.opFillet","BLEND_FACE",FACE,{"disambiguationData":[OSD([subQ0,subQ9]),TDD([makeQuery(id+"F42.boolean.opBoolean","COPY",EDGE,{"disambiguationData":[TD([makeQuery(id+"F34.opLoft","SWEPT_FACE",FACE,{"disambiguationData":[OSD([subQ35,subQ34,subQ32,sQuery(id+"F22.wireOp",EDGE,"E28.11.1"),subQ31,subQ30])]})])],"derivedFrom":subQ11})])]}),makeQuery(id+"F47.opFillet","BLEND_FACE",FACE,{"disambiguationData":[OSD([subQ0,subQ9]),TDD([makeQuery(id+"F42.boolean.opBoolean","COPY",EDGE,{"disambiguationData":[TD([makeQuery(id+"F35.opLoft","SWEPT_FACE",FACE,{"disambiguationData":[OSD([subQ29,subQ28,subQ26,sQuery(id+"F22.wireOp",EDGE,"E28.12.1"),subQ25,subQ24])]})])],"derivedFrom":subQ11})])]}),makeQuery(id+"F47.opFillet","BLEND_FACE",FACE,{"disambiguationData":[OSD([subQ0,subQ9]),TDD([makeQuery(id+"F42.boolean.opBoolean","COPY",EDGE,{"disambiguationData":[TD([makeQuery(id+"F36.opLoft","SWEPT_FACE",FACE,{"disambiguationData":[OSD([subQ23,subQ22,subQ20,sQuery(id+"F22.wireOp",EDGE,"E28.13.1"),subQ19,subQ18])]})])],"derivedFrom":subQ11})])]}),makeQuery(id+"F47.opFillet","BLEND_FACE",FACE,{"disambiguationData":[OSD([subQ0,subQ9]),TDD([makeQuery(id+"F42.boolean.opBoolean","COPY",EDGE,{"disambiguationData":[TD([makeQuery(id+"F37.opLoft","SWEPT_FACE",FACE,{"disambiguationData":[OSD([subQ16,subQ15,subQ14,sQuery(id+"F22.wireOp",EDGE,"E28.14.1"),subQ13,subQ12])]})])],"derivedFrom":subQ11})])]}),makeQuery(id+"F47.opFillet","BLEND_FACE",FACE,{"disambiguationData":[OSD([subQ0,subQ9]),TDD([makeQuery(id+"F42.boolean.opBoolean","COPY",EDGE,{"disambiguationData":[TD([makeQuery(id+"F38.opLoft","SWEPT_FACE",FACE,{"disambiguationData":[OSD([subQ8,subQ7,subQ5,sQuery(id+"F22.wireOp",EDGE,"E28.15.1"),subQ4,subQ3])]})])],"derivedFrom":subQ11})])]})],"blendedInto":[makeQuery(id+"F47.opFillet","BLEND_FACE",FACE,{"disambiguationData":[OSD([subQ0,subQ9]),TDD([makeQuery(id+"F42.boolean.opBoolean","COPY",EDGE,{"disambiguationData":[TD([makeQuery(id+"F23.opLoft","SWEPT_FACE",FACE,{"disambiguationData":[OSD([sQuery(id+"F3.wireOp",EDGE,"E20.8.0"),subQ106,subQ104,subQ103,subQ102,sQuery(id+"F22.wireOp",EDGE,"E27.right")])]})])],"derivedFrom":subQ11})])]}),makeQuery(id+"F47.opFillet","BLEND_FACE",FACE,{"disambiguationData":[OSD([subQ0,subQ9]),TDD([makeQuery(id+"F42.boolean.opBoolean","COPY",EDGE,{"disambiguationData":[TD([subQ101])],"derivedFrom":subQ11})])]}),makeQuery(id+"F47.opFillet","BLEND_FACE",FACE,{"disambiguationData":[OSD([subQ0,subQ9]),TDD([makeQuery(id+"F42.boolean.opBoolean","COPY",EDGE,{"disambiguationData":[TD([subQ94])],"derivedFrom":subQ11})])]}),makeQuery(id+"F47.opFillet","BLEND_FACE",FACE,{"disambiguationData":[OSD([subQ0,subQ9]),TDD([makeQuery(id+"F42.boolean.opBoolean","COPY",EDGE,{"disambiguationData":[TD([subQ88])],"derivedFrom":subQ11})])]}),makeQuery(id+"F47.opFillet","BLEND_FACE",FACE,{"disambiguationData":[OSD([subQ0,subQ9]),TDD([makeQuery(id+"F42.boolean.opBoolean","COPY",EDGE,{"disambiguationData":[TD([subQ81])],"derivedFrom":subQ11})])]}),makeQuery(id+"F47.opFillet","BLEND_FACE",FACE,{"disambiguationData":[OSD([subQ0,subQ9]),TDD([makeQuery(id+"F42.boolean.opBoolean","COPY",EDGE,{"disambiguationData":[TD([subQ74])],"derivedFrom":subQ11})])]}),makeQuery(id+"F47.opFillet","BLEND_FACE",FACE,{"disambiguationData":[OSD([subQ0,subQ9]),TDD([makeQuery(id+"F42.boolean.opBoolean","COPY",EDGE,{"disambiguationData":[TD([subQ67])],"derivedFrom":subQ11})])]}),makeQuery(id+"F47.opFillet","BLEND_FACE",FACE,{"disambiguationData":[OSD([subQ0,subQ9]),TDD([makeQuery(id+"F42.boolean.opBoolean","COPY",EDGE,{"disambiguationData":[TD([makeQuery(id+"F30.opLoft","SWEPT_FACE",FACE,{"disambiguationData":[OSD([subQ58,subQ57,subQ56,sQuery(id+"F22.wireOp",EDGE,"E28.7.1"),subQ55,subQ54])]})])],"derivedFrom":subQ11})])]}),makeQuery(id+"F47.opFillet","BLEND_FACE",FACE,{"disambiguationData":[OSD([subQ0,subQ9]),TDD([makeQuery(id+"F42.boolean.opBoolean","COPY",EDGE,{"disambiguationData":[TD([makeQuery(id+"F31.opLoft","SWEPT_FACE",FACE,{"disambiguationData":[OSD([subQ52,subQ51,subQ53,sQuery(id+"F22.wireOp",EDGE,"E28.8.1"),subQ49,subQ48])]})])],"derivedFrom":subQ11})])]}),makeQuery(id+"F47.opFillet","BLEND_FACE",FACE,{"disambiguationData":[OSD([subQ0,subQ9]),TDD([makeQuery(id+"F42.boolean.opBoolean","COPY",EDGE,{"disambiguationData":[TD([makeQuery(id+"F32.opLoft","SWEPT_FACE",FACE,{"disambiguationData":[OSD([subQ47,subQ46,subQ44,sQuery(id+"F22.wireOp",EDGE,"E28.9.1"),subQ43,subQ42])]})])],"derivedFrom":subQ11})])]}),makeQuery(id+"F47.opFillet","BLEND_FACE",FACE,{"disambiguationData":[OSD([subQ0,subQ9]),TDD([makeQuery(id+"F42.boolean.opBoolean","COPY",EDGE,{"disambiguationData":[TD([makeQuery(id+"F33.opLoft","SWEPT_FACE",FACE,{"disambiguationData":[OSD([subQ41,subQ40,subQ38,sQuery(id+"F22.wireOp",EDGE,"E28.10.1"),subQ37,subQ36])]})])],"derivedFrom":subQ11})])]}),makeQuery(id+"F47.opFillet","BLEND_FACE",FACE,{"disambiguationData":[OSD([subQ0,subQ9]),TDD([makeQuery(id+"F42.boolean.opBoolean","COPY",EDGE,{"disambiguationData":[TD([makeQuery(id+"F34.opLoft","SWEPT_FACE",FACE,{"disambiguationData":[OSD([subQ35,subQ34,subQ32,sQuery(id+"F22.wireOp",EDGE,"E28.11.1"),subQ31,subQ30])]})])],"derivedFrom":subQ11})])]}),makeQuery(id+"F47.opFillet","BLEND_FACE",FACE,{"disambiguationData":[OSD([subQ0,subQ9]),TDD([makeQuery(id+"F42.boolean.opBoolean","COPY",EDGE,{"disambiguationData":[TD([makeQuery(id+"F35.opLoft","SWEPT_FACE",FACE,{"disambiguationData":[OSD([subQ29,subQ28,subQ26,sQuery(id+"F22.wireOp",EDGE,"E28.12.1"),subQ25,subQ24])]})])],"derivedFrom":subQ11})])]}),makeQuery(id+"F47.opFillet","BLEND_FACE",FACE,{"disambiguationData":[OSD([subQ0,subQ9]),TDD([makeQuery(id+"F42.boolean.opBoolean","COPY",EDGE,{"disambiguationData":[TD([makeQuery(id+"F36.opLoft","SWEPT_FACE",FACE,{"disambiguationData":[OSD([subQ23,subQ22,subQ20,sQuery(id+"F22.wireOp",EDGE,"E28.13.1"),subQ19,subQ18])]})])],"derivedFrom":subQ11})])]}),makeQuery(id+"F47.opFillet","BLEND_FACE",FACE,{"disambiguationData":[OSD([subQ0,subQ9]),TDD([makeQuery(id+"F42.boolean.opBoolean","COPY",EDGE,{"disambiguationData":[TD([makeQuery(id+"F37.opLoft","SWEPT_FACE",FACE,{"disambiguationData":[OSD([subQ16,subQ15,subQ14,sQuery(id+"F22.wireOp",EDGE,"E28.14.1"),subQ13,subQ12])]})])],"derivedFrom":subQ11})])]}),makeQuery(id+"F47.opFillet","BLEND_FACE",FACE,{"disambiguationData":[OSD([subQ0,subQ9]),TDD([makeQuery(id+"F42.boolean.opBoolean","COPY",EDGE,{"disambiguationData":[TD([makeQuery(id+"F38.opLoft","SWEPT_FACE",FACE,{"disambiguationData":[OSD([subQ8,subQ7,subQ5,sQuery(id+"F22.wireOp",EDGE,"E28.15.1"),subQ4,subQ3])]})])],"derivedFrom":subQ11})])]})]});}
            var Q24;
            {var subQ0=sQuery(id+"F41.wireOp",EDGE,"E34");var subQ1=sQuery(id+"F41.wireOp",EDGE,"E32");Q24=makeQuery(id+"F42.boolean.opBoolean","INTERSECT",EDGE,{"derivedFrom":[makeQuery(id+"F28.opLoft","SWEPT_FACE",FACE,{"disambiguationData":[OSD([sQuery(id+"F3.wireOp",EDGE,"E20.13.0"),sQuery(id+"F3.wireOp",EDGE,"E20.13.1"),sQuery(id+"F3.wireOp",EDGE,"E20.13.3"),sQuery(id+"F22.wireOp",EDGE,"E28.5.1"),sQuery(id+"F22.wireOp",EDGE,"E28.5.2"),sQuery(id+"F22.wireOp",EDGE,"E28.5.3")])]}),makeQuery(id+"F42.opRevolve","SWEPT_FACE",FACE,{"disambiguationData":[OSD([subQ1]),TDD([makeQuery(id+"F41.imprint","IMPRINT",EDGE,{"disambiguationData":[TD([[makeQuery(id+"F41.imprint","INTERSECT",VERTEX,{"disambiguationData":[OD(0.0)],"derivedFrom":[subQ1,subQ0]}),-1.0]])],"derivedFrom":subQ1})])]})]});}
            var Q25;
            {var subQ0=sQuery(id+"F22.wireOp",EDGE,"E28.6.3");var subQ1=sQuery(id+"F22.wireOp",EDGE,"E28.6.2");var subQ2=sQuery(id+"F22.wireOp",EDGE,"E28.6.0");var subQ3=sQuery(id+"F3.wireOp",EDGE,"E20.14.3");var subQ4=sQuery(id+"F3.wireOp",EDGE,"E20.14.1");var subQ5=makeQuery(id+"F29.opLoft","SWEPT_FACE",FACE,{"disambiguationData":[OSD([subQ4,sQuery(id+"F3.wireOp",EDGE,"E20.14.2"),subQ3,subQ2,subQ1,subQ0])]});var subQ6=sQuery(id+"F22.wireOp",EDGE,"E28.6.1");var subQ7=sQuery(id+"F41.wireOp",EDGE,"E34");var subQ8=sQuery(id+"F41.wireOp",EDGE,"E32");Q25=makeQuery(id+"F44.opFillet","BLEND_EDGE",EDGE,{"blendedFrom":[makeQuery(id+"F40.boolean.opBoolean","INTERSECT",EDGE,{"derivedFrom":[subQ5,makeQuery(id+"F40.opExtrude","CAP_FACE",FACE,{"disambiguationData":[OSD([sQuery(id+"F39.wireOp",EDGE,"E29"),sQuery(id+"F39.wireOp",EDGE,"E30")])],"isStart":true})]}),makeQuery(id+"F42.boolean.opBoolean","COPY",FACE,{"disambiguationData":[TD([makeQuery(id+"F29.opLoft","SWEPT_FACE",FACE,{"disambiguationData":[OSD([sQuery(id+"F3.wireOp",EDGE,"E20.14.0"),subQ4,subQ3,subQ6,subQ1,subQ0])]})])],"derivedFrom":makeQuery(id+"F42.opRevolve","SWEPT_FACE",FACE,{"disambiguationData":[OSD([subQ8]),TDD([makeQuery(id+"F41.imprint","IMPRINT",EDGE,{"disambiguationData":[TD([[makeQuery(id+"F41.imprint","INTERSECT",VERTEX,{"disambiguationData":[OD(0.0)],"derivedFrom":[subQ8,subQ7]}),-1.0]])],"derivedFrom":subQ8})])]})})],"blendedInto":[makeQuery(id+"F42.boolean.opBoolean","COPY",FACE,{"disambiguationData":[TD([makeQuery(id+"F29.opLoft","SWEPT_FACE",FACE,{"disambiguationData":[OSD([sQuery(id+"F3.wireOp",EDGE,"E20.14.0"),subQ4,subQ3,subQ6,subQ1,subQ0])]})])],"derivedFrom":makeQuery(id+"F42.opRevolve","SWEPT_FACE",FACE,{"disambiguationData":[OSD([subQ8]),TDD([makeQuery(id+"F41.imprint","IMPRINT",EDGE,{"disambiguationData":[TD([[makeQuery(id+"F41.imprint","INTERSECT",VERTEX,{"disambiguationData":[OD(0.0)],"derivedFrom":[subQ8,subQ7]}),-1.0]])],"derivedFrom":subQ8})])]})})]});}
            var Q26;
            {var subQ0=sQuery(id+"F41.wireOp",EDGE,"E37");var subQ1=makeQuery(id+"F42.opRevolve","SWEPT_FACE",FACE,{"disambiguationData":[OSD([subQ0])]});var subQ2=makeQuery(id+"F40.opExtrude","CAP_FACE",FACE,{"disambiguationData":[OSD([sQuery(id+"F39.wireOp",EDGE,"E29"),sQuery(id+"F39.wireOp",EDGE,"E30")])],"isStart":true});var subQ3=sQuery(id+"F22.wireOp",EDGE,"E28.15.3");var subQ4=sQuery(id+"F22.wireOp",EDGE,"E28.15.2");var subQ5=sQuery(id+"F3.wireOp",EDGE,"E20.7.3");var subQ7=sQuery(id+"F3.wireOp",EDGE,"E20.7.1");var subQ8=sQuery(id+"F3.wireOp",EDGE,"E20.7.0");var subQ9=sQuery(id+"F41.wireOp",EDGE,"E38");var subQ10=makeQuery(id+"F42.opRevolve","SWEPT_FACE",FACE,{"disambiguationData":[OSD([subQ9])]});var subQ11=makeQuery(id+"F42.opRevolve","SWEPT_EDGE",EDGE,{"disambiguationData":[OSD([subQ0,subQ9])]});var subQ12=sQuery(id+"F22.wireOp",EDGE,"E28.14.3");var subQ13=sQuery(id+"F22.wireOp",EDGE,"E28.14.2");var subQ14=sQuery(id+"F3.wireOp",EDGE,"E20.6.3");var subQ15=sQuery(id+"F3.wireOp",EDGE,"E20.6.1");var subQ16=sQuery(id+"F3.wireOp",EDGE,"E20.6.0");var subQ18=sQuery(id+"F22.wireOp",EDGE,"E28.13.3");var subQ19=sQuery(id+"F22.wireOp",EDGE,"E28.13.2");var subQ20=sQuery(id+"F3.wireOp",EDGE,"E20.5.3");var subQ22=sQuery(id+"F3.wireOp",EDGE,"E20.5.1");var subQ23=sQuery(id+"F3.wireOp",EDGE,"E20.5.0");var subQ24=sQuery(id+"F22.wireOp",EDGE,"E28.12.3");var subQ25=sQuery(id+"F22.wireOp",EDGE,"E28.12.2");var subQ26=sQuery(id+"F3.wireOp",EDGE,"E20.4.3");var subQ28=sQuery(id+"F3.wireOp",EDGE,"E20.4.1");var subQ29=sQuery(id+"F3.wireOp",EDGE,"E20.4.0");var subQ30=sQuery(id+"F22.wireOp",EDGE,"E28.11.3");var subQ31=sQuery(id+"F22.wireOp",EDGE,"E28.11.2");var subQ32=sQuery(id+"F3.wireOp",EDGE,"E20.3.3");var subQ34=sQuery(id+"F3.wireOp",EDGE,"E20.3.1");var subQ35=sQuery(id+"F3.wireOp",EDGE,"E20.3.0");var subQ36=sQuery(id+"F22.wireOp",EDGE,"E28.10.3");var subQ37=sQuery(id+"F22.wireOp",EDGE,"E28.10.2");var subQ38=sQuery(id+"F3.wireOp",EDGE,"E20.2.3");var subQ40=sQuery(id+"F3.wireOp",EDGE,"E20.2.1");var subQ41=sQuery(id+"F3.wireOp",EDGE,"E20.2.0");var subQ42=sQuery(id+"F22.wireOp",EDGE,"E28.9.3");var subQ43=sQuery(id+"F22.wireOp",EDGE,"E28.9.2");var subQ44=sQuery(id+"F3.wireOp",EDGE,"E20.1.3");var subQ46=sQuery(id+"F3.wireOp",EDGE,"E20.1.1");var subQ47=sQuery(id+"F3.wireOp",EDGE,"E20.1.0");var subQ48=sQuery(id+"F22.wireOp",EDGE,"E28.8.3");var subQ49=sQuery(id+"F22.wireOp",EDGE,"E28.8.2");var subQ51=sQuery(id+"F3.wireOp",EDGE,"E18.top");var subQ52=sQuery(id+"F3.wireOp",EDGE,"E18.bottom");var subQ53=sQuery(id+"F3.wireOp",EDGE,"E18.left");var subQ54=sQuery(id+"F22.wireOp",EDGE,"E28.7.3");var subQ55=sQuery(id+"F22.wireOp",EDGE,"E28.7.2");var subQ56=sQuery(id+"F3.wireOp",EDGE,"E20.15.3");var subQ57=sQuery(id+"F3.wireOp",EDGE,"E20.15.1");var subQ58=sQuery(id+"F3.wireOp",EDGE,"E20.15.0");var subQ60=sQuery(id+"F22.wireOp",EDGE,"E28.6.3");var subQ61=sQuery(id+"F22.wireOp",EDGE,"E28.6.2");var subQ62=sQuery(id+"F3.wireOp",EDGE,"E20.14.3");var subQ64=sQuery(id+"F3.wireOp",EDGE,"E20.14.1");var subQ65=sQuery(id+"F3.wireOp",EDGE,"E20.14.0");var subQ66=sQuery(id+"F22.wireOp",EDGE,"E28.5.3");var subQ67=sQuery(id+"F22.wireOp",EDGE,"E28.5.2");var subQ68=sQuery(id+"F3.wireOp",EDGE,"E20.13.3");var subQ70=sQuery(id+"F3.wireOp",EDGE,"E20.13.1");var subQ72=sQuery(id+"F3.wireOp",EDGE,"E20.13.0");var subQ73=makeQuery(id+"F28.opLoft","SWEPT_FACE",FACE,{"disambiguationData":[OSD([subQ72,subQ70,subQ68,sQuery(id+"F22.wireOp",EDGE,"E28.5.1"),subQ67,subQ66])]});var subQ74=sQuery(id+"F22.wireOp",EDGE,"E28.4.3");var subQ75=sQuery(id+"F22.wireOp",EDGE,"E28.4.2");var subQ76=sQuery(id+"F3.wireOp",EDGE,"E20.12.3");var subQ78=sQuery(id+"F3.wireOp",EDGE,"E20.12.1");var subQ79=sQuery(id+"F3.wireOp",EDGE,"E20.12.0");var subQ80=makeQuery(id+"F27.opLoft","SWEPT_FACE",FACE,{"disambiguationData":[OSD([subQ79,subQ78,subQ76,sQuery(id+"F22.wireOp",EDGE,"E28.4.1"),subQ75,subQ74])]});var subQ81=sQuery(id+"F22.wireOp",EDGE,"E28.3.3");var subQ82=sQuery(id+"F22.wireOp",EDGE,"E28.3.2");var subQ83=sQuery(id+"F3.wireOp",EDGE,"E20.11.3");var subQ85=sQuery(id+"F3.wireOp",EDGE,"E20.11.1");var subQ86=sQuery(id+"F3.wireOp",EDGE,"E20.11.0");var subQ87=makeQuery(id+"F26.opLoft","SWEPT_FACE",FACE,{"disambiguationData":[OSD([subQ86,subQ85,subQ83,sQuery(id+"F22.wireOp",EDGE,"E28.3.1"),subQ82,subQ81])]});var subQ88=sQuery(id+"F22.wireOp",EDGE,"E28.2.3");var subQ89=sQuery(id+"F22.wireOp",EDGE,"E28.2.2");var subQ90=sQuery(id+"F3.wireOp",EDGE,"E20.10.3");var subQ91=sQuery(id+"F3.wireOp",EDGE,"E20.10.1");var subQ92=sQuery(id+"F3.wireOp",EDGE,"E20.10.0");var subQ93=makeQuery(id+"F25.opLoft","SWEPT_FACE",FACE,{"disambiguationData":[OSD([subQ92,subQ91,subQ90,sQuery(id+"F22.wireOp",EDGE,"E28.2.1"),subQ89,subQ88])]});var subQ95=sQuery(id+"F22.wireOp",EDGE,"E28.1.3");var subQ96=sQuery(id+"F22.wireOp",EDGE,"E28.1.2");var subQ97=sQuery(id+"F3.wireOp",EDGE,"E20.9.3");var subQ98=sQuery(id+"F3.wireOp",EDGE,"E20.9.1");var subQ99=sQuery(id+"F3.wireOp",EDGE,"E20.9.0");var subQ100=makeQuery(id+"F24.opLoft","SWEPT_FACE",FACE,{"disambiguationData":[OSD([subQ99,subQ98,subQ97,sQuery(id+"F22.wireOp",EDGE,"E28.1.1"),subQ96,subQ95])]});var subQ101=sQuery(id+"F22.wireOp",EDGE,"E27.top");var subQ102=sQuery(id+"F22.wireOp",EDGE,"E27.bottom");var subQ103=sQuery(id+"F3.wireOp",EDGE,"E20.8.3");var subQ105=sQuery(id+"F3.wireOp",EDGE,"E20.8.1");var subQ109=makeQuery(id+"F42.boolean.opBoolean","COPY",FACE,{"disambiguationData":[TD([subQ73])],"derivedFrom":subQ10});var subQ135=makeQuery(id+"F5.opLoft","CAP_FACE",FACE,{"disambiguationData":[OSD([makeQuery(id+"F3.imprint","IMPRINT",FACE,{"disambiguationData":[TD([[makeQuery(id+"F3.imprint","IMPRINT",EDGE,{"derivedFrom":subQ52}),1.0]])]})])],"isStart":true});var subQ181=makeQuery(id+"F28.boolean.opBoolean","INTERSECT",EDGE,{"derivedFrom":[makeQuery(id+"F27.boolean.opBoolean","SPLIT",FACE,{"disambiguationData":[TD([subQ135])],"derivedFrom":makeQuery(id+"F26.boolean.opBoolean","SPLIT",FACE,{"disambiguationData":[TD([subQ135])],"derivedFrom":makeQuery(id+"F25.boolean.opBoolean","SPLIT",FACE,{"disambiguationData":[TD([subQ135])],"derivedFrom":makeQuery(id+"F24.boolean.opBoolean","SPLIT",FACE,{"disambiguationData":[TD([subQ135])],"derivedFrom":makeQuery(id+"F1.opRevolve","SWEPT_FACE",FACE,{"disambiguationData":[OSD([sQuery(id+"F0.wireOp",EDGE,"E4")])]})})})})}),subQ73]});Q26=makeQuery(id+"F48.opFillet","BLEND_EDGE",EDGE,{"blendedFrom":[makeQuery(id+"F47.opFillet","TWEAK_EDGE",EDGE,{"derivedFrom":[makeQuery(id+"F45.opFillet","BLEND_VERTEX",VERTEX,{"blendedFrom":[subQ181,subQ73,subQ109],"blendedInto":[subQ73,subQ109]}),makeQuery(id+"F45.opFillet","BLEND_VERTEX",VERTEX,{"blendedFrom":[subQ181,makeQuery(id+"F42.boolean.opBoolean","MERGE",FACE,{"derivedFrom":[subQ2,subQ1]}),subQ109],"blendedInto":[makeQuery(id+"F42.boolean.opBoolean","MERGE",FACE,{"derivedFrom":[subQ2,subQ1]}),subQ109]})]}),makeQuery(id+"F47.opFillet","BLEND_FACE",FACE,{"disambiguationData":[OSD([subQ0,subQ9]),TDD([makeQuery(id+"F42.boolean.opBoolean","COPY",EDGE,{"disambiguationData":[TD([makeQuery(id+"F23.opLoft","SWEPT_FACE",FACE,{"disambiguationData":[OSD([sQuery(id+"F3.wireOp",EDGE,"E20.8.0"),subQ105,subQ103,subQ102,subQ101,sQuery(id+"F22.wireOp",EDGE,"E27.right")])]})])],"derivedFrom":subQ11})])]}),makeQuery(id+"F47.opFillet","BLEND_FACE",FACE,{"disambiguationData":[OSD([subQ0,subQ9]),TDD([makeQuery(id+"F42.boolean.opBoolean","COPY",EDGE,{"disambiguationData":[TD([subQ100])],"derivedFrom":subQ11})])]}),makeQuery(id+"F47.opFillet","BLEND_FACE",FACE,{"disambiguationData":[OSD([subQ0,subQ9]),TDD([makeQuery(id+"F42.boolean.opBoolean","COPY",EDGE,{"disambiguationData":[TD([subQ93])],"derivedFrom":subQ11})])]}),makeQuery(id+"F47.opFillet","BLEND_FACE",FACE,{"disambiguationData":[OSD([subQ0,subQ9]),TDD([makeQuery(id+"F42.boolean.opBoolean","COPY",EDGE,{"disambiguationData":[TD([subQ87])],"derivedFrom":subQ11})])]}),makeQuery(id+"F47.opFillet","BLEND_FACE",FACE,{"disambiguationData":[OSD([subQ0,subQ9]),TDD([makeQuery(id+"F42.boolean.opBoolean","COPY",EDGE,{"disambiguationData":[TD([subQ80])],"derivedFrom":subQ11})])]}),makeQuery(id+"F47.opFillet","BLEND_FACE",FACE,{"disambiguationData":[OSD([subQ0,subQ9]),TDD([makeQuery(id+"F42.boolean.opBoolean","COPY",EDGE,{"disambiguationData":[TD([subQ73])],"derivedFrom":subQ11})])]}),makeQuery(id+"F47.opFillet","BLEND_FACE",FACE,{"disambiguationData":[OSD([subQ0,subQ9]),TDD([makeQuery(id+"F42.boolean.opBoolean","COPY",EDGE,{"disambiguationData":[TD([makeQuery(id+"F29.opLoft","SWEPT_FACE",FACE,{"disambiguationData":[OSD([subQ65,subQ64,subQ62,sQuery(id+"F22.wireOp",EDGE,"E28.6.1"),subQ61,subQ60])]})])],"derivedFrom":subQ11})])]}),makeQuery(id+"F47.opFillet","BLEND_FACE",FACE,{"disambiguationData":[OSD([subQ0,subQ9]),TDD([makeQuery(id+"F42.boolean.opBoolean","COPY",EDGE,{"disambiguationData":[TD([makeQuery(id+"F30.opLoft","SWEPT_FACE",FACE,{"disambiguationData":[OSD([subQ58,subQ57,subQ56,sQuery(id+"F22.wireOp",EDGE,"E28.7.1"),subQ55,subQ54])]})])],"derivedFrom":subQ11})])]}),makeQuery(id+"F47.opFillet","BLEND_FACE",FACE,{"disambiguationData":[OSD([subQ0,subQ9]),TDD([makeQuery(id+"F42.boolean.opBoolean","COPY",EDGE,{"disambiguationData":[TD([makeQuery(id+"F31.opLoft","SWEPT_FACE",FACE,{"disambiguationData":[OSD([subQ52,subQ51,subQ53,sQuery(id+"F22.wireOp",EDGE,"E28.8.1"),subQ49,subQ48])]})])],"derivedFrom":subQ11})])]}),makeQuery(id+"F47.opFillet","BLEND_FACE",FACE,{"disambiguationData":[OSD([subQ0,subQ9]),TDD([makeQuery(id+"F42.boolean.opBoolean","COPY",EDGE,{"disambiguationData":[TD([makeQuery(id+"F32.opLoft","SWEPT_FACE",FACE,{"disambiguationData":[OSD([subQ47,subQ46,subQ44,sQuery(id+"F22.wireOp",EDGE,"E28.9.1"),subQ43,subQ42])]})])],"derivedFrom":subQ11})])]}),makeQuery(id+"F47.opFillet","BLEND_FACE",FACE,{"disambiguationData":[OSD([subQ0,subQ9]),TDD([makeQuery(id+"F42.boolean.opBoolean","COPY",EDGE,{"disambiguationData":[TD([makeQuery(id+"F33.opLoft","SWEPT_FACE",FACE,{"disambiguationData":[OSD([subQ41,subQ40,subQ38,sQuery(id+"F22.wireOp",EDGE,"E28.10.1"),subQ37,subQ36])]})])],"derivedFrom":subQ11})])]}),makeQuery(id+"F47.opFillet","BLEND_FACE",FACE,{"disambiguationData":[OSD([subQ0,subQ9]),TDD([makeQuery(id+"F42.boolean.opBoolean","COPY",EDGE,{"disambiguationData":[TD([makeQuery(id+"F34.opLoft","SWEPT_FACE",FACE,{"disambiguationData":[OSD([subQ35,subQ34,subQ32,sQuery(id+"F22.wireOp",EDGE,"E28.11.1"),subQ31,subQ30])]})])],"derivedFrom":subQ11})])]}),makeQuery(id+"F47.opFillet","BLEND_FACE",FACE,{"disambiguationData":[OSD([subQ0,subQ9]),TDD([makeQuery(id+"F42.boolean.opBoolean","COPY",EDGE,{"disambiguationData":[TD([makeQuery(id+"F35.opLoft","SWEPT_FACE",FACE,{"disambiguationData":[OSD([subQ29,subQ28,subQ26,sQuery(id+"F22.wireOp",EDGE,"E28.12.1"),subQ25,subQ24])]})])],"derivedFrom":subQ11})])]}),makeQuery(id+"F47.opFillet","BLEND_FACE",FACE,{"disambiguationData":[OSD([subQ0,subQ9]),TDD([makeQuery(id+"F42.boolean.opBoolean","COPY",EDGE,{"disambiguationData":[TD([makeQuery(id+"F36.opLoft","SWEPT_FACE",FACE,{"disambiguationData":[OSD([subQ23,subQ22,subQ20,sQuery(id+"F22.wireOp",EDGE,"E28.13.1"),subQ19,subQ18])]})])],"derivedFrom":subQ11})])]}),makeQuery(id+"F47.opFillet","BLEND_FACE",FACE,{"disambiguationData":[OSD([subQ0,subQ9]),TDD([makeQuery(id+"F42.boolean.opBoolean","COPY",EDGE,{"disambiguationData":[TD([makeQuery(id+"F37.opLoft","SWEPT_FACE",FACE,{"disambiguationData":[OSD([subQ16,subQ15,subQ14,sQuery(id+"F22.wireOp",EDGE,"E28.14.1"),subQ13,subQ12])]})])],"derivedFrom":subQ11})])]}),makeQuery(id+"F47.opFillet","BLEND_FACE",FACE,{"disambiguationData":[OSD([subQ0,subQ9]),TDD([makeQuery(id+"F42.boolean.opBoolean","COPY",EDGE,{"disambiguationData":[TD([makeQuery(id+"F38.opLoft","SWEPT_FACE",FACE,{"disambiguationData":[OSD([subQ8,subQ7,subQ5,sQuery(id+"F22.wireOp",EDGE,"E28.15.1"),subQ4,subQ3])]})])],"derivedFrom":subQ11})])]})],"blendedInto":[makeQuery(id+"F47.opFillet","BLEND_FACE",FACE,{"disambiguationData":[OSD([subQ0,subQ9]),TDD([makeQuery(id+"F42.boolean.opBoolean","COPY",EDGE,{"disambiguationData":[TD([makeQuery(id+"F23.opLoft","SWEPT_FACE",FACE,{"disambiguationData":[OSD([sQuery(id+"F3.wireOp",EDGE,"E20.8.0"),subQ105,subQ103,subQ102,subQ101,sQuery(id+"F22.wireOp",EDGE,"E27.right")])]})])],"derivedFrom":subQ11})])]}),makeQuery(id+"F47.opFillet","BLEND_FACE",FACE,{"disambiguationData":[OSD([subQ0,subQ9]),TDD([makeQuery(id+"F42.boolean.opBoolean","COPY",EDGE,{"disambiguationData":[TD([subQ100])],"derivedFrom":subQ11})])]}),makeQuery(id+"F47.opFillet","BLEND_FACE",FACE,{"disambiguationData":[OSD([subQ0,subQ9]),TDD([makeQuery(id+"F42.boolean.opBoolean","COPY",EDGE,{"disambiguationData":[TD([subQ93])],"derivedFrom":subQ11})])]}),makeQuery(id+"F47.opFillet","BLEND_FACE",FACE,{"disambiguationData":[OSD([subQ0,subQ9]),TDD([makeQuery(id+"F42.boolean.opBoolean","COPY",EDGE,{"disambiguationData":[TD([subQ87])],"derivedFrom":subQ11})])]}),makeQuery(id+"F47.opFillet","BLEND_FACE",FACE,{"disambiguationData":[OSD([subQ0,subQ9]),TDD([makeQuery(id+"F42.boolean.opBoolean","COPY",EDGE,{"disambiguationData":[TD([subQ80])],"derivedFrom":subQ11})])]}),makeQuery(id+"F47.opFillet","BLEND_FACE",FACE,{"disambiguationData":[OSD([subQ0,subQ9]),TDD([makeQuery(id+"F42.boolean.opBoolean","COPY",EDGE,{"disambiguationData":[TD([subQ73])],"derivedFrom":subQ11})])]}),makeQuery(id+"F47.opFillet","BLEND_FACE",FACE,{"disambiguationData":[OSD([subQ0,subQ9]),TDD([makeQuery(id+"F42.boolean.opBoolean","COPY",EDGE,{"disambiguationData":[TD([makeQuery(id+"F29.opLoft","SWEPT_FACE",FACE,{"disambiguationData":[OSD([subQ65,subQ64,subQ62,sQuery(id+"F22.wireOp",EDGE,"E28.6.1"),subQ61,subQ60])]})])],"derivedFrom":subQ11})])]}),makeQuery(id+"F47.opFillet","BLEND_FACE",FACE,{"disambiguationData":[OSD([subQ0,subQ9]),TDD([makeQuery(id+"F42.boolean.opBoolean","COPY",EDGE,{"disambiguationData":[TD([makeQuery(id+"F30.opLoft","SWEPT_FACE",FACE,{"disambiguationData":[OSD([subQ58,subQ57,subQ56,sQuery(id+"F22.wireOp",EDGE,"E28.7.1"),subQ55,subQ54])]})])],"derivedFrom":subQ11})])]}),makeQuery(id+"F47.opFillet","BLEND_FACE",FACE,{"disambiguationData":[OSD([subQ0,subQ9]),TDD([makeQuery(id+"F42.boolean.opBoolean","COPY",EDGE,{"disambiguationData":[TD([makeQuery(id+"F31.opLoft","SWEPT_FACE",FACE,{"disambiguationData":[OSD([subQ52,subQ51,subQ53,sQuery(id+"F22.wireOp",EDGE,"E28.8.1"),subQ49,subQ48])]})])],"derivedFrom":subQ11})])]}),makeQuery(id+"F47.opFillet","BLEND_FACE",FACE,{"disambiguationData":[OSD([subQ0,subQ9]),TDD([makeQuery(id+"F42.boolean.opBoolean","COPY",EDGE,{"disambiguationData":[TD([makeQuery(id+"F32.opLoft","SWEPT_FACE",FACE,{"disambiguationData":[OSD([subQ47,subQ46,subQ44,sQuery(id+"F22.wireOp",EDGE,"E28.9.1"),subQ43,subQ42])]})])],"derivedFrom":subQ11})])]}),makeQuery(id+"F47.opFillet","BLEND_FACE",FACE,{"disambiguationData":[OSD([subQ0,subQ9]),TDD([makeQuery(id+"F42.boolean.opBoolean","COPY",EDGE,{"disambiguationData":[TD([makeQuery(id+"F33.opLoft","SWEPT_FACE",FACE,{"disambiguationData":[OSD([subQ41,subQ40,subQ38,sQuery(id+"F22.wireOp",EDGE,"E28.10.1"),subQ37,subQ36])]})])],"derivedFrom":subQ11})])]}),makeQuery(id+"F47.opFillet","BLEND_FACE",FACE,{"disambiguationData":[OSD([subQ0,subQ9]),TDD([makeQuery(id+"F42.boolean.opBoolean","COPY",EDGE,{"disambiguationData":[TD([makeQuery(id+"F34.opLoft","SWEPT_FACE",FACE,{"disambiguationData":[OSD([subQ35,subQ34,subQ32,sQuery(id+"F22.wireOp",EDGE,"E28.11.1"),subQ31,subQ30])]})])],"derivedFrom":subQ11})])]}),makeQuery(id+"F47.opFillet","BLEND_FACE",FACE,{"disambiguationData":[OSD([subQ0,subQ9]),TDD([makeQuery(id+"F42.boolean.opBoolean","COPY",EDGE,{"disambiguationData":[TD([makeQuery(id+"F35.opLoft","SWEPT_FACE",FACE,{"disambiguationData":[OSD([subQ29,subQ28,subQ26,sQuery(id+"F22.wireOp",EDGE,"E28.12.1"),subQ25,subQ24])]})])],"derivedFrom":subQ11})])]}),makeQuery(id+"F47.opFillet","BLEND_FACE",FACE,{"disambiguationData":[OSD([subQ0,subQ9]),TDD([makeQuery(id+"F42.boolean.opBoolean","COPY",EDGE,{"disambiguationData":[TD([makeQuery(id+"F36.opLoft","SWEPT_FACE",FACE,{"disambiguationData":[OSD([subQ23,subQ22,subQ20,sQuery(id+"F22.wireOp",EDGE,"E28.13.1"),subQ19,subQ18])]})])],"derivedFrom":subQ11})])]}),makeQuery(id+"F47.opFillet","BLEND_FACE",FACE,{"disambiguationData":[OSD([subQ0,subQ9]),TDD([makeQuery(id+"F42.boolean.opBoolean","COPY",EDGE,{"disambiguationData":[TD([makeQuery(id+"F37.opLoft","SWEPT_FACE",FACE,{"disambiguationData":[OSD([subQ16,subQ15,subQ14,sQuery(id+"F22.wireOp",EDGE,"E28.14.1"),subQ13,subQ12])]})])],"derivedFrom":subQ11})])]}),makeQuery(id+"F47.opFillet","BLEND_FACE",FACE,{"disambiguationData":[OSD([subQ0,subQ9]),TDD([makeQuery(id+"F42.boolean.opBoolean","COPY",EDGE,{"disambiguationData":[TD([makeQuery(id+"F38.opLoft","SWEPT_FACE",FACE,{"disambiguationData":[OSD([subQ8,subQ7,subQ5,sQuery(id+"F22.wireOp",EDGE,"E28.15.1"),subQ4,subQ3])]})])],"derivedFrom":subQ11})])]})]});}
            var Q27;
            {var subQ0=sQuery(id+"F22.wireOp",EDGE,"E28.5.3");var subQ1=sQuery(id+"F22.wireOp",EDGE,"E28.5.2");var subQ2=sQuery(id+"F22.wireOp",EDGE,"E28.5.0");var subQ3=sQuery(id+"F3.wireOp",EDGE,"E20.13.3");var subQ4=sQuery(id+"F3.wireOp",EDGE,"E20.13.1");var subQ5=makeQuery(id+"F28.opLoft","SWEPT_FACE",FACE,{"disambiguationData":[OSD([subQ4,sQuery(id+"F3.wireOp",EDGE,"E20.13.2"),subQ3,subQ2,subQ1,subQ0])]});var subQ6=sQuery(id+"F22.wireOp",EDGE,"E28.5.1");var subQ7=sQuery(id+"F41.wireOp",EDGE,"E34");var subQ8=sQuery(id+"F41.wireOp",EDGE,"E32");Q27=makeQuery(id+"F44.opFillet","BLEND_EDGE",EDGE,{"blendedFrom":[makeQuery(id+"F40.boolean.opBoolean","INTERSECT",EDGE,{"derivedFrom":[subQ5,makeQuery(id+"F40.opExtrude","CAP_FACE",FACE,{"disambiguationData":[OSD([sQuery(id+"F39.wireOp",EDGE,"E29"),sQuery(id+"F39.wireOp",EDGE,"E30")])],"isStart":true})]}),makeQuery(id+"F42.boolean.opBoolean","COPY",FACE,{"disambiguationData":[TD([makeQuery(id+"F28.opLoft","SWEPT_FACE",FACE,{"disambiguationData":[OSD([sQuery(id+"F3.wireOp",EDGE,"E20.13.0"),subQ4,subQ3,subQ6,subQ1,subQ0])]})])],"derivedFrom":makeQuery(id+"F42.opRevolve","SWEPT_FACE",FACE,{"disambiguationData":[OSD([subQ8]),TDD([makeQuery(id+"F41.imprint","IMPRINT",EDGE,{"disambiguationData":[TD([[makeQuery(id+"F41.imprint","INTERSECT",VERTEX,{"disambiguationData":[OD(0.0)],"derivedFrom":[subQ8,subQ7]}),-1.0]])],"derivedFrom":subQ8})])]})})],"blendedInto":[makeQuery(id+"F42.boolean.opBoolean","COPY",FACE,{"disambiguationData":[TD([makeQuery(id+"F28.opLoft","SWEPT_FACE",FACE,{"disambiguationData":[OSD([sQuery(id+"F3.wireOp",EDGE,"E20.13.0"),subQ4,subQ3,subQ6,subQ1,subQ0])]})])],"derivedFrom":makeQuery(id+"F42.opRevolve","SWEPT_FACE",FACE,{"disambiguationData":[OSD([subQ8]),TDD([makeQuery(id+"F41.imprint","IMPRINT",EDGE,{"disambiguationData":[TD([[makeQuery(id+"F41.imprint","INTERSECT",VERTEX,{"disambiguationData":[OD(0.0)],"derivedFrom":[subQ8,subQ7]}),-1.0]])],"derivedFrom":subQ8})])]})})]});}
            var Q28;
            {var subQ0=sQuery(id+"F41.wireOp",EDGE,"E34");var subQ1=sQuery(id+"F41.wireOp",EDGE,"E32");Q28=makeQuery(id+"F42.boolean.opBoolean","INTERSECT",EDGE,{"derivedFrom":[makeQuery(id+"F27.opLoft","SWEPT_FACE",FACE,{"disambiguationData":[OSD([sQuery(id+"F3.wireOp",EDGE,"E20.12.0"),sQuery(id+"F3.wireOp",EDGE,"E20.12.1"),sQuery(id+"F3.wireOp",EDGE,"E20.12.3"),sQuery(id+"F22.wireOp",EDGE,"E28.4.1"),sQuery(id+"F22.wireOp",EDGE,"E28.4.2"),sQuery(id+"F22.wireOp",EDGE,"E28.4.3")])]}),makeQuery(id+"F42.opRevolve","SWEPT_FACE",FACE,{"disambiguationData":[OSD([subQ1]),TDD([makeQuery(id+"F41.imprint","IMPRINT",EDGE,{"disambiguationData":[TD([[makeQuery(id+"F41.imprint","INTERSECT",VERTEX,{"disambiguationData":[OD(0.0)],"derivedFrom":[subQ1,subQ0]}),-1.0]])],"derivedFrom":subQ1})])]})]});}
            var Q29;
            {var subQ0=sQuery(id+"F41.wireOp",EDGE,"E37");var subQ1=makeQuery(id+"F42.opRevolve","SWEPT_FACE",FACE,{"disambiguationData":[OSD([subQ0])]});var subQ2=makeQuery(id+"F40.opExtrude","CAP_FACE",FACE,{"disambiguationData":[OSD([sQuery(id+"F39.wireOp",EDGE,"E29"),sQuery(id+"F39.wireOp",EDGE,"E30")])],"isStart":true});var subQ3=sQuery(id+"F22.wireOp",EDGE,"E28.15.3");var subQ4=sQuery(id+"F22.wireOp",EDGE,"E28.15.2");var subQ5=sQuery(id+"F3.wireOp",EDGE,"E20.7.3");var subQ7=sQuery(id+"F3.wireOp",EDGE,"E20.7.1");var subQ8=sQuery(id+"F3.wireOp",EDGE,"E20.7.0");var subQ9=sQuery(id+"F41.wireOp",EDGE,"E38");var subQ10=makeQuery(id+"F42.opRevolve","SWEPT_FACE",FACE,{"disambiguationData":[OSD([subQ9])]});var subQ11=makeQuery(id+"F42.opRevolve","SWEPT_EDGE",EDGE,{"disambiguationData":[OSD([subQ0,subQ9])]});var subQ12=sQuery(id+"F22.wireOp",EDGE,"E28.14.3");var subQ13=sQuery(id+"F22.wireOp",EDGE,"E28.14.2");var subQ14=sQuery(id+"F3.wireOp",EDGE,"E20.6.3");var subQ15=sQuery(id+"F3.wireOp",EDGE,"E20.6.1");var subQ16=sQuery(id+"F3.wireOp",EDGE,"E20.6.0");var subQ18=sQuery(id+"F22.wireOp",EDGE,"E28.13.3");var subQ19=sQuery(id+"F22.wireOp",EDGE,"E28.13.2");var subQ20=sQuery(id+"F3.wireOp",EDGE,"E20.5.3");var subQ22=sQuery(id+"F3.wireOp",EDGE,"E20.5.1");var subQ23=sQuery(id+"F3.wireOp",EDGE,"E20.5.0");var subQ24=sQuery(id+"F22.wireOp",EDGE,"E28.12.3");var subQ25=sQuery(id+"F22.wireOp",EDGE,"E28.12.2");var subQ26=sQuery(id+"F3.wireOp",EDGE,"E20.4.3");var subQ28=sQuery(id+"F3.wireOp",EDGE,"E20.4.1");var subQ29=sQuery(id+"F3.wireOp",EDGE,"E20.4.0");var subQ30=sQuery(id+"F22.wireOp",EDGE,"E28.11.3");var subQ31=sQuery(id+"F22.wireOp",EDGE,"E28.11.2");var subQ32=sQuery(id+"F3.wireOp",EDGE,"E20.3.3");var subQ34=sQuery(id+"F3.wireOp",EDGE,"E20.3.1");var subQ35=sQuery(id+"F3.wireOp",EDGE,"E20.3.0");var subQ36=sQuery(id+"F22.wireOp",EDGE,"E28.10.3");var subQ37=sQuery(id+"F22.wireOp",EDGE,"E28.10.2");var subQ38=sQuery(id+"F3.wireOp",EDGE,"E20.2.3");var subQ40=sQuery(id+"F3.wireOp",EDGE,"E20.2.1");var subQ41=sQuery(id+"F3.wireOp",EDGE,"E20.2.0");var subQ42=sQuery(id+"F22.wireOp",EDGE,"E28.9.3");var subQ43=sQuery(id+"F22.wireOp",EDGE,"E28.9.2");var subQ44=sQuery(id+"F3.wireOp",EDGE,"E20.1.3");var subQ46=sQuery(id+"F3.wireOp",EDGE,"E20.1.1");var subQ47=sQuery(id+"F3.wireOp",EDGE,"E20.1.0");var subQ48=sQuery(id+"F22.wireOp",EDGE,"E28.8.3");var subQ49=sQuery(id+"F22.wireOp",EDGE,"E28.8.2");var subQ51=sQuery(id+"F3.wireOp",EDGE,"E18.top");var subQ52=sQuery(id+"F3.wireOp",EDGE,"E18.bottom");var subQ53=sQuery(id+"F3.wireOp",EDGE,"E18.left");var subQ54=sQuery(id+"F22.wireOp",EDGE,"E28.7.3");var subQ55=sQuery(id+"F22.wireOp",EDGE,"E28.7.2");var subQ56=sQuery(id+"F3.wireOp",EDGE,"E20.15.3");var subQ57=sQuery(id+"F3.wireOp",EDGE,"E20.15.1");var subQ58=sQuery(id+"F3.wireOp",EDGE,"E20.15.0");var subQ60=sQuery(id+"F22.wireOp",EDGE,"E28.6.3");var subQ61=sQuery(id+"F22.wireOp",EDGE,"E28.6.2");var subQ62=sQuery(id+"F3.wireOp",EDGE,"E20.14.3");var subQ64=sQuery(id+"F3.wireOp",EDGE,"E20.14.1");var subQ65=sQuery(id+"F3.wireOp",EDGE,"E20.14.0");var subQ66=sQuery(id+"F22.wireOp",EDGE,"E28.5.3");var subQ67=sQuery(id+"F22.wireOp",EDGE,"E28.5.2");var subQ68=sQuery(id+"F3.wireOp",EDGE,"E20.13.3");var subQ70=sQuery(id+"F3.wireOp",EDGE,"E20.13.1");var subQ71=sQuery(id+"F3.wireOp",EDGE,"E20.13.0");var subQ72=sQuery(id+"F22.wireOp",EDGE,"E28.4.3");var subQ73=sQuery(id+"F22.wireOp",EDGE,"E28.4.2");var subQ74=sQuery(id+"F3.wireOp",EDGE,"E20.12.3");var subQ76=sQuery(id+"F3.wireOp",EDGE,"E20.12.1");var subQ78=sQuery(id+"F3.wireOp",EDGE,"E20.12.0");var subQ79=makeQuery(id+"F27.opLoft","SWEPT_FACE",FACE,{"disambiguationData":[OSD([subQ78,subQ76,subQ74,sQuery(id+"F22.wireOp",EDGE,"E28.4.1"),subQ73,subQ72])]});var subQ80=sQuery(id+"F22.wireOp",EDGE,"E28.3.3");var subQ81=sQuery(id+"F22.wireOp",EDGE,"E28.3.2");var subQ82=sQuery(id+"F3.wireOp",EDGE,"E20.11.3");var subQ84=sQuery(id+"F3.wireOp",EDGE,"E20.11.1");var subQ85=sQuery(id+"F3.wireOp",EDGE,"E20.11.0");var subQ86=makeQuery(id+"F26.opLoft","SWEPT_FACE",FACE,{"disambiguationData":[OSD([subQ85,subQ84,subQ82,sQuery(id+"F22.wireOp",EDGE,"E28.3.1"),subQ81,subQ80])]});var subQ87=sQuery(id+"F22.wireOp",EDGE,"E28.2.3");var subQ88=sQuery(id+"F22.wireOp",EDGE,"E28.2.2");var subQ89=sQuery(id+"F3.wireOp",EDGE,"E20.10.3");var subQ90=sQuery(id+"F3.wireOp",EDGE,"E20.10.1");var subQ91=sQuery(id+"F3.wireOp",EDGE,"E20.10.0");var subQ92=makeQuery(id+"F25.opLoft","SWEPT_FACE",FACE,{"disambiguationData":[OSD([subQ91,subQ90,subQ89,sQuery(id+"F22.wireOp",EDGE,"E28.2.1"),subQ88,subQ87])]});var subQ94=sQuery(id+"F22.wireOp",EDGE,"E28.1.3");var subQ95=sQuery(id+"F22.wireOp",EDGE,"E28.1.2");var subQ96=sQuery(id+"F3.wireOp",EDGE,"E20.9.3");var subQ97=sQuery(id+"F3.wireOp",EDGE,"E20.9.1");var subQ98=sQuery(id+"F3.wireOp",EDGE,"E20.9.0");var subQ99=makeQuery(id+"F24.opLoft","SWEPT_FACE",FACE,{"disambiguationData":[OSD([subQ98,subQ97,subQ96,sQuery(id+"F22.wireOp",EDGE,"E28.1.1"),subQ95,subQ94])]});var subQ100=sQuery(id+"F22.wireOp",EDGE,"E27.top");var subQ101=sQuery(id+"F22.wireOp",EDGE,"E27.bottom");var subQ102=sQuery(id+"F3.wireOp",EDGE,"E20.8.3");var subQ104=sQuery(id+"F3.wireOp",EDGE,"E20.8.1");var subQ108=makeQuery(id+"F42.boolean.opBoolean","COPY",FACE,{"disambiguationData":[TD([subQ79])],"derivedFrom":subQ10});var subQ142=makeQuery(id+"F5.opLoft","CAP_FACE",FACE,{"disambiguationData":[OSD([makeQuery(id+"F3.imprint","IMPRINT",FACE,{"disambiguationData":[TD([[makeQuery(id+"F3.imprint","IMPRINT",EDGE,{"derivedFrom":subQ52}),1.0]])]})])],"isStart":true});var subQ180=makeQuery(id+"F27.boolean.opBoolean","INTERSECT",EDGE,{"derivedFrom":[makeQuery(id+"F26.boolean.opBoolean","SPLIT",FACE,{"disambiguationData":[TD([subQ142])],"derivedFrom":makeQuery(id+"F25.boolean.opBoolean","SPLIT",FACE,{"disambiguationData":[TD([subQ142])],"derivedFrom":makeQuery(id+"F24.boolean.opBoolean","SPLIT",FACE,{"disambiguationData":[TD([subQ142])],"derivedFrom":makeQuery(id+"F1.opRevolve","SWEPT_FACE",FACE,{"disambiguationData":[OSD([sQuery(id+"F0.wireOp",EDGE,"E4")])]})})})}),subQ79]});Q29=makeQuery(id+"F48.opFillet","BLEND_EDGE",EDGE,{"blendedFrom":[makeQuery(id+"F47.opFillet","TWEAK_EDGE",EDGE,{"derivedFrom":[makeQuery(id+"F45.opFillet","BLEND_VERTEX",VERTEX,{"blendedFrom":[subQ180,subQ79,subQ108],"blendedInto":[subQ79,subQ108]}),makeQuery(id+"F45.opFillet","BLEND_VERTEX",VERTEX,{"blendedFrom":[subQ180,makeQuery(id+"F42.boolean.opBoolean","MERGE",FACE,{"derivedFrom":[subQ2,subQ1]}),subQ108],"blendedInto":[makeQuery(id+"F42.boolean.opBoolean","MERGE",FACE,{"derivedFrom":[subQ2,subQ1]}),subQ108]})]}),makeQuery(id+"F47.opFillet","BLEND_FACE",FACE,{"disambiguationData":[OSD([subQ0,subQ9]),TDD([makeQuery(id+"F42.boolean.opBoolean","COPY",EDGE,{"disambiguationData":[TD([makeQuery(id+"F23.opLoft","SWEPT_FACE",FACE,{"disambiguationData":[OSD([sQuery(id+"F3.wireOp",EDGE,"E20.8.0"),subQ104,subQ102,subQ101,subQ100,sQuery(id+"F22.wireOp",EDGE,"E27.right")])]})])],"derivedFrom":subQ11})])]}),makeQuery(id+"F47.opFillet","BLEND_FACE",FACE,{"disambiguationData":[OSD([subQ0,subQ9]),TDD([makeQuery(id+"F42.boolean.opBoolean","COPY",EDGE,{"disambiguationData":[TD([subQ99])],"derivedFrom":subQ11})])]}),makeQuery(id+"F47.opFillet","BLEND_FACE",FACE,{"disambiguationData":[OSD([subQ0,subQ9]),TDD([makeQuery(id+"F42.boolean.opBoolean","COPY",EDGE,{"disambiguationData":[TD([subQ92])],"derivedFrom":subQ11})])]}),makeQuery(id+"F47.opFillet","BLEND_FACE",FACE,{"disambiguationData":[OSD([subQ0,subQ9]),TDD([makeQuery(id+"F42.boolean.opBoolean","COPY",EDGE,{"disambiguationData":[TD([subQ86])],"derivedFrom":subQ11})])]}),makeQuery(id+"F47.opFillet","BLEND_FACE",FACE,{"disambiguationData":[OSD([subQ0,subQ9]),TDD([makeQuery(id+"F42.boolean.opBoolean","COPY",EDGE,{"disambiguationData":[TD([subQ79])],"derivedFrom":subQ11})])]}),makeQuery(id+"F47.opFillet","BLEND_FACE",FACE,{"disambiguationData":[OSD([subQ0,subQ9]),TDD([makeQuery(id+"F42.boolean.opBoolean","COPY",EDGE,{"disambiguationData":[TD([makeQuery(id+"F28.opLoft","SWEPT_FACE",FACE,{"disambiguationData":[OSD([subQ71,subQ70,subQ68,sQuery(id+"F22.wireOp",EDGE,"E28.5.1"),subQ67,subQ66])]})])],"derivedFrom":subQ11})])]}),makeQuery(id+"F47.opFillet","BLEND_FACE",FACE,{"disambiguationData":[OSD([subQ0,subQ9]),TDD([makeQuery(id+"F42.boolean.opBoolean","COPY",EDGE,{"disambiguationData":[TD([makeQuery(id+"F29.opLoft","SWEPT_FACE",FACE,{"disambiguationData":[OSD([subQ65,subQ64,subQ62,sQuery(id+"F22.wireOp",EDGE,"E28.6.1"),subQ61,subQ60])]})])],"derivedFrom":subQ11})])]}),makeQuery(id+"F47.opFillet","BLEND_FACE",FACE,{"disambiguationData":[OSD([subQ0,subQ9]),TDD([makeQuery(id+"F42.boolean.opBoolean","COPY",EDGE,{"disambiguationData":[TD([makeQuery(id+"F30.opLoft","SWEPT_FACE",FACE,{"disambiguationData":[OSD([subQ58,subQ57,subQ56,sQuery(id+"F22.wireOp",EDGE,"E28.7.1"),subQ55,subQ54])]})])],"derivedFrom":subQ11})])]}),makeQuery(id+"F47.opFillet","BLEND_FACE",FACE,{"disambiguationData":[OSD([subQ0,subQ9]),TDD([makeQuery(id+"F42.boolean.opBoolean","COPY",EDGE,{"disambiguationData":[TD([makeQuery(id+"F31.opLoft","SWEPT_FACE",FACE,{"disambiguationData":[OSD([subQ52,subQ51,subQ53,sQuery(id+"F22.wireOp",EDGE,"E28.8.1"),subQ49,subQ48])]})])],"derivedFrom":subQ11})])]}),makeQuery(id+"F47.opFillet","BLEND_FACE",FACE,{"disambiguationData":[OSD([subQ0,subQ9]),TDD([makeQuery(id+"F42.boolean.opBoolean","COPY",EDGE,{"disambiguationData":[TD([makeQuery(id+"F32.opLoft","SWEPT_FACE",FACE,{"disambiguationData":[OSD([subQ47,subQ46,subQ44,sQuery(id+"F22.wireOp",EDGE,"E28.9.1"),subQ43,subQ42])]})])],"derivedFrom":subQ11})])]}),makeQuery(id+"F47.opFillet","BLEND_FACE",FACE,{"disambiguationData":[OSD([subQ0,subQ9]),TDD([makeQuery(id+"F42.boolean.opBoolean","COPY",EDGE,{"disambiguationData":[TD([makeQuery(id+"F33.opLoft","SWEPT_FACE",FACE,{"disambiguationData":[OSD([subQ41,subQ40,subQ38,sQuery(id+"F22.wireOp",EDGE,"E28.10.1"),subQ37,subQ36])]})])],"derivedFrom":subQ11})])]}),makeQuery(id+"F47.opFillet","BLEND_FACE",FACE,{"disambiguationData":[OSD([subQ0,subQ9]),TDD([makeQuery(id+"F42.boolean.opBoolean","COPY",EDGE,{"disambiguationData":[TD([makeQuery(id+"F34.opLoft","SWEPT_FACE",FACE,{"disambiguationData":[OSD([subQ35,subQ34,subQ32,sQuery(id+"F22.wireOp",EDGE,"E28.11.1"),subQ31,subQ30])]})])],"derivedFrom":subQ11})])]}),makeQuery(id+"F47.opFillet","BLEND_FACE",FACE,{"disambiguationData":[OSD([subQ0,subQ9]),TDD([makeQuery(id+"F42.boolean.opBoolean","COPY",EDGE,{"disambiguationData":[TD([makeQuery(id+"F35.opLoft","SWEPT_FACE",FACE,{"disambiguationData":[OSD([subQ29,subQ28,subQ26,sQuery(id+"F22.wireOp",EDGE,"E28.12.1"),subQ25,subQ24])]})])],"derivedFrom":subQ11})])]}),makeQuery(id+"F47.opFillet","BLEND_FACE",FACE,{"disambiguationData":[OSD([subQ0,subQ9]),TDD([makeQuery(id+"F42.boolean.opBoolean","COPY",EDGE,{"disambiguationData":[TD([makeQuery(id+"F36.opLoft","SWEPT_FACE",FACE,{"disambiguationData":[OSD([subQ23,subQ22,subQ20,sQuery(id+"F22.wireOp",EDGE,"E28.13.1"),subQ19,subQ18])]})])],"derivedFrom":subQ11})])]}),makeQuery(id+"F47.opFillet","BLEND_FACE",FACE,{"disambiguationData":[OSD([subQ0,subQ9]),TDD([makeQuery(id+"F42.boolean.opBoolean","COPY",EDGE,{"disambiguationData":[TD([makeQuery(id+"F37.opLoft","SWEPT_FACE",FACE,{"disambiguationData":[OSD([subQ16,subQ15,subQ14,sQuery(id+"F22.wireOp",EDGE,"E28.14.1"),subQ13,subQ12])]})])],"derivedFrom":subQ11})])]}),makeQuery(id+"F47.opFillet","BLEND_FACE",FACE,{"disambiguationData":[OSD([subQ0,subQ9]),TDD([makeQuery(id+"F42.boolean.opBoolean","COPY",EDGE,{"disambiguationData":[TD([makeQuery(id+"F38.opLoft","SWEPT_FACE",FACE,{"disambiguationData":[OSD([subQ8,subQ7,subQ5,sQuery(id+"F22.wireOp",EDGE,"E28.15.1"),subQ4,subQ3])]})])],"derivedFrom":subQ11})])]})],"blendedInto":[makeQuery(id+"F47.opFillet","BLEND_FACE",FACE,{"disambiguationData":[OSD([subQ0,subQ9]),TDD([makeQuery(id+"F42.boolean.opBoolean","COPY",EDGE,{"disambiguationData":[TD([makeQuery(id+"F23.opLoft","SWEPT_FACE",FACE,{"disambiguationData":[OSD([sQuery(id+"F3.wireOp",EDGE,"E20.8.0"),subQ104,subQ102,subQ101,subQ100,sQuery(id+"F22.wireOp",EDGE,"E27.right")])]})])],"derivedFrom":subQ11})])]}),makeQuery(id+"F47.opFillet","BLEND_FACE",FACE,{"disambiguationData":[OSD([subQ0,subQ9]),TDD([makeQuery(id+"F42.boolean.opBoolean","COPY",EDGE,{"disambiguationData":[TD([subQ99])],"derivedFrom":subQ11})])]}),makeQuery(id+"F47.opFillet","BLEND_FACE",FACE,{"disambiguationData":[OSD([subQ0,subQ9]),TDD([makeQuery(id+"F42.boolean.opBoolean","COPY",EDGE,{"disambiguationData":[TD([subQ92])],"derivedFrom":subQ11})])]}),makeQuery(id+"F47.opFillet","BLEND_FACE",FACE,{"disambiguationData":[OSD([subQ0,subQ9]),TDD([makeQuery(id+"F42.boolean.opBoolean","COPY",EDGE,{"disambiguationData":[TD([subQ86])],"derivedFrom":subQ11})])]}),makeQuery(id+"F47.opFillet","BLEND_FACE",FACE,{"disambiguationData":[OSD([subQ0,subQ9]),TDD([makeQuery(id+"F42.boolean.opBoolean","COPY",EDGE,{"disambiguationData":[TD([subQ79])],"derivedFrom":subQ11})])]}),makeQuery(id+"F47.opFillet","BLEND_FACE",FACE,{"disambiguationData":[OSD([subQ0,subQ9]),TDD([makeQuery(id+"F42.boolean.opBoolean","COPY",EDGE,{"disambiguationData":[TD([makeQuery(id+"F28.opLoft","SWEPT_FACE",FACE,{"disambiguationData":[OSD([subQ71,subQ70,subQ68,sQuery(id+"F22.wireOp",EDGE,"E28.5.1"),subQ67,subQ66])]})])],"derivedFrom":subQ11})])]}),makeQuery(id+"F47.opFillet","BLEND_FACE",FACE,{"disambiguationData":[OSD([subQ0,subQ9]),TDD([makeQuery(id+"F42.boolean.opBoolean","COPY",EDGE,{"disambiguationData":[TD([makeQuery(id+"F29.opLoft","SWEPT_FACE",FACE,{"disambiguationData":[OSD([subQ65,subQ64,subQ62,sQuery(id+"F22.wireOp",EDGE,"E28.6.1"),subQ61,subQ60])]})])],"derivedFrom":subQ11})])]}),makeQuery(id+"F47.opFillet","BLEND_FACE",FACE,{"disambiguationData":[OSD([subQ0,subQ9]),TDD([makeQuery(id+"F42.boolean.opBoolean","COPY",EDGE,{"disambiguationData":[TD([makeQuery(id+"F30.opLoft","SWEPT_FACE",FACE,{"disambiguationData":[OSD([subQ58,subQ57,subQ56,sQuery(id+"F22.wireOp",EDGE,"E28.7.1"),subQ55,subQ54])]})])],"derivedFrom":subQ11})])]}),makeQuery(id+"F47.opFillet","BLEND_FACE",FACE,{"disambiguationData":[OSD([subQ0,subQ9]),TDD([makeQuery(id+"F42.boolean.opBoolean","COPY",EDGE,{"disambiguationData":[TD([makeQuery(id+"F31.opLoft","SWEPT_FACE",FACE,{"disambiguationData":[OSD([subQ52,subQ51,subQ53,sQuery(id+"F22.wireOp",EDGE,"E28.8.1"),subQ49,subQ48])]})])],"derivedFrom":subQ11})])]}),makeQuery(id+"F47.opFillet","BLEND_FACE",FACE,{"disambiguationData":[OSD([subQ0,subQ9]),TDD([makeQuery(id+"F42.boolean.opBoolean","COPY",EDGE,{"disambiguationData":[TD([makeQuery(id+"F32.opLoft","SWEPT_FACE",FACE,{"disambiguationData":[OSD([subQ47,subQ46,subQ44,sQuery(id+"F22.wireOp",EDGE,"E28.9.1"),subQ43,subQ42])]})])],"derivedFrom":subQ11})])]}),makeQuery(id+"F47.opFillet","BLEND_FACE",FACE,{"disambiguationData":[OSD([subQ0,subQ9]),TDD([makeQuery(id+"F42.boolean.opBoolean","COPY",EDGE,{"disambiguationData":[TD([makeQuery(id+"F33.opLoft","SWEPT_FACE",FACE,{"disambiguationData":[OSD([subQ41,subQ40,subQ38,sQuery(id+"F22.wireOp",EDGE,"E28.10.1"),subQ37,subQ36])]})])],"derivedFrom":subQ11})])]}),makeQuery(id+"F47.opFillet","BLEND_FACE",FACE,{"disambiguationData":[OSD([subQ0,subQ9]),TDD([makeQuery(id+"F42.boolean.opBoolean","COPY",EDGE,{"disambiguationData":[TD([makeQuery(id+"F34.opLoft","SWEPT_FACE",FACE,{"disambiguationData":[OSD([subQ35,subQ34,subQ32,sQuery(id+"F22.wireOp",EDGE,"E28.11.1"),subQ31,subQ30])]})])],"derivedFrom":subQ11})])]}),makeQuery(id+"F47.opFillet","BLEND_FACE",FACE,{"disambiguationData":[OSD([subQ0,subQ9]),TDD([makeQuery(id+"F42.boolean.opBoolean","COPY",EDGE,{"disambiguationData":[TD([makeQuery(id+"F35.opLoft","SWEPT_FACE",FACE,{"disambiguationData":[OSD([subQ29,subQ28,subQ26,sQuery(id+"F22.wireOp",EDGE,"E28.12.1"),subQ25,subQ24])]})])],"derivedFrom":subQ11})])]}),makeQuery(id+"F47.opFillet","BLEND_FACE",FACE,{"disambiguationData":[OSD([subQ0,subQ9]),TDD([makeQuery(id+"F42.boolean.opBoolean","COPY",EDGE,{"disambiguationData":[TD([makeQuery(id+"F36.opLoft","SWEPT_FACE",FACE,{"disambiguationData":[OSD([subQ23,subQ22,subQ20,sQuery(id+"F22.wireOp",EDGE,"E28.13.1"),subQ19,subQ18])]})])],"derivedFrom":subQ11})])]}),makeQuery(id+"F47.opFillet","BLEND_FACE",FACE,{"disambiguationData":[OSD([subQ0,subQ9]),TDD([makeQuery(id+"F42.boolean.opBoolean","COPY",EDGE,{"disambiguationData":[TD([makeQuery(id+"F37.opLoft","SWEPT_FACE",FACE,{"disambiguationData":[OSD([subQ16,subQ15,subQ14,sQuery(id+"F22.wireOp",EDGE,"E28.14.1"),subQ13,subQ12])]})])],"derivedFrom":subQ11})])]}),makeQuery(id+"F47.opFillet","BLEND_FACE",FACE,{"disambiguationData":[OSD([subQ0,subQ9]),TDD([makeQuery(id+"F42.boolean.opBoolean","COPY",EDGE,{"disambiguationData":[TD([makeQuery(id+"F38.opLoft","SWEPT_FACE",FACE,{"disambiguationData":[OSD([subQ8,subQ7,subQ5,sQuery(id+"F22.wireOp",EDGE,"E28.15.1"),subQ4,subQ3])]})])],"derivedFrom":subQ11})])]})]});}
            var Q30;
            {var subQ0=sQuery(id+"F22.wireOp",EDGE,"E28.4.3");var subQ1=sQuery(id+"F22.wireOp",EDGE,"E28.4.2");var subQ2=sQuery(id+"F22.wireOp",EDGE,"E28.4.0");var subQ3=sQuery(id+"F3.wireOp",EDGE,"E20.12.3");var subQ4=sQuery(id+"F3.wireOp",EDGE,"E20.12.1");var subQ5=makeQuery(id+"F27.opLoft","SWEPT_FACE",FACE,{"disambiguationData":[OSD([subQ4,sQuery(id+"F3.wireOp",EDGE,"E20.12.2"),subQ3,subQ2,subQ1,subQ0])]});var subQ6=sQuery(id+"F22.wireOp",EDGE,"E28.4.1");var subQ7=sQuery(id+"F41.wireOp",EDGE,"E34");var subQ8=sQuery(id+"F41.wireOp",EDGE,"E32");Q30=makeQuery(id+"F44.opFillet","BLEND_EDGE",EDGE,{"blendedFrom":[makeQuery(id+"F40.boolean.opBoolean","INTERSECT",EDGE,{"derivedFrom":[subQ5,makeQuery(id+"F40.opExtrude","CAP_FACE",FACE,{"disambiguationData":[OSD([sQuery(id+"F39.wireOp",EDGE,"E29"),sQuery(id+"F39.wireOp",EDGE,"E30")])],"isStart":true})]}),makeQuery(id+"F42.boolean.opBoolean","COPY",FACE,{"disambiguationData":[TD([makeQuery(id+"F27.opLoft","SWEPT_FACE",FACE,{"disambiguationData":[OSD([sQuery(id+"F3.wireOp",EDGE,"E20.12.0"),subQ4,subQ3,subQ6,subQ1,subQ0])]})])],"derivedFrom":makeQuery(id+"F42.opRevolve","SWEPT_FACE",FACE,{"disambiguationData":[OSD([subQ8]),TDD([makeQuery(id+"F41.imprint","IMPRINT",EDGE,{"disambiguationData":[TD([[makeQuery(id+"F41.imprint","INTERSECT",VERTEX,{"disambiguationData":[OD(0.0)],"derivedFrom":[subQ8,subQ7]}),-1.0]])],"derivedFrom":subQ8})])]})})],"blendedInto":[makeQuery(id+"F42.boolean.opBoolean","COPY",FACE,{"disambiguationData":[TD([makeQuery(id+"F27.opLoft","SWEPT_FACE",FACE,{"disambiguationData":[OSD([sQuery(id+"F3.wireOp",EDGE,"E20.12.0"),subQ4,subQ3,subQ6,subQ1,subQ0])]})])],"derivedFrom":makeQuery(id+"F42.opRevolve","SWEPT_FACE",FACE,{"disambiguationData":[OSD([subQ8]),TDD([makeQuery(id+"F41.imprint","IMPRINT",EDGE,{"disambiguationData":[TD([[makeQuery(id+"F41.imprint","INTERSECT",VERTEX,{"disambiguationData":[OD(0.0)],"derivedFrom":[subQ8,subQ7]}),-1.0]])],"derivedFrom":subQ8})])]})})]});}
            var Q31;
            {var subQ0=sQuery(id+"F41.wireOp",EDGE,"E34");var subQ1=sQuery(id+"F41.wireOp",EDGE,"E32");Q31=makeQuery(id+"F42.boolean.opBoolean","INTERSECT",EDGE,{"derivedFrom":[makeQuery(id+"F26.opLoft","SWEPT_FACE",FACE,{"disambiguationData":[OSD([sQuery(id+"F3.wireOp",EDGE,"E20.11.0"),sQuery(id+"F3.wireOp",EDGE,"E20.11.1"),sQuery(id+"F3.wireOp",EDGE,"E20.11.3"),sQuery(id+"F22.wireOp",EDGE,"E28.3.1"),sQuery(id+"F22.wireOp",EDGE,"E28.3.2"),sQuery(id+"F22.wireOp",EDGE,"E28.3.3")])]}),makeQuery(id+"F42.opRevolve","SWEPT_FACE",FACE,{"disambiguationData":[OSD([subQ1]),TDD([makeQuery(id+"F41.imprint","IMPRINT",EDGE,{"disambiguationData":[TD([[makeQuery(id+"F41.imprint","INTERSECT",VERTEX,{"disambiguationData":[OD(0.0)],"derivedFrom":[subQ1,subQ0]}),-1.0]])],"derivedFrom":subQ1})])]})]});}
            var Q32;
            {var subQ0=sQuery(id+"F41.wireOp",EDGE,"E37");var subQ1=makeQuery(id+"F42.opRevolve","SWEPT_FACE",FACE,{"disambiguationData":[OSD([subQ0])]});var subQ2=makeQuery(id+"F40.opExtrude","CAP_FACE",FACE,{"disambiguationData":[OSD([sQuery(id+"F39.wireOp",EDGE,"E29"),sQuery(id+"F39.wireOp",EDGE,"E30")])],"isStart":true});var subQ3=sQuery(id+"F22.wireOp",EDGE,"E28.15.3");var subQ4=sQuery(id+"F22.wireOp",EDGE,"E28.15.2");var subQ5=sQuery(id+"F3.wireOp",EDGE,"E20.7.3");var subQ7=sQuery(id+"F3.wireOp",EDGE,"E20.7.1");var subQ8=sQuery(id+"F3.wireOp",EDGE,"E20.7.0");var subQ9=sQuery(id+"F41.wireOp",EDGE,"E38");var subQ10=makeQuery(id+"F42.opRevolve","SWEPT_FACE",FACE,{"disambiguationData":[OSD([subQ9])]});var subQ11=makeQuery(id+"F42.opRevolve","SWEPT_EDGE",EDGE,{"disambiguationData":[OSD([subQ0,subQ9])]});var subQ12=sQuery(id+"F22.wireOp",EDGE,"E28.14.3");var subQ13=sQuery(id+"F22.wireOp",EDGE,"E28.14.2");var subQ14=sQuery(id+"F3.wireOp",EDGE,"E20.6.3");var subQ15=sQuery(id+"F3.wireOp",EDGE,"E20.6.1");var subQ16=sQuery(id+"F3.wireOp",EDGE,"E20.6.0");var subQ18=sQuery(id+"F22.wireOp",EDGE,"E28.13.3");var subQ19=sQuery(id+"F22.wireOp",EDGE,"E28.13.2");var subQ20=sQuery(id+"F3.wireOp",EDGE,"E20.5.3");var subQ22=sQuery(id+"F3.wireOp",EDGE,"E20.5.1");var subQ23=sQuery(id+"F3.wireOp",EDGE,"E20.5.0");var subQ24=sQuery(id+"F22.wireOp",EDGE,"E28.12.3");var subQ25=sQuery(id+"F22.wireOp",EDGE,"E28.12.2");var subQ26=sQuery(id+"F3.wireOp",EDGE,"E20.4.3");var subQ28=sQuery(id+"F3.wireOp",EDGE,"E20.4.1");var subQ29=sQuery(id+"F3.wireOp",EDGE,"E20.4.0");var subQ30=sQuery(id+"F22.wireOp",EDGE,"E28.11.3");var subQ31=sQuery(id+"F22.wireOp",EDGE,"E28.11.2");var subQ32=sQuery(id+"F3.wireOp",EDGE,"E20.3.3");var subQ34=sQuery(id+"F3.wireOp",EDGE,"E20.3.1");var subQ35=sQuery(id+"F3.wireOp",EDGE,"E20.3.0");var subQ36=sQuery(id+"F22.wireOp",EDGE,"E28.10.3");var subQ37=sQuery(id+"F22.wireOp",EDGE,"E28.10.2");var subQ38=sQuery(id+"F3.wireOp",EDGE,"E20.2.3");var subQ40=sQuery(id+"F3.wireOp",EDGE,"E20.2.1");var subQ41=sQuery(id+"F3.wireOp",EDGE,"E20.2.0");var subQ42=sQuery(id+"F22.wireOp",EDGE,"E28.9.3");var subQ43=sQuery(id+"F22.wireOp",EDGE,"E28.9.2");var subQ44=sQuery(id+"F3.wireOp",EDGE,"E20.1.3");var subQ46=sQuery(id+"F3.wireOp",EDGE,"E20.1.1");var subQ47=sQuery(id+"F3.wireOp",EDGE,"E20.1.0");var subQ48=sQuery(id+"F22.wireOp",EDGE,"E28.8.3");var subQ49=sQuery(id+"F22.wireOp",EDGE,"E28.8.2");var subQ51=sQuery(id+"F3.wireOp",EDGE,"E18.top");var subQ52=sQuery(id+"F3.wireOp",EDGE,"E18.bottom");var subQ53=sQuery(id+"F3.wireOp",EDGE,"E18.left");var subQ54=sQuery(id+"F22.wireOp",EDGE,"E28.7.3");var subQ55=sQuery(id+"F22.wireOp",EDGE,"E28.7.2");var subQ56=sQuery(id+"F3.wireOp",EDGE,"E20.15.3");var subQ57=sQuery(id+"F3.wireOp",EDGE,"E20.15.1");var subQ58=sQuery(id+"F3.wireOp",EDGE,"E20.15.0");var subQ60=sQuery(id+"F22.wireOp",EDGE,"E28.6.3");var subQ61=sQuery(id+"F22.wireOp",EDGE,"E28.6.2");var subQ62=sQuery(id+"F3.wireOp",EDGE,"E20.14.3");var subQ64=sQuery(id+"F3.wireOp",EDGE,"E20.14.1");var subQ65=sQuery(id+"F3.wireOp",EDGE,"E20.14.0");var subQ66=sQuery(id+"F22.wireOp",EDGE,"E28.5.3");var subQ67=sQuery(id+"F22.wireOp",EDGE,"E28.5.2");var subQ68=sQuery(id+"F3.wireOp",EDGE,"E20.13.3");var subQ70=sQuery(id+"F3.wireOp",EDGE,"E20.13.1");var subQ71=sQuery(id+"F3.wireOp",EDGE,"E20.13.0");var subQ72=sQuery(id+"F22.wireOp",EDGE,"E28.4.3");var subQ73=sQuery(id+"F22.wireOp",EDGE,"E28.4.2");var subQ74=sQuery(id+"F3.wireOp",EDGE,"E20.12.3");var subQ76=sQuery(id+"F3.wireOp",EDGE,"E20.12.1");var subQ77=sQuery(id+"F3.wireOp",EDGE,"E20.12.0");var subQ78=sQuery(id+"F22.wireOp",EDGE,"E28.3.3");var subQ79=sQuery(id+"F22.wireOp",EDGE,"E28.3.2");var subQ80=sQuery(id+"F3.wireOp",EDGE,"E20.11.3");var subQ82=sQuery(id+"F3.wireOp",EDGE,"E20.11.1");var subQ84=sQuery(id+"F3.wireOp",EDGE,"E20.11.0");var subQ85=makeQuery(id+"F26.opLoft","SWEPT_FACE",FACE,{"disambiguationData":[OSD([subQ84,subQ82,subQ80,sQuery(id+"F22.wireOp",EDGE,"E28.3.1"),subQ79,subQ78])]});var subQ86=sQuery(id+"F22.wireOp",EDGE,"E28.2.3");var subQ87=sQuery(id+"F22.wireOp",EDGE,"E28.2.2");var subQ88=sQuery(id+"F3.wireOp",EDGE,"E20.10.3");var subQ89=sQuery(id+"F3.wireOp",EDGE,"E20.10.1");var subQ90=sQuery(id+"F3.wireOp",EDGE,"E20.10.0");var subQ91=makeQuery(id+"F25.opLoft","SWEPT_FACE",FACE,{"disambiguationData":[OSD([subQ90,subQ89,subQ88,sQuery(id+"F22.wireOp",EDGE,"E28.2.1"),subQ87,subQ86])]});var subQ93=sQuery(id+"F22.wireOp",EDGE,"E28.1.3");var subQ94=sQuery(id+"F22.wireOp",EDGE,"E28.1.2");var subQ95=sQuery(id+"F3.wireOp",EDGE,"E20.9.3");var subQ96=sQuery(id+"F3.wireOp",EDGE,"E20.9.1");var subQ97=sQuery(id+"F3.wireOp",EDGE,"E20.9.0");var subQ98=makeQuery(id+"F24.opLoft","SWEPT_FACE",FACE,{"disambiguationData":[OSD([subQ97,subQ96,subQ95,sQuery(id+"F22.wireOp",EDGE,"E28.1.1"),subQ94,subQ93])]});var subQ99=sQuery(id+"F22.wireOp",EDGE,"E27.top");var subQ100=sQuery(id+"F22.wireOp",EDGE,"E27.bottom");var subQ101=sQuery(id+"F3.wireOp",EDGE,"E20.8.3");var subQ103=sQuery(id+"F3.wireOp",EDGE,"E20.8.1");var subQ107=makeQuery(id+"F42.boolean.opBoolean","COPY",FACE,{"disambiguationData":[TD([subQ85])],"derivedFrom":subQ10});var subQ141=makeQuery(id+"F5.opLoft","CAP_FACE",FACE,{"disambiguationData":[OSD([makeQuery(id+"F3.imprint","IMPRINT",FACE,{"disambiguationData":[TD([[makeQuery(id+"F3.imprint","IMPRINT",EDGE,{"derivedFrom":subQ52}),1.0]])]})])],"isStart":true});var subQ179=makeQuery(id+"F26.boolean.opBoolean","INTERSECT",EDGE,{"derivedFrom":[makeQuery(id+"F25.boolean.opBoolean","SPLIT",FACE,{"disambiguationData":[TD([subQ141])],"derivedFrom":makeQuery(id+"F24.boolean.opBoolean","SPLIT",FACE,{"disambiguationData":[TD([subQ141])],"derivedFrom":makeQuery(id+"F1.opRevolve","SWEPT_FACE",FACE,{"disambiguationData":[OSD([sQuery(id+"F0.wireOp",EDGE,"E4")])]})})}),subQ85]});Q32=makeQuery(id+"F48.opFillet","BLEND_EDGE",EDGE,{"blendedFrom":[makeQuery(id+"F47.opFillet","TWEAK_EDGE",EDGE,{"derivedFrom":[makeQuery(id+"F45.opFillet","BLEND_VERTEX",VERTEX,{"blendedFrom":[subQ179,subQ85,subQ107],"blendedInto":[subQ85,subQ107]}),makeQuery(id+"F45.opFillet","BLEND_VERTEX",VERTEX,{"blendedFrom":[subQ179,makeQuery(id+"F42.boolean.opBoolean","MERGE",FACE,{"derivedFrom":[subQ2,subQ1]}),subQ107],"blendedInto":[makeQuery(id+"F42.boolean.opBoolean","MERGE",FACE,{"derivedFrom":[subQ2,subQ1]}),subQ107]})]}),makeQuery(id+"F47.opFillet","BLEND_FACE",FACE,{"disambiguationData":[OSD([subQ0,subQ9]),TDD([makeQuery(id+"F42.boolean.opBoolean","COPY",EDGE,{"disambiguationData":[TD([makeQuery(id+"F23.opLoft","SWEPT_FACE",FACE,{"disambiguationData":[OSD([sQuery(id+"F3.wireOp",EDGE,"E20.8.0"),subQ103,subQ101,subQ100,subQ99,sQuery(id+"F22.wireOp",EDGE,"E27.right")])]})])],"derivedFrom":subQ11})])]}),makeQuery(id+"F47.opFillet","BLEND_FACE",FACE,{"disambiguationData":[OSD([subQ0,subQ9]),TDD([makeQuery(id+"F42.boolean.opBoolean","COPY",EDGE,{"disambiguationData":[TD([subQ98])],"derivedFrom":subQ11})])]}),makeQuery(id+"F47.opFillet","BLEND_FACE",FACE,{"disambiguationData":[OSD([subQ0,subQ9]),TDD([makeQuery(id+"F42.boolean.opBoolean","COPY",EDGE,{"disambiguationData":[TD([subQ91])],"derivedFrom":subQ11})])]}),makeQuery(id+"F47.opFillet","BLEND_FACE",FACE,{"disambiguationData":[OSD([subQ0,subQ9]),TDD([makeQuery(id+"F42.boolean.opBoolean","COPY",EDGE,{"disambiguationData":[TD([subQ85])],"derivedFrom":subQ11})])]}),makeQuery(id+"F47.opFillet","BLEND_FACE",FACE,{"disambiguationData":[OSD([subQ0,subQ9]),TDD([makeQuery(id+"F42.boolean.opBoolean","COPY",EDGE,{"disambiguationData":[TD([makeQuery(id+"F27.opLoft","SWEPT_FACE",FACE,{"disambiguationData":[OSD([subQ77,subQ76,subQ74,sQuery(id+"F22.wireOp",EDGE,"E28.4.1"),subQ73,subQ72])]})])],"derivedFrom":subQ11})])]}),makeQuery(id+"F47.opFillet","BLEND_FACE",FACE,{"disambiguationData":[OSD([subQ0,subQ9]),TDD([makeQuery(id+"F42.boolean.opBoolean","COPY",EDGE,{"disambiguationData":[TD([makeQuery(id+"F28.opLoft","SWEPT_FACE",FACE,{"disambiguationData":[OSD([subQ71,subQ70,subQ68,sQuery(id+"F22.wireOp",EDGE,"E28.5.1"),subQ67,subQ66])]})])],"derivedFrom":subQ11})])]}),makeQuery(id+"F47.opFillet","BLEND_FACE",FACE,{"disambiguationData":[OSD([subQ0,subQ9]),TDD([makeQuery(id+"F42.boolean.opBoolean","COPY",EDGE,{"disambiguationData":[TD([makeQuery(id+"F29.opLoft","SWEPT_FACE",FACE,{"disambiguationData":[OSD([subQ65,subQ64,subQ62,sQuery(id+"F22.wireOp",EDGE,"E28.6.1"),subQ61,subQ60])]})])],"derivedFrom":subQ11})])]}),makeQuery(id+"F47.opFillet","BLEND_FACE",FACE,{"disambiguationData":[OSD([subQ0,subQ9]),TDD([makeQuery(id+"F42.boolean.opBoolean","COPY",EDGE,{"disambiguationData":[TD([makeQuery(id+"F30.opLoft","SWEPT_FACE",FACE,{"disambiguationData":[OSD([subQ58,subQ57,subQ56,sQuery(id+"F22.wireOp",EDGE,"E28.7.1"),subQ55,subQ54])]})])],"derivedFrom":subQ11})])]}),makeQuery(id+"F47.opFillet","BLEND_FACE",FACE,{"disambiguationData":[OSD([subQ0,subQ9]),TDD([makeQuery(id+"F42.boolean.opBoolean","COPY",EDGE,{"disambiguationData":[TD([makeQuery(id+"F31.opLoft","SWEPT_FACE",FACE,{"disambiguationData":[OSD([subQ52,subQ51,subQ53,sQuery(id+"F22.wireOp",EDGE,"E28.8.1"),subQ49,subQ48])]})])],"derivedFrom":subQ11})])]}),makeQuery(id+"F47.opFillet","BLEND_FACE",FACE,{"disambiguationData":[OSD([subQ0,subQ9]),TDD([makeQuery(id+"F42.boolean.opBoolean","COPY",EDGE,{"disambiguationData":[TD([makeQuery(id+"F32.opLoft","SWEPT_FACE",FACE,{"disambiguationData":[OSD([subQ47,subQ46,subQ44,sQuery(id+"F22.wireOp",EDGE,"E28.9.1"),subQ43,subQ42])]})])],"derivedFrom":subQ11})])]}),makeQuery(id+"F47.opFillet","BLEND_FACE",FACE,{"disambiguationData":[OSD([subQ0,subQ9]),TDD([makeQuery(id+"F42.boolean.opBoolean","COPY",EDGE,{"disambiguationData":[TD([makeQuery(id+"F33.opLoft","SWEPT_FACE",FACE,{"disambiguationData":[OSD([subQ41,subQ40,subQ38,sQuery(id+"F22.wireOp",EDGE,"E28.10.1"),subQ37,subQ36])]})])],"derivedFrom":subQ11})])]}),makeQuery(id+"F47.opFillet","BLEND_FACE",FACE,{"disambiguationData":[OSD([subQ0,subQ9]),TDD([makeQuery(id+"F42.boolean.opBoolean","COPY",EDGE,{"disambiguationData":[TD([makeQuery(id+"F34.opLoft","SWEPT_FACE",FACE,{"disambiguationData":[OSD([subQ35,subQ34,subQ32,sQuery(id+"F22.wireOp",EDGE,"E28.11.1"),subQ31,subQ30])]})])],"derivedFrom":subQ11})])]}),makeQuery(id+"F47.opFillet","BLEND_FACE",FACE,{"disambiguationData":[OSD([subQ0,subQ9]),TDD([makeQuery(id+"F42.boolean.opBoolean","COPY",EDGE,{"disambiguationData":[TD([makeQuery(id+"F35.opLoft","SWEPT_FACE",FACE,{"disambiguationData":[OSD([subQ29,subQ28,subQ26,sQuery(id+"F22.wireOp",EDGE,"E28.12.1"),subQ25,subQ24])]})])],"derivedFrom":subQ11})])]}),makeQuery(id+"F47.opFillet","BLEND_FACE",FACE,{"disambiguationData":[OSD([subQ0,subQ9]),TDD([makeQuery(id+"F42.boolean.opBoolean","COPY",EDGE,{"disambiguationData":[TD([makeQuery(id+"F36.opLoft","SWEPT_FACE",FACE,{"disambiguationData":[OSD([subQ23,subQ22,subQ20,sQuery(id+"F22.wireOp",EDGE,"E28.13.1"),subQ19,subQ18])]})])],"derivedFrom":subQ11})])]}),makeQuery(id+"F47.opFillet","BLEND_FACE",FACE,{"disambiguationData":[OSD([subQ0,subQ9]),TDD([makeQuery(id+"F42.boolean.opBoolean","COPY",EDGE,{"disambiguationData":[TD([makeQuery(id+"F37.opLoft","SWEPT_FACE",FACE,{"disambiguationData":[OSD([subQ16,subQ15,subQ14,sQuery(id+"F22.wireOp",EDGE,"E28.14.1"),subQ13,subQ12])]})])],"derivedFrom":subQ11})])]}),makeQuery(id+"F47.opFillet","BLEND_FACE",FACE,{"disambiguationData":[OSD([subQ0,subQ9]),TDD([makeQuery(id+"F42.boolean.opBoolean","COPY",EDGE,{"disambiguationData":[TD([makeQuery(id+"F38.opLoft","SWEPT_FACE",FACE,{"disambiguationData":[OSD([subQ8,subQ7,subQ5,sQuery(id+"F22.wireOp",EDGE,"E28.15.1"),subQ4,subQ3])]})])],"derivedFrom":subQ11})])]})],"blendedInto":[makeQuery(id+"F47.opFillet","BLEND_FACE",FACE,{"disambiguationData":[OSD([subQ0,subQ9]),TDD([makeQuery(id+"F42.boolean.opBoolean","COPY",EDGE,{"disambiguationData":[TD([makeQuery(id+"F23.opLoft","SWEPT_FACE",FACE,{"disambiguationData":[OSD([sQuery(id+"F3.wireOp",EDGE,"E20.8.0"),subQ103,subQ101,subQ100,subQ99,sQuery(id+"F22.wireOp",EDGE,"E27.right")])]})])],"derivedFrom":subQ11})])]}),makeQuery(id+"F47.opFillet","BLEND_FACE",FACE,{"disambiguationData":[OSD([subQ0,subQ9]),TDD([makeQuery(id+"F42.boolean.opBoolean","COPY",EDGE,{"disambiguationData":[TD([subQ98])],"derivedFrom":subQ11})])]}),makeQuery(id+"F47.opFillet","BLEND_FACE",FACE,{"disambiguationData":[OSD([subQ0,subQ9]),TDD([makeQuery(id+"F42.boolean.opBoolean","COPY",EDGE,{"disambiguationData":[TD([subQ91])],"derivedFrom":subQ11})])]}),makeQuery(id+"F47.opFillet","BLEND_FACE",FACE,{"disambiguationData":[OSD([subQ0,subQ9]),TDD([makeQuery(id+"F42.boolean.opBoolean","COPY",EDGE,{"disambiguationData":[TD([subQ85])],"derivedFrom":subQ11})])]}),makeQuery(id+"F47.opFillet","BLEND_FACE",FACE,{"disambiguationData":[OSD([subQ0,subQ9]),TDD([makeQuery(id+"F42.boolean.opBoolean","COPY",EDGE,{"disambiguationData":[TD([makeQuery(id+"F27.opLoft","SWEPT_FACE",FACE,{"disambiguationData":[OSD([subQ77,subQ76,subQ74,sQuery(id+"F22.wireOp",EDGE,"E28.4.1"),subQ73,subQ72])]})])],"derivedFrom":subQ11})])]}),makeQuery(id+"F47.opFillet","BLEND_FACE",FACE,{"disambiguationData":[OSD([subQ0,subQ9]),TDD([makeQuery(id+"F42.boolean.opBoolean","COPY",EDGE,{"disambiguationData":[TD([makeQuery(id+"F28.opLoft","SWEPT_FACE",FACE,{"disambiguationData":[OSD([subQ71,subQ70,subQ68,sQuery(id+"F22.wireOp",EDGE,"E28.5.1"),subQ67,subQ66])]})])],"derivedFrom":subQ11})])]}),makeQuery(id+"F47.opFillet","BLEND_FACE",FACE,{"disambiguationData":[OSD([subQ0,subQ9]),TDD([makeQuery(id+"F42.boolean.opBoolean","COPY",EDGE,{"disambiguationData":[TD([makeQuery(id+"F29.opLoft","SWEPT_FACE",FACE,{"disambiguationData":[OSD([subQ65,subQ64,subQ62,sQuery(id+"F22.wireOp",EDGE,"E28.6.1"),subQ61,subQ60])]})])],"derivedFrom":subQ11})])]}),makeQuery(id+"F47.opFillet","BLEND_FACE",FACE,{"disambiguationData":[OSD([subQ0,subQ9]),TDD([makeQuery(id+"F42.boolean.opBoolean","COPY",EDGE,{"disambiguationData":[TD([makeQuery(id+"F30.opLoft","SWEPT_FACE",FACE,{"disambiguationData":[OSD([subQ58,subQ57,subQ56,sQuery(id+"F22.wireOp",EDGE,"E28.7.1"),subQ55,subQ54])]})])],"derivedFrom":subQ11})])]}),makeQuery(id+"F47.opFillet","BLEND_FACE",FACE,{"disambiguationData":[OSD([subQ0,subQ9]),TDD([makeQuery(id+"F42.boolean.opBoolean","COPY",EDGE,{"disambiguationData":[TD([makeQuery(id+"F31.opLoft","SWEPT_FACE",FACE,{"disambiguationData":[OSD([subQ52,subQ51,subQ53,sQuery(id+"F22.wireOp",EDGE,"E28.8.1"),subQ49,subQ48])]})])],"derivedFrom":subQ11})])]}),makeQuery(id+"F47.opFillet","BLEND_FACE",FACE,{"disambiguationData":[OSD([subQ0,subQ9]),TDD([makeQuery(id+"F42.boolean.opBoolean","COPY",EDGE,{"disambiguationData":[TD([makeQuery(id+"F32.opLoft","SWEPT_FACE",FACE,{"disambiguationData":[OSD([subQ47,subQ46,subQ44,sQuery(id+"F22.wireOp",EDGE,"E28.9.1"),subQ43,subQ42])]})])],"derivedFrom":subQ11})])]}),makeQuery(id+"F47.opFillet","BLEND_FACE",FACE,{"disambiguationData":[OSD([subQ0,subQ9]),TDD([makeQuery(id+"F42.boolean.opBoolean","COPY",EDGE,{"disambiguationData":[TD([makeQuery(id+"F33.opLoft","SWEPT_FACE",FACE,{"disambiguationData":[OSD([subQ41,subQ40,subQ38,sQuery(id+"F22.wireOp",EDGE,"E28.10.1"),subQ37,subQ36])]})])],"derivedFrom":subQ11})])]}),makeQuery(id+"F47.opFillet","BLEND_FACE",FACE,{"disambiguationData":[OSD([subQ0,subQ9]),TDD([makeQuery(id+"F42.boolean.opBoolean","COPY",EDGE,{"disambiguationData":[TD([makeQuery(id+"F34.opLoft","SWEPT_FACE",FACE,{"disambiguationData":[OSD([subQ35,subQ34,subQ32,sQuery(id+"F22.wireOp",EDGE,"E28.11.1"),subQ31,subQ30])]})])],"derivedFrom":subQ11})])]}),makeQuery(id+"F47.opFillet","BLEND_FACE",FACE,{"disambiguationData":[OSD([subQ0,subQ9]),TDD([makeQuery(id+"F42.boolean.opBoolean","COPY",EDGE,{"disambiguationData":[TD([makeQuery(id+"F35.opLoft","SWEPT_FACE",FACE,{"disambiguationData":[OSD([subQ29,subQ28,subQ26,sQuery(id+"F22.wireOp",EDGE,"E28.12.1"),subQ25,subQ24])]})])],"derivedFrom":subQ11})])]}),makeQuery(id+"F47.opFillet","BLEND_FACE",FACE,{"disambiguationData":[OSD([subQ0,subQ9]),TDD([makeQuery(id+"F42.boolean.opBoolean","COPY",EDGE,{"disambiguationData":[TD([makeQuery(id+"F36.opLoft","SWEPT_FACE",FACE,{"disambiguationData":[OSD([subQ23,subQ22,subQ20,sQuery(id+"F22.wireOp",EDGE,"E28.13.1"),subQ19,subQ18])]})])],"derivedFrom":subQ11})])]}),makeQuery(id+"F47.opFillet","BLEND_FACE",FACE,{"disambiguationData":[OSD([subQ0,subQ9]),TDD([makeQuery(id+"F42.boolean.opBoolean","COPY",EDGE,{"disambiguationData":[TD([makeQuery(id+"F37.opLoft","SWEPT_FACE",FACE,{"disambiguationData":[OSD([subQ16,subQ15,subQ14,sQuery(id+"F22.wireOp",EDGE,"E28.14.1"),subQ13,subQ12])]})])],"derivedFrom":subQ11})])]}),makeQuery(id+"F47.opFillet","BLEND_FACE",FACE,{"disambiguationData":[OSD([subQ0,subQ9]),TDD([makeQuery(id+"F42.boolean.opBoolean","COPY",EDGE,{"disambiguationData":[TD([makeQuery(id+"F38.opLoft","SWEPT_FACE",FACE,{"disambiguationData":[OSD([subQ8,subQ7,subQ5,sQuery(id+"F22.wireOp",EDGE,"E28.15.1"),subQ4,subQ3])]})])],"derivedFrom":subQ11})])]})]});}
            var Q33;
            {var subQ0=sQuery(id+"F41.wireOp",EDGE,"E34");var subQ1=sQuery(id+"F41.wireOp",EDGE,"E32");Q33=makeQuery(id+"F42.boolean.opBoolean","INTERSECT",EDGE,{"derivedFrom":[makeQuery(id+"F25.opLoft","SWEPT_FACE",FACE,{"disambiguationData":[OSD([sQuery(id+"F3.wireOp",EDGE,"E20.10.0"),sQuery(id+"F3.wireOp",EDGE,"E20.10.1"),sQuery(id+"F3.wireOp",EDGE,"E20.10.3"),sQuery(id+"F22.wireOp",EDGE,"E28.2.1"),sQuery(id+"F22.wireOp",EDGE,"E28.2.2"),sQuery(id+"F22.wireOp",EDGE,"E28.2.3")])]}),makeQuery(id+"F42.opRevolve","SWEPT_FACE",FACE,{"disambiguationData":[OSD([subQ1]),TDD([makeQuery(id+"F41.imprint","IMPRINT",EDGE,{"disambiguationData":[TD([[makeQuery(id+"F41.imprint","INTERSECT",VERTEX,{"disambiguationData":[OD(0.0)],"derivedFrom":[subQ1,subQ0]}),-1.0]])],"derivedFrom":subQ1})])]})]});}
            var Q34;
            {var subQ0=sQuery(id+"F22.wireOp",EDGE,"E28.3.0");var subQ1=sQuery(id+"F22.wireOp",EDGE,"E28.3.1");var subQ2=sQuery(id+"F22.wireOp",EDGE,"E28.3.2");var subQ3=sQuery(id+"F22.wireOp",EDGE,"E28.3.3");var subQ4=sQuery(id+"F3.wireOp",EDGE,"E20.11.3");var subQ5=sQuery(id+"F3.wireOp",EDGE,"E20.11.1");var subQ6=makeQuery(id+"F26.opLoft","SWEPT_FACE",FACE,{"disambiguationData":[OSD([subQ5,sQuery(id+"F3.wireOp",EDGE,"E20.11.2"),subQ4,subQ0,subQ2,subQ3])]});var subQ7=sQuery(id+"F41.wireOp",EDGE,"E34");var subQ8=sQuery(id+"F41.wireOp",EDGE,"E32");Q34=makeQuery(id+"F44.opFillet","BLEND_EDGE",EDGE,{"blendedFrom":[makeQuery(id+"F40.boolean.opBoolean","INTERSECT",EDGE,{"derivedFrom":[subQ6,makeQuery(id+"F40.opExtrude","CAP_FACE",FACE,{"disambiguationData":[OSD([sQuery(id+"F39.wireOp",EDGE,"E29"),sQuery(id+"F39.wireOp",EDGE,"E30")])],"isStart":true})]}),makeQuery(id+"F42.boolean.opBoolean","COPY",FACE,{"disambiguationData":[TD([makeQuery(id+"F26.opLoft","SWEPT_FACE",FACE,{"disambiguationData":[OSD([sQuery(id+"F3.wireOp",EDGE,"E20.11.0"),subQ5,subQ4,subQ1,subQ2,subQ3])]})])],"derivedFrom":makeQuery(id+"F42.opRevolve","SWEPT_FACE",FACE,{"disambiguationData":[OSD([subQ8]),TDD([makeQuery(id+"F41.imprint","IMPRINT",EDGE,{"disambiguationData":[TD([[makeQuery(id+"F41.imprint","INTERSECT",VERTEX,{"disambiguationData":[OD(0.0)],"derivedFrom":[subQ8,subQ7]}),-1.0]])],"derivedFrom":subQ8})])]})})],"blendedInto":[makeQuery(id+"F42.boolean.opBoolean","COPY",FACE,{"disambiguationData":[TD([makeQuery(id+"F26.opLoft","SWEPT_FACE",FACE,{"disambiguationData":[OSD([sQuery(id+"F3.wireOp",EDGE,"E20.11.0"),subQ5,subQ4,subQ1,subQ2,subQ3])]})])],"derivedFrom":makeQuery(id+"F42.opRevolve","SWEPT_FACE",FACE,{"disambiguationData":[OSD([subQ8]),TDD([makeQuery(id+"F41.imprint","IMPRINT",EDGE,{"disambiguationData":[TD([[makeQuery(id+"F41.imprint","INTERSECT",VERTEX,{"disambiguationData":[OD(0.0)],"derivedFrom":[subQ8,subQ7]}),-1.0]])],"derivedFrom":subQ8})])]})})]});}
            var Q35;
            {var subQ0=sQuery(id+"F41.wireOp",EDGE,"E37");var subQ1=makeQuery(id+"F42.opRevolve","SWEPT_FACE",FACE,{"disambiguationData":[OSD([subQ0])]});var subQ2=makeQuery(id+"F40.opExtrude","CAP_FACE",FACE,{"disambiguationData":[OSD([sQuery(id+"F39.wireOp",EDGE,"E29"),sQuery(id+"F39.wireOp",EDGE,"E30")])],"isStart":true});var subQ3=sQuery(id+"F22.wireOp",EDGE,"E28.15.3");var subQ4=sQuery(id+"F22.wireOp",EDGE,"E28.15.2");var subQ5=sQuery(id+"F3.wireOp",EDGE,"E20.7.3");var subQ7=sQuery(id+"F3.wireOp",EDGE,"E20.7.1");var subQ8=sQuery(id+"F3.wireOp",EDGE,"E20.7.0");var subQ9=sQuery(id+"F41.wireOp",EDGE,"E38");var subQ10=makeQuery(id+"F42.opRevolve","SWEPT_FACE",FACE,{"disambiguationData":[OSD([subQ9])]});var subQ11=makeQuery(id+"F42.opRevolve","SWEPT_EDGE",EDGE,{"disambiguationData":[OSD([subQ0,subQ9])]});var subQ12=sQuery(id+"F22.wireOp",EDGE,"E28.14.3");var subQ13=sQuery(id+"F22.wireOp",EDGE,"E28.14.2");var subQ14=sQuery(id+"F3.wireOp",EDGE,"E20.6.3");var subQ15=sQuery(id+"F3.wireOp",EDGE,"E20.6.1");var subQ16=sQuery(id+"F3.wireOp",EDGE,"E20.6.0");var subQ18=sQuery(id+"F22.wireOp",EDGE,"E28.13.3");var subQ19=sQuery(id+"F22.wireOp",EDGE,"E28.13.2");var subQ20=sQuery(id+"F3.wireOp",EDGE,"E20.5.3");var subQ22=sQuery(id+"F3.wireOp",EDGE,"E20.5.1");var subQ23=sQuery(id+"F3.wireOp",EDGE,"E20.5.0");var subQ24=sQuery(id+"F22.wireOp",EDGE,"E28.12.3");var subQ25=sQuery(id+"F22.wireOp",EDGE,"E28.12.2");var subQ26=sQuery(id+"F3.wireOp",EDGE,"E20.4.3");var subQ28=sQuery(id+"F3.wireOp",EDGE,"E20.4.1");var subQ29=sQuery(id+"F3.wireOp",EDGE,"E20.4.0");var subQ30=sQuery(id+"F22.wireOp",EDGE,"E28.11.3");var subQ31=sQuery(id+"F22.wireOp",EDGE,"E28.11.2");var subQ32=sQuery(id+"F3.wireOp",EDGE,"E20.3.3");var subQ34=sQuery(id+"F3.wireOp",EDGE,"E20.3.1");var subQ35=sQuery(id+"F3.wireOp",EDGE,"E20.3.0");var subQ36=sQuery(id+"F22.wireOp",EDGE,"E28.10.3");var subQ37=sQuery(id+"F22.wireOp",EDGE,"E28.10.2");var subQ38=sQuery(id+"F3.wireOp",EDGE,"E20.2.3");var subQ40=sQuery(id+"F3.wireOp",EDGE,"E20.2.1");var subQ41=sQuery(id+"F3.wireOp",EDGE,"E20.2.0");var subQ42=sQuery(id+"F22.wireOp",EDGE,"E28.9.3");var subQ43=sQuery(id+"F22.wireOp",EDGE,"E28.9.2");var subQ44=sQuery(id+"F3.wireOp",EDGE,"E20.1.3");var subQ46=sQuery(id+"F3.wireOp",EDGE,"E20.1.1");var subQ47=sQuery(id+"F3.wireOp",EDGE,"E20.1.0");var subQ48=sQuery(id+"F22.wireOp",EDGE,"E28.8.3");var subQ49=sQuery(id+"F22.wireOp",EDGE,"E28.8.2");var subQ51=sQuery(id+"F3.wireOp",EDGE,"E18.top");var subQ52=sQuery(id+"F3.wireOp",EDGE,"E18.bottom");var subQ53=sQuery(id+"F3.wireOp",EDGE,"E18.left");var subQ54=sQuery(id+"F22.wireOp",EDGE,"E28.7.3");var subQ55=sQuery(id+"F22.wireOp",EDGE,"E28.7.2");var subQ56=sQuery(id+"F3.wireOp",EDGE,"E20.15.3");var subQ57=sQuery(id+"F3.wireOp",EDGE,"E20.15.1");var subQ58=sQuery(id+"F3.wireOp",EDGE,"E20.15.0");var subQ60=sQuery(id+"F22.wireOp",EDGE,"E28.6.3");var subQ61=sQuery(id+"F22.wireOp",EDGE,"E28.6.2");var subQ62=sQuery(id+"F3.wireOp",EDGE,"E20.14.3");var subQ64=sQuery(id+"F3.wireOp",EDGE,"E20.14.1");var subQ65=sQuery(id+"F3.wireOp",EDGE,"E20.14.0");var subQ66=sQuery(id+"F22.wireOp",EDGE,"E28.5.3");var subQ67=sQuery(id+"F22.wireOp",EDGE,"E28.5.2");var subQ68=sQuery(id+"F3.wireOp",EDGE,"E20.13.3");var subQ70=sQuery(id+"F3.wireOp",EDGE,"E20.13.1");var subQ71=sQuery(id+"F3.wireOp",EDGE,"E20.13.0");var subQ72=sQuery(id+"F22.wireOp",EDGE,"E28.4.3");var subQ73=sQuery(id+"F22.wireOp",EDGE,"E28.4.2");var subQ74=sQuery(id+"F3.wireOp",EDGE,"E20.12.3");var subQ76=sQuery(id+"F3.wireOp",EDGE,"E20.12.1");var subQ77=sQuery(id+"F3.wireOp",EDGE,"E20.12.0");var subQ78=sQuery(id+"F22.wireOp",EDGE,"E28.3.3");var subQ79=sQuery(id+"F22.wireOp",EDGE,"E28.3.2");var subQ80=sQuery(id+"F3.wireOp",EDGE,"E20.11.3");var subQ82=sQuery(id+"F3.wireOp",EDGE,"E20.11.1");var subQ83=sQuery(id+"F3.wireOp",EDGE,"E20.11.0");var subQ84=sQuery(id+"F22.wireOp",EDGE,"E28.2.3");var subQ85=sQuery(id+"F22.wireOp",EDGE,"E28.2.2");var subQ86=sQuery(id+"F3.wireOp",EDGE,"E20.10.3");var subQ87=sQuery(id+"F3.wireOp",EDGE,"E20.10.1");var subQ88=sQuery(id+"F3.wireOp",EDGE,"E20.10.0");var subQ89=makeQuery(id+"F25.opLoft","SWEPT_FACE",FACE,{"disambiguationData":[OSD([subQ88,subQ87,subQ86,sQuery(id+"F22.wireOp",EDGE,"E28.2.1"),subQ85,subQ84])]});var subQ92=sQuery(id+"F22.wireOp",EDGE,"E28.1.3");var subQ93=sQuery(id+"F22.wireOp",EDGE,"E28.1.2");var subQ94=sQuery(id+"F3.wireOp",EDGE,"E20.9.3");var subQ95=sQuery(id+"F3.wireOp",EDGE,"E20.9.1");var subQ96=sQuery(id+"F3.wireOp",EDGE,"E20.9.0");var subQ97=makeQuery(id+"F24.opLoft","SWEPT_FACE",FACE,{"disambiguationData":[OSD([subQ96,subQ95,subQ94,sQuery(id+"F22.wireOp",EDGE,"E28.1.1"),subQ93,subQ92])]});var subQ98=sQuery(id+"F22.wireOp",EDGE,"E27.top");var subQ99=sQuery(id+"F22.wireOp",EDGE,"E27.bottom");var subQ100=sQuery(id+"F3.wireOp",EDGE,"E20.8.3");var subQ102=sQuery(id+"F3.wireOp",EDGE,"E20.8.1");var subQ106=makeQuery(id+"F42.boolean.opBoolean","COPY",FACE,{"disambiguationData":[TD([subQ89])],"derivedFrom":subQ10});var subQ135=makeQuery(id+"F25.boolean.opBoolean","INTERSECT",EDGE,{"derivedFrom":[makeQuery(id+"F24.boolean.opBoolean","SPLIT",FACE,{"disambiguationData":[TD([makeQuery(id+"F5.opLoft","CAP_FACE",FACE,{"disambiguationData":[OSD([makeQuery(id+"F3.imprint","IMPRINT",FACE,{"disambiguationData":[TD([[makeQuery(id+"F3.imprint","IMPRINT",EDGE,{"derivedFrom":subQ52}),1.0]])]})])],"isStart":true})])],"derivedFrom":makeQuery(id+"F1.opRevolve","SWEPT_FACE",FACE,{"disambiguationData":[OSD([sQuery(id+"F0.wireOp",EDGE,"E4")])]})}),subQ89]});Q35=makeQuery(id+"F48.opFillet","BLEND_EDGE",EDGE,{"blendedFrom":[makeQuery(id+"F47.opFillet","TWEAK_EDGE",EDGE,{"derivedFrom":[makeQuery(id+"F45.opFillet","BLEND_VERTEX",VERTEX,{"blendedFrom":[subQ135,subQ89,subQ106],"blendedInto":[subQ89,subQ106]}),makeQuery(id+"F45.opFillet","BLEND_VERTEX",VERTEX,{"blendedFrom":[subQ135,makeQuery(id+"F42.boolean.opBoolean","MERGE",FACE,{"derivedFrom":[subQ2,subQ1]}),subQ106],"blendedInto":[makeQuery(id+"F42.boolean.opBoolean","MERGE",FACE,{"derivedFrom":[subQ2,subQ1]}),subQ106]})]}),makeQuery(id+"F47.opFillet","BLEND_FACE",FACE,{"disambiguationData":[OSD([subQ0,subQ9]),TDD([makeQuery(id+"F42.boolean.opBoolean","COPY",EDGE,{"disambiguationData":[TD([makeQuery(id+"F23.opLoft","SWEPT_FACE",FACE,{"disambiguationData":[OSD([sQuery(id+"F3.wireOp",EDGE,"E20.8.0"),subQ102,subQ100,subQ99,subQ98,sQuery(id+"F22.wireOp",EDGE,"E27.right")])]})])],"derivedFrom":subQ11})])]}),makeQuery(id+"F47.opFillet","BLEND_FACE",FACE,{"disambiguationData":[OSD([subQ0,subQ9]),TDD([makeQuery(id+"F42.boolean.opBoolean","COPY",EDGE,{"disambiguationData":[TD([subQ97])],"derivedFrom":subQ11})])]}),makeQuery(id+"F47.opFillet","BLEND_FACE",FACE,{"disambiguationData":[OSD([subQ0,subQ9]),TDD([makeQuery(id+"F42.boolean.opBoolean","COPY",EDGE,{"disambiguationData":[TD([subQ89])],"derivedFrom":subQ11})])]}),makeQuery(id+"F47.opFillet","BLEND_FACE",FACE,{"disambiguationData":[OSD([subQ0,subQ9]),TDD([makeQuery(id+"F42.boolean.opBoolean","COPY",EDGE,{"disambiguationData":[TD([makeQuery(id+"F26.opLoft","SWEPT_FACE",FACE,{"disambiguationData":[OSD([subQ83,subQ82,subQ80,sQuery(id+"F22.wireOp",EDGE,"E28.3.1"),subQ79,subQ78])]})])],"derivedFrom":subQ11})])]}),makeQuery(id+"F47.opFillet","BLEND_FACE",FACE,{"disambiguationData":[OSD([subQ0,subQ9]),TDD([makeQuery(id+"F42.boolean.opBoolean","COPY",EDGE,{"disambiguationData":[TD([makeQuery(id+"F27.opLoft","SWEPT_FACE",FACE,{"disambiguationData":[OSD([subQ77,subQ76,subQ74,sQuery(id+"F22.wireOp",EDGE,"E28.4.1"),subQ73,subQ72])]})])],"derivedFrom":subQ11})])]}),makeQuery(id+"F47.opFillet","BLEND_FACE",FACE,{"disambiguationData":[OSD([subQ0,subQ9]),TDD([makeQuery(id+"F42.boolean.opBoolean","COPY",EDGE,{"disambiguationData":[TD([makeQuery(id+"F28.opLoft","SWEPT_FACE",FACE,{"disambiguationData":[OSD([subQ71,subQ70,subQ68,sQuery(id+"F22.wireOp",EDGE,"E28.5.1"),subQ67,subQ66])]})])],"derivedFrom":subQ11})])]}),makeQuery(id+"F47.opFillet","BLEND_FACE",FACE,{"disambiguationData":[OSD([subQ0,subQ9]),TDD([makeQuery(id+"F42.boolean.opBoolean","COPY",EDGE,{"disambiguationData":[TD([makeQuery(id+"F29.opLoft","SWEPT_FACE",FACE,{"disambiguationData":[OSD([subQ65,subQ64,subQ62,sQuery(id+"F22.wireOp",EDGE,"E28.6.1"),subQ61,subQ60])]})])],"derivedFrom":subQ11})])]}),makeQuery(id+"F47.opFillet","BLEND_FACE",FACE,{"disambiguationData":[OSD([subQ0,subQ9]),TDD([makeQuery(id+"F42.boolean.opBoolean","COPY",EDGE,{"disambiguationData":[TD([makeQuery(id+"F30.opLoft","SWEPT_FACE",FACE,{"disambiguationData":[OSD([subQ58,subQ57,subQ56,sQuery(id+"F22.wireOp",EDGE,"E28.7.1"),subQ55,subQ54])]})])],"derivedFrom":subQ11})])]}),makeQuery(id+"F47.opFillet","BLEND_FACE",FACE,{"disambiguationData":[OSD([subQ0,subQ9]),TDD([makeQuery(id+"F42.boolean.opBoolean","COPY",EDGE,{"disambiguationData":[TD([makeQuery(id+"F31.opLoft","SWEPT_FACE",FACE,{"disambiguationData":[OSD([subQ52,subQ51,subQ53,sQuery(id+"F22.wireOp",EDGE,"E28.8.1"),subQ49,subQ48])]})])],"derivedFrom":subQ11})])]}),makeQuery(id+"F47.opFillet","BLEND_FACE",FACE,{"disambiguationData":[OSD([subQ0,subQ9]),TDD([makeQuery(id+"F42.boolean.opBoolean","COPY",EDGE,{"disambiguationData":[TD([makeQuery(id+"F32.opLoft","SWEPT_FACE",FACE,{"disambiguationData":[OSD([subQ47,subQ46,subQ44,sQuery(id+"F22.wireOp",EDGE,"E28.9.1"),subQ43,subQ42])]})])],"derivedFrom":subQ11})])]}),makeQuery(id+"F47.opFillet","BLEND_FACE",FACE,{"disambiguationData":[OSD([subQ0,subQ9]),TDD([makeQuery(id+"F42.boolean.opBoolean","COPY",EDGE,{"disambiguationData":[TD([makeQuery(id+"F33.opLoft","SWEPT_FACE",FACE,{"disambiguationData":[OSD([subQ41,subQ40,subQ38,sQuery(id+"F22.wireOp",EDGE,"E28.10.1"),subQ37,subQ36])]})])],"derivedFrom":subQ11})])]}),makeQuery(id+"F47.opFillet","BLEND_FACE",FACE,{"disambiguationData":[OSD([subQ0,subQ9]),TDD([makeQuery(id+"F42.boolean.opBoolean","COPY",EDGE,{"disambiguationData":[TD([makeQuery(id+"F34.opLoft","SWEPT_FACE",FACE,{"disambiguationData":[OSD([subQ35,subQ34,subQ32,sQuery(id+"F22.wireOp",EDGE,"E28.11.1"),subQ31,subQ30])]})])],"derivedFrom":subQ11})])]}),makeQuery(id+"F47.opFillet","BLEND_FACE",FACE,{"disambiguationData":[OSD([subQ0,subQ9]),TDD([makeQuery(id+"F42.boolean.opBoolean","COPY",EDGE,{"disambiguationData":[TD([makeQuery(id+"F35.opLoft","SWEPT_FACE",FACE,{"disambiguationData":[OSD([subQ29,subQ28,subQ26,sQuery(id+"F22.wireOp",EDGE,"E28.12.1"),subQ25,subQ24])]})])],"derivedFrom":subQ11})])]}),makeQuery(id+"F47.opFillet","BLEND_FACE",FACE,{"disambiguationData":[OSD([subQ0,subQ9]),TDD([makeQuery(id+"F42.boolean.opBoolean","COPY",EDGE,{"disambiguationData":[TD([makeQuery(id+"F36.opLoft","SWEPT_FACE",FACE,{"disambiguationData":[OSD([subQ23,subQ22,subQ20,sQuery(id+"F22.wireOp",EDGE,"E28.13.1"),subQ19,subQ18])]})])],"derivedFrom":subQ11})])]}),makeQuery(id+"F47.opFillet","BLEND_FACE",FACE,{"disambiguationData":[OSD([subQ0,subQ9]),TDD([makeQuery(id+"F42.boolean.opBoolean","COPY",EDGE,{"disambiguationData":[TD([makeQuery(id+"F37.opLoft","SWEPT_FACE",FACE,{"disambiguationData":[OSD([subQ16,subQ15,subQ14,sQuery(id+"F22.wireOp",EDGE,"E28.14.1"),subQ13,subQ12])]})])],"derivedFrom":subQ11})])]}),makeQuery(id+"F47.opFillet","BLEND_FACE",FACE,{"disambiguationData":[OSD([subQ0,subQ9]),TDD([makeQuery(id+"F42.boolean.opBoolean","COPY",EDGE,{"disambiguationData":[TD([makeQuery(id+"F38.opLoft","SWEPT_FACE",FACE,{"disambiguationData":[OSD([subQ8,subQ7,subQ5,sQuery(id+"F22.wireOp",EDGE,"E28.15.1"),subQ4,subQ3])]})])],"derivedFrom":subQ11})])]})],"blendedInto":[makeQuery(id+"F47.opFillet","BLEND_FACE",FACE,{"disambiguationData":[OSD([subQ0,subQ9]),TDD([makeQuery(id+"F42.boolean.opBoolean","COPY",EDGE,{"disambiguationData":[TD([makeQuery(id+"F23.opLoft","SWEPT_FACE",FACE,{"disambiguationData":[OSD([sQuery(id+"F3.wireOp",EDGE,"E20.8.0"),subQ102,subQ100,subQ99,subQ98,sQuery(id+"F22.wireOp",EDGE,"E27.right")])]})])],"derivedFrom":subQ11})])]}),makeQuery(id+"F47.opFillet","BLEND_FACE",FACE,{"disambiguationData":[OSD([subQ0,subQ9]),TDD([makeQuery(id+"F42.boolean.opBoolean","COPY",EDGE,{"disambiguationData":[TD([subQ97])],"derivedFrom":subQ11})])]}),makeQuery(id+"F47.opFillet","BLEND_FACE",FACE,{"disambiguationData":[OSD([subQ0,subQ9]),TDD([makeQuery(id+"F42.boolean.opBoolean","COPY",EDGE,{"disambiguationData":[TD([subQ89])],"derivedFrom":subQ11})])]}),makeQuery(id+"F47.opFillet","BLEND_FACE",FACE,{"disambiguationData":[OSD([subQ0,subQ9]),TDD([makeQuery(id+"F42.boolean.opBoolean","COPY",EDGE,{"disambiguationData":[TD([makeQuery(id+"F26.opLoft","SWEPT_FACE",FACE,{"disambiguationData":[OSD([subQ83,subQ82,subQ80,sQuery(id+"F22.wireOp",EDGE,"E28.3.1"),subQ79,subQ78])]})])],"derivedFrom":subQ11})])]}),makeQuery(id+"F47.opFillet","BLEND_FACE",FACE,{"disambiguationData":[OSD([subQ0,subQ9]),TDD([makeQuery(id+"F42.boolean.opBoolean","COPY",EDGE,{"disambiguationData":[TD([makeQuery(id+"F27.opLoft","SWEPT_FACE",FACE,{"disambiguationData":[OSD([subQ77,subQ76,subQ74,sQuery(id+"F22.wireOp",EDGE,"E28.4.1"),subQ73,subQ72])]})])],"derivedFrom":subQ11})])]}),makeQuery(id+"F47.opFillet","BLEND_FACE",FACE,{"disambiguationData":[OSD([subQ0,subQ9]),TDD([makeQuery(id+"F42.boolean.opBoolean","COPY",EDGE,{"disambiguationData":[TD([makeQuery(id+"F28.opLoft","SWEPT_FACE",FACE,{"disambiguationData":[OSD([subQ71,subQ70,subQ68,sQuery(id+"F22.wireOp",EDGE,"E28.5.1"),subQ67,subQ66])]})])],"derivedFrom":subQ11})])]}),makeQuery(id+"F47.opFillet","BLEND_FACE",FACE,{"disambiguationData":[OSD([subQ0,subQ9]),TDD([makeQuery(id+"F42.boolean.opBoolean","COPY",EDGE,{"disambiguationData":[TD([makeQuery(id+"F29.opLoft","SWEPT_FACE",FACE,{"disambiguationData":[OSD([subQ65,subQ64,subQ62,sQuery(id+"F22.wireOp",EDGE,"E28.6.1"),subQ61,subQ60])]})])],"derivedFrom":subQ11})])]}),makeQuery(id+"F47.opFillet","BLEND_FACE",FACE,{"disambiguationData":[OSD([subQ0,subQ9]),TDD([makeQuery(id+"F42.boolean.opBoolean","COPY",EDGE,{"disambiguationData":[TD([makeQuery(id+"F30.opLoft","SWEPT_FACE",FACE,{"disambiguationData":[OSD([subQ58,subQ57,subQ56,sQuery(id+"F22.wireOp",EDGE,"E28.7.1"),subQ55,subQ54])]})])],"derivedFrom":subQ11})])]}),makeQuery(id+"F47.opFillet","BLEND_FACE",FACE,{"disambiguationData":[OSD([subQ0,subQ9]),TDD([makeQuery(id+"F42.boolean.opBoolean","COPY",EDGE,{"disambiguationData":[TD([makeQuery(id+"F31.opLoft","SWEPT_FACE",FACE,{"disambiguationData":[OSD([subQ52,subQ51,subQ53,sQuery(id+"F22.wireOp",EDGE,"E28.8.1"),subQ49,subQ48])]})])],"derivedFrom":subQ11})])]}),makeQuery(id+"F47.opFillet","BLEND_FACE",FACE,{"disambiguationData":[OSD([subQ0,subQ9]),TDD([makeQuery(id+"F42.boolean.opBoolean","COPY",EDGE,{"disambiguationData":[TD([makeQuery(id+"F32.opLoft","SWEPT_FACE",FACE,{"disambiguationData":[OSD([subQ47,subQ46,subQ44,sQuery(id+"F22.wireOp",EDGE,"E28.9.1"),subQ43,subQ42])]})])],"derivedFrom":subQ11})])]}),makeQuery(id+"F47.opFillet","BLEND_FACE",FACE,{"disambiguationData":[OSD([subQ0,subQ9]),TDD([makeQuery(id+"F42.boolean.opBoolean","COPY",EDGE,{"disambiguationData":[TD([makeQuery(id+"F33.opLoft","SWEPT_FACE",FACE,{"disambiguationData":[OSD([subQ41,subQ40,subQ38,sQuery(id+"F22.wireOp",EDGE,"E28.10.1"),subQ37,subQ36])]})])],"derivedFrom":subQ11})])]}),makeQuery(id+"F47.opFillet","BLEND_FACE",FACE,{"disambiguationData":[OSD([subQ0,subQ9]),TDD([makeQuery(id+"F42.boolean.opBoolean","COPY",EDGE,{"disambiguationData":[TD([makeQuery(id+"F34.opLoft","SWEPT_FACE",FACE,{"disambiguationData":[OSD([subQ35,subQ34,subQ32,sQuery(id+"F22.wireOp",EDGE,"E28.11.1"),subQ31,subQ30])]})])],"derivedFrom":subQ11})])]}),makeQuery(id+"F47.opFillet","BLEND_FACE",FACE,{"disambiguationData":[OSD([subQ0,subQ9]),TDD([makeQuery(id+"F42.boolean.opBoolean","COPY",EDGE,{"disambiguationData":[TD([makeQuery(id+"F35.opLoft","SWEPT_FACE",FACE,{"disambiguationData":[OSD([subQ29,subQ28,subQ26,sQuery(id+"F22.wireOp",EDGE,"E28.12.1"),subQ25,subQ24])]})])],"derivedFrom":subQ11})])]}),makeQuery(id+"F47.opFillet","BLEND_FACE",FACE,{"disambiguationData":[OSD([subQ0,subQ9]),TDD([makeQuery(id+"F42.boolean.opBoolean","COPY",EDGE,{"disambiguationData":[TD([makeQuery(id+"F36.opLoft","SWEPT_FACE",FACE,{"disambiguationData":[OSD([subQ23,subQ22,subQ20,sQuery(id+"F22.wireOp",EDGE,"E28.13.1"),subQ19,subQ18])]})])],"derivedFrom":subQ11})])]}),makeQuery(id+"F47.opFillet","BLEND_FACE",FACE,{"disambiguationData":[OSD([subQ0,subQ9]),TDD([makeQuery(id+"F42.boolean.opBoolean","COPY",EDGE,{"disambiguationData":[TD([makeQuery(id+"F37.opLoft","SWEPT_FACE",FACE,{"disambiguationData":[OSD([subQ16,subQ15,subQ14,sQuery(id+"F22.wireOp",EDGE,"E28.14.1"),subQ13,subQ12])]})])],"derivedFrom":subQ11})])]}),makeQuery(id+"F47.opFillet","BLEND_FACE",FACE,{"disambiguationData":[OSD([subQ0,subQ9]),TDD([makeQuery(id+"F42.boolean.opBoolean","COPY",EDGE,{"disambiguationData":[TD([makeQuery(id+"F38.opLoft","SWEPT_FACE",FACE,{"disambiguationData":[OSD([subQ8,subQ7,subQ5,sQuery(id+"F22.wireOp",EDGE,"E28.15.1"),subQ4,subQ3])]})])],"derivedFrom":subQ11})])]})]});}
            var Q36;
            {var subQ0=sQuery(id+"F22.wireOp",EDGE,"E28.2.3");var subQ1=sQuery(id+"F22.wireOp",EDGE,"E28.2.2");var subQ2=sQuery(id+"F22.wireOp",EDGE,"E28.2.1");var subQ3=sQuery(id+"F3.wireOp",EDGE,"E20.10.3");var subQ4=sQuery(id+"F3.wireOp",EDGE,"E20.10.1");var subQ5=sQuery(id+"F22.wireOp",EDGE,"E28.2.0");var subQ6=makeQuery(id+"F25.opLoft","SWEPT_FACE",FACE,{"disambiguationData":[OSD([subQ4,sQuery(id+"F3.wireOp",EDGE,"E20.10.2"),subQ3,subQ5,subQ1,subQ0])]});var subQ7=sQuery(id+"F41.wireOp",EDGE,"E34");var subQ8=sQuery(id+"F41.wireOp",EDGE,"E32");Q36=makeQuery(id+"F44.opFillet","BLEND_EDGE",EDGE,{"blendedFrom":[makeQuery(id+"F40.boolean.opBoolean","INTERSECT",EDGE,{"derivedFrom":[subQ6,makeQuery(id+"F40.opExtrude","CAP_FACE",FACE,{"disambiguationData":[OSD([sQuery(id+"F39.wireOp",EDGE,"E29"),sQuery(id+"F39.wireOp",EDGE,"E30")])],"isStart":true})]}),makeQuery(id+"F42.boolean.opBoolean","COPY",FACE,{"disambiguationData":[TD([makeQuery(id+"F25.opLoft","SWEPT_FACE",FACE,{"disambiguationData":[OSD([sQuery(id+"F3.wireOp",EDGE,"E20.10.0"),subQ4,subQ3,subQ2,subQ1,subQ0])]})])],"derivedFrom":makeQuery(id+"F42.opRevolve","SWEPT_FACE",FACE,{"disambiguationData":[OSD([subQ8]),TDD([makeQuery(id+"F41.imprint","IMPRINT",EDGE,{"disambiguationData":[TD([[makeQuery(id+"F41.imprint","INTERSECT",VERTEX,{"disambiguationData":[OD(0.0)],"derivedFrom":[subQ8,subQ7]}),-1.0]])],"derivedFrom":subQ8})])]})})],"blendedInto":[makeQuery(id+"F42.boolean.opBoolean","COPY",FACE,{"disambiguationData":[TD([makeQuery(id+"F25.opLoft","SWEPT_FACE",FACE,{"disambiguationData":[OSD([sQuery(id+"F3.wireOp",EDGE,"E20.10.0"),subQ4,subQ3,subQ2,subQ1,subQ0])]})])],"derivedFrom":makeQuery(id+"F42.opRevolve","SWEPT_FACE",FACE,{"disambiguationData":[OSD([subQ8]),TDD([makeQuery(id+"F41.imprint","IMPRINT",EDGE,{"disambiguationData":[TD([[makeQuery(id+"F41.imprint","INTERSECT",VERTEX,{"disambiguationData":[OD(0.0)],"derivedFrom":[subQ8,subQ7]}),-1.0]])],"derivedFrom":subQ8})])]})})]});}
            var Q37;
            {var subQ0=sQuery(id+"F41.wireOp",EDGE,"E34");var subQ1=sQuery(id+"F41.wireOp",EDGE,"E32");Q37=makeQuery(id+"F42.boolean.opBoolean","INTERSECT",EDGE,{"derivedFrom":[makeQuery(id+"F24.opLoft","SWEPT_FACE",FACE,{"disambiguationData":[OSD([sQuery(id+"F3.wireOp",EDGE,"E20.9.0"),sQuery(id+"F3.wireOp",EDGE,"E20.9.1"),sQuery(id+"F3.wireOp",EDGE,"E20.9.3"),sQuery(id+"F22.wireOp",EDGE,"E28.1.1"),sQuery(id+"F22.wireOp",EDGE,"E28.1.2"),sQuery(id+"F22.wireOp",EDGE,"E28.1.3")])]}),makeQuery(id+"F42.opRevolve","SWEPT_FACE",FACE,{"disambiguationData":[OSD([subQ1]),TDD([makeQuery(id+"F41.imprint","IMPRINT",EDGE,{"disambiguationData":[TD([[makeQuery(id+"F41.imprint","INTERSECT",VERTEX,{"disambiguationData":[OD(0.0)],"derivedFrom":[subQ1,subQ0]}),-1.0]])],"derivedFrom":subQ1})])]})]});}
            var Q38;
            {var subQ0=sQuery(id+"F41.wireOp",EDGE,"E37");var subQ1=makeQuery(id+"F42.opRevolve","SWEPT_FACE",FACE,{"disambiguationData":[OSD([subQ0])]});var subQ2=makeQuery(id+"F40.opExtrude","CAP_FACE",FACE,{"disambiguationData":[OSD([sQuery(id+"F39.wireOp",EDGE,"E29"),sQuery(id+"F39.wireOp",EDGE,"E30")])],"isStart":true});var subQ3=sQuery(id+"F22.wireOp",EDGE,"E28.15.3");var subQ4=sQuery(id+"F22.wireOp",EDGE,"E28.15.2");var subQ5=sQuery(id+"F3.wireOp",EDGE,"E20.7.3");var subQ6=sQuery(id+"F3.wireOp",EDGE,"E20.7.1");var subQ7=sQuery(id+"F41.wireOp",EDGE,"E38");var subQ8=makeQuery(id+"F42.opRevolve","SWEPT_FACE",FACE,{"disambiguationData":[OSD([subQ7])]});var subQ9=makeQuery(id+"F42.opRevolve","SWEPT_EDGE",EDGE,{"disambiguationData":[OSD([subQ0,subQ7])]});var subQ10=sQuery(id+"F22.wireOp",EDGE,"E28.14.3");var subQ11=sQuery(id+"F22.wireOp",EDGE,"E28.14.2");var subQ12=sQuery(id+"F3.wireOp",EDGE,"E20.6.3");var subQ13=sQuery(id+"F3.wireOp",EDGE,"E20.6.1");var subQ14=sQuery(id+"F22.wireOp",EDGE,"E28.13.3");var subQ15=sQuery(id+"F22.wireOp",EDGE,"E28.13.2");var subQ16=sQuery(id+"F3.wireOp",EDGE,"E20.5.3");var subQ17=sQuery(id+"F3.wireOp",EDGE,"E20.5.1");var subQ18=sQuery(id+"F22.wireOp",EDGE,"E28.12.3");var subQ19=sQuery(id+"F22.wireOp",EDGE,"E28.12.2");var subQ20=sQuery(id+"F3.wireOp",EDGE,"E20.4.3");var subQ21=sQuery(id+"F3.wireOp",EDGE,"E20.4.1");var subQ22=sQuery(id+"F22.wireOp",EDGE,"E28.11.3");var subQ23=sQuery(id+"F22.wireOp",EDGE,"E28.11.2");var subQ24=sQuery(id+"F3.wireOp",EDGE,"E20.3.3");var subQ25=sQuery(id+"F3.wireOp",EDGE,"E20.3.1");var subQ26=sQuery(id+"F22.wireOp",EDGE,"E28.10.3");var subQ27=sQuery(id+"F22.wireOp",EDGE,"E28.10.2");var subQ28=sQuery(id+"F3.wireOp",EDGE,"E20.2.3");var subQ29=sQuery(id+"F3.wireOp",EDGE,"E20.2.1");var subQ30=sQuery(id+"F22.wireOp",EDGE,"E28.9.3");var subQ31=sQuery(id+"F22.wireOp",EDGE,"E28.9.2");var subQ32=sQuery(id+"F3.wireOp",EDGE,"E20.1.3");var subQ33=sQuery(id+"F3.wireOp",EDGE,"E20.1.1");var subQ34=sQuery(id+"F22.wireOp",EDGE,"E28.8.3");var subQ35=sQuery(id+"F22.wireOp",EDGE,"E28.8.2");var subQ36=sQuery(id+"F3.wireOp",EDGE,"E18.top");var subQ37=sQuery(id+"F3.wireOp",EDGE,"E18.bottom");var subQ38=sQuery(id+"F22.wireOp",EDGE,"E28.7.3");var subQ39=sQuery(id+"F22.wireOp",EDGE,"E28.7.2");var subQ40=sQuery(id+"F3.wireOp",EDGE,"E20.15.3");var subQ41=sQuery(id+"F3.wireOp",EDGE,"E20.15.1");var subQ42=sQuery(id+"F22.wireOp",EDGE,"E28.6.3");var subQ43=sQuery(id+"F22.wireOp",EDGE,"E28.6.2");var subQ44=sQuery(id+"F3.wireOp",EDGE,"E20.14.3");var subQ45=sQuery(id+"F3.wireOp",EDGE,"E20.14.1");var subQ46=sQuery(id+"F22.wireOp",EDGE,"E28.5.3");var subQ47=sQuery(id+"F22.wireOp",EDGE,"E28.5.2");var subQ48=sQuery(id+"F3.wireOp",EDGE,"E20.13.3");var subQ49=sQuery(id+"F3.wireOp",EDGE,"E20.13.1");var subQ50=sQuery(id+"F22.wireOp",EDGE,"E28.4.3");var subQ51=sQuery(id+"F22.wireOp",EDGE,"E28.4.2");var subQ52=sQuery(id+"F3.wireOp",EDGE,"E20.12.3");var subQ53=sQuery(id+"F3.wireOp",EDGE,"E20.12.1");var subQ54=sQuery(id+"F22.wireOp",EDGE,"E28.3.3");var subQ55=sQuery(id+"F22.wireOp",EDGE,"E28.3.2");var subQ56=sQuery(id+"F3.wireOp",EDGE,"E20.11.3");var subQ57=sQuery(id+"F3.wireOp",EDGE,"E20.11.1");var subQ58=sQuery(id+"F22.wireOp",EDGE,"E28.2.3");var subQ59=sQuery(id+"F22.wireOp",EDGE,"E28.2.2");var subQ60=sQuery(id+"F3.wireOp",EDGE,"E20.10.3");var subQ61=sQuery(id+"F3.wireOp",EDGE,"E20.10.1");var subQ62=sQuery(id+"F22.wireOp",EDGE,"E28.1.3");var subQ63=sQuery(id+"F22.wireOp",EDGE,"E28.1.2");var subQ64=sQuery(id+"F3.wireOp",EDGE,"E20.9.3");var subQ65=sQuery(id+"F3.wireOp",EDGE,"E20.9.1");var subQ67=makeQuery(id+"F24.opLoft","SWEPT_FACE",FACE,{"disambiguationData":[OSD([sQuery(id+"F3.wireOp",EDGE,"E20.9.0"),subQ65,subQ64,sQuery(id+"F22.wireOp",EDGE,"E28.1.1"),subQ63,subQ62])]});var subQ68=sQuery(id+"F22.wireOp",EDGE,"E27.top");var subQ69=sQuery(id+"F22.wireOp",EDGE,"E27.bottom");var subQ70=sQuery(id+"F3.wireOp",EDGE,"E20.8.3");var subQ71=sQuery(id+"F3.wireOp",EDGE,"E20.8.1");var subQ74=makeQuery(id+"F42.boolean.opBoolean","COPY",FACE,{"disambiguationData":[TD([subQ67])],"derivedFrom":subQ8});var subQ75=makeQuery(id+"F24.boolean.opBoolean","INTERSECT",EDGE,{"derivedFrom":[makeQuery(id+"F1.opRevolve","SWEPT_FACE",FACE,{"disambiguationData":[OSD([sQuery(id+"F0.wireOp",EDGE,"E4")])]}),subQ67]});Q38=makeQuery(id+"F48.opFillet","BLEND_EDGE",EDGE,{"blendedFrom":[makeQuery(id+"F47.opFillet","TWEAK_EDGE",EDGE,{"derivedFrom":[makeQuery(id+"F45.opFillet","BLEND_VERTEX",VERTEX,{"blendedFrom":[subQ75,subQ67,subQ74],"blendedInto":[subQ67,subQ74]}),makeQuery(id+"F45.opFillet","BLEND_VERTEX",VERTEX,{"blendedFrom":[subQ75,makeQuery(id+"F42.boolean.opBoolean","MERGE",FACE,{"derivedFrom":[subQ2,subQ1]}),subQ74],"blendedInto":[makeQuery(id+"F42.boolean.opBoolean","MERGE",FACE,{"derivedFrom":[subQ2,subQ1]}),subQ74]})]}),makeQuery(id+"F47.opFillet","BLEND_FACE",FACE,{"disambiguationData":[OSD([subQ0,subQ7]),TDD([makeQuery(id+"F42.boolean.opBoolean","COPY",EDGE,{"disambiguationData":[TD([makeQuery(id+"F23.opLoft","SWEPT_FACE",FACE,{"disambiguationData":[OSD([sQuery(id+"F3.wireOp",EDGE,"E20.8.0"),subQ71,subQ70,subQ69,subQ68,sQuery(id+"F22.wireOp",EDGE,"E27.right")])]})])],"derivedFrom":subQ9})])]}),makeQuery(id+"F47.opFillet","BLEND_FACE",FACE,{"disambiguationData":[OSD([subQ0,subQ7]),TDD([makeQuery(id+"F42.boolean.opBoolean","COPY",EDGE,{"disambiguationData":[TD([subQ67])],"derivedFrom":subQ9})])]}),makeQuery(id+"F47.opFillet","BLEND_FACE",FACE,{"disambiguationData":[OSD([subQ0,subQ7]),TDD([makeQuery(id+"F42.boolean.opBoolean","COPY",EDGE,{"disambiguationData":[TD([makeQuery(id+"F25.opLoft","SWEPT_FACE",FACE,{"disambiguationData":[OSD([sQuery(id+"F3.wireOp",EDGE,"E20.10.0"),subQ61,subQ60,sQuery(id+"F22.wireOp",EDGE,"E28.2.1"),subQ59,subQ58])]})])],"derivedFrom":subQ9})])]}),makeQuery(id+"F47.opFillet","BLEND_FACE",FACE,{"disambiguationData":[OSD([subQ0,subQ7]),TDD([makeQuery(id+"F42.boolean.opBoolean","COPY",EDGE,{"disambiguationData":[TD([makeQuery(id+"F26.opLoft","SWEPT_FACE",FACE,{"disambiguationData":[OSD([sQuery(id+"F3.wireOp",EDGE,"E20.11.0"),subQ57,subQ56,sQuery(id+"F22.wireOp",EDGE,"E28.3.1"),subQ55,subQ54])]})])],"derivedFrom":subQ9})])]}),makeQuery(id+"F47.opFillet","BLEND_FACE",FACE,{"disambiguationData":[OSD([subQ0,subQ7]),TDD([makeQuery(id+"F42.boolean.opBoolean","COPY",EDGE,{"disambiguationData":[TD([makeQuery(id+"F27.opLoft","SWEPT_FACE",FACE,{"disambiguationData":[OSD([sQuery(id+"F3.wireOp",EDGE,"E20.12.0"),subQ53,subQ52,sQuery(id+"F22.wireOp",EDGE,"E28.4.1"),subQ51,subQ50])]})])],"derivedFrom":subQ9})])]}),makeQuery(id+"F47.opFillet","BLEND_FACE",FACE,{"disambiguationData":[OSD([subQ0,subQ7]),TDD([makeQuery(id+"F42.boolean.opBoolean","COPY",EDGE,{"disambiguationData":[TD([makeQuery(id+"F28.opLoft","SWEPT_FACE",FACE,{"disambiguationData":[OSD([sQuery(id+"F3.wireOp",EDGE,"E20.13.0"),subQ49,subQ48,sQuery(id+"F22.wireOp",EDGE,"E28.5.1"),subQ47,subQ46])]})])],"derivedFrom":subQ9})])]}),makeQuery(id+"F47.opFillet","BLEND_FACE",FACE,{"disambiguationData":[OSD([subQ0,subQ7]),TDD([makeQuery(id+"F42.boolean.opBoolean","COPY",EDGE,{"disambiguationData":[TD([makeQuery(id+"F29.opLoft","SWEPT_FACE",FACE,{"disambiguationData":[OSD([sQuery(id+"F3.wireOp",EDGE,"E20.14.0"),subQ45,subQ44,sQuery(id+"F22.wireOp",EDGE,"E28.6.1"),subQ43,subQ42])]})])],"derivedFrom":subQ9})])]}),makeQuery(id+"F47.opFillet","BLEND_FACE",FACE,{"disambiguationData":[OSD([subQ0,subQ7]),TDD([makeQuery(id+"F42.boolean.opBoolean","COPY",EDGE,{"disambiguationData":[TD([makeQuery(id+"F30.opLoft","SWEPT_FACE",FACE,{"disambiguationData":[OSD([sQuery(id+"F3.wireOp",EDGE,"E20.15.0"),subQ41,subQ40,sQuery(id+"F22.wireOp",EDGE,"E28.7.1"),subQ39,subQ38])]})])],"derivedFrom":subQ9})])]}),makeQuery(id+"F47.opFillet","BLEND_FACE",FACE,{"disambiguationData":[OSD([subQ0,subQ7]),TDD([makeQuery(id+"F42.boolean.opBoolean","COPY",EDGE,{"disambiguationData":[TD([makeQuery(id+"F31.opLoft","SWEPT_FACE",FACE,{"disambiguationData":[OSD([subQ37,subQ36,sQuery(id+"F3.wireOp",EDGE,"E18.left"),sQuery(id+"F22.wireOp",EDGE,"E28.8.1"),subQ35,subQ34])]})])],"derivedFrom":subQ9})])]}),makeQuery(id+"F47.opFillet","BLEND_FACE",FACE,{"disambiguationData":[OSD([subQ0,subQ7]),TDD([makeQuery(id+"F42.boolean.opBoolean","COPY",EDGE,{"disambiguationData":[TD([makeQuery(id+"F32.opLoft","SWEPT_FACE",FACE,{"disambiguationData":[OSD([sQuery(id+"F3.wireOp",EDGE,"E20.1.0"),subQ33,subQ32,sQuery(id+"F22.wireOp",EDGE,"E28.9.1"),subQ31,subQ30])]})])],"derivedFrom":subQ9})])]}),makeQuery(id+"F47.opFillet","BLEND_FACE",FACE,{"disambiguationData":[OSD([subQ0,subQ7]),TDD([makeQuery(id+"F42.boolean.opBoolean","COPY",EDGE,{"disambiguationData":[TD([makeQuery(id+"F33.opLoft","SWEPT_FACE",FACE,{"disambiguationData":[OSD([sQuery(id+"F3.wireOp",EDGE,"E20.2.0"),subQ29,subQ28,sQuery(id+"F22.wireOp",EDGE,"E28.10.1"),subQ27,subQ26])]})])],"derivedFrom":subQ9})])]}),makeQuery(id+"F47.opFillet","BLEND_FACE",FACE,{"disambiguationData":[OSD([subQ0,subQ7]),TDD([makeQuery(id+"F42.boolean.opBoolean","COPY",EDGE,{"disambiguationData":[TD([makeQuery(id+"F34.opLoft","SWEPT_FACE",FACE,{"disambiguationData":[OSD([sQuery(id+"F3.wireOp",EDGE,"E20.3.0"),subQ25,subQ24,sQuery(id+"F22.wireOp",EDGE,"E28.11.1"),subQ23,subQ22])]})])],"derivedFrom":subQ9})])]}),makeQuery(id+"F47.opFillet","BLEND_FACE",FACE,{"disambiguationData":[OSD([subQ0,subQ7]),TDD([makeQuery(id+"F42.boolean.opBoolean","COPY",EDGE,{"disambiguationData":[TD([makeQuery(id+"F35.opLoft","SWEPT_FACE",FACE,{"disambiguationData":[OSD([sQuery(id+"F3.wireOp",EDGE,"E20.4.0"),subQ21,subQ20,sQuery(id+"F22.wireOp",EDGE,"E28.12.1"),subQ19,subQ18])]})])],"derivedFrom":subQ9})])]}),makeQuery(id+"F47.opFillet","BLEND_FACE",FACE,{"disambiguationData":[OSD([subQ0,subQ7]),TDD([makeQuery(id+"F42.boolean.opBoolean","COPY",EDGE,{"disambiguationData":[TD([makeQuery(id+"F36.opLoft","SWEPT_FACE",FACE,{"disambiguationData":[OSD([sQuery(id+"F3.wireOp",EDGE,"E20.5.0"),subQ17,subQ16,sQuery(id+"F22.wireOp",EDGE,"E28.13.1"),subQ15,subQ14])]})])],"derivedFrom":subQ9})])]}),makeQuery(id+"F47.opFillet","BLEND_FACE",FACE,{"disambiguationData":[OSD([subQ0,subQ7]),TDD([makeQuery(id+"F42.boolean.opBoolean","COPY",EDGE,{"disambiguationData":[TD([makeQuery(id+"F37.opLoft","SWEPT_FACE",FACE,{"disambiguationData":[OSD([sQuery(id+"F3.wireOp",EDGE,"E20.6.0"),subQ13,subQ12,sQuery(id+"F22.wireOp",EDGE,"E28.14.1"),subQ11,subQ10])]})])],"derivedFrom":subQ9})])]}),makeQuery(id+"F47.opFillet","BLEND_FACE",FACE,{"disambiguationData":[OSD([subQ0,subQ7]),TDD([makeQuery(id+"F42.boolean.opBoolean","COPY",EDGE,{"disambiguationData":[TD([makeQuery(id+"F38.opLoft","SWEPT_FACE",FACE,{"disambiguationData":[OSD([sQuery(id+"F3.wireOp",EDGE,"E20.7.0"),subQ6,subQ5,sQuery(id+"F22.wireOp",EDGE,"E28.15.1"),subQ4,subQ3])]})])],"derivedFrom":subQ9})])]})],"blendedInto":[makeQuery(id+"F47.opFillet","BLEND_FACE",FACE,{"disambiguationData":[OSD([subQ0,subQ7]),TDD([makeQuery(id+"F42.boolean.opBoolean","COPY",EDGE,{"disambiguationData":[TD([makeQuery(id+"F23.opLoft","SWEPT_FACE",FACE,{"disambiguationData":[OSD([sQuery(id+"F3.wireOp",EDGE,"E20.8.0"),subQ71,subQ70,subQ69,subQ68,sQuery(id+"F22.wireOp",EDGE,"E27.right")])]})])],"derivedFrom":subQ9})])]}),makeQuery(id+"F47.opFillet","BLEND_FACE",FACE,{"disambiguationData":[OSD([subQ0,subQ7]),TDD([makeQuery(id+"F42.boolean.opBoolean","COPY",EDGE,{"disambiguationData":[TD([subQ67])],"derivedFrom":subQ9})])]}),makeQuery(id+"F47.opFillet","BLEND_FACE",FACE,{"disambiguationData":[OSD([subQ0,subQ7]),TDD([makeQuery(id+"F42.boolean.opBoolean","COPY",EDGE,{"disambiguationData":[TD([makeQuery(id+"F25.opLoft","SWEPT_FACE",FACE,{"disambiguationData":[OSD([sQuery(id+"F3.wireOp",EDGE,"E20.10.0"),subQ61,subQ60,sQuery(id+"F22.wireOp",EDGE,"E28.2.1"),subQ59,subQ58])]})])],"derivedFrom":subQ9})])]}),makeQuery(id+"F47.opFillet","BLEND_FACE",FACE,{"disambiguationData":[OSD([subQ0,subQ7]),TDD([makeQuery(id+"F42.boolean.opBoolean","COPY",EDGE,{"disambiguationData":[TD([makeQuery(id+"F26.opLoft","SWEPT_FACE",FACE,{"disambiguationData":[OSD([sQuery(id+"F3.wireOp",EDGE,"E20.11.0"),subQ57,subQ56,sQuery(id+"F22.wireOp",EDGE,"E28.3.1"),subQ55,subQ54])]})])],"derivedFrom":subQ9})])]}),makeQuery(id+"F47.opFillet","BLEND_FACE",FACE,{"disambiguationData":[OSD([subQ0,subQ7]),TDD([makeQuery(id+"F42.boolean.opBoolean","COPY",EDGE,{"disambiguationData":[TD([makeQuery(id+"F27.opLoft","SWEPT_FACE",FACE,{"disambiguationData":[OSD([sQuery(id+"F3.wireOp",EDGE,"E20.12.0"),subQ53,subQ52,sQuery(id+"F22.wireOp",EDGE,"E28.4.1"),subQ51,subQ50])]})])],"derivedFrom":subQ9})])]}),makeQuery(id+"F47.opFillet","BLEND_FACE",FACE,{"disambiguationData":[OSD([subQ0,subQ7]),TDD([makeQuery(id+"F42.boolean.opBoolean","COPY",EDGE,{"disambiguationData":[TD([makeQuery(id+"F28.opLoft","SWEPT_FACE",FACE,{"disambiguationData":[OSD([sQuery(id+"F3.wireOp",EDGE,"E20.13.0"),subQ49,subQ48,sQuery(id+"F22.wireOp",EDGE,"E28.5.1"),subQ47,subQ46])]})])],"derivedFrom":subQ9})])]}),makeQuery(id+"F47.opFillet","BLEND_FACE",FACE,{"disambiguationData":[OSD([subQ0,subQ7]),TDD([makeQuery(id+"F42.boolean.opBoolean","COPY",EDGE,{"disambiguationData":[TD([makeQuery(id+"F29.opLoft","SWEPT_FACE",FACE,{"disambiguationData":[OSD([sQuery(id+"F3.wireOp",EDGE,"E20.14.0"),subQ45,subQ44,sQuery(id+"F22.wireOp",EDGE,"E28.6.1"),subQ43,subQ42])]})])],"derivedFrom":subQ9})])]}),makeQuery(id+"F47.opFillet","BLEND_FACE",FACE,{"disambiguationData":[OSD([subQ0,subQ7]),TDD([makeQuery(id+"F42.boolean.opBoolean","COPY",EDGE,{"disambiguationData":[TD([makeQuery(id+"F30.opLoft","SWEPT_FACE",FACE,{"disambiguationData":[OSD([sQuery(id+"F3.wireOp",EDGE,"E20.15.0"),subQ41,subQ40,sQuery(id+"F22.wireOp",EDGE,"E28.7.1"),subQ39,subQ38])]})])],"derivedFrom":subQ9})])]}),makeQuery(id+"F47.opFillet","BLEND_FACE",FACE,{"disambiguationData":[OSD([subQ0,subQ7]),TDD([makeQuery(id+"F42.boolean.opBoolean","COPY",EDGE,{"disambiguationData":[TD([makeQuery(id+"F31.opLoft","SWEPT_FACE",FACE,{"disambiguationData":[OSD([subQ37,subQ36,sQuery(id+"F3.wireOp",EDGE,"E18.left"),sQuery(id+"F22.wireOp",EDGE,"E28.8.1"),subQ35,subQ34])]})])],"derivedFrom":subQ9})])]}),makeQuery(id+"F47.opFillet","BLEND_FACE",FACE,{"disambiguationData":[OSD([subQ0,subQ7]),TDD([makeQuery(id+"F42.boolean.opBoolean","COPY",EDGE,{"disambiguationData":[TD([makeQuery(id+"F32.opLoft","SWEPT_FACE",FACE,{"disambiguationData":[OSD([sQuery(id+"F3.wireOp",EDGE,"E20.1.0"),subQ33,subQ32,sQuery(id+"F22.wireOp",EDGE,"E28.9.1"),subQ31,subQ30])]})])],"derivedFrom":subQ9})])]}),makeQuery(id+"F47.opFillet","BLEND_FACE",FACE,{"disambiguationData":[OSD([subQ0,subQ7]),TDD([makeQuery(id+"F42.boolean.opBoolean","COPY",EDGE,{"disambiguationData":[TD([makeQuery(id+"F33.opLoft","SWEPT_FACE",FACE,{"disambiguationData":[OSD([sQuery(id+"F3.wireOp",EDGE,"E20.2.0"),subQ29,subQ28,sQuery(id+"F22.wireOp",EDGE,"E28.10.1"),subQ27,subQ26])]})])],"derivedFrom":subQ9})])]}),makeQuery(id+"F47.opFillet","BLEND_FACE",FACE,{"disambiguationData":[OSD([subQ0,subQ7]),TDD([makeQuery(id+"F42.boolean.opBoolean","COPY",EDGE,{"disambiguationData":[TD([makeQuery(id+"F34.opLoft","SWEPT_FACE",FACE,{"disambiguationData":[OSD([sQuery(id+"F3.wireOp",EDGE,"E20.3.0"),subQ25,subQ24,sQuery(id+"F22.wireOp",EDGE,"E28.11.1"),subQ23,subQ22])]})])],"derivedFrom":subQ9})])]}),makeQuery(id+"F47.opFillet","BLEND_FACE",FACE,{"disambiguationData":[OSD([subQ0,subQ7]),TDD([makeQuery(id+"F42.boolean.opBoolean","COPY",EDGE,{"disambiguationData":[TD([makeQuery(id+"F35.opLoft","SWEPT_FACE",FACE,{"disambiguationData":[OSD([sQuery(id+"F3.wireOp",EDGE,"E20.4.0"),subQ21,subQ20,sQuery(id+"F22.wireOp",EDGE,"E28.12.1"),subQ19,subQ18])]})])],"derivedFrom":subQ9})])]}),makeQuery(id+"F47.opFillet","BLEND_FACE",FACE,{"disambiguationData":[OSD([subQ0,subQ7]),TDD([makeQuery(id+"F42.boolean.opBoolean","COPY",EDGE,{"disambiguationData":[TD([makeQuery(id+"F36.opLoft","SWEPT_FACE",FACE,{"disambiguationData":[OSD([sQuery(id+"F3.wireOp",EDGE,"E20.5.0"),subQ17,subQ16,sQuery(id+"F22.wireOp",EDGE,"E28.13.1"),subQ15,subQ14])]})])],"derivedFrom":subQ9})])]}),makeQuery(id+"F47.opFillet","BLEND_FACE",FACE,{"disambiguationData":[OSD([subQ0,subQ7]),TDD([makeQuery(id+"F42.boolean.opBoolean","COPY",EDGE,{"disambiguationData":[TD([makeQuery(id+"F37.opLoft","SWEPT_FACE",FACE,{"disambiguationData":[OSD([sQuery(id+"F3.wireOp",EDGE,"E20.6.0"),subQ13,subQ12,sQuery(id+"F22.wireOp",EDGE,"E28.14.1"),subQ11,subQ10])]})])],"derivedFrom":subQ9})])]}),makeQuery(id+"F47.opFillet","BLEND_FACE",FACE,{"disambiguationData":[OSD([subQ0,subQ7]),TDD([makeQuery(id+"F42.boolean.opBoolean","COPY",EDGE,{"disambiguationData":[TD([makeQuery(id+"F38.opLoft","SWEPT_FACE",FACE,{"disambiguationData":[OSD([sQuery(id+"F3.wireOp",EDGE,"E20.7.0"),subQ6,subQ5,sQuery(id+"F22.wireOp",EDGE,"E28.15.1"),subQ4,subQ3])]})])],"derivedFrom":subQ9})])]})]});}
            var Q39;
            {var subQ0=sQuery(id+"F22.wireOp",EDGE,"E28.1.0");var subQ1=sQuery(id+"F22.wireOp",EDGE,"E28.1.1");var subQ2=sQuery(id+"F22.wireOp",EDGE,"E28.1.2");var subQ3=sQuery(id+"F22.wireOp",EDGE,"E28.1.3");var subQ4=sQuery(id+"F3.wireOp",EDGE,"E20.9.3");var subQ5=sQuery(id+"F3.wireOp",EDGE,"E20.9.1");var subQ6=makeQuery(id+"F24.opLoft","SWEPT_FACE",FACE,{"disambiguationData":[OSD([subQ5,sQuery(id+"F3.wireOp",EDGE,"E20.9.2"),subQ4,subQ0,subQ2,subQ3])]});var subQ7=sQuery(id+"F41.wireOp",EDGE,"E34");var subQ8=sQuery(id+"F41.wireOp",EDGE,"E32");Q39=makeQuery(id+"F44.opFillet","BLEND_EDGE",EDGE,{"blendedFrom":[makeQuery(id+"F40.boolean.opBoolean","INTERSECT",EDGE,{"derivedFrom":[subQ6,makeQuery(id+"F40.opExtrude","CAP_FACE",FACE,{"disambiguationData":[OSD([sQuery(id+"F39.wireOp",EDGE,"E29"),sQuery(id+"F39.wireOp",EDGE,"E30")])],"isStart":true})]}),makeQuery(id+"F42.boolean.opBoolean","COPY",FACE,{"disambiguationData":[TD([makeQuery(id+"F24.opLoft","SWEPT_FACE",FACE,{"disambiguationData":[OSD([sQuery(id+"F3.wireOp",EDGE,"E20.9.0"),subQ5,subQ4,subQ1,subQ2,subQ3])]})])],"derivedFrom":makeQuery(id+"F42.opRevolve","SWEPT_FACE",FACE,{"disambiguationData":[OSD([subQ8]),TDD([makeQuery(id+"F41.imprint","IMPRINT",EDGE,{"disambiguationData":[TD([[makeQuery(id+"F41.imprint","INTERSECT",VERTEX,{"disambiguationData":[OD(0.0)],"derivedFrom":[subQ8,subQ7]}),-1.0]])],"derivedFrom":subQ8})])]})})],"blendedInto":[makeQuery(id+"F42.boolean.opBoolean","COPY",FACE,{"disambiguationData":[TD([makeQuery(id+"F24.opLoft","SWEPT_FACE",FACE,{"disambiguationData":[OSD([sQuery(id+"F3.wireOp",EDGE,"E20.9.0"),subQ5,subQ4,subQ1,subQ2,subQ3])]})])],"derivedFrom":makeQuery(id+"F42.opRevolve","SWEPT_FACE",FACE,{"disambiguationData":[OSD([subQ8]),TDD([makeQuery(id+"F41.imprint","IMPRINT",EDGE,{"disambiguationData":[TD([[makeQuery(id+"F41.imprint","INTERSECT",VERTEX,{"disambiguationData":[OD(0.0)],"derivedFrom":[subQ8,subQ7]}),-1.0]])],"derivedFrom":subQ8})])]})})]});}
            var Q40;
            {var subQ0=sQuery(id+"F41.wireOp",EDGE,"E34");var subQ1=sQuery(id+"F41.wireOp",EDGE,"E32");Q40=makeQuery(id+"F42.boolean.opBoolean","INTERSECT",EDGE,{"derivedFrom":[makeQuery(id+"F23.opLoft","SWEPT_FACE",FACE,{"disambiguationData":[OSD([sQuery(id+"F3.wireOp",EDGE,"E20.8.0"),sQuery(id+"F3.wireOp",EDGE,"E20.8.1"),sQuery(id+"F3.wireOp",EDGE,"E20.8.3"),sQuery(id+"F22.wireOp",EDGE,"E27.bottom"),sQuery(id+"F22.wireOp",EDGE,"E27.top"),sQuery(id+"F22.wireOp",EDGE,"E27.right")])]}),makeQuery(id+"F42.opRevolve","SWEPT_FACE",FACE,{"disambiguationData":[OSD([subQ1]),TDD([makeQuery(id+"F41.imprint","IMPRINT",EDGE,{"disambiguationData":[TD([[makeQuery(id+"F41.imprint","INTERSECT",VERTEX,{"disambiguationData":[OD(0.0)],"derivedFrom":[subQ1,subQ0]}),-1.0]])],"derivedFrom":subQ1})])]})]});}
            var Q41;
            {var subQ0=sQuery(id+"F41.wireOp",EDGE,"E37");var subQ1=makeQuery(id+"F42.opRevolve","SWEPT_FACE",FACE,{"disambiguationData":[OSD([subQ0])]});var subQ2=makeQuery(id+"F40.opExtrude","CAP_FACE",FACE,{"disambiguationData":[OSD([sQuery(id+"F39.wireOp",EDGE,"E29"),sQuery(id+"F39.wireOp",EDGE,"E30")])],"isStart":true});var subQ3=sQuery(id+"F22.wireOp",EDGE,"E28.15.3");var subQ4=sQuery(id+"F22.wireOp",EDGE,"E28.15.2");var subQ5=sQuery(id+"F3.wireOp",EDGE,"E20.7.3");var subQ6=sQuery(id+"F3.wireOp",EDGE,"E20.7.1");var subQ7=sQuery(id+"F41.wireOp",EDGE,"E38");var subQ8=makeQuery(id+"F42.opRevolve","SWEPT_FACE",FACE,{"disambiguationData":[OSD([subQ7])]});var subQ9=makeQuery(id+"F42.opRevolve","SWEPT_EDGE",EDGE,{"disambiguationData":[OSD([subQ0,subQ7])]});var subQ10=sQuery(id+"F22.wireOp",EDGE,"E28.14.3");var subQ11=sQuery(id+"F22.wireOp",EDGE,"E28.14.2");var subQ12=sQuery(id+"F3.wireOp",EDGE,"E20.6.3");var subQ13=sQuery(id+"F3.wireOp",EDGE,"E20.6.1");var subQ14=sQuery(id+"F22.wireOp",EDGE,"E28.13.3");var subQ15=sQuery(id+"F22.wireOp",EDGE,"E28.13.2");var subQ16=sQuery(id+"F3.wireOp",EDGE,"E20.5.3");var subQ17=sQuery(id+"F3.wireOp",EDGE,"E20.5.1");var subQ18=sQuery(id+"F22.wireOp",EDGE,"E28.12.3");var subQ19=sQuery(id+"F22.wireOp",EDGE,"E28.12.2");var subQ20=sQuery(id+"F3.wireOp",EDGE,"E20.4.3");var subQ21=sQuery(id+"F3.wireOp",EDGE,"E20.4.1");var subQ22=sQuery(id+"F22.wireOp",EDGE,"E28.11.3");var subQ23=sQuery(id+"F22.wireOp",EDGE,"E28.11.2");var subQ24=sQuery(id+"F3.wireOp",EDGE,"E20.3.3");var subQ25=sQuery(id+"F3.wireOp",EDGE,"E20.3.1");var subQ26=sQuery(id+"F22.wireOp",EDGE,"E28.10.3");var subQ27=sQuery(id+"F22.wireOp",EDGE,"E28.10.2");var subQ28=sQuery(id+"F3.wireOp",EDGE,"E20.2.3");var subQ29=sQuery(id+"F3.wireOp",EDGE,"E20.2.1");var subQ30=sQuery(id+"F22.wireOp",EDGE,"E28.9.3");var subQ31=sQuery(id+"F22.wireOp",EDGE,"E28.9.2");var subQ32=sQuery(id+"F3.wireOp",EDGE,"E20.1.3");var subQ33=sQuery(id+"F3.wireOp",EDGE,"E20.1.1");var subQ34=sQuery(id+"F22.wireOp",EDGE,"E28.8.3");var subQ35=sQuery(id+"F22.wireOp",EDGE,"E28.8.2");var subQ36=sQuery(id+"F3.wireOp",EDGE,"E18.top");var subQ37=sQuery(id+"F3.wireOp",EDGE,"E18.bottom");var subQ38=sQuery(id+"F22.wireOp",EDGE,"E28.7.3");var subQ39=sQuery(id+"F22.wireOp",EDGE,"E28.7.2");var subQ40=sQuery(id+"F3.wireOp",EDGE,"E20.15.3");var subQ41=sQuery(id+"F3.wireOp",EDGE,"E20.15.1");var subQ42=sQuery(id+"F22.wireOp",EDGE,"E28.6.3");var subQ43=sQuery(id+"F22.wireOp",EDGE,"E28.6.2");var subQ44=sQuery(id+"F3.wireOp",EDGE,"E20.14.3");var subQ45=sQuery(id+"F3.wireOp",EDGE,"E20.14.1");var subQ46=sQuery(id+"F22.wireOp",EDGE,"E28.5.3");var subQ47=sQuery(id+"F22.wireOp",EDGE,"E28.5.2");var subQ48=sQuery(id+"F3.wireOp",EDGE,"E20.13.3");var subQ49=sQuery(id+"F3.wireOp",EDGE,"E20.13.1");var subQ50=sQuery(id+"F22.wireOp",EDGE,"E28.4.3");var subQ51=sQuery(id+"F22.wireOp",EDGE,"E28.4.2");var subQ52=sQuery(id+"F3.wireOp",EDGE,"E20.12.3");var subQ53=sQuery(id+"F3.wireOp",EDGE,"E20.12.1");var subQ54=sQuery(id+"F22.wireOp",EDGE,"E28.3.3");var subQ55=sQuery(id+"F22.wireOp",EDGE,"E28.3.2");var subQ56=sQuery(id+"F3.wireOp",EDGE,"E20.11.3");var subQ57=sQuery(id+"F3.wireOp",EDGE,"E20.11.1");var subQ58=sQuery(id+"F22.wireOp",EDGE,"E28.2.3");var subQ59=sQuery(id+"F22.wireOp",EDGE,"E28.2.2");var subQ60=sQuery(id+"F3.wireOp",EDGE,"E20.10.3");var subQ61=sQuery(id+"F3.wireOp",EDGE,"E20.10.1");var subQ62=sQuery(id+"F22.wireOp",EDGE,"E28.1.3");var subQ63=sQuery(id+"F22.wireOp",EDGE,"E28.1.2");var subQ64=sQuery(id+"F3.wireOp",EDGE,"E20.9.3");var subQ65=sQuery(id+"F3.wireOp",EDGE,"E20.9.1");var subQ66=sQuery(id+"F22.wireOp",EDGE,"E27.top");var subQ67=sQuery(id+"F22.wireOp",EDGE,"E27.bottom");var subQ68=sQuery(id+"F3.wireOp",EDGE,"E20.8.3");var subQ69=sQuery(id+"F3.wireOp",EDGE,"E20.8.1");var subQ71=makeQuery(id+"F23.opLoft","SWEPT_FACE",FACE,{"disambiguationData":[OSD([sQuery(id+"F3.wireOp",EDGE,"E20.8.0"),subQ69,subQ68,subQ67,subQ66,sQuery(id+"F22.wireOp",EDGE,"E27.right")])]});var subQ74=makeQuery(id+"F42.boolean.opBoolean","COPY",FACE,{"disambiguationData":[TD([subQ71])],"derivedFrom":subQ8});var subQ75=makeQuery(id+"F23.boolean.opBoolean","INTERSECT",EDGE,{"derivedFrom":[makeQuery(id+"F1.opRevolve","SWEPT_FACE",FACE,{"disambiguationData":[OSD([sQuery(id+"F0.wireOp",EDGE,"E4")])]}),subQ71]});Q41=makeQuery(id+"F48.opFillet","BLEND_EDGE",EDGE,{"blendedFrom":[makeQuery(id+"F47.opFillet","TWEAK_EDGE",EDGE,{"derivedFrom":[makeQuery(id+"F45.opFillet","BLEND_VERTEX",VERTEX,{"blendedFrom":[subQ75,subQ71,subQ74],"blendedInto":[subQ71,subQ74]}),makeQuery(id+"F45.opFillet","BLEND_VERTEX",VERTEX,{"blendedFrom":[subQ75,makeQuery(id+"F42.boolean.opBoolean","MERGE",FACE,{"derivedFrom":[subQ2,subQ1]}),subQ74],"blendedInto":[makeQuery(id+"F42.boolean.opBoolean","MERGE",FACE,{"derivedFrom":[subQ2,subQ1]}),subQ74]})]}),makeQuery(id+"F47.opFillet","BLEND_FACE",FACE,{"disambiguationData":[OSD([subQ0,subQ7]),TDD([makeQuery(id+"F42.boolean.opBoolean","COPY",EDGE,{"disambiguationData":[TD([subQ71])],"derivedFrom":subQ9})])]}),makeQuery(id+"F47.opFillet","BLEND_FACE",FACE,{"disambiguationData":[OSD([subQ0,subQ7]),TDD([makeQuery(id+"F42.boolean.opBoolean","COPY",EDGE,{"disambiguationData":[TD([makeQuery(id+"F24.opLoft","SWEPT_FACE",FACE,{"disambiguationData":[OSD([sQuery(id+"F3.wireOp",EDGE,"E20.9.0"),subQ65,subQ64,sQuery(id+"F22.wireOp",EDGE,"E28.1.1"),subQ63,subQ62])]})])],"derivedFrom":subQ9})])]}),makeQuery(id+"F47.opFillet","BLEND_FACE",FACE,{"disambiguationData":[OSD([subQ0,subQ7]),TDD([makeQuery(id+"F42.boolean.opBoolean","COPY",EDGE,{"disambiguationData":[TD([makeQuery(id+"F25.opLoft","SWEPT_FACE",FACE,{"disambiguationData":[OSD([sQuery(id+"F3.wireOp",EDGE,"E20.10.0"),subQ61,subQ60,sQuery(id+"F22.wireOp",EDGE,"E28.2.1"),subQ59,subQ58])]})])],"derivedFrom":subQ9})])]}),makeQuery(id+"F47.opFillet","BLEND_FACE",FACE,{"disambiguationData":[OSD([subQ0,subQ7]),TDD([makeQuery(id+"F42.boolean.opBoolean","COPY",EDGE,{"disambiguationData":[TD([makeQuery(id+"F26.opLoft","SWEPT_FACE",FACE,{"disambiguationData":[OSD([sQuery(id+"F3.wireOp",EDGE,"E20.11.0"),subQ57,subQ56,sQuery(id+"F22.wireOp",EDGE,"E28.3.1"),subQ55,subQ54])]})])],"derivedFrom":subQ9})])]}),makeQuery(id+"F47.opFillet","BLEND_FACE",FACE,{"disambiguationData":[OSD([subQ0,subQ7]),TDD([makeQuery(id+"F42.boolean.opBoolean","COPY",EDGE,{"disambiguationData":[TD([makeQuery(id+"F27.opLoft","SWEPT_FACE",FACE,{"disambiguationData":[OSD([sQuery(id+"F3.wireOp",EDGE,"E20.12.0"),subQ53,subQ52,sQuery(id+"F22.wireOp",EDGE,"E28.4.1"),subQ51,subQ50])]})])],"derivedFrom":subQ9})])]}),makeQuery(id+"F47.opFillet","BLEND_FACE",FACE,{"disambiguationData":[OSD([subQ0,subQ7]),TDD([makeQuery(id+"F42.boolean.opBoolean","COPY",EDGE,{"disambiguationData":[TD([makeQuery(id+"F28.opLoft","SWEPT_FACE",FACE,{"disambiguationData":[OSD([sQuery(id+"F3.wireOp",EDGE,"E20.13.0"),subQ49,subQ48,sQuery(id+"F22.wireOp",EDGE,"E28.5.1"),subQ47,subQ46])]})])],"derivedFrom":subQ9})])]}),makeQuery(id+"F47.opFillet","BLEND_FACE",FACE,{"disambiguationData":[OSD([subQ0,subQ7]),TDD([makeQuery(id+"F42.boolean.opBoolean","COPY",EDGE,{"disambiguationData":[TD([makeQuery(id+"F29.opLoft","SWEPT_FACE",FACE,{"disambiguationData":[OSD([sQuery(id+"F3.wireOp",EDGE,"E20.14.0"),subQ45,subQ44,sQuery(id+"F22.wireOp",EDGE,"E28.6.1"),subQ43,subQ42])]})])],"derivedFrom":subQ9})])]}),makeQuery(id+"F47.opFillet","BLEND_FACE",FACE,{"disambiguationData":[OSD([subQ0,subQ7]),TDD([makeQuery(id+"F42.boolean.opBoolean","COPY",EDGE,{"disambiguationData":[TD([makeQuery(id+"F30.opLoft","SWEPT_FACE",FACE,{"disambiguationData":[OSD([sQuery(id+"F3.wireOp",EDGE,"E20.15.0"),subQ41,subQ40,sQuery(id+"F22.wireOp",EDGE,"E28.7.1"),subQ39,subQ38])]})])],"derivedFrom":subQ9})])]}),makeQuery(id+"F47.opFillet","BLEND_FACE",FACE,{"disambiguationData":[OSD([subQ0,subQ7]),TDD([makeQuery(id+"F42.boolean.opBoolean","COPY",EDGE,{"disambiguationData":[TD([makeQuery(id+"F31.opLoft","SWEPT_FACE",FACE,{"disambiguationData":[OSD([subQ37,subQ36,sQuery(id+"F3.wireOp",EDGE,"E18.left"),sQuery(id+"F22.wireOp",EDGE,"E28.8.1"),subQ35,subQ34])]})])],"derivedFrom":subQ9})])]}),makeQuery(id+"F47.opFillet","BLEND_FACE",FACE,{"disambiguationData":[OSD([subQ0,subQ7]),TDD([makeQuery(id+"F42.boolean.opBoolean","COPY",EDGE,{"disambiguationData":[TD([makeQuery(id+"F32.opLoft","SWEPT_FACE",FACE,{"disambiguationData":[OSD([sQuery(id+"F3.wireOp",EDGE,"E20.1.0"),subQ33,subQ32,sQuery(id+"F22.wireOp",EDGE,"E28.9.1"),subQ31,subQ30])]})])],"derivedFrom":subQ9})])]}),makeQuery(id+"F47.opFillet","BLEND_FACE",FACE,{"disambiguationData":[OSD([subQ0,subQ7]),TDD([makeQuery(id+"F42.boolean.opBoolean","COPY",EDGE,{"disambiguationData":[TD([makeQuery(id+"F33.opLoft","SWEPT_FACE",FACE,{"disambiguationData":[OSD([sQuery(id+"F3.wireOp",EDGE,"E20.2.0"),subQ29,subQ28,sQuery(id+"F22.wireOp",EDGE,"E28.10.1"),subQ27,subQ26])]})])],"derivedFrom":subQ9})])]}),makeQuery(id+"F47.opFillet","BLEND_FACE",FACE,{"disambiguationData":[OSD([subQ0,subQ7]),TDD([makeQuery(id+"F42.boolean.opBoolean","COPY",EDGE,{"disambiguationData":[TD([makeQuery(id+"F34.opLoft","SWEPT_FACE",FACE,{"disambiguationData":[OSD([sQuery(id+"F3.wireOp",EDGE,"E20.3.0"),subQ25,subQ24,sQuery(id+"F22.wireOp",EDGE,"E28.11.1"),subQ23,subQ22])]})])],"derivedFrom":subQ9})])]}),makeQuery(id+"F47.opFillet","BLEND_FACE",FACE,{"disambiguationData":[OSD([subQ0,subQ7]),TDD([makeQuery(id+"F42.boolean.opBoolean","COPY",EDGE,{"disambiguationData":[TD([makeQuery(id+"F35.opLoft","SWEPT_FACE",FACE,{"disambiguationData":[OSD([sQuery(id+"F3.wireOp",EDGE,"E20.4.0"),subQ21,subQ20,sQuery(id+"F22.wireOp",EDGE,"E28.12.1"),subQ19,subQ18])]})])],"derivedFrom":subQ9})])]}),makeQuery(id+"F47.opFillet","BLEND_FACE",FACE,{"disambiguationData":[OSD([subQ0,subQ7]),TDD([makeQuery(id+"F42.boolean.opBoolean","COPY",EDGE,{"disambiguationData":[TD([makeQuery(id+"F36.opLoft","SWEPT_FACE",FACE,{"disambiguationData":[OSD([sQuery(id+"F3.wireOp",EDGE,"E20.5.0"),subQ17,subQ16,sQuery(id+"F22.wireOp",EDGE,"E28.13.1"),subQ15,subQ14])]})])],"derivedFrom":subQ9})])]}),makeQuery(id+"F47.opFillet","BLEND_FACE",FACE,{"disambiguationData":[OSD([subQ0,subQ7]),TDD([makeQuery(id+"F42.boolean.opBoolean","COPY",EDGE,{"disambiguationData":[TD([makeQuery(id+"F37.opLoft","SWEPT_FACE",FACE,{"disambiguationData":[OSD([sQuery(id+"F3.wireOp",EDGE,"E20.6.0"),subQ13,subQ12,sQuery(id+"F22.wireOp",EDGE,"E28.14.1"),subQ11,subQ10])]})])],"derivedFrom":subQ9})])]}),makeQuery(id+"F47.opFillet","BLEND_FACE",FACE,{"disambiguationData":[OSD([subQ0,subQ7]),TDD([makeQuery(id+"F42.boolean.opBoolean","COPY",EDGE,{"disambiguationData":[TD([makeQuery(id+"F38.opLoft","SWEPT_FACE",FACE,{"disambiguationData":[OSD([sQuery(id+"F3.wireOp",EDGE,"E20.7.0"),subQ6,subQ5,sQuery(id+"F22.wireOp",EDGE,"E28.15.1"),subQ4,subQ3])]})])],"derivedFrom":subQ9})])]})],"blendedInto":[makeQuery(id+"F47.opFillet","BLEND_FACE",FACE,{"disambiguationData":[OSD([subQ0,subQ7]),TDD([makeQuery(id+"F42.boolean.opBoolean","COPY",EDGE,{"disambiguationData":[TD([subQ71])],"derivedFrom":subQ9})])]}),makeQuery(id+"F47.opFillet","BLEND_FACE",FACE,{"disambiguationData":[OSD([subQ0,subQ7]),TDD([makeQuery(id+"F42.boolean.opBoolean","COPY",EDGE,{"disambiguationData":[TD([makeQuery(id+"F24.opLoft","SWEPT_FACE",FACE,{"disambiguationData":[OSD([sQuery(id+"F3.wireOp",EDGE,"E20.9.0"),subQ65,subQ64,sQuery(id+"F22.wireOp",EDGE,"E28.1.1"),subQ63,subQ62])]})])],"derivedFrom":subQ9})])]}),makeQuery(id+"F47.opFillet","BLEND_FACE",FACE,{"disambiguationData":[OSD([subQ0,subQ7]),TDD([makeQuery(id+"F42.boolean.opBoolean","COPY",EDGE,{"disambiguationData":[TD([makeQuery(id+"F25.opLoft","SWEPT_FACE",FACE,{"disambiguationData":[OSD([sQuery(id+"F3.wireOp",EDGE,"E20.10.0"),subQ61,subQ60,sQuery(id+"F22.wireOp",EDGE,"E28.2.1"),subQ59,subQ58])]})])],"derivedFrom":subQ9})])]}),makeQuery(id+"F47.opFillet","BLEND_FACE",FACE,{"disambiguationData":[OSD([subQ0,subQ7]),TDD([makeQuery(id+"F42.boolean.opBoolean","COPY",EDGE,{"disambiguationData":[TD([makeQuery(id+"F26.opLoft","SWEPT_FACE",FACE,{"disambiguationData":[OSD([sQuery(id+"F3.wireOp",EDGE,"E20.11.0"),subQ57,subQ56,sQuery(id+"F22.wireOp",EDGE,"E28.3.1"),subQ55,subQ54])]})])],"derivedFrom":subQ9})])]}),makeQuery(id+"F47.opFillet","BLEND_FACE",FACE,{"disambiguationData":[OSD([subQ0,subQ7]),TDD([makeQuery(id+"F42.boolean.opBoolean","COPY",EDGE,{"disambiguationData":[TD([makeQuery(id+"F27.opLoft","SWEPT_FACE",FACE,{"disambiguationData":[OSD([sQuery(id+"F3.wireOp",EDGE,"E20.12.0"),subQ53,subQ52,sQuery(id+"F22.wireOp",EDGE,"E28.4.1"),subQ51,subQ50])]})])],"derivedFrom":subQ9})])]}),makeQuery(id+"F47.opFillet","BLEND_FACE",FACE,{"disambiguationData":[OSD([subQ0,subQ7]),TDD([makeQuery(id+"F42.boolean.opBoolean","COPY",EDGE,{"disambiguationData":[TD([makeQuery(id+"F28.opLoft","SWEPT_FACE",FACE,{"disambiguationData":[OSD([sQuery(id+"F3.wireOp",EDGE,"E20.13.0"),subQ49,subQ48,sQuery(id+"F22.wireOp",EDGE,"E28.5.1"),subQ47,subQ46])]})])],"derivedFrom":subQ9})])]}),makeQuery(id+"F47.opFillet","BLEND_FACE",FACE,{"disambiguationData":[OSD([subQ0,subQ7]),TDD([makeQuery(id+"F42.boolean.opBoolean","COPY",EDGE,{"disambiguationData":[TD([makeQuery(id+"F29.opLoft","SWEPT_FACE",FACE,{"disambiguationData":[OSD([sQuery(id+"F3.wireOp",EDGE,"E20.14.0"),subQ45,subQ44,sQuery(id+"F22.wireOp",EDGE,"E28.6.1"),subQ43,subQ42])]})])],"derivedFrom":subQ9})])]}),makeQuery(id+"F47.opFillet","BLEND_FACE",FACE,{"disambiguationData":[OSD([subQ0,subQ7]),TDD([makeQuery(id+"F42.boolean.opBoolean","COPY",EDGE,{"disambiguationData":[TD([makeQuery(id+"F30.opLoft","SWEPT_FACE",FACE,{"disambiguationData":[OSD([sQuery(id+"F3.wireOp",EDGE,"E20.15.0"),subQ41,subQ40,sQuery(id+"F22.wireOp",EDGE,"E28.7.1"),subQ39,subQ38])]})])],"derivedFrom":subQ9})])]}),makeQuery(id+"F47.opFillet","BLEND_FACE",FACE,{"disambiguationData":[OSD([subQ0,subQ7]),TDD([makeQuery(id+"F42.boolean.opBoolean","COPY",EDGE,{"disambiguationData":[TD([makeQuery(id+"F31.opLoft","SWEPT_FACE",FACE,{"disambiguationData":[OSD([subQ37,subQ36,sQuery(id+"F3.wireOp",EDGE,"E18.left"),sQuery(id+"F22.wireOp",EDGE,"E28.8.1"),subQ35,subQ34])]})])],"derivedFrom":subQ9})])]}),makeQuery(id+"F47.opFillet","BLEND_FACE",FACE,{"disambiguationData":[OSD([subQ0,subQ7]),TDD([makeQuery(id+"F42.boolean.opBoolean","COPY",EDGE,{"disambiguationData":[TD([makeQuery(id+"F32.opLoft","SWEPT_FACE",FACE,{"disambiguationData":[OSD([sQuery(id+"F3.wireOp",EDGE,"E20.1.0"),subQ33,subQ32,sQuery(id+"F22.wireOp",EDGE,"E28.9.1"),subQ31,subQ30])]})])],"derivedFrom":subQ9})])]}),makeQuery(id+"F47.opFillet","BLEND_FACE",FACE,{"disambiguationData":[OSD([subQ0,subQ7]),TDD([makeQuery(id+"F42.boolean.opBoolean","COPY",EDGE,{"disambiguationData":[TD([makeQuery(id+"F33.opLoft","SWEPT_FACE",FACE,{"disambiguationData":[OSD([sQuery(id+"F3.wireOp",EDGE,"E20.2.0"),subQ29,subQ28,sQuery(id+"F22.wireOp",EDGE,"E28.10.1"),subQ27,subQ26])]})])],"derivedFrom":subQ9})])]}),makeQuery(id+"F47.opFillet","BLEND_FACE",FACE,{"disambiguationData":[OSD([subQ0,subQ7]),TDD([makeQuery(id+"F42.boolean.opBoolean","COPY",EDGE,{"disambiguationData":[TD([makeQuery(id+"F34.opLoft","SWEPT_FACE",FACE,{"disambiguationData":[OSD([sQuery(id+"F3.wireOp",EDGE,"E20.3.0"),subQ25,subQ24,sQuery(id+"F22.wireOp",EDGE,"E28.11.1"),subQ23,subQ22])]})])],"derivedFrom":subQ9})])]}),makeQuery(id+"F47.opFillet","BLEND_FACE",FACE,{"disambiguationData":[OSD([subQ0,subQ7]),TDD([makeQuery(id+"F42.boolean.opBoolean","COPY",EDGE,{"disambiguationData":[TD([makeQuery(id+"F35.opLoft","SWEPT_FACE",FACE,{"disambiguationData":[OSD([sQuery(id+"F3.wireOp",EDGE,"E20.4.0"),subQ21,subQ20,sQuery(id+"F22.wireOp",EDGE,"E28.12.1"),subQ19,subQ18])]})])],"derivedFrom":subQ9})])]}),makeQuery(id+"F47.opFillet","BLEND_FACE",FACE,{"disambiguationData":[OSD([subQ0,subQ7]),TDD([makeQuery(id+"F42.boolean.opBoolean","COPY",EDGE,{"disambiguationData":[TD([makeQuery(id+"F36.opLoft","SWEPT_FACE",FACE,{"disambiguationData":[OSD([sQuery(id+"F3.wireOp",EDGE,"E20.5.0"),subQ17,subQ16,sQuery(id+"F22.wireOp",EDGE,"E28.13.1"),subQ15,subQ14])]})])],"derivedFrom":subQ9})])]}),makeQuery(id+"F47.opFillet","BLEND_FACE",FACE,{"disambiguationData":[OSD([subQ0,subQ7]),TDD([makeQuery(id+"F42.boolean.opBoolean","COPY",EDGE,{"disambiguationData":[TD([makeQuery(id+"F37.opLoft","SWEPT_FACE",FACE,{"disambiguationData":[OSD([sQuery(id+"F3.wireOp",EDGE,"E20.6.0"),subQ13,subQ12,sQuery(id+"F22.wireOp",EDGE,"E28.14.1"),subQ11,subQ10])]})])],"derivedFrom":subQ9})])]}),makeQuery(id+"F47.opFillet","BLEND_FACE",FACE,{"disambiguationData":[OSD([subQ0,subQ7]),TDD([makeQuery(id+"F42.boolean.opBoolean","COPY",EDGE,{"disambiguationData":[TD([makeQuery(id+"F38.opLoft","SWEPT_FACE",FACE,{"disambiguationData":[OSD([sQuery(id+"F3.wireOp",EDGE,"E20.7.0"),subQ6,subQ5,sQuery(id+"F22.wireOp",EDGE,"E28.15.1"),subQ4,subQ3])]})])],"derivedFrom":subQ9})])]})]});}
            var Q42;
            {var subQ0=sQuery(id+"F22.wireOp",EDGE,"E27.left");var subQ1=sQuery(id+"F22.wireOp",EDGE,"E27.top");var subQ2=sQuery(id+"F22.wireOp",EDGE,"E27.bottom");var subQ3=sQuery(id+"F3.wireOp",EDGE,"E20.8.3");var subQ4=sQuery(id+"F3.wireOp",EDGE,"E20.8.1");var subQ5=makeQuery(id+"F23.opLoft","SWEPT_FACE",FACE,{"disambiguationData":[OSD([subQ4,sQuery(id+"F3.wireOp",EDGE,"E20.8.2"),subQ3,subQ2,subQ1,subQ0])]});var subQ6=sQuery(id+"F22.wireOp",EDGE,"E27.right");var subQ7=sQuery(id+"F41.wireOp",EDGE,"E34");var subQ8=sQuery(id+"F41.wireOp",EDGE,"E32");Q42=makeQuery(id+"F44.opFillet","BLEND_EDGE",EDGE,{"blendedFrom":[makeQuery(id+"F40.boolean.opBoolean","INTERSECT",EDGE,{"derivedFrom":[subQ5,makeQuery(id+"F40.opExtrude","CAP_FACE",FACE,{"disambiguationData":[OSD([sQuery(id+"F39.wireOp",EDGE,"E29"),sQuery(id+"F39.wireOp",EDGE,"E30")])],"isStart":true})]}),makeQuery(id+"F42.boolean.opBoolean","COPY",FACE,{"disambiguationData":[TD([makeQuery(id+"F23.opLoft","SWEPT_FACE",FACE,{"disambiguationData":[OSD([sQuery(id+"F3.wireOp",EDGE,"E20.8.0"),subQ4,subQ3,subQ2,subQ1,subQ6])]})])],"derivedFrom":makeQuery(id+"F42.opRevolve","SWEPT_FACE",FACE,{"disambiguationData":[OSD([subQ8]),TDD([makeQuery(id+"F41.imprint","IMPRINT",EDGE,{"disambiguationData":[TD([[makeQuery(id+"F41.imprint","INTERSECT",VERTEX,{"disambiguationData":[OD(0.0)],"derivedFrom":[subQ8,subQ7]}),-1.0]])],"derivedFrom":subQ8})])]})})],"blendedInto":[makeQuery(id+"F42.boolean.opBoolean","COPY",FACE,{"disambiguationData":[TD([makeQuery(id+"F23.opLoft","SWEPT_FACE",FACE,{"disambiguationData":[OSD([sQuery(id+"F3.wireOp",EDGE,"E20.8.0"),subQ4,subQ3,subQ2,subQ1,subQ6])]})])],"derivedFrom":makeQuery(id+"F42.opRevolve","SWEPT_FACE",FACE,{"disambiguationData":[OSD([subQ8]),TDD([makeQuery(id+"F41.imprint","IMPRINT",EDGE,{"disambiguationData":[TD([[makeQuery(id+"F41.imprint","INTERSECT",VERTEX,{"disambiguationData":[OD(0.0)],"derivedFrom":[subQ8,subQ7]}),-1.0]])],"derivedFrom":subQ8})])]})})]});}
            var Q43;
            {var subQ0=sQuery(id+"F41.wireOp",EDGE,"E34");var subQ1=sQuery(id+"F41.wireOp",EDGE,"E32");Q43=makeQuery(id+"F42.boolean.opBoolean","INTERSECT",EDGE,{"derivedFrom":[makeQuery(id+"F38.opLoft","SWEPT_FACE",FACE,{"disambiguationData":[OSD([sQuery(id+"F3.wireOp",EDGE,"E20.7.0"),sQuery(id+"F3.wireOp",EDGE,"E20.7.1"),sQuery(id+"F3.wireOp",EDGE,"E20.7.3"),sQuery(id+"F22.wireOp",EDGE,"E28.15.1"),sQuery(id+"F22.wireOp",EDGE,"E28.15.2"),sQuery(id+"F22.wireOp",EDGE,"E28.15.3")])]}),makeQuery(id+"F42.opRevolve","SWEPT_FACE",FACE,{"disambiguationData":[OSD([subQ1]),TDD([makeQuery(id+"F41.imprint","IMPRINT",EDGE,{"disambiguationData":[TD([[makeQuery(id+"F41.imprint","INTERSECT",VERTEX,{"disambiguationData":[OD(0.0)],"derivedFrom":[subQ1,subQ0]}),-1.0]])],"derivedFrom":subQ1})])]})]});}
            var Q44;
            {var subQ0=sQuery(id+"F41.wireOp",EDGE,"E37");var subQ1=makeQuery(id+"F42.opRevolve","SWEPT_FACE",FACE,{"disambiguationData":[OSD([subQ0])]});var subQ2=makeQuery(id+"F40.opExtrude","CAP_FACE",FACE,{"disambiguationData":[OSD([sQuery(id+"F39.wireOp",EDGE,"E29"),sQuery(id+"F39.wireOp",EDGE,"E30")])],"isStart":true});var subQ3=sQuery(id+"F22.wireOp",EDGE,"E28.15.3");var subQ4=sQuery(id+"F22.wireOp",EDGE,"E28.15.2");var subQ5=sQuery(id+"F3.wireOp",EDGE,"E20.7.3");var subQ7=sQuery(id+"F3.wireOp",EDGE,"E20.7.1");var subQ9=sQuery(id+"F3.wireOp",EDGE,"E20.7.0");var subQ10=makeQuery(id+"F38.opLoft","SWEPT_FACE",FACE,{"disambiguationData":[OSD([subQ9,subQ7,subQ5,sQuery(id+"F22.wireOp",EDGE,"E28.15.1"),subQ4,subQ3])]});var subQ11=sQuery(id+"F41.wireOp",EDGE,"E38");var subQ12=makeQuery(id+"F42.opRevolve","SWEPT_FACE",FACE,{"disambiguationData":[OSD([subQ11])]});var subQ13=makeQuery(id+"F42.opRevolve","SWEPT_EDGE",EDGE,{"disambiguationData":[OSD([subQ0,subQ11])]});var subQ14=sQuery(id+"F22.wireOp",EDGE,"E28.14.3");var subQ15=sQuery(id+"F22.wireOp",EDGE,"E28.14.2");var subQ16=sQuery(id+"F3.wireOp",EDGE,"E20.6.3");var subQ17=sQuery(id+"F3.wireOp",EDGE,"E20.6.1");var subQ18=sQuery(id+"F3.wireOp",EDGE,"E20.6.0");var subQ19=makeQuery(id+"F37.opLoft","SWEPT_FACE",FACE,{"disambiguationData":[OSD([subQ18,subQ17,subQ16,sQuery(id+"F22.wireOp",EDGE,"E28.14.1"),subQ15,subQ14])]});var subQ21=sQuery(id+"F22.wireOp",EDGE,"E28.13.3");var subQ22=sQuery(id+"F22.wireOp",EDGE,"E28.13.2");var subQ23=sQuery(id+"F3.wireOp",EDGE,"E20.5.3");var subQ25=sQuery(id+"F3.wireOp",EDGE,"E20.5.1");var subQ26=sQuery(id+"F3.wireOp",EDGE,"E20.5.0");var subQ27=makeQuery(id+"F36.opLoft","SWEPT_FACE",FACE,{"disambiguationData":[OSD([subQ26,subQ25,subQ23,sQuery(id+"F22.wireOp",EDGE,"E28.13.1"),subQ22,subQ21])]});var subQ28=sQuery(id+"F22.wireOp",EDGE,"E28.12.3");var subQ29=sQuery(id+"F22.wireOp",EDGE,"E28.12.2");var subQ30=sQuery(id+"F3.wireOp",EDGE,"E20.4.3");var subQ32=sQuery(id+"F3.wireOp",EDGE,"E20.4.1");var subQ33=sQuery(id+"F3.wireOp",EDGE,"E20.4.0");var subQ34=makeQuery(id+"F35.opLoft","SWEPT_FACE",FACE,{"disambiguationData":[OSD([subQ33,subQ32,subQ30,sQuery(id+"F22.wireOp",EDGE,"E28.12.1"),subQ29,subQ28])]});var subQ35=sQuery(id+"F22.wireOp",EDGE,"E28.11.3");var subQ36=sQuery(id+"F22.wireOp",EDGE,"E28.11.2");var subQ37=sQuery(id+"F3.wireOp",EDGE,"E20.3.3");var subQ39=sQuery(id+"F3.wireOp",EDGE,"E20.3.1");var subQ40=sQuery(id+"F3.wireOp",EDGE,"E20.3.0");var subQ41=makeQuery(id+"F34.opLoft","SWEPT_FACE",FACE,{"disambiguationData":[OSD([subQ40,subQ39,subQ37,sQuery(id+"F22.wireOp",EDGE,"E28.11.1"),subQ36,subQ35])]});var subQ42=sQuery(id+"F22.wireOp",EDGE,"E28.10.3");var subQ43=sQuery(id+"F22.wireOp",EDGE,"E28.10.2");var subQ44=sQuery(id+"F3.wireOp",EDGE,"E20.2.3");var subQ46=sQuery(id+"F3.wireOp",EDGE,"E20.2.1");var subQ47=sQuery(id+"F3.wireOp",EDGE,"E20.2.0");var subQ48=makeQuery(id+"F33.opLoft","SWEPT_FACE",FACE,{"disambiguationData":[OSD([subQ47,subQ46,subQ44,sQuery(id+"F22.wireOp",EDGE,"E28.10.1"),subQ43,subQ42])]});var subQ49=sQuery(id+"F22.wireOp",EDGE,"E28.9.3");var subQ50=sQuery(id+"F22.wireOp",EDGE,"E28.9.2");var subQ51=sQuery(id+"F3.wireOp",EDGE,"E20.1.3");var subQ53=sQuery(id+"F3.wireOp",EDGE,"E20.1.1");var subQ54=sQuery(id+"F3.wireOp",EDGE,"E20.1.0");var subQ55=makeQuery(id+"F32.opLoft","SWEPT_FACE",FACE,{"disambiguationData":[OSD([subQ54,subQ53,subQ51,sQuery(id+"F22.wireOp",EDGE,"E28.9.1"),subQ50,subQ49])]});var subQ56=sQuery(id+"F22.wireOp",EDGE,"E28.8.3");var subQ57=sQuery(id+"F22.wireOp",EDGE,"E28.8.2");var subQ59=sQuery(id+"F3.wireOp",EDGE,"E18.top");var subQ60=sQuery(id+"F3.wireOp",EDGE,"E18.bottom");var subQ61=sQuery(id+"F3.wireOp",EDGE,"E18.left");var subQ62=makeQuery(id+"F31.opLoft","SWEPT_FACE",FACE,{"disambiguationData":[OSD([subQ60,subQ59,subQ61,sQuery(id+"F22.wireOp",EDGE,"E28.8.1"),subQ57,subQ56])]});var subQ63=sQuery(id+"F22.wireOp",EDGE,"E28.7.3");var subQ64=sQuery(id+"F22.wireOp",EDGE,"E28.7.2");var subQ65=sQuery(id+"F3.wireOp",EDGE,"E20.15.3");var subQ66=sQuery(id+"F3.wireOp",EDGE,"E20.15.1");var subQ67=sQuery(id+"F3.wireOp",EDGE,"E20.15.0");var subQ68=makeQuery(id+"F30.opLoft","SWEPT_FACE",FACE,{"disambiguationData":[OSD([subQ67,subQ66,subQ65,sQuery(id+"F22.wireOp",EDGE,"E28.7.1"),subQ64,subQ63])]});var subQ70=sQuery(id+"F22.wireOp",EDGE,"E28.6.3");var subQ71=sQuery(id+"F22.wireOp",EDGE,"E28.6.2");var subQ72=sQuery(id+"F3.wireOp",EDGE,"E20.14.3");var subQ74=sQuery(id+"F3.wireOp",EDGE,"E20.14.1");var subQ75=sQuery(id+"F3.wireOp",EDGE,"E20.14.0");var subQ76=makeQuery(id+"F29.opLoft","SWEPT_FACE",FACE,{"disambiguationData":[OSD([subQ75,subQ74,subQ72,sQuery(id+"F22.wireOp",EDGE,"E28.6.1"),subQ71,subQ70])]});var subQ77=sQuery(id+"F22.wireOp",EDGE,"E28.5.3");var subQ78=sQuery(id+"F22.wireOp",EDGE,"E28.5.2");var subQ79=sQuery(id+"F3.wireOp",EDGE,"E20.13.3");var subQ81=sQuery(id+"F3.wireOp",EDGE,"E20.13.1");var subQ82=sQuery(id+"F3.wireOp",EDGE,"E20.13.0");var subQ83=makeQuery(id+"F28.opLoft","SWEPT_FACE",FACE,{"disambiguationData":[OSD([subQ82,subQ81,subQ79,sQuery(id+"F22.wireOp",EDGE,"E28.5.1"),subQ78,subQ77])]});var subQ84=sQuery(id+"F22.wireOp",EDGE,"E28.4.3");var subQ85=sQuery(id+"F22.wireOp",EDGE,"E28.4.2");var subQ86=sQuery(id+"F3.wireOp",EDGE,"E20.12.3");var subQ88=sQuery(id+"F3.wireOp",EDGE,"E20.12.1");var subQ89=sQuery(id+"F3.wireOp",EDGE,"E20.12.0");var subQ90=makeQuery(id+"F27.opLoft","SWEPT_FACE",FACE,{"disambiguationData":[OSD([subQ89,subQ88,subQ86,sQuery(id+"F22.wireOp",EDGE,"E28.4.1"),subQ85,subQ84])]});var subQ91=sQuery(id+"F22.wireOp",EDGE,"E28.3.3");var subQ92=sQuery(id+"F22.wireOp",EDGE,"E28.3.2");var subQ93=sQuery(id+"F3.wireOp",EDGE,"E20.11.3");var subQ95=sQuery(id+"F3.wireOp",EDGE,"E20.11.1");var subQ96=sQuery(id+"F3.wireOp",EDGE,"E20.11.0");var subQ97=makeQuery(id+"F26.opLoft","SWEPT_FACE",FACE,{"disambiguationData":[OSD([subQ96,subQ95,subQ93,sQuery(id+"F22.wireOp",EDGE,"E28.3.1"),subQ92,subQ91])]});var subQ98=sQuery(id+"F22.wireOp",EDGE,"E28.2.3");var subQ99=sQuery(id+"F22.wireOp",EDGE,"E28.2.2");var subQ100=sQuery(id+"F3.wireOp",EDGE,"E20.10.3");var subQ101=sQuery(id+"F3.wireOp",EDGE,"E20.10.1");var subQ102=sQuery(id+"F3.wireOp",EDGE,"E20.10.0");var subQ103=makeQuery(id+"F25.opLoft","SWEPT_FACE",FACE,{"disambiguationData":[OSD([subQ102,subQ101,subQ100,sQuery(id+"F22.wireOp",EDGE,"E28.2.1"),subQ99,subQ98])]});var subQ105=sQuery(id+"F22.wireOp",EDGE,"E28.1.3");var subQ106=sQuery(id+"F22.wireOp",EDGE,"E28.1.2");var subQ107=sQuery(id+"F3.wireOp",EDGE,"E20.9.3");var subQ108=sQuery(id+"F3.wireOp",EDGE,"E20.9.1");var subQ109=sQuery(id+"F3.wireOp",EDGE,"E20.9.0");var subQ110=makeQuery(id+"F24.opLoft","SWEPT_FACE",FACE,{"disambiguationData":[OSD([subQ109,subQ108,subQ107,sQuery(id+"F22.wireOp",EDGE,"E28.1.1"),subQ106,subQ105])]});var subQ111=sQuery(id+"F22.wireOp",EDGE,"E27.top");var subQ112=sQuery(id+"F22.wireOp",EDGE,"E27.bottom");var subQ113=sQuery(id+"F3.wireOp",EDGE,"E20.8.3");var subQ115=sQuery(id+"F3.wireOp",EDGE,"E20.8.1");var subQ119=makeQuery(id+"F42.boolean.opBoolean","COPY",FACE,{"disambiguationData":[TD([subQ10])],"derivedFrom":subQ12});var subQ127=makeQuery(id+"F14.opLoft","CAP_FACE",FACE,{"disambiguationData":[OSD([makeQuery(id+"F3.imprint","IMPRINT",FACE,{"disambiguationData":[TD([[makeQuery(id+"F3.imprint","IMPRINT",EDGE,{"derivedFrom":subQ9}),-1.0]])]})])],"isStart":true});var subQ162=makeQuery(id+"F5.opLoft","CAP_FACE",FACE,{"disambiguationData":[OSD([makeQuery(id+"F3.imprint","IMPRINT",FACE,{"disambiguationData":[TD([[makeQuery(id+"F3.imprint","IMPRINT",EDGE,{"derivedFrom":subQ60}),1.0]])]})])],"isStart":true});var subQ191=makeQuery(id+"F38.boolean.opBoolean","INTERSECT",EDGE,{"derivedFrom":[makeQuery(id+"F37.boolean.opBoolean","SPLIT",FACE,{"disambiguationData":[TD([subQ127])],"derivedFrom":makeQuery(id+"F36.boolean.opBoolean","SPLIT",FACE,{"disambiguationData":[TD([subQ127])],"derivedFrom":makeQuery(id+"F35.boolean.opBoolean","SPLIT",FACE,{"disambiguationData":[TD([subQ127])],"derivedFrom":makeQuery(id+"F34.boolean.opBoolean","SPLIT",FACE,{"disambiguationData":[TD([subQ127])],"derivedFrom":makeQuery(id+"F33.boolean.opBoolean","SPLIT",FACE,{"disambiguationData":[TD([subQ127])],"derivedFrom":makeQuery(id+"F32.boolean.opBoolean","SPLIT",FACE,{"disambiguationData":[TD([subQ127])],"derivedFrom":makeQuery(id+"F31.boolean.opBoolean","SPLIT",FACE,{"disambiguationData":[TD([subQ127])],"derivedFrom":makeQuery(id+"F30.boolean.opBoolean","SPLIT",FACE,{"disambiguationData":[TD([subQ162])],"derivedFrom":makeQuery(id+"F29.boolean.opBoolean","SPLIT",FACE,{"disambiguationData":[TD([subQ162])],"derivedFrom":makeQuery(id+"F28.boolean.opBoolean","SPLIT",FACE,{"disambiguationData":[TD([subQ162])],"derivedFrom":makeQuery(id+"F27.boolean.opBoolean","SPLIT",FACE,{"disambiguationData":[TD([subQ162])],"derivedFrom":makeQuery(id+"F26.boolean.opBoolean","SPLIT",FACE,{"disambiguationData":[TD([subQ162])],"derivedFrom":makeQuery(id+"F25.boolean.opBoolean","SPLIT",FACE,{"disambiguationData":[TD([subQ162])],"derivedFrom":makeQuery(id+"F24.boolean.opBoolean","SPLIT",FACE,{"disambiguationData":[TD([subQ162])],"derivedFrom":makeQuery(id+"F1.opRevolve","SWEPT_FACE",FACE,{"disambiguationData":[OSD([sQuery(id+"F0.wireOp",EDGE,"E4")])]})})})})})})})})})})})})})})}),subQ10]});Q44=makeQuery(id+"F48.opFillet","BLEND_EDGE",EDGE,{"blendedFrom":[makeQuery(id+"F47.opFillet","TWEAK_EDGE",EDGE,{"derivedFrom":[makeQuery(id+"F45.opFillet","BLEND_VERTEX",VERTEX,{"blendedFrom":[subQ191,subQ10,subQ119],"blendedInto":[subQ10,subQ119]}),makeQuery(id+"F45.opFillet","BLEND_VERTEX",VERTEX,{"blendedFrom":[subQ191,makeQuery(id+"F42.boolean.opBoolean","MERGE",FACE,{"derivedFrom":[subQ2,subQ1]}),subQ119],"blendedInto":[makeQuery(id+"F42.boolean.opBoolean","MERGE",FACE,{"derivedFrom":[subQ2,subQ1]}),subQ119]})]}),makeQuery(id+"F47.opFillet","BLEND_FACE",FACE,{"disambiguationData":[OSD([subQ0,subQ11]),TDD([makeQuery(id+"F42.boolean.opBoolean","COPY",EDGE,{"disambiguationData":[TD([makeQuery(id+"F23.opLoft","SWEPT_FACE",FACE,{"disambiguationData":[OSD([sQuery(id+"F3.wireOp",EDGE,"E20.8.0"),subQ115,subQ113,subQ112,subQ111,sQuery(id+"F22.wireOp",EDGE,"E27.right")])]})])],"derivedFrom":subQ13})])]}),makeQuery(id+"F47.opFillet","BLEND_FACE",FACE,{"disambiguationData":[OSD([subQ0,subQ11]),TDD([makeQuery(id+"F42.boolean.opBoolean","COPY",EDGE,{"disambiguationData":[TD([subQ110])],"derivedFrom":subQ13})])]}),makeQuery(id+"F47.opFillet","BLEND_FACE",FACE,{"disambiguationData":[OSD([subQ0,subQ11]),TDD([makeQuery(id+"F42.boolean.opBoolean","COPY",EDGE,{"disambiguationData":[TD([subQ103])],"derivedFrom":subQ13})])]}),makeQuery(id+"F47.opFillet","BLEND_FACE",FACE,{"disambiguationData":[OSD([subQ0,subQ11]),TDD([makeQuery(id+"F42.boolean.opBoolean","COPY",EDGE,{"disambiguationData":[TD([subQ97])],"derivedFrom":subQ13})])]}),makeQuery(id+"F47.opFillet","BLEND_FACE",FACE,{"disambiguationData":[OSD([subQ0,subQ11]),TDD([makeQuery(id+"F42.boolean.opBoolean","COPY",EDGE,{"disambiguationData":[TD([subQ90])],"derivedFrom":subQ13})])]}),makeQuery(id+"F47.opFillet","BLEND_FACE",FACE,{"disambiguationData":[OSD([subQ0,subQ11]),TDD([makeQuery(id+"F42.boolean.opBoolean","COPY",EDGE,{"disambiguationData":[TD([subQ83])],"derivedFrom":subQ13})])]}),makeQuery(id+"F47.opFillet","BLEND_FACE",FACE,{"disambiguationData":[OSD([subQ0,subQ11]),TDD([makeQuery(id+"F42.boolean.opBoolean","COPY",EDGE,{"disambiguationData":[TD([subQ76])],"derivedFrom":subQ13})])]}),makeQuery(id+"F47.opFillet","BLEND_FACE",FACE,{"disambiguationData":[OSD([subQ0,subQ11]),TDD([makeQuery(id+"F42.boolean.opBoolean","COPY",EDGE,{"disambiguationData":[TD([subQ68])],"derivedFrom":subQ13})])]}),makeQuery(id+"F47.opFillet","BLEND_FACE",FACE,{"disambiguationData":[OSD([subQ0,subQ11]),TDD([makeQuery(id+"F42.boolean.opBoolean","COPY",EDGE,{"disambiguationData":[TD([subQ62])],"derivedFrom":subQ13})])]}),makeQuery(id+"F47.opFillet","BLEND_FACE",FACE,{"disambiguationData":[OSD([subQ0,subQ11]),TDD([makeQuery(id+"F42.boolean.opBoolean","COPY",EDGE,{"disambiguationData":[TD([subQ55])],"derivedFrom":subQ13})])]}),makeQuery(id+"F47.opFillet","BLEND_FACE",FACE,{"disambiguationData":[OSD([subQ0,subQ11]),TDD([makeQuery(id+"F42.boolean.opBoolean","COPY",EDGE,{"disambiguationData":[TD([subQ48])],"derivedFrom":subQ13})])]}),makeQuery(id+"F47.opFillet","BLEND_FACE",FACE,{"disambiguationData":[OSD([subQ0,subQ11]),TDD([makeQuery(id+"F42.boolean.opBoolean","COPY",EDGE,{"disambiguationData":[TD([subQ41])],"derivedFrom":subQ13})])]}),makeQuery(id+"F47.opFillet","BLEND_FACE",FACE,{"disambiguationData":[OSD([subQ0,subQ11]),TDD([makeQuery(id+"F42.boolean.opBoolean","COPY",EDGE,{"disambiguationData":[TD([subQ34])],"derivedFrom":subQ13})])]}),makeQuery(id+"F47.opFillet","BLEND_FACE",FACE,{"disambiguationData":[OSD([subQ0,subQ11]),TDD([makeQuery(id+"F42.boolean.opBoolean","COPY",EDGE,{"disambiguationData":[TD([subQ27])],"derivedFrom":subQ13})])]}),makeQuery(id+"F47.opFillet","BLEND_FACE",FACE,{"disambiguationData":[OSD([subQ0,subQ11]),TDD([makeQuery(id+"F42.boolean.opBoolean","COPY",EDGE,{"disambiguationData":[TD([subQ19])],"derivedFrom":subQ13})])]}),makeQuery(id+"F47.opFillet","BLEND_FACE",FACE,{"disambiguationData":[OSD([subQ0,subQ11]),TDD([makeQuery(id+"F42.boolean.opBoolean","COPY",EDGE,{"disambiguationData":[TD([subQ10])],"derivedFrom":subQ13})])]})],"blendedInto":[makeQuery(id+"F47.opFillet","BLEND_FACE",FACE,{"disambiguationData":[OSD([subQ0,subQ11]),TDD([makeQuery(id+"F42.boolean.opBoolean","COPY",EDGE,{"disambiguationData":[TD([makeQuery(id+"F23.opLoft","SWEPT_FACE",FACE,{"disambiguationData":[OSD([sQuery(id+"F3.wireOp",EDGE,"E20.8.0"),subQ115,subQ113,subQ112,subQ111,sQuery(id+"F22.wireOp",EDGE,"E27.right")])]})])],"derivedFrom":subQ13})])]}),makeQuery(id+"F47.opFillet","BLEND_FACE",FACE,{"disambiguationData":[OSD([subQ0,subQ11]),TDD([makeQuery(id+"F42.boolean.opBoolean","COPY",EDGE,{"disambiguationData":[TD([subQ110])],"derivedFrom":subQ13})])]}),makeQuery(id+"F47.opFillet","BLEND_FACE",FACE,{"disambiguationData":[OSD([subQ0,subQ11]),TDD([makeQuery(id+"F42.boolean.opBoolean","COPY",EDGE,{"disambiguationData":[TD([subQ103])],"derivedFrom":subQ13})])]}),makeQuery(id+"F47.opFillet","BLEND_FACE",FACE,{"disambiguationData":[OSD([subQ0,subQ11]),TDD([makeQuery(id+"F42.boolean.opBoolean","COPY",EDGE,{"disambiguationData":[TD([subQ97])],"derivedFrom":subQ13})])]}),makeQuery(id+"F47.opFillet","BLEND_FACE",FACE,{"disambiguationData":[OSD([subQ0,subQ11]),TDD([makeQuery(id+"F42.boolean.opBoolean","COPY",EDGE,{"disambiguationData":[TD([subQ90])],"derivedFrom":subQ13})])]}),makeQuery(id+"F47.opFillet","BLEND_FACE",FACE,{"disambiguationData":[OSD([subQ0,subQ11]),TDD([makeQuery(id+"F42.boolean.opBoolean","COPY",EDGE,{"disambiguationData":[TD([subQ83])],"derivedFrom":subQ13})])]}),makeQuery(id+"F47.opFillet","BLEND_FACE",FACE,{"disambiguationData":[OSD([subQ0,subQ11]),TDD([makeQuery(id+"F42.boolean.opBoolean","COPY",EDGE,{"disambiguationData":[TD([subQ76])],"derivedFrom":subQ13})])]}),makeQuery(id+"F47.opFillet","BLEND_FACE",FACE,{"disambiguationData":[OSD([subQ0,subQ11]),TDD([makeQuery(id+"F42.boolean.opBoolean","COPY",EDGE,{"disambiguationData":[TD([subQ68])],"derivedFrom":subQ13})])]}),makeQuery(id+"F47.opFillet","BLEND_FACE",FACE,{"disambiguationData":[OSD([subQ0,subQ11]),TDD([makeQuery(id+"F42.boolean.opBoolean","COPY",EDGE,{"disambiguationData":[TD([subQ62])],"derivedFrom":subQ13})])]}),makeQuery(id+"F47.opFillet","BLEND_FACE",FACE,{"disambiguationData":[OSD([subQ0,subQ11]),TDD([makeQuery(id+"F42.boolean.opBoolean","COPY",EDGE,{"disambiguationData":[TD([subQ55])],"derivedFrom":subQ13})])]}),makeQuery(id+"F47.opFillet","BLEND_FACE",FACE,{"disambiguationData":[OSD([subQ0,subQ11]),TDD([makeQuery(id+"F42.boolean.opBoolean","COPY",EDGE,{"disambiguationData":[TD([subQ48])],"derivedFrom":subQ13})])]}),makeQuery(id+"F47.opFillet","BLEND_FACE",FACE,{"disambiguationData":[OSD([subQ0,subQ11]),TDD([makeQuery(id+"F42.boolean.opBoolean","COPY",EDGE,{"disambiguationData":[TD([subQ41])],"derivedFrom":subQ13})])]}),makeQuery(id+"F47.opFillet","BLEND_FACE",FACE,{"disambiguationData":[OSD([subQ0,subQ11]),TDD([makeQuery(id+"F42.boolean.opBoolean","COPY",EDGE,{"disambiguationData":[TD([subQ34])],"derivedFrom":subQ13})])]}),makeQuery(id+"F47.opFillet","BLEND_FACE",FACE,{"disambiguationData":[OSD([subQ0,subQ11]),TDD([makeQuery(id+"F42.boolean.opBoolean","COPY",EDGE,{"disambiguationData":[TD([subQ27])],"derivedFrom":subQ13})])]}),makeQuery(id+"F47.opFillet","BLEND_FACE",FACE,{"disambiguationData":[OSD([subQ0,subQ11]),TDD([makeQuery(id+"F42.boolean.opBoolean","COPY",EDGE,{"disambiguationData":[TD([subQ19])],"derivedFrom":subQ13})])]}),makeQuery(id+"F47.opFillet","BLEND_FACE",FACE,{"disambiguationData":[OSD([subQ0,subQ11]),TDD([makeQuery(id+"F42.boolean.opBoolean","COPY",EDGE,{"disambiguationData":[TD([subQ10])],"derivedFrom":subQ13})])]})]});}
            var Q45;
            {var subQ0=sQuery(id+"F41.wireOp",EDGE,"E34");var subQ1=sQuery(id+"F41.wireOp",EDGE,"E32");Q45=makeQuery(id+"F42.boolean.opBoolean","INTERSECT",EDGE,{"derivedFrom":[makeQuery(id+"F37.opLoft","SWEPT_FACE",FACE,{"disambiguationData":[OSD([sQuery(id+"F3.wireOp",EDGE,"E20.6.0"),sQuery(id+"F3.wireOp",EDGE,"E20.6.1"),sQuery(id+"F3.wireOp",EDGE,"E20.6.3"),sQuery(id+"F22.wireOp",EDGE,"E28.14.1"),sQuery(id+"F22.wireOp",EDGE,"E28.14.2"),sQuery(id+"F22.wireOp",EDGE,"E28.14.3")])]}),makeQuery(id+"F42.opRevolve","SWEPT_FACE",FACE,{"disambiguationData":[OSD([subQ1]),TDD([makeQuery(id+"F41.imprint","IMPRINT",EDGE,{"disambiguationData":[TD([[makeQuery(id+"F41.imprint","INTERSECT",VERTEX,{"disambiguationData":[OD(0.0)],"derivedFrom":[subQ1,subQ0]}),-1.0]])],"derivedFrom":subQ1})])]})]});}
            var Q46;
            {var subQ0=sQuery(id+"F22.wireOp",EDGE,"E28.15.3");var subQ1=sQuery(id+"F22.wireOp",EDGE,"E28.15.2");var subQ2=sQuery(id+"F22.wireOp",EDGE,"E28.15.1");var subQ3=sQuery(id+"F3.wireOp",EDGE,"E20.7.3");var subQ4=sQuery(id+"F3.wireOp",EDGE,"E20.7.1");var subQ5=sQuery(id+"F22.wireOp",EDGE,"E28.15.0");var subQ6=makeQuery(id+"F38.opLoft","SWEPT_FACE",FACE,{"disambiguationData":[OSD([subQ4,sQuery(id+"F3.wireOp",EDGE,"E20.7.2"),subQ3,subQ5,subQ1,subQ0])]});var subQ7=sQuery(id+"F41.wireOp",EDGE,"E34");var subQ8=sQuery(id+"F41.wireOp",EDGE,"E32");Q46=makeQuery(id+"F44.opFillet","BLEND_EDGE",EDGE,{"blendedFrom":[makeQuery(id+"F40.boolean.opBoolean","INTERSECT",EDGE,{"derivedFrom":[subQ6,makeQuery(id+"F40.opExtrude","CAP_FACE",FACE,{"disambiguationData":[OSD([sQuery(id+"F39.wireOp",EDGE,"E29"),sQuery(id+"F39.wireOp",EDGE,"E30")])],"isStart":true})]}),makeQuery(id+"F42.boolean.opBoolean","COPY",FACE,{"disambiguationData":[TD([makeQuery(id+"F38.opLoft","SWEPT_FACE",FACE,{"disambiguationData":[OSD([sQuery(id+"F3.wireOp",EDGE,"E20.7.0"),subQ4,subQ3,subQ2,subQ1,subQ0])]})])],"derivedFrom":makeQuery(id+"F42.opRevolve","SWEPT_FACE",FACE,{"disambiguationData":[OSD([subQ8]),TDD([makeQuery(id+"F41.imprint","IMPRINT",EDGE,{"disambiguationData":[TD([[makeQuery(id+"F41.imprint","INTERSECT",VERTEX,{"disambiguationData":[OD(0.0)],"derivedFrom":[subQ8,subQ7]}),-1.0]])],"derivedFrom":subQ8})])]})})],"blendedInto":[makeQuery(id+"F42.boolean.opBoolean","COPY",FACE,{"disambiguationData":[TD([makeQuery(id+"F38.opLoft","SWEPT_FACE",FACE,{"disambiguationData":[OSD([sQuery(id+"F3.wireOp",EDGE,"E20.7.0"),subQ4,subQ3,subQ2,subQ1,subQ0])]})])],"derivedFrom":makeQuery(id+"F42.opRevolve","SWEPT_FACE",FACE,{"disambiguationData":[OSD([subQ8]),TDD([makeQuery(id+"F41.imprint","IMPRINT",EDGE,{"disambiguationData":[TD([[makeQuery(id+"F41.imprint","INTERSECT",VERTEX,{"disambiguationData":[OD(0.0)],"derivedFrom":[subQ8,subQ7]}),-1.0]])],"derivedFrom":subQ8})])]})})]});}
            var Q47;
            {var subQ0=sQuery(id+"F41.wireOp",EDGE,"E37");var subQ1=makeQuery(id+"F42.opRevolve","SWEPT_FACE",FACE,{"disambiguationData":[OSD([subQ0])]});var subQ2=makeQuery(id+"F40.opExtrude","CAP_FACE",FACE,{"disambiguationData":[OSD([sQuery(id+"F39.wireOp",EDGE,"E29"),sQuery(id+"F39.wireOp",EDGE,"E30")])],"isStart":true});var subQ3=sQuery(id+"F22.wireOp",EDGE,"E28.15.3");var subQ4=sQuery(id+"F22.wireOp",EDGE,"E28.15.2");var subQ5=sQuery(id+"F3.wireOp",EDGE,"E20.7.3");var subQ7=sQuery(id+"F3.wireOp",EDGE,"E20.7.1");var subQ8=sQuery(id+"F3.wireOp",EDGE,"E20.7.0");var subQ9=sQuery(id+"F41.wireOp",EDGE,"E38");var subQ10=makeQuery(id+"F42.opRevolve","SWEPT_FACE",FACE,{"disambiguationData":[OSD([subQ9])]});var subQ11=makeQuery(id+"F42.opRevolve","SWEPT_EDGE",EDGE,{"disambiguationData":[OSD([subQ0,subQ9])]});var subQ12=sQuery(id+"F22.wireOp",EDGE,"E28.14.3");var subQ13=sQuery(id+"F22.wireOp",EDGE,"E28.14.2");var subQ14=sQuery(id+"F3.wireOp",EDGE,"E20.6.3");var subQ15=sQuery(id+"F3.wireOp",EDGE,"E20.6.1");var subQ16=sQuery(id+"F3.wireOp",EDGE,"E20.6.0");var subQ17=makeQuery(id+"F37.opLoft","SWEPT_FACE",FACE,{"disambiguationData":[OSD([subQ16,subQ15,subQ14,sQuery(id+"F22.wireOp",EDGE,"E28.14.1"),subQ13,subQ12])]});var subQ20=sQuery(id+"F22.wireOp",EDGE,"E28.13.3");var subQ21=sQuery(id+"F22.wireOp",EDGE,"E28.13.2");var subQ22=sQuery(id+"F3.wireOp",EDGE,"E20.5.3");var subQ24=sQuery(id+"F3.wireOp",EDGE,"E20.5.1");var subQ25=sQuery(id+"F3.wireOp",EDGE,"E20.5.0");var subQ26=makeQuery(id+"F36.opLoft","SWEPT_FACE",FACE,{"disambiguationData":[OSD([subQ25,subQ24,subQ22,sQuery(id+"F22.wireOp",EDGE,"E28.13.1"),subQ21,subQ20])]});var subQ27=sQuery(id+"F22.wireOp",EDGE,"E28.12.3");var subQ28=sQuery(id+"F22.wireOp",EDGE,"E28.12.2");var subQ29=sQuery(id+"F3.wireOp",EDGE,"E20.4.3");var subQ31=sQuery(id+"F3.wireOp",EDGE,"E20.4.1");var subQ32=sQuery(id+"F3.wireOp",EDGE,"E20.4.0");var subQ33=makeQuery(id+"F35.opLoft","SWEPT_FACE",FACE,{"disambiguationData":[OSD([subQ32,subQ31,subQ29,sQuery(id+"F22.wireOp",EDGE,"E28.12.1"),subQ28,subQ27])]});var subQ34=sQuery(id+"F22.wireOp",EDGE,"E28.11.3");var subQ35=sQuery(id+"F22.wireOp",EDGE,"E28.11.2");var subQ36=sQuery(id+"F3.wireOp",EDGE,"E20.3.3");var subQ38=sQuery(id+"F3.wireOp",EDGE,"E20.3.1");var subQ39=sQuery(id+"F3.wireOp",EDGE,"E20.3.0");var subQ40=makeQuery(id+"F34.opLoft","SWEPT_FACE",FACE,{"disambiguationData":[OSD([subQ39,subQ38,subQ36,sQuery(id+"F22.wireOp",EDGE,"E28.11.1"),subQ35,subQ34])]});var subQ41=sQuery(id+"F22.wireOp",EDGE,"E28.10.3");var subQ42=sQuery(id+"F22.wireOp",EDGE,"E28.10.2");var subQ43=sQuery(id+"F3.wireOp",EDGE,"E20.2.3");var subQ45=sQuery(id+"F3.wireOp",EDGE,"E20.2.1");var subQ46=sQuery(id+"F3.wireOp",EDGE,"E20.2.0");var subQ47=makeQuery(id+"F33.opLoft","SWEPT_FACE",FACE,{"disambiguationData":[OSD([subQ46,subQ45,subQ43,sQuery(id+"F22.wireOp",EDGE,"E28.10.1"),subQ42,subQ41])]});var subQ48=sQuery(id+"F22.wireOp",EDGE,"E28.9.3");var subQ49=sQuery(id+"F22.wireOp",EDGE,"E28.9.2");var subQ50=sQuery(id+"F3.wireOp",EDGE,"E20.1.3");var subQ52=sQuery(id+"F3.wireOp",EDGE,"E20.1.1");var subQ53=sQuery(id+"F3.wireOp",EDGE,"E20.1.0");var subQ54=makeQuery(id+"F32.opLoft","SWEPT_FACE",FACE,{"disambiguationData":[OSD([subQ53,subQ52,subQ50,sQuery(id+"F22.wireOp",EDGE,"E28.9.1"),subQ49,subQ48])]});var subQ55=sQuery(id+"F22.wireOp",EDGE,"E28.8.3");var subQ56=sQuery(id+"F22.wireOp",EDGE,"E28.8.2");var subQ58=sQuery(id+"F3.wireOp",EDGE,"E18.top");var subQ59=sQuery(id+"F3.wireOp",EDGE,"E18.bottom");var subQ60=sQuery(id+"F3.wireOp",EDGE,"E18.left");var subQ61=makeQuery(id+"F31.opLoft","SWEPT_FACE",FACE,{"disambiguationData":[OSD([subQ59,subQ58,subQ60,sQuery(id+"F22.wireOp",EDGE,"E28.8.1"),subQ56,subQ55])]});var subQ62=sQuery(id+"F22.wireOp",EDGE,"E28.7.3");var subQ63=sQuery(id+"F22.wireOp",EDGE,"E28.7.2");var subQ64=sQuery(id+"F3.wireOp",EDGE,"E20.15.3");var subQ65=sQuery(id+"F3.wireOp",EDGE,"E20.15.1");var subQ66=sQuery(id+"F3.wireOp",EDGE,"E20.15.0");var subQ67=makeQuery(id+"F30.opLoft","SWEPT_FACE",FACE,{"disambiguationData":[OSD([subQ66,subQ65,subQ64,sQuery(id+"F22.wireOp",EDGE,"E28.7.1"),subQ63,subQ62])]});var subQ69=sQuery(id+"F22.wireOp",EDGE,"E28.6.3");var subQ70=sQuery(id+"F22.wireOp",EDGE,"E28.6.2");var subQ71=sQuery(id+"F3.wireOp",EDGE,"E20.14.3");var subQ73=sQuery(id+"F3.wireOp",EDGE,"E20.14.1");var subQ74=sQuery(id+"F3.wireOp",EDGE,"E20.14.0");var subQ75=makeQuery(id+"F29.opLoft","SWEPT_FACE",FACE,{"disambiguationData":[OSD([subQ74,subQ73,subQ71,sQuery(id+"F22.wireOp",EDGE,"E28.6.1"),subQ70,subQ69])]});var subQ76=sQuery(id+"F22.wireOp",EDGE,"E28.5.3");var subQ77=sQuery(id+"F22.wireOp",EDGE,"E28.5.2");var subQ78=sQuery(id+"F3.wireOp",EDGE,"E20.13.3");var subQ80=sQuery(id+"F3.wireOp",EDGE,"E20.13.1");var subQ81=sQuery(id+"F3.wireOp",EDGE,"E20.13.0");var subQ82=makeQuery(id+"F28.opLoft","SWEPT_FACE",FACE,{"disambiguationData":[OSD([subQ81,subQ80,subQ78,sQuery(id+"F22.wireOp",EDGE,"E28.5.1"),subQ77,subQ76])]});var subQ83=sQuery(id+"F22.wireOp",EDGE,"E28.4.3");var subQ84=sQuery(id+"F22.wireOp",EDGE,"E28.4.2");var subQ85=sQuery(id+"F3.wireOp",EDGE,"E20.12.3");var subQ87=sQuery(id+"F3.wireOp",EDGE,"E20.12.1");var subQ88=sQuery(id+"F3.wireOp",EDGE,"E20.12.0");var subQ89=makeQuery(id+"F27.opLoft","SWEPT_FACE",FACE,{"disambiguationData":[OSD([subQ88,subQ87,subQ85,sQuery(id+"F22.wireOp",EDGE,"E28.4.1"),subQ84,subQ83])]});var subQ90=sQuery(id+"F22.wireOp",EDGE,"E28.3.3");var subQ91=sQuery(id+"F22.wireOp",EDGE,"E28.3.2");var subQ92=sQuery(id+"F3.wireOp",EDGE,"E20.11.3");var subQ94=sQuery(id+"F3.wireOp",EDGE,"E20.11.1");var subQ95=sQuery(id+"F3.wireOp",EDGE,"E20.11.0");var subQ96=makeQuery(id+"F26.opLoft","SWEPT_FACE",FACE,{"disambiguationData":[OSD([subQ95,subQ94,subQ92,sQuery(id+"F22.wireOp",EDGE,"E28.3.1"),subQ91,subQ90])]});var subQ97=sQuery(id+"F22.wireOp",EDGE,"E28.2.3");var subQ98=sQuery(id+"F22.wireOp",EDGE,"E28.2.2");var subQ99=sQuery(id+"F3.wireOp",EDGE,"E20.10.3");var subQ100=sQuery(id+"F3.wireOp",EDGE,"E20.10.1");var subQ101=sQuery(id+"F3.wireOp",EDGE,"E20.10.0");var subQ102=makeQuery(id+"F25.opLoft","SWEPT_FACE",FACE,{"disambiguationData":[OSD([subQ101,subQ100,subQ99,sQuery(id+"F22.wireOp",EDGE,"E28.2.1"),subQ98,subQ97])]});var subQ104=sQuery(id+"F22.wireOp",EDGE,"E28.1.3");var subQ105=sQuery(id+"F22.wireOp",EDGE,"E28.1.2");var subQ106=sQuery(id+"F3.wireOp",EDGE,"E20.9.3");var subQ107=sQuery(id+"F3.wireOp",EDGE,"E20.9.1");var subQ108=sQuery(id+"F3.wireOp",EDGE,"E20.9.0");var subQ109=makeQuery(id+"F24.opLoft","SWEPT_FACE",FACE,{"disambiguationData":[OSD([subQ108,subQ107,subQ106,sQuery(id+"F22.wireOp",EDGE,"E28.1.1"),subQ105,subQ104])]});var subQ110=sQuery(id+"F22.wireOp",EDGE,"E27.top");var subQ111=sQuery(id+"F22.wireOp",EDGE,"E27.bottom");var subQ112=sQuery(id+"F3.wireOp",EDGE,"E20.8.3");var subQ114=sQuery(id+"F3.wireOp",EDGE,"E20.8.1");var subQ118=makeQuery(id+"F42.boolean.opBoolean","COPY",FACE,{"disambiguationData":[TD([subQ17])],"derivedFrom":subQ10});var subQ126=makeQuery(id+"F14.opLoft","CAP_FACE",FACE,{"disambiguationData":[OSD([makeQuery(id+"F3.imprint","IMPRINT",FACE,{"disambiguationData":[TD([[makeQuery(id+"F3.imprint","IMPRINT",EDGE,{"derivedFrom":subQ8}),-1.0]])]})])],"isStart":true});var subQ161=makeQuery(id+"F5.opLoft","CAP_FACE",FACE,{"disambiguationData":[OSD([makeQuery(id+"F3.imprint","IMPRINT",FACE,{"disambiguationData":[TD([[makeQuery(id+"F3.imprint","IMPRINT",EDGE,{"derivedFrom":subQ59}),1.0]])]})])],"isStart":true});var subQ190=makeQuery(id+"F37.boolean.opBoolean","INTERSECT",EDGE,{"derivedFrom":[makeQuery(id+"F36.boolean.opBoolean","SPLIT",FACE,{"disambiguationData":[TD([subQ126])],"derivedFrom":makeQuery(id+"F35.boolean.opBoolean","SPLIT",FACE,{"disambiguationData":[TD([subQ126])],"derivedFrom":makeQuery(id+"F34.boolean.opBoolean","SPLIT",FACE,{"disambiguationData":[TD([subQ126])],"derivedFrom":makeQuery(id+"F33.boolean.opBoolean","SPLIT",FACE,{"disambiguationData":[TD([subQ126])],"derivedFrom":makeQuery(id+"F32.boolean.opBoolean","SPLIT",FACE,{"disambiguationData":[TD([subQ126])],"derivedFrom":makeQuery(id+"F31.boolean.opBoolean","SPLIT",FACE,{"disambiguationData":[TD([subQ126])],"derivedFrom":makeQuery(id+"F30.boolean.opBoolean","SPLIT",FACE,{"disambiguationData":[TD([subQ161])],"derivedFrom":makeQuery(id+"F29.boolean.opBoolean","SPLIT",FACE,{"disambiguationData":[TD([subQ161])],"derivedFrom":makeQuery(id+"F28.boolean.opBoolean","SPLIT",FACE,{"disambiguationData":[TD([subQ161])],"derivedFrom":makeQuery(id+"F27.boolean.opBoolean","SPLIT",FACE,{"disambiguationData":[TD([subQ161])],"derivedFrom":makeQuery(id+"F26.boolean.opBoolean","SPLIT",FACE,{"disambiguationData":[TD([subQ161])],"derivedFrom":makeQuery(id+"F25.boolean.opBoolean","SPLIT",FACE,{"disambiguationData":[TD([subQ161])],"derivedFrom":makeQuery(id+"F24.boolean.opBoolean","SPLIT",FACE,{"disambiguationData":[TD([subQ161])],"derivedFrom":makeQuery(id+"F1.opRevolve","SWEPT_FACE",FACE,{"disambiguationData":[OSD([sQuery(id+"F0.wireOp",EDGE,"E4")])]})})})})})})})})})})})})})}),subQ17]});Q47=makeQuery(id+"F48.opFillet","BLEND_EDGE",EDGE,{"blendedFrom":[makeQuery(id+"F47.opFillet","TWEAK_EDGE",EDGE,{"derivedFrom":[makeQuery(id+"F45.opFillet","BLEND_VERTEX",VERTEX,{"blendedFrom":[subQ190,subQ17,subQ118],"blendedInto":[subQ17,subQ118]}),makeQuery(id+"F45.opFillet","BLEND_VERTEX",VERTEX,{"blendedFrom":[subQ190,makeQuery(id+"F42.boolean.opBoolean","MERGE",FACE,{"derivedFrom":[subQ2,subQ1]}),subQ118],"blendedInto":[makeQuery(id+"F42.boolean.opBoolean","MERGE",FACE,{"derivedFrom":[subQ2,subQ1]}),subQ118]})]}),makeQuery(id+"F47.opFillet","BLEND_FACE",FACE,{"disambiguationData":[OSD([subQ0,subQ9]),TDD([makeQuery(id+"F42.boolean.opBoolean","COPY",EDGE,{"disambiguationData":[TD([makeQuery(id+"F23.opLoft","SWEPT_FACE",FACE,{"disambiguationData":[OSD([sQuery(id+"F3.wireOp",EDGE,"E20.8.0"),subQ114,subQ112,subQ111,subQ110,sQuery(id+"F22.wireOp",EDGE,"E27.right")])]})])],"derivedFrom":subQ11})])]}),makeQuery(id+"F47.opFillet","BLEND_FACE",FACE,{"disambiguationData":[OSD([subQ0,subQ9]),TDD([makeQuery(id+"F42.boolean.opBoolean","COPY",EDGE,{"disambiguationData":[TD([subQ109])],"derivedFrom":subQ11})])]}),makeQuery(id+"F47.opFillet","BLEND_FACE",FACE,{"disambiguationData":[OSD([subQ0,subQ9]),TDD([makeQuery(id+"F42.boolean.opBoolean","COPY",EDGE,{"disambiguationData":[TD([subQ102])],"derivedFrom":subQ11})])]}),makeQuery(id+"F47.opFillet","BLEND_FACE",FACE,{"disambiguationData":[OSD([subQ0,subQ9]),TDD([makeQuery(id+"F42.boolean.opBoolean","COPY",EDGE,{"disambiguationData":[TD([subQ96])],"derivedFrom":subQ11})])]}),makeQuery(id+"F47.opFillet","BLEND_FACE",FACE,{"disambiguationData":[OSD([subQ0,subQ9]),TDD([makeQuery(id+"F42.boolean.opBoolean","COPY",EDGE,{"disambiguationData":[TD([subQ89])],"derivedFrom":subQ11})])]}),makeQuery(id+"F47.opFillet","BLEND_FACE",FACE,{"disambiguationData":[OSD([subQ0,subQ9]),TDD([makeQuery(id+"F42.boolean.opBoolean","COPY",EDGE,{"disambiguationData":[TD([subQ82])],"derivedFrom":subQ11})])]}),makeQuery(id+"F47.opFillet","BLEND_FACE",FACE,{"disambiguationData":[OSD([subQ0,subQ9]),TDD([makeQuery(id+"F42.boolean.opBoolean","COPY",EDGE,{"disambiguationData":[TD([subQ75])],"derivedFrom":subQ11})])]}),makeQuery(id+"F47.opFillet","BLEND_FACE",FACE,{"disambiguationData":[OSD([subQ0,subQ9]),TDD([makeQuery(id+"F42.boolean.opBoolean","COPY",EDGE,{"disambiguationData":[TD([subQ67])],"derivedFrom":subQ11})])]}),makeQuery(id+"F47.opFillet","BLEND_FACE",FACE,{"disambiguationData":[OSD([subQ0,subQ9]),TDD([makeQuery(id+"F42.boolean.opBoolean","COPY",EDGE,{"disambiguationData":[TD([subQ61])],"derivedFrom":subQ11})])]}),makeQuery(id+"F47.opFillet","BLEND_FACE",FACE,{"disambiguationData":[OSD([subQ0,subQ9]),TDD([makeQuery(id+"F42.boolean.opBoolean","COPY",EDGE,{"disambiguationData":[TD([subQ54])],"derivedFrom":subQ11})])]}),makeQuery(id+"F47.opFillet","BLEND_FACE",FACE,{"disambiguationData":[OSD([subQ0,subQ9]),TDD([makeQuery(id+"F42.boolean.opBoolean","COPY",EDGE,{"disambiguationData":[TD([subQ47])],"derivedFrom":subQ11})])]}),makeQuery(id+"F47.opFillet","BLEND_FACE",FACE,{"disambiguationData":[OSD([subQ0,subQ9]),TDD([makeQuery(id+"F42.boolean.opBoolean","COPY",EDGE,{"disambiguationData":[TD([subQ40])],"derivedFrom":subQ11})])]}),makeQuery(id+"F47.opFillet","BLEND_FACE",FACE,{"disambiguationData":[OSD([subQ0,subQ9]),TDD([makeQuery(id+"F42.boolean.opBoolean","COPY",EDGE,{"disambiguationData":[TD([subQ33])],"derivedFrom":subQ11})])]}),makeQuery(id+"F47.opFillet","BLEND_FACE",FACE,{"disambiguationData":[OSD([subQ0,subQ9]),TDD([makeQuery(id+"F42.boolean.opBoolean","COPY",EDGE,{"disambiguationData":[TD([subQ26])],"derivedFrom":subQ11})])]}),makeQuery(id+"F47.opFillet","BLEND_FACE",FACE,{"disambiguationData":[OSD([subQ0,subQ9]),TDD([makeQuery(id+"F42.boolean.opBoolean","COPY",EDGE,{"disambiguationData":[TD([subQ17])],"derivedFrom":subQ11})])]}),makeQuery(id+"F47.opFillet","BLEND_FACE",FACE,{"disambiguationData":[OSD([subQ0,subQ9]),TDD([makeQuery(id+"F42.boolean.opBoolean","COPY",EDGE,{"disambiguationData":[TD([makeQuery(id+"F38.opLoft","SWEPT_FACE",FACE,{"disambiguationData":[OSD([subQ8,subQ7,subQ5,sQuery(id+"F22.wireOp",EDGE,"E28.15.1"),subQ4,subQ3])]})])],"derivedFrom":subQ11})])]})],"blendedInto":[makeQuery(id+"F47.opFillet","BLEND_FACE",FACE,{"disambiguationData":[OSD([subQ0,subQ9]),TDD([makeQuery(id+"F42.boolean.opBoolean","COPY",EDGE,{"disambiguationData":[TD([makeQuery(id+"F23.opLoft","SWEPT_FACE",FACE,{"disambiguationData":[OSD([sQuery(id+"F3.wireOp",EDGE,"E20.8.0"),subQ114,subQ112,subQ111,subQ110,sQuery(id+"F22.wireOp",EDGE,"E27.right")])]})])],"derivedFrom":subQ11})])]}),makeQuery(id+"F47.opFillet","BLEND_FACE",FACE,{"disambiguationData":[OSD([subQ0,subQ9]),TDD([makeQuery(id+"F42.boolean.opBoolean","COPY",EDGE,{"disambiguationData":[TD([subQ109])],"derivedFrom":subQ11})])]}),makeQuery(id+"F47.opFillet","BLEND_FACE",FACE,{"disambiguationData":[OSD([subQ0,subQ9]),TDD([makeQuery(id+"F42.boolean.opBoolean","COPY",EDGE,{"disambiguationData":[TD([subQ102])],"derivedFrom":subQ11})])]}),makeQuery(id+"F47.opFillet","BLEND_FACE",FACE,{"disambiguationData":[OSD([subQ0,subQ9]),TDD([makeQuery(id+"F42.boolean.opBoolean","COPY",EDGE,{"disambiguationData":[TD([subQ96])],"derivedFrom":subQ11})])]}),makeQuery(id+"F47.opFillet","BLEND_FACE",FACE,{"disambiguationData":[OSD([subQ0,subQ9]),TDD([makeQuery(id+"F42.boolean.opBoolean","COPY",EDGE,{"disambiguationData":[TD([subQ89])],"derivedFrom":subQ11})])]}),makeQuery(id+"F47.opFillet","BLEND_FACE",FACE,{"disambiguationData":[OSD([subQ0,subQ9]),TDD([makeQuery(id+"F42.boolean.opBoolean","COPY",EDGE,{"disambiguationData":[TD([subQ82])],"derivedFrom":subQ11})])]}),makeQuery(id+"F47.opFillet","BLEND_FACE",FACE,{"disambiguationData":[OSD([subQ0,subQ9]),TDD([makeQuery(id+"F42.boolean.opBoolean","COPY",EDGE,{"disambiguationData":[TD([subQ75])],"derivedFrom":subQ11})])]}),makeQuery(id+"F47.opFillet","BLEND_FACE",FACE,{"disambiguationData":[OSD([subQ0,subQ9]),TDD([makeQuery(id+"F42.boolean.opBoolean","COPY",EDGE,{"disambiguationData":[TD([subQ67])],"derivedFrom":subQ11})])]}),makeQuery(id+"F47.opFillet","BLEND_FACE",FACE,{"disambiguationData":[OSD([subQ0,subQ9]),TDD([makeQuery(id+"F42.boolean.opBoolean","COPY",EDGE,{"disambiguationData":[TD([subQ61])],"derivedFrom":subQ11})])]}),makeQuery(id+"F47.opFillet","BLEND_FACE",FACE,{"disambiguationData":[OSD([subQ0,subQ9]),TDD([makeQuery(id+"F42.boolean.opBoolean","COPY",EDGE,{"disambiguationData":[TD([subQ54])],"derivedFrom":subQ11})])]}),makeQuery(id+"F47.opFillet","BLEND_FACE",FACE,{"disambiguationData":[OSD([subQ0,subQ9]),TDD([makeQuery(id+"F42.boolean.opBoolean","COPY",EDGE,{"disambiguationData":[TD([subQ47])],"derivedFrom":subQ11})])]}),makeQuery(id+"F47.opFillet","BLEND_FACE",FACE,{"disambiguationData":[OSD([subQ0,subQ9]),TDD([makeQuery(id+"F42.boolean.opBoolean","COPY",EDGE,{"disambiguationData":[TD([subQ40])],"derivedFrom":subQ11})])]}),makeQuery(id+"F47.opFillet","BLEND_FACE",FACE,{"disambiguationData":[OSD([subQ0,subQ9]),TDD([makeQuery(id+"F42.boolean.opBoolean","COPY",EDGE,{"disambiguationData":[TD([subQ33])],"derivedFrom":subQ11})])]}),makeQuery(id+"F47.opFillet","BLEND_FACE",FACE,{"disambiguationData":[OSD([subQ0,subQ9]),TDD([makeQuery(id+"F42.boolean.opBoolean","COPY",EDGE,{"disambiguationData":[TD([subQ26])],"derivedFrom":subQ11})])]}),makeQuery(id+"F47.opFillet","BLEND_FACE",FACE,{"disambiguationData":[OSD([subQ0,subQ9]),TDD([makeQuery(id+"F42.boolean.opBoolean","COPY",EDGE,{"disambiguationData":[TD([subQ17])],"derivedFrom":subQ11})])]}),makeQuery(id+"F47.opFillet","BLEND_FACE",FACE,{"disambiguationData":[OSD([subQ0,subQ9]),TDD([makeQuery(id+"F42.boolean.opBoolean","COPY",EDGE,{"disambiguationData":[TD([makeQuery(id+"F38.opLoft","SWEPT_FACE",FACE,{"disambiguationData":[OSD([subQ8,subQ7,subQ5,sQuery(id+"F22.wireOp",EDGE,"E28.15.1"),subQ4,subQ3])]})])],"derivedFrom":subQ11})])]})]});}
            var Q48;
            {var subQ0=makeQuery(id+"F40.opExtrude","CAP_FACE",FACE,{"disambiguationData":[OSD([sQuery(id+"F39.wireOp",EDGE,"E29"),sQuery(id+"F39.wireOp",EDGE,"E30")])],"isStart":false});var subQ1=sQuery(id+"F4.wireOp",EDGE,"E26.1.3");var subQ2=sQuery(id+"F4.wireOp",EDGE,"E26.1.2");var subQ3=sQuery(id+"F3.wireOp",EDGE,"E20.1.3");var subQ4=sQuery(id+"F3.wireOp",EDGE,"E20.1.1");var subQ5=sQuery(id+"F41.wireOp",EDGE,"E35");var subQ6=makeQuery(id+"F42.opRevolve","SWEPT_FACE",FACE,{"disambiguationData":[OSD([subQ5])]});var subQ7=sQuery(id+"F41.wireOp",EDGE,"E36");var subQ8=makeQuery(id+"F42.opRevolve","SWEPT_FACE",FACE,{"disambiguationData":[OSD([subQ7])]});var subQ9=makeQuery(id+"F42.opRevolve","SWEPT_EDGE",EDGE,{"disambiguationData":[OSD([subQ5,subQ7])]});var subQ10=sQuery(id+"F4.wireOp",EDGE,"E26.2.3");var subQ11=sQuery(id+"F4.wireOp",EDGE,"E26.2.2");var subQ12=sQuery(id+"F3.wireOp",EDGE,"E20.2.3");var subQ13=sQuery(id+"F3.wireOp",EDGE,"E20.2.1");var subQ14=sQuery(id+"F4.wireOp",EDGE,"E26.3.3");var subQ15=sQuery(id+"F4.wireOp",EDGE,"E26.3.2");var subQ16=sQuery(id+"F3.wireOp",EDGE,"E20.3.3");var subQ17=sQuery(id+"F3.wireOp",EDGE,"E20.3.1");var subQ18=sQuery(id+"F4.wireOp",EDGE,"E26.4.3");var subQ19=sQuery(id+"F4.wireOp",EDGE,"E26.4.2");var subQ20=sQuery(id+"F3.wireOp",EDGE,"E20.4.3");var subQ21=sQuery(id+"F3.wireOp",EDGE,"E20.4.1");var subQ22=sQuery(id+"F4.wireOp",EDGE,"E26.5.3");var subQ23=sQuery(id+"F4.wireOp",EDGE,"E26.5.2");var subQ24=sQuery(id+"F3.wireOp",EDGE,"E20.5.3");var subQ25=sQuery(id+"F3.wireOp",EDGE,"E20.5.1");var subQ26=sQuery(id+"F4.wireOp",EDGE,"E26.6.3");var subQ27=sQuery(id+"F4.wireOp",EDGE,"E26.6.2");var subQ28=sQuery(id+"F3.wireOp",EDGE,"E20.6.3");var subQ29=sQuery(id+"F3.wireOp",EDGE,"E20.6.1");var subQ31=makeQuery(id+"F15.opLoft","SWEPT_FACE",FACE,{"disambiguationData":[OSD([sQuery(id+"F3.wireOp",EDGE,"E20.6.0"),subQ29,subQ28,sQuery(id+"F4.wireOp",EDGE,"E26.6.0"),subQ27,subQ26])]});var subQ32=sQuery(id+"F4.wireOp",EDGE,"E26.7.3");var subQ33=sQuery(id+"F4.wireOp",EDGE,"E26.7.2");var subQ34=sQuery(id+"F3.wireOp",EDGE,"E20.7.3");var subQ35=sQuery(id+"F3.wireOp",EDGE,"E20.7.1");var subQ36=sQuery(id+"F4.wireOp",EDGE,"E26.8.3");var subQ37=sQuery(id+"F4.wireOp",EDGE,"E26.8.2");var subQ38=sQuery(id+"F3.wireOp",EDGE,"E20.8.3");var subQ39=sQuery(id+"F3.wireOp",EDGE,"E20.8.1");var subQ40=sQuery(id+"F4.wireOp",EDGE,"E26.9.3");var subQ41=sQuery(id+"F4.wireOp",EDGE,"E26.9.2");var subQ42=sQuery(id+"F3.wireOp",EDGE,"E20.9.3");var subQ43=sQuery(id+"F3.wireOp",EDGE,"E20.9.1");var subQ44=sQuery(id+"F4.wireOp",EDGE,"E26.10.3");var subQ45=sQuery(id+"F4.wireOp",EDGE,"E26.10.2");var subQ46=sQuery(id+"F3.wireOp",EDGE,"E20.10.3");var subQ47=sQuery(id+"F3.wireOp",EDGE,"E20.10.1");var subQ48=sQuery(id+"F4.wireOp",EDGE,"E26.11.3");var subQ49=sQuery(id+"F4.wireOp",EDGE,"E26.11.2");var subQ50=sQuery(id+"F3.wireOp",EDGE,"E20.11.3");var subQ51=sQuery(id+"F3.wireOp",EDGE,"E20.11.1");var subQ52=sQuery(id+"F4.wireOp",EDGE,"E26.12.3");var subQ53=sQuery(id+"F4.wireOp",EDGE,"E26.12.2");var subQ54=sQuery(id+"F3.wireOp",EDGE,"E20.12.3");var subQ55=sQuery(id+"F3.wireOp",EDGE,"E20.12.1");var subQ56=sQuery(id+"F4.wireOp",EDGE,"E26.13.3");var subQ57=sQuery(id+"F4.wireOp",EDGE,"E26.13.2");var subQ58=sQuery(id+"F3.wireOp",EDGE,"E20.13.3");var subQ59=sQuery(id+"F3.wireOp",EDGE,"E20.13.1");var subQ60=sQuery(id+"F4.wireOp",EDGE,"E26.14.3");var subQ61=sQuery(id+"F4.wireOp",EDGE,"E26.14.2");var subQ62=sQuery(id+"F3.wireOp",EDGE,"E20.14.3");var subQ63=sQuery(id+"F3.wireOp",EDGE,"E20.14.1");var subQ64=sQuery(id+"F4.wireOp",EDGE,"E26.15.3");var subQ65=sQuery(id+"F4.wireOp",EDGE,"E26.15.2");var subQ66=sQuery(id+"F3.wireOp",EDGE,"E20.15.3");var subQ67=sQuery(id+"F3.wireOp",EDGE,"E20.15.1");var subQ68=sQuery(id+"F4.wireOp",EDGE,"E23");var subQ69=sQuery(id+"F4.wireOp",EDGE,"E22");var subQ70=sQuery(id+"F3.wireOp",EDGE,"E18.top");var subQ71=sQuery(id+"F3.wireOp",EDGE,"E18.bottom");var subQ74=makeQuery(id+"F42.boolean.opBoolean","COPY",FACE,{"disambiguationData":[TD([subQ31])],"derivedFrom":subQ6});var subQ75=makeQuery(id+"F15.boolean.opBoolean","INTERSECT",EDGE,{"derivedFrom":[makeQuery(id+"F1.opRevolve","SWEPT_FACE",FACE,{"disambiguationData":[OSD([sQuery(id+"F0.wireOp",EDGE,"E4")])]}),subQ31]});Q48=makeQuery(id+"F48.opFillet","BLEND_EDGE",EDGE,{"blendedFrom":[makeQuery(id+"F47.opFillet","TWEAK_EDGE",EDGE,{"derivedFrom":[makeQuery(id+"F45.opFillet","BLEND_VERTEX",VERTEX,{"blendedFrom":[subQ75,subQ31,subQ74],"blendedInto":[subQ31,subQ74]}),makeQuery(id+"F45.opFillet","BLEND_VERTEX",VERTEX,{"blendedFrom":[subQ75,makeQuery(id+"F42.boolean.opBoolean","MERGE",FACE,{"derivedFrom":[subQ0,subQ8]}),subQ74],"blendedInto":[makeQuery(id+"F42.boolean.opBoolean","MERGE",FACE,{"derivedFrom":[subQ0,subQ8]}),subQ74]})]}),makeQuery(id+"F47.opFillet","BLEND_FACE",FACE,{"disambiguationData":[OSD([subQ5,subQ7]),TDD([makeQuery(id+"F42.boolean.opBoolean","COPY",EDGE,{"disambiguationData":[TD([makeQuery(id+"F5.opLoft","SWEPT_FACE",FACE,{"disambiguationData":[OSD([subQ71,subQ70,sQuery(id+"F3.wireOp",EDGE,"E18.left"),sQuery(id+"F4.wireOp",EDGE,"E21"),subQ69,subQ68])]})])],"derivedFrom":subQ9})])]}),makeQuery(id+"F47.opFillet","BLEND_FACE",FACE,{"disambiguationData":[OSD([subQ5,subQ7]),TDD([makeQuery(id+"F42.boolean.opBoolean","COPY",EDGE,{"disambiguationData":[TD([makeQuery(id+"F6.opLoft","SWEPT_FACE",FACE,{"disambiguationData":[OSD([sQuery(id+"F3.wireOp",EDGE,"E20.15.0"),subQ67,subQ66,sQuery(id+"F4.wireOp",EDGE,"E26.15.0"),subQ65,subQ64])]})])],"derivedFrom":subQ9})])]}),makeQuery(id+"F47.opFillet","BLEND_FACE",FACE,{"disambiguationData":[OSD([subQ5,subQ7]),TDD([makeQuery(id+"F42.boolean.opBoolean","COPY",EDGE,{"disambiguationData":[TD([makeQuery(id+"F7.opLoft","SWEPT_FACE",FACE,{"disambiguationData":[OSD([sQuery(id+"F3.wireOp",EDGE,"E20.14.0"),subQ63,subQ62,sQuery(id+"F4.wireOp",EDGE,"E26.14.0"),subQ61,subQ60])]})])],"derivedFrom":subQ9})])]}),makeQuery(id+"F47.opFillet","BLEND_FACE",FACE,{"disambiguationData":[OSD([subQ5,subQ7]),TDD([makeQuery(id+"F42.boolean.opBoolean","COPY",EDGE,{"disambiguationData":[TD([makeQuery(id+"F8.opLoft","SWEPT_FACE",FACE,{"disambiguationData":[OSD([sQuery(id+"F3.wireOp",EDGE,"E20.13.0"),subQ59,subQ58,sQuery(id+"F4.wireOp",EDGE,"E26.13.0"),subQ57,subQ56])]})])],"derivedFrom":subQ9})])]}),makeQuery(id+"F47.opFillet","BLEND_FACE",FACE,{"disambiguationData":[OSD([subQ5,subQ7]),TDD([makeQuery(id+"F42.boolean.opBoolean","COPY",EDGE,{"disambiguationData":[TD([makeQuery(id+"F9.opLoft","SWEPT_FACE",FACE,{"disambiguationData":[OSD([sQuery(id+"F3.wireOp",EDGE,"E20.12.0"),subQ55,subQ54,sQuery(id+"F4.wireOp",EDGE,"E26.12.0"),subQ53,subQ52])]})])],"derivedFrom":subQ9})])]}),makeQuery(id+"F47.opFillet","BLEND_FACE",FACE,{"disambiguationData":[OSD([subQ5,subQ7]),TDD([makeQuery(id+"F42.boolean.opBoolean","COPY",EDGE,{"disambiguationData":[TD([makeQuery(id+"F10.opLoft","SWEPT_FACE",FACE,{"disambiguationData":[OSD([sQuery(id+"F3.wireOp",EDGE,"E20.11.0"),subQ51,subQ50,sQuery(id+"F4.wireOp",EDGE,"E26.11.0"),subQ49,subQ48])]})])],"derivedFrom":subQ9})])]}),makeQuery(id+"F47.opFillet","BLEND_FACE",FACE,{"disambiguationData":[OSD([subQ5,subQ7]),TDD([makeQuery(id+"F42.boolean.opBoolean","COPY",EDGE,{"disambiguationData":[TD([makeQuery(id+"F11.opLoft","SWEPT_FACE",FACE,{"disambiguationData":[OSD([sQuery(id+"F3.wireOp",EDGE,"E20.10.0"),subQ47,subQ46,sQuery(id+"F4.wireOp",EDGE,"E26.10.0"),subQ45,subQ44])]})])],"derivedFrom":subQ9})])]}),makeQuery(id+"F47.opFillet","BLEND_FACE",FACE,{"disambiguationData":[OSD([subQ5,subQ7]),TDD([makeQuery(id+"F42.boolean.opBoolean","COPY",EDGE,{"disambiguationData":[TD([makeQuery(id+"F12.opLoft","SWEPT_FACE",FACE,{"disambiguationData":[OSD([sQuery(id+"F3.wireOp",EDGE,"E20.9.0"),subQ43,subQ42,sQuery(id+"F4.wireOp",EDGE,"E26.9.0"),subQ41,subQ40])]})])],"derivedFrom":subQ9})])]}),makeQuery(id+"F47.opFillet","BLEND_FACE",FACE,{"disambiguationData":[OSD([subQ5,subQ7]),TDD([makeQuery(id+"F42.boolean.opBoolean","COPY",EDGE,{"disambiguationData":[TD([makeQuery(id+"F13.opLoft","SWEPT_FACE",FACE,{"disambiguationData":[OSD([sQuery(id+"F3.wireOp",EDGE,"E20.8.0"),subQ39,subQ38,sQuery(id+"F4.wireOp",EDGE,"E26.8.0"),subQ37,subQ36])]})])],"derivedFrom":subQ9})])]}),makeQuery(id+"F47.opFillet","BLEND_FACE",FACE,{"disambiguationData":[OSD([subQ5,subQ7]),TDD([makeQuery(id+"F42.boolean.opBoolean","COPY",EDGE,{"disambiguationData":[TD([makeQuery(id+"F14.opLoft","SWEPT_FACE",FACE,{"disambiguationData":[OSD([sQuery(id+"F3.wireOp",EDGE,"E20.7.0"),subQ35,subQ34,sQuery(id+"F4.wireOp",EDGE,"E26.7.0"),subQ33,subQ32])]})])],"derivedFrom":subQ9})])]}),makeQuery(id+"F47.opFillet","BLEND_FACE",FACE,{"disambiguationData":[OSD([subQ5,subQ7]),TDD([makeQuery(id+"F42.boolean.opBoolean","COPY",EDGE,{"disambiguationData":[TD([subQ31])],"derivedFrom":subQ9})])]}),makeQuery(id+"F47.opFillet","BLEND_FACE",FACE,{"disambiguationData":[OSD([subQ5,subQ7]),TDD([makeQuery(id+"F42.boolean.opBoolean","COPY",EDGE,{"disambiguationData":[TD([makeQuery(id+"F16.opLoft","SWEPT_FACE",FACE,{"disambiguationData":[OSD([sQuery(id+"F3.wireOp",EDGE,"E20.5.0"),subQ25,subQ24,sQuery(id+"F4.wireOp",EDGE,"E26.5.0"),subQ23,subQ22])]})])],"derivedFrom":subQ9})])]}),makeQuery(id+"F47.opFillet","BLEND_FACE",FACE,{"disambiguationData":[OSD([subQ5,subQ7]),TDD([makeQuery(id+"F42.boolean.opBoolean","COPY",EDGE,{"disambiguationData":[TD([makeQuery(id+"F17.opLoft","SWEPT_FACE",FACE,{"disambiguationData":[OSD([sQuery(id+"F3.wireOp",EDGE,"E20.4.0"),subQ21,subQ20,sQuery(id+"F4.wireOp",EDGE,"E26.4.0"),subQ19,subQ18])]})])],"derivedFrom":subQ9})])]}),makeQuery(id+"F47.opFillet","BLEND_FACE",FACE,{"disambiguationData":[OSD([subQ5,subQ7]),TDD([makeQuery(id+"F42.boolean.opBoolean","COPY",EDGE,{"disambiguationData":[TD([makeQuery(id+"F18.opLoft","SWEPT_FACE",FACE,{"disambiguationData":[OSD([sQuery(id+"F3.wireOp",EDGE,"E20.3.0"),subQ17,subQ16,sQuery(id+"F4.wireOp",EDGE,"E26.3.0"),subQ15,subQ14])]})])],"derivedFrom":subQ9})])]}),makeQuery(id+"F47.opFillet","BLEND_FACE",FACE,{"disambiguationData":[OSD([subQ5,subQ7]),TDD([makeQuery(id+"F42.boolean.opBoolean","COPY",EDGE,{"disambiguationData":[TD([makeQuery(id+"F19.opLoft","SWEPT_FACE",FACE,{"disambiguationData":[OSD([sQuery(id+"F3.wireOp",EDGE,"E20.2.0"),subQ13,subQ12,sQuery(id+"F4.wireOp",EDGE,"E26.2.0"),subQ11,subQ10])]})])],"derivedFrom":subQ9})])]}),makeQuery(id+"F47.opFillet","BLEND_FACE",FACE,{"disambiguationData":[OSD([subQ5,subQ7]),TDD([makeQuery(id+"F42.boolean.opBoolean","COPY",EDGE,{"disambiguationData":[TD([makeQuery(id+"F20.opLoft","SWEPT_FACE",FACE,{"disambiguationData":[OSD([sQuery(id+"F3.wireOp",EDGE,"E20.1.0"),subQ4,subQ3,sQuery(id+"F4.wireOp",EDGE,"E26.1.0"),subQ2,subQ1])]})])],"derivedFrom":subQ9})])]})],"blendedInto":[makeQuery(id+"F47.opFillet","BLEND_FACE",FACE,{"disambiguationData":[OSD([subQ5,subQ7]),TDD([makeQuery(id+"F42.boolean.opBoolean","COPY",EDGE,{"disambiguationData":[TD([makeQuery(id+"F5.opLoft","SWEPT_FACE",FACE,{"disambiguationData":[OSD([subQ71,subQ70,sQuery(id+"F3.wireOp",EDGE,"E18.left"),sQuery(id+"F4.wireOp",EDGE,"E21"),subQ69,subQ68])]})])],"derivedFrom":subQ9})])]}),makeQuery(id+"F47.opFillet","BLEND_FACE",FACE,{"disambiguationData":[OSD([subQ5,subQ7]),TDD([makeQuery(id+"F42.boolean.opBoolean","COPY",EDGE,{"disambiguationData":[TD([makeQuery(id+"F6.opLoft","SWEPT_FACE",FACE,{"disambiguationData":[OSD([sQuery(id+"F3.wireOp",EDGE,"E20.15.0"),subQ67,subQ66,sQuery(id+"F4.wireOp",EDGE,"E26.15.0"),subQ65,subQ64])]})])],"derivedFrom":subQ9})])]}),makeQuery(id+"F47.opFillet","BLEND_FACE",FACE,{"disambiguationData":[OSD([subQ5,subQ7]),TDD([makeQuery(id+"F42.boolean.opBoolean","COPY",EDGE,{"disambiguationData":[TD([makeQuery(id+"F7.opLoft","SWEPT_FACE",FACE,{"disambiguationData":[OSD([sQuery(id+"F3.wireOp",EDGE,"E20.14.0"),subQ63,subQ62,sQuery(id+"F4.wireOp",EDGE,"E26.14.0"),subQ61,subQ60])]})])],"derivedFrom":subQ9})])]}),makeQuery(id+"F47.opFillet","BLEND_FACE",FACE,{"disambiguationData":[OSD([subQ5,subQ7]),TDD([makeQuery(id+"F42.boolean.opBoolean","COPY",EDGE,{"disambiguationData":[TD([makeQuery(id+"F8.opLoft","SWEPT_FACE",FACE,{"disambiguationData":[OSD([sQuery(id+"F3.wireOp",EDGE,"E20.13.0"),subQ59,subQ58,sQuery(id+"F4.wireOp",EDGE,"E26.13.0"),subQ57,subQ56])]})])],"derivedFrom":subQ9})])]}),makeQuery(id+"F47.opFillet","BLEND_FACE",FACE,{"disambiguationData":[OSD([subQ5,subQ7]),TDD([makeQuery(id+"F42.boolean.opBoolean","COPY",EDGE,{"disambiguationData":[TD([makeQuery(id+"F9.opLoft","SWEPT_FACE",FACE,{"disambiguationData":[OSD([sQuery(id+"F3.wireOp",EDGE,"E20.12.0"),subQ55,subQ54,sQuery(id+"F4.wireOp",EDGE,"E26.12.0"),subQ53,subQ52])]})])],"derivedFrom":subQ9})])]}),makeQuery(id+"F47.opFillet","BLEND_FACE",FACE,{"disambiguationData":[OSD([subQ5,subQ7]),TDD([makeQuery(id+"F42.boolean.opBoolean","COPY",EDGE,{"disambiguationData":[TD([makeQuery(id+"F10.opLoft","SWEPT_FACE",FACE,{"disambiguationData":[OSD([sQuery(id+"F3.wireOp",EDGE,"E20.11.0"),subQ51,subQ50,sQuery(id+"F4.wireOp",EDGE,"E26.11.0"),subQ49,subQ48])]})])],"derivedFrom":subQ9})])]}),makeQuery(id+"F47.opFillet","BLEND_FACE",FACE,{"disambiguationData":[OSD([subQ5,subQ7]),TDD([makeQuery(id+"F42.boolean.opBoolean","COPY",EDGE,{"disambiguationData":[TD([makeQuery(id+"F11.opLoft","SWEPT_FACE",FACE,{"disambiguationData":[OSD([sQuery(id+"F3.wireOp",EDGE,"E20.10.0"),subQ47,subQ46,sQuery(id+"F4.wireOp",EDGE,"E26.10.0"),subQ45,subQ44])]})])],"derivedFrom":subQ9})])]}),makeQuery(id+"F47.opFillet","BLEND_FACE",FACE,{"disambiguationData":[OSD([subQ5,subQ7]),TDD([makeQuery(id+"F42.boolean.opBoolean","COPY",EDGE,{"disambiguationData":[TD([makeQuery(id+"F12.opLoft","SWEPT_FACE",FACE,{"disambiguationData":[OSD([sQuery(id+"F3.wireOp",EDGE,"E20.9.0"),subQ43,subQ42,sQuery(id+"F4.wireOp",EDGE,"E26.9.0"),subQ41,subQ40])]})])],"derivedFrom":subQ9})])]}),makeQuery(id+"F47.opFillet","BLEND_FACE",FACE,{"disambiguationData":[OSD([subQ5,subQ7]),TDD([makeQuery(id+"F42.boolean.opBoolean","COPY",EDGE,{"disambiguationData":[TD([makeQuery(id+"F13.opLoft","SWEPT_FACE",FACE,{"disambiguationData":[OSD([sQuery(id+"F3.wireOp",EDGE,"E20.8.0"),subQ39,subQ38,sQuery(id+"F4.wireOp",EDGE,"E26.8.0"),subQ37,subQ36])]})])],"derivedFrom":subQ9})])]}),makeQuery(id+"F47.opFillet","BLEND_FACE",FACE,{"disambiguationData":[OSD([subQ5,subQ7]),TDD([makeQuery(id+"F42.boolean.opBoolean","COPY",EDGE,{"disambiguationData":[TD([makeQuery(id+"F14.opLoft","SWEPT_FACE",FACE,{"disambiguationData":[OSD([sQuery(id+"F3.wireOp",EDGE,"E20.7.0"),subQ35,subQ34,sQuery(id+"F4.wireOp",EDGE,"E26.7.0"),subQ33,subQ32])]})])],"derivedFrom":subQ9})])]}),makeQuery(id+"F47.opFillet","BLEND_FACE",FACE,{"disambiguationData":[OSD([subQ5,subQ7]),TDD([makeQuery(id+"F42.boolean.opBoolean","COPY",EDGE,{"disambiguationData":[TD([subQ31])],"derivedFrom":subQ9})])]}),makeQuery(id+"F47.opFillet","BLEND_FACE",FACE,{"disambiguationData":[OSD([subQ5,subQ7]),TDD([makeQuery(id+"F42.boolean.opBoolean","COPY",EDGE,{"disambiguationData":[TD([makeQuery(id+"F16.opLoft","SWEPT_FACE",FACE,{"disambiguationData":[OSD([sQuery(id+"F3.wireOp",EDGE,"E20.5.0"),subQ25,subQ24,sQuery(id+"F4.wireOp",EDGE,"E26.5.0"),subQ23,subQ22])]})])],"derivedFrom":subQ9})])]}),makeQuery(id+"F47.opFillet","BLEND_FACE",FACE,{"disambiguationData":[OSD([subQ5,subQ7]),TDD([makeQuery(id+"F42.boolean.opBoolean","COPY",EDGE,{"disambiguationData":[TD([makeQuery(id+"F17.opLoft","SWEPT_FACE",FACE,{"disambiguationData":[OSD([sQuery(id+"F3.wireOp",EDGE,"E20.4.0"),subQ21,subQ20,sQuery(id+"F4.wireOp",EDGE,"E26.4.0"),subQ19,subQ18])]})])],"derivedFrom":subQ9})])]}),makeQuery(id+"F47.opFillet","BLEND_FACE",FACE,{"disambiguationData":[OSD([subQ5,subQ7]),TDD([makeQuery(id+"F42.boolean.opBoolean","COPY",EDGE,{"disambiguationData":[TD([makeQuery(id+"F18.opLoft","SWEPT_FACE",FACE,{"disambiguationData":[OSD([sQuery(id+"F3.wireOp",EDGE,"E20.3.0"),subQ17,subQ16,sQuery(id+"F4.wireOp",EDGE,"E26.3.0"),subQ15,subQ14])]})])],"derivedFrom":subQ9})])]}),makeQuery(id+"F47.opFillet","BLEND_FACE",FACE,{"disambiguationData":[OSD([subQ5,subQ7]),TDD([makeQuery(id+"F42.boolean.opBoolean","COPY",EDGE,{"disambiguationData":[TD([makeQuery(id+"F19.opLoft","SWEPT_FACE",FACE,{"disambiguationData":[OSD([sQuery(id+"F3.wireOp",EDGE,"E20.2.0"),subQ13,subQ12,sQuery(id+"F4.wireOp",EDGE,"E26.2.0"),subQ11,subQ10])]})])],"derivedFrom":subQ9})])]}),makeQuery(id+"F47.opFillet","BLEND_FACE",FACE,{"disambiguationData":[OSD([subQ5,subQ7]),TDD([makeQuery(id+"F42.boolean.opBoolean","COPY",EDGE,{"disambiguationData":[TD([makeQuery(id+"F20.opLoft","SWEPT_FACE",FACE,{"disambiguationData":[OSD([sQuery(id+"F3.wireOp",EDGE,"E20.1.0"),subQ4,subQ3,sQuery(id+"F4.wireOp",EDGE,"E26.1.0"),subQ2,subQ1])]})])],"derivedFrom":subQ9})])]})]});}
            var Q49;
            {var subQ0=makeQuery(id+"F40.opExtrude","CAP_FACE",FACE,{"disambiguationData":[OSD([sQuery(id+"F39.wireOp",EDGE,"E29"),sQuery(id+"F39.wireOp",EDGE,"E30")])],"isStart":false});var subQ1=sQuery(id+"F4.wireOp",EDGE,"E26.1.3");var subQ2=sQuery(id+"F4.wireOp",EDGE,"E26.1.2");var subQ3=sQuery(id+"F3.wireOp",EDGE,"E20.1.3");var subQ4=sQuery(id+"F3.wireOp",EDGE,"E20.1.1");var subQ5=sQuery(id+"F41.wireOp",EDGE,"E35");var subQ6=makeQuery(id+"F42.opRevolve","SWEPT_FACE",FACE,{"disambiguationData":[OSD([subQ5])]});var subQ7=sQuery(id+"F41.wireOp",EDGE,"E36");var subQ8=makeQuery(id+"F42.opRevolve","SWEPT_FACE",FACE,{"disambiguationData":[OSD([subQ7])]});var subQ9=makeQuery(id+"F42.opRevolve","SWEPT_EDGE",EDGE,{"disambiguationData":[OSD([subQ5,subQ7])]});var subQ10=sQuery(id+"F4.wireOp",EDGE,"E26.2.3");var subQ11=sQuery(id+"F4.wireOp",EDGE,"E26.2.2");var subQ12=sQuery(id+"F3.wireOp",EDGE,"E20.2.3");var subQ13=sQuery(id+"F3.wireOp",EDGE,"E20.2.1");var subQ14=sQuery(id+"F4.wireOp",EDGE,"E26.3.3");var subQ15=sQuery(id+"F4.wireOp",EDGE,"E26.3.2");var subQ16=sQuery(id+"F3.wireOp",EDGE,"E20.3.3");var subQ17=sQuery(id+"F3.wireOp",EDGE,"E20.3.1");var subQ18=sQuery(id+"F4.wireOp",EDGE,"E26.4.3");var subQ19=sQuery(id+"F4.wireOp",EDGE,"E26.4.2");var subQ20=sQuery(id+"F3.wireOp",EDGE,"E20.4.3");var subQ21=sQuery(id+"F3.wireOp",EDGE,"E20.4.1");var subQ22=sQuery(id+"F4.wireOp",EDGE,"E26.5.3");var subQ23=sQuery(id+"F4.wireOp",EDGE,"E26.5.2");var subQ24=sQuery(id+"F3.wireOp",EDGE,"E20.5.3");var subQ25=sQuery(id+"F3.wireOp",EDGE,"E20.5.1");var subQ27=makeQuery(id+"F16.opLoft","SWEPT_FACE",FACE,{"disambiguationData":[OSD([sQuery(id+"F3.wireOp",EDGE,"E20.5.0"),subQ25,subQ24,sQuery(id+"F4.wireOp",EDGE,"E26.5.0"),subQ23,subQ22])]});var subQ28=sQuery(id+"F4.wireOp",EDGE,"E26.6.3");var subQ29=sQuery(id+"F4.wireOp",EDGE,"E26.6.2");var subQ30=sQuery(id+"F3.wireOp",EDGE,"E20.6.3");var subQ31=sQuery(id+"F3.wireOp",EDGE,"E20.6.1");var subQ32=sQuery(id+"F4.wireOp",EDGE,"E26.7.3");var subQ33=sQuery(id+"F4.wireOp",EDGE,"E26.7.2");var subQ34=sQuery(id+"F3.wireOp",EDGE,"E20.7.3");var subQ35=sQuery(id+"F3.wireOp",EDGE,"E20.7.1");var subQ36=sQuery(id+"F4.wireOp",EDGE,"E26.8.3");var subQ37=sQuery(id+"F4.wireOp",EDGE,"E26.8.2");var subQ38=sQuery(id+"F3.wireOp",EDGE,"E20.8.3");var subQ39=sQuery(id+"F3.wireOp",EDGE,"E20.8.1");var subQ40=sQuery(id+"F4.wireOp",EDGE,"E26.9.3");var subQ41=sQuery(id+"F4.wireOp",EDGE,"E26.9.2");var subQ42=sQuery(id+"F3.wireOp",EDGE,"E20.9.3");var subQ43=sQuery(id+"F3.wireOp",EDGE,"E20.9.1");var subQ44=sQuery(id+"F4.wireOp",EDGE,"E26.10.3");var subQ45=sQuery(id+"F4.wireOp",EDGE,"E26.10.2");var subQ46=sQuery(id+"F3.wireOp",EDGE,"E20.10.3");var subQ47=sQuery(id+"F3.wireOp",EDGE,"E20.10.1");var subQ48=sQuery(id+"F4.wireOp",EDGE,"E26.11.3");var subQ49=sQuery(id+"F4.wireOp",EDGE,"E26.11.2");var subQ50=sQuery(id+"F3.wireOp",EDGE,"E20.11.3");var subQ51=sQuery(id+"F3.wireOp",EDGE,"E20.11.1");var subQ52=sQuery(id+"F4.wireOp",EDGE,"E26.12.3");var subQ53=sQuery(id+"F4.wireOp",EDGE,"E26.12.2");var subQ54=sQuery(id+"F3.wireOp",EDGE,"E20.12.3");var subQ55=sQuery(id+"F3.wireOp",EDGE,"E20.12.1");var subQ56=sQuery(id+"F4.wireOp",EDGE,"E26.13.3");var subQ57=sQuery(id+"F4.wireOp",EDGE,"E26.13.2");var subQ58=sQuery(id+"F3.wireOp",EDGE,"E20.13.3");var subQ59=sQuery(id+"F3.wireOp",EDGE,"E20.13.1");var subQ60=sQuery(id+"F4.wireOp",EDGE,"E26.14.3");var subQ61=sQuery(id+"F4.wireOp",EDGE,"E26.14.2");var subQ62=sQuery(id+"F3.wireOp",EDGE,"E20.14.3");var subQ63=sQuery(id+"F3.wireOp",EDGE,"E20.14.1");var subQ64=sQuery(id+"F4.wireOp",EDGE,"E26.15.3");var subQ65=sQuery(id+"F4.wireOp",EDGE,"E26.15.2");var subQ66=sQuery(id+"F3.wireOp",EDGE,"E20.15.3");var subQ67=sQuery(id+"F3.wireOp",EDGE,"E20.15.1");var subQ68=sQuery(id+"F4.wireOp",EDGE,"E23");var subQ69=sQuery(id+"F4.wireOp",EDGE,"E22");var subQ70=sQuery(id+"F3.wireOp",EDGE,"E18.top");var subQ71=sQuery(id+"F3.wireOp",EDGE,"E18.bottom");var subQ74=makeQuery(id+"F42.boolean.opBoolean","COPY",FACE,{"disambiguationData":[TD([subQ27])],"derivedFrom":subQ6});var subQ75=makeQuery(id+"F16.boolean.opBoolean","INTERSECT",EDGE,{"derivedFrom":[makeQuery(id+"F1.opRevolve","SWEPT_FACE",FACE,{"disambiguationData":[OSD([sQuery(id+"F0.wireOp",EDGE,"E4")])]}),subQ27]});Q49=makeQuery(id+"F48.opFillet","BLEND_EDGE",EDGE,{"blendedFrom":[makeQuery(id+"F47.opFillet","TWEAK_EDGE",EDGE,{"derivedFrom":[makeQuery(id+"F45.opFillet","BLEND_VERTEX",VERTEX,{"blendedFrom":[subQ75,subQ27,subQ74],"blendedInto":[subQ27,subQ74]}),makeQuery(id+"F45.opFillet","BLEND_VERTEX",VERTEX,{"blendedFrom":[subQ75,makeQuery(id+"F42.boolean.opBoolean","MERGE",FACE,{"derivedFrom":[subQ0,subQ8]}),subQ74],"blendedInto":[makeQuery(id+"F42.boolean.opBoolean","MERGE",FACE,{"derivedFrom":[subQ0,subQ8]}),subQ74]})]}),makeQuery(id+"F47.opFillet","BLEND_FACE",FACE,{"disambiguationData":[OSD([subQ5,subQ7]),TDD([makeQuery(id+"F42.boolean.opBoolean","COPY",EDGE,{"disambiguationData":[TD([makeQuery(id+"F5.opLoft","SWEPT_FACE",FACE,{"disambiguationData":[OSD([subQ71,subQ70,sQuery(id+"F3.wireOp",EDGE,"E18.left"),sQuery(id+"F4.wireOp",EDGE,"E21"),subQ69,subQ68])]})])],"derivedFrom":subQ9})])]}),makeQuery(id+"F47.opFillet","BLEND_FACE",FACE,{"disambiguationData":[OSD([subQ5,subQ7]),TDD([makeQuery(id+"F42.boolean.opBoolean","COPY",EDGE,{"disambiguationData":[TD([makeQuery(id+"F6.opLoft","SWEPT_FACE",FACE,{"disambiguationData":[OSD([sQuery(id+"F3.wireOp",EDGE,"E20.15.0"),subQ67,subQ66,sQuery(id+"F4.wireOp",EDGE,"E26.15.0"),subQ65,subQ64])]})])],"derivedFrom":subQ9})])]}),makeQuery(id+"F47.opFillet","BLEND_FACE",FACE,{"disambiguationData":[OSD([subQ5,subQ7]),TDD([makeQuery(id+"F42.boolean.opBoolean","COPY",EDGE,{"disambiguationData":[TD([makeQuery(id+"F7.opLoft","SWEPT_FACE",FACE,{"disambiguationData":[OSD([sQuery(id+"F3.wireOp",EDGE,"E20.14.0"),subQ63,subQ62,sQuery(id+"F4.wireOp",EDGE,"E26.14.0"),subQ61,subQ60])]})])],"derivedFrom":subQ9})])]}),makeQuery(id+"F47.opFillet","BLEND_FACE",FACE,{"disambiguationData":[OSD([subQ5,subQ7]),TDD([makeQuery(id+"F42.boolean.opBoolean","COPY",EDGE,{"disambiguationData":[TD([makeQuery(id+"F8.opLoft","SWEPT_FACE",FACE,{"disambiguationData":[OSD([sQuery(id+"F3.wireOp",EDGE,"E20.13.0"),subQ59,subQ58,sQuery(id+"F4.wireOp",EDGE,"E26.13.0"),subQ57,subQ56])]})])],"derivedFrom":subQ9})])]}),makeQuery(id+"F47.opFillet","BLEND_FACE",FACE,{"disambiguationData":[OSD([subQ5,subQ7]),TDD([makeQuery(id+"F42.boolean.opBoolean","COPY",EDGE,{"disambiguationData":[TD([makeQuery(id+"F9.opLoft","SWEPT_FACE",FACE,{"disambiguationData":[OSD([sQuery(id+"F3.wireOp",EDGE,"E20.12.0"),subQ55,subQ54,sQuery(id+"F4.wireOp",EDGE,"E26.12.0"),subQ53,subQ52])]})])],"derivedFrom":subQ9})])]}),makeQuery(id+"F47.opFillet","BLEND_FACE",FACE,{"disambiguationData":[OSD([subQ5,subQ7]),TDD([makeQuery(id+"F42.boolean.opBoolean","COPY",EDGE,{"disambiguationData":[TD([makeQuery(id+"F10.opLoft","SWEPT_FACE",FACE,{"disambiguationData":[OSD([sQuery(id+"F3.wireOp",EDGE,"E20.11.0"),subQ51,subQ50,sQuery(id+"F4.wireOp",EDGE,"E26.11.0"),subQ49,subQ48])]})])],"derivedFrom":subQ9})])]}),makeQuery(id+"F47.opFillet","BLEND_FACE",FACE,{"disambiguationData":[OSD([subQ5,subQ7]),TDD([makeQuery(id+"F42.boolean.opBoolean","COPY",EDGE,{"disambiguationData":[TD([makeQuery(id+"F11.opLoft","SWEPT_FACE",FACE,{"disambiguationData":[OSD([sQuery(id+"F3.wireOp",EDGE,"E20.10.0"),subQ47,subQ46,sQuery(id+"F4.wireOp",EDGE,"E26.10.0"),subQ45,subQ44])]})])],"derivedFrom":subQ9})])]}),makeQuery(id+"F47.opFillet","BLEND_FACE",FACE,{"disambiguationData":[OSD([subQ5,subQ7]),TDD([makeQuery(id+"F42.boolean.opBoolean","COPY",EDGE,{"disambiguationData":[TD([makeQuery(id+"F12.opLoft","SWEPT_FACE",FACE,{"disambiguationData":[OSD([sQuery(id+"F3.wireOp",EDGE,"E20.9.0"),subQ43,subQ42,sQuery(id+"F4.wireOp",EDGE,"E26.9.0"),subQ41,subQ40])]})])],"derivedFrom":subQ9})])]}),makeQuery(id+"F47.opFillet","BLEND_FACE",FACE,{"disambiguationData":[OSD([subQ5,subQ7]),TDD([makeQuery(id+"F42.boolean.opBoolean","COPY",EDGE,{"disambiguationData":[TD([makeQuery(id+"F13.opLoft","SWEPT_FACE",FACE,{"disambiguationData":[OSD([sQuery(id+"F3.wireOp",EDGE,"E20.8.0"),subQ39,subQ38,sQuery(id+"F4.wireOp",EDGE,"E26.8.0"),subQ37,subQ36])]})])],"derivedFrom":subQ9})])]}),makeQuery(id+"F47.opFillet","BLEND_FACE",FACE,{"disambiguationData":[OSD([subQ5,subQ7]),TDD([makeQuery(id+"F42.boolean.opBoolean","COPY",EDGE,{"disambiguationData":[TD([makeQuery(id+"F14.opLoft","SWEPT_FACE",FACE,{"disambiguationData":[OSD([sQuery(id+"F3.wireOp",EDGE,"E20.7.0"),subQ35,subQ34,sQuery(id+"F4.wireOp",EDGE,"E26.7.0"),subQ33,subQ32])]})])],"derivedFrom":subQ9})])]}),makeQuery(id+"F47.opFillet","BLEND_FACE",FACE,{"disambiguationData":[OSD([subQ5,subQ7]),TDD([makeQuery(id+"F42.boolean.opBoolean","COPY",EDGE,{"disambiguationData":[TD([makeQuery(id+"F15.opLoft","SWEPT_FACE",FACE,{"disambiguationData":[OSD([sQuery(id+"F3.wireOp",EDGE,"E20.6.0"),subQ31,subQ30,sQuery(id+"F4.wireOp",EDGE,"E26.6.0"),subQ29,subQ28])]})])],"derivedFrom":subQ9})])]}),makeQuery(id+"F47.opFillet","BLEND_FACE",FACE,{"disambiguationData":[OSD([subQ5,subQ7]),TDD([makeQuery(id+"F42.boolean.opBoolean","COPY",EDGE,{"disambiguationData":[TD([subQ27])],"derivedFrom":subQ9})])]}),makeQuery(id+"F47.opFillet","BLEND_FACE",FACE,{"disambiguationData":[OSD([subQ5,subQ7]),TDD([makeQuery(id+"F42.boolean.opBoolean","COPY",EDGE,{"disambiguationData":[TD([makeQuery(id+"F17.opLoft","SWEPT_FACE",FACE,{"disambiguationData":[OSD([sQuery(id+"F3.wireOp",EDGE,"E20.4.0"),subQ21,subQ20,sQuery(id+"F4.wireOp",EDGE,"E26.4.0"),subQ19,subQ18])]})])],"derivedFrom":subQ9})])]}),makeQuery(id+"F47.opFillet","BLEND_FACE",FACE,{"disambiguationData":[OSD([subQ5,subQ7]),TDD([makeQuery(id+"F42.boolean.opBoolean","COPY",EDGE,{"disambiguationData":[TD([makeQuery(id+"F18.opLoft","SWEPT_FACE",FACE,{"disambiguationData":[OSD([sQuery(id+"F3.wireOp",EDGE,"E20.3.0"),subQ17,subQ16,sQuery(id+"F4.wireOp",EDGE,"E26.3.0"),subQ15,subQ14])]})])],"derivedFrom":subQ9})])]}),makeQuery(id+"F47.opFillet","BLEND_FACE",FACE,{"disambiguationData":[OSD([subQ5,subQ7]),TDD([makeQuery(id+"F42.boolean.opBoolean","COPY",EDGE,{"disambiguationData":[TD([makeQuery(id+"F19.opLoft","SWEPT_FACE",FACE,{"disambiguationData":[OSD([sQuery(id+"F3.wireOp",EDGE,"E20.2.0"),subQ13,subQ12,sQuery(id+"F4.wireOp",EDGE,"E26.2.0"),subQ11,subQ10])]})])],"derivedFrom":subQ9})])]}),makeQuery(id+"F47.opFillet","BLEND_FACE",FACE,{"disambiguationData":[OSD([subQ5,subQ7]),TDD([makeQuery(id+"F42.boolean.opBoolean","COPY",EDGE,{"disambiguationData":[TD([makeQuery(id+"F20.opLoft","SWEPT_FACE",FACE,{"disambiguationData":[OSD([sQuery(id+"F3.wireOp",EDGE,"E20.1.0"),subQ4,subQ3,sQuery(id+"F4.wireOp",EDGE,"E26.1.0"),subQ2,subQ1])]})])],"derivedFrom":subQ9})])]})],"blendedInto":[makeQuery(id+"F47.opFillet","BLEND_FACE",FACE,{"disambiguationData":[OSD([subQ5,subQ7]),TDD([makeQuery(id+"F42.boolean.opBoolean","COPY",EDGE,{"disambiguationData":[TD([makeQuery(id+"F5.opLoft","SWEPT_FACE",FACE,{"disambiguationData":[OSD([subQ71,subQ70,sQuery(id+"F3.wireOp",EDGE,"E18.left"),sQuery(id+"F4.wireOp",EDGE,"E21"),subQ69,subQ68])]})])],"derivedFrom":subQ9})])]}),makeQuery(id+"F47.opFillet","BLEND_FACE",FACE,{"disambiguationData":[OSD([subQ5,subQ7]),TDD([makeQuery(id+"F42.boolean.opBoolean","COPY",EDGE,{"disambiguationData":[TD([makeQuery(id+"F6.opLoft","SWEPT_FACE",FACE,{"disambiguationData":[OSD([sQuery(id+"F3.wireOp",EDGE,"E20.15.0"),subQ67,subQ66,sQuery(id+"F4.wireOp",EDGE,"E26.15.0"),subQ65,subQ64])]})])],"derivedFrom":subQ9})])]}),makeQuery(id+"F47.opFillet","BLEND_FACE",FACE,{"disambiguationData":[OSD([subQ5,subQ7]),TDD([makeQuery(id+"F42.boolean.opBoolean","COPY",EDGE,{"disambiguationData":[TD([makeQuery(id+"F7.opLoft","SWEPT_FACE",FACE,{"disambiguationData":[OSD([sQuery(id+"F3.wireOp",EDGE,"E20.14.0"),subQ63,subQ62,sQuery(id+"F4.wireOp",EDGE,"E26.14.0"),subQ61,subQ60])]})])],"derivedFrom":subQ9})])]}),makeQuery(id+"F47.opFillet","BLEND_FACE",FACE,{"disambiguationData":[OSD([subQ5,subQ7]),TDD([makeQuery(id+"F42.boolean.opBoolean","COPY",EDGE,{"disambiguationData":[TD([makeQuery(id+"F8.opLoft","SWEPT_FACE",FACE,{"disambiguationData":[OSD([sQuery(id+"F3.wireOp",EDGE,"E20.13.0"),subQ59,subQ58,sQuery(id+"F4.wireOp",EDGE,"E26.13.0"),subQ57,subQ56])]})])],"derivedFrom":subQ9})])]}),makeQuery(id+"F47.opFillet","BLEND_FACE",FACE,{"disambiguationData":[OSD([subQ5,subQ7]),TDD([makeQuery(id+"F42.boolean.opBoolean","COPY",EDGE,{"disambiguationData":[TD([makeQuery(id+"F9.opLoft","SWEPT_FACE",FACE,{"disambiguationData":[OSD([sQuery(id+"F3.wireOp",EDGE,"E20.12.0"),subQ55,subQ54,sQuery(id+"F4.wireOp",EDGE,"E26.12.0"),subQ53,subQ52])]})])],"derivedFrom":subQ9})])]}),makeQuery(id+"F47.opFillet","BLEND_FACE",FACE,{"disambiguationData":[OSD([subQ5,subQ7]),TDD([makeQuery(id+"F42.boolean.opBoolean","COPY",EDGE,{"disambiguationData":[TD([makeQuery(id+"F10.opLoft","SWEPT_FACE",FACE,{"disambiguationData":[OSD([sQuery(id+"F3.wireOp",EDGE,"E20.11.0"),subQ51,subQ50,sQuery(id+"F4.wireOp",EDGE,"E26.11.0"),subQ49,subQ48])]})])],"derivedFrom":subQ9})])]}),makeQuery(id+"F47.opFillet","BLEND_FACE",FACE,{"disambiguationData":[OSD([subQ5,subQ7]),TDD([makeQuery(id+"F42.boolean.opBoolean","COPY",EDGE,{"disambiguationData":[TD([makeQuery(id+"F11.opLoft","SWEPT_FACE",FACE,{"disambiguationData":[OSD([sQuery(id+"F3.wireOp",EDGE,"E20.10.0"),subQ47,subQ46,sQuery(id+"F4.wireOp",EDGE,"E26.10.0"),subQ45,subQ44])]})])],"derivedFrom":subQ9})])]}),makeQuery(id+"F47.opFillet","BLEND_FACE",FACE,{"disambiguationData":[OSD([subQ5,subQ7]),TDD([makeQuery(id+"F42.boolean.opBoolean","COPY",EDGE,{"disambiguationData":[TD([makeQuery(id+"F12.opLoft","SWEPT_FACE",FACE,{"disambiguationData":[OSD([sQuery(id+"F3.wireOp",EDGE,"E20.9.0"),subQ43,subQ42,sQuery(id+"F4.wireOp",EDGE,"E26.9.0"),subQ41,subQ40])]})])],"derivedFrom":subQ9})])]}),makeQuery(id+"F47.opFillet","BLEND_FACE",FACE,{"disambiguationData":[OSD([subQ5,subQ7]),TDD([makeQuery(id+"F42.boolean.opBoolean","COPY",EDGE,{"disambiguationData":[TD([makeQuery(id+"F13.opLoft","SWEPT_FACE",FACE,{"disambiguationData":[OSD([sQuery(id+"F3.wireOp",EDGE,"E20.8.0"),subQ39,subQ38,sQuery(id+"F4.wireOp",EDGE,"E26.8.0"),subQ37,subQ36])]})])],"derivedFrom":subQ9})])]}),makeQuery(id+"F47.opFillet","BLEND_FACE",FACE,{"disambiguationData":[OSD([subQ5,subQ7]),TDD([makeQuery(id+"F42.boolean.opBoolean","COPY",EDGE,{"disambiguationData":[TD([makeQuery(id+"F14.opLoft","SWEPT_FACE",FACE,{"disambiguationData":[OSD([sQuery(id+"F3.wireOp",EDGE,"E20.7.0"),subQ35,subQ34,sQuery(id+"F4.wireOp",EDGE,"E26.7.0"),subQ33,subQ32])]})])],"derivedFrom":subQ9})])]}),makeQuery(id+"F47.opFillet","BLEND_FACE",FACE,{"disambiguationData":[OSD([subQ5,subQ7]),TDD([makeQuery(id+"F42.boolean.opBoolean","COPY",EDGE,{"disambiguationData":[TD([makeQuery(id+"F15.opLoft","SWEPT_FACE",FACE,{"disambiguationData":[OSD([sQuery(id+"F3.wireOp",EDGE,"E20.6.0"),subQ31,subQ30,sQuery(id+"F4.wireOp",EDGE,"E26.6.0"),subQ29,subQ28])]})])],"derivedFrom":subQ9})])]}),makeQuery(id+"F47.opFillet","BLEND_FACE",FACE,{"disambiguationData":[OSD([subQ5,subQ7]),TDD([makeQuery(id+"F42.boolean.opBoolean","COPY",EDGE,{"disambiguationData":[TD([subQ27])],"derivedFrom":subQ9})])]}),makeQuery(id+"F47.opFillet","BLEND_FACE",FACE,{"disambiguationData":[OSD([subQ5,subQ7]),TDD([makeQuery(id+"F42.boolean.opBoolean","COPY",EDGE,{"disambiguationData":[TD([makeQuery(id+"F17.opLoft","SWEPT_FACE",FACE,{"disambiguationData":[OSD([sQuery(id+"F3.wireOp",EDGE,"E20.4.0"),subQ21,subQ20,sQuery(id+"F4.wireOp",EDGE,"E26.4.0"),subQ19,subQ18])]})])],"derivedFrom":subQ9})])]}),makeQuery(id+"F47.opFillet","BLEND_FACE",FACE,{"disambiguationData":[OSD([subQ5,subQ7]),TDD([makeQuery(id+"F42.boolean.opBoolean","COPY",EDGE,{"disambiguationData":[TD([makeQuery(id+"F18.opLoft","SWEPT_FACE",FACE,{"disambiguationData":[OSD([sQuery(id+"F3.wireOp",EDGE,"E20.3.0"),subQ17,subQ16,sQuery(id+"F4.wireOp",EDGE,"E26.3.0"),subQ15,subQ14])]})])],"derivedFrom":subQ9})])]}),makeQuery(id+"F47.opFillet","BLEND_FACE",FACE,{"disambiguationData":[OSD([subQ5,subQ7]),TDD([makeQuery(id+"F42.boolean.opBoolean","COPY",EDGE,{"disambiguationData":[TD([makeQuery(id+"F19.opLoft","SWEPT_FACE",FACE,{"disambiguationData":[OSD([sQuery(id+"F3.wireOp",EDGE,"E20.2.0"),subQ13,subQ12,sQuery(id+"F4.wireOp",EDGE,"E26.2.0"),subQ11,subQ10])]})])],"derivedFrom":subQ9})])]}),makeQuery(id+"F47.opFillet","BLEND_FACE",FACE,{"disambiguationData":[OSD([subQ5,subQ7]),TDD([makeQuery(id+"F42.boolean.opBoolean","COPY",EDGE,{"disambiguationData":[TD([makeQuery(id+"F20.opLoft","SWEPT_FACE",FACE,{"disambiguationData":[OSD([sQuery(id+"F3.wireOp",EDGE,"E20.1.0"),subQ4,subQ3,sQuery(id+"F4.wireOp",EDGE,"E26.1.0"),subQ2,subQ1])]})])],"derivedFrom":subQ9})])]})]});}
            var Q50;
            {var subQ0=makeQuery(id+"F40.opExtrude","CAP_FACE",FACE,{"disambiguationData":[OSD([sQuery(id+"F39.wireOp",EDGE,"E29"),sQuery(id+"F39.wireOp",EDGE,"E30")])],"isStart":false});var subQ1=sQuery(id+"F4.wireOp",EDGE,"E26.1.3");var subQ2=sQuery(id+"F4.wireOp",EDGE,"E26.1.2");var subQ3=sQuery(id+"F3.wireOp",EDGE,"E20.1.3");var subQ4=sQuery(id+"F3.wireOp",EDGE,"E20.1.1");var subQ5=sQuery(id+"F41.wireOp",EDGE,"E35");var subQ6=makeQuery(id+"F42.opRevolve","SWEPT_FACE",FACE,{"disambiguationData":[OSD([subQ5])]});var subQ7=sQuery(id+"F41.wireOp",EDGE,"E36");var subQ8=makeQuery(id+"F42.opRevolve","SWEPT_FACE",FACE,{"disambiguationData":[OSD([subQ7])]});var subQ9=makeQuery(id+"F42.opRevolve","SWEPT_EDGE",EDGE,{"disambiguationData":[OSD([subQ5,subQ7])]});var subQ10=sQuery(id+"F4.wireOp",EDGE,"E26.2.3");var subQ11=sQuery(id+"F4.wireOp",EDGE,"E26.2.2");var subQ12=sQuery(id+"F3.wireOp",EDGE,"E20.2.3");var subQ13=sQuery(id+"F3.wireOp",EDGE,"E20.2.1");var subQ14=sQuery(id+"F4.wireOp",EDGE,"E26.3.3");var subQ15=sQuery(id+"F4.wireOp",EDGE,"E26.3.2");var subQ16=sQuery(id+"F3.wireOp",EDGE,"E20.3.3");var subQ17=sQuery(id+"F3.wireOp",EDGE,"E20.3.1");var subQ18=sQuery(id+"F4.wireOp",EDGE,"E26.4.3");var subQ19=sQuery(id+"F4.wireOp",EDGE,"E26.4.2");var subQ20=sQuery(id+"F3.wireOp",EDGE,"E20.4.3");var subQ21=sQuery(id+"F3.wireOp",EDGE,"E20.4.1");var subQ23=makeQuery(id+"F17.opLoft","SWEPT_FACE",FACE,{"disambiguationData":[OSD([sQuery(id+"F3.wireOp",EDGE,"E20.4.0"),subQ21,subQ20,sQuery(id+"F4.wireOp",EDGE,"E26.4.0"),subQ19,subQ18])]});var subQ24=sQuery(id+"F4.wireOp",EDGE,"E26.5.3");var subQ25=sQuery(id+"F4.wireOp",EDGE,"E26.5.2");var subQ26=sQuery(id+"F3.wireOp",EDGE,"E20.5.3");var subQ27=sQuery(id+"F3.wireOp",EDGE,"E20.5.1");var subQ28=sQuery(id+"F4.wireOp",EDGE,"E26.6.3");var subQ29=sQuery(id+"F4.wireOp",EDGE,"E26.6.2");var subQ30=sQuery(id+"F3.wireOp",EDGE,"E20.6.3");var subQ31=sQuery(id+"F3.wireOp",EDGE,"E20.6.1");var subQ32=sQuery(id+"F4.wireOp",EDGE,"E26.7.3");var subQ33=sQuery(id+"F4.wireOp",EDGE,"E26.7.2");var subQ34=sQuery(id+"F3.wireOp",EDGE,"E20.7.3");var subQ35=sQuery(id+"F3.wireOp",EDGE,"E20.7.1");var subQ36=sQuery(id+"F4.wireOp",EDGE,"E26.8.3");var subQ37=sQuery(id+"F4.wireOp",EDGE,"E26.8.2");var subQ38=sQuery(id+"F3.wireOp",EDGE,"E20.8.3");var subQ39=sQuery(id+"F3.wireOp",EDGE,"E20.8.1");var subQ40=sQuery(id+"F4.wireOp",EDGE,"E26.9.3");var subQ41=sQuery(id+"F4.wireOp",EDGE,"E26.9.2");var subQ42=sQuery(id+"F3.wireOp",EDGE,"E20.9.3");var subQ43=sQuery(id+"F3.wireOp",EDGE,"E20.9.1");var subQ44=sQuery(id+"F4.wireOp",EDGE,"E26.10.3");var subQ45=sQuery(id+"F4.wireOp",EDGE,"E26.10.2");var subQ46=sQuery(id+"F3.wireOp",EDGE,"E20.10.3");var subQ47=sQuery(id+"F3.wireOp",EDGE,"E20.10.1");var subQ48=sQuery(id+"F4.wireOp",EDGE,"E26.11.3");var subQ49=sQuery(id+"F4.wireOp",EDGE,"E26.11.2");var subQ50=sQuery(id+"F3.wireOp",EDGE,"E20.11.3");var subQ51=sQuery(id+"F3.wireOp",EDGE,"E20.11.1");var subQ52=sQuery(id+"F4.wireOp",EDGE,"E26.12.3");var subQ53=sQuery(id+"F4.wireOp",EDGE,"E26.12.2");var subQ54=sQuery(id+"F3.wireOp",EDGE,"E20.12.3");var subQ55=sQuery(id+"F3.wireOp",EDGE,"E20.12.1");var subQ56=sQuery(id+"F4.wireOp",EDGE,"E26.13.3");var subQ57=sQuery(id+"F4.wireOp",EDGE,"E26.13.2");var subQ58=sQuery(id+"F3.wireOp",EDGE,"E20.13.3");var subQ59=sQuery(id+"F3.wireOp",EDGE,"E20.13.1");var subQ60=sQuery(id+"F4.wireOp",EDGE,"E26.14.3");var subQ61=sQuery(id+"F4.wireOp",EDGE,"E26.14.2");var subQ62=sQuery(id+"F3.wireOp",EDGE,"E20.14.3");var subQ63=sQuery(id+"F3.wireOp",EDGE,"E20.14.1");var subQ64=sQuery(id+"F4.wireOp",EDGE,"E26.15.3");var subQ65=sQuery(id+"F4.wireOp",EDGE,"E26.15.2");var subQ66=sQuery(id+"F3.wireOp",EDGE,"E20.15.3");var subQ67=sQuery(id+"F3.wireOp",EDGE,"E20.15.1");var subQ68=sQuery(id+"F4.wireOp",EDGE,"E23");var subQ69=sQuery(id+"F4.wireOp",EDGE,"E22");var subQ70=sQuery(id+"F3.wireOp",EDGE,"E18.top");var subQ71=sQuery(id+"F3.wireOp",EDGE,"E18.bottom");var subQ74=makeQuery(id+"F42.boolean.opBoolean","COPY",FACE,{"disambiguationData":[TD([subQ23])],"derivedFrom":subQ6});var subQ75=makeQuery(id+"F17.boolean.opBoolean","INTERSECT",EDGE,{"derivedFrom":[makeQuery(id+"F1.opRevolve","SWEPT_FACE",FACE,{"disambiguationData":[OSD([sQuery(id+"F0.wireOp",EDGE,"E4")])]}),subQ23]});Q50=makeQuery(id+"F48.opFillet","BLEND_EDGE",EDGE,{"blendedFrom":[makeQuery(id+"F47.opFillet","TWEAK_EDGE",EDGE,{"derivedFrom":[makeQuery(id+"F45.opFillet","BLEND_VERTEX",VERTEX,{"blendedFrom":[subQ75,subQ23,subQ74],"blendedInto":[subQ23,subQ74]}),makeQuery(id+"F45.opFillet","BLEND_VERTEX",VERTEX,{"blendedFrom":[subQ75,makeQuery(id+"F42.boolean.opBoolean","MERGE",FACE,{"derivedFrom":[subQ0,subQ8]}),subQ74],"blendedInto":[makeQuery(id+"F42.boolean.opBoolean","MERGE",FACE,{"derivedFrom":[subQ0,subQ8]}),subQ74]})]}),makeQuery(id+"F47.opFillet","BLEND_FACE",FACE,{"disambiguationData":[OSD([subQ5,subQ7]),TDD([makeQuery(id+"F42.boolean.opBoolean","COPY",EDGE,{"disambiguationData":[TD([makeQuery(id+"F5.opLoft","SWEPT_FACE",FACE,{"disambiguationData":[OSD([subQ71,subQ70,sQuery(id+"F3.wireOp",EDGE,"E18.left"),sQuery(id+"F4.wireOp",EDGE,"E21"),subQ69,subQ68])]})])],"derivedFrom":subQ9})])]}),makeQuery(id+"F47.opFillet","BLEND_FACE",FACE,{"disambiguationData":[OSD([subQ5,subQ7]),TDD([makeQuery(id+"F42.boolean.opBoolean","COPY",EDGE,{"disambiguationData":[TD([makeQuery(id+"F6.opLoft","SWEPT_FACE",FACE,{"disambiguationData":[OSD([sQuery(id+"F3.wireOp",EDGE,"E20.15.0"),subQ67,subQ66,sQuery(id+"F4.wireOp",EDGE,"E26.15.0"),subQ65,subQ64])]})])],"derivedFrom":subQ9})])]}),makeQuery(id+"F47.opFillet","BLEND_FACE",FACE,{"disambiguationData":[OSD([subQ5,subQ7]),TDD([makeQuery(id+"F42.boolean.opBoolean","COPY",EDGE,{"disambiguationData":[TD([makeQuery(id+"F7.opLoft","SWEPT_FACE",FACE,{"disambiguationData":[OSD([sQuery(id+"F3.wireOp",EDGE,"E20.14.0"),subQ63,subQ62,sQuery(id+"F4.wireOp",EDGE,"E26.14.0"),subQ61,subQ60])]})])],"derivedFrom":subQ9})])]}),makeQuery(id+"F47.opFillet","BLEND_FACE",FACE,{"disambiguationData":[OSD([subQ5,subQ7]),TDD([makeQuery(id+"F42.boolean.opBoolean","COPY",EDGE,{"disambiguationData":[TD([makeQuery(id+"F8.opLoft","SWEPT_FACE",FACE,{"disambiguationData":[OSD([sQuery(id+"F3.wireOp",EDGE,"E20.13.0"),subQ59,subQ58,sQuery(id+"F4.wireOp",EDGE,"E26.13.0"),subQ57,subQ56])]})])],"derivedFrom":subQ9})])]}),makeQuery(id+"F47.opFillet","BLEND_FACE",FACE,{"disambiguationData":[OSD([subQ5,subQ7]),TDD([makeQuery(id+"F42.boolean.opBoolean","COPY",EDGE,{"disambiguationData":[TD([makeQuery(id+"F9.opLoft","SWEPT_FACE",FACE,{"disambiguationData":[OSD([sQuery(id+"F3.wireOp",EDGE,"E20.12.0"),subQ55,subQ54,sQuery(id+"F4.wireOp",EDGE,"E26.12.0"),subQ53,subQ52])]})])],"derivedFrom":subQ9})])]}),makeQuery(id+"F47.opFillet","BLEND_FACE",FACE,{"disambiguationData":[OSD([subQ5,subQ7]),TDD([makeQuery(id+"F42.boolean.opBoolean","COPY",EDGE,{"disambiguationData":[TD([makeQuery(id+"F10.opLoft","SWEPT_FACE",FACE,{"disambiguationData":[OSD([sQuery(id+"F3.wireOp",EDGE,"E20.11.0"),subQ51,subQ50,sQuery(id+"F4.wireOp",EDGE,"E26.11.0"),subQ49,subQ48])]})])],"derivedFrom":subQ9})])]}),makeQuery(id+"F47.opFillet","BLEND_FACE",FACE,{"disambiguationData":[OSD([subQ5,subQ7]),TDD([makeQuery(id+"F42.boolean.opBoolean","COPY",EDGE,{"disambiguationData":[TD([makeQuery(id+"F11.opLoft","SWEPT_FACE",FACE,{"disambiguationData":[OSD([sQuery(id+"F3.wireOp",EDGE,"E20.10.0"),subQ47,subQ46,sQuery(id+"F4.wireOp",EDGE,"E26.10.0"),subQ45,subQ44])]})])],"derivedFrom":subQ9})])]}),makeQuery(id+"F47.opFillet","BLEND_FACE",FACE,{"disambiguationData":[OSD([subQ5,subQ7]),TDD([makeQuery(id+"F42.boolean.opBoolean","COPY",EDGE,{"disambiguationData":[TD([makeQuery(id+"F12.opLoft","SWEPT_FACE",FACE,{"disambiguationData":[OSD([sQuery(id+"F3.wireOp",EDGE,"E20.9.0"),subQ43,subQ42,sQuery(id+"F4.wireOp",EDGE,"E26.9.0"),subQ41,subQ40])]})])],"derivedFrom":subQ9})])]}),makeQuery(id+"F47.opFillet","BLEND_FACE",FACE,{"disambiguationData":[OSD([subQ5,subQ7]),TDD([makeQuery(id+"F42.boolean.opBoolean","COPY",EDGE,{"disambiguationData":[TD([makeQuery(id+"F13.opLoft","SWEPT_FACE",FACE,{"disambiguationData":[OSD([sQuery(id+"F3.wireOp",EDGE,"E20.8.0"),subQ39,subQ38,sQuery(id+"F4.wireOp",EDGE,"E26.8.0"),subQ37,subQ36])]})])],"derivedFrom":subQ9})])]}),makeQuery(id+"F47.opFillet","BLEND_FACE",FACE,{"disambiguationData":[OSD([subQ5,subQ7]),TDD([makeQuery(id+"F42.boolean.opBoolean","COPY",EDGE,{"disambiguationData":[TD([makeQuery(id+"F14.opLoft","SWEPT_FACE",FACE,{"disambiguationData":[OSD([sQuery(id+"F3.wireOp",EDGE,"E20.7.0"),subQ35,subQ34,sQuery(id+"F4.wireOp",EDGE,"E26.7.0"),subQ33,subQ32])]})])],"derivedFrom":subQ9})])]}),makeQuery(id+"F47.opFillet","BLEND_FACE",FACE,{"disambiguationData":[OSD([subQ5,subQ7]),TDD([makeQuery(id+"F42.boolean.opBoolean","COPY",EDGE,{"disambiguationData":[TD([makeQuery(id+"F15.opLoft","SWEPT_FACE",FACE,{"disambiguationData":[OSD([sQuery(id+"F3.wireOp",EDGE,"E20.6.0"),subQ31,subQ30,sQuery(id+"F4.wireOp",EDGE,"E26.6.0"),subQ29,subQ28])]})])],"derivedFrom":subQ9})])]}),makeQuery(id+"F47.opFillet","BLEND_FACE",FACE,{"disambiguationData":[OSD([subQ5,subQ7]),TDD([makeQuery(id+"F42.boolean.opBoolean","COPY",EDGE,{"disambiguationData":[TD([makeQuery(id+"F16.opLoft","SWEPT_FACE",FACE,{"disambiguationData":[OSD([sQuery(id+"F3.wireOp",EDGE,"E20.5.0"),subQ27,subQ26,sQuery(id+"F4.wireOp",EDGE,"E26.5.0"),subQ25,subQ24])]})])],"derivedFrom":subQ9})])]}),makeQuery(id+"F47.opFillet","BLEND_FACE",FACE,{"disambiguationData":[OSD([subQ5,subQ7]),TDD([makeQuery(id+"F42.boolean.opBoolean","COPY",EDGE,{"disambiguationData":[TD([subQ23])],"derivedFrom":subQ9})])]}),makeQuery(id+"F47.opFillet","BLEND_FACE",FACE,{"disambiguationData":[OSD([subQ5,subQ7]),TDD([makeQuery(id+"F42.boolean.opBoolean","COPY",EDGE,{"disambiguationData":[TD([makeQuery(id+"F18.opLoft","SWEPT_FACE",FACE,{"disambiguationData":[OSD([sQuery(id+"F3.wireOp",EDGE,"E20.3.0"),subQ17,subQ16,sQuery(id+"F4.wireOp",EDGE,"E26.3.0"),subQ15,subQ14])]})])],"derivedFrom":subQ9})])]}),makeQuery(id+"F47.opFillet","BLEND_FACE",FACE,{"disambiguationData":[OSD([subQ5,subQ7]),TDD([makeQuery(id+"F42.boolean.opBoolean","COPY",EDGE,{"disambiguationData":[TD([makeQuery(id+"F19.opLoft","SWEPT_FACE",FACE,{"disambiguationData":[OSD([sQuery(id+"F3.wireOp",EDGE,"E20.2.0"),subQ13,subQ12,sQuery(id+"F4.wireOp",EDGE,"E26.2.0"),subQ11,subQ10])]})])],"derivedFrom":subQ9})])]}),makeQuery(id+"F47.opFillet","BLEND_FACE",FACE,{"disambiguationData":[OSD([subQ5,subQ7]),TDD([makeQuery(id+"F42.boolean.opBoolean","COPY",EDGE,{"disambiguationData":[TD([makeQuery(id+"F20.opLoft","SWEPT_FACE",FACE,{"disambiguationData":[OSD([sQuery(id+"F3.wireOp",EDGE,"E20.1.0"),subQ4,subQ3,sQuery(id+"F4.wireOp",EDGE,"E26.1.0"),subQ2,subQ1])]})])],"derivedFrom":subQ9})])]})],"blendedInto":[makeQuery(id+"F47.opFillet","BLEND_FACE",FACE,{"disambiguationData":[OSD([subQ5,subQ7]),TDD([makeQuery(id+"F42.boolean.opBoolean","COPY",EDGE,{"disambiguationData":[TD([makeQuery(id+"F5.opLoft","SWEPT_FACE",FACE,{"disambiguationData":[OSD([subQ71,subQ70,sQuery(id+"F3.wireOp",EDGE,"E18.left"),sQuery(id+"F4.wireOp",EDGE,"E21"),subQ69,subQ68])]})])],"derivedFrom":subQ9})])]}),makeQuery(id+"F47.opFillet","BLEND_FACE",FACE,{"disambiguationData":[OSD([subQ5,subQ7]),TDD([makeQuery(id+"F42.boolean.opBoolean","COPY",EDGE,{"disambiguationData":[TD([makeQuery(id+"F6.opLoft","SWEPT_FACE",FACE,{"disambiguationData":[OSD([sQuery(id+"F3.wireOp",EDGE,"E20.15.0"),subQ67,subQ66,sQuery(id+"F4.wireOp",EDGE,"E26.15.0"),subQ65,subQ64])]})])],"derivedFrom":subQ9})])]}),makeQuery(id+"F47.opFillet","BLEND_FACE",FACE,{"disambiguationData":[OSD([subQ5,subQ7]),TDD([makeQuery(id+"F42.boolean.opBoolean","COPY",EDGE,{"disambiguationData":[TD([makeQuery(id+"F7.opLoft","SWEPT_FACE",FACE,{"disambiguationData":[OSD([sQuery(id+"F3.wireOp",EDGE,"E20.14.0"),subQ63,subQ62,sQuery(id+"F4.wireOp",EDGE,"E26.14.0"),subQ61,subQ60])]})])],"derivedFrom":subQ9})])]}),makeQuery(id+"F47.opFillet","BLEND_FACE",FACE,{"disambiguationData":[OSD([subQ5,subQ7]),TDD([makeQuery(id+"F42.boolean.opBoolean","COPY",EDGE,{"disambiguationData":[TD([makeQuery(id+"F8.opLoft","SWEPT_FACE",FACE,{"disambiguationData":[OSD([sQuery(id+"F3.wireOp",EDGE,"E20.13.0"),subQ59,subQ58,sQuery(id+"F4.wireOp",EDGE,"E26.13.0"),subQ57,subQ56])]})])],"derivedFrom":subQ9})])]}),makeQuery(id+"F47.opFillet","BLEND_FACE",FACE,{"disambiguationData":[OSD([subQ5,subQ7]),TDD([makeQuery(id+"F42.boolean.opBoolean","COPY",EDGE,{"disambiguationData":[TD([makeQuery(id+"F9.opLoft","SWEPT_FACE",FACE,{"disambiguationData":[OSD([sQuery(id+"F3.wireOp",EDGE,"E20.12.0"),subQ55,subQ54,sQuery(id+"F4.wireOp",EDGE,"E26.12.0"),subQ53,subQ52])]})])],"derivedFrom":subQ9})])]}),makeQuery(id+"F47.opFillet","BLEND_FACE",FACE,{"disambiguationData":[OSD([subQ5,subQ7]),TDD([makeQuery(id+"F42.boolean.opBoolean","COPY",EDGE,{"disambiguationData":[TD([makeQuery(id+"F10.opLoft","SWEPT_FACE",FACE,{"disambiguationData":[OSD([sQuery(id+"F3.wireOp",EDGE,"E20.11.0"),subQ51,subQ50,sQuery(id+"F4.wireOp",EDGE,"E26.11.0"),subQ49,subQ48])]})])],"derivedFrom":subQ9})])]}),makeQuery(id+"F47.opFillet","BLEND_FACE",FACE,{"disambiguationData":[OSD([subQ5,subQ7]),TDD([makeQuery(id+"F42.boolean.opBoolean","COPY",EDGE,{"disambiguationData":[TD([makeQuery(id+"F11.opLoft","SWEPT_FACE",FACE,{"disambiguationData":[OSD([sQuery(id+"F3.wireOp",EDGE,"E20.10.0"),subQ47,subQ46,sQuery(id+"F4.wireOp",EDGE,"E26.10.0"),subQ45,subQ44])]})])],"derivedFrom":subQ9})])]}),makeQuery(id+"F47.opFillet","BLEND_FACE",FACE,{"disambiguationData":[OSD([subQ5,subQ7]),TDD([makeQuery(id+"F42.boolean.opBoolean","COPY",EDGE,{"disambiguationData":[TD([makeQuery(id+"F12.opLoft","SWEPT_FACE",FACE,{"disambiguationData":[OSD([sQuery(id+"F3.wireOp",EDGE,"E20.9.0"),subQ43,subQ42,sQuery(id+"F4.wireOp",EDGE,"E26.9.0"),subQ41,subQ40])]})])],"derivedFrom":subQ9})])]}),makeQuery(id+"F47.opFillet","BLEND_FACE",FACE,{"disambiguationData":[OSD([subQ5,subQ7]),TDD([makeQuery(id+"F42.boolean.opBoolean","COPY",EDGE,{"disambiguationData":[TD([makeQuery(id+"F13.opLoft","SWEPT_FACE",FACE,{"disambiguationData":[OSD([sQuery(id+"F3.wireOp",EDGE,"E20.8.0"),subQ39,subQ38,sQuery(id+"F4.wireOp",EDGE,"E26.8.0"),subQ37,subQ36])]})])],"derivedFrom":subQ9})])]}),makeQuery(id+"F47.opFillet","BLEND_FACE",FACE,{"disambiguationData":[OSD([subQ5,subQ7]),TDD([makeQuery(id+"F42.boolean.opBoolean","COPY",EDGE,{"disambiguationData":[TD([makeQuery(id+"F14.opLoft","SWEPT_FACE",FACE,{"disambiguationData":[OSD([sQuery(id+"F3.wireOp",EDGE,"E20.7.0"),subQ35,subQ34,sQuery(id+"F4.wireOp",EDGE,"E26.7.0"),subQ33,subQ32])]})])],"derivedFrom":subQ9})])]}),makeQuery(id+"F47.opFillet","BLEND_FACE",FACE,{"disambiguationData":[OSD([subQ5,subQ7]),TDD([makeQuery(id+"F42.boolean.opBoolean","COPY",EDGE,{"disambiguationData":[TD([makeQuery(id+"F15.opLoft","SWEPT_FACE",FACE,{"disambiguationData":[OSD([sQuery(id+"F3.wireOp",EDGE,"E20.6.0"),subQ31,subQ30,sQuery(id+"F4.wireOp",EDGE,"E26.6.0"),subQ29,subQ28])]})])],"derivedFrom":subQ9})])]}),makeQuery(id+"F47.opFillet","BLEND_FACE",FACE,{"disambiguationData":[OSD([subQ5,subQ7]),TDD([makeQuery(id+"F42.boolean.opBoolean","COPY",EDGE,{"disambiguationData":[TD([makeQuery(id+"F16.opLoft","SWEPT_FACE",FACE,{"disambiguationData":[OSD([sQuery(id+"F3.wireOp",EDGE,"E20.5.0"),subQ27,subQ26,sQuery(id+"F4.wireOp",EDGE,"E26.5.0"),subQ25,subQ24])]})])],"derivedFrom":subQ9})])]}),makeQuery(id+"F47.opFillet","BLEND_FACE",FACE,{"disambiguationData":[OSD([subQ5,subQ7]),TDD([makeQuery(id+"F42.boolean.opBoolean","COPY",EDGE,{"disambiguationData":[TD([subQ23])],"derivedFrom":subQ9})])]}),makeQuery(id+"F47.opFillet","BLEND_FACE",FACE,{"disambiguationData":[OSD([subQ5,subQ7]),TDD([makeQuery(id+"F42.boolean.opBoolean","COPY",EDGE,{"disambiguationData":[TD([makeQuery(id+"F18.opLoft","SWEPT_FACE",FACE,{"disambiguationData":[OSD([sQuery(id+"F3.wireOp",EDGE,"E20.3.0"),subQ17,subQ16,sQuery(id+"F4.wireOp",EDGE,"E26.3.0"),subQ15,subQ14])]})])],"derivedFrom":subQ9})])]}),makeQuery(id+"F47.opFillet","BLEND_FACE",FACE,{"disambiguationData":[OSD([subQ5,subQ7]),TDD([makeQuery(id+"F42.boolean.opBoolean","COPY",EDGE,{"disambiguationData":[TD([makeQuery(id+"F19.opLoft","SWEPT_FACE",FACE,{"disambiguationData":[OSD([sQuery(id+"F3.wireOp",EDGE,"E20.2.0"),subQ13,subQ12,sQuery(id+"F4.wireOp",EDGE,"E26.2.0"),subQ11,subQ10])]})])],"derivedFrom":subQ9})])]}),makeQuery(id+"F47.opFillet","BLEND_FACE",FACE,{"disambiguationData":[OSD([subQ5,subQ7]),TDD([makeQuery(id+"F42.boolean.opBoolean","COPY",EDGE,{"disambiguationData":[TD([makeQuery(id+"F20.opLoft","SWEPT_FACE",FACE,{"disambiguationData":[OSD([sQuery(id+"F3.wireOp",EDGE,"E20.1.0"),subQ4,subQ3,sQuery(id+"F4.wireOp",EDGE,"E26.1.0"),subQ2,subQ1])]})])],"derivedFrom":subQ9})])]})]});}
            var Q51;
            {var subQ0=makeQuery(id+"F40.opExtrude","CAP_FACE",FACE,{"disambiguationData":[OSD([sQuery(id+"F39.wireOp",EDGE,"E29"),sQuery(id+"F39.wireOp",EDGE,"E30")])],"isStart":false});var subQ1=sQuery(id+"F4.wireOp",EDGE,"E26.1.3");var subQ2=sQuery(id+"F4.wireOp",EDGE,"E26.1.2");var subQ3=sQuery(id+"F3.wireOp",EDGE,"E20.1.3");var subQ4=sQuery(id+"F3.wireOp",EDGE,"E20.1.1");var subQ5=sQuery(id+"F41.wireOp",EDGE,"E35");var subQ6=makeQuery(id+"F42.opRevolve","SWEPT_FACE",FACE,{"disambiguationData":[OSD([subQ5])]});var subQ7=sQuery(id+"F41.wireOp",EDGE,"E36");var subQ8=makeQuery(id+"F42.opRevolve","SWEPT_FACE",FACE,{"disambiguationData":[OSD([subQ7])]});var subQ9=makeQuery(id+"F42.opRevolve","SWEPT_EDGE",EDGE,{"disambiguationData":[OSD([subQ5,subQ7])]});var subQ10=sQuery(id+"F4.wireOp",EDGE,"E26.2.3");var subQ11=sQuery(id+"F4.wireOp",EDGE,"E26.2.2");var subQ12=sQuery(id+"F3.wireOp",EDGE,"E20.2.3");var subQ13=sQuery(id+"F3.wireOp",EDGE,"E20.2.1");var subQ14=sQuery(id+"F4.wireOp",EDGE,"E26.3.3");var subQ15=sQuery(id+"F4.wireOp",EDGE,"E26.3.2");var subQ16=sQuery(id+"F3.wireOp",EDGE,"E20.3.3");var subQ17=sQuery(id+"F3.wireOp",EDGE,"E20.3.1");var subQ18=makeQuery(id+"F18.opLoft","SWEPT_FACE",FACE,{"disambiguationData":[OSD([sQuery(id+"F3.wireOp",EDGE,"E20.3.0"),subQ17,subQ16,sQuery(id+"F4.wireOp",EDGE,"E26.3.0"),subQ15,subQ14])]});var subQ20=sQuery(id+"F4.wireOp",EDGE,"E26.4.3");var subQ21=sQuery(id+"F4.wireOp",EDGE,"E26.4.2");var subQ22=sQuery(id+"F3.wireOp",EDGE,"E20.4.3");var subQ23=sQuery(id+"F3.wireOp",EDGE,"E20.4.1");var subQ24=sQuery(id+"F4.wireOp",EDGE,"E26.5.3");var subQ25=sQuery(id+"F4.wireOp",EDGE,"E26.5.2");var subQ26=sQuery(id+"F3.wireOp",EDGE,"E20.5.3");var subQ27=sQuery(id+"F3.wireOp",EDGE,"E20.5.1");var subQ28=sQuery(id+"F4.wireOp",EDGE,"E26.6.3");var subQ29=sQuery(id+"F4.wireOp",EDGE,"E26.6.2");var subQ30=sQuery(id+"F3.wireOp",EDGE,"E20.6.3");var subQ31=sQuery(id+"F3.wireOp",EDGE,"E20.6.1");var subQ32=sQuery(id+"F4.wireOp",EDGE,"E26.7.3");var subQ33=sQuery(id+"F4.wireOp",EDGE,"E26.7.2");var subQ34=sQuery(id+"F3.wireOp",EDGE,"E20.7.3");var subQ35=sQuery(id+"F3.wireOp",EDGE,"E20.7.1");var subQ36=sQuery(id+"F4.wireOp",EDGE,"E26.8.3");var subQ37=sQuery(id+"F4.wireOp",EDGE,"E26.8.2");var subQ38=sQuery(id+"F3.wireOp",EDGE,"E20.8.3");var subQ39=sQuery(id+"F3.wireOp",EDGE,"E20.8.1");var subQ40=sQuery(id+"F4.wireOp",EDGE,"E26.9.3");var subQ41=sQuery(id+"F4.wireOp",EDGE,"E26.9.2");var subQ42=sQuery(id+"F3.wireOp",EDGE,"E20.9.3");var subQ43=sQuery(id+"F3.wireOp",EDGE,"E20.9.1");var subQ44=sQuery(id+"F4.wireOp",EDGE,"E26.10.3");var subQ45=sQuery(id+"F4.wireOp",EDGE,"E26.10.2");var subQ46=sQuery(id+"F3.wireOp",EDGE,"E20.10.3");var subQ47=sQuery(id+"F3.wireOp",EDGE,"E20.10.1");var subQ48=sQuery(id+"F4.wireOp",EDGE,"E26.11.3");var subQ49=sQuery(id+"F4.wireOp",EDGE,"E26.11.2");var subQ50=sQuery(id+"F3.wireOp",EDGE,"E20.11.3");var subQ51=sQuery(id+"F3.wireOp",EDGE,"E20.11.1");var subQ52=sQuery(id+"F4.wireOp",EDGE,"E26.12.3");var subQ53=sQuery(id+"F4.wireOp",EDGE,"E26.12.2");var subQ54=sQuery(id+"F3.wireOp",EDGE,"E20.12.3");var subQ55=sQuery(id+"F3.wireOp",EDGE,"E20.12.1");var subQ56=sQuery(id+"F4.wireOp",EDGE,"E26.13.3");var subQ57=sQuery(id+"F4.wireOp",EDGE,"E26.13.2");var subQ58=sQuery(id+"F3.wireOp",EDGE,"E20.13.3");var subQ59=sQuery(id+"F3.wireOp",EDGE,"E20.13.1");var subQ60=sQuery(id+"F4.wireOp",EDGE,"E26.14.3");var subQ61=sQuery(id+"F4.wireOp",EDGE,"E26.14.2");var subQ62=sQuery(id+"F3.wireOp",EDGE,"E20.14.3");var subQ63=sQuery(id+"F3.wireOp",EDGE,"E20.14.1");var subQ64=sQuery(id+"F4.wireOp",EDGE,"E26.15.3");var subQ65=sQuery(id+"F4.wireOp",EDGE,"E26.15.2");var subQ66=sQuery(id+"F3.wireOp",EDGE,"E20.15.3");var subQ67=sQuery(id+"F3.wireOp",EDGE,"E20.15.1");var subQ68=sQuery(id+"F4.wireOp",EDGE,"E23");var subQ69=sQuery(id+"F4.wireOp",EDGE,"E22");var subQ70=sQuery(id+"F3.wireOp",EDGE,"E18.top");var subQ71=sQuery(id+"F3.wireOp",EDGE,"E18.bottom");var subQ74=makeQuery(id+"F42.boolean.opBoolean","COPY",FACE,{"disambiguationData":[TD([subQ18])],"derivedFrom":subQ6});var subQ75=makeQuery(id+"F18.boolean.opBoolean","INTERSECT",EDGE,{"derivedFrom":[makeQuery(id+"F1.opRevolve","SWEPT_FACE",FACE,{"disambiguationData":[OSD([sQuery(id+"F0.wireOp",EDGE,"E4")])]}),subQ18]});Q51=makeQuery(id+"F48.opFillet","BLEND_EDGE",EDGE,{"blendedFrom":[makeQuery(id+"F47.opFillet","TWEAK_EDGE",EDGE,{"derivedFrom":[makeQuery(id+"F45.opFillet","BLEND_VERTEX",VERTEX,{"blendedFrom":[subQ75,subQ18,subQ74],"blendedInto":[subQ18,subQ74]}),makeQuery(id+"F45.opFillet","BLEND_VERTEX",VERTEX,{"blendedFrom":[subQ75,makeQuery(id+"F42.boolean.opBoolean","MERGE",FACE,{"derivedFrom":[subQ0,subQ8]}),subQ74],"blendedInto":[makeQuery(id+"F42.boolean.opBoolean","MERGE",FACE,{"derivedFrom":[subQ0,subQ8]}),subQ74]})]}),makeQuery(id+"F47.opFillet","BLEND_FACE",FACE,{"disambiguationData":[OSD([subQ5,subQ7]),TDD([makeQuery(id+"F42.boolean.opBoolean","COPY",EDGE,{"disambiguationData":[TD([makeQuery(id+"F5.opLoft","SWEPT_FACE",FACE,{"disambiguationData":[OSD([subQ71,subQ70,sQuery(id+"F3.wireOp",EDGE,"E18.left"),sQuery(id+"F4.wireOp",EDGE,"E21"),subQ69,subQ68])]})])],"derivedFrom":subQ9})])]}),makeQuery(id+"F47.opFillet","BLEND_FACE",FACE,{"disambiguationData":[OSD([subQ5,subQ7]),TDD([makeQuery(id+"F42.boolean.opBoolean","COPY",EDGE,{"disambiguationData":[TD([makeQuery(id+"F6.opLoft","SWEPT_FACE",FACE,{"disambiguationData":[OSD([sQuery(id+"F3.wireOp",EDGE,"E20.15.0"),subQ67,subQ66,sQuery(id+"F4.wireOp",EDGE,"E26.15.0"),subQ65,subQ64])]})])],"derivedFrom":subQ9})])]}),makeQuery(id+"F47.opFillet","BLEND_FACE",FACE,{"disambiguationData":[OSD([subQ5,subQ7]),TDD([makeQuery(id+"F42.boolean.opBoolean","COPY",EDGE,{"disambiguationData":[TD([makeQuery(id+"F7.opLoft","SWEPT_FACE",FACE,{"disambiguationData":[OSD([sQuery(id+"F3.wireOp",EDGE,"E20.14.0"),subQ63,subQ62,sQuery(id+"F4.wireOp",EDGE,"E26.14.0"),subQ61,subQ60])]})])],"derivedFrom":subQ9})])]}),makeQuery(id+"F47.opFillet","BLEND_FACE",FACE,{"disambiguationData":[OSD([subQ5,subQ7]),TDD([makeQuery(id+"F42.boolean.opBoolean","COPY",EDGE,{"disambiguationData":[TD([makeQuery(id+"F8.opLoft","SWEPT_FACE",FACE,{"disambiguationData":[OSD([sQuery(id+"F3.wireOp",EDGE,"E20.13.0"),subQ59,subQ58,sQuery(id+"F4.wireOp",EDGE,"E26.13.0"),subQ57,subQ56])]})])],"derivedFrom":subQ9})])]}),makeQuery(id+"F47.opFillet","BLEND_FACE",FACE,{"disambiguationData":[OSD([subQ5,subQ7]),TDD([makeQuery(id+"F42.boolean.opBoolean","COPY",EDGE,{"disambiguationData":[TD([makeQuery(id+"F9.opLoft","SWEPT_FACE",FACE,{"disambiguationData":[OSD([sQuery(id+"F3.wireOp",EDGE,"E20.12.0"),subQ55,subQ54,sQuery(id+"F4.wireOp",EDGE,"E26.12.0"),subQ53,subQ52])]})])],"derivedFrom":subQ9})])]}),makeQuery(id+"F47.opFillet","BLEND_FACE",FACE,{"disambiguationData":[OSD([subQ5,subQ7]),TDD([makeQuery(id+"F42.boolean.opBoolean","COPY",EDGE,{"disambiguationData":[TD([makeQuery(id+"F10.opLoft","SWEPT_FACE",FACE,{"disambiguationData":[OSD([sQuery(id+"F3.wireOp",EDGE,"E20.11.0"),subQ51,subQ50,sQuery(id+"F4.wireOp",EDGE,"E26.11.0"),subQ49,subQ48])]})])],"derivedFrom":subQ9})])]}),makeQuery(id+"F47.opFillet","BLEND_FACE",FACE,{"disambiguationData":[OSD([subQ5,subQ7]),TDD([makeQuery(id+"F42.boolean.opBoolean","COPY",EDGE,{"disambiguationData":[TD([makeQuery(id+"F11.opLoft","SWEPT_FACE",FACE,{"disambiguationData":[OSD([sQuery(id+"F3.wireOp",EDGE,"E20.10.0"),subQ47,subQ46,sQuery(id+"F4.wireOp",EDGE,"E26.10.0"),subQ45,subQ44])]})])],"derivedFrom":subQ9})])]}),makeQuery(id+"F47.opFillet","BLEND_FACE",FACE,{"disambiguationData":[OSD([subQ5,subQ7]),TDD([makeQuery(id+"F42.boolean.opBoolean","COPY",EDGE,{"disambiguationData":[TD([makeQuery(id+"F12.opLoft","SWEPT_FACE",FACE,{"disambiguationData":[OSD([sQuery(id+"F3.wireOp",EDGE,"E20.9.0"),subQ43,subQ42,sQuery(id+"F4.wireOp",EDGE,"E26.9.0"),subQ41,subQ40])]})])],"derivedFrom":subQ9})])]}),makeQuery(id+"F47.opFillet","BLEND_FACE",FACE,{"disambiguationData":[OSD([subQ5,subQ7]),TDD([makeQuery(id+"F42.boolean.opBoolean","COPY",EDGE,{"disambiguationData":[TD([makeQuery(id+"F13.opLoft","SWEPT_FACE",FACE,{"disambiguationData":[OSD([sQuery(id+"F3.wireOp",EDGE,"E20.8.0"),subQ39,subQ38,sQuery(id+"F4.wireOp",EDGE,"E26.8.0"),subQ37,subQ36])]})])],"derivedFrom":subQ9})])]}),makeQuery(id+"F47.opFillet","BLEND_FACE",FACE,{"disambiguationData":[OSD([subQ5,subQ7]),TDD([makeQuery(id+"F42.boolean.opBoolean","COPY",EDGE,{"disambiguationData":[TD([makeQuery(id+"F14.opLoft","SWEPT_FACE",FACE,{"disambiguationData":[OSD([sQuery(id+"F3.wireOp",EDGE,"E20.7.0"),subQ35,subQ34,sQuery(id+"F4.wireOp",EDGE,"E26.7.0"),subQ33,subQ32])]})])],"derivedFrom":subQ9})])]}),makeQuery(id+"F47.opFillet","BLEND_FACE",FACE,{"disambiguationData":[OSD([subQ5,subQ7]),TDD([makeQuery(id+"F42.boolean.opBoolean","COPY",EDGE,{"disambiguationData":[TD([makeQuery(id+"F15.opLoft","SWEPT_FACE",FACE,{"disambiguationData":[OSD([sQuery(id+"F3.wireOp",EDGE,"E20.6.0"),subQ31,subQ30,sQuery(id+"F4.wireOp",EDGE,"E26.6.0"),subQ29,subQ28])]})])],"derivedFrom":subQ9})])]}),makeQuery(id+"F47.opFillet","BLEND_FACE",FACE,{"disambiguationData":[OSD([subQ5,subQ7]),TDD([makeQuery(id+"F42.boolean.opBoolean","COPY",EDGE,{"disambiguationData":[TD([makeQuery(id+"F16.opLoft","SWEPT_FACE",FACE,{"disambiguationData":[OSD([sQuery(id+"F3.wireOp",EDGE,"E20.5.0"),subQ27,subQ26,sQuery(id+"F4.wireOp",EDGE,"E26.5.0"),subQ25,subQ24])]})])],"derivedFrom":subQ9})])]}),makeQuery(id+"F47.opFillet","BLEND_FACE",FACE,{"disambiguationData":[OSD([subQ5,subQ7]),TDD([makeQuery(id+"F42.boolean.opBoolean","COPY",EDGE,{"disambiguationData":[TD([makeQuery(id+"F17.opLoft","SWEPT_FACE",FACE,{"disambiguationData":[OSD([sQuery(id+"F3.wireOp",EDGE,"E20.4.0"),subQ23,subQ22,sQuery(id+"F4.wireOp",EDGE,"E26.4.0"),subQ21,subQ20])]})])],"derivedFrom":subQ9})])]}),makeQuery(id+"F47.opFillet","BLEND_FACE",FACE,{"disambiguationData":[OSD([subQ5,subQ7]),TDD([makeQuery(id+"F42.boolean.opBoolean","COPY",EDGE,{"disambiguationData":[TD([subQ18])],"derivedFrom":subQ9})])]}),makeQuery(id+"F47.opFillet","BLEND_FACE",FACE,{"disambiguationData":[OSD([subQ5,subQ7]),TDD([makeQuery(id+"F42.boolean.opBoolean","COPY",EDGE,{"disambiguationData":[TD([makeQuery(id+"F19.opLoft","SWEPT_FACE",FACE,{"disambiguationData":[OSD([sQuery(id+"F3.wireOp",EDGE,"E20.2.0"),subQ13,subQ12,sQuery(id+"F4.wireOp",EDGE,"E26.2.0"),subQ11,subQ10])]})])],"derivedFrom":subQ9})])]}),makeQuery(id+"F47.opFillet","BLEND_FACE",FACE,{"disambiguationData":[OSD([subQ5,subQ7]),TDD([makeQuery(id+"F42.boolean.opBoolean","COPY",EDGE,{"disambiguationData":[TD([makeQuery(id+"F20.opLoft","SWEPT_FACE",FACE,{"disambiguationData":[OSD([sQuery(id+"F3.wireOp",EDGE,"E20.1.0"),subQ4,subQ3,sQuery(id+"F4.wireOp",EDGE,"E26.1.0"),subQ2,subQ1])]})])],"derivedFrom":subQ9})])]})],"blendedInto":[makeQuery(id+"F47.opFillet","BLEND_FACE",FACE,{"disambiguationData":[OSD([subQ5,subQ7]),TDD([makeQuery(id+"F42.boolean.opBoolean","COPY",EDGE,{"disambiguationData":[TD([makeQuery(id+"F5.opLoft","SWEPT_FACE",FACE,{"disambiguationData":[OSD([subQ71,subQ70,sQuery(id+"F3.wireOp",EDGE,"E18.left"),sQuery(id+"F4.wireOp",EDGE,"E21"),subQ69,subQ68])]})])],"derivedFrom":subQ9})])]}),makeQuery(id+"F47.opFillet","BLEND_FACE",FACE,{"disambiguationData":[OSD([subQ5,subQ7]),TDD([makeQuery(id+"F42.boolean.opBoolean","COPY",EDGE,{"disambiguationData":[TD([makeQuery(id+"F6.opLoft","SWEPT_FACE",FACE,{"disambiguationData":[OSD([sQuery(id+"F3.wireOp",EDGE,"E20.15.0"),subQ67,subQ66,sQuery(id+"F4.wireOp",EDGE,"E26.15.0"),subQ65,subQ64])]})])],"derivedFrom":subQ9})])]}),makeQuery(id+"F47.opFillet","BLEND_FACE",FACE,{"disambiguationData":[OSD([subQ5,subQ7]),TDD([makeQuery(id+"F42.boolean.opBoolean","COPY",EDGE,{"disambiguationData":[TD([makeQuery(id+"F7.opLoft","SWEPT_FACE",FACE,{"disambiguationData":[OSD([sQuery(id+"F3.wireOp",EDGE,"E20.14.0"),subQ63,subQ62,sQuery(id+"F4.wireOp",EDGE,"E26.14.0"),subQ61,subQ60])]})])],"derivedFrom":subQ9})])]}),makeQuery(id+"F47.opFillet","BLEND_FACE",FACE,{"disambiguationData":[OSD([subQ5,subQ7]),TDD([makeQuery(id+"F42.boolean.opBoolean","COPY",EDGE,{"disambiguationData":[TD([makeQuery(id+"F8.opLoft","SWEPT_FACE",FACE,{"disambiguationData":[OSD([sQuery(id+"F3.wireOp",EDGE,"E20.13.0"),subQ59,subQ58,sQuery(id+"F4.wireOp",EDGE,"E26.13.0"),subQ57,subQ56])]})])],"derivedFrom":subQ9})])]}),makeQuery(id+"F47.opFillet","BLEND_FACE",FACE,{"disambiguationData":[OSD([subQ5,subQ7]),TDD([makeQuery(id+"F42.boolean.opBoolean","COPY",EDGE,{"disambiguationData":[TD([makeQuery(id+"F9.opLoft","SWEPT_FACE",FACE,{"disambiguationData":[OSD([sQuery(id+"F3.wireOp",EDGE,"E20.12.0"),subQ55,subQ54,sQuery(id+"F4.wireOp",EDGE,"E26.12.0"),subQ53,subQ52])]})])],"derivedFrom":subQ9})])]}),makeQuery(id+"F47.opFillet","BLEND_FACE",FACE,{"disambiguationData":[OSD([subQ5,subQ7]),TDD([makeQuery(id+"F42.boolean.opBoolean","COPY",EDGE,{"disambiguationData":[TD([makeQuery(id+"F10.opLoft","SWEPT_FACE",FACE,{"disambiguationData":[OSD([sQuery(id+"F3.wireOp",EDGE,"E20.11.0"),subQ51,subQ50,sQuery(id+"F4.wireOp",EDGE,"E26.11.0"),subQ49,subQ48])]})])],"derivedFrom":subQ9})])]}),makeQuery(id+"F47.opFillet","BLEND_FACE",FACE,{"disambiguationData":[OSD([subQ5,subQ7]),TDD([makeQuery(id+"F42.boolean.opBoolean","COPY",EDGE,{"disambiguationData":[TD([makeQuery(id+"F11.opLoft","SWEPT_FACE",FACE,{"disambiguationData":[OSD([sQuery(id+"F3.wireOp",EDGE,"E20.10.0"),subQ47,subQ46,sQuery(id+"F4.wireOp",EDGE,"E26.10.0"),subQ45,subQ44])]})])],"derivedFrom":subQ9})])]}),makeQuery(id+"F47.opFillet","BLEND_FACE",FACE,{"disambiguationData":[OSD([subQ5,subQ7]),TDD([makeQuery(id+"F42.boolean.opBoolean","COPY",EDGE,{"disambiguationData":[TD([makeQuery(id+"F12.opLoft","SWEPT_FACE",FACE,{"disambiguationData":[OSD([sQuery(id+"F3.wireOp",EDGE,"E20.9.0"),subQ43,subQ42,sQuery(id+"F4.wireOp",EDGE,"E26.9.0"),subQ41,subQ40])]})])],"derivedFrom":subQ9})])]}),makeQuery(id+"F47.opFillet","BLEND_FACE",FACE,{"disambiguationData":[OSD([subQ5,subQ7]),TDD([makeQuery(id+"F42.boolean.opBoolean","COPY",EDGE,{"disambiguationData":[TD([makeQuery(id+"F13.opLoft","SWEPT_FACE",FACE,{"disambiguationData":[OSD([sQuery(id+"F3.wireOp",EDGE,"E20.8.0"),subQ39,subQ38,sQuery(id+"F4.wireOp",EDGE,"E26.8.0"),subQ37,subQ36])]})])],"derivedFrom":subQ9})])]}),makeQuery(id+"F47.opFillet","BLEND_FACE",FACE,{"disambiguationData":[OSD([subQ5,subQ7]),TDD([makeQuery(id+"F42.boolean.opBoolean","COPY",EDGE,{"disambiguationData":[TD([makeQuery(id+"F14.opLoft","SWEPT_FACE",FACE,{"disambiguationData":[OSD([sQuery(id+"F3.wireOp",EDGE,"E20.7.0"),subQ35,subQ34,sQuery(id+"F4.wireOp",EDGE,"E26.7.0"),subQ33,subQ32])]})])],"derivedFrom":subQ9})])]}),makeQuery(id+"F47.opFillet","BLEND_FACE",FACE,{"disambiguationData":[OSD([subQ5,subQ7]),TDD([makeQuery(id+"F42.boolean.opBoolean","COPY",EDGE,{"disambiguationData":[TD([makeQuery(id+"F15.opLoft","SWEPT_FACE",FACE,{"disambiguationData":[OSD([sQuery(id+"F3.wireOp",EDGE,"E20.6.0"),subQ31,subQ30,sQuery(id+"F4.wireOp",EDGE,"E26.6.0"),subQ29,subQ28])]})])],"derivedFrom":subQ9})])]}),makeQuery(id+"F47.opFillet","BLEND_FACE",FACE,{"disambiguationData":[OSD([subQ5,subQ7]),TDD([makeQuery(id+"F42.boolean.opBoolean","COPY",EDGE,{"disambiguationData":[TD([makeQuery(id+"F16.opLoft","SWEPT_FACE",FACE,{"disambiguationData":[OSD([sQuery(id+"F3.wireOp",EDGE,"E20.5.0"),subQ27,subQ26,sQuery(id+"F4.wireOp",EDGE,"E26.5.0"),subQ25,subQ24])]})])],"derivedFrom":subQ9})])]}),makeQuery(id+"F47.opFillet","BLEND_FACE",FACE,{"disambiguationData":[OSD([subQ5,subQ7]),TDD([makeQuery(id+"F42.boolean.opBoolean","COPY",EDGE,{"disambiguationData":[TD([makeQuery(id+"F17.opLoft","SWEPT_FACE",FACE,{"disambiguationData":[OSD([sQuery(id+"F3.wireOp",EDGE,"E20.4.0"),subQ23,subQ22,sQuery(id+"F4.wireOp",EDGE,"E26.4.0"),subQ21,subQ20])]})])],"derivedFrom":subQ9})])]}),makeQuery(id+"F47.opFillet","BLEND_FACE",FACE,{"disambiguationData":[OSD([subQ5,subQ7]),TDD([makeQuery(id+"F42.boolean.opBoolean","COPY",EDGE,{"disambiguationData":[TD([subQ18])],"derivedFrom":subQ9})])]}),makeQuery(id+"F47.opFillet","BLEND_FACE",FACE,{"disambiguationData":[OSD([subQ5,subQ7]),TDD([makeQuery(id+"F42.boolean.opBoolean","COPY",EDGE,{"disambiguationData":[TD([makeQuery(id+"F19.opLoft","SWEPT_FACE",FACE,{"disambiguationData":[OSD([sQuery(id+"F3.wireOp",EDGE,"E20.2.0"),subQ13,subQ12,sQuery(id+"F4.wireOp",EDGE,"E26.2.0"),subQ11,subQ10])]})])],"derivedFrom":subQ9})])]}),makeQuery(id+"F47.opFillet","BLEND_FACE",FACE,{"disambiguationData":[OSD([subQ5,subQ7]),TDD([makeQuery(id+"F42.boolean.opBoolean","COPY",EDGE,{"disambiguationData":[TD([makeQuery(id+"F20.opLoft","SWEPT_FACE",FACE,{"disambiguationData":[OSD([sQuery(id+"F3.wireOp",EDGE,"E20.1.0"),subQ4,subQ3,sQuery(id+"F4.wireOp",EDGE,"E26.1.0"),subQ2,subQ1])]})])],"derivedFrom":subQ9})])]})]});}
            var Q52;
            {var subQ0=makeQuery(id+"F40.opExtrude","CAP_FACE",FACE,{"disambiguationData":[OSD([sQuery(id+"F39.wireOp",EDGE,"E29"),sQuery(id+"F39.wireOp",EDGE,"E30")])],"isStart":false});var subQ1=sQuery(id+"F4.wireOp",EDGE,"E26.1.3");var subQ2=sQuery(id+"F4.wireOp",EDGE,"E26.1.2");var subQ3=sQuery(id+"F3.wireOp",EDGE,"E20.1.3");var subQ4=sQuery(id+"F3.wireOp",EDGE,"E20.1.1");var subQ5=sQuery(id+"F41.wireOp",EDGE,"E35");var subQ6=makeQuery(id+"F42.opRevolve","SWEPT_FACE",FACE,{"disambiguationData":[OSD([subQ5])]});var subQ7=sQuery(id+"F41.wireOp",EDGE,"E36");var subQ8=makeQuery(id+"F42.opRevolve","SWEPT_FACE",FACE,{"disambiguationData":[OSD([subQ7])]});var subQ9=makeQuery(id+"F42.opRevolve","SWEPT_EDGE",EDGE,{"disambiguationData":[OSD([subQ5,subQ7])]});var subQ10=sQuery(id+"F4.wireOp",EDGE,"E26.2.3");var subQ11=sQuery(id+"F4.wireOp",EDGE,"E26.2.2");var subQ12=sQuery(id+"F3.wireOp",EDGE,"E20.2.3");var subQ13=sQuery(id+"F3.wireOp",EDGE,"E20.2.1");var subQ15=makeQuery(id+"F19.opLoft","SWEPT_FACE",FACE,{"disambiguationData":[OSD([sQuery(id+"F3.wireOp",EDGE,"E20.2.0"),subQ13,subQ12,sQuery(id+"F4.wireOp",EDGE,"E26.2.0"),subQ11,subQ10])]});var subQ16=sQuery(id+"F4.wireOp",EDGE,"E26.3.3");var subQ17=sQuery(id+"F4.wireOp",EDGE,"E26.3.2");var subQ18=sQuery(id+"F3.wireOp",EDGE,"E20.3.3");var subQ19=sQuery(id+"F3.wireOp",EDGE,"E20.3.1");var subQ20=sQuery(id+"F4.wireOp",EDGE,"E26.4.3");var subQ21=sQuery(id+"F4.wireOp",EDGE,"E26.4.2");var subQ22=sQuery(id+"F3.wireOp",EDGE,"E20.4.3");var subQ23=sQuery(id+"F3.wireOp",EDGE,"E20.4.1");var subQ24=sQuery(id+"F4.wireOp",EDGE,"E26.5.3");var subQ25=sQuery(id+"F4.wireOp",EDGE,"E26.5.2");var subQ26=sQuery(id+"F3.wireOp",EDGE,"E20.5.3");var subQ27=sQuery(id+"F3.wireOp",EDGE,"E20.5.1");var subQ28=sQuery(id+"F4.wireOp",EDGE,"E26.6.3");var subQ29=sQuery(id+"F4.wireOp",EDGE,"E26.6.2");var subQ30=sQuery(id+"F3.wireOp",EDGE,"E20.6.3");var subQ31=sQuery(id+"F3.wireOp",EDGE,"E20.6.1");var subQ32=sQuery(id+"F4.wireOp",EDGE,"E26.7.3");var subQ33=sQuery(id+"F4.wireOp",EDGE,"E26.7.2");var subQ34=sQuery(id+"F3.wireOp",EDGE,"E20.7.3");var subQ35=sQuery(id+"F3.wireOp",EDGE,"E20.7.1");var subQ36=sQuery(id+"F4.wireOp",EDGE,"E26.8.3");var subQ37=sQuery(id+"F4.wireOp",EDGE,"E26.8.2");var subQ38=sQuery(id+"F3.wireOp",EDGE,"E20.8.3");var subQ39=sQuery(id+"F3.wireOp",EDGE,"E20.8.1");var subQ40=sQuery(id+"F4.wireOp",EDGE,"E26.9.3");var subQ41=sQuery(id+"F4.wireOp",EDGE,"E26.9.2");var subQ42=sQuery(id+"F3.wireOp",EDGE,"E20.9.3");var subQ43=sQuery(id+"F3.wireOp",EDGE,"E20.9.1");var subQ44=sQuery(id+"F4.wireOp",EDGE,"E26.10.3");var subQ45=sQuery(id+"F4.wireOp",EDGE,"E26.10.2");var subQ46=sQuery(id+"F3.wireOp",EDGE,"E20.10.3");var subQ47=sQuery(id+"F3.wireOp",EDGE,"E20.10.1");var subQ48=sQuery(id+"F4.wireOp",EDGE,"E26.11.3");var subQ49=sQuery(id+"F4.wireOp",EDGE,"E26.11.2");var subQ50=sQuery(id+"F3.wireOp",EDGE,"E20.11.3");var subQ51=sQuery(id+"F3.wireOp",EDGE,"E20.11.1");var subQ52=sQuery(id+"F4.wireOp",EDGE,"E26.12.3");var subQ53=sQuery(id+"F4.wireOp",EDGE,"E26.12.2");var subQ54=sQuery(id+"F3.wireOp",EDGE,"E20.12.3");var subQ55=sQuery(id+"F3.wireOp",EDGE,"E20.12.1");var subQ56=sQuery(id+"F4.wireOp",EDGE,"E26.13.3");var subQ57=sQuery(id+"F4.wireOp",EDGE,"E26.13.2");var subQ58=sQuery(id+"F3.wireOp",EDGE,"E20.13.3");var subQ59=sQuery(id+"F3.wireOp",EDGE,"E20.13.1");var subQ60=sQuery(id+"F4.wireOp",EDGE,"E26.14.3");var subQ61=sQuery(id+"F4.wireOp",EDGE,"E26.14.2");var subQ62=sQuery(id+"F3.wireOp",EDGE,"E20.14.3");var subQ63=sQuery(id+"F3.wireOp",EDGE,"E20.14.1");var subQ64=sQuery(id+"F4.wireOp",EDGE,"E26.15.3");var subQ65=sQuery(id+"F4.wireOp",EDGE,"E26.15.2");var subQ66=sQuery(id+"F3.wireOp",EDGE,"E20.15.3");var subQ67=sQuery(id+"F3.wireOp",EDGE,"E20.15.1");var subQ68=sQuery(id+"F4.wireOp",EDGE,"E23");var subQ69=sQuery(id+"F4.wireOp",EDGE,"E22");var subQ70=sQuery(id+"F3.wireOp",EDGE,"E18.top");var subQ71=sQuery(id+"F3.wireOp",EDGE,"E18.bottom");var subQ74=makeQuery(id+"F42.boolean.opBoolean","COPY",FACE,{"disambiguationData":[TD([subQ15])],"derivedFrom":subQ6});var subQ75=makeQuery(id+"F19.boolean.opBoolean","INTERSECT",EDGE,{"derivedFrom":[makeQuery(id+"F1.opRevolve","SWEPT_FACE",FACE,{"disambiguationData":[OSD([sQuery(id+"F0.wireOp",EDGE,"E4")])]}),subQ15]});Q52=makeQuery(id+"F48.opFillet","BLEND_EDGE",EDGE,{"blendedFrom":[makeQuery(id+"F47.opFillet","TWEAK_EDGE",EDGE,{"derivedFrom":[makeQuery(id+"F45.opFillet","BLEND_VERTEX",VERTEX,{"blendedFrom":[subQ75,subQ15,subQ74],"blendedInto":[subQ15,subQ74]}),makeQuery(id+"F45.opFillet","BLEND_VERTEX",VERTEX,{"blendedFrom":[subQ75,makeQuery(id+"F42.boolean.opBoolean","MERGE",FACE,{"derivedFrom":[subQ0,subQ8]}),subQ74],"blendedInto":[makeQuery(id+"F42.boolean.opBoolean","MERGE",FACE,{"derivedFrom":[subQ0,subQ8]}),subQ74]})]}),makeQuery(id+"F47.opFillet","BLEND_FACE",FACE,{"disambiguationData":[OSD([subQ5,subQ7]),TDD([makeQuery(id+"F42.boolean.opBoolean","COPY",EDGE,{"disambiguationData":[TD([makeQuery(id+"F5.opLoft","SWEPT_FACE",FACE,{"disambiguationData":[OSD([subQ71,subQ70,sQuery(id+"F3.wireOp",EDGE,"E18.left"),sQuery(id+"F4.wireOp",EDGE,"E21"),subQ69,subQ68])]})])],"derivedFrom":subQ9})])]}),makeQuery(id+"F47.opFillet","BLEND_FACE",FACE,{"disambiguationData":[OSD([subQ5,subQ7]),TDD([makeQuery(id+"F42.boolean.opBoolean","COPY",EDGE,{"disambiguationData":[TD([makeQuery(id+"F6.opLoft","SWEPT_FACE",FACE,{"disambiguationData":[OSD([sQuery(id+"F3.wireOp",EDGE,"E20.15.0"),subQ67,subQ66,sQuery(id+"F4.wireOp",EDGE,"E26.15.0"),subQ65,subQ64])]})])],"derivedFrom":subQ9})])]}),makeQuery(id+"F47.opFillet","BLEND_FACE",FACE,{"disambiguationData":[OSD([subQ5,subQ7]),TDD([makeQuery(id+"F42.boolean.opBoolean","COPY",EDGE,{"disambiguationData":[TD([makeQuery(id+"F7.opLoft","SWEPT_FACE",FACE,{"disambiguationData":[OSD([sQuery(id+"F3.wireOp",EDGE,"E20.14.0"),subQ63,subQ62,sQuery(id+"F4.wireOp",EDGE,"E26.14.0"),subQ61,subQ60])]})])],"derivedFrom":subQ9})])]}),makeQuery(id+"F47.opFillet","BLEND_FACE",FACE,{"disambiguationData":[OSD([subQ5,subQ7]),TDD([makeQuery(id+"F42.boolean.opBoolean","COPY",EDGE,{"disambiguationData":[TD([makeQuery(id+"F8.opLoft","SWEPT_FACE",FACE,{"disambiguationData":[OSD([sQuery(id+"F3.wireOp",EDGE,"E20.13.0"),subQ59,subQ58,sQuery(id+"F4.wireOp",EDGE,"E26.13.0"),subQ57,subQ56])]})])],"derivedFrom":subQ9})])]}),makeQuery(id+"F47.opFillet","BLEND_FACE",FACE,{"disambiguationData":[OSD([subQ5,subQ7]),TDD([makeQuery(id+"F42.boolean.opBoolean","COPY",EDGE,{"disambiguationData":[TD([makeQuery(id+"F9.opLoft","SWEPT_FACE",FACE,{"disambiguationData":[OSD([sQuery(id+"F3.wireOp",EDGE,"E20.12.0"),subQ55,subQ54,sQuery(id+"F4.wireOp",EDGE,"E26.12.0"),subQ53,subQ52])]})])],"derivedFrom":subQ9})])]}),makeQuery(id+"F47.opFillet","BLEND_FACE",FACE,{"disambiguationData":[OSD([subQ5,subQ7]),TDD([makeQuery(id+"F42.boolean.opBoolean","COPY",EDGE,{"disambiguationData":[TD([makeQuery(id+"F10.opLoft","SWEPT_FACE",FACE,{"disambiguationData":[OSD([sQuery(id+"F3.wireOp",EDGE,"E20.11.0"),subQ51,subQ50,sQuery(id+"F4.wireOp",EDGE,"E26.11.0"),subQ49,subQ48])]})])],"derivedFrom":subQ9})])]}),makeQuery(id+"F47.opFillet","BLEND_FACE",FACE,{"disambiguationData":[OSD([subQ5,subQ7]),TDD([makeQuery(id+"F42.boolean.opBoolean","COPY",EDGE,{"disambiguationData":[TD([makeQuery(id+"F11.opLoft","SWEPT_FACE",FACE,{"disambiguationData":[OSD([sQuery(id+"F3.wireOp",EDGE,"E20.10.0"),subQ47,subQ46,sQuery(id+"F4.wireOp",EDGE,"E26.10.0"),subQ45,subQ44])]})])],"derivedFrom":subQ9})])]}),makeQuery(id+"F47.opFillet","BLEND_FACE",FACE,{"disambiguationData":[OSD([subQ5,subQ7]),TDD([makeQuery(id+"F42.boolean.opBoolean","COPY",EDGE,{"disambiguationData":[TD([makeQuery(id+"F12.opLoft","SWEPT_FACE",FACE,{"disambiguationData":[OSD([sQuery(id+"F3.wireOp",EDGE,"E20.9.0"),subQ43,subQ42,sQuery(id+"F4.wireOp",EDGE,"E26.9.0"),subQ41,subQ40])]})])],"derivedFrom":subQ9})])]}),makeQuery(id+"F47.opFillet","BLEND_FACE",FACE,{"disambiguationData":[OSD([subQ5,subQ7]),TDD([makeQuery(id+"F42.boolean.opBoolean","COPY",EDGE,{"disambiguationData":[TD([makeQuery(id+"F13.opLoft","SWEPT_FACE",FACE,{"disambiguationData":[OSD([sQuery(id+"F3.wireOp",EDGE,"E20.8.0"),subQ39,subQ38,sQuery(id+"F4.wireOp",EDGE,"E26.8.0"),subQ37,subQ36])]})])],"derivedFrom":subQ9})])]}),makeQuery(id+"F47.opFillet","BLEND_FACE",FACE,{"disambiguationData":[OSD([subQ5,subQ7]),TDD([makeQuery(id+"F42.boolean.opBoolean","COPY",EDGE,{"disambiguationData":[TD([makeQuery(id+"F14.opLoft","SWEPT_FACE",FACE,{"disambiguationData":[OSD([sQuery(id+"F3.wireOp",EDGE,"E20.7.0"),subQ35,subQ34,sQuery(id+"F4.wireOp",EDGE,"E26.7.0"),subQ33,subQ32])]})])],"derivedFrom":subQ9})])]}),makeQuery(id+"F47.opFillet","BLEND_FACE",FACE,{"disambiguationData":[OSD([subQ5,subQ7]),TDD([makeQuery(id+"F42.boolean.opBoolean","COPY",EDGE,{"disambiguationData":[TD([makeQuery(id+"F15.opLoft","SWEPT_FACE",FACE,{"disambiguationData":[OSD([sQuery(id+"F3.wireOp",EDGE,"E20.6.0"),subQ31,subQ30,sQuery(id+"F4.wireOp",EDGE,"E26.6.0"),subQ29,subQ28])]})])],"derivedFrom":subQ9})])]}),makeQuery(id+"F47.opFillet","BLEND_FACE",FACE,{"disambiguationData":[OSD([subQ5,subQ7]),TDD([makeQuery(id+"F42.boolean.opBoolean","COPY",EDGE,{"disambiguationData":[TD([makeQuery(id+"F16.opLoft","SWEPT_FACE",FACE,{"disambiguationData":[OSD([sQuery(id+"F3.wireOp",EDGE,"E20.5.0"),subQ27,subQ26,sQuery(id+"F4.wireOp",EDGE,"E26.5.0"),subQ25,subQ24])]})])],"derivedFrom":subQ9})])]}),makeQuery(id+"F47.opFillet","BLEND_FACE",FACE,{"disambiguationData":[OSD([subQ5,subQ7]),TDD([makeQuery(id+"F42.boolean.opBoolean","COPY",EDGE,{"disambiguationData":[TD([makeQuery(id+"F17.opLoft","SWEPT_FACE",FACE,{"disambiguationData":[OSD([sQuery(id+"F3.wireOp",EDGE,"E20.4.0"),subQ23,subQ22,sQuery(id+"F4.wireOp",EDGE,"E26.4.0"),subQ21,subQ20])]})])],"derivedFrom":subQ9})])]}),makeQuery(id+"F47.opFillet","BLEND_FACE",FACE,{"disambiguationData":[OSD([subQ5,subQ7]),TDD([makeQuery(id+"F42.boolean.opBoolean","COPY",EDGE,{"disambiguationData":[TD([makeQuery(id+"F18.opLoft","SWEPT_FACE",FACE,{"disambiguationData":[OSD([sQuery(id+"F3.wireOp",EDGE,"E20.3.0"),subQ19,subQ18,sQuery(id+"F4.wireOp",EDGE,"E26.3.0"),subQ17,subQ16])]})])],"derivedFrom":subQ9})])]}),makeQuery(id+"F47.opFillet","BLEND_FACE",FACE,{"disambiguationData":[OSD([subQ5,subQ7]),TDD([makeQuery(id+"F42.boolean.opBoolean","COPY",EDGE,{"disambiguationData":[TD([subQ15])],"derivedFrom":subQ9})])]}),makeQuery(id+"F47.opFillet","BLEND_FACE",FACE,{"disambiguationData":[OSD([subQ5,subQ7]),TDD([makeQuery(id+"F42.boolean.opBoolean","COPY",EDGE,{"disambiguationData":[TD([makeQuery(id+"F20.opLoft","SWEPT_FACE",FACE,{"disambiguationData":[OSD([sQuery(id+"F3.wireOp",EDGE,"E20.1.0"),subQ4,subQ3,sQuery(id+"F4.wireOp",EDGE,"E26.1.0"),subQ2,subQ1])]})])],"derivedFrom":subQ9})])]})],"blendedInto":[makeQuery(id+"F47.opFillet","BLEND_FACE",FACE,{"disambiguationData":[OSD([subQ5,subQ7]),TDD([makeQuery(id+"F42.boolean.opBoolean","COPY",EDGE,{"disambiguationData":[TD([makeQuery(id+"F5.opLoft","SWEPT_FACE",FACE,{"disambiguationData":[OSD([subQ71,subQ70,sQuery(id+"F3.wireOp",EDGE,"E18.left"),sQuery(id+"F4.wireOp",EDGE,"E21"),subQ69,subQ68])]})])],"derivedFrom":subQ9})])]}),makeQuery(id+"F47.opFillet","BLEND_FACE",FACE,{"disambiguationData":[OSD([subQ5,subQ7]),TDD([makeQuery(id+"F42.boolean.opBoolean","COPY",EDGE,{"disambiguationData":[TD([makeQuery(id+"F6.opLoft","SWEPT_FACE",FACE,{"disambiguationData":[OSD([sQuery(id+"F3.wireOp",EDGE,"E20.15.0"),subQ67,subQ66,sQuery(id+"F4.wireOp",EDGE,"E26.15.0"),subQ65,subQ64])]})])],"derivedFrom":subQ9})])]}),makeQuery(id+"F47.opFillet","BLEND_FACE",FACE,{"disambiguationData":[OSD([subQ5,subQ7]),TDD([makeQuery(id+"F42.boolean.opBoolean","COPY",EDGE,{"disambiguationData":[TD([makeQuery(id+"F7.opLoft","SWEPT_FACE",FACE,{"disambiguationData":[OSD([sQuery(id+"F3.wireOp",EDGE,"E20.14.0"),subQ63,subQ62,sQuery(id+"F4.wireOp",EDGE,"E26.14.0"),subQ61,subQ60])]})])],"derivedFrom":subQ9})])]}),makeQuery(id+"F47.opFillet","BLEND_FACE",FACE,{"disambiguationData":[OSD([subQ5,subQ7]),TDD([makeQuery(id+"F42.boolean.opBoolean","COPY",EDGE,{"disambiguationData":[TD([makeQuery(id+"F8.opLoft","SWEPT_FACE",FACE,{"disambiguationData":[OSD([sQuery(id+"F3.wireOp",EDGE,"E20.13.0"),subQ59,subQ58,sQuery(id+"F4.wireOp",EDGE,"E26.13.0"),subQ57,subQ56])]})])],"derivedFrom":subQ9})])]}),makeQuery(id+"F47.opFillet","BLEND_FACE",FACE,{"disambiguationData":[OSD([subQ5,subQ7]),TDD([makeQuery(id+"F42.boolean.opBoolean","COPY",EDGE,{"disambiguationData":[TD([makeQuery(id+"F9.opLoft","SWEPT_FACE",FACE,{"disambiguationData":[OSD([sQuery(id+"F3.wireOp",EDGE,"E20.12.0"),subQ55,subQ54,sQuery(id+"F4.wireOp",EDGE,"E26.12.0"),subQ53,subQ52])]})])],"derivedFrom":subQ9})])]}),makeQuery(id+"F47.opFillet","BLEND_FACE",FACE,{"disambiguationData":[OSD([subQ5,subQ7]),TDD([makeQuery(id+"F42.boolean.opBoolean","COPY",EDGE,{"disambiguationData":[TD([makeQuery(id+"F10.opLoft","SWEPT_FACE",FACE,{"disambiguationData":[OSD([sQuery(id+"F3.wireOp",EDGE,"E20.11.0"),subQ51,subQ50,sQuery(id+"F4.wireOp",EDGE,"E26.11.0"),subQ49,subQ48])]})])],"derivedFrom":subQ9})])]}),makeQuery(id+"F47.opFillet","BLEND_FACE",FACE,{"disambiguationData":[OSD([subQ5,subQ7]),TDD([makeQuery(id+"F42.boolean.opBoolean","COPY",EDGE,{"disambiguationData":[TD([makeQuery(id+"F11.opLoft","SWEPT_FACE",FACE,{"disambiguationData":[OSD([sQuery(id+"F3.wireOp",EDGE,"E20.10.0"),subQ47,subQ46,sQuery(id+"F4.wireOp",EDGE,"E26.10.0"),subQ45,subQ44])]})])],"derivedFrom":subQ9})])]}),makeQuery(id+"F47.opFillet","BLEND_FACE",FACE,{"disambiguationData":[OSD([subQ5,subQ7]),TDD([makeQuery(id+"F42.boolean.opBoolean","COPY",EDGE,{"disambiguationData":[TD([makeQuery(id+"F12.opLoft","SWEPT_FACE",FACE,{"disambiguationData":[OSD([sQuery(id+"F3.wireOp",EDGE,"E20.9.0"),subQ43,subQ42,sQuery(id+"F4.wireOp",EDGE,"E26.9.0"),subQ41,subQ40])]})])],"derivedFrom":subQ9})])]}),makeQuery(id+"F47.opFillet","BLEND_FACE",FACE,{"disambiguationData":[OSD([subQ5,subQ7]),TDD([makeQuery(id+"F42.boolean.opBoolean","COPY",EDGE,{"disambiguationData":[TD([makeQuery(id+"F13.opLoft","SWEPT_FACE",FACE,{"disambiguationData":[OSD([sQuery(id+"F3.wireOp",EDGE,"E20.8.0"),subQ39,subQ38,sQuery(id+"F4.wireOp",EDGE,"E26.8.0"),subQ37,subQ36])]})])],"derivedFrom":subQ9})])]}),makeQuery(id+"F47.opFillet","BLEND_FACE",FACE,{"disambiguationData":[OSD([subQ5,subQ7]),TDD([makeQuery(id+"F42.boolean.opBoolean","COPY",EDGE,{"disambiguationData":[TD([makeQuery(id+"F14.opLoft","SWEPT_FACE",FACE,{"disambiguationData":[OSD([sQuery(id+"F3.wireOp",EDGE,"E20.7.0"),subQ35,subQ34,sQuery(id+"F4.wireOp",EDGE,"E26.7.0"),subQ33,subQ32])]})])],"derivedFrom":subQ9})])]}),makeQuery(id+"F47.opFillet","BLEND_FACE",FACE,{"disambiguationData":[OSD([subQ5,subQ7]),TDD([makeQuery(id+"F42.boolean.opBoolean","COPY",EDGE,{"disambiguationData":[TD([makeQuery(id+"F15.opLoft","SWEPT_FACE",FACE,{"disambiguationData":[OSD([sQuery(id+"F3.wireOp",EDGE,"E20.6.0"),subQ31,subQ30,sQuery(id+"F4.wireOp",EDGE,"E26.6.0"),subQ29,subQ28])]})])],"derivedFrom":subQ9})])]}),makeQuery(id+"F47.opFillet","BLEND_FACE",FACE,{"disambiguationData":[OSD([subQ5,subQ7]),TDD([makeQuery(id+"F42.boolean.opBoolean","COPY",EDGE,{"disambiguationData":[TD([makeQuery(id+"F16.opLoft","SWEPT_FACE",FACE,{"disambiguationData":[OSD([sQuery(id+"F3.wireOp",EDGE,"E20.5.0"),subQ27,subQ26,sQuery(id+"F4.wireOp",EDGE,"E26.5.0"),subQ25,subQ24])]})])],"derivedFrom":subQ9})])]}),makeQuery(id+"F47.opFillet","BLEND_FACE",FACE,{"disambiguationData":[OSD([subQ5,subQ7]),TDD([makeQuery(id+"F42.boolean.opBoolean","COPY",EDGE,{"disambiguationData":[TD([makeQuery(id+"F17.opLoft","SWEPT_FACE",FACE,{"disambiguationData":[OSD([sQuery(id+"F3.wireOp",EDGE,"E20.4.0"),subQ23,subQ22,sQuery(id+"F4.wireOp",EDGE,"E26.4.0"),subQ21,subQ20])]})])],"derivedFrom":subQ9})])]}),makeQuery(id+"F47.opFillet","BLEND_FACE",FACE,{"disambiguationData":[OSD([subQ5,subQ7]),TDD([makeQuery(id+"F42.boolean.opBoolean","COPY",EDGE,{"disambiguationData":[TD([makeQuery(id+"F18.opLoft","SWEPT_FACE",FACE,{"disambiguationData":[OSD([sQuery(id+"F3.wireOp",EDGE,"E20.3.0"),subQ19,subQ18,sQuery(id+"F4.wireOp",EDGE,"E26.3.0"),subQ17,subQ16])]})])],"derivedFrom":subQ9})])]}),makeQuery(id+"F47.opFillet","BLEND_FACE",FACE,{"disambiguationData":[OSD([subQ5,subQ7]),TDD([makeQuery(id+"F42.boolean.opBoolean","COPY",EDGE,{"disambiguationData":[TD([subQ15])],"derivedFrom":subQ9})])]}),makeQuery(id+"F47.opFillet","BLEND_FACE",FACE,{"disambiguationData":[OSD([subQ5,subQ7]),TDD([makeQuery(id+"F42.boolean.opBoolean","COPY",EDGE,{"disambiguationData":[TD([makeQuery(id+"F20.opLoft","SWEPT_FACE",FACE,{"disambiguationData":[OSD([sQuery(id+"F3.wireOp",EDGE,"E20.1.0"),subQ4,subQ3,sQuery(id+"F4.wireOp",EDGE,"E26.1.0"),subQ2,subQ1])]})])],"derivedFrom":subQ9})])]})]});}
            var Q53;
            {var subQ0=makeQuery(id+"F40.opExtrude","CAP_FACE",FACE,{"disambiguationData":[OSD([sQuery(id+"F39.wireOp",EDGE,"E29"),sQuery(id+"F39.wireOp",EDGE,"E30")])],"isStart":false});var subQ1=sQuery(id+"F4.wireOp",EDGE,"E26.1.3");var subQ2=sQuery(id+"F4.wireOp",EDGE,"E26.1.2");var subQ3=sQuery(id+"F3.wireOp",EDGE,"E20.1.3");var subQ4=sQuery(id+"F3.wireOp",EDGE,"E20.1.1");var subQ6=sQuery(id+"F41.wireOp",EDGE,"E35");var subQ7=makeQuery(id+"F42.opRevolve","SWEPT_FACE",FACE,{"disambiguationData":[OSD([subQ6])]});var subQ8=makeQuery(id+"F20.opLoft","SWEPT_FACE",FACE,{"disambiguationData":[OSD([sQuery(id+"F3.wireOp",EDGE,"E20.1.0"),subQ4,subQ3,sQuery(id+"F4.wireOp",EDGE,"E26.1.0"),subQ2,subQ1])]});var subQ9=sQuery(id+"F41.wireOp",EDGE,"E36");var subQ10=makeQuery(id+"F42.opRevolve","SWEPT_FACE",FACE,{"disambiguationData":[OSD([subQ9])]});var subQ11=makeQuery(id+"F42.opRevolve","SWEPT_EDGE",EDGE,{"disambiguationData":[OSD([subQ6,subQ9])]});var subQ12=sQuery(id+"F4.wireOp",EDGE,"E26.2.3");var subQ13=sQuery(id+"F4.wireOp",EDGE,"E26.2.2");var subQ14=sQuery(id+"F3.wireOp",EDGE,"E20.2.3");var subQ15=sQuery(id+"F3.wireOp",EDGE,"E20.2.1");var subQ16=sQuery(id+"F4.wireOp",EDGE,"E26.3.3");var subQ17=sQuery(id+"F4.wireOp",EDGE,"E26.3.2");var subQ18=sQuery(id+"F3.wireOp",EDGE,"E20.3.3");var subQ19=sQuery(id+"F3.wireOp",EDGE,"E20.3.1");var subQ20=sQuery(id+"F4.wireOp",EDGE,"E26.4.3");var subQ21=sQuery(id+"F4.wireOp",EDGE,"E26.4.2");var subQ22=sQuery(id+"F3.wireOp",EDGE,"E20.4.3");var subQ23=sQuery(id+"F3.wireOp",EDGE,"E20.4.1");var subQ24=sQuery(id+"F4.wireOp",EDGE,"E26.5.3");var subQ25=sQuery(id+"F4.wireOp",EDGE,"E26.5.2");var subQ26=sQuery(id+"F3.wireOp",EDGE,"E20.5.3");var subQ27=sQuery(id+"F3.wireOp",EDGE,"E20.5.1");var subQ28=sQuery(id+"F4.wireOp",EDGE,"E26.6.3");var subQ29=sQuery(id+"F4.wireOp",EDGE,"E26.6.2");var subQ30=sQuery(id+"F3.wireOp",EDGE,"E20.6.3");var subQ31=sQuery(id+"F3.wireOp",EDGE,"E20.6.1");var subQ32=sQuery(id+"F4.wireOp",EDGE,"E26.7.3");var subQ33=sQuery(id+"F4.wireOp",EDGE,"E26.7.2");var subQ34=sQuery(id+"F3.wireOp",EDGE,"E20.7.3");var subQ35=sQuery(id+"F3.wireOp",EDGE,"E20.7.1");var subQ36=sQuery(id+"F4.wireOp",EDGE,"E26.8.3");var subQ37=sQuery(id+"F4.wireOp",EDGE,"E26.8.2");var subQ38=sQuery(id+"F3.wireOp",EDGE,"E20.8.3");var subQ39=sQuery(id+"F3.wireOp",EDGE,"E20.8.1");var subQ40=sQuery(id+"F4.wireOp",EDGE,"E26.9.3");var subQ41=sQuery(id+"F4.wireOp",EDGE,"E26.9.2");var subQ42=sQuery(id+"F3.wireOp",EDGE,"E20.9.3");var subQ43=sQuery(id+"F3.wireOp",EDGE,"E20.9.1");var subQ44=sQuery(id+"F4.wireOp",EDGE,"E26.10.3");var subQ45=sQuery(id+"F4.wireOp",EDGE,"E26.10.2");var subQ46=sQuery(id+"F3.wireOp",EDGE,"E20.10.3");var subQ47=sQuery(id+"F3.wireOp",EDGE,"E20.10.1");var subQ48=sQuery(id+"F4.wireOp",EDGE,"E26.11.3");var subQ49=sQuery(id+"F4.wireOp",EDGE,"E26.11.2");var subQ50=sQuery(id+"F3.wireOp",EDGE,"E20.11.3");var subQ51=sQuery(id+"F3.wireOp",EDGE,"E20.11.1");var subQ52=sQuery(id+"F4.wireOp",EDGE,"E26.12.3");var subQ53=sQuery(id+"F4.wireOp",EDGE,"E26.12.2");var subQ54=sQuery(id+"F3.wireOp",EDGE,"E20.12.3");var subQ55=sQuery(id+"F3.wireOp",EDGE,"E20.12.1");var subQ56=sQuery(id+"F4.wireOp",EDGE,"E26.13.3");var subQ57=sQuery(id+"F4.wireOp",EDGE,"E26.13.2");var subQ58=sQuery(id+"F3.wireOp",EDGE,"E20.13.3");var subQ59=sQuery(id+"F3.wireOp",EDGE,"E20.13.1");var subQ60=sQuery(id+"F4.wireOp",EDGE,"E26.14.3");var subQ61=sQuery(id+"F4.wireOp",EDGE,"E26.14.2");var subQ62=sQuery(id+"F3.wireOp",EDGE,"E20.14.3");var subQ63=sQuery(id+"F3.wireOp",EDGE,"E20.14.1");var subQ64=sQuery(id+"F4.wireOp",EDGE,"E26.15.3");var subQ65=sQuery(id+"F4.wireOp",EDGE,"E26.15.2");var subQ66=sQuery(id+"F3.wireOp",EDGE,"E20.15.3");var subQ67=sQuery(id+"F3.wireOp",EDGE,"E20.15.1");var subQ68=sQuery(id+"F4.wireOp",EDGE,"E23");var subQ69=sQuery(id+"F4.wireOp",EDGE,"E22");var subQ70=sQuery(id+"F3.wireOp",EDGE,"E18.top");var subQ71=sQuery(id+"F3.wireOp",EDGE,"E18.bottom");var subQ74=makeQuery(id+"F42.boolean.opBoolean","COPY",FACE,{"disambiguationData":[TD([subQ8])],"derivedFrom":subQ7});var subQ75=makeQuery(id+"F20.boolean.opBoolean","INTERSECT",EDGE,{"derivedFrom":[makeQuery(id+"F1.opRevolve","SWEPT_FACE",FACE,{"disambiguationData":[OSD([sQuery(id+"F0.wireOp",EDGE,"E4")])]}),subQ8]});Q53=makeQuery(id+"F48.opFillet","BLEND_EDGE",EDGE,{"blendedFrom":[makeQuery(id+"F47.opFillet","TWEAK_EDGE",EDGE,{"derivedFrom":[makeQuery(id+"F45.opFillet","BLEND_VERTEX",VERTEX,{"blendedFrom":[subQ75,subQ8,subQ74],"blendedInto":[subQ8,subQ74]}),makeQuery(id+"F45.opFillet","BLEND_VERTEX",VERTEX,{"blendedFrom":[subQ75,makeQuery(id+"F42.boolean.opBoolean","MERGE",FACE,{"derivedFrom":[subQ0,subQ10]}),subQ74],"blendedInto":[makeQuery(id+"F42.boolean.opBoolean","MERGE",FACE,{"derivedFrom":[subQ0,subQ10]}),subQ74]})]}),makeQuery(id+"F47.opFillet","BLEND_FACE",FACE,{"disambiguationData":[OSD([subQ6,subQ9]),TDD([makeQuery(id+"F42.boolean.opBoolean","COPY",EDGE,{"disambiguationData":[TD([makeQuery(id+"F5.opLoft","SWEPT_FACE",FACE,{"disambiguationData":[OSD([subQ71,subQ70,sQuery(id+"F3.wireOp",EDGE,"E18.left"),sQuery(id+"F4.wireOp",EDGE,"E21"),subQ69,subQ68])]})])],"derivedFrom":subQ11})])]}),makeQuery(id+"F47.opFillet","BLEND_FACE",FACE,{"disambiguationData":[OSD([subQ6,subQ9]),TDD([makeQuery(id+"F42.boolean.opBoolean","COPY",EDGE,{"disambiguationData":[TD([makeQuery(id+"F6.opLoft","SWEPT_FACE",FACE,{"disambiguationData":[OSD([sQuery(id+"F3.wireOp",EDGE,"E20.15.0"),subQ67,subQ66,sQuery(id+"F4.wireOp",EDGE,"E26.15.0"),subQ65,subQ64])]})])],"derivedFrom":subQ11})])]}),makeQuery(id+"F47.opFillet","BLEND_FACE",FACE,{"disambiguationData":[OSD([subQ6,subQ9]),TDD([makeQuery(id+"F42.boolean.opBoolean","COPY",EDGE,{"disambiguationData":[TD([makeQuery(id+"F7.opLoft","SWEPT_FACE",FACE,{"disambiguationData":[OSD([sQuery(id+"F3.wireOp",EDGE,"E20.14.0"),subQ63,subQ62,sQuery(id+"F4.wireOp",EDGE,"E26.14.0"),subQ61,subQ60])]})])],"derivedFrom":subQ11})])]}),makeQuery(id+"F47.opFillet","BLEND_FACE",FACE,{"disambiguationData":[OSD([subQ6,subQ9]),TDD([makeQuery(id+"F42.boolean.opBoolean","COPY",EDGE,{"disambiguationData":[TD([makeQuery(id+"F8.opLoft","SWEPT_FACE",FACE,{"disambiguationData":[OSD([sQuery(id+"F3.wireOp",EDGE,"E20.13.0"),subQ59,subQ58,sQuery(id+"F4.wireOp",EDGE,"E26.13.0"),subQ57,subQ56])]})])],"derivedFrom":subQ11})])]}),makeQuery(id+"F47.opFillet","BLEND_FACE",FACE,{"disambiguationData":[OSD([subQ6,subQ9]),TDD([makeQuery(id+"F42.boolean.opBoolean","COPY",EDGE,{"disambiguationData":[TD([makeQuery(id+"F9.opLoft","SWEPT_FACE",FACE,{"disambiguationData":[OSD([sQuery(id+"F3.wireOp",EDGE,"E20.12.0"),subQ55,subQ54,sQuery(id+"F4.wireOp",EDGE,"E26.12.0"),subQ53,subQ52])]})])],"derivedFrom":subQ11})])]}),makeQuery(id+"F47.opFillet","BLEND_FACE",FACE,{"disambiguationData":[OSD([subQ6,subQ9]),TDD([makeQuery(id+"F42.boolean.opBoolean","COPY",EDGE,{"disambiguationData":[TD([makeQuery(id+"F10.opLoft","SWEPT_FACE",FACE,{"disambiguationData":[OSD([sQuery(id+"F3.wireOp",EDGE,"E20.11.0"),subQ51,subQ50,sQuery(id+"F4.wireOp",EDGE,"E26.11.0"),subQ49,subQ48])]})])],"derivedFrom":subQ11})])]}),makeQuery(id+"F47.opFillet","BLEND_FACE",FACE,{"disambiguationData":[OSD([subQ6,subQ9]),TDD([makeQuery(id+"F42.boolean.opBoolean","COPY",EDGE,{"disambiguationData":[TD([makeQuery(id+"F11.opLoft","SWEPT_FACE",FACE,{"disambiguationData":[OSD([sQuery(id+"F3.wireOp",EDGE,"E20.10.0"),subQ47,subQ46,sQuery(id+"F4.wireOp",EDGE,"E26.10.0"),subQ45,subQ44])]})])],"derivedFrom":subQ11})])]}),makeQuery(id+"F47.opFillet","BLEND_FACE",FACE,{"disambiguationData":[OSD([subQ6,subQ9]),TDD([makeQuery(id+"F42.boolean.opBoolean","COPY",EDGE,{"disambiguationData":[TD([makeQuery(id+"F12.opLoft","SWEPT_FACE",FACE,{"disambiguationData":[OSD([sQuery(id+"F3.wireOp",EDGE,"E20.9.0"),subQ43,subQ42,sQuery(id+"F4.wireOp",EDGE,"E26.9.0"),subQ41,subQ40])]})])],"derivedFrom":subQ11})])]}),makeQuery(id+"F47.opFillet","BLEND_FACE",FACE,{"disambiguationData":[OSD([subQ6,subQ9]),TDD([makeQuery(id+"F42.boolean.opBoolean","COPY",EDGE,{"disambiguationData":[TD([makeQuery(id+"F13.opLoft","SWEPT_FACE",FACE,{"disambiguationData":[OSD([sQuery(id+"F3.wireOp",EDGE,"E20.8.0"),subQ39,subQ38,sQuery(id+"F4.wireOp",EDGE,"E26.8.0"),subQ37,subQ36])]})])],"derivedFrom":subQ11})])]}),makeQuery(id+"F47.opFillet","BLEND_FACE",FACE,{"disambiguationData":[OSD([subQ6,subQ9]),TDD([makeQuery(id+"F42.boolean.opBoolean","COPY",EDGE,{"disambiguationData":[TD([makeQuery(id+"F14.opLoft","SWEPT_FACE",FACE,{"disambiguationData":[OSD([sQuery(id+"F3.wireOp",EDGE,"E20.7.0"),subQ35,subQ34,sQuery(id+"F4.wireOp",EDGE,"E26.7.0"),subQ33,subQ32])]})])],"derivedFrom":subQ11})])]}),makeQuery(id+"F47.opFillet","BLEND_FACE",FACE,{"disambiguationData":[OSD([subQ6,subQ9]),TDD([makeQuery(id+"F42.boolean.opBoolean","COPY",EDGE,{"disambiguationData":[TD([makeQuery(id+"F15.opLoft","SWEPT_FACE",FACE,{"disambiguationData":[OSD([sQuery(id+"F3.wireOp",EDGE,"E20.6.0"),subQ31,subQ30,sQuery(id+"F4.wireOp",EDGE,"E26.6.0"),subQ29,subQ28])]})])],"derivedFrom":subQ11})])]}),makeQuery(id+"F47.opFillet","BLEND_FACE",FACE,{"disambiguationData":[OSD([subQ6,subQ9]),TDD([makeQuery(id+"F42.boolean.opBoolean","COPY",EDGE,{"disambiguationData":[TD([makeQuery(id+"F16.opLoft","SWEPT_FACE",FACE,{"disambiguationData":[OSD([sQuery(id+"F3.wireOp",EDGE,"E20.5.0"),subQ27,subQ26,sQuery(id+"F4.wireOp",EDGE,"E26.5.0"),subQ25,subQ24])]})])],"derivedFrom":subQ11})])]}),makeQuery(id+"F47.opFillet","BLEND_FACE",FACE,{"disambiguationData":[OSD([subQ6,subQ9]),TDD([makeQuery(id+"F42.boolean.opBoolean","COPY",EDGE,{"disambiguationData":[TD([makeQuery(id+"F17.opLoft","SWEPT_FACE",FACE,{"disambiguationData":[OSD([sQuery(id+"F3.wireOp",EDGE,"E20.4.0"),subQ23,subQ22,sQuery(id+"F4.wireOp",EDGE,"E26.4.0"),subQ21,subQ20])]})])],"derivedFrom":subQ11})])]}),makeQuery(id+"F47.opFillet","BLEND_FACE",FACE,{"disambiguationData":[OSD([subQ6,subQ9]),TDD([makeQuery(id+"F42.boolean.opBoolean","COPY",EDGE,{"disambiguationData":[TD([makeQuery(id+"F18.opLoft","SWEPT_FACE",FACE,{"disambiguationData":[OSD([sQuery(id+"F3.wireOp",EDGE,"E20.3.0"),subQ19,subQ18,sQuery(id+"F4.wireOp",EDGE,"E26.3.0"),subQ17,subQ16])]})])],"derivedFrom":subQ11})])]}),makeQuery(id+"F47.opFillet","BLEND_FACE",FACE,{"disambiguationData":[OSD([subQ6,subQ9]),TDD([makeQuery(id+"F42.boolean.opBoolean","COPY",EDGE,{"disambiguationData":[TD([makeQuery(id+"F19.opLoft","SWEPT_FACE",FACE,{"disambiguationData":[OSD([sQuery(id+"F3.wireOp",EDGE,"E20.2.0"),subQ15,subQ14,sQuery(id+"F4.wireOp",EDGE,"E26.2.0"),subQ13,subQ12])]})])],"derivedFrom":subQ11})])]}),makeQuery(id+"F47.opFillet","BLEND_FACE",FACE,{"disambiguationData":[OSD([subQ6,subQ9]),TDD([makeQuery(id+"F42.boolean.opBoolean","COPY",EDGE,{"disambiguationData":[TD([subQ8])],"derivedFrom":subQ11})])]})],"blendedInto":[makeQuery(id+"F47.opFillet","BLEND_FACE",FACE,{"disambiguationData":[OSD([subQ6,subQ9]),TDD([makeQuery(id+"F42.boolean.opBoolean","COPY",EDGE,{"disambiguationData":[TD([makeQuery(id+"F5.opLoft","SWEPT_FACE",FACE,{"disambiguationData":[OSD([subQ71,subQ70,sQuery(id+"F3.wireOp",EDGE,"E18.left"),sQuery(id+"F4.wireOp",EDGE,"E21"),subQ69,subQ68])]})])],"derivedFrom":subQ11})])]}),makeQuery(id+"F47.opFillet","BLEND_FACE",FACE,{"disambiguationData":[OSD([subQ6,subQ9]),TDD([makeQuery(id+"F42.boolean.opBoolean","COPY",EDGE,{"disambiguationData":[TD([makeQuery(id+"F6.opLoft","SWEPT_FACE",FACE,{"disambiguationData":[OSD([sQuery(id+"F3.wireOp",EDGE,"E20.15.0"),subQ67,subQ66,sQuery(id+"F4.wireOp",EDGE,"E26.15.0"),subQ65,subQ64])]})])],"derivedFrom":subQ11})])]}),makeQuery(id+"F47.opFillet","BLEND_FACE",FACE,{"disambiguationData":[OSD([subQ6,subQ9]),TDD([makeQuery(id+"F42.boolean.opBoolean","COPY",EDGE,{"disambiguationData":[TD([makeQuery(id+"F7.opLoft","SWEPT_FACE",FACE,{"disambiguationData":[OSD([sQuery(id+"F3.wireOp",EDGE,"E20.14.0"),subQ63,subQ62,sQuery(id+"F4.wireOp",EDGE,"E26.14.0"),subQ61,subQ60])]})])],"derivedFrom":subQ11})])]}),makeQuery(id+"F47.opFillet","BLEND_FACE",FACE,{"disambiguationData":[OSD([subQ6,subQ9]),TDD([makeQuery(id+"F42.boolean.opBoolean","COPY",EDGE,{"disambiguationData":[TD([makeQuery(id+"F8.opLoft","SWEPT_FACE",FACE,{"disambiguationData":[OSD([sQuery(id+"F3.wireOp",EDGE,"E20.13.0"),subQ59,subQ58,sQuery(id+"F4.wireOp",EDGE,"E26.13.0"),subQ57,subQ56])]})])],"derivedFrom":subQ11})])]}),makeQuery(id+"F47.opFillet","BLEND_FACE",FACE,{"disambiguationData":[OSD([subQ6,subQ9]),TDD([makeQuery(id+"F42.boolean.opBoolean","COPY",EDGE,{"disambiguationData":[TD([makeQuery(id+"F9.opLoft","SWEPT_FACE",FACE,{"disambiguationData":[OSD([sQuery(id+"F3.wireOp",EDGE,"E20.12.0"),subQ55,subQ54,sQuery(id+"F4.wireOp",EDGE,"E26.12.0"),subQ53,subQ52])]})])],"derivedFrom":subQ11})])]}),makeQuery(id+"F47.opFillet","BLEND_FACE",FACE,{"disambiguationData":[OSD([subQ6,subQ9]),TDD([makeQuery(id+"F42.boolean.opBoolean","COPY",EDGE,{"disambiguationData":[TD([makeQuery(id+"F10.opLoft","SWEPT_FACE",FACE,{"disambiguationData":[OSD([sQuery(id+"F3.wireOp",EDGE,"E20.11.0"),subQ51,subQ50,sQuery(id+"F4.wireOp",EDGE,"E26.11.0"),subQ49,subQ48])]})])],"derivedFrom":subQ11})])]}),makeQuery(id+"F47.opFillet","BLEND_FACE",FACE,{"disambiguationData":[OSD([subQ6,subQ9]),TDD([makeQuery(id+"F42.boolean.opBoolean","COPY",EDGE,{"disambiguationData":[TD([makeQuery(id+"F11.opLoft","SWEPT_FACE",FACE,{"disambiguationData":[OSD([sQuery(id+"F3.wireOp",EDGE,"E20.10.0"),subQ47,subQ46,sQuery(id+"F4.wireOp",EDGE,"E26.10.0"),subQ45,subQ44])]})])],"derivedFrom":subQ11})])]}),makeQuery(id+"F47.opFillet","BLEND_FACE",FACE,{"disambiguationData":[OSD([subQ6,subQ9]),TDD([makeQuery(id+"F42.boolean.opBoolean","COPY",EDGE,{"disambiguationData":[TD([makeQuery(id+"F12.opLoft","SWEPT_FACE",FACE,{"disambiguationData":[OSD([sQuery(id+"F3.wireOp",EDGE,"E20.9.0"),subQ43,subQ42,sQuery(id+"F4.wireOp",EDGE,"E26.9.0"),subQ41,subQ40])]})])],"derivedFrom":subQ11})])]}),makeQuery(id+"F47.opFillet","BLEND_FACE",FACE,{"disambiguationData":[OSD([subQ6,subQ9]),TDD([makeQuery(id+"F42.boolean.opBoolean","COPY",EDGE,{"disambiguationData":[TD([makeQuery(id+"F13.opLoft","SWEPT_FACE",FACE,{"disambiguationData":[OSD([sQuery(id+"F3.wireOp",EDGE,"E20.8.0"),subQ39,subQ38,sQuery(id+"F4.wireOp",EDGE,"E26.8.0"),subQ37,subQ36])]})])],"derivedFrom":subQ11})])]}),makeQuery(id+"F47.opFillet","BLEND_FACE",FACE,{"disambiguationData":[OSD([subQ6,subQ9]),TDD([makeQuery(id+"F42.boolean.opBoolean","COPY",EDGE,{"disambiguationData":[TD([makeQuery(id+"F14.opLoft","SWEPT_FACE",FACE,{"disambiguationData":[OSD([sQuery(id+"F3.wireOp",EDGE,"E20.7.0"),subQ35,subQ34,sQuery(id+"F4.wireOp",EDGE,"E26.7.0"),subQ33,subQ32])]})])],"derivedFrom":subQ11})])]}),makeQuery(id+"F47.opFillet","BLEND_FACE",FACE,{"disambiguationData":[OSD([subQ6,subQ9]),TDD([makeQuery(id+"F42.boolean.opBoolean","COPY",EDGE,{"disambiguationData":[TD([makeQuery(id+"F15.opLoft","SWEPT_FACE",FACE,{"disambiguationData":[OSD([sQuery(id+"F3.wireOp",EDGE,"E20.6.0"),subQ31,subQ30,sQuery(id+"F4.wireOp",EDGE,"E26.6.0"),subQ29,subQ28])]})])],"derivedFrom":subQ11})])]}),makeQuery(id+"F47.opFillet","BLEND_FACE",FACE,{"disambiguationData":[OSD([subQ6,subQ9]),TDD([makeQuery(id+"F42.boolean.opBoolean","COPY",EDGE,{"disambiguationData":[TD([makeQuery(id+"F16.opLoft","SWEPT_FACE",FACE,{"disambiguationData":[OSD([sQuery(id+"F3.wireOp",EDGE,"E20.5.0"),subQ27,subQ26,sQuery(id+"F4.wireOp",EDGE,"E26.5.0"),subQ25,subQ24])]})])],"derivedFrom":subQ11})])]}),makeQuery(id+"F47.opFillet","BLEND_FACE",FACE,{"disambiguationData":[OSD([subQ6,subQ9]),TDD([makeQuery(id+"F42.boolean.opBoolean","COPY",EDGE,{"disambiguationData":[TD([makeQuery(id+"F17.opLoft","SWEPT_FACE",FACE,{"disambiguationData":[OSD([sQuery(id+"F3.wireOp",EDGE,"E20.4.0"),subQ23,subQ22,sQuery(id+"F4.wireOp",EDGE,"E26.4.0"),subQ21,subQ20])]})])],"derivedFrom":subQ11})])]}),makeQuery(id+"F47.opFillet","BLEND_FACE",FACE,{"disambiguationData":[OSD([subQ6,subQ9]),TDD([makeQuery(id+"F42.boolean.opBoolean","COPY",EDGE,{"disambiguationData":[TD([makeQuery(id+"F18.opLoft","SWEPT_FACE",FACE,{"disambiguationData":[OSD([sQuery(id+"F3.wireOp",EDGE,"E20.3.0"),subQ19,subQ18,sQuery(id+"F4.wireOp",EDGE,"E26.3.0"),subQ17,subQ16])]})])],"derivedFrom":subQ11})])]}),makeQuery(id+"F47.opFillet","BLEND_FACE",FACE,{"disambiguationData":[OSD([subQ6,subQ9]),TDD([makeQuery(id+"F42.boolean.opBoolean","COPY",EDGE,{"disambiguationData":[TD([makeQuery(id+"F19.opLoft","SWEPT_FACE",FACE,{"disambiguationData":[OSD([sQuery(id+"F3.wireOp",EDGE,"E20.2.0"),subQ15,subQ14,sQuery(id+"F4.wireOp",EDGE,"E26.2.0"),subQ13,subQ12])]})])],"derivedFrom":subQ11})])]}),makeQuery(id+"F47.opFillet","BLEND_FACE",FACE,{"disambiguationData":[OSD([subQ6,subQ9]),TDD([makeQuery(id+"F42.boolean.opBoolean","COPY",EDGE,{"disambiguationData":[TD([subQ8])],"derivedFrom":subQ11})])]})]});}
            var Q54;
            {var subQ0=makeQuery(id+"F40.opExtrude","CAP_FACE",FACE,{"disambiguationData":[OSD([sQuery(id+"F39.wireOp",EDGE,"E29"),sQuery(id+"F39.wireOp",EDGE,"E30")])],"isStart":false});var subQ1=sQuery(id+"F4.wireOp",EDGE,"E26.1.3");var subQ2=sQuery(id+"F4.wireOp",EDGE,"E26.1.2");var subQ3=sQuery(id+"F3.wireOp",EDGE,"E20.1.3");var subQ4=sQuery(id+"F3.wireOp",EDGE,"E20.1.1");var subQ5=sQuery(id+"F41.wireOp",EDGE,"E35");var subQ6=makeQuery(id+"F42.opRevolve","SWEPT_FACE",FACE,{"disambiguationData":[OSD([subQ5])]});var subQ7=sQuery(id+"F41.wireOp",EDGE,"E36");var subQ8=makeQuery(id+"F42.opRevolve","SWEPT_FACE",FACE,{"disambiguationData":[OSD([subQ7])]});var subQ9=makeQuery(id+"F42.opRevolve","SWEPT_EDGE",EDGE,{"disambiguationData":[OSD([subQ5,subQ7])]});var subQ10=sQuery(id+"F4.wireOp",EDGE,"E26.2.3");var subQ11=sQuery(id+"F4.wireOp",EDGE,"E26.2.2");var subQ12=sQuery(id+"F3.wireOp",EDGE,"E20.2.3");var subQ13=sQuery(id+"F3.wireOp",EDGE,"E20.2.1");var subQ14=sQuery(id+"F4.wireOp",EDGE,"E26.3.3");var subQ15=sQuery(id+"F4.wireOp",EDGE,"E26.3.2");var subQ16=sQuery(id+"F3.wireOp",EDGE,"E20.3.3");var subQ17=sQuery(id+"F3.wireOp",EDGE,"E20.3.1");var subQ18=sQuery(id+"F4.wireOp",EDGE,"E26.4.3");var subQ19=sQuery(id+"F4.wireOp",EDGE,"E26.4.2");var subQ20=sQuery(id+"F3.wireOp",EDGE,"E20.4.3");var subQ21=sQuery(id+"F3.wireOp",EDGE,"E20.4.1");var subQ22=sQuery(id+"F4.wireOp",EDGE,"E26.5.3");var subQ23=sQuery(id+"F4.wireOp",EDGE,"E26.5.2");var subQ24=sQuery(id+"F3.wireOp",EDGE,"E20.5.3");var subQ25=sQuery(id+"F3.wireOp",EDGE,"E20.5.1");var subQ26=sQuery(id+"F4.wireOp",EDGE,"E26.6.3");var subQ27=sQuery(id+"F4.wireOp",EDGE,"E26.6.2");var subQ28=sQuery(id+"F3.wireOp",EDGE,"E20.6.3");var subQ29=sQuery(id+"F3.wireOp",EDGE,"E20.6.1");var subQ30=sQuery(id+"F4.wireOp",EDGE,"E26.7.3");var subQ31=sQuery(id+"F4.wireOp",EDGE,"E26.7.2");var subQ32=sQuery(id+"F3.wireOp",EDGE,"E20.7.3");var subQ33=sQuery(id+"F3.wireOp",EDGE,"E20.7.1");var subQ34=sQuery(id+"F4.wireOp",EDGE,"E26.8.3");var subQ35=sQuery(id+"F4.wireOp",EDGE,"E26.8.2");var subQ36=sQuery(id+"F3.wireOp",EDGE,"E20.8.3");var subQ37=sQuery(id+"F3.wireOp",EDGE,"E20.8.1");var subQ38=sQuery(id+"F4.wireOp",EDGE,"E26.9.3");var subQ39=sQuery(id+"F4.wireOp",EDGE,"E26.9.2");var subQ40=sQuery(id+"F3.wireOp",EDGE,"E20.9.3");var subQ41=sQuery(id+"F3.wireOp",EDGE,"E20.9.1");var subQ42=sQuery(id+"F4.wireOp",EDGE,"E26.10.3");var subQ43=sQuery(id+"F4.wireOp",EDGE,"E26.10.2");var subQ44=sQuery(id+"F3.wireOp",EDGE,"E20.10.3");var subQ45=sQuery(id+"F3.wireOp",EDGE,"E20.10.1");var subQ46=sQuery(id+"F4.wireOp",EDGE,"E26.11.3");var subQ47=sQuery(id+"F4.wireOp",EDGE,"E26.11.2");var subQ48=sQuery(id+"F3.wireOp",EDGE,"E20.11.3");var subQ49=sQuery(id+"F3.wireOp",EDGE,"E20.11.1");var subQ50=sQuery(id+"F4.wireOp",EDGE,"E26.12.3");var subQ51=sQuery(id+"F4.wireOp",EDGE,"E26.12.2");var subQ52=sQuery(id+"F3.wireOp",EDGE,"E20.12.3");var subQ53=sQuery(id+"F3.wireOp",EDGE,"E20.12.1");var subQ54=sQuery(id+"F4.wireOp",EDGE,"E26.13.3");var subQ55=sQuery(id+"F4.wireOp",EDGE,"E26.13.2");var subQ56=sQuery(id+"F3.wireOp",EDGE,"E20.13.3");var subQ57=sQuery(id+"F3.wireOp",EDGE,"E20.13.1");var subQ58=sQuery(id+"F4.wireOp",EDGE,"E26.14.3");var subQ59=sQuery(id+"F4.wireOp",EDGE,"E26.14.2");var subQ60=sQuery(id+"F3.wireOp",EDGE,"E20.14.3");var subQ61=sQuery(id+"F3.wireOp",EDGE,"E20.14.1");var subQ62=sQuery(id+"F4.wireOp",EDGE,"E26.15.3");var subQ63=sQuery(id+"F4.wireOp",EDGE,"E26.15.2");var subQ64=sQuery(id+"F3.wireOp",EDGE,"E20.15.3");var subQ65=sQuery(id+"F3.wireOp",EDGE,"E20.15.1");var subQ66=sQuery(id+"F4.wireOp",EDGE,"E23");var subQ67=sQuery(id+"F4.wireOp",EDGE,"E22");var subQ68=sQuery(id+"F3.wireOp",EDGE,"E18.top");var subQ69=sQuery(id+"F3.wireOp",EDGE,"E18.bottom");var subQ71=makeQuery(id+"F5.opLoft","SWEPT_FACE",FACE,{"disambiguationData":[OSD([subQ69,subQ68,sQuery(id+"F3.wireOp",EDGE,"E18.left"),sQuery(id+"F4.wireOp",EDGE,"E21"),subQ67,subQ66])]});var subQ74=makeQuery(id+"F42.boolean.opBoolean","COPY",FACE,{"disambiguationData":[TD([subQ71])],"derivedFrom":subQ6});var subQ75=makeQuery(id+"F5.boolean.opBoolean","INTERSECT",EDGE,{"derivedFrom":[makeQuery(id+"F1.opRevolve","SWEPT_FACE",FACE,{"disambiguationData":[OSD([sQuery(id+"F0.wireOp",EDGE,"E4")])]}),subQ71]});Q54=makeQuery(id+"F48.opFillet","BLEND_EDGE",EDGE,{"blendedFrom":[makeQuery(id+"F47.opFillet","TWEAK_EDGE",EDGE,{"derivedFrom":[makeQuery(id+"F45.opFillet","BLEND_VERTEX",VERTEX,{"blendedFrom":[subQ75,subQ71,subQ74],"blendedInto":[subQ71,subQ74]}),makeQuery(id+"F45.opFillet","BLEND_VERTEX",VERTEX,{"blendedFrom":[subQ75,makeQuery(id+"F42.boolean.opBoolean","MERGE",FACE,{"derivedFrom":[subQ0,subQ8]}),subQ74],"blendedInto":[makeQuery(id+"F42.boolean.opBoolean","MERGE",FACE,{"derivedFrom":[subQ0,subQ8]}),subQ74]})]}),makeQuery(id+"F47.opFillet","BLEND_FACE",FACE,{"disambiguationData":[OSD([subQ5,subQ7]),TDD([makeQuery(id+"F42.boolean.opBoolean","COPY",EDGE,{"disambiguationData":[TD([subQ71])],"derivedFrom":subQ9})])]}),makeQuery(id+"F47.opFillet","BLEND_FACE",FACE,{"disambiguationData":[OSD([subQ5,subQ7]),TDD([makeQuery(id+"F42.boolean.opBoolean","COPY",EDGE,{"disambiguationData":[TD([makeQuery(id+"F6.opLoft","SWEPT_FACE",FACE,{"disambiguationData":[OSD([sQuery(id+"F3.wireOp",EDGE,"E20.15.0"),subQ65,subQ64,sQuery(id+"F4.wireOp",EDGE,"E26.15.0"),subQ63,subQ62])]})])],"derivedFrom":subQ9})])]}),makeQuery(id+"F47.opFillet","BLEND_FACE",FACE,{"disambiguationData":[OSD([subQ5,subQ7]),TDD([makeQuery(id+"F42.boolean.opBoolean","COPY",EDGE,{"disambiguationData":[TD([makeQuery(id+"F7.opLoft","SWEPT_FACE",FACE,{"disambiguationData":[OSD([sQuery(id+"F3.wireOp",EDGE,"E20.14.0"),subQ61,subQ60,sQuery(id+"F4.wireOp",EDGE,"E26.14.0"),subQ59,subQ58])]})])],"derivedFrom":subQ9})])]}),makeQuery(id+"F47.opFillet","BLEND_FACE",FACE,{"disambiguationData":[OSD([subQ5,subQ7]),TDD([makeQuery(id+"F42.boolean.opBoolean","COPY",EDGE,{"disambiguationData":[TD([makeQuery(id+"F8.opLoft","SWEPT_FACE",FACE,{"disambiguationData":[OSD([sQuery(id+"F3.wireOp",EDGE,"E20.13.0"),subQ57,subQ56,sQuery(id+"F4.wireOp",EDGE,"E26.13.0"),subQ55,subQ54])]})])],"derivedFrom":subQ9})])]}),makeQuery(id+"F47.opFillet","BLEND_FACE",FACE,{"disambiguationData":[OSD([subQ5,subQ7]),TDD([makeQuery(id+"F42.boolean.opBoolean","COPY",EDGE,{"disambiguationData":[TD([makeQuery(id+"F9.opLoft","SWEPT_FACE",FACE,{"disambiguationData":[OSD([sQuery(id+"F3.wireOp",EDGE,"E20.12.0"),subQ53,subQ52,sQuery(id+"F4.wireOp",EDGE,"E26.12.0"),subQ51,subQ50])]})])],"derivedFrom":subQ9})])]}),makeQuery(id+"F47.opFillet","BLEND_FACE",FACE,{"disambiguationData":[OSD([subQ5,subQ7]),TDD([makeQuery(id+"F42.boolean.opBoolean","COPY",EDGE,{"disambiguationData":[TD([makeQuery(id+"F10.opLoft","SWEPT_FACE",FACE,{"disambiguationData":[OSD([sQuery(id+"F3.wireOp",EDGE,"E20.11.0"),subQ49,subQ48,sQuery(id+"F4.wireOp",EDGE,"E26.11.0"),subQ47,subQ46])]})])],"derivedFrom":subQ9})])]}),makeQuery(id+"F47.opFillet","BLEND_FACE",FACE,{"disambiguationData":[OSD([subQ5,subQ7]),TDD([makeQuery(id+"F42.boolean.opBoolean","COPY",EDGE,{"disambiguationData":[TD([makeQuery(id+"F11.opLoft","SWEPT_FACE",FACE,{"disambiguationData":[OSD([sQuery(id+"F3.wireOp",EDGE,"E20.10.0"),subQ45,subQ44,sQuery(id+"F4.wireOp",EDGE,"E26.10.0"),subQ43,subQ42])]})])],"derivedFrom":subQ9})])]}),makeQuery(id+"F47.opFillet","BLEND_FACE",FACE,{"disambiguationData":[OSD([subQ5,subQ7]),TDD([makeQuery(id+"F42.boolean.opBoolean","COPY",EDGE,{"disambiguationData":[TD([makeQuery(id+"F12.opLoft","SWEPT_FACE",FACE,{"disambiguationData":[OSD([sQuery(id+"F3.wireOp",EDGE,"E20.9.0"),subQ41,subQ40,sQuery(id+"F4.wireOp",EDGE,"E26.9.0"),subQ39,subQ38])]})])],"derivedFrom":subQ9})])]}),makeQuery(id+"F47.opFillet","BLEND_FACE",FACE,{"disambiguationData":[OSD([subQ5,subQ7]),TDD([makeQuery(id+"F42.boolean.opBoolean","COPY",EDGE,{"disambiguationData":[TD([makeQuery(id+"F13.opLoft","SWEPT_FACE",FACE,{"disambiguationData":[OSD([sQuery(id+"F3.wireOp",EDGE,"E20.8.0"),subQ37,subQ36,sQuery(id+"F4.wireOp",EDGE,"E26.8.0"),subQ35,subQ34])]})])],"derivedFrom":subQ9})])]}),makeQuery(id+"F47.opFillet","BLEND_FACE",FACE,{"disambiguationData":[OSD([subQ5,subQ7]),TDD([makeQuery(id+"F42.boolean.opBoolean","COPY",EDGE,{"disambiguationData":[TD([makeQuery(id+"F14.opLoft","SWEPT_FACE",FACE,{"disambiguationData":[OSD([sQuery(id+"F3.wireOp",EDGE,"E20.7.0"),subQ33,subQ32,sQuery(id+"F4.wireOp",EDGE,"E26.7.0"),subQ31,subQ30])]})])],"derivedFrom":subQ9})])]}),makeQuery(id+"F47.opFillet","BLEND_FACE",FACE,{"disambiguationData":[OSD([subQ5,subQ7]),TDD([makeQuery(id+"F42.boolean.opBoolean","COPY",EDGE,{"disambiguationData":[TD([makeQuery(id+"F15.opLoft","SWEPT_FACE",FACE,{"disambiguationData":[OSD([sQuery(id+"F3.wireOp",EDGE,"E20.6.0"),subQ29,subQ28,sQuery(id+"F4.wireOp",EDGE,"E26.6.0"),subQ27,subQ26])]})])],"derivedFrom":subQ9})])]}),makeQuery(id+"F47.opFillet","BLEND_FACE",FACE,{"disambiguationData":[OSD([subQ5,subQ7]),TDD([makeQuery(id+"F42.boolean.opBoolean","COPY",EDGE,{"disambiguationData":[TD([makeQuery(id+"F16.opLoft","SWEPT_FACE",FACE,{"disambiguationData":[OSD([sQuery(id+"F3.wireOp",EDGE,"E20.5.0"),subQ25,subQ24,sQuery(id+"F4.wireOp",EDGE,"E26.5.0"),subQ23,subQ22])]})])],"derivedFrom":subQ9})])]}),makeQuery(id+"F47.opFillet","BLEND_FACE",FACE,{"disambiguationData":[OSD([subQ5,subQ7]),TDD([makeQuery(id+"F42.boolean.opBoolean","COPY",EDGE,{"disambiguationData":[TD([makeQuery(id+"F17.opLoft","SWEPT_FACE",FACE,{"disambiguationData":[OSD([sQuery(id+"F3.wireOp",EDGE,"E20.4.0"),subQ21,subQ20,sQuery(id+"F4.wireOp",EDGE,"E26.4.0"),subQ19,subQ18])]})])],"derivedFrom":subQ9})])]}),makeQuery(id+"F47.opFillet","BLEND_FACE",FACE,{"disambiguationData":[OSD([subQ5,subQ7]),TDD([makeQuery(id+"F42.boolean.opBoolean","COPY",EDGE,{"disambiguationData":[TD([makeQuery(id+"F18.opLoft","SWEPT_FACE",FACE,{"disambiguationData":[OSD([sQuery(id+"F3.wireOp",EDGE,"E20.3.0"),subQ17,subQ16,sQuery(id+"F4.wireOp",EDGE,"E26.3.0"),subQ15,subQ14])]})])],"derivedFrom":subQ9})])]}),makeQuery(id+"F47.opFillet","BLEND_FACE",FACE,{"disambiguationData":[OSD([subQ5,subQ7]),TDD([makeQuery(id+"F42.boolean.opBoolean","COPY",EDGE,{"disambiguationData":[TD([makeQuery(id+"F19.opLoft","SWEPT_FACE",FACE,{"disambiguationData":[OSD([sQuery(id+"F3.wireOp",EDGE,"E20.2.0"),subQ13,subQ12,sQuery(id+"F4.wireOp",EDGE,"E26.2.0"),subQ11,subQ10])]})])],"derivedFrom":subQ9})])]}),makeQuery(id+"F47.opFillet","BLEND_FACE",FACE,{"disambiguationData":[OSD([subQ5,subQ7]),TDD([makeQuery(id+"F42.boolean.opBoolean","COPY",EDGE,{"disambiguationData":[TD([makeQuery(id+"F20.opLoft","SWEPT_FACE",FACE,{"disambiguationData":[OSD([sQuery(id+"F3.wireOp",EDGE,"E20.1.0"),subQ4,subQ3,sQuery(id+"F4.wireOp",EDGE,"E26.1.0"),subQ2,subQ1])]})])],"derivedFrom":subQ9})])]})],"blendedInto":[makeQuery(id+"F47.opFillet","BLEND_FACE",FACE,{"disambiguationData":[OSD([subQ5,subQ7]),TDD([makeQuery(id+"F42.boolean.opBoolean","COPY",EDGE,{"disambiguationData":[TD([subQ71])],"derivedFrom":subQ9})])]}),makeQuery(id+"F47.opFillet","BLEND_FACE",FACE,{"disambiguationData":[OSD([subQ5,subQ7]),TDD([makeQuery(id+"F42.boolean.opBoolean","COPY",EDGE,{"disambiguationData":[TD([makeQuery(id+"F6.opLoft","SWEPT_FACE",FACE,{"disambiguationData":[OSD([sQuery(id+"F3.wireOp",EDGE,"E20.15.0"),subQ65,subQ64,sQuery(id+"F4.wireOp",EDGE,"E26.15.0"),subQ63,subQ62])]})])],"derivedFrom":subQ9})])]}),makeQuery(id+"F47.opFillet","BLEND_FACE",FACE,{"disambiguationData":[OSD([subQ5,subQ7]),TDD([makeQuery(id+"F42.boolean.opBoolean","COPY",EDGE,{"disambiguationData":[TD([makeQuery(id+"F7.opLoft","SWEPT_FACE",FACE,{"disambiguationData":[OSD([sQuery(id+"F3.wireOp",EDGE,"E20.14.0"),subQ61,subQ60,sQuery(id+"F4.wireOp",EDGE,"E26.14.0"),subQ59,subQ58])]})])],"derivedFrom":subQ9})])]}),makeQuery(id+"F47.opFillet","BLEND_FACE",FACE,{"disambiguationData":[OSD([subQ5,subQ7]),TDD([makeQuery(id+"F42.boolean.opBoolean","COPY",EDGE,{"disambiguationData":[TD([makeQuery(id+"F8.opLoft","SWEPT_FACE",FACE,{"disambiguationData":[OSD([sQuery(id+"F3.wireOp",EDGE,"E20.13.0"),subQ57,subQ56,sQuery(id+"F4.wireOp",EDGE,"E26.13.0"),subQ55,subQ54])]})])],"derivedFrom":subQ9})])]}),makeQuery(id+"F47.opFillet","BLEND_FACE",FACE,{"disambiguationData":[OSD([subQ5,subQ7]),TDD([makeQuery(id+"F42.boolean.opBoolean","COPY",EDGE,{"disambiguationData":[TD([makeQuery(id+"F9.opLoft","SWEPT_FACE",FACE,{"disambiguationData":[OSD([sQuery(id+"F3.wireOp",EDGE,"E20.12.0"),subQ53,subQ52,sQuery(id+"F4.wireOp",EDGE,"E26.12.0"),subQ51,subQ50])]})])],"derivedFrom":subQ9})])]}),makeQuery(id+"F47.opFillet","BLEND_FACE",FACE,{"disambiguationData":[OSD([subQ5,subQ7]),TDD([makeQuery(id+"F42.boolean.opBoolean","COPY",EDGE,{"disambiguationData":[TD([makeQuery(id+"F10.opLoft","SWEPT_FACE",FACE,{"disambiguationData":[OSD([sQuery(id+"F3.wireOp",EDGE,"E20.11.0"),subQ49,subQ48,sQuery(id+"F4.wireOp",EDGE,"E26.11.0"),subQ47,subQ46])]})])],"derivedFrom":subQ9})])]}),makeQuery(id+"F47.opFillet","BLEND_FACE",FACE,{"disambiguationData":[OSD([subQ5,subQ7]),TDD([makeQuery(id+"F42.boolean.opBoolean","COPY",EDGE,{"disambiguationData":[TD([makeQuery(id+"F11.opLoft","SWEPT_FACE",FACE,{"disambiguationData":[OSD([sQuery(id+"F3.wireOp",EDGE,"E20.10.0"),subQ45,subQ44,sQuery(id+"F4.wireOp",EDGE,"E26.10.0"),subQ43,subQ42])]})])],"derivedFrom":subQ9})])]}),makeQuery(id+"F47.opFillet","BLEND_FACE",FACE,{"disambiguationData":[OSD([subQ5,subQ7]),TDD([makeQuery(id+"F42.boolean.opBoolean","COPY",EDGE,{"disambiguationData":[TD([makeQuery(id+"F12.opLoft","SWEPT_FACE",FACE,{"disambiguationData":[OSD([sQuery(id+"F3.wireOp",EDGE,"E20.9.0"),subQ41,subQ40,sQuery(id+"F4.wireOp",EDGE,"E26.9.0"),subQ39,subQ38])]})])],"derivedFrom":subQ9})])]}),makeQuery(id+"F47.opFillet","BLEND_FACE",FACE,{"disambiguationData":[OSD([subQ5,subQ7]),TDD([makeQuery(id+"F42.boolean.opBoolean","COPY",EDGE,{"disambiguationData":[TD([makeQuery(id+"F13.opLoft","SWEPT_FACE",FACE,{"disambiguationData":[OSD([sQuery(id+"F3.wireOp",EDGE,"E20.8.0"),subQ37,subQ36,sQuery(id+"F4.wireOp",EDGE,"E26.8.0"),subQ35,subQ34])]})])],"derivedFrom":subQ9})])]}),makeQuery(id+"F47.opFillet","BLEND_FACE",FACE,{"disambiguationData":[OSD([subQ5,subQ7]),TDD([makeQuery(id+"F42.boolean.opBoolean","COPY",EDGE,{"disambiguationData":[TD([makeQuery(id+"F14.opLoft","SWEPT_FACE",FACE,{"disambiguationData":[OSD([sQuery(id+"F3.wireOp",EDGE,"E20.7.0"),subQ33,subQ32,sQuery(id+"F4.wireOp",EDGE,"E26.7.0"),subQ31,subQ30])]})])],"derivedFrom":subQ9})])]}),makeQuery(id+"F47.opFillet","BLEND_FACE",FACE,{"disambiguationData":[OSD([subQ5,subQ7]),TDD([makeQuery(id+"F42.boolean.opBoolean","COPY",EDGE,{"disambiguationData":[TD([makeQuery(id+"F15.opLoft","SWEPT_FACE",FACE,{"disambiguationData":[OSD([sQuery(id+"F3.wireOp",EDGE,"E20.6.0"),subQ29,subQ28,sQuery(id+"F4.wireOp",EDGE,"E26.6.0"),subQ27,subQ26])]})])],"derivedFrom":subQ9})])]}),makeQuery(id+"F47.opFillet","BLEND_FACE",FACE,{"disambiguationData":[OSD([subQ5,subQ7]),TDD([makeQuery(id+"F42.boolean.opBoolean","COPY",EDGE,{"disambiguationData":[TD([makeQuery(id+"F16.opLoft","SWEPT_FACE",FACE,{"disambiguationData":[OSD([sQuery(id+"F3.wireOp",EDGE,"E20.5.0"),subQ25,subQ24,sQuery(id+"F4.wireOp",EDGE,"E26.5.0"),subQ23,subQ22])]})])],"derivedFrom":subQ9})])]}),makeQuery(id+"F47.opFillet","BLEND_FACE",FACE,{"disambiguationData":[OSD([subQ5,subQ7]),TDD([makeQuery(id+"F42.boolean.opBoolean","COPY",EDGE,{"disambiguationData":[TD([makeQuery(id+"F17.opLoft","SWEPT_FACE",FACE,{"disambiguationData":[OSD([sQuery(id+"F3.wireOp",EDGE,"E20.4.0"),subQ21,subQ20,sQuery(id+"F4.wireOp",EDGE,"E26.4.0"),subQ19,subQ18])]})])],"derivedFrom":subQ9})])]}),makeQuery(id+"F47.opFillet","BLEND_FACE",FACE,{"disambiguationData":[OSD([subQ5,subQ7]),TDD([makeQuery(id+"F42.boolean.opBoolean","COPY",EDGE,{"disambiguationData":[TD([makeQuery(id+"F18.opLoft","SWEPT_FACE",FACE,{"disambiguationData":[OSD([sQuery(id+"F3.wireOp",EDGE,"E20.3.0"),subQ17,subQ16,sQuery(id+"F4.wireOp",EDGE,"E26.3.0"),subQ15,subQ14])]})])],"derivedFrom":subQ9})])]}),makeQuery(id+"F47.opFillet","BLEND_FACE",FACE,{"disambiguationData":[OSD([subQ5,subQ7]),TDD([makeQuery(id+"F42.boolean.opBoolean","COPY",EDGE,{"disambiguationData":[TD([makeQuery(id+"F19.opLoft","SWEPT_FACE",FACE,{"disambiguationData":[OSD([sQuery(id+"F3.wireOp",EDGE,"E20.2.0"),subQ13,subQ12,sQuery(id+"F4.wireOp",EDGE,"E26.2.0"),subQ11,subQ10])]})])],"derivedFrom":subQ9})])]}),makeQuery(id+"F47.opFillet","BLEND_FACE",FACE,{"disambiguationData":[OSD([subQ5,subQ7]),TDD([makeQuery(id+"F42.boolean.opBoolean","COPY",EDGE,{"disambiguationData":[TD([makeQuery(id+"F20.opLoft","SWEPT_FACE",FACE,{"disambiguationData":[OSD([sQuery(id+"F3.wireOp",EDGE,"E20.1.0"),subQ4,subQ3,sQuery(id+"F4.wireOp",EDGE,"E26.1.0"),subQ2,subQ1])]})])],"derivedFrom":subQ9})])]})]});}
            var Q55;
            {var subQ0=makeQuery(id+"F40.opExtrude","CAP_FACE",FACE,{"disambiguationData":[OSD([sQuery(id+"F39.wireOp",EDGE,"E29"),sQuery(id+"F39.wireOp",EDGE,"E30")])],"isStart":false});var subQ1=sQuery(id+"F4.wireOp",EDGE,"E26.1.3");var subQ2=sQuery(id+"F4.wireOp",EDGE,"E26.1.2");var subQ3=sQuery(id+"F3.wireOp",EDGE,"E20.1.3");var subQ4=sQuery(id+"F3.wireOp",EDGE,"E20.1.1");var subQ5=sQuery(id+"F41.wireOp",EDGE,"E35");var subQ6=makeQuery(id+"F42.opRevolve","SWEPT_FACE",FACE,{"disambiguationData":[OSD([subQ5])]});var subQ7=sQuery(id+"F41.wireOp",EDGE,"E36");var subQ8=makeQuery(id+"F42.opRevolve","SWEPT_FACE",FACE,{"disambiguationData":[OSD([subQ7])]});var subQ9=makeQuery(id+"F42.opRevolve","SWEPT_EDGE",EDGE,{"disambiguationData":[OSD([subQ5,subQ7])]});var subQ10=sQuery(id+"F4.wireOp",EDGE,"E26.2.3");var subQ11=sQuery(id+"F4.wireOp",EDGE,"E26.2.2");var subQ12=sQuery(id+"F3.wireOp",EDGE,"E20.2.3");var subQ13=sQuery(id+"F3.wireOp",EDGE,"E20.2.1");var subQ14=sQuery(id+"F4.wireOp",EDGE,"E26.3.3");var subQ15=sQuery(id+"F4.wireOp",EDGE,"E26.3.2");var subQ16=sQuery(id+"F3.wireOp",EDGE,"E20.3.3");var subQ17=sQuery(id+"F3.wireOp",EDGE,"E20.3.1");var subQ18=sQuery(id+"F4.wireOp",EDGE,"E26.4.3");var subQ19=sQuery(id+"F4.wireOp",EDGE,"E26.4.2");var subQ20=sQuery(id+"F3.wireOp",EDGE,"E20.4.3");var subQ21=sQuery(id+"F3.wireOp",EDGE,"E20.4.1");var subQ22=sQuery(id+"F4.wireOp",EDGE,"E26.5.3");var subQ23=sQuery(id+"F4.wireOp",EDGE,"E26.5.2");var subQ24=sQuery(id+"F3.wireOp",EDGE,"E20.5.3");var subQ25=sQuery(id+"F3.wireOp",EDGE,"E20.5.1");var subQ26=sQuery(id+"F4.wireOp",EDGE,"E26.6.3");var subQ27=sQuery(id+"F4.wireOp",EDGE,"E26.6.2");var subQ28=sQuery(id+"F3.wireOp",EDGE,"E20.6.3");var subQ29=sQuery(id+"F3.wireOp",EDGE,"E20.6.1");var subQ30=sQuery(id+"F4.wireOp",EDGE,"E26.7.3");var subQ31=sQuery(id+"F4.wireOp",EDGE,"E26.7.2");var subQ32=sQuery(id+"F3.wireOp",EDGE,"E20.7.3");var subQ33=sQuery(id+"F3.wireOp",EDGE,"E20.7.1");var subQ34=sQuery(id+"F4.wireOp",EDGE,"E26.8.3");var subQ35=sQuery(id+"F4.wireOp",EDGE,"E26.8.2");var subQ36=sQuery(id+"F3.wireOp",EDGE,"E20.8.3");var subQ37=sQuery(id+"F3.wireOp",EDGE,"E20.8.1");var subQ38=sQuery(id+"F4.wireOp",EDGE,"E26.9.3");var subQ39=sQuery(id+"F4.wireOp",EDGE,"E26.9.2");var subQ40=sQuery(id+"F3.wireOp",EDGE,"E20.9.3");var subQ41=sQuery(id+"F3.wireOp",EDGE,"E20.9.1");var subQ42=sQuery(id+"F4.wireOp",EDGE,"E26.10.3");var subQ43=sQuery(id+"F4.wireOp",EDGE,"E26.10.2");var subQ44=sQuery(id+"F3.wireOp",EDGE,"E20.10.3");var subQ45=sQuery(id+"F3.wireOp",EDGE,"E20.10.1");var subQ46=sQuery(id+"F4.wireOp",EDGE,"E26.11.3");var subQ47=sQuery(id+"F4.wireOp",EDGE,"E26.11.2");var subQ48=sQuery(id+"F3.wireOp",EDGE,"E20.11.3");var subQ49=sQuery(id+"F3.wireOp",EDGE,"E20.11.1");var subQ50=sQuery(id+"F4.wireOp",EDGE,"E26.12.3");var subQ51=sQuery(id+"F4.wireOp",EDGE,"E26.12.2");var subQ52=sQuery(id+"F3.wireOp",EDGE,"E20.12.3");var subQ53=sQuery(id+"F3.wireOp",EDGE,"E20.12.1");var subQ54=sQuery(id+"F4.wireOp",EDGE,"E26.13.3");var subQ55=sQuery(id+"F4.wireOp",EDGE,"E26.13.2");var subQ56=sQuery(id+"F3.wireOp",EDGE,"E20.13.3");var subQ57=sQuery(id+"F3.wireOp",EDGE,"E20.13.1");var subQ58=sQuery(id+"F4.wireOp",EDGE,"E26.14.3");var subQ59=sQuery(id+"F4.wireOp",EDGE,"E26.14.2");var subQ60=sQuery(id+"F3.wireOp",EDGE,"E20.14.3");var subQ61=sQuery(id+"F3.wireOp",EDGE,"E20.14.1");var subQ62=sQuery(id+"F4.wireOp",EDGE,"E26.15.3");var subQ63=sQuery(id+"F4.wireOp",EDGE,"E26.15.2");var subQ64=sQuery(id+"F3.wireOp",EDGE,"E20.15.3");var subQ65=sQuery(id+"F3.wireOp",EDGE,"E20.15.1");var subQ67=makeQuery(id+"F6.opLoft","SWEPT_FACE",FACE,{"disambiguationData":[OSD([sQuery(id+"F3.wireOp",EDGE,"E20.15.0"),subQ65,subQ64,sQuery(id+"F4.wireOp",EDGE,"E26.15.0"),subQ63,subQ62])]});var subQ68=sQuery(id+"F4.wireOp",EDGE,"E23");var subQ69=sQuery(id+"F4.wireOp",EDGE,"E22");var subQ70=sQuery(id+"F3.wireOp",EDGE,"E18.top");var subQ71=sQuery(id+"F3.wireOp",EDGE,"E18.bottom");var subQ74=makeQuery(id+"F42.boolean.opBoolean","COPY",FACE,{"disambiguationData":[TD([subQ67])],"derivedFrom":subQ6});var subQ75=makeQuery(id+"F6.boolean.opBoolean","INTERSECT",EDGE,{"derivedFrom":[makeQuery(id+"F1.opRevolve","SWEPT_FACE",FACE,{"disambiguationData":[OSD([sQuery(id+"F0.wireOp",EDGE,"E4")])]}),subQ67]});Q55=makeQuery(id+"F48.opFillet","BLEND_EDGE",EDGE,{"blendedFrom":[makeQuery(id+"F47.opFillet","TWEAK_EDGE",EDGE,{"derivedFrom":[makeQuery(id+"F45.opFillet","BLEND_VERTEX",VERTEX,{"blendedFrom":[subQ75,subQ67,subQ74],"blendedInto":[subQ67,subQ74]}),makeQuery(id+"F45.opFillet","BLEND_VERTEX",VERTEX,{"blendedFrom":[subQ75,makeQuery(id+"F42.boolean.opBoolean","MERGE",FACE,{"derivedFrom":[subQ0,subQ8]}),subQ74],"blendedInto":[makeQuery(id+"F42.boolean.opBoolean","MERGE",FACE,{"derivedFrom":[subQ0,subQ8]}),subQ74]})]}),makeQuery(id+"F47.opFillet","BLEND_FACE",FACE,{"disambiguationData":[OSD([subQ5,subQ7]),TDD([makeQuery(id+"F42.boolean.opBoolean","COPY",EDGE,{"disambiguationData":[TD([makeQuery(id+"F5.opLoft","SWEPT_FACE",FACE,{"disambiguationData":[OSD([subQ71,subQ70,sQuery(id+"F3.wireOp",EDGE,"E18.left"),sQuery(id+"F4.wireOp",EDGE,"E21"),subQ69,subQ68])]})])],"derivedFrom":subQ9})])]}),makeQuery(id+"F47.opFillet","BLEND_FACE",FACE,{"disambiguationData":[OSD([subQ5,subQ7]),TDD([makeQuery(id+"F42.boolean.opBoolean","COPY",EDGE,{"disambiguationData":[TD([subQ67])],"derivedFrom":subQ9})])]}),makeQuery(id+"F47.opFillet","BLEND_FACE",FACE,{"disambiguationData":[OSD([subQ5,subQ7]),TDD([makeQuery(id+"F42.boolean.opBoolean","COPY",EDGE,{"disambiguationData":[TD([makeQuery(id+"F7.opLoft","SWEPT_FACE",FACE,{"disambiguationData":[OSD([sQuery(id+"F3.wireOp",EDGE,"E20.14.0"),subQ61,subQ60,sQuery(id+"F4.wireOp",EDGE,"E26.14.0"),subQ59,subQ58])]})])],"derivedFrom":subQ9})])]}),makeQuery(id+"F47.opFillet","BLEND_FACE",FACE,{"disambiguationData":[OSD([subQ5,subQ7]),TDD([makeQuery(id+"F42.boolean.opBoolean","COPY",EDGE,{"disambiguationData":[TD([makeQuery(id+"F8.opLoft","SWEPT_FACE",FACE,{"disambiguationData":[OSD([sQuery(id+"F3.wireOp",EDGE,"E20.13.0"),subQ57,subQ56,sQuery(id+"F4.wireOp",EDGE,"E26.13.0"),subQ55,subQ54])]})])],"derivedFrom":subQ9})])]}),makeQuery(id+"F47.opFillet","BLEND_FACE",FACE,{"disambiguationData":[OSD([subQ5,subQ7]),TDD([makeQuery(id+"F42.boolean.opBoolean","COPY",EDGE,{"disambiguationData":[TD([makeQuery(id+"F9.opLoft","SWEPT_FACE",FACE,{"disambiguationData":[OSD([sQuery(id+"F3.wireOp",EDGE,"E20.12.0"),subQ53,subQ52,sQuery(id+"F4.wireOp",EDGE,"E26.12.0"),subQ51,subQ50])]})])],"derivedFrom":subQ9})])]}),makeQuery(id+"F47.opFillet","BLEND_FACE",FACE,{"disambiguationData":[OSD([subQ5,subQ7]),TDD([makeQuery(id+"F42.boolean.opBoolean","COPY",EDGE,{"disambiguationData":[TD([makeQuery(id+"F10.opLoft","SWEPT_FACE",FACE,{"disambiguationData":[OSD([sQuery(id+"F3.wireOp",EDGE,"E20.11.0"),subQ49,subQ48,sQuery(id+"F4.wireOp",EDGE,"E26.11.0"),subQ47,subQ46])]})])],"derivedFrom":subQ9})])]}),makeQuery(id+"F47.opFillet","BLEND_FACE",FACE,{"disambiguationData":[OSD([subQ5,subQ7]),TDD([makeQuery(id+"F42.boolean.opBoolean","COPY",EDGE,{"disambiguationData":[TD([makeQuery(id+"F11.opLoft","SWEPT_FACE",FACE,{"disambiguationData":[OSD([sQuery(id+"F3.wireOp",EDGE,"E20.10.0"),subQ45,subQ44,sQuery(id+"F4.wireOp",EDGE,"E26.10.0"),subQ43,subQ42])]})])],"derivedFrom":subQ9})])]}),makeQuery(id+"F47.opFillet","BLEND_FACE",FACE,{"disambiguationData":[OSD([subQ5,subQ7]),TDD([makeQuery(id+"F42.boolean.opBoolean","COPY",EDGE,{"disambiguationData":[TD([makeQuery(id+"F12.opLoft","SWEPT_FACE",FACE,{"disambiguationData":[OSD([sQuery(id+"F3.wireOp",EDGE,"E20.9.0"),subQ41,subQ40,sQuery(id+"F4.wireOp",EDGE,"E26.9.0"),subQ39,subQ38])]})])],"derivedFrom":subQ9})])]}),makeQuery(id+"F47.opFillet","BLEND_FACE",FACE,{"disambiguationData":[OSD([subQ5,subQ7]),TDD([makeQuery(id+"F42.boolean.opBoolean","COPY",EDGE,{"disambiguationData":[TD([makeQuery(id+"F13.opLoft","SWEPT_FACE",FACE,{"disambiguationData":[OSD([sQuery(id+"F3.wireOp",EDGE,"E20.8.0"),subQ37,subQ36,sQuery(id+"F4.wireOp",EDGE,"E26.8.0"),subQ35,subQ34])]})])],"derivedFrom":subQ9})])]}),makeQuery(id+"F47.opFillet","BLEND_FACE",FACE,{"disambiguationData":[OSD([subQ5,subQ7]),TDD([makeQuery(id+"F42.boolean.opBoolean","COPY",EDGE,{"disambiguationData":[TD([makeQuery(id+"F14.opLoft","SWEPT_FACE",FACE,{"disambiguationData":[OSD([sQuery(id+"F3.wireOp",EDGE,"E20.7.0"),subQ33,subQ32,sQuery(id+"F4.wireOp",EDGE,"E26.7.0"),subQ31,subQ30])]})])],"derivedFrom":subQ9})])]}),makeQuery(id+"F47.opFillet","BLEND_FACE",FACE,{"disambiguationData":[OSD([subQ5,subQ7]),TDD([makeQuery(id+"F42.boolean.opBoolean","COPY",EDGE,{"disambiguationData":[TD([makeQuery(id+"F15.opLoft","SWEPT_FACE",FACE,{"disambiguationData":[OSD([sQuery(id+"F3.wireOp",EDGE,"E20.6.0"),subQ29,subQ28,sQuery(id+"F4.wireOp",EDGE,"E26.6.0"),subQ27,subQ26])]})])],"derivedFrom":subQ9})])]}),makeQuery(id+"F47.opFillet","BLEND_FACE",FACE,{"disambiguationData":[OSD([subQ5,subQ7]),TDD([makeQuery(id+"F42.boolean.opBoolean","COPY",EDGE,{"disambiguationData":[TD([makeQuery(id+"F16.opLoft","SWEPT_FACE",FACE,{"disambiguationData":[OSD([sQuery(id+"F3.wireOp",EDGE,"E20.5.0"),subQ25,subQ24,sQuery(id+"F4.wireOp",EDGE,"E26.5.0"),subQ23,subQ22])]})])],"derivedFrom":subQ9})])]}),makeQuery(id+"F47.opFillet","BLEND_FACE",FACE,{"disambiguationData":[OSD([subQ5,subQ7]),TDD([makeQuery(id+"F42.boolean.opBoolean","COPY",EDGE,{"disambiguationData":[TD([makeQuery(id+"F17.opLoft","SWEPT_FACE",FACE,{"disambiguationData":[OSD([sQuery(id+"F3.wireOp",EDGE,"E20.4.0"),subQ21,subQ20,sQuery(id+"F4.wireOp",EDGE,"E26.4.0"),subQ19,subQ18])]})])],"derivedFrom":subQ9})])]}),makeQuery(id+"F47.opFillet","BLEND_FACE",FACE,{"disambiguationData":[OSD([subQ5,subQ7]),TDD([makeQuery(id+"F42.boolean.opBoolean","COPY",EDGE,{"disambiguationData":[TD([makeQuery(id+"F18.opLoft","SWEPT_FACE",FACE,{"disambiguationData":[OSD([sQuery(id+"F3.wireOp",EDGE,"E20.3.0"),subQ17,subQ16,sQuery(id+"F4.wireOp",EDGE,"E26.3.0"),subQ15,subQ14])]})])],"derivedFrom":subQ9})])]}),makeQuery(id+"F47.opFillet","BLEND_FACE",FACE,{"disambiguationData":[OSD([subQ5,subQ7]),TDD([makeQuery(id+"F42.boolean.opBoolean","COPY",EDGE,{"disambiguationData":[TD([makeQuery(id+"F19.opLoft","SWEPT_FACE",FACE,{"disambiguationData":[OSD([sQuery(id+"F3.wireOp",EDGE,"E20.2.0"),subQ13,subQ12,sQuery(id+"F4.wireOp",EDGE,"E26.2.0"),subQ11,subQ10])]})])],"derivedFrom":subQ9})])]}),makeQuery(id+"F47.opFillet","BLEND_FACE",FACE,{"disambiguationData":[OSD([subQ5,subQ7]),TDD([makeQuery(id+"F42.boolean.opBoolean","COPY",EDGE,{"disambiguationData":[TD([makeQuery(id+"F20.opLoft","SWEPT_FACE",FACE,{"disambiguationData":[OSD([sQuery(id+"F3.wireOp",EDGE,"E20.1.0"),subQ4,subQ3,sQuery(id+"F4.wireOp",EDGE,"E26.1.0"),subQ2,subQ1])]})])],"derivedFrom":subQ9})])]})],"blendedInto":[makeQuery(id+"F47.opFillet","BLEND_FACE",FACE,{"disambiguationData":[OSD([subQ5,subQ7]),TDD([makeQuery(id+"F42.boolean.opBoolean","COPY",EDGE,{"disambiguationData":[TD([makeQuery(id+"F5.opLoft","SWEPT_FACE",FACE,{"disambiguationData":[OSD([subQ71,subQ70,sQuery(id+"F3.wireOp",EDGE,"E18.left"),sQuery(id+"F4.wireOp",EDGE,"E21"),subQ69,subQ68])]})])],"derivedFrom":subQ9})])]}),makeQuery(id+"F47.opFillet","BLEND_FACE",FACE,{"disambiguationData":[OSD([subQ5,subQ7]),TDD([makeQuery(id+"F42.boolean.opBoolean","COPY",EDGE,{"disambiguationData":[TD([subQ67])],"derivedFrom":subQ9})])]}),makeQuery(id+"F47.opFillet","BLEND_FACE",FACE,{"disambiguationData":[OSD([subQ5,subQ7]),TDD([makeQuery(id+"F42.boolean.opBoolean","COPY",EDGE,{"disambiguationData":[TD([makeQuery(id+"F7.opLoft","SWEPT_FACE",FACE,{"disambiguationData":[OSD([sQuery(id+"F3.wireOp",EDGE,"E20.14.0"),subQ61,subQ60,sQuery(id+"F4.wireOp",EDGE,"E26.14.0"),subQ59,subQ58])]})])],"derivedFrom":subQ9})])]}),makeQuery(id+"F47.opFillet","BLEND_FACE",FACE,{"disambiguationData":[OSD([subQ5,subQ7]),TDD([makeQuery(id+"F42.boolean.opBoolean","COPY",EDGE,{"disambiguationData":[TD([makeQuery(id+"F8.opLoft","SWEPT_FACE",FACE,{"disambiguationData":[OSD([sQuery(id+"F3.wireOp",EDGE,"E20.13.0"),subQ57,subQ56,sQuery(id+"F4.wireOp",EDGE,"E26.13.0"),subQ55,subQ54])]})])],"derivedFrom":subQ9})])]}),makeQuery(id+"F47.opFillet","BLEND_FACE",FACE,{"disambiguationData":[OSD([subQ5,subQ7]),TDD([makeQuery(id+"F42.boolean.opBoolean","COPY",EDGE,{"disambiguationData":[TD([makeQuery(id+"F9.opLoft","SWEPT_FACE",FACE,{"disambiguationData":[OSD([sQuery(id+"F3.wireOp",EDGE,"E20.12.0"),subQ53,subQ52,sQuery(id+"F4.wireOp",EDGE,"E26.12.0"),subQ51,subQ50])]})])],"derivedFrom":subQ9})])]}),makeQuery(id+"F47.opFillet","BLEND_FACE",FACE,{"disambiguationData":[OSD([subQ5,subQ7]),TDD([makeQuery(id+"F42.boolean.opBoolean","COPY",EDGE,{"disambiguationData":[TD([makeQuery(id+"F10.opLoft","SWEPT_FACE",FACE,{"disambiguationData":[OSD([sQuery(id+"F3.wireOp",EDGE,"E20.11.0"),subQ49,subQ48,sQuery(id+"F4.wireOp",EDGE,"E26.11.0"),subQ47,subQ46])]})])],"derivedFrom":subQ9})])]}),makeQuery(id+"F47.opFillet","BLEND_FACE",FACE,{"disambiguationData":[OSD([subQ5,subQ7]),TDD([makeQuery(id+"F42.boolean.opBoolean","COPY",EDGE,{"disambiguationData":[TD([makeQuery(id+"F11.opLoft","SWEPT_FACE",FACE,{"disambiguationData":[OSD([sQuery(id+"F3.wireOp",EDGE,"E20.10.0"),subQ45,subQ44,sQuery(id+"F4.wireOp",EDGE,"E26.10.0"),subQ43,subQ42])]})])],"derivedFrom":subQ9})])]}),makeQuery(id+"F47.opFillet","BLEND_FACE",FACE,{"disambiguationData":[OSD([subQ5,subQ7]),TDD([makeQuery(id+"F42.boolean.opBoolean","COPY",EDGE,{"disambiguationData":[TD([makeQuery(id+"F12.opLoft","SWEPT_FACE",FACE,{"disambiguationData":[OSD([sQuery(id+"F3.wireOp",EDGE,"E20.9.0"),subQ41,subQ40,sQuery(id+"F4.wireOp",EDGE,"E26.9.0"),subQ39,subQ38])]})])],"derivedFrom":subQ9})])]}),makeQuery(id+"F47.opFillet","BLEND_FACE",FACE,{"disambiguationData":[OSD([subQ5,subQ7]),TDD([makeQuery(id+"F42.boolean.opBoolean","COPY",EDGE,{"disambiguationData":[TD([makeQuery(id+"F13.opLoft","SWEPT_FACE",FACE,{"disambiguationData":[OSD([sQuery(id+"F3.wireOp",EDGE,"E20.8.0"),subQ37,subQ36,sQuery(id+"F4.wireOp",EDGE,"E26.8.0"),subQ35,subQ34])]})])],"derivedFrom":subQ9})])]}),makeQuery(id+"F47.opFillet","BLEND_FACE",FACE,{"disambiguationData":[OSD([subQ5,subQ7]),TDD([makeQuery(id+"F42.boolean.opBoolean","COPY",EDGE,{"disambiguationData":[TD([makeQuery(id+"F14.opLoft","SWEPT_FACE",FACE,{"disambiguationData":[OSD([sQuery(id+"F3.wireOp",EDGE,"E20.7.0"),subQ33,subQ32,sQuery(id+"F4.wireOp",EDGE,"E26.7.0"),subQ31,subQ30])]})])],"derivedFrom":subQ9})])]}),makeQuery(id+"F47.opFillet","BLEND_FACE",FACE,{"disambiguationData":[OSD([subQ5,subQ7]),TDD([makeQuery(id+"F42.boolean.opBoolean","COPY",EDGE,{"disambiguationData":[TD([makeQuery(id+"F15.opLoft","SWEPT_FACE",FACE,{"disambiguationData":[OSD([sQuery(id+"F3.wireOp",EDGE,"E20.6.0"),subQ29,subQ28,sQuery(id+"F4.wireOp",EDGE,"E26.6.0"),subQ27,subQ26])]})])],"derivedFrom":subQ9})])]}),makeQuery(id+"F47.opFillet","BLEND_FACE",FACE,{"disambiguationData":[OSD([subQ5,subQ7]),TDD([makeQuery(id+"F42.boolean.opBoolean","COPY",EDGE,{"disambiguationData":[TD([makeQuery(id+"F16.opLoft","SWEPT_FACE",FACE,{"disambiguationData":[OSD([sQuery(id+"F3.wireOp",EDGE,"E20.5.0"),subQ25,subQ24,sQuery(id+"F4.wireOp",EDGE,"E26.5.0"),subQ23,subQ22])]})])],"derivedFrom":subQ9})])]}),makeQuery(id+"F47.opFillet","BLEND_FACE",FACE,{"disambiguationData":[OSD([subQ5,subQ7]),TDD([makeQuery(id+"F42.boolean.opBoolean","COPY",EDGE,{"disambiguationData":[TD([makeQuery(id+"F17.opLoft","SWEPT_FACE",FACE,{"disambiguationData":[OSD([sQuery(id+"F3.wireOp",EDGE,"E20.4.0"),subQ21,subQ20,sQuery(id+"F4.wireOp",EDGE,"E26.4.0"),subQ19,subQ18])]})])],"derivedFrom":subQ9})])]}),makeQuery(id+"F47.opFillet","BLEND_FACE",FACE,{"disambiguationData":[OSD([subQ5,subQ7]),TDD([makeQuery(id+"F42.boolean.opBoolean","COPY",EDGE,{"disambiguationData":[TD([makeQuery(id+"F18.opLoft","SWEPT_FACE",FACE,{"disambiguationData":[OSD([sQuery(id+"F3.wireOp",EDGE,"E20.3.0"),subQ17,subQ16,sQuery(id+"F4.wireOp",EDGE,"E26.3.0"),subQ15,subQ14])]})])],"derivedFrom":subQ9})])]}),makeQuery(id+"F47.opFillet","BLEND_FACE",FACE,{"disambiguationData":[OSD([subQ5,subQ7]),TDD([makeQuery(id+"F42.boolean.opBoolean","COPY",EDGE,{"disambiguationData":[TD([makeQuery(id+"F19.opLoft","SWEPT_FACE",FACE,{"disambiguationData":[OSD([sQuery(id+"F3.wireOp",EDGE,"E20.2.0"),subQ13,subQ12,sQuery(id+"F4.wireOp",EDGE,"E26.2.0"),subQ11,subQ10])]})])],"derivedFrom":subQ9})])]}),makeQuery(id+"F47.opFillet","BLEND_FACE",FACE,{"disambiguationData":[OSD([subQ5,subQ7]),TDD([makeQuery(id+"F42.boolean.opBoolean","COPY",EDGE,{"disambiguationData":[TD([makeQuery(id+"F20.opLoft","SWEPT_FACE",FACE,{"disambiguationData":[OSD([sQuery(id+"F3.wireOp",EDGE,"E20.1.0"),subQ4,subQ3,sQuery(id+"F4.wireOp",EDGE,"E26.1.0"),subQ2,subQ1])]})])],"derivedFrom":subQ9})])]})]});}
            var Q56;
            {var subQ0=makeQuery(id+"F40.opExtrude","CAP_FACE",FACE,{"disambiguationData":[OSD([sQuery(id+"F39.wireOp",EDGE,"E29"),sQuery(id+"F39.wireOp",EDGE,"E30")])],"isStart":false});var subQ1=sQuery(id+"F4.wireOp",EDGE,"E26.1.3");var subQ2=sQuery(id+"F4.wireOp",EDGE,"E26.1.2");var subQ3=sQuery(id+"F3.wireOp",EDGE,"E20.1.3");var subQ4=sQuery(id+"F3.wireOp",EDGE,"E20.1.1");var subQ5=sQuery(id+"F41.wireOp",EDGE,"E35");var subQ6=makeQuery(id+"F42.opRevolve","SWEPT_FACE",FACE,{"disambiguationData":[OSD([subQ5])]});var subQ7=sQuery(id+"F41.wireOp",EDGE,"E36");var subQ8=makeQuery(id+"F42.opRevolve","SWEPT_FACE",FACE,{"disambiguationData":[OSD([subQ7])]});var subQ9=makeQuery(id+"F42.opRevolve","SWEPT_EDGE",EDGE,{"disambiguationData":[OSD([subQ5,subQ7])]});var subQ10=sQuery(id+"F4.wireOp",EDGE,"E26.2.3");var subQ11=sQuery(id+"F4.wireOp",EDGE,"E26.2.2");var subQ12=sQuery(id+"F3.wireOp",EDGE,"E20.2.3");var subQ13=sQuery(id+"F3.wireOp",EDGE,"E20.2.1");var subQ14=sQuery(id+"F4.wireOp",EDGE,"E26.3.3");var subQ15=sQuery(id+"F4.wireOp",EDGE,"E26.3.2");var subQ16=sQuery(id+"F3.wireOp",EDGE,"E20.3.3");var subQ17=sQuery(id+"F3.wireOp",EDGE,"E20.3.1");var subQ18=sQuery(id+"F4.wireOp",EDGE,"E26.4.3");var subQ19=sQuery(id+"F4.wireOp",EDGE,"E26.4.2");var subQ20=sQuery(id+"F3.wireOp",EDGE,"E20.4.3");var subQ21=sQuery(id+"F3.wireOp",EDGE,"E20.4.1");var subQ22=sQuery(id+"F4.wireOp",EDGE,"E26.5.3");var subQ23=sQuery(id+"F4.wireOp",EDGE,"E26.5.2");var subQ24=sQuery(id+"F3.wireOp",EDGE,"E20.5.3");var subQ25=sQuery(id+"F3.wireOp",EDGE,"E20.5.1");var subQ26=sQuery(id+"F4.wireOp",EDGE,"E26.6.3");var subQ27=sQuery(id+"F4.wireOp",EDGE,"E26.6.2");var subQ28=sQuery(id+"F3.wireOp",EDGE,"E20.6.3");var subQ29=sQuery(id+"F3.wireOp",EDGE,"E20.6.1");var subQ30=sQuery(id+"F4.wireOp",EDGE,"E26.7.3");var subQ31=sQuery(id+"F4.wireOp",EDGE,"E26.7.2");var subQ32=sQuery(id+"F3.wireOp",EDGE,"E20.7.3");var subQ33=sQuery(id+"F3.wireOp",EDGE,"E20.7.1");var subQ34=sQuery(id+"F4.wireOp",EDGE,"E26.8.3");var subQ35=sQuery(id+"F4.wireOp",EDGE,"E26.8.2");var subQ36=sQuery(id+"F3.wireOp",EDGE,"E20.8.3");var subQ37=sQuery(id+"F3.wireOp",EDGE,"E20.8.1");var subQ38=sQuery(id+"F4.wireOp",EDGE,"E26.9.3");var subQ39=sQuery(id+"F4.wireOp",EDGE,"E26.9.2");var subQ40=sQuery(id+"F3.wireOp",EDGE,"E20.9.3");var subQ41=sQuery(id+"F3.wireOp",EDGE,"E20.9.1");var subQ42=sQuery(id+"F4.wireOp",EDGE,"E26.10.3");var subQ43=sQuery(id+"F4.wireOp",EDGE,"E26.10.2");var subQ44=sQuery(id+"F3.wireOp",EDGE,"E20.10.3");var subQ45=sQuery(id+"F3.wireOp",EDGE,"E20.10.1");var subQ46=sQuery(id+"F4.wireOp",EDGE,"E26.11.3");var subQ47=sQuery(id+"F4.wireOp",EDGE,"E26.11.2");var subQ48=sQuery(id+"F3.wireOp",EDGE,"E20.11.3");var subQ49=sQuery(id+"F3.wireOp",EDGE,"E20.11.1");var subQ50=sQuery(id+"F4.wireOp",EDGE,"E26.12.3");var subQ51=sQuery(id+"F4.wireOp",EDGE,"E26.12.2");var subQ52=sQuery(id+"F3.wireOp",EDGE,"E20.12.3");var subQ53=sQuery(id+"F3.wireOp",EDGE,"E20.12.1");var subQ54=sQuery(id+"F4.wireOp",EDGE,"E26.13.3");var subQ55=sQuery(id+"F4.wireOp",EDGE,"E26.13.2");var subQ56=sQuery(id+"F3.wireOp",EDGE,"E20.13.3");var subQ57=sQuery(id+"F3.wireOp",EDGE,"E20.13.1");var subQ58=sQuery(id+"F4.wireOp",EDGE,"E26.14.3");var subQ59=sQuery(id+"F4.wireOp",EDGE,"E26.14.2");var subQ60=sQuery(id+"F3.wireOp",EDGE,"E20.14.3");var subQ61=sQuery(id+"F3.wireOp",EDGE,"E20.14.1");var subQ63=makeQuery(id+"F7.opLoft","SWEPT_FACE",FACE,{"disambiguationData":[OSD([sQuery(id+"F3.wireOp",EDGE,"E20.14.0"),subQ61,subQ60,sQuery(id+"F4.wireOp",EDGE,"E26.14.0"),subQ59,subQ58])]});var subQ64=sQuery(id+"F4.wireOp",EDGE,"E26.15.3");var subQ65=sQuery(id+"F4.wireOp",EDGE,"E26.15.2");var subQ66=sQuery(id+"F3.wireOp",EDGE,"E20.15.3");var subQ67=sQuery(id+"F3.wireOp",EDGE,"E20.15.1");var subQ68=sQuery(id+"F4.wireOp",EDGE,"E23");var subQ69=sQuery(id+"F4.wireOp",EDGE,"E22");var subQ70=sQuery(id+"F3.wireOp",EDGE,"E18.top");var subQ71=sQuery(id+"F3.wireOp",EDGE,"E18.bottom");var subQ74=makeQuery(id+"F42.boolean.opBoolean","COPY",FACE,{"disambiguationData":[TD([subQ63])],"derivedFrom":subQ6});var subQ75=makeQuery(id+"F7.boolean.opBoolean","INTERSECT",EDGE,{"derivedFrom":[makeQuery(id+"F1.opRevolve","SWEPT_FACE",FACE,{"disambiguationData":[OSD([sQuery(id+"F0.wireOp",EDGE,"E4")])]}),subQ63]});Q56=makeQuery(id+"F48.opFillet","BLEND_EDGE",EDGE,{"blendedFrom":[makeQuery(id+"F47.opFillet","TWEAK_EDGE",EDGE,{"derivedFrom":[makeQuery(id+"F45.opFillet","BLEND_VERTEX",VERTEX,{"blendedFrom":[subQ75,subQ63,subQ74],"blendedInto":[subQ63,subQ74]}),makeQuery(id+"F45.opFillet","BLEND_VERTEX",VERTEX,{"blendedFrom":[subQ75,makeQuery(id+"F42.boolean.opBoolean","MERGE",FACE,{"derivedFrom":[subQ0,subQ8]}),subQ74],"blendedInto":[makeQuery(id+"F42.boolean.opBoolean","MERGE",FACE,{"derivedFrom":[subQ0,subQ8]}),subQ74]})]}),makeQuery(id+"F47.opFillet","BLEND_FACE",FACE,{"disambiguationData":[OSD([subQ5,subQ7]),TDD([makeQuery(id+"F42.boolean.opBoolean","COPY",EDGE,{"disambiguationData":[TD([makeQuery(id+"F5.opLoft","SWEPT_FACE",FACE,{"disambiguationData":[OSD([subQ71,subQ70,sQuery(id+"F3.wireOp",EDGE,"E18.left"),sQuery(id+"F4.wireOp",EDGE,"E21"),subQ69,subQ68])]})])],"derivedFrom":subQ9})])]}),makeQuery(id+"F47.opFillet","BLEND_FACE",FACE,{"disambiguationData":[OSD([subQ5,subQ7]),TDD([makeQuery(id+"F42.boolean.opBoolean","COPY",EDGE,{"disambiguationData":[TD([makeQuery(id+"F6.opLoft","SWEPT_FACE",FACE,{"disambiguationData":[OSD([sQuery(id+"F3.wireOp",EDGE,"E20.15.0"),subQ67,subQ66,sQuery(id+"F4.wireOp",EDGE,"E26.15.0"),subQ65,subQ64])]})])],"derivedFrom":subQ9})])]}),makeQuery(id+"F47.opFillet","BLEND_FACE",FACE,{"disambiguationData":[OSD([subQ5,subQ7]),TDD([makeQuery(id+"F42.boolean.opBoolean","COPY",EDGE,{"disambiguationData":[TD([subQ63])],"derivedFrom":subQ9})])]}),makeQuery(id+"F47.opFillet","BLEND_FACE",FACE,{"disambiguationData":[OSD([subQ5,subQ7]),TDD([makeQuery(id+"F42.boolean.opBoolean","COPY",EDGE,{"disambiguationData":[TD([makeQuery(id+"F8.opLoft","SWEPT_FACE",FACE,{"disambiguationData":[OSD([sQuery(id+"F3.wireOp",EDGE,"E20.13.0"),subQ57,subQ56,sQuery(id+"F4.wireOp",EDGE,"E26.13.0"),subQ55,subQ54])]})])],"derivedFrom":subQ9})])]}),makeQuery(id+"F47.opFillet","BLEND_FACE",FACE,{"disambiguationData":[OSD([subQ5,subQ7]),TDD([makeQuery(id+"F42.boolean.opBoolean","COPY",EDGE,{"disambiguationData":[TD([makeQuery(id+"F9.opLoft","SWEPT_FACE",FACE,{"disambiguationData":[OSD([sQuery(id+"F3.wireOp",EDGE,"E20.12.0"),subQ53,subQ52,sQuery(id+"F4.wireOp",EDGE,"E26.12.0"),subQ51,subQ50])]})])],"derivedFrom":subQ9})])]}),makeQuery(id+"F47.opFillet","BLEND_FACE",FACE,{"disambiguationData":[OSD([subQ5,subQ7]),TDD([makeQuery(id+"F42.boolean.opBoolean","COPY",EDGE,{"disambiguationData":[TD([makeQuery(id+"F10.opLoft","SWEPT_FACE",FACE,{"disambiguationData":[OSD([sQuery(id+"F3.wireOp",EDGE,"E20.11.0"),subQ49,subQ48,sQuery(id+"F4.wireOp",EDGE,"E26.11.0"),subQ47,subQ46])]})])],"derivedFrom":subQ9})])]}),makeQuery(id+"F47.opFillet","BLEND_FACE",FACE,{"disambiguationData":[OSD([subQ5,subQ7]),TDD([makeQuery(id+"F42.boolean.opBoolean","COPY",EDGE,{"disambiguationData":[TD([makeQuery(id+"F11.opLoft","SWEPT_FACE",FACE,{"disambiguationData":[OSD([sQuery(id+"F3.wireOp",EDGE,"E20.10.0"),subQ45,subQ44,sQuery(id+"F4.wireOp",EDGE,"E26.10.0"),subQ43,subQ42])]})])],"derivedFrom":subQ9})])]}),makeQuery(id+"F47.opFillet","BLEND_FACE",FACE,{"disambiguationData":[OSD([subQ5,subQ7]),TDD([makeQuery(id+"F42.boolean.opBoolean","COPY",EDGE,{"disambiguationData":[TD([makeQuery(id+"F12.opLoft","SWEPT_FACE",FACE,{"disambiguationData":[OSD([sQuery(id+"F3.wireOp",EDGE,"E20.9.0"),subQ41,subQ40,sQuery(id+"F4.wireOp",EDGE,"E26.9.0"),subQ39,subQ38])]})])],"derivedFrom":subQ9})])]}),makeQuery(id+"F47.opFillet","BLEND_FACE",FACE,{"disambiguationData":[OSD([subQ5,subQ7]),TDD([makeQuery(id+"F42.boolean.opBoolean","COPY",EDGE,{"disambiguationData":[TD([makeQuery(id+"F13.opLoft","SWEPT_FACE",FACE,{"disambiguationData":[OSD([sQuery(id+"F3.wireOp",EDGE,"E20.8.0"),subQ37,subQ36,sQuery(id+"F4.wireOp",EDGE,"E26.8.0"),subQ35,subQ34])]})])],"derivedFrom":subQ9})])]}),makeQuery(id+"F47.opFillet","BLEND_FACE",FACE,{"disambiguationData":[OSD([subQ5,subQ7]),TDD([makeQuery(id+"F42.boolean.opBoolean","COPY",EDGE,{"disambiguationData":[TD([makeQuery(id+"F14.opLoft","SWEPT_FACE",FACE,{"disambiguationData":[OSD([sQuery(id+"F3.wireOp",EDGE,"E20.7.0"),subQ33,subQ32,sQuery(id+"F4.wireOp",EDGE,"E26.7.0"),subQ31,subQ30])]})])],"derivedFrom":subQ9})])]}),makeQuery(id+"F47.opFillet","BLEND_FACE",FACE,{"disambiguationData":[OSD([subQ5,subQ7]),TDD([makeQuery(id+"F42.boolean.opBoolean","COPY",EDGE,{"disambiguationData":[TD([makeQuery(id+"F15.opLoft","SWEPT_FACE",FACE,{"disambiguationData":[OSD([sQuery(id+"F3.wireOp",EDGE,"E20.6.0"),subQ29,subQ28,sQuery(id+"F4.wireOp",EDGE,"E26.6.0"),subQ27,subQ26])]})])],"derivedFrom":subQ9})])]}),makeQuery(id+"F47.opFillet","BLEND_FACE",FACE,{"disambiguationData":[OSD([subQ5,subQ7]),TDD([makeQuery(id+"F42.boolean.opBoolean","COPY",EDGE,{"disambiguationData":[TD([makeQuery(id+"F16.opLoft","SWEPT_FACE",FACE,{"disambiguationData":[OSD([sQuery(id+"F3.wireOp",EDGE,"E20.5.0"),subQ25,subQ24,sQuery(id+"F4.wireOp",EDGE,"E26.5.0"),subQ23,subQ22])]})])],"derivedFrom":subQ9})])]}),makeQuery(id+"F47.opFillet","BLEND_FACE",FACE,{"disambiguationData":[OSD([subQ5,subQ7]),TDD([makeQuery(id+"F42.boolean.opBoolean","COPY",EDGE,{"disambiguationData":[TD([makeQuery(id+"F17.opLoft","SWEPT_FACE",FACE,{"disambiguationData":[OSD([sQuery(id+"F3.wireOp",EDGE,"E20.4.0"),subQ21,subQ20,sQuery(id+"F4.wireOp",EDGE,"E26.4.0"),subQ19,subQ18])]})])],"derivedFrom":subQ9})])]}),makeQuery(id+"F47.opFillet","BLEND_FACE",FACE,{"disambiguationData":[OSD([subQ5,subQ7]),TDD([makeQuery(id+"F42.boolean.opBoolean","COPY",EDGE,{"disambiguationData":[TD([makeQuery(id+"F18.opLoft","SWEPT_FACE",FACE,{"disambiguationData":[OSD([sQuery(id+"F3.wireOp",EDGE,"E20.3.0"),subQ17,subQ16,sQuery(id+"F4.wireOp",EDGE,"E26.3.0"),subQ15,subQ14])]})])],"derivedFrom":subQ9})])]}),makeQuery(id+"F47.opFillet","BLEND_FACE",FACE,{"disambiguationData":[OSD([subQ5,subQ7]),TDD([makeQuery(id+"F42.boolean.opBoolean","COPY",EDGE,{"disambiguationData":[TD([makeQuery(id+"F19.opLoft","SWEPT_FACE",FACE,{"disambiguationData":[OSD([sQuery(id+"F3.wireOp",EDGE,"E20.2.0"),subQ13,subQ12,sQuery(id+"F4.wireOp",EDGE,"E26.2.0"),subQ11,subQ10])]})])],"derivedFrom":subQ9})])]}),makeQuery(id+"F47.opFillet","BLEND_FACE",FACE,{"disambiguationData":[OSD([subQ5,subQ7]),TDD([makeQuery(id+"F42.boolean.opBoolean","COPY",EDGE,{"disambiguationData":[TD([makeQuery(id+"F20.opLoft","SWEPT_FACE",FACE,{"disambiguationData":[OSD([sQuery(id+"F3.wireOp",EDGE,"E20.1.0"),subQ4,subQ3,sQuery(id+"F4.wireOp",EDGE,"E26.1.0"),subQ2,subQ1])]})])],"derivedFrom":subQ9})])]})],"blendedInto":[makeQuery(id+"F47.opFillet","BLEND_FACE",FACE,{"disambiguationData":[OSD([subQ5,subQ7]),TDD([makeQuery(id+"F42.boolean.opBoolean","COPY",EDGE,{"disambiguationData":[TD([makeQuery(id+"F5.opLoft","SWEPT_FACE",FACE,{"disambiguationData":[OSD([subQ71,subQ70,sQuery(id+"F3.wireOp",EDGE,"E18.left"),sQuery(id+"F4.wireOp",EDGE,"E21"),subQ69,subQ68])]})])],"derivedFrom":subQ9})])]}),makeQuery(id+"F47.opFillet","BLEND_FACE",FACE,{"disambiguationData":[OSD([subQ5,subQ7]),TDD([makeQuery(id+"F42.boolean.opBoolean","COPY",EDGE,{"disambiguationData":[TD([makeQuery(id+"F6.opLoft","SWEPT_FACE",FACE,{"disambiguationData":[OSD([sQuery(id+"F3.wireOp",EDGE,"E20.15.0"),subQ67,subQ66,sQuery(id+"F4.wireOp",EDGE,"E26.15.0"),subQ65,subQ64])]})])],"derivedFrom":subQ9})])]}),makeQuery(id+"F47.opFillet","BLEND_FACE",FACE,{"disambiguationData":[OSD([subQ5,subQ7]),TDD([makeQuery(id+"F42.boolean.opBoolean","COPY",EDGE,{"disambiguationData":[TD([subQ63])],"derivedFrom":subQ9})])]}),makeQuery(id+"F47.opFillet","BLEND_FACE",FACE,{"disambiguationData":[OSD([subQ5,subQ7]),TDD([makeQuery(id+"F42.boolean.opBoolean","COPY",EDGE,{"disambiguationData":[TD([makeQuery(id+"F8.opLoft","SWEPT_FACE",FACE,{"disambiguationData":[OSD([sQuery(id+"F3.wireOp",EDGE,"E20.13.0"),subQ57,subQ56,sQuery(id+"F4.wireOp",EDGE,"E26.13.0"),subQ55,subQ54])]})])],"derivedFrom":subQ9})])]}),makeQuery(id+"F47.opFillet","BLEND_FACE",FACE,{"disambiguationData":[OSD([subQ5,subQ7]),TDD([makeQuery(id+"F42.boolean.opBoolean","COPY",EDGE,{"disambiguationData":[TD([makeQuery(id+"F9.opLoft","SWEPT_FACE",FACE,{"disambiguationData":[OSD([sQuery(id+"F3.wireOp",EDGE,"E20.12.0"),subQ53,subQ52,sQuery(id+"F4.wireOp",EDGE,"E26.12.0"),subQ51,subQ50])]})])],"derivedFrom":subQ9})])]}),makeQuery(id+"F47.opFillet","BLEND_FACE",FACE,{"disambiguationData":[OSD([subQ5,subQ7]),TDD([makeQuery(id+"F42.boolean.opBoolean","COPY",EDGE,{"disambiguationData":[TD([makeQuery(id+"F10.opLoft","SWEPT_FACE",FACE,{"disambiguationData":[OSD([sQuery(id+"F3.wireOp",EDGE,"E20.11.0"),subQ49,subQ48,sQuery(id+"F4.wireOp",EDGE,"E26.11.0"),subQ47,subQ46])]})])],"derivedFrom":subQ9})])]}),makeQuery(id+"F47.opFillet","BLEND_FACE",FACE,{"disambiguationData":[OSD([subQ5,subQ7]),TDD([makeQuery(id+"F42.boolean.opBoolean","COPY",EDGE,{"disambiguationData":[TD([makeQuery(id+"F11.opLoft","SWEPT_FACE",FACE,{"disambiguationData":[OSD([sQuery(id+"F3.wireOp",EDGE,"E20.10.0"),subQ45,subQ44,sQuery(id+"F4.wireOp",EDGE,"E26.10.0"),subQ43,subQ42])]})])],"derivedFrom":subQ9})])]}),makeQuery(id+"F47.opFillet","BLEND_FACE",FACE,{"disambiguationData":[OSD([subQ5,subQ7]),TDD([makeQuery(id+"F42.boolean.opBoolean","COPY",EDGE,{"disambiguationData":[TD([makeQuery(id+"F12.opLoft","SWEPT_FACE",FACE,{"disambiguationData":[OSD([sQuery(id+"F3.wireOp",EDGE,"E20.9.0"),subQ41,subQ40,sQuery(id+"F4.wireOp",EDGE,"E26.9.0"),subQ39,subQ38])]})])],"derivedFrom":subQ9})])]}),makeQuery(id+"F47.opFillet","BLEND_FACE",FACE,{"disambiguationData":[OSD([subQ5,subQ7]),TDD([makeQuery(id+"F42.boolean.opBoolean","COPY",EDGE,{"disambiguationData":[TD([makeQuery(id+"F13.opLoft","SWEPT_FACE",FACE,{"disambiguationData":[OSD([sQuery(id+"F3.wireOp",EDGE,"E20.8.0"),subQ37,subQ36,sQuery(id+"F4.wireOp",EDGE,"E26.8.0"),subQ35,subQ34])]})])],"derivedFrom":subQ9})])]}),makeQuery(id+"F47.opFillet","BLEND_FACE",FACE,{"disambiguationData":[OSD([subQ5,subQ7]),TDD([makeQuery(id+"F42.boolean.opBoolean","COPY",EDGE,{"disambiguationData":[TD([makeQuery(id+"F14.opLoft","SWEPT_FACE",FACE,{"disambiguationData":[OSD([sQuery(id+"F3.wireOp",EDGE,"E20.7.0"),subQ33,subQ32,sQuery(id+"F4.wireOp",EDGE,"E26.7.0"),subQ31,subQ30])]})])],"derivedFrom":subQ9})])]}),makeQuery(id+"F47.opFillet","BLEND_FACE",FACE,{"disambiguationData":[OSD([subQ5,subQ7]),TDD([makeQuery(id+"F42.boolean.opBoolean","COPY",EDGE,{"disambiguationData":[TD([makeQuery(id+"F15.opLoft","SWEPT_FACE",FACE,{"disambiguationData":[OSD([sQuery(id+"F3.wireOp",EDGE,"E20.6.0"),subQ29,subQ28,sQuery(id+"F4.wireOp",EDGE,"E26.6.0"),subQ27,subQ26])]})])],"derivedFrom":subQ9})])]}),makeQuery(id+"F47.opFillet","BLEND_FACE",FACE,{"disambiguationData":[OSD([subQ5,subQ7]),TDD([makeQuery(id+"F42.boolean.opBoolean","COPY",EDGE,{"disambiguationData":[TD([makeQuery(id+"F16.opLoft","SWEPT_FACE",FACE,{"disambiguationData":[OSD([sQuery(id+"F3.wireOp",EDGE,"E20.5.0"),subQ25,subQ24,sQuery(id+"F4.wireOp",EDGE,"E26.5.0"),subQ23,subQ22])]})])],"derivedFrom":subQ9})])]}),makeQuery(id+"F47.opFillet","BLEND_FACE",FACE,{"disambiguationData":[OSD([subQ5,subQ7]),TDD([makeQuery(id+"F42.boolean.opBoolean","COPY",EDGE,{"disambiguationData":[TD([makeQuery(id+"F17.opLoft","SWEPT_FACE",FACE,{"disambiguationData":[OSD([sQuery(id+"F3.wireOp",EDGE,"E20.4.0"),subQ21,subQ20,sQuery(id+"F4.wireOp",EDGE,"E26.4.0"),subQ19,subQ18])]})])],"derivedFrom":subQ9})])]}),makeQuery(id+"F47.opFillet","BLEND_FACE",FACE,{"disambiguationData":[OSD([subQ5,subQ7]),TDD([makeQuery(id+"F42.boolean.opBoolean","COPY",EDGE,{"disambiguationData":[TD([makeQuery(id+"F18.opLoft","SWEPT_FACE",FACE,{"disambiguationData":[OSD([sQuery(id+"F3.wireOp",EDGE,"E20.3.0"),subQ17,subQ16,sQuery(id+"F4.wireOp",EDGE,"E26.3.0"),subQ15,subQ14])]})])],"derivedFrom":subQ9})])]}),makeQuery(id+"F47.opFillet","BLEND_FACE",FACE,{"disambiguationData":[OSD([subQ5,subQ7]),TDD([makeQuery(id+"F42.boolean.opBoolean","COPY",EDGE,{"disambiguationData":[TD([makeQuery(id+"F19.opLoft","SWEPT_FACE",FACE,{"disambiguationData":[OSD([sQuery(id+"F3.wireOp",EDGE,"E20.2.0"),subQ13,subQ12,sQuery(id+"F4.wireOp",EDGE,"E26.2.0"),subQ11,subQ10])]})])],"derivedFrom":subQ9})])]}),makeQuery(id+"F47.opFillet","BLEND_FACE",FACE,{"disambiguationData":[OSD([subQ5,subQ7]),TDD([makeQuery(id+"F42.boolean.opBoolean","COPY",EDGE,{"disambiguationData":[TD([makeQuery(id+"F20.opLoft","SWEPT_FACE",FACE,{"disambiguationData":[OSD([sQuery(id+"F3.wireOp",EDGE,"E20.1.0"),subQ4,subQ3,sQuery(id+"F4.wireOp",EDGE,"E26.1.0"),subQ2,subQ1])]})])],"derivedFrom":subQ9})])]})]});}
            var Q57;
            {var subQ0=makeQuery(id+"F40.opExtrude","CAP_FACE",FACE,{"disambiguationData":[OSD([sQuery(id+"F39.wireOp",EDGE,"E29"),sQuery(id+"F39.wireOp",EDGE,"E30")])],"isStart":false});var subQ1=sQuery(id+"F4.wireOp",EDGE,"E26.1.3");var subQ2=sQuery(id+"F4.wireOp",EDGE,"E26.1.2");var subQ3=sQuery(id+"F3.wireOp",EDGE,"E20.1.3");var subQ4=sQuery(id+"F3.wireOp",EDGE,"E20.1.1");var subQ5=sQuery(id+"F41.wireOp",EDGE,"E35");var subQ6=makeQuery(id+"F42.opRevolve","SWEPT_FACE",FACE,{"disambiguationData":[OSD([subQ5])]});var subQ7=sQuery(id+"F41.wireOp",EDGE,"E36");var subQ8=makeQuery(id+"F42.opRevolve","SWEPT_FACE",FACE,{"disambiguationData":[OSD([subQ7])]});var subQ9=makeQuery(id+"F42.opRevolve","SWEPT_EDGE",EDGE,{"disambiguationData":[OSD([subQ5,subQ7])]});var subQ10=sQuery(id+"F4.wireOp",EDGE,"E26.2.3");var subQ11=sQuery(id+"F4.wireOp",EDGE,"E26.2.2");var subQ12=sQuery(id+"F3.wireOp",EDGE,"E20.2.3");var subQ13=sQuery(id+"F3.wireOp",EDGE,"E20.2.1");var subQ14=sQuery(id+"F4.wireOp",EDGE,"E26.3.3");var subQ15=sQuery(id+"F4.wireOp",EDGE,"E26.3.2");var subQ16=sQuery(id+"F3.wireOp",EDGE,"E20.3.3");var subQ17=sQuery(id+"F3.wireOp",EDGE,"E20.3.1");var subQ18=sQuery(id+"F4.wireOp",EDGE,"E26.4.3");var subQ19=sQuery(id+"F4.wireOp",EDGE,"E26.4.2");var subQ20=sQuery(id+"F3.wireOp",EDGE,"E20.4.3");var subQ21=sQuery(id+"F3.wireOp",EDGE,"E20.4.1");var subQ22=sQuery(id+"F4.wireOp",EDGE,"E26.5.3");var subQ23=sQuery(id+"F4.wireOp",EDGE,"E26.5.2");var subQ24=sQuery(id+"F3.wireOp",EDGE,"E20.5.3");var subQ25=sQuery(id+"F3.wireOp",EDGE,"E20.5.1");var subQ26=sQuery(id+"F4.wireOp",EDGE,"E26.6.3");var subQ27=sQuery(id+"F4.wireOp",EDGE,"E26.6.2");var subQ28=sQuery(id+"F3.wireOp",EDGE,"E20.6.3");var subQ29=sQuery(id+"F3.wireOp",EDGE,"E20.6.1");var subQ30=sQuery(id+"F4.wireOp",EDGE,"E26.7.3");var subQ31=sQuery(id+"F4.wireOp",EDGE,"E26.7.2");var subQ32=sQuery(id+"F3.wireOp",EDGE,"E20.7.3");var subQ33=sQuery(id+"F3.wireOp",EDGE,"E20.7.1");var subQ34=sQuery(id+"F4.wireOp",EDGE,"E26.8.3");var subQ35=sQuery(id+"F4.wireOp",EDGE,"E26.8.2");var subQ36=sQuery(id+"F3.wireOp",EDGE,"E20.8.3");var subQ37=sQuery(id+"F3.wireOp",EDGE,"E20.8.1");var subQ38=sQuery(id+"F4.wireOp",EDGE,"E26.9.3");var subQ39=sQuery(id+"F4.wireOp",EDGE,"E26.9.2");var subQ40=sQuery(id+"F3.wireOp",EDGE,"E20.9.3");var subQ41=sQuery(id+"F3.wireOp",EDGE,"E20.9.1");var subQ42=sQuery(id+"F4.wireOp",EDGE,"E26.10.3");var subQ43=sQuery(id+"F4.wireOp",EDGE,"E26.10.2");var subQ44=sQuery(id+"F3.wireOp",EDGE,"E20.10.3");var subQ45=sQuery(id+"F3.wireOp",EDGE,"E20.10.1");var subQ46=sQuery(id+"F4.wireOp",EDGE,"E26.11.3");var subQ47=sQuery(id+"F4.wireOp",EDGE,"E26.11.2");var subQ48=sQuery(id+"F3.wireOp",EDGE,"E20.11.3");var subQ49=sQuery(id+"F3.wireOp",EDGE,"E20.11.1");var subQ50=sQuery(id+"F4.wireOp",EDGE,"E26.12.3");var subQ51=sQuery(id+"F4.wireOp",EDGE,"E26.12.2");var subQ52=sQuery(id+"F3.wireOp",EDGE,"E20.12.3");var subQ53=sQuery(id+"F3.wireOp",EDGE,"E20.12.1");var subQ54=sQuery(id+"F4.wireOp",EDGE,"E26.13.3");var subQ55=sQuery(id+"F4.wireOp",EDGE,"E26.13.2");var subQ56=sQuery(id+"F3.wireOp",EDGE,"E20.13.3");var subQ57=sQuery(id+"F3.wireOp",EDGE,"E20.13.1");var subQ59=makeQuery(id+"F8.opLoft","SWEPT_FACE",FACE,{"disambiguationData":[OSD([sQuery(id+"F3.wireOp",EDGE,"E20.13.0"),subQ57,subQ56,sQuery(id+"F4.wireOp",EDGE,"E26.13.0"),subQ55,subQ54])]});var subQ60=sQuery(id+"F4.wireOp",EDGE,"E26.14.3");var subQ61=sQuery(id+"F4.wireOp",EDGE,"E26.14.2");var subQ62=sQuery(id+"F3.wireOp",EDGE,"E20.14.3");var subQ63=sQuery(id+"F3.wireOp",EDGE,"E20.14.1");var subQ64=sQuery(id+"F4.wireOp",EDGE,"E26.15.3");var subQ65=sQuery(id+"F4.wireOp",EDGE,"E26.15.2");var subQ66=sQuery(id+"F3.wireOp",EDGE,"E20.15.3");var subQ67=sQuery(id+"F3.wireOp",EDGE,"E20.15.1");var subQ68=sQuery(id+"F4.wireOp",EDGE,"E23");var subQ69=sQuery(id+"F4.wireOp",EDGE,"E22");var subQ70=sQuery(id+"F3.wireOp",EDGE,"E18.top");var subQ71=sQuery(id+"F3.wireOp",EDGE,"E18.bottom");var subQ74=makeQuery(id+"F42.boolean.opBoolean","COPY",FACE,{"disambiguationData":[TD([subQ59])],"derivedFrom":subQ6});var subQ75=makeQuery(id+"F8.boolean.opBoolean","INTERSECT",EDGE,{"derivedFrom":[makeQuery(id+"F1.opRevolve","SWEPT_FACE",FACE,{"disambiguationData":[OSD([sQuery(id+"F0.wireOp",EDGE,"E4")])]}),subQ59]});Q57=makeQuery(id+"F48.opFillet","BLEND_EDGE",EDGE,{"blendedFrom":[makeQuery(id+"F47.opFillet","TWEAK_EDGE",EDGE,{"derivedFrom":[makeQuery(id+"F45.opFillet","BLEND_VERTEX",VERTEX,{"blendedFrom":[subQ75,subQ59,subQ74],"blendedInto":[subQ59,subQ74]}),makeQuery(id+"F45.opFillet","BLEND_VERTEX",VERTEX,{"blendedFrom":[subQ75,makeQuery(id+"F42.boolean.opBoolean","MERGE",FACE,{"derivedFrom":[subQ0,subQ8]}),subQ74],"blendedInto":[makeQuery(id+"F42.boolean.opBoolean","MERGE",FACE,{"derivedFrom":[subQ0,subQ8]}),subQ74]})]}),makeQuery(id+"F47.opFillet","BLEND_FACE",FACE,{"disambiguationData":[OSD([subQ5,subQ7]),TDD([makeQuery(id+"F42.boolean.opBoolean","COPY",EDGE,{"disambiguationData":[TD([makeQuery(id+"F5.opLoft","SWEPT_FACE",FACE,{"disambiguationData":[OSD([subQ71,subQ70,sQuery(id+"F3.wireOp",EDGE,"E18.left"),sQuery(id+"F4.wireOp",EDGE,"E21"),subQ69,subQ68])]})])],"derivedFrom":subQ9})])]}),makeQuery(id+"F47.opFillet","BLEND_FACE",FACE,{"disambiguationData":[OSD([subQ5,subQ7]),TDD([makeQuery(id+"F42.boolean.opBoolean","COPY",EDGE,{"disambiguationData":[TD([makeQuery(id+"F6.opLoft","SWEPT_FACE",FACE,{"disambiguationData":[OSD([sQuery(id+"F3.wireOp",EDGE,"E20.15.0"),subQ67,subQ66,sQuery(id+"F4.wireOp",EDGE,"E26.15.0"),subQ65,subQ64])]})])],"derivedFrom":subQ9})])]}),makeQuery(id+"F47.opFillet","BLEND_FACE",FACE,{"disambiguationData":[OSD([subQ5,subQ7]),TDD([makeQuery(id+"F42.boolean.opBoolean","COPY",EDGE,{"disambiguationData":[TD([makeQuery(id+"F7.opLoft","SWEPT_FACE",FACE,{"disambiguationData":[OSD([sQuery(id+"F3.wireOp",EDGE,"E20.14.0"),subQ63,subQ62,sQuery(id+"F4.wireOp",EDGE,"E26.14.0"),subQ61,subQ60])]})])],"derivedFrom":subQ9})])]}),makeQuery(id+"F47.opFillet","BLEND_FACE",FACE,{"disambiguationData":[OSD([subQ5,subQ7]),TDD([makeQuery(id+"F42.boolean.opBoolean","COPY",EDGE,{"disambiguationData":[TD([subQ59])],"derivedFrom":subQ9})])]}),makeQuery(id+"F47.opFillet","BLEND_FACE",FACE,{"disambiguationData":[OSD([subQ5,subQ7]),TDD([makeQuery(id+"F42.boolean.opBoolean","COPY",EDGE,{"disambiguationData":[TD([makeQuery(id+"F9.opLoft","SWEPT_FACE",FACE,{"disambiguationData":[OSD([sQuery(id+"F3.wireOp",EDGE,"E20.12.0"),subQ53,subQ52,sQuery(id+"F4.wireOp",EDGE,"E26.12.0"),subQ51,subQ50])]})])],"derivedFrom":subQ9})])]}),makeQuery(id+"F47.opFillet","BLEND_FACE",FACE,{"disambiguationData":[OSD([subQ5,subQ7]),TDD([makeQuery(id+"F42.boolean.opBoolean","COPY",EDGE,{"disambiguationData":[TD([makeQuery(id+"F10.opLoft","SWEPT_FACE",FACE,{"disambiguationData":[OSD([sQuery(id+"F3.wireOp",EDGE,"E20.11.0"),subQ49,subQ48,sQuery(id+"F4.wireOp",EDGE,"E26.11.0"),subQ47,subQ46])]})])],"derivedFrom":subQ9})])]}),makeQuery(id+"F47.opFillet","BLEND_FACE",FACE,{"disambiguationData":[OSD([subQ5,subQ7]),TDD([makeQuery(id+"F42.boolean.opBoolean","COPY",EDGE,{"disambiguationData":[TD([makeQuery(id+"F11.opLoft","SWEPT_FACE",FACE,{"disambiguationData":[OSD([sQuery(id+"F3.wireOp",EDGE,"E20.10.0"),subQ45,subQ44,sQuery(id+"F4.wireOp",EDGE,"E26.10.0"),subQ43,subQ42])]})])],"derivedFrom":subQ9})])]}),makeQuery(id+"F47.opFillet","BLEND_FACE",FACE,{"disambiguationData":[OSD([subQ5,subQ7]),TDD([makeQuery(id+"F42.boolean.opBoolean","COPY",EDGE,{"disambiguationData":[TD([makeQuery(id+"F12.opLoft","SWEPT_FACE",FACE,{"disambiguationData":[OSD([sQuery(id+"F3.wireOp",EDGE,"E20.9.0"),subQ41,subQ40,sQuery(id+"F4.wireOp",EDGE,"E26.9.0"),subQ39,subQ38])]})])],"derivedFrom":subQ9})])]}),makeQuery(id+"F47.opFillet","BLEND_FACE",FACE,{"disambiguationData":[OSD([subQ5,subQ7]),TDD([makeQuery(id+"F42.boolean.opBoolean","COPY",EDGE,{"disambiguationData":[TD([makeQuery(id+"F13.opLoft","SWEPT_FACE",FACE,{"disambiguationData":[OSD([sQuery(id+"F3.wireOp",EDGE,"E20.8.0"),subQ37,subQ36,sQuery(id+"F4.wireOp",EDGE,"E26.8.0"),subQ35,subQ34])]})])],"derivedFrom":subQ9})])]}),makeQuery(id+"F47.opFillet","BLEND_FACE",FACE,{"disambiguationData":[OSD([subQ5,subQ7]),TDD([makeQuery(id+"F42.boolean.opBoolean","COPY",EDGE,{"disambiguationData":[TD([makeQuery(id+"F14.opLoft","SWEPT_FACE",FACE,{"disambiguationData":[OSD([sQuery(id+"F3.wireOp",EDGE,"E20.7.0"),subQ33,subQ32,sQuery(id+"F4.wireOp",EDGE,"E26.7.0"),subQ31,subQ30])]})])],"derivedFrom":subQ9})])]}),makeQuery(id+"F47.opFillet","BLEND_FACE",FACE,{"disambiguationData":[OSD([subQ5,subQ7]),TDD([makeQuery(id+"F42.boolean.opBoolean","COPY",EDGE,{"disambiguationData":[TD([makeQuery(id+"F15.opLoft","SWEPT_FACE",FACE,{"disambiguationData":[OSD([sQuery(id+"F3.wireOp",EDGE,"E20.6.0"),subQ29,subQ28,sQuery(id+"F4.wireOp",EDGE,"E26.6.0"),subQ27,subQ26])]})])],"derivedFrom":subQ9})])]}),makeQuery(id+"F47.opFillet","BLEND_FACE",FACE,{"disambiguationData":[OSD([subQ5,subQ7]),TDD([makeQuery(id+"F42.boolean.opBoolean","COPY",EDGE,{"disambiguationData":[TD([makeQuery(id+"F16.opLoft","SWEPT_FACE",FACE,{"disambiguationData":[OSD([sQuery(id+"F3.wireOp",EDGE,"E20.5.0"),subQ25,subQ24,sQuery(id+"F4.wireOp",EDGE,"E26.5.0"),subQ23,subQ22])]})])],"derivedFrom":subQ9})])]}),makeQuery(id+"F47.opFillet","BLEND_FACE",FACE,{"disambiguationData":[OSD([subQ5,subQ7]),TDD([makeQuery(id+"F42.boolean.opBoolean","COPY",EDGE,{"disambiguationData":[TD([makeQuery(id+"F17.opLoft","SWEPT_FACE",FACE,{"disambiguationData":[OSD([sQuery(id+"F3.wireOp",EDGE,"E20.4.0"),subQ21,subQ20,sQuery(id+"F4.wireOp",EDGE,"E26.4.0"),subQ19,subQ18])]})])],"derivedFrom":subQ9})])]}),makeQuery(id+"F47.opFillet","BLEND_FACE",FACE,{"disambiguationData":[OSD([subQ5,subQ7]),TDD([makeQuery(id+"F42.boolean.opBoolean","COPY",EDGE,{"disambiguationData":[TD([makeQuery(id+"F18.opLoft","SWEPT_FACE",FACE,{"disambiguationData":[OSD([sQuery(id+"F3.wireOp",EDGE,"E20.3.0"),subQ17,subQ16,sQuery(id+"F4.wireOp",EDGE,"E26.3.0"),subQ15,subQ14])]})])],"derivedFrom":subQ9})])]}),makeQuery(id+"F47.opFillet","BLEND_FACE",FACE,{"disambiguationData":[OSD([subQ5,subQ7]),TDD([makeQuery(id+"F42.boolean.opBoolean","COPY",EDGE,{"disambiguationData":[TD([makeQuery(id+"F19.opLoft","SWEPT_FACE",FACE,{"disambiguationData":[OSD([sQuery(id+"F3.wireOp",EDGE,"E20.2.0"),subQ13,subQ12,sQuery(id+"F4.wireOp",EDGE,"E26.2.0"),subQ11,subQ10])]})])],"derivedFrom":subQ9})])]}),makeQuery(id+"F47.opFillet","BLEND_FACE",FACE,{"disambiguationData":[OSD([subQ5,subQ7]),TDD([makeQuery(id+"F42.boolean.opBoolean","COPY",EDGE,{"disambiguationData":[TD([makeQuery(id+"F20.opLoft","SWEPT_FACE",FACE,{"disambiguationData":[OSD([sQuery(id+"F3.wireOp",EDGE,"E20.1.0"),subQ4,subQ3,sQuery(id+"F4.wireOp",EDGE,"E26.1.0"),subQ2,subQ1])]})])],"derivedFrom":subQ9})])]})],"blendedInto":[makeQuery(id+"F47.opFillet","BLEND_FACE",FACE,{"disambiguationData":[OSD([subQ5,subQ7]),TDD([makeQuery(id+"F42.boolean.opBoolean","COPY",EDGE,{"disambiguationData":[TD([makeQuery(id+"F5.opLoft","SWEPT_FACE",FACE,{"disambiguationData":[OSD([subQ71,subQ70,sQuery(id+"F3.wireOp",EDGE,"E18.left"),sQuery(id+"F4.wireOp",EDGE,"E21"),subQ69,subQ68])]})])],"derivedFrom":subQ9})])]}),makeQuery(id+"F47.opFillet","BLEND_FACE",FACE,{"disambiguationData":[OSD([subQ5,subQ7]),TDD([makeQuery(id+"F42.boolean.opBoolean","COPY",EDGE,{"disambiguationData":[TD([makeQuery(id+"F6.opLoft","SWEPT_FACE",FACE,{"disambiguationData":[OSD([sQuery(id+"F3.wireOp",EDGE,"E20.15.0"),subQ67,subQ66,sQuery(id+"F4.wireOp",EDGE,"E26.15.0"),subQ65,subQ64])]})])],"derivedFrom":subQ9})])]}),makeQuery(id+"F47.opFillet","BLEND_FACE",FACE,{"disambiguationData":[OSD([subQ5,subQ7]),TDD([makeQuery(id+"F42.boolean.opBoolean","COPY",EDGE,{"disambiguationData":[TD([makeQuery(id+"F7.opLoft","SWEPT_FACE",FACE,{"disambiguationData":[OSD([sQuery(id+"F3.wireOp",EDGE,"E20.14.0"),subQ63,subQ62,sQuery(id+"F4.wireOp",EDGE,"E26.14.0"),subQ61,subQ60])]})])],"derivedFrom":subQ9})])]}),makeQuery(id+"F47.opFillet","BLEND_FACE",FACE,{"disambiguationData":[OSD([subQ5,subQ7]),TDD([makeQuery(id+"F42.boolean.opBoolean","COPY",EDGE,{"disambiguationData":[TD([subQ59])],"derivedFrom":subQ9})])]}),makeQuery(id+"F47.opFillet","BLEND_FACE",FACE,{"disambiguationData":[OSD([subQ5,subQ7]),TDD([makeQuery(id+"F42.boolean.opBoolean","COPY",EDGE,{"disambiguationData":[TD([makeQuery(id+"F9.opLoft","SWEPT_FACE",FACE,{"disambiguationData":[OSD([sQuery(id+"F3.wireOp",EDGE,"E20.12.0"),subQ53,subQ52,sQuery(id+"F4.wireOp",EDGE,"E26.12.0"),subQ51,subQ50])]})])],"derivedFrom":subQ9})])]}),makeQuery(id+"F47.opFillet","BLEND_FACE",FACE,{"disambiguationData":[OSD([subQ5,subQ7]),TDD([makeQuery(id+"F42.boolean.opBoolean","COPY",EDGE,{"disambiguationData":[TD([makeQuery(id+"F10.opLoft","SWEPT_FACE",FACE,{"disambiguationData":[OSD([sQuery(id+"F3.wireOp",EDGE,"E20.11.0"),subQ49,subQ48,sQuery(id+"F4.wireOp",EDGE,"E26.11.0"),subQ47,subQ46])]})])],"derivedFrom":subQ9})])]}),makeQuery(id+"F47.opFillet","BLEND_FACE",FACE,{"disambiguationData":[OSD([subQ5,subQ7]),TDD([makeQuery(id+"F42.boolean.opBoolean","COPY",EDGE,{"disambiguationData":[TD([makeQuery(id+"F11.opLoft","SWEPT_FACE",FACE,{"disambiguationData":[OSD([sQuery(id+"F3.wireOp",EDGE,"E20.10.0"),subQ45,subQ44,sQuery(id+"F4.wireOp",EDGE,"E26.10.0"),subQ43,subQ42])]})])],"derivedFrom":subQ9})])]}),makeQuery(id+"F47.opFillet","BLEND_FACE",FACE,{"disambiguationData":[OSD([subQ5,subQ7]),TDD([makeQuery(id+"F42.boolean.opBoolean","COPY",EDGE,{"disambiguationData":[TD([makeQuery(id+"F12.opLoft","SWEPT_FACE",FACE,{"disambiguationData":[OSD([sQuery(id+"F3.wireOp",EDGE,"E20.9.0"),subQ41,subQ40,sQuery(id+"F4.wireOp",EDGE,"E26.9.0"),subQ39,subQ38])]})])],"derivedFrom":subQ9})])]}),makeQuery(id+"F47.opFillet","BLEND_FACE",FACE,{"disambiguationData":[OSD([subQ5,subQ7]),TDD([makeQuery(id+"F42.boolean.opBoolean","COPY",EDGE,{"disambiguationData":[TD([makeQuery(id+"F13.opLoft","SWEPT_FACE",FACE,{"disambiguationData":[OSD([sQuery(id+"F3.wireOp",EDGE,"E20.8.0"),subQ37,subQ36,sQuery(id+"F4.wireOp",EDGE,"E26.8.0"),subQ35,subQ34])]})])],"derivedFrom":subQ9})])]}),makeQuery(id+"F47.opFillet","BLEND_FACE",FACE,{"disambiguationData":[OSD([subQ5,subQ7]),TDD([makeQuery(id+"F42.boolean.opBoolean","COPY",EDGE,{"disambiguationData":[TD([makeQuery(id+"F14.opLoft","SWEPT_FACE",FACE,{"disambiguationData":[OSD([sQuery(id+"F3.wireOp",EDGE,"E20.7.0"),subQ33,subQ32,sQuery(id+"F4.wireOp",EDGE,"E26.7.0"),subQ31,subQ30])]})])],"derivedFrom":subQ9})])]}),makeQuery(id+"F47.opFillet","BLEND_FACE",FACE,{"disambiguationData":[OSD([subQ5,subQ7]),TDD([makeQuery(id+"F42.boolean.opBoolean","COPY",EDGE,{"disambiguationData":[TD([makeQuery(id+"F15.opLoft","SWEPT_FACE",FACE,{"disambiguationData":[OSD([sQuery(id+"F3.wireOp",EDGE,"E20.6.0"),subQ29,subQ28,sQuery(id+"F4.wireOp",EDGE,"E26.6.0"),subQ27,subQ26])]})])],"derivedFrom":subQ9})])]}),makeQuery(id+"F47.opFillet","BLEND_FACE",FACE,{"disambiguationData":[OSD([subQ5,subQ7]),TDD([makeQuery(id+"F42.boolean.opBoolean","COPY",EDGE,{"disambiguationData":[TD([makeQuery(id+"F16.opLoft","SWEPT_FACE",FACE,{"disambiguationData":[OSD([sQuery(id+"F3.wireOp",EDGE,"E20.5.0"),subQ25,subQ24,sQuery(id+"F4.wireOp",EDGE,"E26.5.0"),subQ23,subQ22])]})])],"derivedFrom":subQ9})])]}),makeQuery(id+"F47.opFillet","BLEND_FACE",FACE,{"disambiguationData":[OSD([subQ5,subQ7]),TDD([makeQuery(id+"F42.boolean.opBoolean","COPY",EDGE,{"disambiguationData":[TD([makeQuery(id+"F17.opLoft","SWEPT_FACE",FACE,{"disambiguationData":[OSD([sQuery(id+"F3.wireOp",EDGE,"E20.4.0"),subQ21,subQ20,sQuery(id+"F4.wireOp",EDGE,"E26.4.0"),subQ19,subQ18])]})])],"derivedFrom":subQ9})])]}),makeQuery(id+"F47.opFillet","BLEND_FACE",FACE,{"disambiguationData":[OSD([subQ5,subQ7]),TDD([makeQuery(id+"F42.boolean.opBoolean","COPY",EDGE,{"disambiguationData":[TD([makeQuery(id+"F18.opLoft","SWEPT_FACE",FACE,{"disambiguationData":[OSD([sQuery(id+"F3.wireOp",EDGE,"E20.3.0"),subQ17,subQ16,sQuery(id+"F4.wireOp",EDGE,"E26.3.0"),subQ15,subQ14])]})])],"derivedFrom":subQ9})])]}),makeQuery(id+"F47.opFillet","BLEND_FACE",FACE,{"disambiguationData":[OSD([subQ5,subQ7]),TDD([makeQuery(id+"F42.boolean.opBoolean","COPY",EDGE,{"disambiguationData":[TD([makeQuery(id+"F19.opLoft","SWEPT_FACE",FACE,{"disambiguationData":[OSD([sQuery(id+"F3.wireOp",EDGE,"E20.2.0"),subQ13,subQ12,sQuery(id+"F4.wireOp",EDGE,"E26.2.0"),subQ11,subQ10])]})])],"derivedFrom":subQ9})])]}),makeQuery(id+"F47.opFillet","BLEND_FACE",FACE,{"disambiguationData":[OSD([subQ5,subQ7]),TDD([makeQuery(id+"F42.boolean.opBoolean","COPY",EDGE,{"disambiguationData":[TD([makeQuery(id+"F20.opLoft","SWEPT_FACE",FACE,{"disambiguationData":[OSD([sQuery(id+"F3.wireOp",EDGE,"E20.1.0"),subQ4,subQ3,sQuery(id+"F4.wireOp",EDGE,"E26.1.0"),subQ2,subQ1])]})])],"derivedFrom":subQ9})])]})]});}
            var Q58;
            {var subQ0=makeQuery(id+"F40.opExtrude","CAP_FACE",FACE,{"disambiguationData":[OSD([sQuery(id+"F39.wireOp",EDGE,"E29"),sQuery(id+"F39.wireOp",EDGE,"E30")])],"isStart":false});var subQ1=sQuery(id+"F4.wireOp",EDGE,"E26.1.3");var subQ2=sQuery(id+"F4.wireOp",EDGE,"E26.1.2");var subQ3=sQuery(id+"F3.wireOp",EDGE,"E20.1.3");var subQ4=sQuery(id+"F3.wireOp",EDGE,"E20.1.1");var subQ5=sQuery(id+"F41.wireOp",EDGE,"E35");var subQ6=makeQuery(id+"F42.opRevolve","SWEPT_FACE",FACE,{"disambiguationData":[OSD([subQ5])]});var subQ7=sQuery(id+"F41.wireOp",EDGE,"E36");var subQ8=makeQuery(id+"F42.opRevolve","SWEPT_FACE",FACE,{"disambiguationData":[OSD([subQ7])]});var subQ9=makeQuery(id+"F42.opRevolve","SWEPT_EDGE",EDGE,{"disambiguationData":[OSD([subQ5,subQ7])]});var subQ10=sQuery(id+"F4.wireOp",EDGE,"E26.2.3");var subQ11=sQuery(id+"F4.wireOp",EDGE,"E26.2.2");var subQ12=sQuery(id+"F3.wireOp",EDGE,"E20.2.3");var subQ13=sQuery(id+"F3.wireOp",EDGE,"E20.2.1");var subQ14=sQuery(id+"F4.wireOp",EDGE,"E26.3.3");var subQ15=sQuery(id+"F4.wireOp",EDGE,"E26.3.2");var subQ16=sQuery(id+"F3.wireOp",EDGE,"E20.3.3");var subQ17=sQuery(id+"F3.wireOp",EDGE,"E20.3.1");var subQ18=sQuery(id+"F4.wireOp",EDGE,"E26.4.3");var subQ19=sQuery(id+"F4.wireOp",EDGE,"E26.4.2");var subQ20=sQuery(id+"F3.wireOp",EDGE,"E20.4.3");var subQ21=sQuery(id+"F3.wireOp",EDGE,"E20.4.1");var subQ22=sQuery(id+"F4.wireOp",EDGE,"E26.5.3");var subQ23=sQuery(id+"F4.wireOp",EDGE,"E26.5.2");var subQ24=sQuery(id+"F3.wireOp",EDGE,"E20.5.3");var subQ25=sQuery(id+"F3.wireOp",EDGE,"E20.5.1");var subQ26=sQuery(id+"F4.wireOp",EDGE,"E26.6.3");var subQ27=sQuery(id+"F4.wireOp",EDGE,"E26.6.2");var subQ28=sQuery(id+"F3.wireOp",EDGE,"E20.6.3");var subQ29=sQuery(id+"F3.wireOp",EDGE,"E20.6.1");var subQ30=sQuery(id+"F4.wireOp",EDGE,"E26.7.3");var subQ31=sQuery(id+"F4.wireOp",EDGE,"E26.7.2");var subQ32=sQuery(id+"F3.wireOp",EDGE,"E20.7.3");var subQ33=sQuery(id+"F3.wireOp",EDGE,"E20.7.1");var subQ34=sQuery(id+"F4.wireOp",EDGE,"E26.8.3");var subQ35=sQuery(id+"F4.wireOp",EDGE,"E26.8.2");var subQ36=sQuery(id+"F3.wireOp",EDGE,"E20.8.3");var subQ37=sQuery(id+"F3.wireOp",EDGE,"E20.8.1");var subQ38=sQuery(id+"F4.wireOp",EDGE,"E26.9.3");var subQ39=sQuery(id+"F4.wireOp",EDGE,"E26.9.2");var subQ40=sQuery(id+"F3.wireOp",EDGE,"E20.9.3");var subQ41=sQuery(id+"F3.wireOp",EDGE,"E20.9.1");var subQ42=sQuery(id+"F4.wireOp",EDGE,"E26.10.3");var subQ43=sQuery(id+"F4.wireOp",EDGE,"E26.10.2");var subQ44=sQuery(id+"F3.wireOp",EDGE,"E20.10.3");var subQ45=sQuery(id+"F3.wireOp",EDGE,"E20.10.1");var subQ46=sQuery(id+"F4.wireOp",EDGE,"E26.11.3");var subQ47=sQuery(id+"F4.wireOp",EDGE,"E26.11.2");var subQ48=sQuery(id+"F3.wireOp",EDGE,"E20.11.3");var subQ49=sQuery(id+"F3.wireOp",EDGE,"E20.11.1");var subQ50=sQuery(id+"F4.wireOp",EDGE,"E26.12.3");var subQ51=sQuery(id+"F4.wireOp",EDGE,"E26.12.2");var subQ52=sQuery(id+"F3.wireOp",EDGE,"E20.12.3");var subQ53=sQuery(id+"F3.wireOp",EDGE,"E20.12.1");var subQ55=makeQuery(id+"F9.opLoft","SWEPT_FACE",FACE,{"disambiguationData":[OSD([sQuery(id+"F3.wireOp",EDGE,"E20.12.0"),subQ53,subQ52,sQuery(id+"F4.wireOp",EDGE,"E26.12.0"),subQ51,subQ50])]});var subQ56=sQuery(id+"F4.wireOp",EDGE,"E26.13.3");var subQ57=sQuery(id+"F4.wireOp",EDGE,"E26.13.2");var subQ58=sQuery(id+"F3.wireOp",EDGE,"E20.13.3");var subQ59=sQuery(id+"F3.wireOp",EDGE,"E20.13.1");var subQ60=sQuery(id+"F4.wireOp",EDGE,"E26.14.3");var subQ61=sQuery(id+"F4.wireOp",EDGE,"E26.14.2");var subQ62=sQuery(id+"F3.wireOp",EDGE,"E20.14.3");var subQ63=sQuery(id+"F3.wireOp",EDGE,"E20.14.1");var subQ64=sQuery(id+"F4.wireOp",EDGE,"E26.15.3");var subQ65=sQuery(id+"F4.wireOp",EDGE,"E26.15.2");var subQ66=sQuery(id+"F3.wireOp",EDGE,"E20.15.3");var subQ67=sQuery(id+"F3.wireOp",EDGE,"E20.15.1");var subQ68=sQuery(id+"F4.wireOp",EDGE,"E23");var subQ69=sQuery(id+"F4.wireOp",EDGE,"E22");var subQ70=sQuery(id+"F3.wireOp",EDGE,"E18.top");var subQ71=sQuery(id+"F3.wireOp",EDGE,"E18.bottom");var subQ74=makeQuery(id+"F42.boolean.opBoolean","COPY",FACE,{"disambiguationData":[TD([subQ55])],"derivedFrom":subQ6});var subQ75=makeQuery(id+"F9.boolean.opBoolean","INTERSECT",EDGE,{"derivedFrom":[makeQuery(id+"F1.opRevolve","SWEPT_FACE",FACE,{"disambiguationData":[OSD([sQuery(id+"F0.wireOp",EDGE,"E4")])]}),subQ55]});Q58=makeQuery(id+"F48.opFillet","BLEND_EDGE",EDGE,{"blendedFrom":[makeQuery(id+"F47.opFillet","TWEAK_EDGE",EDGE,{"derivedFrom":[makeQuery(id+"F45.opFillet","BLEND_VERTEX",VERTEX,{"blendedFrom":[subQ75,subQ55,subQ74],"blendedInto":[subQ55,subQ74]}),makeQuery(id+"F45.opFillet","BLEND_VERTEX",VERTEX,{"blendedFrom":[subQ75,makeQuery(id+"F42.boolean.opBoolean","MERGE",FACE,{"derivedFrom":[subQ0,subQ8]}),subQ74],"blendedInto":[makeQuery(id+"F42.boolean.opBoolean","MERGE",FACE,{"derivedFrom":[subQ0,subQ8]}),subQ74]})]}),makeQuery(id+"F47.opFillet","BLEND_FACE",FACE,{"disambiguationData":[OSD([subQ5,subQ7]),TDD([makeQuery(id+"F42.boolean.opBoolean","COPY",EDGE,{"disambiguationData":[TD([makeQuery(id+"F5.opLoft","SWEPT_FACE",FACE,{"disambiguationData":[OSD([subQ71,subQ70,sQuery(id+"F3.wireOp",EDGE,"E18.left"),sQuery(id+"F4.wireOp",EDGE,"E21"),subQ69,subQ68])]})])],"derivedFrom":subQ9})])]}),makeQuery(id+"F47.opFillet","BLEND_FACE",FACE,{"disambiguationData":[OSD([subQ5,subQ7]),TDD([makeQuery(id+"F42.boolean.opBoolean","COPY",EDGE,{"disambiguationData":[TD([makeQuery(id+"F6.opLoft","SWEPT_FACE",FACE,{"disambiguationData":[OSD([sQuery(id+"F3.wireOp",EDGE,"E20.15.0"),subQ67,subQ66,sQuery(id+"F4.wireOp",EDGE,"E26.15.0"),subQ65,subQ64])]})])],"derivedFrom":subQ9})])]}),makeQuery(id+"F47.opFillet","BLEND_FACE",FACE,{"disambiguationData":[OSD([subQ5,subQ7]),TDD([makeQuery(id+"F42.boolean.opBoolean","COPY",EDGE,{"disambiguationData":[TD([makeQuery(id+"F7.opLoft","SWEPT_FACE",FACE,{"disambiguationData":[OSD([sQuery(id+"F3.wireOp",EDGE,"E20.14.0"),subQ63,subQ62,sQuery(id+"F4.wireOp",EDGE,"E26.14.0"),subQ61,subQ60])]})])],"derivedFrom":subQ9})])]}),makeQuery(id+"F47.opFillet","BLEND_FACE",FACE,{"disambiguationData":[OSD([subQ5,subQ7]),TDD([makeQuery(id+"F42.boolean.opBoolean","COPY",EDGE,{"disambiguationData":[TD([makeQuery(id+"F8.opLoft","SWEPT_FACE",FACE,{"disambiguationData":[OSD([sQuery(id+"F3.wireOp",EDGE,"E20.13.0"),subQ59,subQ58,sQuery(id+"F4.wireOp",EDGE,"E26.13.0"),subQ57,subQ56])]})])],"derivedFrom":subQ9})])]}),makeQuery(id+"F47.opFillet","BLEND_FACE",FACE,{"disambiguationData":[OSD([subQ5,subQ7]),TDD([makeQuery(id+"F42.boolean.opBoolean","COPY",EDGE,{"disambiguationData":[TD([subQ55])],"derivedFrom":subQ9})])]}),makeQuery(id+"F47.opFillet","BLEND_FACE",FACE,{"disambiguationData":[OSD([subQ5,subQ7]),TDD([makeQuery(id+"F42.boolean.opBoolean","COPY",EDGE,{"disambiguationData":[TD([makeQuery(id+"F10.opLoft","SWEPT_FACE",FACE,{"disambiguationData":[OSD([sQuery(id+"F3.wireOp",EDGE,"E20.11.0"),subQ49,subQ48,sQuery(id+"F4.wireOp",EDGE,"E26.11.0"),subQ47,subQ46])]})])],"derivedFrom":subQ9})])]}),makeQuery(id+"F47.opFillet","BLEND_FACE",FACE,{"disambiguationData":[OSD([subQ5,subQ7]),TDD([makeQuery(id+"F42.boolean.opBoolean","COPY",EDGE,{"disambiguationData":[TD([makeQuery(id+"F11.opLoft","SWEPT_FACE",FACE,{"disambiguationData":[OSD([sQuery(id+"F3.wireOp",EDGE,"E20.10.0"),subQ45,subQ44,sQuery(id+"F4.wireOp",EDGE,"E26.10.0"),subQ43,subQ42])]})])],"derivedFrom":subQ9})])]}),makeQuery(id+"F47.opFillet","BLEND_FACE",FACE,{"disambiguationData":[OSD([subQ5,subQ7]),TDD([makeQuery(id+"F42.boolean.opBoolean","COPY",EDGE,{"disambiguationData":[TD([makeQuery(id+"F12.opLoft","SWEPT_FACE",FACE,{"disambiguationData":[OSD([sQuery(id+"F3.wireOp",EDGE,"E20.9.0"),subQ41,subQ40,sQuery(id+"F4.wireOp",EDGE,"E26.9.0"),subQ39,subQ38])]})])],"derivedFrom":subQ9})])]}),makeQuery(id+"F47.opFillet","BLEND_FACE",FACE,{"disambiguationData":[OSD([subQ5,subQ7]),TDD([makeQuery(id+"F42.boolean.opBoolean","COPY",EDGE,{"disambiguationData":[TD([makeQuery(id+"F13.opLoft","SWEPT_FACE",FACE,{"disambiguationData":[OSD([sQuery(id+"F3.wireOp",EDGE,"E20.8.0"),subQ37,subQ36,sQuery(id+"F4.wireOp",EDGE,"E26.8.0"),subQ35,subQ34])]})])],"derivedFrom":subQ9})])]}),makeQuery(id+"F47.opFillet","BLEND_FACE",FACE,{"disambiguationData":[OSD([subQ5,subQ7]),TDD([makeQuery(id+"F42.boolean.opBoolean","COPY",EDGE,{"disambiguationData":[TD([makeQuery(id+"F14.opLoft","SWEPT_FACE",FACE,{"disambiguationData":[OSD([sQuery(id+"F3.wireOp",EDGE,"E20.7.0"),subQ33,subQ32,sQuery(id+"F4.wireOp",EDGE,"E26.7.0"),subQ31,subQ30])]})])],"derivedFrom":subQ9})])]}),makeQuery(id+"F47.opFillet","BLEND_FACE",FACE,{"disambiguationData":[OSD([subQ5,subQ7]),TDD([makeQuery(id+"F42.boolean.opBoolean","COPY",EDGE,{"disambiguationData":[TD([makeQuery(id+"F15.opLoft","SWEPT_FACE",FACE,{"disambiguationData":[OSD([sQuery(id+"F3.wireOp",EDGE,"E20.6.0"),subQ29,subQ28,sQuery(id+"F4.wireOp",EDGE,"E26.6.0"),subQ27,subQ26])]})])],"derivedFrom":subQ9})])]}),makeQuery(id+"F47.opFillet","BLEND_FACE",FACE,{"disambiguationData":[OSD([subQ5,subQ7]),TDD([makeQuery(id+"F42.boolean.opBoolean","COPY",EDGE,{"disambiguationData":[TD([makeQuery(id+"F16.opLoft","SWEPT_FACE",FACE,{"disambiguationData":[OSD([sQuery(id+"F3.wireOp",EDGE,"E20.5.0"),subQ25,subQ24,sQuery(id+"F4.wireOp",EDGE,"E26.5.0"),subQ23,subQ22])]})])],"derivedFrom":subQ9})])]}),makeQuery(id+"F47.opFillet","BLEND_FACE",FACE,{"disambiguationData":[OSD([subQ5,subQ7]),TDD([makeQuery(id+"F42.boolean.opBoolean","COPY",EDGE,{"disambiguationData":[TD([makeQuery(id+"F17.opLoft","SWEPT_FACE",FACE,{"disambiguationData":[OSD([sQuery(id+"F3.wireOp",EDGE,"E20.4.0"),subQ21,subQ20,sQuery(id+"F4.wireOp",EDGE,"E26.4.0"),subQ19,subQ18])]})])],"derivedFrom":subQ9})])]}),makeQuery(id+"F47.opFillet","BLEND_FACE",FACE,{"disambiguationData":[OSD([subQ5,subQ7]),TDD([makeQuery(id+"F42.boolean.opBoolean","COPY",EDGE,{"disambiguationData":[TD([makeQuery(id+"F18.opLoft","SWEPT_FACE",FACE,{"disambiguationData":[OSD([sQuery(id+"F3.wireOp",EDGE,"E20.3.0"),subQ17,subQ16,sQuery(id+"F4.wireOp",EDGE,"E26.3.0"),subQ15,subQ14])]})])],"derivedFrom":subQ9})])]}),makeQuery(id+"F47.opFillet","BLEND_FACE",FACE,{"disambiguationData":[OSD([subQ5,subQ7]),TDD([makeQuery(id+"F42.boolean.opBoolean","COPY",EDGE,{"disambiguationData":[TD([makeQuery(id+"F19.opLoft","SWEPT_FACE",FACE,{"disambiguationData":[OSD([sQuery(id+"F3.wireOp",EDGE,"E20.2.0"),subQ13,subQ12,sQuery(id+"F4.wireOp",EDGE,"E26.2.0"),subQ11,subQ10])]})])],"derivedFrom":subQ9})])]}),makeQuery(id+"F47.opFillet","BLEND_FACE",FACE,{"disambiguationData":[OSD([subQ5,subQ7]),TDD([makeQuery(id+"F42.boolean.opBoolean","COPY",EDGE,{"disambiguationData":[TD([makeQuery(id+"F20.opLoft","SWEPT_FACE",FACE,{"disambiguationData":[OSD([sQuery(id+"F3.wireOp",EDGE,"E20.1.0"),subQ4,subQ3,sQuery(id+"F4.wireOp",EDGE,"E26.1.0"),subQ2,subQ1])]})])],"derivedFrom":subQ9})])]})],"blendedInto":[makeQuery(id+"F47.opFillet","BLEND_FACE",FACE,{"disambiguationData":[OSD([subQ5,subQ7]),TDD([makeQuery(id+"F42.boolean.opBoolean","COPY",EDGE,{"disambiguationData":[TD([makeQuery(id+"F5.opLoft","SWEPT_FACE",FACE,{"disambiguationData":[OSD([subQ71,subQ70,sQuery(id+"F3.wireOp",EDGE,"E18.left"),sQuery(id+"F4.wireOp",EDGE,"E21"),subQ69,subQ68])]})])],"derivedFrom":subQ9})])]}),makeQuery(id+"F47.opFillet","BLEND_FACE",FACE,{"disambiguationData":[OSD([subQ5,subQ7]),TDD([makeQuery(id+"F42.boolean.opBoolean","COPY",EDGE,{"disambiguationData":[TD([makeQuery(id+"F6.opLoft","SWEPT_FACE",FACE,{"disambiguationData":[OSD([sQuery(id+"F3.wireOp",EDGE,"E20.15.0"),subQ67,subQ66,sQuery(id+"F4.wireOp",EDGE,"E26.15.0"),subQ65,subQ64])]})])],"derivedFrom":subQ9})])]}),makeQuery(id+"F47.opFillet","BLEND_FACE",FACE,{"disambiguationData":[OSD([subQ5,subQ7]),TDD([makeQuery(id+"F42.boolean.opBoolean","COPY",EDGE,{"disambiguationData":[TD([makeQuery(id+"F7.opLoft","SWEPT_FACE",FACE,{"disambiguationData":[OSD([sQuery(id+"F3.wireOp",EDGE,"E20.14.0"),subQ63,subQ62,sQuery(id+"F4.wireOp",EDGE,"E26.14.0"),subQ61,subQ60])]})])],"derivedFrom":subQ9})])]}),makeQuery(id+"F47.opFillet","BLEND_FACE",FACE,{"disambiguationData":[OSD([subQ5,subQ7]),TDD([makeQuery(id+"F42.boolean.opBoolean","COPY",EDGE,{"disambiguationData":[TD([makeQuery(id+"F8.opLoft","SWEPT_FACE",FACE,{"disambiguationData":[OSD([sQuery(id+"F3.wireOp",EDGE,"E20.13.0"),subQ59,subQ58,sQuery(id+"F4.wireOp",EDGE,"E26.13.0"),subQ57,subQ56])]})])],"derivedFrom":subQ9})])]}),makeQuery(id+"F47.opFillet","BLEND_FACE",FACE,{"disambiguationData":[OSD([subQ5,subQ7]),TDD([makeQuery(id+"F42.boolean.opBoolean","COPY",EDGE,{"disambiguationData":[TD([subQ55])],"derivedFrom":subQ9})])]}),makeQuery(id+"F47.opFillet","BLEND_FACE",FACE,{"disambiguationData":[OSD([subQ5,subQ7]),TDD([makeQuery(id+"F42.boolean.opBoolean","COPY",EDGE,{"disambiguationData":[TD([makeQuery(id+"F10.opLoft","SWEPT_FACE",FACE,{"disambiguationData":[OSD([sQuery(id+"F3.wireOp",EDGE,"E20.11.0"),subQ49,subQ48,sQuery(id+"F4.wireOp",EDGE,"E26.11.0"),subQ47,subQ46])]})])],"derivedFrom":subQ9})])]}),makeQuery(id+"F47.opFillet","BLEND_FACE",FACE,{"disambiguationData":[OSD([subQ5,subQ7]),TDD([makeQuery(id+"F42.boolean.opBoolean","COPY",EDGE,{"disambiguationData":[TD([makeQuery(id+"F11.opLoft","SWEPT_FACE",FACE,{"disambiguationData":[OSD([sQuery(id+"F3.wireOp",EDGE,"E20.10.0"),subQ45,subQ44,sQuery(id+"F4.wireOp",EDGE,"E26.10.0"),subQ43,subQ42])]})])],"derivedFrom":subQ9})])]}),makeQuery(id+"F47.opFillet","BLEND_FACE",FACE,{"disambiguationData":[OSD([subQ5,subQ7]),TDD([makeQuery(id+"F42.boolean.opBoolean","COPY",EDGE,{"disambiguationData":[TD([makeQuery(id+"F12.opLoft","SWEPT_FACE",FACE,{"disambiguationData":[OSD([sQuery(id+"F3.wireOp",EDGE,"E20.9.0"),subQ41,subQ40,sQuery(id+"F4.wireOp",EDGE,"E26.9.0"),subQ39,subQ38])]})])],"derivedFrom":subQ9})])]}),makeQuery(id+"F47.opFillet","BLEND_FACE",FACE,{"disambiguationData":[OSD([subQ5,subQ7]),TDD([makeQuery(id+"F42.boolean.opBoolean","COPY",EDGE,{"disambiguationData":[TD([makeQuery(id+"F13.opLoft","SWEPT_FACE",FACE,{"disambiguationData":[OSD([sQuery(id+"F3.wireOp",EDGE,"E20.8.0"),subQ37,subQ36,sQuery(id+"F4.wireOp",EDGE,"E26.8.0"),subQ35,subQ34])]})])],"derivedFrom":subQ9})])]}),makeQuery(id+"F47.opFillet","BLEND_FACE",FACE,{"disambiguationData":[OSD([subQ5,subQ7]),TDD([makeQuery(id+"F42.boolean.opBoolean","COPY",EDGE,{"disambiguationData":[TD([makeQuery(id+"F14.opLoft","SWEPT_FACE",FACE,{"disambiguationData":[OSD([sQuery(id+"F3.wireOp",EDGE,"E20.7.0"),subQ33,subQ32,sQuery(id+"F4.wireOp",EDGE,"E26.7.0"),subQ31,subQ30])]})])],"derivedFrom":subQ9})])]}),makeQuery(id+"F47.opFillet","BLEND_FACE",FACE,{"disambiguationData":[OSD([subQ5,subQ7]),TDD([makeQuery(id+"F42.boolean.opBoolean","COPY",EDGE,{"disambiguationData":[TD([makeQuery(id+"F15.opLoft","SWEPT_FACE",FACE,{"disambiguationData":[OSD([sQuery(id+"F3.wireOp",EDGE,"E20.6.0"),subQ29,subQ28,sQuery(id+"F4.wireOp",EDGE,"E26.6.0"),subQ27,subQ26])]})])],"derivedFrom":subQ9})])]}),makeQuery(id+"F47.opFillet","BLEND_FACE",FACE,{"disambiguationData":[OSD([subQ5,subQ7]),TDD([makeQuery(id+"F42.boolean.opBoolean","COPY",EDGE,{"disambiguationData":[TD([makeQuery(id+"F16.opLoft","SWEPT_FACE",FACE,{"disambiguationData":[OSD([sQuery(id+"F3.wireOp",EDGE,"E20.5.0"),subQ25,subQ24,sQuery(id+"F4.wireOp",EDGE,"E26.5.0"),subQ23,subQ22])]})])],"derivedFrom":subQ9})])]}),makeQuery(id+"F47.opFillet","BLEND_FACE",FACE,{"disambiguationData":[OSD([subQ5,subQ7]),TDD([makeQuery(id+"F42.boolean.opBoolean","COPY",EDGE,{"disambiguationData":[TD([makeQuery(id+"F17.opLoft","SWEPT_FACE",FACE,{"disambiguationData":[OSD([sQuery(id+"F3.wireOp",EDGE,"E20.4.0"),subQ21,subQ20,sQuery(id+"F4.wireOp",EDGE,"E26.4.0"),subQ19,subQ18])]})])],"derivedFrom":subQ9})])]}),makeQuery(id+"F47.opFillet","BLEND_FACE",FACE,{"disambiguationData":[OSD([subQ5,subQ7]),TDD([makeQuery(id+"F42.boolean.opBoolean","COPY",EDGE,{"disambiguationData":[TD([makeQuery(id+"F18.opLoft","SWEPT_FACE",FACE,{"disambiguationData":[OSD([sQuery(id+"F3.wireOp",EDGE,"E20.3.0"),subQ17,subQ16,sQuery(id+"F4.wireOp",EDGE,"E26.3.0"),subQ15,subQ14])]})])],"derivedFrom":subQ9})])]}),makeQuery(id+"F47.opFillet","BLEND_FACE",FACE,{"disambiguationData":[OSD([subQ5,subQ7]),TDD([makeQuery(id+"F42.boolean.opBoolean","COPY",EDGE,{"disambiguationData":[TD([makeQuery(id+"F19.opLoft","SWEPT_FACE",FACE,{"disambiguationData":[OSD([sQuery(id+"F3.wireOp",EDGE,"E20.2.0"),subQ13,subQ12,sQuery(id+"F4.wireOp",EDGE,"E26.2.0"),subQ11,subQ10])]})])],"derivedFrom":subQ9})])]}),makeQuery(id+"F47.opFillet","BLEND_FACE",FACE,{"disambiguationData":[OSD([subQ5,subQ7]),TDD([makeQuery(id+"F42.boolean.opBoolean","COPY",EDGE,{"disambiguationData":[TD([makeQuery(id+"F20.opLoft","SWEPT_FACE",FACE,{"disambiguationData":[OSD([sQuery(id+"F3.wireOp",EDGE,"E20.1.0"),subQ4,subQ3,sQuery(id+"F4.wireOp",EDGE,"E26.1.0"),subQ2,subQ1])]})])],"derivedFrom":subQ9})])]})]});}
            var Q59;
            {var subQ0=makeQuery(id+"F40.opExtrude","CAP_FACE",FACE,{"disambiguationData":[OSD([sQuery(id+"F39.wireOp",EDGE,"E29"),sQuery(id+"F39.wireOp",EDGE,"E30")])],"isStart":false});var subQ1=sQuery(id+"F4.wireOp",EDGE,"E26.1.3");var subQ2=sQuery(id+"F4.wireOp",EDGE,"E26.1.2");var subQ3=sQuery(id+"F3.wireOp",EDGE,"E20.1.3");var subQ4=sQuery(id+"F3.wireOp",EDGE,"E20.1.1");var subQ5=sQuery(id+"F41.wireOp",EDGE,"E35");var subQ6=makeQuery(id+"F42.opRevolve","SWEPT_FACE",FACE,{"disambiguationData":[OSD([subQ5])]});var subQ7=sQuery(id+"F41.wireOp",EDGE,"E36");var subQ8=makeQuery(id+"F42.opRevolve","SWEPT_FACE",FACE,{"disambiguationData":[OSD([subQ7])]});var subQ9=makeQuery(id+"F42.opRevolve","SWEPT_EDGE",EDGE,{"disambiguationData":[OSD([subQ5,subQ7])]});var subQ10=sQuery(id+"F4.wireOp",EDGE,"E26.2.3");var subQ11=sQuery(id+"F4.wireOp",EDGE,"E26.2.2");var subQ12=sQuery(id+"F3.wireOp",EDGE,"E20.2.3");var subQ13=sQuery(id+"F3.wireOp",EDGE,"E20.2.1");var subQ14=sQuery(id+"F4.wireOp",EDGE,"E26.3.3");var subQ15=sQuery(id+"F4.wireOp",EDGE,"E26.3.2");var subQ16=sQuery(id+"F3.wireOp",EDGE,"E20.3.3");var subQ17=sQuery(id+"F3.wireOp",EDGE,"E20.3.1");var subQ18=sQuery(id+"F4.wireOp",EDGE,"E26.4.3");var subQ19=sQuery(id+"F4.wireOp",EDGE,"E26.4.2");var subQ20=sQuery(id+"F3.wireOp",EDGE,"E20.4.3");var subQ21=sQuery(id+"F3.wireOp",EDGE,"E20.4.1");var subQ22=sQuery(id+"F4.wireOp",EDGE,"E26.5.3");var subQ23=sQuery(id+"F4.wireOp",EDGE,"E26.5.2");var subQ24=sQuery(id+"F3.wireOp",EDGE,"E20.5.3");var subQ25=sQuery(id+"F3.wireOp",EDGE,"E20.5.1");var subQ26=sQuery(id+"F4.wireOp",EDGE,"E26.6.3");var subQ27=sQuery(id+"F4.wireOp",EDGE,"E26.6.2");var subQ28=sQuery(id+"F3.wireOp",EDGE,"E20.6.3");var subQ29=sQuery(id+"F3.wireOp",EDGE,"E20.6.1");var subQ30=sQuery(id+"F4.wireOp",EDGE,"E26.7.3");var subQ31=sQuery(id+"F4.wireOp",EDGE,"E26.7.2");var subQ32=sQuery(id+"F3.wireOp",EDGE,"E20.7.3");var subQ33=sQuery(id+"F3.wireOp",EDGE,"E20.7.1");var subQ34=sQuery(id+"F4.wireOp",EDGE,"E26.8.3");var subQ35=sQuery(id+"F4.wireOp",EDGE,"E26.8.2");var subQ36=sQuery(id+"F3.wireOp",EDGE,"E20.8.3");var subQ37=sQuery(id+"F3.wireOp",EDGE,"E20.8.1");var subQ38=sQuery(id+"F4.wireOp",EDGE,"E26.9.3");var subQ39=sQuery(id+"F4.wireOp",EDGE,"E26.9.2");var subQ40=sQuery(id+"F3.wireOp",EDGE,"E20.9.3");var subQ41=sQuery(id+"F3.wireOp",EDGE,"E20.9.1");var subQ42=sQuery(id+"F4.wireOp",EDGE,"E26.10.3");var subQ43=sQuery(id+"F4.wireOp",EDGE,"E26.10.2");var subQ44=sQuery(id+"F3.wireOp",EDGE,"E20.10.3");var subQ45=sQuery(id+"F3.wireOp",EDGE,"E20.10.1");var subQ46=sQuery(id+"F4.wireOp",EDGE,"E26.11.3");var subQ47=sQuery(id+"F4.wireOp",EDGE,"E26.11.2");var subQ48=sQuery(id+"F3.wireOp",EDGE,"E20.11.3");var subQ49=sQuery(id+"F3.wireOp",EDGE,"E20.11.1");var subQ51=makeQuery(id+"F10.opLoft","SWEPT_FACE",FACE,{"disambiguationData":[OSD([sQuery(id+"F3.wireOp",EDGE,"E20.11.0"),subQ49,subQ48,sQuery(id+"F4.wireOp",EDGE,"E26.11.0"),subQ47,subQ46])]});var subQ52=sQuery(id+"F4.wireOp",EDGE,"E26.12.3");var subQ53=sQuery(id+"F4.wireOp",EDGE,"E26.12.2");var subQ54=sQuery(id+"F3.wireOp",EDGE,"E20.12.3");var subQ55=sQuery(id+"F3.wireOp",EDGE,"E20.12.1");var subQ56=sQuery(id+"F4.wireOp",EDGE,"E26.13.3");var subQ57=sQuery(id+"F4.wireOp",EDGE,"E26.13.2");var subQ58=sQuery(id+"F3.wireOp",EDGE,"E20.13.3");var subQ59=sQuery(id+"F3.wireOp",EDGE,"E20.13.1");var subQ60=sQuery(id+"F4.wireOp",EDGE,"E26.14.3");var subQ61=sQuery(id+"F4.wireOp",EDGE,"E26.14.2");var subQ62=sQuery(id+"F3.wireOp",EDGE,"E20.14.3");var subQ63=sQuery(id+"F3.wireOp",EDGE,"E20.14.1");var subQ64=sQuery(id+"F4.wireOp",EDGE,"E26.15.3");var subQ65=sQuery(id+"F4.wireOp",EDGE,"E26.15.2");var subQ66=sQuery(id+"F3.wireOp",EDGE,"E20.15.3");var subQ67=sQuery(id+"F3.wireOp",EDGE,"E20.15.1");var subQ68=sQuery(id+"F4.wireOp",EDGE,"E23");var subQ69=sQuery(id+"F4.wireOp",EDGE,"E22");var subQ70=sQuery(id+"F3.wireOp",EDGE,"E18.top");var subQ71=sQuery(id+"F3.wireOp",EDGE,"E18.bottom");var subQ74=makeQuery(id+"F42.boolean.opBoolean","COPY",FACE,{"disambiguationData":[TD([subQ51])],"derivedFrom":subQ6});var subQ75=makeQuery(id+"F10.boolean.opBoolean","INTERSECT",EDGE,{"derivedFrom":[makeQuery(id+"F1.opRevolve","SWEPT_FACE",FACE,{"disambiguationData":[OSD([sQuery(id+"F0.wireOp",EDGE,"E4")])]}),subQ51]});Q59=makeQuery(id+"F48.opFillet","BLEND_EDGE",EDGE,{"blendedFrom":[makeQuery(id+"F47.opFillet","TWEAK_EDGE",EDGE,{"derivedFrom":[makeQuery(id+"F45.opFillet","BLEND_VERTEX",VERTEX,{"blendedFrom":[subQ75,subQ51,subQ74],"blendedInto":[subQ51,subQ74]}),makeQuery(id+"F45.opFillet","BLEND_VERTEX",VERTEX,{"blendedFrom":[subQ75,makeQuery(id+"F42.boolean.opBoolean","MERGE",FACE,{"derivedFrom":[subQ0,subQ8]}),subQ74],"blendedInto":[makeQuery(id+"F42.boolean.opBoolean","MERGE",FACE,{"derivedFrom":[subQ0,subQ8]}),subQ74]})]}),makeQuery(id+"F47.opFillet","BLEND_FACE",FACE,{"disambiguationData":[OSD([subQ5,subQ7]),TDD([makeQuery(id+"F42.boolean.opBoolean","COPY",EDGE,{"disambiguationData":[TD([makeQuery(id+"F5.opLoft","SWEPT_FACE",FACE,{"disambiguationData":[OSD([subQ71,subQ70,sQuery(id+"F3.wireOp",EDGE,"E18.left"),sQuery(id+"F4.wireOp",EDGE,"E21"),subQ69,subQ68])]})])],"derivedFrom":subQ9})])]}),makeQuery(id+"F47.opFillet","BLEND_FACE",FACE,{"disambiguationData":[OSD([subQ5,subQ7]),TDD([makeQuery(id+"F42.boolean.opBoolean","COPY",EDGE,{"disambiguationData":[TD([makeQuery(id+"F6.opLoft","SWEPT_FACE",FACE,{"disambiguationData":[OSD([sQuery(id+"F3.wireOp",EDGE,"E20.15.0"),subQ67,subQ66,sQuery(id+"F4.wireOp",EDGE,"E26.15.0"),subQ65,subQ64])]})])],"derivedFrom":subQ9})])]}),makeQuery(id+"F47.opFillet","BLEND_FACE",FACE,{"disambiguationData":[OSD([subQ5,subQ7]),TDD([makeQuery(id+"F42.boolean.opBoolean","COPY",EDGE,{"disambiguationData":[TD([makeQuery(id+"F7.opLoft","SWEPT_FACE",FACE,{"disambiguationData":[OSD([sQuery(id+"F3.wireOp",EDGE,"E20.14.0"),subQ63,subQ62,sQuery(id+"F4.wireOp",EDGE,"E26.14.0"),subQ61,subQ60])]})])],"derivedFrom":subQ9})])]}),makeQuery(id+"F47.opFillet","BLEND_FACE",FACE,{"disambiguationData":[OSD([subQ5,subQ7]),TDD([makeQuery(id+"F42.boolean.opBoolean","COPY",EDGE,{"disambiguationData":[TD([makeQuery(id+"F8.opLoft","SWEPT_FACE",FACE,{"disambiguationData":[OSD([sQuery(id+"F3.wireOp",EDGE,"E20.13.0"),subQ59,subQ58,sQuery(id+"F4.wireOp",EDGE,"E26.13.0"),subQ57,subQ56])]})])],"derivedFrom":subQ9})])]}),makeQuery(id+"F47.opFillet","BLEND_FACE",FACE,{"disambiguationData":[OSD([subQ5,subQ7]),TDD([makeQuery(id+"F42.boolean.opBoolean","COPY",EDGE,{"disambiguationData":[TD([makeQuery(id+"F9.opLoft","SWEPT_FACE",FACE,{"disambiguationData":[OSD([sQuery(id+"F3.wireOp",EDGE,"E20.12.0"),subQ55,subQ54,sQuery(id+"F4.wireOp",EDGE,"E26.12.0"),subQ53,subQ52])]})])],"derivedFrom":subQ9})])]}),makeQuery(id+"F47.opFillet","BLEND_FACE",FACE,{"disambiguationData":[OSD([subQ5,subQ7]),TDD([makeQuery(id+"F42.boolean.opBoolean","COPY",EDGE,{"disambiguationData":[TD([subQ51])],"derivedFrom":subQ9})])]}),makeQuery(id+"F47.opFillet","BLEND_FACE",FACE,{"disambiguationData":[OSD([subQ5,subQ7]),TDD([makeQuery(id+"F42.boolean.opBoolean","COPY",EDGE,{"disambiguationData":[TD([makeQuery(id+"F11.opLoft","SWEPT_FACE",FACE,{"disambiguationData":[OSD([sQuery(id+"F3.wireOp",EDGE,"E20.10.0"),subQ45,subQ44,sQuery(id+"F4.wireOp",EDGE,"E26.10.0"),subQ43,subQ42])]})])],"derivedFrom":subQ9})])]}),makeQuery(id+"F47.opFillet","BLEND_FACE",FACE,{"disambiguationData":[OSD([subQ5,subQ7]),TDD([makeQuery(id+"F42.boolean.opBoolean","COPY",EDGE,{"disambiguationData":[TD([makeQuery(id+"F12.opLoft","SWEPT_FACE",FACE,{"disambiguationData":[OSD([sQuery(id+"F3.wireOp",EDGE,"E20.9.0"),subQ41,subQ40,sQuery(id+"F4.wireOp",EDGE,"E26.9.0"),subQ39,subQ38])]})])],"derivedFrom":subQ9})])]}),makeQuery(id+"F47.opFillet","BLEND_FACE",FACE,{"disambiguationData":[OSD([subQ5,subQ7]),TDD([makeQuery(id+"F42.boolean.opBoolean","COPY",EDGE,{"disambiguationData":[TD([makeQuery(id+"F13.opLoft","SWEPT_FACE",FACE,{"disambiguationData":[OSD([sQuery(id+"F3.wireOp",EDGE,"E20.8.0"),subQ37,subQ36,sQuery(id+"F4.wireOp",EDGE,"E26.8.0"),subQ35,subQ34])]})])],"derivedFrom":subQ9})])]}),makeQuery(id+"F47.opFillet","BLEND_FACE",FACE,{"disambiguationData":[OSD([subQ5,subQ7]),TDD([makeQuery(id+"F42.boolean.opBoolean","COPY",EDGE,{"disambiguationData":[TD([makeQuery(id+"F14.opLoft","SWEPT_FACE",FACE,{"disambiguationData":[OSD([sQuery(id+"F3.wireOp",EDGE,"E20.7.0"),subQ33,subQ32,sQuery(id+"F4.wireOp",EDGE,"E26.7.0"),subQ31,subQ30])]})])],"derivedFrom":subQ9})])]}),makeQuery(id+"F47.opFillet","BLEND_FACE",FACE,{"disambiguationData":[OSD([subQ5,subQ7]),TDD([makeQuery(id+"F42.boolean.opBoolean","COPY",EDGE,{"disambiguationData":[TD([makeQuery(id+"F15.opLoft","SWEPT_FACE",FACE,{"disambiguationData":[OSD([sQuery(id+"F3.wireOp",EDGE,"E20.6.0"),subQ29,subQ28,sQuery(id+"F4.wireOp",EDGE,"E26.6.0"),subQ27,subQ26])]})])],"derivedFrom":subQ9})])]}),makeQuery(id+"F47.opFillet","BLEND_FACE",FACE,{"disambiguationData":[OSD([subQ5,subQ7]),TDD([makeQuery(id+"F42.boolean.opBoolean","COPY",EDGE,{"disambiguationData":[TD([makeQuery(id+"F16.opLoft","SWEPT_FACE",FACE,{"disambiguationData":[OSD([sQuery(id+"F3.wireOp",EDGE,"E20.5.0"),subQ25,subQ24,sQuery(id+"F4.wireOp",EDGE,"E26.5.0"),subQ23,subQ22])]})])],"derivedFrom":subQ9})])]}),makeQuery(id+"F47.opFillet","BLEND_FACE",FACE,{"disambiguationData":[OSD([subQ5,subQ7]),TDD([makeQuery(id+"F42.boolean.opBoolean","COPY",EDGE,{"disambiguationData":[TD([makeQuery(id+"F17.opLoft","SWEPT_FACE",FACE,{"disambiguationData":[OSD([sQuery(id+"F3.wireOp",EDGE,"E20.4.0"),subQ21,subQ20,sQuery(id+"F4.wireOp",EDGE,"E26.4.0"),subQ19,subQ18])]})])],"derivedFrom":subQ9})])]}),makeQuery(id+"F47.opFillet","BLEND_FACE",FACE,{"disambiguationData":[OSD([subQ5,subQ7]),TDD([makeQuery(id+"F42.boolean.opBoolean","COPY",EDGE,{"disambiguationData":[TD([makeQuery(id+"F18.opLoft","SWEPT_FACE",FACE,{"disambiguationData":[OSD([sQuery(id+"F3.wireOp",EDGE,"E20.3.0"),subQ17,subQ16,sQuery(id+"F4.wireOp",EDGE,"E26.3.0"),subQ15,subQ14])]})])],"derivedFrom":subQ9})])]}),makeQuery(id+"F47.opFillet","BLEND_FACE",FACE,{"disambiguationData":[OSD([subQ5,subQ7]),TDD([makeQuery(id+"F42.boolean.opBoolean","COPY",EDGE,{"disambiguationData":[TD([makeQuery(id+"F19.opLoft","SWEPT_FACE",FACE,{"disambiguationData":[OSD([sQuery(id+"F3.wireOp",EDGE,"E20.2.0"),subQ13,subQ12,sQuery(id+"F4.wireOp",EDGE,"E26.2.0"),subQ11,subQ10])]})])],"derivedFrom":subQ9})])]}),makeQuery(id+"F47.opFillet","BLEND_FACE",FACE,{"disambiguationData":[OSD([subQ5,subQ7]),TDD([makeQuery(id+"F42.boolean.opBoolean","COPY",EDGE,{"disambiguationData":[TD([makeQuery(id+"F20.opLoft","SWEPT_FACE",FACE,{"disambiguationData":[OSD([sQuery(id+"F3.wireOp",EDGE,"E20.1.0"),subQ4,subQ3,sQuery(id+"F4.wireOp",EDGE,"E26.1.0"),subQ2,subQ1])]})])],"derivedFrom":subQ9})])]})],"blendedInto":[makeQuery(id+"F47.opFillet","BLEND_FACE",FACE,{"disambiguationData":[OSD([subQ5,subQ7]),TDD([makeQuery(id+"F42.boolean.opBoolean","COPY",EDGE,{"disambiguationData":[TD([makeQuery(id+"F5.opLoft","SWEPT_FACE",FACE,{"disambiguationData":[OSD([subQ71,subQ70,sQuery(id+"F3.wireOp",EDGE,"E18.left"),sQuery(id+"F4.wireOp",EDGE,"E21"),subQ69,subQ68])]})])],"derivedFrom":subQ9})])]}),makeQuery(id+"F47.opFillet","BLEND_FACE",FACE,{"disambiguationData":[OSD([subQ5,subQ7]),TDD([makeQuery(id+"F42.boolean.opBoolean","COPY",EDGE,{"disambiguationData":[TD([makeQuery(id+"F6.opLoft","SWEPT_FACE",FACE,{"disambiguationData":[OSD([sQuery(id+"F3.wireOp",EDGE,"E20.15.0"),subQ67,subQ66,sQuery(id+"F4.wireOp",EDGE,"E26.15.0"),subQ65,subQ64])]})])],"derivedFrom":subQ9})])]}),makeQuery(id+"F47.opFillet","BLEND_FACE",FACE,{"disambiguationData":[OSD([subQ5,subQ7]),TDD([makeQuery(id+"F42.boolean.opBoolean","COPY",EDGE,{"disambiguationData":[TD([makeQuery(id+"F7.opLoft","SWEPT_FACE",FACE,{"disambiguationData":[OSD([sQuery(id+"F3.wireOp",EDGE,"E20.14.0"),subQ63,subQ62,sQuery(id+"F4.wireOp",EDGE,"E26.14.0"),subQ61,subQ60])]})])],"derivedFrom":subQ9})])]}),makeQuery(id+"F47.opFillet","BLEND_FACE",FACE,{"disambiguationData":[OSD([subQ5,subQ7]),TDD([makeQuery(id+"F42.boolean.opBoolean","COPY",EDGE,{"disambiguationData":[TD([makeQuery(id+"F8.opLoft","SWEPT_FACE",FACE,{"disambiguationData":[OSD([sQuery(id+"F3.wireOp",EDGE,"E20.13.0"),subQ59,subQ58,sQuery(id+"F4.wireOp",EDGE,"E26.13.0"),subQ57,subQ56])]})])],"derivedFrom":subQ9})])]}),makeQuery(id+"F47.opFillet","BLEND_FACE",FACE,{"disambiguationData":[OSD([subQ5,subQ7]),TDD([makeQuery(id+"F42.boolean.opBoolean","COPY",EDGE,{"disambiguationData":[TD([makeQuery(id+"F9.opLoft","SWEPT_FACE",FACE,{"disambiguationData":[OSD([sQuery(id+"F3.wireOp",EDGE,"E20.12.0"),subQ55,subQ54,sQuery(id+"F4.wireOp",EDGE,"E26.12.0"),subQ53,subQ52])]})])],"derivedFrom":subQ9})])]}),makeQuery(id+"F47.opFillet","BLEND_FACE",FACE,{"disambiguationData":[OSD([subQ5,subQ7]),TDD([makeQuery(id+"F42.boolean.opBoolean","COPY",EDGE,{"disambiguationData":[TD([subQ51])],"derivedFrom":subQ9})])]}),makeQuery(id+"F47.opFillet","BLEND_FACE",FACE,{"disambiguationData":[OSD([subQ5,subQ7]),TDD([makeQuery(id+"F42.boolean.opBoolean","COPY",EDGE,{"disambiguationData":[TD([makeQuery(id+"F11.opLoft","SWEPT_FACE",FACE,{"disambiguationData":[OSD([sQuery(id+"F3.wireOp",EDGE,"E20.10.0"),subQ45,subQ44,sQuery(id+"F4.wireOp",EDGE,"E26.10.0"),subQ43,subQ42])]})])],"derivedFrom":subQ9})])]}),makeQuery(id+"F47.opFillet","BLEND_FACE",FACE,{"disambiguationData":[OSD([subQ5,subQ7]),TDD([makeQuery(id+"F42.boolean.opBoolean","COPY",EDGE,{"disambiguationData":[TD([makeQuery(id+"F12.opLoft","SWEPT_FACE",FACE,{"disambiguationData":[OSD([sQuery(id+"F3.wireOp",EDGE,"E20.9.0"),subQ41,subQ40,sQuery(id+"F4.wireOp",EDGE,"E26.9.0"),subQ39,subQ38])]})])],"derivedFrom":subQ9})])]}),makeQuery(id+"F47.opFillet","BLEND_FACE",FACE,{"disambiguationData":[OSD([subQ5,subQ7]),TDD([makeQuery(id+"F42.boolean.opBoolean","COPY",EDGE,{"disambiguationData":[TD([makeQuery(id+"F13.opLoft","SWEPT_FACE",FACE,{"disambiguationData":[OSD([sQuery(id+"F3.wireOp",EDGE,"E20.8.0"),subQ37,subQ36,sQuery(id+"F4.wireOp",EDGE,"E26.8.0"),subQ35,subQ34])]})])],"derivedFrom":subQ9})])]}),makeQuery(id+"F47.opFillet","BLEND_FACE",FACE,{"disambiguationData":[OSD([subQ5,subQ7]),TDD([makeQuery(id+"F42.boolean.opBoolean","COPY",EDGE,{"disambiguationData":[TD([makeQuery(id+"F14.opLoft","SWEPT_FACE",FACE,{"disambiguationData":[OSD([sQuery(id+"F3.wireOp",EDGE,"E20.7.0"),subQ33,subQ32,sQuery(id+"F4.wireOp",EDGE,"E26.7.0"),subQ31,subQ30])]})])],"derivedFrom":subQ9})])]}),makeQuery(id+"F47.opFillet","BLEND_FACE",FACE,{"disambiguationData":[OSD([subQ5,subQ7]),TDD([makeQuery(id+"F42.boolean.opBoolean","COPY",EDGE,{"disambiguationData":[TD([makeQuery(id+"F15.opLoft","SWEPT_FACE",FACE,{"disambiguationData":[OSD([sQuery(id+"F3.wireOp",EDGE,"E20.6.0"),subQ29,subQ28,sQuery(id+"F4.wireOp",EDGE,"E26.6.0"),subQ27,subQ26])]})])],"derivedFrom":subQ9})])]}),makeQuery(id+"F47.opFillet","BLEND_FACE",FACE,{"disambiguationData":[OSD([subQ5,subQ7]),TDD([makeQuery(id+"F42.boolean.opBoolean","COPY",EDGE,{"disambiguationData":[TD([makeQuery(id+"F16.opLoft","SWEPT_FACE",FACE,{"disambiguationData":[OSD([sQuery(id+"F3.wireOp",EDGE,"E20.5.0"),subQ25,subQ24,sQuery(id+"F4.wireOp",EDGE,"E26.5.0"),subQ23,subQ22])]})])],"derivedFrom":subQ9})])]}),makeQuery(id+"F47.opFillet","BLEND_FACE",FACE,{"disambiguationData":[OSD([subQ5,subQ7]),TDD([makeQuery(id+"F42.boolean.opBoolean","COPY",EDGE,{"disambiguationData":[TD([makeQuery(id+"F17.opLoft","SWEPT_FACE",FACE,{"disambiguationData":[OSD([sQuery(id+"F3.wireOp",EDGE,"E20.4.0"),subQ21,subQ20,sQuery(id+"F4.wireOp",EDGE,"E26.4.0"),subQ19,subQ18])]})])],"derivedFrom":subQ9})])]}),makeQuery(id+"F47.opFillet","BLEND_FACE",FACE,{"disambiguationData":[OSD([subQ5,subQ7]),TDD([makeQuery(id+"F42.boolean.opBoolean","COPY",EDGE,{"disambiguationData":[TD([makeQuery(id+"F18.opLoft","SWEPT_FACE",FACE,{"disambiguationData":[OSD([sQuery(id+"F3.wireOp",EDGE,"E20.3.0"),subQ17,subQ16,sQuery(id+"F4.wireOp",EDGE,"E26.3.0"),subQ15,subQ14])]})])],"derivedFrom":subQ9})])]}),makeQuery(id+"F47.opFillet","BLEND_FACE",FACE,{"disambiguationData":[OSD([subQ5,subQ7]),TDD([makeQuery(id+"F42.boolean.opBoolean","COPY",EDGE,{"disambiguationData":[TD([makeQuery(id+"F19.opLoft","SWEPT_FACE",FACE,{"disambiguationData":[OSD([sQuery(id+"F3.wireOp",EDGE,"E20.2.0"),subQ13,subQ12,sQuery(id+"F4.wireOp",EDGE,"E26.2.0"),subQ11,subQ10])]})])],"derivedFrom":subQ9})])]}),makeQuery(id+"F47.opFillet","BLEND_FACE",FACE,{"disambiguationData":[OSD([subQ5,subQ7]),TDD([makeQuery(id+"F42.boolean.opBoolean","COPY",EDGE,{"disambiguationData":[TD([makeQuery(id+"F20.opLoft","SWEPT_FACE",FACE,{"disambiguationData":[OSD([sQuery(id+"F3.wireOp",EDGE,"E20.1.0"),subQ4,subQ3,sQuery(id+"F4.wireOp",EDGE,"E26.1.0"),subQ2,subQ1])]})])],"derivedFrom":subQ9})])]})]});}
            var Q60;
            {var subQ0=makeQuery(id+"F40.opExtrude","CAP_FACE",FACE,{"disambiguationData":[OSD([sQuery(id+"F39.wireOp",EDGE,"E29"),sQuery(id+"F39.wireOp",EDGE,"E30")])],"isStart":false});var subQ1=sQuery(id+"F4.wireOp",EDGE,"E26.1.3");var subQ2=sQuery(id+"F4.wireOp",EDGE,"E26.1.2");var subQ3=sQuery(id+"F3.wireOp",EDGE,"E20.1.3");var subQ4=sQuery(id+"F3.wireOp",EDGE,"E20.1.1");var subQ5=sQuery(id+"F41.wireOp",EDGE,"E35");var subQ6=makeQuery(id+"F42.opRevolve","SWEPT_FACE",FACE,{"disambiguationData":[OSD([subQ5])]});var subQ7=sQuery(id+"F41.wireOp",EDGE,"E36");var subQ8=makeQuery(id+"F42.opRevolve","SWEPT_FACE",FACE,{"disambiguationData":[OSD([subQ7])]});var subQ9=makeQuery(id+"F42.opRevolve","SWEPT_EDGE",EDGE,{"disambiguationData":[OSD([subQ5,subQ7])]});var subQ10=sQuery(id+"F4.wireOp",EDGE,"E26.2.3");var subQ11=sQuery(id+"F4.wireOp",EDGE,"E26.2.2");var subQ12=sQuery(id+"F3.wireOp",EDGE,"E20.2.3");var subQ13=sQuery(id+"F3.wireOp",EDGE,"E20.2.1");var subQ14=sQuery(id+"F4.wireOp",EDGE,"E26.3.3");var subQ15=sQuery(id+"F4.wireOp",EDGE,"E26.3.2");var subQ16=sQuery(id+"F3.wireOp",EDGE,"E20.3.3");var subQ17=sQuery(id+"F3.wireOp",EDGE,"E20.3.1");var subQ18=sQuery(id+"F4.wireOp",EDGE,"E26.4.3");var subQ19=sQuery(id+"F4.wireOp",EDGE,"E26.4.2");var subQ20=sQuery(id+"F3.wireOp",EDGE,"E20.4.3");var subQ21=sQuery(id+"F3.wireOp",EDGE,"E20.4.1");var subQ22=sQuery(id+"F4.wireOp",EDGE,"E26.5.3");var subQ23=sQuery(id+"F4.wireOp",EDGE,"E26.5.2");var subQ24=sQuery(id+"F3.wireOp",EDGE,"E20.5.3");var subQ25=sQuery(id+"F3.wireOp",EDGE,"E20.5.1");var subQ26=sQuery(id+"F4.wireOp",EDGE,"E26.6.3");var subQ27=sQuery(id+"F4.wireOp",EDGE,"E26.6.2");var subQ28=sQuery(id+"F3.wireOp",EDGE,"E20.6.3");var subQ29=sQuery(id+"F3.wireOp",EDGE,"E20.6.1");var subQ30=sQuery(id+"F4.wireOp",EDGE,"E26.7.3");var subQ31=sQuery(id+"F4.wireOp",EDGE,"E26.7.2");var subQ32=sQuery(id+"F3.wireOp",EDGE,"E20.7.3");var subQ33=sQuery(id+"F3.wireOp",EDGE,"E20.7.1");var subQ34=sQuery(id+"F4.wireOp",EDGE,"E26.8.3");var subQ35=sQuery(id+"F4.wireOp",EDGE,"E26.8.2");var subQ36=sQuery(id+"F3.wireOp",EDGE,"E20.8.3");var subQ37=sQuery(id+"F3.wireOp",EDGE,"E20.8.1");var subQ38=sQuery(id+"F4.wireOp",EDGE,"E26.9.3");var subQ39=sQuery(id+"F4.wireOp",EDGE,"E26.9.2");var subQ40=sQuery(id+"F3.wireOp",EDGE,"E20.9.3");var subQ41=sQuery(id+"F3.wireOp",EDGE,"E20.9.1");var subQ42=sQuery(id+"F4.wireOp",EDGE,"E26.10.3");var subQ43=sQuery(id+"F4.wireOp",EDGE,"E26.10.2");var subQ44=sQuery(id+"F3.wireOp",EDGE,"E20.10.3");var subQ45=sQuery(id+"F3.wireOp",EDGE,"E20.10.1");var subQ47=makeQuery(id+"F11.opLoft","SWEPT_FACE",FACE,{"disambiguationData":[OSD([sQuery(id+"F3.wireOp",EDGE,"E20.10.0"),subQ45,subQ44,sQuery(id+"F4.wireOp",EDGE,"E26.10.0"),subQ43,subQ42])]});var subQ48=sQuery(id+"F4.wireOp",EDGE,"E26.11.3");var subQ49=sQuery(id+"F4.wireOp",EDGE,"E26.11.2");var subQ50=sQuery(id+"F3.wireOp",EDGE,"E20.11.3");var subQ51=sQuery(id+"F3.wireOp",EDGE,"E20.11.1");var subQ52=sQuery(id+"F4.wireOp",EDGE,"E26.12.3");var subQ53=sQuery(id+"F4.wireOp",EDGE,"E26.12.2");var subQ54=sQuery(id+"F3.wireOp",EDGE,"E20.12.3");var subQ55=sQuery(id+"F3.wireOp",EDGE,"E20.12.1");var subQ56=sQuery(id+"F4.wireOp",EDGE,"E26.13.3");var subQ57=sQuery(id+"F4.wireOp",EDGE,"E26.13.2");var subQ58=sQuery(id+"F3.wireOp",EDGE,"E20.13.3");var subQ59=sQuery(id+"F3.wireOp",EDGE,"E20.13.1");var subQ60=sQuery(id+"F4.wireOp",EDGE,"E26.14.3");var subQ61=sQuery(id+"F4.wireOp",EDGE,"E26.14.2");var subQ62=sQuery(id+"F3.wireOp",EDGE,"E20.14.3");var subQ63=sQuery(id+"F3.wireOp",EDGE,"E20.14.1");var subQ64=sQuery(id+"F4.wireOp",EDGE,"E26.15.3");var subQ65=sQuery(id+"F4.wireOp",EDGE,"E26.15.2");var subQ66=sQuery(id+"F3.wireOp",EDGE,"E20.15.3");var subQ67=sQuery(id+"F3.wireOp",EDGE,"E20.15.1");var subQ68=sQuery(id+"F4.wireOp",EDGE,"E23");var subQ69=sQuery(id+"F4.wireOp",EDGE,"E22");var subQ70=sQuery(id+"F3.wireOp",EDGE,"E18.top");var subQ71=sQuery(id+"F3.wireOp",EDGE,"E18.bottom");var subQ74=makeQuery(id+"F42.boolean.opBoolean","COPY",FACE,{"disambiguationData":[TD([subQ47])],"derivedFrom":subQ6});var subQ75=makeQuery(id+"F11.boolean.opBoolean","INTERSECT",EDGE,{"derivedFrom":[makeQuery(id+"F1.opRevolve","SWEPT_FACE",FACE,{"disambiguationData":[OSD([sQuery(id+"F0.wireOp",EDGE,"E4")])]}),subQ47]});Q60=makeQuery(id+"F48.opFillet","BLEND_EDGE",EDGE,{"blendedFrom":[makeQuery(id+"F47.opFillet","TWEAK_EDGE",EDGE,{"derivedFrom":[makeQuery(id+"F45.opFillet","BLEND_VERTEX",VERTEX,{"blendedFrom":[subQ75,subQ47,subQ74],"blendedInto":[subQ47,subQ74]}),makeQuery(id+"F45.opFillet","BLEND_VERTEX",VERTEX,{"blendedFrom":[subQ75,makeQuery(id+"F42.boolean.opBoolean","MERGE",FACE,{"derivedFrom":[subQ0,subQ8]}),subQ74],"blendedInto":[makeQuery(id+"F42.boolean.opBoolean","MERGE",FACE,{"derivedFrom":[subQ0,subQ8]}),subQ74]})]}),makeQuery(id+"F47.opFillet","BLEND_FACE",FACE,{"disambiguationData":[OSD([subQ5,subQ7]),TDD([makeQuery(id+"F42.boolean.opBoolean","COPY",EDGE,{"disambiguationData":[TD([makeQuery(id+"F5.opLoft","SWEPT_FACE",FACE,{"disambiguationData":[OSD([subQ71,subQ70,sQuery(id+"F3.wireOp",EDGE,"E18.left"),sQuery(id+"F4.wireOp",EDGE,"E21"),subQ69,subQ68])]})])],"derivedFrom":subQ9})])]}),makeQuery(id+"F47.opFillet","BLEND_FACE",FACE,{"disambiguationData":[OSD([subQ5,subQ7]),TDD([makeQuery(id+"F42.boolean.opBoolean","COPY",EDGE,{"disambiguationData":[TD([makeQuery(id+"F6.opLoft","SWEPT_FACE",FACE,{"disambiguationData":[OSD([sQuery(id+"F3.wireOp",EDGE,"E20.15.0"),subQ67,subQ66,sQuery(id+"F4.wireOp",EDGE,"E26.15.0"),subQ65,subQ64])]})])],"derivedFrom":subQ9})])]}),makeQuery(id+"F47.opFillet","BLEND_FACE",FACE,{"disambiguationData":[OSD([subQ5,subQ7]),TDD([makeQuery(id+"F42.boolean.opBoolean","COPY",EDGE,{"disambiguationData":[TD([makeQuery(id+"F7.opLoft","SWEPT_FACE",FACE,{"disambiguationData":[OSD([sQuery(id+"F3.wireOp",EDGE,"E20.14.0"),subQ63,subQ62,sQuery(id+"F4.wireOp",EDGE,"E26.14.0"),subQ61,subQ60])]})])],"derivedFrom":subQ9})])]}),makeQuery(id+"F47.opFillet","BLEND_FACE",FACE,{"disambiguationData":[OSD([subQ5,subQ7]),TDD([makeQuery(id+"F42.boolean.opBoolean","COPY",EDGE,{"disambiguationData":[TD([makeQuery(id+"F8.opLoft","SWEPT_FACE",FACE,{"disambiguationData":[OSD([sQuery(id+"F3.wireOp",EDGE,"E20.13.0"),subQ59,subQ58,sQuery(id+"F4.wireOp",EDGE,"E26.13.0"),subQ57,subQ56])]})])],"derivedFrom":subQ9})])]}),makeQuery(id+"F47.opFillet","BLEND_FACE",FACE,{"disambiguationData":[OSD([subQ5,subQ7]),TDD([makeQuery(id+"F42.boolean.opBoolean","COPY",EDGE,{"disambiguationData":[TD([makeQuery(id+"F9.opLoft","SWEPT_FACE",FACE,{"disambiguationData":[OSD([sQuery(id+"F3.wireOp",EDGE,"E20.12.0"),subQ55,subQ54,sQuery(id+"F4.wireOp",EDGE,"E26.12.0"),subQ53,subQ52])]})])],"derivedFrom":subQ9})])]}),makeQuery(id+"F47.opFillet","BLEND_FACE",FACE,{"disambiguationData":[OSD([subQ5,subQ7]),TDD([makeQuery(id+"F42.boolean.opBoolean","COPY",EDGE,{"disambiguationData":[TD([makeQuery(id+"F10.opLoft","SWEPT_FACE",FACE,{"disambiguationData":[OSD([sQuery(id+"F3.wireOp",EDGE,"E20.11.0"),subQ51,subQ50,sQuery(id+"F4.wireOp",EDGE,"E26.11.0"),subQ49,subQ48])]})])],"derivedFrom":subQ9})])]}),makeQuery(id+"F47.opFillet","BLEND_FACE",FACE,{"disambiguationData":[OSD([subQ5,subQ7]),TDD([makeQuery(id+"F42.boolean.opBoolean","COPY",EDGE,{"disambiguationData":[TD([subQ47])],"derivedFrom":subQ9})])]}),makeQuery(id+"F47.opFillet","BLEND_FACE",FACE,{"disambiguationData":[OSD([subQ5,subQ7]),TDD([makeQuery(id+"F42.boolean.opBoolean","COPY",EDGE,{"disambiguationData":[TD([makeQuery(id+"F12.opLoft","SWEPT_FACE",FACE,{"disambiguationData":[OSD([sQuery(id+"F3.wireOp",EDGE,"E20.9.0"),subQ41,subQ40,sQuery(id+"F4.wireOp",EDGE,"E26.9.0"),subQ39,subQ38])]})])],"derivedFrom":subQ9})])]}),makeQuery(id+"F47.opFillet","BLEND_FACE",FACE,{"disambiguationData":[OSD([subQ5,subQ7]),TDD([makeQuery(id+"F42.boolean.opBoolean","COPY",EDGE,{"disambiguationData":[TD([makeQuery(id+"F13.opLoft","SWEPT_FACE",FACE,{"disambiguationData":[OSD([sQuery(id+"F3.wireOp",EDGE,"E20.8.0"),subQ37,subQ36,sQuery(id+"F4.wireOp",EDGE,"E26.8.0"),subQ35,subQ34])]})])],"derivedFrom":subQ9})])]}),makeQuery(id+"F47.opFillet","BLEND_FACE",FACE,{"disambiguationData":[OSD([subQ5,subQ7]),TDD([makeQuery(id+"F42.boolean.opBoolean","COPY",EDGE,{"disambiguationData":[TD([makeQuery(id+"F14.opLoft","SWEPT_FACE",FACE,{"disambiguationData":[OSD([sQuery(id+"F3.wireOp",EDGE,"E20.7.0"),subQ33,subQ32,sQuery(id+"F4.wireOp",EDGE,"E26.7.0"),subQ31,subQ30])]})])],"derivedFrom":subQ9})])]}),makeQuery(id+"F47.opFillet","BLEND_FACE",FACE,{"disambiguationData":[OSD([subQ5,subQ7]),TDD([makeQuery(id+"F42.boolean.opBoolean","COPY",EDGE,{"disambiguationData":[TD([makeQuery(id+"F15.opLoft","SWEPT_FACE",FACE,{"disambiguationData":[OSD([sQuery(id+"F3.wireOp",EDGE,"E20.6.0"),subQ29,subQ28,sQuery(id+"F4.wireOp",EDGE,"E26.6.0"),subQ27,subQ26])]})])],"derivedFrom":subQ9})])]}),makeQuery(id+"F47.opFillet","BLEND_FACE",FACE,{"disambiguationData":[OSD([subQ5,subQ7]),TDD([makeQuery(id+"F42.boolean.opBoolean","COPY",EDGE,{"disambiguationData":[TD([makeQuery(id+"F16.opLoft","SWEPT_FACE",FACE,{"disambiguationData":[OSD([sQuery(id+"F3.wireOp",EDGE,"E20.5.0"),subQ25,subQ24,sQuery(id+"F4.wireOp",EDGE,"E26.5.0"),subQ23,subQ22])]})])],"derivedFrom":subQ9})])]}),makeQuery(id+"F47.opFillet","BLEND_FACE",FACE,{"disambiguationData":[OSD([subQ5,subQ7]),TDD([makeQuery(id+"F42.boolean.opBoolean","COPY",EDGE,{"disambiguationData":[TD([makeQuery(id+"F17.opLoft","SWEPT_FACE",FACE,{"disambiguationData":[OSD([sQuery(id+"F3.wireOp",EDGE,"E20.4.0"),subQ21,subQ20,sQuery(id+"F4.wireOp",EDGE,"E26.4.0"),subQ19,subQ18])]})])],"derivedFrom":subQ9})])]}),makeQuery(id+"F47.opFillet","BLEND_FACE",FACE,{"disambiguationData":[OSD([subQ5,subQ7]),TDD([makeQuery(id+"F42.boolean.opBoolean","COPY",EDGE,{"disambiguationData":[TD([makeQuery(id+"F18.opLoft","SWEPT_FACE",FACE,{"disambiguationData":[OSD([sQuery(id+"F3.wireOp",EDGE,"E20.3.0"),subQ17,subQ16,sQuery(id+"F4.wireOp",EDGE,"E26.3.0"),subQ15,subQ14])]})])],"derivedFrom":subQ9})])]}),makeQuery(id+"F47.opFillet","BLEND_FACE",FACE,{"disambiguationData":[OSD([subQ5,subQ7]),TDD([makeQuery(id+"F42.boolean.opBoolean","COPY",EDGE,{"disambiguationData":[TD([makeQuery(id+"F19.opLoft","SWEPT_FACE",FACE,{"disambiguationData":[OSD([sQuery(id+"F3.wireOp",EDGE,"E20.2.0"),subQ13,subQ12,sQuery(id+"F4.wireOp",EDGE,"E26.2.0"),subQ11,subQ10])]})])],"derivedFrom":subQ9})])]}),makeQuery(id+"F47.opFillet","BLEND_FACE",FACE,{"disambiguationData":[OSD([subQ5,subQ7]),TDD([makeQuery(id+"F42.boolean.opBoolean","COPY",EDGE,{"disambiguationData":[TD([makeQuery(id+"F20.opLoft","SWEPT_FACE",FACE,{"disambiguationData":[OSD([sQuery(id+"F3.wireOp",EDGE,"E20.1.0"),subQ4,subQ3,sQuery(id+"F4.wireOp",EDGE,"E26.1.0"),subQ2,subQ1])]})])],"derivedFrom":subQ9})])]})],"blendedInto":[makeQuery(id+"F47.opFillet","BLEND_FACE",FACE,{"disambiguationData":[OSD([subQ5,subQ7]),TDD([makeQuery(id+"F42.boolean.opBoolean","COPY",EDGE,{"disambiguationData":[TD([makeQuery(id+"F5.opLoft","SWEPT_FACE",FACE,{"disambiguationData":[OSD([subQ71,subQ70,sQuery(id+"F3.wireOp",EDGE,"E18.left"),sQuery(id+"F4.wireOp",EDGE,"E21"),subQ69,subQ68])]})])],"derivedFrom":subQ9})])]}),makeQuery(id+"F47.opFillet","BLEND_FACE",FACE,{"disambiguationData":[OSD([subQ5,subQ7]),TDD([makeQuery(id+"F42.boolean.opBoolean","COPY",EDGE,{"disambiguationData":[TD([makeQuery(id+"F6.opLoft","SWEPT_FACE",FACE,{"disambiguationData":[OSD([sQuery(id+"F3.wireOp",EDGE,"E20.15.0"),subQ67,subQ66,sQuery(id+"F4.wireOp",EDGE,"E26.15.0"),subQ65,subQ64])]})])],"derivedFrom":subQ9})])]}),makeQuery(id+"F47.opFillet","BLEND_FACE",FACE,{"disambiguationData":[OSD([subQ5,subQ7]),TDD([makeQuery(id+"F42.boolean.opBoolean","COPY",EDGE,{"disambiguationData":[TD([makeQuery(id+"F7.opLoft","SWEPT_FACE",FACE,{"disambiguationData":[OSD([sQuery(id+"F3.wireOp",EDGE,"E20.14.0"),subQ63,subQ62,sQuery(id+"F4.wireOp",EDGE,"E26.14.0"),subQ61,subQ60])]})])],"derivedFrom":subQ9})])]}),makeQuery(id+"F47.opFillet","BLEND_FACE",FACE,{"disambiguationData":[OSD([subQ5,subQ7]),TDD([makeQuery(id+"F42.boolean.opBoolean","COPY",EDGE,{"disambiguationData":[TD([makeQuery(id+"F8.opLoft","SWEPT_FACE",FACE,{"disambiguationData":[OSD([sQuery(id+"F3.wireOp",EDGE,"E20.13.0"),subQ59,subQ58,sQuery(id+"F4.wireOp",EDGE,"E26.13.0"),subQ57,subQ56])]})])],"derivedFrom":subQ9})])]}),makeQuery(id+"F47.opFillet","BLEND_FACE",FACE,{"disambiguationData":[OSD([subQ5,subQ7]),TDD([makeQuery(id+"F42.boolean.opBoolean","COPY",EDGE,{"disambiguationData":[TD([makeQuery(id+"F9.opLoft","SWEPT_FACE",FACE,{"disambiguationData":[OSD([sQuery(id+"F3.wireOp",EDGE,"E20.12.0"),subQ55,subQ54,sQuery(id+"F4.wireOp",EDGE,"E26.12.0"),subQ53,subQ52])]})])],"derivedFrom":subQ9})])]}),makeQuery(id+"F47.opFillet","BLEND_FACE",FACE,{"disambiguationData":[OSD([subQ5,subQ7]),TDD([makeQuery(id+"F42.boolean.opBoolean","COPY",EDGE,{"disambiguationData":[TD([makeQuery(id+"F10.opLoft","SWEPT_FACE",FACE,{"disambiguationData":[OSD([sQuery(id+"F3.wireOp",EDGE,"E20.11.0"),subQ51,subQ50,sQuery(id+"F4.wireOp",EDGE,"E26.11.0"),subQ49,subQ48])]})])],"derivedFrom":subQ9})])]}),makeQuery(id+"F47.opFillet","BLEND_FACE",FACE,{"disambiguationData":[OSD([subQ5,subQ7]),TDD([makeQuery(id+"F42.boolean.opBoolean","COPY",EDGE,{"disambiguationData":[TD([subQ47])],"derivedFrom":subQ9})])]}),makeQuery(id+"F47.opFillet","BLEND_FACE",FACE,{"disambiguationData":[OSD([subQ5,subQ7]),TDD([makeQuery(id+"F42.boolean.opBoolean","COPY",EDGE,{"disambiguationData":[TD([makeQuery(id+"F12.opLoft","SWEPT_FACE",FACE,{"disambiguationData":[OSD([sQuery(id+"F3.wireOp",EDGE,"E20.9.0"),subQ41,subQ40,sQuery(id+"F4.wireOp",EDGE,"E26.9.0"),subQ39,subQ38])]})])],"derivedFrom":subQ9})])]}),makeQuery(id+"F47.opFillet","BLEND_FACE",FACE,{"disambiguationData":[OSD([subQ5,subQ7]),TDD([makeQuery(id+"F42.boolean.opBoolean","COPY",EDGE,{"disambiguationData":[TD([makeQuery(id+"F13.opLoft","SWEPT_FACE",FACE,{"disambiguationData":[OSD([sQuery(id+"F3.wireOp",EDGE,"E20.8.0"),subQ37,subQ36,sQuery(id+"F4.wireOp",EDGE,"E26.8.0"),subQ35,subQ34])]})])],"derivedFrom":subQ9})])]}),makeQuery(id+"F47.opFillet","BLEND_FACE",FACE,{"disambiguationData":[OSD([subQ5,subQ7]),TDD([makeQuery(id+"F42.boolean.opBoolean","COPY",EDGE,{"disambiguationData":[TD([makeQuery(id+"F14.opLoft","SWEPT_FACE",FACE,{"disambiguationData":[OSD([sQuery(id+"F3.wireOp",EDGE,"E20.7.0"),subQ33,subQ32,sQuery(id+"F4.wireOp",EDGE,"E26.7.0"),subQ31,subQ30])]})])],"derivedFrom":subQ9})])]}),makeQuery(id+"F47.opFillet","BLEND_FACE",FACE,{"disambiguationData":[OSD([subQ5,subQ7]),TDD([makeQuery(id+"F42.boolean.opBoolean","COPY",EDGE,{"disambiguationData":[TD([makeQuery(id+"F15.opLoft","SWEPT_FACE",FACE,{"disambiguationData":[OSD([sQuery(id+"F3.wireOp",EDGE,"E20.6.0"),subQ29,subQ28,sQuery(id+"F4.wireOp",EDGE,"E26.6.0"),subQ27,subQ26])]})])],"derivedFrom":subQ9})])]}),makeQuery(id+"F47.opFillet","BLEND_FACE",FACE,{"disambiguationData":[OSD([subQ5,subQ7]),TDD([makeQuery(id+"F42.boolean.opBoolean","COPY",EDGE,{"disambiguationData":[TD([makeQuery(id+"F16.opLoft","SWEPT_FACE",FACE,{"disambiguationData":[OSD([sQuery(id+"F3.wireOp",EDGE,"E20.5.0"),subQ25,subQ24,sQuery(id+"F4.wireOp",EDGE,"E26.5.0"),subQ23,subQ22])]})])],"derivedFrom":subQ9})])]}),makeQuery(id+"F47.opFillet","BLEND_FACE",FACE,{"disambiguationData":[OSD([subQ5,subQ7]),TDD([makeQuery(id+"F42.boolean.opBoolean","COPY",EDGE,{"disambiguationData":[TD([makeQuery(id+"F17.opLoft","SWEPT_FACE",FACE,{"disambiguationData":[OSD([sQuery(id+"F3.wireOp",EDGE,"E20.4.0"),subQ21,subQ20,sQuery(id+"F4.wireOp",EDGE,"E26.4.0"),subQ19,subQ18])]})])],"derivedFrom":subQ9})])]}),makeQuery(id+"F47.opFillet","BLEND_FACE",FACE,{"disambiguationData":[OSD([subQ5,subQ7]),TDD([makeQuery(id+"F42.boolean.opBoolean","COPY",EDGE,{"disambiguationData":[TD([makeQuery(id+"F18.opLoft","SWEPT_FACE",FACE,{"disambiguationData":[OSD([sQuery(id+"F3.wireOp",EDGE,"E20.3.0"),subQ17,subQ16,sQuery(id+"F4.wireOp",EDGE,"E26.3.0"),subQ15,subQ14])]})])],"derivedFrom":subQ9})])]}),makeQuery(id+"F47.opFillet","BLEND_FACE",FACE,{"disambiguationData":[OSD([subQ5,subQ7]),TDD([makeQuery(id+"F42.boolean.opBoolean","COPY",EDGE,{"disambiguationData":[TD([makeQuery(id+"F19.opLoft","SWEPT_FACE",FACE,{"disambiguationData":[OSD([sQuery(id+"F3.wireOp",EDGE,"E20.2.0"),subQ13,subQ12,sQuery(id+"F4.wireOp",EDGE,"E26.2.0"),subQ11,subQ10])]})])],"derivedFrom":subQ9})])]}),makeQuery(id+"F47.opFillet","BLEND_FACE",FACE,{"disambiguationData":[OSD([subQ5,subQ7]),TDD([makeQuery(id+"F42.boolean.opBoolean","COPY",EDGE,{"disambiguationData":[TD([makeQuery(id+"F20.opLoft","SWEPT_FACE",FACE,{"disambiguationData":[OSD([sQuery(id+"F3.wireOp",EDGE,"E20.1.0"),subQ4,subQ3,sQuery(id+"F4.wireOp",EDGE,"E26.1.0"),subQ2,subQ1])]})])],"derivedFrom":subQ9})])]})]});}
            var Q61;
            {var subQ0=makeQuery(id+"F40.opExtrude","CAP_FACE",FACE,{"disambiguationData":[OSD([sQuery(id+"F39.wireOp",EDGE,"E29"),sQuery(id+"F39.wireOp",EDGE,"E30")])],"isStart":false});var subQ1=sQuery(id+"F4.wireOp",EDGE,"E26.1.3");var subQ2=sQuery(id+"F4.wireOp",EDGE,"E26.1.2");var subQ3=sQuery(id+"F3.wireOp",EDGE,"E20.1.3");var subQ4=sQuery(id+"F3.wireOp",EDGE,"E20.1.1");var subQ5=sQuery(id+"F41.wireOp",EDGE,"E35");var subQ6=makeQuery(id+"F42.opRevolve","SWEPT_FACE",FACE,{"disambiguationData":[OSD([subQ5])]});var subQ7=sQuery(id+"F41.wireOp",EDGE,"E36");var subQ8=makeQuery(id+"F42.opRevolve","SWEPT_FACE",FACE,{"disambiguationData":[OSD([subQ7])]});var subQ9=makeQuery(id+"F42.opRevolve","SWEPT_EDGE",EDGE,{"disambiguationData":[OSD([subQ5,subQ7])]});var subQ10=sQuery(id+"F4.wireOp",EDGE,"E26.2.3");var subQ11=sQuery(id+"F4.wireOp",EDGE,"E26.2.2");var subQ12=sQuery(id+"F3.wireOp",EDGE,"E20.2.3");var subQ13=sQuery(id+"F3.wireOp",EDGE,"E20.2.1");var subQ14=sQuery(id+"F4.wireOp",EDGE,"E26.3.3");var subQ15=sQuery(id+"F4.wireOp",EDGE,"E26.3.2");var subQ16=sQuery(id+"F3.wireOp",EDGE,"E20.3.3");var subQ17=sQuery(id+"F3.wireOp",EDGE,"E20.3.1");var subQ18=sQuery(id+"F4.wireOp",EDGE,"E26.4.3");var subQ19=sQuery(id+"F4.wireOp",EDGE,"E26.4.2");var subQ20=sQuery(id+"F3.wireOp",EDGE,"E20.4.3");var subQ21=sQuery(id+"F3.wireOp",EDGE,"E20.4.1");var subQ22=sQuery(id+"F4.wireOp",EDGE,"E26.5.3");var subQ23=sQuery(id+"F4.wireOp",EDGE,"E26.5.2");var subQ24=sQuery(id+"F3.wireOp",EDGE,"E20.5.3");var subQ25=sQuery(id+"F3.wireOp",EDGE,"E20.5.1");var subQ26=sQuery(id+"F4.wireOp",EDGE,"E26.6.3");var subQ27=sQuery(id+"F4.wireOp",EDGE,"E26.6.2");var subQ28=sQuery(id+"F3.wireOp",EDGE,"E20.6.3");var subQ29=sQuery(id+"F3.wireOp",EDGE,"E20.6.1");var subQ30=sQuery(id+"F4.wireOp",EDGE,"E26.7.3");var subQ31=sQuery(id+"F4.wireOp",EDGE,"E26.7.2");var subQ32=sQuery(id+"F3.wireOp",EDGE,"E20.7.3");var subQ33=sQuery(id+"F3.wireOp",EDGE,"E20.7.1");var subQ34=sQuery(id+"F4.wireOp",EDGE,"E26.8.3");var subQ35=sQuery(id+"F4.wireOp",EDGE,"E26.8.2");var subQ36=sQuery(id+"F3.wireOp",EDGE,"E20.8.3");var subQ37=sQuery(id+"F3.wireOp",EDGE,"E20.8.1");var subQ38=sQuery(id+"F4.wireOp",EDGE,"E26.9.3");var subQ39=sQuery(id+"F4.wireOp",EDGE,"E26.9.2");var subQ40=sQuery(id+"F3.wireOp",EDGE,"E20.9.3");var subQ41=sQuery(id+"F3.wireOp",EDGE,"E20.9.1");var subQ43=makeQuery(id+"F12.opLoft","SWEPT_FACE",FACE,{"disambiguationData":[OSD([sQuery(id+"F3.wireOp",EDGE,"E20.9.0"),subQ41,subQ40,sQuery(id+"F4.wireOp",EDGE,"E26.9.0"),subQ39,subQ38])]});var subQ44=sQuery(id+"F4.wireOp",EDGE,"E26.10.3");var subQ45=sQuery(id+"F4.wireOp",EDGE,"E26.10.2");var subQ46=sQuery(id+"F3.wireOp",EDGE,"E20.10.3");var subQ47=sQuery(id+"F3.wireOp",EDGE,"E20.10.1");var subQ48=sQuery(id+"F4.wireOp",EDGE,"E26.11.3");var subQ49=sQuery(id+"F4.wireOp",EDGE,"E26.11.2");var subQ50=sQuery(id+"F3.wireOp",EDGE,"E20.11.3");var subQ51=sQuery(id+"F3.wireOp",EDGE,"E20.11.1");var subQ52=sQuery(id+"F4.wireOp",EDGE,"E26.12.3");var subQ53=sQuery(id+"F4.wireOp",EDGE,"E26.12.2");var subQ54=sQuery(id+"F3.wireOp",EDGE,"E20.12.3");var subQ55=sQuery(id+"F3.wireOp",EDGE,"E20.12.1");var subQ56=sQuery(id+"F4.wireOp",EDGE,"E26.13.3");var subQ57=sQuery(id+"F4.wireOp",EDGE,"E26.13.2");var subQ58=sQuery(id+"F3.wireOp",EDGE,"E20.13.3");var subQ59=sQuery(id+"F3.wireOp",EDGE,"E20.13.1");var subQ60=sQuery(id+"F4.wireOp",EDGE,"E26.14.3");var subQ61=sQuery(id+"F4.wireOp",EDGE,"E26.14.2");var subQ62=sQuery(id+"F3.wireOp",EDGE,"E20.14.3");var subQ63=sQuery(id+"F3.wireOp",EDGE,"E20.14.1");var subQ64=sQuery(id+"F4.wireOp",EDGE,"E26.15.3");var subQ65=sQuery(id+"F4.wireOp",EDGE,"E26.15.2");var subQ66=sQuery(id+"F3.wireOp",EDGE,"E20.15.3");var subQ67=sQuery(id+"F3.wireOp",EDGE,"E20.15.1");var subQ68=sQuery(id+"F4.wireOp",EDGE,"E23");var subQ69=sQuery(id+"F4.wireOp",EDGE,"E22");var subQ70=sQuery(id+"F3.wireOp",EDGE,"E18.top");var subQ71=sQuery(id+"F3.wireOp",EDGE,"E18.bottom");var subQ74=makeQuery(id+"F42.boolean.opBoolean","COPY",FACE,{"disambiguationData":[TD([subQ43])],"derivedFrom":subQ6});var subQ75=makeQuery(id+"F12.boolean.opBoolean","INTERSECT",EDGE,{"derivedFrom":[makeQuery(id+"F1.opRevolve","SWEPT_FACE",FACE,{"disambiguationData":[OSD([sQuery(id+"F0.wireOp",EDGE,"E4")])]}),subQ43]});Q61=makeQuery(id+"F48.opFillet","BLEND_EDGE",EDGE,{"blendedFrom":[makeQuery(id+"F47.opFillet","TWEAK_EDGE",EDGE,{"derivedFrom":[makeQuery(id+"F45.opFillet","BLEND_VERTEX",VERTEX,{"blendedFrom":[subQ75,subQ43,subQ74],"blendedInto":[subQ43,subQ74]}),makeQuery(id+"F45.opFillet","BLEND_VERTEX",VERTEX,{"blendedFrom":[subQ75,makeQuery(id+"F42.boolean.opBoolean","MERGE",FACE,{"derivedFrom":[subQ0,subQ8]}),subQ74],"blendedInto":[makeQuery(id+"F42.boolean.opBoolean","MERGE",FACE,{"derivedFrom":[subQ0,subQ8]}),subQ74]})]}),makeQuery(id+"F47.opFillet","BLEND_FACE",FACE,{"disambiguationData":[OSD([subQ5,subQ7]),TDD([makeQuery(id+"F42.boolean.opBoolean","COPY",EDGE,{"disambiguationData":[TD([makeQuery(id+"F5.opLoft","SWEPT_FACE",FACE,{"disambiguationData":[OSD([subQ71,subQ70,sQuery(id+"F3.wireOp",EDGE,"E18.left"),sQuery(id+"F4.wireOp",EDGE,"E21"),subQ69,subQ68])]})])],"derivedFrom":subQ9})])]}),makeQuery(id+"F47.opFillet","BLEND_FACE",FACE,{"disambiguationData":[OSD([subQ5,subQ7]),TDD([makeQuery(id+"F42.boolean.opBoolean","COPY",EDGE,{"disambiguationData":[TD([makeQuery(id+"F6.opLoft","SWEPT_FACE",FACE,{"disambiguationData":[OSD([sQuery(id+"F3.wireOp",EDGE,"E20.15.0"),subQ67,subQ66,sQuery(id+"F4.wireOp",EDGE,"E26.15.0"),subQ65,subQ64])]})])],"derivedFrom":subQ9})])]}),makeQuery(id+"F47.opFillet","BLEND_FACE",FACE,{"disambiguationData":[OSD([subQ5,subQ7]),TDD([makeQuery(id+"F42.boolean.opBoolean","COPY",EDGE,{"disambiguationData":[TD([makeQuery(id+"F7.opLoft","SWEPT_FACE",FACE,{"disambiguationData":[OSD([sQuery(id+"F3.wireOp",EDGE,"E20.14.0"),subQ63,subQ62,sQuery(id+"F4.wireOp",EDGE,"E26.14.0"),subQ61,subQ60])]})])],"derivedFrom":subQ9})])]}),makeQuery(id+"F47.opFillet","BLEND_FACE",FACE,{"disambiguationData":[OSD([subQ5,subQ7]),TDD([makeQuery(id+"F42.boolean.opBoolean","COPY",EDGE,{"disambiguationData":[TD([makeQuery(id+"F8.opLoft","SWEPT_FACE",FACE,{"disambiguationData":[OSD([sQuery(id+"F3.wireOp",EDGE,"E20.13.0"),subQ59,subQ58,sQuery(id+"F4.wireOp",EDGE,"E26.13.0"),subQ57,subQ56])]})])],"derivedFrom":subQ9})])]}),makeQuery(id+"F47.opFillet","BLEND_FACE",FACE,{"disambiguationData":[OSD([subQ5,subQ7]),TDD([makeQuery(id+"F42.boolean.opBoolean","COPY",EDGE,{"disambiguationData":[TD([makeQuery(id+"F9.opLoft","SWEPT_FACE",FACE,{"disambiguationData":[OSD([sQuery(id+"F3.wireOp",EDGE,"E20.12.0"),subQ55,subQ54,sQuery(id+"F4.wireOp",EDGE,"E26.12.0"),subQ53,subQ52])]})])],"derivedFrom":subQ9})])]}),makeQuery(id+"F47.opFillet","BLEND_FACE",FACE,{"disambiguationData":[OSD([subQ5,subQ7]),TDD([makeQuery(id+"F42.boolean.opBoolean","COPY",EDGE,{"disambiguationData":[TD([makeQuery(id+"F10.opLoft","SWEPT_FACE",FACE,{"disambiguationData":[OSD([sQuery(id+"F3.wireOp",EDGE,"E20.11.0"),subQ51,subQ50,sQuery(id+"F4.wireOp",EDGE,"E26.11.0"),subQ49,subQ48])]})])],"derivedFrom":subQ9})])]}),makeQuery(id+"F47.opFillet","BLEND_FACE",FACE,{"disambiguationData":[OSD([subQ5,subQ7]),TDD([makeQuery(id+"F42.boolean.opBoolean","COPY",EDGE,{"disambiguationData":[TD([makeQuery(id+"F11.opLoft","SWEPT_FACE",FACE,{"disambiguationData":[OSD([sQuery(id+"F3.wireOp",EDGE,"E20.10.0"),subQ47,subQ46,sQuery(id+"F4.wireOp",EDGE,"E26.10.0"),subQ45,subQ44])]})])],"derivedFrom":subQ9})])]}),makeQuery(id+"F47.opFillet","BLEND_FACE",FACE,{"disambiguationData":[OSD([subQ5,subQ7]),TDD([makeQuery(id+"F42.boolean.opBoolean","COPY",EDGE,{"disambiguationData":[TD([subQ43])],"derivedFrom":subQ9})])]}),makeQuery(id+"F47.opFillet","BLEND_FACE",FACE,{"disambiguationData":[OSD([subQ5,subQ7]),TDD([makeQuery(id+"F42.boolean.opBoolean","COPY",EDGE,{"disambiguationData":[TD([makeQuery(id+"F13.opLoft","SWEPT_FACE",FACE,{"disambiguationData":[OSD([sQuery(id+"F3.wireOp",EDGE,"E20.8.0"),subQ37,subQ36,sQuery(id+"F4.wireOp",EDGE,"E26.8.0"),subQ35,subQ34])]})])],"derivedFrom":subQ9})])]}),makeQuery(id+"F47.opFillet","BLEND_FACE",FACE,{"disambiguationData":[OSD([subQ5,subQ7]),TDD([makeQuery(id+"F42.boolean.opBoolean","COPY",EDGE,{"disambiguationData":[TD([makeQuery(id+"F14.opLoft","SWEPT_FACE",FACE,{"disambiguationData":[OSD([sQuery(id+"F3.wireOp",EDGE,"E20.7.0"),subQ33,subQ32,sQuery(id+"F4.wireOp",EDGE,"E26.7.0"),subQ31,subQ30])]})])],"derivedFrom":subQ9})])]}),makeQuery(id+"F47.opFillet","BLEND_FACE",FACE,{"disambiguationData":[OSD([subQ5,subQ7]),TDD([makeQuery(id+"F42.boolean.opBoolean","COPY",EDGE,{"disambiguationData":[TD([makeQuery(id+"F15.opLoft","SWEPT_FACE",FACE,{"disambiguationData":[OSD([sQuery(id+"F3.wireOp",EDGE,"E20.6.0"),subQ29,subQ28,sQuery(id+"F4.wireOp",EDGE,"E26.6.0"),subQ27,subQ26])]})])],"derivedFrom":subQ9})])]}),makeQuery(id+"F47.opFillet","BLEND_FACE",FACE,{"disambiguationData":[OSD([subQ5,subQ7]),TDD([makeQuery(id+"F42.boolean.opBoolean","COPY",EDGE,{"disambiguationData":[TD([makeQuery(id+"F16.opLoft","SWEPT_FACE",FACE,{"disambiguationData":[OSD([sQuery(id+"F3.wireOp",EDGE,"E20.5.0"),subQ25,subQ24,sQuery(id+"F4.wireOp",EDGE,"E26.5.0"),subQ23,subQ22])]})])],"derivedFrom":subQ9})])]}),makeQuery(id+"F47.opFillet","BLEND_FACE",FACE,{"disambiguationData":[OSD([subQ5,subQ7]),TDD([makeQuery(id+"F42.boolean.opBoolean","COPY",EDGE,{"disambiguationData":[TD([makeQuery(id+"F17.opLoft","SWEPT_FACE",FACE,{"disambiguationData":[OSD([sQuery(id+"F3.wireOp",EDGE,"E20.4.0"),subQ21,subQ20,sQuery(id+"F4.wireOp",EDGE,"E26.4.0"),subQ19,subQ18])]})])],"derivedFrom":subQ9})])]}),makeQuery(id+"F47.opFillet","BLEND_FACE",FACE,{"disambiguationData":[OSD([subQ5,subQ7]),TDD([makeQuery(id+"F42.boolean.opBoolean","COPY",EDGE,{"disambiguationData":[TD([makeQuery(id+"F18.opLoft","SWEPT_FACE",FACE,{"disambiguationData":[OSD([sQuery(id+"F3.wireOp",EDGE,"E20.3.0"),subQ17,subQ16,sQuery(id+"F4.wireOp",EDGE,"E26.3.0"),subQ15,subQ14])]})])],"derivedFrom":subQ9})])]}),makeQuery(id+"F47.opFillet","BLEND_FACE",FACE,{"disambiguationData":[OSD([subQ5,subQ7]),TDD([makeQuery(id+"F42.boolean.opBoolean","COPY",EDGE,{"disambiguationData":[TD([makeQuery(id+"F19.opLoft","SWEPT_FACE",FACE,{"disambiguationData":[OSD([sQuery(id+"F3.wireOp",EDGE,"E20.2.0"),subQ13,subQ12,sQuery(id+"F4.wireOp",EDGE,"E26.2.0"),subQ11,subQ10])]})])],"derivedFrom":subQ9})])]}),makeQuery(id+"F47.opFillet","BLEND_FACE",FACE,{"disambiguationData":[OSD([subQ5,subQ7]),TDD([makeQuery(id+"F42.boolean.opBoolean","COPY",EDGE,{"disambiguationData":[TD([makeQuery(id+"F20.opLoft","SWEPT_FACE",FACE,{"disambiguationData":[OSD([sQuery(id+"F3.wireOp",EDGE,"E20.1.0"),subQ4,subQ3,sQuery(id+"F4.wireOp",EDGE,"E26.1.0"),subQ2,subQ1])]})])],"derivedFrom":subQ9})])]})],"blendedInto":[makeQuery(id+"F47.opFillet","BLEND_FACE",FACE,{"disambiguationData":[OSD([subQ5,subQ7]),TDD([makeQuery(id+"F42.boolean.opBoolean","COPY",EDGE,{"disambiguationData":[TD([makeQuery(id+"F5.opLoft","SWEPT_FACE",FACE,{"disambiguationData":[OSD([subQ71,subQ70,sQuery(id+"F3.wireOp",EDGE,"E18.left"),sQuery(id+"F4.wireOp",EDGE,"E21"),subQ69,subQ68])]})])],"derivedFrom":subQ9})])]}),makeQuery(id+"F47.opFillet","BLEND_FACE",FACE,{"disambiguationData":[OSD([subQ5,subQ7]),TDD([makeQuery(id+"F42.boolean.opBoolean","COPY",EDGE,{"disambiguationData":[TD([makeQuery(id+"F6.opLoft","SWEPT_FACE",FACE,{"disambiguationData":[OSD([sQuery(id+"F3.wireOp",EDGE,"E20.15.0"),subQ67,subQ66,sQuery(id+"F4.wireOp",EDGE,"E26.15.0"),subQ65,subQ64])]})])],"derivedFrom":subQ9})])]}),makeQuery(id+"F47.opFillet","BLEND_FACE",FACE,{"disambiguationData":[OSD([subQ5,subQ7]),TDD([makeQuery(id+"F42.boolean.opBoolean","COPY",EDGE,{"disambiguationData":[TD([makeQuery(id+"F7.opLoft","SWEPT_FACE",FACE,{"disambiguationData":[OSD([sQuery(id+"F3.wireOp",EDGE,"E20.14.0"),subQ63,subQ62,sQuery(id+"F4.wireOp",EDGE,"E26.14.0"),subQ61,subQ60])]})])],"derivedFrom":subQ9})])]}),makeQuery(id+"F47.opFillet","BLEND_FACE",FACE,{"disambiguationData":[OSD([subQ5,subQ7]),TDD([makeQuery(id+"F42.boolean.opBoolean","COPY",EDGE,{"disambiguationData":[TD([makeQuery(id+"F8.opLoft","SWEPT_FACE",FACE,{"disambiguationData":[OSD([sQuery(id+"F3.wireOp",EDGE,"E20.13.0"),subQ59,subQ58,sQuery(id+"F4.wireOp",EDGE,"E26.13.0"),subQ57,subQ56])]})])],"derivedFrom":subQ9})])]}),makeQuery(id+"F47.opFillet","BLEND_FACE",FACE,{"disambiguationData":[OSD([subQ5,subQ7]),TDD([makeQuery(id+"F42.boolean.opBoolean","COPY",EDGE,{"disambiguationData":[TD([makeQuery(id+"F9.opLoft","SWEPT_FACE",FACE,{"disambiguationData":[OSD([sQuery(id+"F3.wireOp",EDGE,"E20.12.0"),subQ55,subQ54,sQuery(id+"F4.wireOp",EDGE,"E26.12.0"),subQ53,subQ52])]})])],"derivedFrom":subQ9})])]}),makeQuery(id+"F47.opFillet","BLEND_FACE",FACE,{"disambiguationData":[OSD([subQ5,subQ7]),TDD([makeQuery(id+"F42.boolean.opBoolean","COPY",EDGE,{"disambiguationData":[TD([makeQuery(id+"F10.opLoft","SWEPT_FACE",FACE,{"disambiguationData":[OSD([sQuery(id+"F3.wireOp",EDGE,"E20.11.0"),subQ51,subQ50,sQuery(id+"F4.wireOp",EDGE,"E26.11.0"),subQ49,subQ48])]})])],"derivedFrom":subQ9})])]}),makeQuery(id+"F47.opFillet","BLEND_FACE",FACE,{"disambiguationData":[OSD([subQ5,subQ7]),TDD([makeQuery(id+"F42.boolean.opBoolean","COPY",EDGE,{"disambiguationData":[TD([makeQuery(id+"F11.opLoft","SWEPT_FACE",FACE,{"disambiguationData":[OSD([sQuery(id+"F3.wireOp",EDGE,"E20.10.0"),subQ47,subQ46,sQuery(id+"F4.wireOp",EDGE,"E26.10.0"),subQ45,subQ44])]})])],"derivedFrom":subQ9})])]}),makeQuery(id+"F47.opFillet","BLEND_FACE",FACE,{"disambiguationData":[OSD([subQ5,subQ7]),TDD([makeQuery(id+"F42.boolean.opBoolean","COPY",EDGE,{"disambiguationData":[TD([subQ43])],"derivedFrom":subQ9})])]}),makeQuery(id+"F47.opFillet","BLEND_FACE",FACE,{"disambiguationData":[OSD([subQ5,subQ7]),TDD([makeQuery(id+"F42.boolean.opBoolean","COPY",EDGE,{"disambiguationData":[TD([makeQuery(id+"F13.opLoft","SWEPT_FACE",FACE,{"disambiguationData":[OSD([sQuery(id+"F3.wireOp",EDGE,"E20.8.0"),subQ37,subQ36,sQuery(id+"F4.wireOp",EDGE,"E26.8.0"),subQ35,subQ34])]})])],"derivedFrom":subQ9})])]}),makeQuery(id+"F47.opFillet","BLEND_FACE",FACE,{"disambiguationData":[OSD([subQ5,subQ7]),TDD([makeQuery(id+"F42.boolean.opBoolean","COPY",EDGE,{"disambiguationData":[TD([makeQuery(id+"F14.opLoft","SWEPT_FACE",FACE,{"disambiguationData":[OSD([sQuery(id+"F3.wireOp",EDGE,"E20.7.0"),subQ33,subQ32,sQuery(id+"F4.wireOp",EDGE,"E26.7.0"),subQ31,subQ30])]})])],"derivedFrom":subQ9})])]}),makeQuery(id+"F47.opFillet","BLEND_FACE",FACE,{"disambiguationData":[OSD([subQ5,subQ7]),TDD([makeQuery(id+"F42.boolean.opBoolean","COPY",EDGE,{"disambiguationData":[TD([makeQuery(id+"F15.opLoft","SWEPT_FACE",FACE,{"disambiguationData":[OSD([sQuery(id+"F3.wireOp",EDGE,"E20.6.0"),subQ29,subQ28,sQuery(id+"F4.wireOp",EDGE,"E26.6.0"),subQ27,subQ26])]})])],"derivedFrom":subQ9})])]}),makeQuery(id+"F47.opFillet","BLEND_FACE",FACE,{"disambiguationData":[OSD([subQ5,subQ7]),TDD([makeQuery(id+"F42.boolean.opBoolean","COPY",EDGE,{"disambiguationData":[TD([makeQuery(id+"F16.opLoft","SWEPT_FACE",FACE,{"disambiguationData":[OSD([sQuery(id+"F3.wireOp",EDGE,"E20.5.0"),subQ25,subQ24,sQuery(id+"F4.wireOp",EDGE,"E26.5.0"),subQ23,subQ22])]})])],"derivedFrom":subQ9})])]}),makeQuery(id+"F47.opFillet","BLEND_FACE",FACE,{"disambiguationData":[OSD([subQ5,subQ7]),TDD([makeQuery(id+"F42.boolean.opBoolean","COPY",EDGE,{"disambiguationData":[TD([makeQuery(id+"F17.opLoft","SWEPT_FACE",FACE,{"disambiguationData":[OSD([sQuery(id+"F3.wireOp",EDGE,"E20.4.0"),subQ21,subQ20,sQuery(id+"F4.wireOp",EDGE,"E26.4.0"),subQ19,subQ18])]})])],"derivedFrom":subQ9})])]}),makeQuery(id+"F47.opFillet","BLEND_FACE",FACE,{"disambiguationData":[OSD([subQ5,subQ7]),TDD([makeQuery(id+"F42.boolean.opBoolean","COPY",EDGE,{"disambiguationData":[TD([makeQuery(id+"F18.opLoft","SWEPT_FACE",FACE,{"disambiguationData":[OSD([sQuery(id+"F3.wireOp",EDGE,"E20.3.0"),subQ17,subQ16,sQuery(id+"F4.wireOp",EDGE,"E26.3.0"),subQ15,subQ14])]})])],"derivedFrom":subQ9})])]}),makeQuery(id+"F47.opFillet","BLEND_FACE",FACE,{"disambiguationData":[OSD([subQ5,subQ7]),TDD([makeQuery(id+"F42.boolean.opBoolean","COPY",EDGE,{"disambiguationData":[TD([makeQuery(id+"F19.opLoft","SWEPT_FACE",FACE,{"disambiguationData":[OSD([sQuery(id+"F3.wireOp",EDGE,"E20.2.0"),subQ13,subQ12,sQuery(id+"F4.wireOp",EDGE,"E26.2.0"),subQ11,subQ10])]})])],"derivedFrom":subQ9})])]}),makeQuery(id+"F47.opFillet","BLEND_FACE",FACE,{"disambiguationData":[OSD([subQ5,subQ7]),TDD([makeQuery(id+"F42.boolean.opBoolean","COPY",EDGE,{"disambiguationData":[TD([makeQuery(id+"F20.opLoft","SWEPT_FACE",FACE,{"disambiguationData":[OSD([sQuery(id+"F3.wireOp",EDGE,"E20.1.0"),subQ4,subQ3,sQuery(id+"F4.wireOp",EDGE,"E26.1.0"),subQ2,subQ1])]})])],"derivedFrom":subQ9})])]})]});}
            var Q62;
            {var subQ0=makeQuery(id+"F40.opExtrude","CAP_FACE",FACE,{"disambiguationData":[OSD([sQuery(id+"F39.wireOp",EDGE,"E29"),sQuery(id+"F39.wireOp",EDGE,"E30")])],"isStart":false});var subQ1=sQuery(id+"F4.wireOp",EDGE,"E26.1.3");var subQ2=sQuery(id+"F4.wireOp",EDGE,"E26.1.2");var subQ3=sQuery(id+"F3.wireOp",EDGE,"E20.1.3");var subQ4=sQuery(id+"F3.wireOp",EDGE,"E20.1.1");var subQ5=sQuery(id+"F41.wireOp",EDGE,"E35");var subQ6=makeQuery(id+"F42.opRevolve","SWEPT_FACE",FACE,{"disambiguationData":[OSD([subQ5])]});var subQ7=sQuery(id+"F41.wireOp",EDGE,"E36");var subQ8=makeQuery(id+"F42.opRevolve","SWEPT_FACE",FACE,{"disambiguationData":[OSD([subQ7])]});var subQ9=makeQuery(id+"F42.opRevolve","SWEPT_EDGE",EDGE,{"disambiguationData":[OSD([subQ5,subQ7])]});var subQ10=sQuery(id+"F4.wireOp",EDGE,"E26.2.3");var subQ11=sQuery(id+"F4.wireOp",EDGE,"E26.2.2");var subQ12=sQuery(id+"F3.wireOp",EDGE,"E20.2.3");var subQ13=sQuery(id+"F3.wireOp",EDGE,"E20.2.1");var subQ14=sQuery(id+"F4.wireOp",EDGE,"E26.3.3");var subQ15=sQuery(id+"F4.wireOp",EDGE,"E26.3.2");var subQ16=sQuery(id+"F3.wireOp",EDGE,"E20.3.3");var subQ17=sQuery(id+"F3.wireOp",EDGE,"E20.3.1");var subQ18=sQuery(id+"F4.wireOp",EDGE,"E26.4.3");var subQ19=sQuery(id+"F4.wireOp",EDGE,"E26.4.2");var subQ20=sQuery(id+"F3.wireOp",EDGE,"E20.4.3");var subQ21=sQuery(id+"F3.wireOp",EDGE,"E20.4.1");var subQ22=sQuery(id+"F4.wireOp",EDGE,"E26.5.3");var subQ23=sQuery(id+"F4.wireOp",EDGE,"E26.5.2");var subQ24=sQuery(id+"F3.wireOp",EDGE,"E20.5.3");var subQ25=sQuery(id+"F3.wireOp",EDGE,"E20.5.1");var subQ26=sQuery(id+"F4.wireOp",EDGE,"E26.6.3");var subQ27=sQuery(id+"F4.wireOp",EDGE,"E26.6.2");var subQ28=sQuery(id+"F3.wireOp",EDGE,"E20.6.3");var subQ29=sQuery(id+"F3.wireOp",EDGE,"E20.6.1");var subQ30=sQuery(id+"F4.wireOp",EDGE,"E26.7.3");var subQ31=sQuery(id+"F4.wireOp",EDGE,"E26.7.2");var subQ32=sQuery(id+"F3.wireOp",EDGE,"E20.7.3");var subQ33=sQuery(id+"F3.wireOp",EDGE,"E20.7.1");var subQ35=makeQuery(id+"F14.opLoft","SWEPT_FACE",FACE,{"disambiguationData":[OSD([sQuery(id+"F3.wireOp",EDGE,"E20.7.0"),subQ33,subQ32,sQuery(id+"F4.wireOp",EDGE,"E26.7.0"),subQ31,subQ30])]});var subQ36=sQuery(id+"F4.wireOp",EDGE,"E26.8.3");var subQ37=sQuery(id+"F4.wireOp",EDGE,"E26.8.2");var subQ38=sQuery(id+"F3.wireOp",EDGE,"E20.8.3");var subQ39=sQuery(id+"F3.wireOp",EDGE,"E20.8.1");var subQ40=sQuery(id+"F4.wireOp",EDGE,"E26.9.3");var subQ41=sQuery(id+"F4.wireOp",EDGE,"E26.9.2");var subQ42=sQuery(id+"F3.wireOp",EDGE,"E20.9.3");var subQ43=sQuery(id+"F3.wireOp",EDGE,"E20.9.1");var subQ44=sQuery(id+"F4.wireOp",EDGE,"E26.10.3");var subQ45=sQuery(id+"F4.wireOp",EDGE,"E26.10.2");var subQ46=sQuery(id+"F3.wireOp",EDGE,"E20.10.3");var subQ47=sQuery(id+"F3.wireOp",EDGE,"E20.10.1");var subQ48=sQuery(id+"F4.wireOp",EDGE,"E26.11.3");var subQ49=sQuery(id+"F4.wireOp",EDGE,"E26.11.2");var subQ50=sQuery(id+"F3.wireOp",EDGE,"E20.11.3");var subQ51=sQuery(id+"F3.wireOp",EDGE,"E20.11.1");var subQ52=sQuery(id+"F4.wireOp",EDGE,"E26.12.3");var subQ53=sQuery(id+"F4.wireOp",EDGE,"E26.12.2");var subQ54=sQuery(id+"F3.wireOp",EDGE,"E20.12.3");var subQ55=sQuery(id+"F3.wireOp",EDGE,"E20.12.1");var subQ56=sQuery(id+"F4.wireOp",EDGE,"E26.13.3");var subQ57=sQuery(id+"F4.wireOp",EDGE,"E26.13.2");var subQ58=sQuery(id+"F3.wireOp",EDGE,"E20.13.3");var subQ59=sQuery(id+"F3.wireOp",EDGE,"E20.13.1");var subQ60=sQuery(id+"F4.wireOp",EDGE,"E26.14.3");var subQ61=sQuery(id+"F4.wireOp",EDGE,"E26.14.2");var subQ62=sQuery(id+"F3.wireOp",EDGE,"E20.14.3");var subQ63=sQuery(id+"F3.wireOp",EDGE,"E20.14.1");var subQ64=sQuery(id+"F4.wireOp",EDGE,"E26.15.3");var subQ65=sQuery(id+"F4.wireOp",EDGE,"E26.15.2");var subQ66=sQuery(id+"F3.wireOp",EDGE,"E20.15.3");var subQ67=sQuery(id+"F3.wireOp",EDGE,"E20.15.1");var subQ68=sQuery(id+"F4.wireOp",EDGE,"E23");var subQ69=sQuery(id+"F4.wireOp",EDGE,"E22");var subQ70=sQuery(id+"F3.wireOp",EDGE,"E18.top");var subQ71=sQuery(id+"F3.wireOp",EDGE,"E18.bottom");var subQ74=makeQuery(id+"F42.boolean.opBoolean","COPY",FACE,{"disambiguationData":[TD([subQ35])],"derivedFrom":subQ6});var subQ75=makeQuery(id+"F14.boolean.opBoolean","INTERSECT",EDGE,{"derivedFrom":[makeQuery(id+"F1.opRevolve","SWEPT_FACE",FACE,{"disambiguationData":[OSD([sQuery(id+"F0.wireOp",EDGE,"E4")])]}),subQ35]});Q62=makeQuery(id+"F48.opFillet","BLEND_EDGE",EDGE,{"blendedFrom":[makeQuery(id+"F47.opFillet","TWEAK_EDGE",EDGE,{"derivedFrom":[makeQuery(id+"F45.opFillet","BLEND_VERTEX",VERTEX,{"blendedFrom":[subQ75,subQ35,subQ74],"blendedInto":[subQ35,subQ74]}),makeQuery(id+"F45.opFillet","BLEND_VERTEX",VERTEX,{"blendedFrom":[subQ75,makeQuery(id+"F42.boolean.opBoolean","MERGE",FACE,{"derivedFrom":[subQ0,subQ8]}),subQ74],"blendedInto":[makeQuery(id+"F42.boolean.opBoolean","MERGE",FACE,{"derivedFrom":[subQ0,subQ8]}),subQ74]})]}),makeQuery(id+"F47.opFillet","BLEND_FACE",FACE,{"disambiguationData":[OSD([subQ5,subQ7]),TDD([makeQuery(id+"F42.boolean.opBoolean","COPY",EDGE,{"disambiguationData":[TD([makeQuery(id+"F5.opLoft","SWEPT_FACE",FACE,{"disambiguationData":[OSD([subQ71,subQ70,sQuery(id+"F3.wireOp",EDGE,"E18.left"),sQuery(id+"F4.wireOp",EDGE,"E21"),subQ69,subQ68])]})])],"derivedFrom":subQ9})])]}),makeQuery(id+"F47.opFillet","BLEND_FACE",FACE,{"disambiguationData":[OSD([subQ5,subQ7]),TDD([makeQuery(id+"F42.boolean.opBoolean","COPY",EDGE,{"disambiguationData":[TD([makeQuery(id+"F6.opLoft","SWEPT_FACE",FACE,{"disambiguationData":[OSD([sQuery(id+"F3.wireOp",EDGE,"E20.15.0"),subQ67,subQ66,sQuery(id+"F4.wireOp",EDGE,"E26.15.0"),subQ65,subQ64])]})])],"derivedFrom":subQ9})])]}),makeQuery(id+"F47.opFillet","BLEND_FACE",FACE,{"disambiguationData":[OSD([subQ5,subQ7]),TDD([makeQuery(id+"F42.boolean.opBoolean","COPY",EDGE,{"disambiguationData":[TD([makeQuery(id+"F7.opLoft","SWEPT_FACE",FACE,{"disambiguationData":[OSD([sQuery(id+"F3.wireOp",EDGE,"E20.14.0"),subQ63,subQ62,sQuery(id+"F4.wireOp",EDGE,"E26.14.0"),subQ61,subQ60])]})])],"derivedFrom":subQ9})])]}),makeQuery(id+"F47.opFillet","BLEND_FACE",FACE,{"disambiguationData":[OSD([subQ5,subQ7]),TDD([makeQuery(id+"F42.boolean.opBoolean","COPY",EDGE,{"disambiguationData":[TD([makeQuery(id+"F8.opLoft","SWEPT_FACE",FACE,{"disambiguationData":[OSD([sQuery(id+"F3.wireOp",EDGE,"E20.13.0"),subQ59,subQ58,sQuery(id+"F4.wireOp",EDGE,"E26.13.0"),subQ57,subQ56])]})])],"derivedFrom":subQ9})])]}),makeQuery(id+"F47.opFillet","BLEND_FACE",FACE,{"disambiguationData":[OSD([subQ5,subQ7]),TDD([makeQuery(id+"F42.boolean.opBoolean","COPY",EDGE,{"disambiguationData":[TD([makeQuery(id+"F9.opLoft","SWEPT_FACE",FACE,{"disambiguationData":[OSD([sQuery(id+"F3.wireOp",EDGE,"E20.12.0"),subQ55,subQ54,sQuery(id+"F4.wireOp",EDGE,"E26.12.0"),subQ53,subQ52])]})])],"derivedFrom":subQ9})])]}),makeQuery(id+"F47.opFillet","BLEND_FACE",FACE,{"disambiguationData":[OSD([subQ5,subQ7]),TDD([makeQuery(id+"F42.boolean.opBoolean","COPY",EDGE,{"disambiguationData":[TD([makeQuery(id+"F10.opLoft","SWEPT_FACE",FACE,{"disambiguationData":[OSD([sQuery(id+"F3.wireOp",EDGE,"E20.11.0"),subQ51,subQ50,sQuery(id+"F4.wireOp",EDGE,"E26.11.0"),subQ49,subQ48])]})])],"derivedFrom":subQ9})])]}),makeQuery(id+"F47.opFillet","BLEND_FACE",FACE,{"disambiguationData":[OSD([subQ5,subQ7]),TDD([makeQuery(id+"F42.boolean.opBoolean","COPY",EDGE,{"disambiguationData":[TD([makeQuery(id+"F11.opLoft","SWEPT_FACE",FACE,{"disambiguationData":[OSD([sQuery(id+"F3.wireOp",EDGE,"E20.10.0"),subQ47,subQ46,sQuery(id+"F4.wireOp",EDGE,"E26.10.0"),subQ45,subQ44])]})])],"derivedFrom":subQ9})])]}),makeQuery(id+"F47.opFillet","BLEND_FACE",FACE,{"disambiguationData":[OSD([subQ5,subQ7]),TDD([makeQuery(id+"F42.boolean.opBoolean","COPY",EDGE,{"disambiguationData":[TD([makeQuery(id+"F12.opLoft","SWEPT_FACE",FACE,{"disambiguationData":[OSD([sQuery(id+"F3.wireOp",EDGE,"E20.9.0"),subQ43,subQ42,sQuery(id+"F4.wireOp",EDGE,"E26.9.0"),subQ41,subQ40])]})])],"derivedFrom":subQ9})])]}),makeQuery(id+"F47.opFillet","BLEND_FACE",FACE,{"disambiguationData":[OSD([subQ5,subQ7]),TDD([makeQuery(id+"F42.boolean.opBoolean","COPY",EDGE,{"disambiguationData":[TD([makeQuery(id+"F13.opLoft","SWEPT_FACE",FACE,{"disambiguationData":[OSD([sQuery(id+"F3.wireOp",EDGE,"E20.8.0"),subQ39,subQ38,sQuery(id+"F4.wireOp",EDGE,"E26.8.0"),subQ37,subQ36])]})])],"derivedFrom":subQ9})])]}),makeQuery(id+"F47.opFillet","BLEND_FACE",FACE,{"disambiguationData":[OSD([subQ5,subQ7]),TDD([makeQuery(id+"F42.boolean.opBoolean","COPY",EDGE,{"disambiguationData":[TD([subQ35])],"derivedFrom":subQ9})])]}),makeQuery(id+"F47.opFillet","BLEND_FACE",FACE,{"disambiguationData":[OSD([subQ5,subQ7]),TDD([makeQuery(id+"F42.boolean.opBoolean","COPY",EDGE,{"disambiguationData":[TD([makeQuery(id+"F15.opLoft","SWEPT_FACE",FACE,{"disambiguationData":[OSD([sQuery(id+"F3.wireOp",EDGE,"E20.6.0"),subQ29,subQ28,sQuery(id+"F4.wireOp",EDGE,"E26.6.0"),subQ27,subQ26])]})])],"derivedFrom":subQ9})])]}),makeQuery(id+"F47.opFillet","BLEND_FACE",FACE,{"disambiguationData":[OSD([subQ5,subQ7]),TDD([makeQuery(id+"F42.boolean.opBoolean","COPY",EDGE,{"disambiguationData":[TD([makeQuery(id+"F16.opLoft","SWEPT_FACE",FACE,{"disambiguationData":[OSD([sQuery(id+"F3.wireOp",EDGE,"E20.5.0"),subQ25,subQ24,sQuery(id+"F4.wireOp",EDGE,"E26.5.0"),subQ23,subQ22])]})])],"derivedFrom":subQ9})])]}),makeQuery(id+"F47.opFillet","BLEND_FACE",FACE,{"disambiguationData":[OSD([subQ5,subQ7]),TDD([makeQuery(id+"F42.boolean.opBoolean","COPY",EDGE,{"disambiguationData":[TD([makeQuery(id+"F17.opLoft","SWEPT_FACE",FACE,{"disambiguationData":[OSD([sQuery(id+"F3.wireOp",EDGE,"E20.4.0"),subQ21,subQ20,sQuery(id+"F4.wireOp",EDGE,"E26.4.0"),subQ19,subQ18])]})])],"derivedFrom":subQ9})])]}),makeQuery(id+"F47.opFillet","BLEND_FACE",FACE,{"disambiguationData":[OSD([subQ5,subQ7]),TDD([makeQuery(id+"F42.boolean.opBoolean","COPY",EDGE,{"disambiguationData":[TD([makeQuery(id+"F18.opLoft","SWEPT_FACE",FACE,{"disambiguationData":[OSD([sQuery(id+"F3.wireOp",EDGE,"E20.3.0"),subQ17,subQ16,sQuery(id+"F4.wireOp",EDGE,"E26.3.0"),subQ15,subQ14])]})])],"derivedFrom":subQ9})])]}),makeQuery(id+"F47.opFillet","BLEND_FACE",FACE,{"disambiguationData":[OSD([subQ5,subQ7]),TDD([makeQuery(id+"F42.boolean.opBoolean","COPY",EDGE,{"disambiguationData":[TD([makeQuery(id+"F19.opLoft","SWEPT_FACE",FACE,{"disambiguationData":[OSD([sQuery(id+"F3.wireOp",EDGE,"E20.2.0"),subQ13,subQ12,sQuery(id+"F4.wireOp",EDGE,"E26.2.0"),subQ11,subQ10])]})])],"derivedFrom":subQ9})])]}),makeQuery(id+"F47.opFillet","BLEND_FACE",FACE,{"disambiguationData":[OSD([subQ5,subQ7]),TDD([makeQuery(id+"F42.boolean.opBoolean","COPY",EDGE,{"disambiguationData":[TD([makeQuery(id+"F20.opLoft","SWEPT_FACE",FACE,{"disambiguationData":[OSD([sQuery(id+"F3.wireOp",EDGE,"E20.1.0"),subQ4,subQ3,sQuery(id+"F4.wireOp",EDGE,"E26.1.0"),subQ2,subQ1])]})])],"derivedFrom":subQ9})])]})],"blendedInto":[makeQuery(id+"F47.opFillet","BLEND_FACE",FACE,{"disambiguationData":[OSD([subQ5,subQ7]),TDD([makeQuery(id+"F42.boolean.opBoolean","COPY",EDGE,{"disambiguationData":[TD([makeQuery(id+"F5.opLoft","SWEPT_FACE",FACE,{"disambiguationData":[OSD([subQ71,subQ70,sQuery(id+"F3.wireOp",EDGE,"E18.left"),sQuery(id+"F4.wireOp",EDGE,"E21"),subQ69,subQ68])]})])],"derivedFrom":subQ9})])]}),makeQuery(id+"F47.opFillet","BLEND_FACE",FACE,{"disambiguationData":[OSD([subQ5,subQ7]),TDD([makeQuery(id+"F42.boolean.opBoolean","COPY",EDGE,{"disambiguationData":[TD([makeQuery(id+"F6.opLoft","SWEPT_FACE",FACE,{"disambiguationData":[OSD([sQuery(id+"F3.wireOp",EDGE,"E20.15.0"),subQ67,subQ66,sQuery(id+"F4.wireOp",EDGE,"E26.15.0"),subQ65,subQ64])]})])],"derivedFrom":subQ9})])]}),makeQuery(id+"F47.opFillet","BLEND_FACE",FACE,{"disambiguationData":[OSD([subQ5,subQ7]),TDD([makeQuery(id+"F42.boolean.opBoolean","COPY",EDGE,{"disambiguationData":[TD([makeQuery(id+"F7.opLoft","SWEPT_FACE",FACE,{"disambiguationData":[OSD([sQuery(id+"F3.wireOp",EDGE,"E20.14.0"),subQ63,subQ62,sQuery(id+"F4.wireOp",EDGE,"E26.14.0"),subQ61,subQ60])]})])],"derivedFrom":subQ9})])]}),makeQuery(id+"F47.opFillet","BLEND_FACE",FACE,{"disambiguationData":[OSD([subQ5,subQ7]),TDD([makeQuery(id+"F42.boolean.opBoolean","COPY",EDGE,{"disambiguationData":[TD([makeQuery(id+"F8.opLoft","SWEPT_FACE",FACE,{"disambiguationData":[OSD([sQuery(id+"F3.wireOp",EDGE,"E20.13.0"),subQ59,subQ58,sQuery(id+"F4.wireOp",EDGE,"E26.13.0"),subQ57,subQ56])]})])],"derivedFrom":subQ9})])]}),makeQuery(id+"F47.opFillet","BLEND_FACE",FACE,{"disambiguationData":[OSD([subQ5,subQ7]),TDD([makeQuery(id+"F42.boolean.opBoolean","COPY",EDGE,{"disambiguationData":[TD([makeQuery(id+"F9.opLoft","SWEPT_FACE",FACE,{"disambiguationData":[OSD([sQuery(id+"F3.wireOp",EDGE,"E20.12.0"),subQ55,subQ54,sQuery(id+"F4.wireOp",EDGE,"E26.12.0"),subQ53,subQ52])]})])],"derivedFrom":subQ9})])]}),makeQuery(id+"F47.opFillet","BLEND_FACE",FACE,{"disambiguationData":[OSD([subQ5,subQ7]),TDD([makeQuery(id+"F42.boolean.opBoolean","COPY",EDGE,{"disambiguationData":[TD([makeQuery(id+"F10.opLoft","SWEPT_FACE",FACE,{"disambiguationData":[OSD([sQuery(id+"F3.wireOp",EDGE,"E20.11.0"),subQ51,subQ50,sQuery(id+"F4.wireOp",EDGE,"E26.11.0"),subQ49,subQ48])]})])],"derivedFrom":subQ9})])]}),makeQuery(id+"F47.opFillet","BLEND_FACE",FACE,{"disambiguationData":[OSD([subQ5,subQ7]),TDD([makeQuery(id+"F42.boolean.opBoolean","COPY",EDGE,{"disambiguationData":[TD([makeQuery(id+"F11.opLoft","SWEPT_FACE",FACE,{"disambiguationData":[OSD([sQuery(id+"F3.wireOp",EDGE,"E20.10.0"),subQ47,subQ46,sQuery(id+"F4.wireOp",EDGE,"E26.10.0"),subQ45,subQ44])]})])],"derivedFrom":subQ9})])]}),makeQuery(id+"F47.opFillet","BLEND_FACE",FACE,{"disambiguationData":[OSD([subQ5,subQ7]),TDD([makeQuery(id+"F42.boolean.opBoolean","COPY",EDGE,{"disambiguationData":[TD([makeQuery(id+"F12.opLoft","SWEPT_FACE",FACE,{"disambiguationData":[OSD([sQuery(id+"F3.wireOp",EDGE,"E20.9.0"),subQ43,subQ42,sQuery(id+"F4.wireOp",EDGE,"E26.9.0"),subQ41,subQ40])]})])],"derivedFrom":subQ9})])]}),makeQuery(id+"F47.opFillet","BLEND_FACE",FACE,{"disambiguationData":[OSD([subQ5,subQ7]),TDD([makeQuery(id+"F42.boolean.opBoolean","COPY",EDGE,{"disambiguationData":[TD([makeQuery(id+"F13.opLoft","SWEPT_FACE",FACE,{"disambiguationData":[OSD([sQuery(id+"F3.wireOp",EDGE,"E20.8.0"),subQ39,subQ38,sQuery(id+"F4.wireOp",EDGE,"E26.8.0"),subQ37,subQ36])]})])],"derivedFrom":subQ9})])]}),makeQuery(id+"F47.opFillet","BLEND_FACE",FACE,{"disambiguationData":[OSD([subQ5,subQ7]),TDD([makeQuery(id+"F42.boolean.opBoolean","COPY",EDGE,{"disambiguationData":[TD([subQ35])],"derivedFrom":subQ9})])]}),makeQuery(id+"F47.opFillet","BLEND_FACE",FACE,{"disambiguationData":[OSD([subQ5,subQ7]),TDD([makeQuery(id+"F42.boolean.opBoolean","COPY",EDGE,{"disambiguationData":[TD([makeQuery(id+"F15.opLoft","SWEPT_FACE",FACE,{"disambiguationData":[OSD([sQuery(id+"F3.wireOp",EDGE,"E20.6.0"),subQ29,subQ28,sQuery(id+"F4.wireOp",EDGE,"E26.6.0"),subQ27,subQ26])]})])],"derivedFrom":subQ9})])]}),makeQuery(id+"F47.opFillet","BLEND_FACE",FACE,{"disambiguationData":[OSD([subQ5,subQ7]),TDD([makeQuery(id+"F42.boolean.opBoolean","COPY",EDGE,{"disambiguationData":[TD([makeQuery(id+"F16.opLoft","SWEPT_FACE",FACE,{"disambiguationData":[OSD([sQuery(id+"F3.wireOp",EDGE,"E20.5.0"),subQ25,subQ24,sQuery(id+"F4.wireOp",EDGE,"E26.5.0"),subQ23,subQ22])]})])],"derivedFrom":subQ9})])]}),makeQuery(id+"F47.opFillet","BLEND_FACE",FACE,{"disambiguationData":[OSD([subQ5,subQ7]),TDD([makeQuery(id+"F42.boolean.opBoolean","COPY",EDGE,{"disambiguationData":[TD([makeQuery(id+"F17.opLoft","SWEPT_FACE",FACE,{"disambiguationData":[OSD([sQuery(id+"F3.wireOp",EDGE,"E20.4.0"),subQ21,subQ20,sQuery(id+"F4.wireOp",EDGE,"E26.4.0"),subQ19,subQ18])]})])],"derivedFrom":subQ9})])]}),makeQuery(id+"F47.opFillet","BLEND_FACE",FACE,{"disambiguationData":[OSD([subQ5,subQ7]),TDD([makeQuery(id+"F42.boolean.opBoolean","COPY",EDGE,{"disambiguationData":[TD([makeQuery(id+"F18.opLoft","SWEPT_FACE",FACE,{"disambiguationData":[OSD([sQuery(id+"F3.wireOp",EDGE,"E20.3.0"),subQ17,subQ16,sQuery(id+"F4.wireOp",EDGE,"E26.3.0"),subQ15,subQ14])]})])],"derivedFrom":subQ9})])]}),makeQuery(id+"F47.opFillet","BLEND_FACE",FACE,{"disambiguationData":[OSD([subQ5,subQ7]),TDD([makeQuery(id+"F42.boolean.opBoolean","COPY",EDGE,{"disambiguationData":[TD([makeQuery(id+"F19.opLoft","SWEPT_FACE",FACE,{"disambiguationData":[OSD([sQuery(id+"F3.wireOp",EDGE,"E20.2.0"),subQ13,subQ12,sQuery(id+"F4.wireOp",EDGE,"E26.2.0"),subQ11,subQ10])]})])],"derivedFrom":subQ9})])]}),makeQuery(id+"F47.opFillet","BLEND_FACE",FACE,{"disambiguationData":[OSD([subQ5,subQ7]),TDD([makeQuery(id+"F42.boolean.opBoolean","COPY",EDGE,{"disambiguationData":[TD([makeQuery(id+"F20.opLoft","SWEPT_FACE",FACE,{"disambiguationData":[OSD([sQuery(id+"F3.wireOp",EDGE,"E20.1.0"),subQ4,subQ3,sQuery(id+"F4.wireOp",EDGE,"E26.1.0"),subQ2,subQ1])]})])],"derivedFrom":subQ9})])]})]});}
            var Q63;
            {var subQ0=makeQuery(id+"F40.opExtrude","CAP_FACE",FACE,{"disambiguationData":[OSD([sQuery(id+"F39.wireOp",EDGE,"E29"),sQuery(id+"F39.wireOp",EDGE,"E30")])],"isStart":false});var subQ1=sQuery(id+"F4.wireOp",EDGE,"E26.1.3");var subQ2=sQuery(id+"F4.wireOp",EDGE,"E26.1.2");var subQ3=sQuery(id+"F3.wireOp",EDGE,"E20.1.3");var subQ4=sQuery(id+"F3.wireOp",EDGE,"E20.1.1");var subQ5=sQuery(id+"F41.wireOp",EDGE,"E35");var subQ6=makeQuery(id+"F42.opRevolve","SWEPT_FACE",FACE,{"disambiguationData":[OSD([subQ5])]});var subQ7=sQuery(id+"F41.wireOp",EDGE,"E36");var subQ8=makeQuery(id+"F42.opRevolve","SWEPT_FACE",FACE,{"disambiguationData":[OSD([subQ7])]});var subQ9=makeQuery(id+"F42.opRevolve","SWEPT_EDGE",EDGE,{"disambiguationData":[OSD([subQ5,subQ7])]});var subQ10=sQuery(id+"F4.wireOp",EDGE,"E26.2.3");var subQ11=sQuery(id+"F4.wireOp",EDGE,"E26.2.2");var subQ12=sQuery(id+"F3.wireOp",EDGE,"E20.2.3");var subQ13=sQuery(id+"F3.wireOp",EDGE,"E20.2.1");var subQ14=sQuery(id+"F4.wireOp",EDGE,"E26.3.3");var subQ15=sQuery(id+"F4.wireOp",EDGE,"E26.3.2");var subQ16=sQuery(id+"F3.wireOp",EDGE,"E20.3.3");var subQ17=sQuery(id+"F3.wireOp",EDGE,"E20.3.1");var subQ18=sQuery(id+"F4.wireOp",EDGE,"E26.4.3");var subQ19=sQuery(id+"F4.wireOp",EDGE,"E26.4.2");var subQ20=sQuery(id+"F3.wireOp",EDGE,"E20.4.3");var subQ21=sQuery(id+"F3.wireOp",EDGE,"E20.4.1");var subQ22=sQuery(id+"F4.wireOp",EDGE,"E26.5.3");var subQ23=sQuery(id+"F4.wireOp",EDGE,"E26.5.2");var subQ24=sQuery(id+"F3.wireOp",EDGE,"E20.5.3");var subQ25=sQuery(id+"F3.wireOp",EDGE,"E20.5.1");var subQ26=sQuery(id+"F4.wireOp",EDGE,"E26.6.3");var subQ27=sQuery(id+"F4.wireOp",EDGE,"E26.6.2");var subQ28=sQuery(id+"F3.wireOp",EDGE,"E20.6.3");var subQ29=sQuery(id+"F3.wireOp",EDGE,"E20.6.1");var subQ30=sQuery(id+"F4.wireOp",EDGE,"E26.7.3");var subQ31=sQuery(id+"F4.wireOp",EDGE,"E26.7.2");var subQ32=sQuery(id+"F3.wireOp",EDGE,"E20.7.3");var subQ33=sQuery(id+"F3.wireOp",EDGE,"E20.7.1");var subQ34=sQuery(id+"F4.wireOp",EDGE,"E26.8.3");var subQ35=sQuery(id+"F4.wireOp",EDGE,"E26.8.2");var subQ36=sQuery(id+"F3.wireOp",EDGE,"E20.8.3");var subQ37=sQuery(id+"F3.wireOp",EDGE,"E20.8.1");var subQ39=makeQuery(id+"F13.opLoft","SWEPT_FACE",FACE,{"disambiguationData":[OSD([sQuery(id+"F3.wireOp",EDGE,"E20.8.0"),subQ37,subQ36,sQuery(id+"F4.wireOp",EDGE,"E26.8.0"),subQ35,subQ34])]});var subQ40=sQuery(id+"F4.wireOp",EDGE,"E26.9.3");var subQ41=sQuery(id+"F4.wireOp",EDGE,"E26.9.2");var subQ42=sQuery(id+"F3.wireOp",EDGE,"E20.9.3");var subQ43=sQuery(id+"F3.wireOp",EDGE,"E20.9.1");var subQ44=sQuery(id+"F4.wireOp",EDGE,"E26.10.3");var subQ45=sQuery(id+"F4.wireOp",EDGE,"E26.10.2");var subQ46=sQuery(id+"F3.wireOp",EDGE,"E20.10.3");var subQ47=sQuery(id+"F3.wireOp",EDGE,"E20.10.1");var subQ48=sQuery(id+"F4.wireOp",EDGE,"E26.11.3");var subQ49=sQuery(id+"F4.wireOp",EDGE,"E26.11.2");var subQ50=sQuery(id+"F3.wireOp",EDGE,"E20.11.3");var subQ51=sQuery(id+"F3.wireOp",EDGE,"E20.11.1");var subQ52=sQuery(id+"F4.wireOp",EDGE,"E26.12.3");var subQ53=sQuery(id+"F4.wireOp",EDGE,"E26.12.2");var subQ54=sQuery(id+"F3.wireOp",EDGE,"E20.12.3");var subQ55=sQuery(id+"F3.wireOp",EDGE,"E20.12.1");var subQ56=sQuery(id+"F4.wireOp",EDGE,"E26.13.3");var subQ57=sQuery(id+"F4.wireOp",EDGE,"E26.13.2");var subQ58=sQuery(id+"F3.wireOp",EDGE,"E20.13.3");var subQ59=sQuery(id+"F3.wireOp",EDGE,"E20.13.1");var subQ60=sQuery(id+"F4.wireOp",EDGE,"E26.14.3");var subQ61=sQuery(id+"F4.wireOp",EDGE,"E26.14.2");var subQ62=sQuery(id+"F3.wireOp",EDGE,"E20.14.3");var subQ63=sQuery(id+"F3.wireOp",EDGE,"E20.14.1");var subQ64=sQuery(id+"F4.wireOp",EDGE,"E26.15.3");var subQ65=sQuery(id+"F4.wireOp",EDGE,"E26.15.2");var subQ66=sQuery(id+"F3.wireOp",EDGE,"E20.15.3");var subQ67=sQuery(id+"F3.wireOp",EDGE,"E20.15.1");var subQ68=sQuery(id+"F4.wireOp",EDGE,"E23");var subQ69=sQuery(id+"F4.wireOp",EDGE,"E22");var subQ70=sQuery(id+"F3.wireOp",EDGE,"E18.top");var subQ71=sQuery(id+"F3.wireOp",EDGE,"E18.bottom");var subQ74=makeQuery(id+"F42.boolean.opBoolean","COPY",FACE,{"disambiguationData":[TD([subQ39])],"derivedFrom":subQ6});var subQ75=makeQuery(id+"F13.boolean.opBoolean","INTERSECT",EDGE,{"derivedFrom":[makeQuery(id+"F1.opRevolve","SWEPT_FACE",FACE,{"disambiguationData":[OSD([sQuery(id+"F0.wireOp",EDGE,"E4")])]}),subQ39]});Q63=makeQuery(id+"F48.opFillet","BLEND_EDGE",EDGE,{"blendedFrom":[makeQuery(id+"F47.opFillet","TWEAK_EDGE",EDGE,{"derivedFrom":[makeQuery(id+"F45.opFillet","BLEND_VERTEX",VERTEX,{"blendedFrom":[subQ75,subQ39,subQ74],"blendedInto":[subQ39,subQ74]}),makeQuery(id+"F45.opFillet","BLEND_VERTEX",VERTEX,{"blendedFrom":[subQ75,makeQuery(id+"F42.boolean.opBoolean","MERGE",FACE,{"derivedFrom":[subQ0,subQ8]}),subQ74],"blendedInto":[makeQuery(id+"F42.boolean.opBoolean","MERGE",FACE,{"derivedFrom":[subQ0,subQ8]}),subQ74]})]}),makeQuery(id+"F47.opFillet","BLEND_FACE",FACE,{"disambiguationData":[OSD([subQ5,subQ7]),TDD([makeQuery(id+"F42.boolean.opBoolean","COPY",EDGE,{"disambiguationData":[TD([makeQuery(id+"F5.opLoft","SWEPT_FACE",FACE,{"disambiguationData":[OSD([subQ71,subQ70,sQuery(id+"F3.wireOp",EDGE,"E18.left"),sQuery(id+"F4.wireOp",EDGE,"E21"),subQ69,subQ68])]})])],"derivedFrom":subQ9})])]}),makeQuery(id+"F47.opFillet","BLEND_FACE",FACE,{"disambiguationData":[OSD([subQ5,subQ7]),TDD([makeQuery(id+"F42.boolean.opBoolean","COPY",EDGE,{"disambiguationData":[TD([makeQuery(id+"F6.opLoft","SWEPT_FACE",FACE,{"disambiguationData":[OSD([sQuery(id+"F3.wireOp",EDGE,"E20.15.0"),subQ67,subQ66,sQuery(id+"F4.wireOp",EDGE,"E26.15.0"),subQ65,subQ64])]})])],"derivedFrom":subQ9})])]}),makeQuery(id+"F47.opFillet","BLEND_FACE",FACE,{"disambiguationData":[OSD([subQ5,subQ7]),TDD([makeQuery(id+"F42.boolean.opBoolean","COPY",EDGE,{"disambiguationData":[TD([makeQuery(id+"F7.opLoft","SWEPT_FACE",FACE,{"disambiguationData":[OSD([sQuery(id+"F3.wireOp",EDGE,"E20.14.0"),subQ63,subQ62,sQuery(id+"F4.wireOp",EDGE,"E26.14.0"),subQ61,subQ60])]})])],"derivedFrom":subQ9})])]}),makeQuery(id+"F47.opFillet","BLEND_FACE",FACE,{"disambiguationData":[OSD([subQ5,subQ7]),TDD([makeQuery(id+"F42.boolean.opBoolean","COPY",EDGE,{"disambiguationData":[TD([makeQuery(id+"F8.opLoft","SWEPT_FACE",FACE,{"disambiguationData":[OSD([sQuery(id+"F3.wireOp",EDGE,"E20.13.0"),subQ59,subQ58,sQuery(id+"F4.wireOp",EDGE,"E26.13.0"),subQ57,subQ56])]})])],"derivedFrom":subQ9})])]}),makeQuery(id+"F47.opFillet","BLEND_FACE",FACE,{"disambiguationData":[OSD([subQ5,subQ7]),TDD([makeQuery(id+"F42.boolean.opBoolean","COPY",EDGE,{"disambiguationData":[TD([makeQuery(id+"F9.opLoft","SWEPT_FACE",FACE,{"disambiguationData":[OSD([sQuery(id+"F3.wireOp",EDGE,"E20.12.0"),subQ55,subQ54,sQuery(id+"F4.wireOp",EDGE,"E26.12.0"),subQ53,subQ52])]})])],"derivedFrom":subQ9})])]}),makeQuery(id+"F47.opFillet","BLEND_FACE",FACE,{"disambiguationData":[OSD([subQ5,subQ7]),TDD([makeQuery(id+"F42.boolean.opBoolean","COPY",EDGE,{"disambiguationData":[TD([makeQuery(id+"F10.opLoft","SWEPT_FACE",FACE,{"disambiguationData":[OSD([sQuery(id+"F3.wireOp",EDGE,"E20.11.0"),subQ51,subQ50,sQuery(id+"F4.wireOp",EDGE,"E26.11.0"),subQ49,subQ48])]})])],"derivedFrom":subQ9})])]}),makeQuery(id+"F47.opFillet","BLEND_FACE",FACE,{"disambiguationData":[OSD([subQ5,subQ7]),TDD([makeQuery(id+"F42.boolean.opBoolean","COPY",EDGE,{"disambiguationData":[TD([makeQuery(id+"F11.opLoft","SWEPT_FACE",FACE,{"disambiguationData":[OSD([sQuery(id+"F3.wireOp",EDGE,"E20.10.0"),subQ47,subQ46,sQuery(id+"F4.wireOp",EDGE,"E26.10.0"),subQ45,subQ44])]})])],"derivedFrom":subQ9})])]}),makeQuery(id+"F47.opFillet","BLEND_FACE",FACE,{"disambiguationData":[OSD([subQ5,subQ7]),TDD([makeQuery(id+"F42.boolean.opBoolean","COPY",EDGE,{"disambiguationData":[TD([makeQuery(id+"F12.opLoft","SWEPT_FACE",FACE,{"disambiguationData":[OSD([sQuery(id+"F3.wireOp",EDGE,"E20.9.0"),subQ43,subQ42,sQuery(id+"F4.wireOp",EDGE,"E26.9.0"),subQ41,subQ40])]})])],"derivedFrom":subQ9})])]}),makeQuery(id+"F47.opFillet","BLEND_FACE",FACE,{"disambiguationData":[OSD([subQ5,subQ7]),TDD([makeQuery(id+"F42.boolean.opBoolean","COPY",EDGE,{"disambiguationData":[TD([subQ39])],"derivedFrom":subQ9})])]}),makeQuery(id+"F47.opFillet","BLEND_FACE",FACE,{"disambiguationData":[OSD([subQ5,subQ7]),TDD([makeQuery(id+"F42.boolean.opBoolean","COPY",EDGE,{"disambiguationData":[TD([makeQuery(id+"F14.opLoft","SWEPT_FACE",FACE,{"disambiguationData":[OSD([sQuery(id+"F3.wireOp",EDGE,"E20.7.0"),subQ33,subQ32,sQuery(id+"F4.wireOp",EDGE,"E26.7.0"),subQ31,subQ30])]})])],"derivedFrom":subQ9})])]}),makeQuery(id+"F47.opFillet","BLEND_FACE",FACE,{"disambiguationData":[OSD([subQ5,subQ7]),TDD([makeQuery(id+"F42.boolean.opBoolean","COPY",EDGE,{"disambiguationData":[TD([makeQuery(id+"F15.opLoft","SWEPT_FACE",FACE,{"disambiguationData":[OSD([sQuery(id+"F3.wireOp",EDGE,"E20.6.0"),subQ29,subQ28,sQuery(id+"F4.wireOp",EDGE,"E26.6.0"),subQ27,subQ26])]})])],"derivedFrom":subQ9})])]}),makeQuery(id+"F47.opFillet","BLEND_FACE",FACE,{"disambiguationData":[OSD([subQ5,subQ7]),TDD([makeQuery(id+"F42.boolean.opBoolean","COPY",EDGE,{"disambiguationData":[TD([makeQuery(id+"F16.opLoft","SWEPT_FACE",FACE,{"disambiguationData":[OSD([sQuery(id+"F3.wireOp",EDGE,"E20.5.0"),subQ25,subQ24,sQuery(id+"F4.wireOp",EDGE,"E26.5.0"),subQ23,subQ22])]})])],"derivedFrom":subQ9})])]}),makeQuery(id+"F47.opFillet","BLEND_FACE",FACE,{"disambiguationData":[OSD([subQ5,subQ7]),TDD([makeQuery(id+"F42.boolean.opBoolean","COPY",EDGE,{"disambiguationData":[TD([makeQuery(id+"F17.opLoft","SWEPT_FACE",FACE,{"disambiguationData":[OSD([sQuery(id+"F3.wireOp",EDGE,"E20.4.0"),subQ21,subQ20,sQuery(id+"F4.wireOp",EDGE,"E26.4.0"),subQ19,subQ18])]})])],"derivedFrom":subQ9})])]}),makeQuery(id+"F47.opFillet","BLEND_FACE",FACE,{"disambiguationData":[OSD([subQ5,subQ7]),TDD([makeQuery(id+"F42.boolean.opBoolean","COPY",EDGE,{"disambiguationData":[TD([makeQuery(id+"F18.opLoft","SWEPT_FACE",FACE,{"disambiguationData":[OSD([sQuery(id+"F3.wireOp",EDGE,"E20.3.0"),subQ17,subQ16,sQuery(id+"F4.wireOp",EDGE,"E26.3.0"),subQ15,subQ14])]})])],"derivedFrom":subQ9})])]}),makeQuery(id+"F47.opFillet","BLEND_FACE",FACE,{"disambiguationData":[OSD([subQ5,subQ7]),TDD([makeQuery(id+"F42.boolean.opBoolean","COPY",EDGE,{"disambiguationData":[TD([makeQuery(id+"F19.opLoft","SWEPT_FACE",FACE,{"disambiguationData":[OSD([sQuery(id+"F3.wireOp",EDGE,"E20.2.0"),subQ13,subQ12,sQuery(id+"F4.wireOp",EDGE,"E26.2.0"),subQ11,subQ10])]})])],"derivedFrom":subQ9})])]}),makeQuery(id+"F47.opFillet","BLEND_FACE",FACE,{"disambiguationData":[OSD([subQ5,subQ7]),TDD([makeQuery(id+"F42.boolean.opBoolean","COPY",EDGE,{"disambiguationData":[TD([makeQuery(id+"F20.opLoft","SWEPT_FACE",FACE,{"disambiguationData":[OSD([sQuery(id+"F3.wireOp",EDGE,"E20.1.0"),subQ4,subQ3,sQuery(id+"F4.wireOp",EDGE,"E26.1.0"),subQ2,subQ1])]})])],"derivedFrom":subQ9})])]})],"blendedInto":[makeQuery(id+"F47.opFillet","BLEND_FACE",FACE,{"disambiguationData":[OSD([subQ5,subQ7]),TDD([makeQuery(id+"F42.boolean.opBoolean","COPY",EDGE,{"disambiguationData":[TD([makeQuery(id+"F5.opLoft","SWEPT_FACE",FACE,{"disambiguationData":[OSD([subQ71,subQ70,sQuery(id+"F3.wireOp",EDGE,"E18.left"),sQuery(id+"F4.wireOp",EDGE,"E21"),subQ69,subQ68])]})])],"derivedFrom":subQ9})])]}),makeQuery(id+"F47.opFillet","BLEND_FACE",FACE,{"disambiguationData":[OSD([subQ5,subQ7]),TDD([makeQuery(id+"F42.boolean.opBoolean","COPY",EDGE,{"disambiguationData":[TD([makeQuery(id+"F6.opLoft","SWEPT_FACE",FACE,{"disambiguationData":[OSD([sQuery(id+"F3.wireOp",EDGE,"E20.15.0"),subQ67,subQ66,sQuery(id+"F4.wireOp",EDGE,"E26.15.0"),subQ65,subQ64])]})])],"derivedFrom":subQ9})])]}),makeQuery(id+"F47.opFillet","BLEND_FACE",FACE,{"disambiguationData":[OSD([subQ5,subQ7]),TDD([makeQuery(id+"F42.boolean.opBoolean","COPY",EDGE,{"disambiguationData":[TD([makeQuery(id+"F7.opLoft","SWEPT_FACE",FACE,{"disambiguationData":[OSD([sQuery(id+"F3.wireOp",EDGE,"E20.14.0"),subQ63,subQ62,sQuery(id+"F4.wireOp",EDGE,"E26.14.0"),subQ61,subQ60])]})])],"derivedFrom":subQ9})])]}),makeQuery(id+"F47.opFillet","BLEND_FACE",FACE,{"disambiguationData":[OSD([subQ5,subQ7]),TDD([makeQuery(id+"F42.boolean.opBoolean","COPY",EDGE,{"disambiguationData":[TD([makeQuery(id+"F8.opLoft","SWEPT_FACE",FACE,{"disambiguationData":[OSD([sQuery(id+"F3.wireOp",EDGE,"E20.13.0"),subQ59,subQ58,sQuery(id+"F4.wireOp",EDGE,"E26.13.0"),subQ57,subQ56])]})])],"derivedFrom":subQ9})])]}),makeQuery(id+"F47.opFillet","BLEND_FACE",FACE,{"disambiguationData":[OSD([subQ5,subQ7]),TDD([makeQuery(id+"F42.boolean.opBoolean","COPY",EDGE,{"disambiguationData":[TD([makeQuery(id+"F9.opLoft","SWEPT_FACE",FACE,{"disambiguationData":[OSD([sQuery(id+"F3.wireOp",EDGE,"E20.12.0"),subQ55,subQ54,sQuery(id+"F4.wireOp",EDGE,"E26.12.0"),subQ53,subQ52])]})])],"derivedFrom":subQ9})])]}),makeQuery(id+"F47.opFillet","BLEND_FACE",FACE,{"disambiguationData":[OSD([subQ5,subQ7]),TDD([makeQuery(id+"F42.boolean.opBoolean","COPY",EDGE,{"disambiguationData":[TD([makeQuery(id+"F10.opLoft","SWEPT_FACE",FACE,{"disambiguationData":[OSD([sQuery(id+"F3.wireOp",EDGE,"E20.11.0"),subQ51,subQ50,sQuery(id+"F4.wireOp",EDGE,"E26.11.0"),subQ49,subQ48])]})])],"derivedFrom":subQ9})])]}),makeQuery(id+"F47.opFillet","BLEND_FACE",FACE,{"disambiguationData":[OSD([subQ5,subQ7]),TDD([makeQuery(id+"F42.boolean.opBoolean","COPY",EDGE,{"disambiguationData":[TD([makeQuery(id+"F11.opLoft","SWEPT_FACE",FACE,{"disambiguationData":[OSD([sQuery(id+"F3.wireOp",EDGE,"E20.10.0"),subQ47,subQ46,sQuery(id+"F4.wireOp",EDGE,"E26.10.0"),subQ45,subQ44])]})])],"derivedFrom":subQ9})])]}),makeQuery(id+"F47.opFillet","BLEND_FACE",FACE,{"disambiguationData":[OSD([subQ5,subQ7]),TDD([makeQuery(id+"F42.boolean.opBoolean","COPY",EDGE,{"disambiguationData":[TD([makeQuery(id+"F12.opLoft","SWEPT_FACE",FACE,{"disambiguationData":[OSD([sQuery(id+"F3.wireOp",EDGE,"E20.9.0"),subQ43,subQ42,sQuery(id+"F4.wireOp",EDGE,"E26.9.0"),subQ41,subQ40])]})])],"derivedFrom":subQ9})])]}),makeQuery(id+"F47.opFillet","BLEND_FACE",FACE,{"disambiguationData":[OSD([subQ5,subQ7]),TDD([makeQuery(id+"F42.boolean.opBoolean","COPY",EDGE,{"disambiguationData":[TD([subQ39])],"derivedFrom":subQ9})])]}),makeQuery(id+"F47.opFillet","BLEND_FACE",FACE,{"disambiguationData":[OSD([subQ5,subQ7]),TDD([makeQuery(id+"F42.boolean.opBoolean","COPY",EDGE,{"disambiguationData":[TD([makeQuery(id+"F14.opLoft","SWEPT_FACE",FACE,{"disambiguationData":[OSD([sQuery(id+"F3.wireOp",EDGE,"E20.7.0"),subQ33,subQ32,sQuery(id+"F4.wireOp",EDGE,"E26.7.0"),subQ31,subQ30])]})])],"derivedFrom":subQ9})])]}),makeQuery(id+"F47.opFillet","BLEND_FACE",FACE,{"disambiguationData":[OSD([subQ5,subQ7]),TDD([makeQuery(id+"F42.boolean.opBoolean","COPY",EDGE,{"disambiguationData":[TD([makeQuery(id+"F15.opLoft","SWEPT_FACE",FACE,{"disambiguationData":[OSD([sQuery(id+"F3.wireOp",EDGE,"E20.6.0"),subQ29,subQ28,sQuery(id+"F4.wireOp",EDGE,"E26.6.0"),subQ27,subQ26])]})])],"derivedFrom":subQ9})])]}),makeQuery(id+"F47.opFillet","BLEND_FACE",FACE,{"disambiguationData":[OSD([subQ5,subQ7]),TDD([makeQuery(id+"F42.boolean.opBoolean","COPY",EDGE,{"disambiguationData":[TD([makeQuery(id+"F16.opLoft","SWEPT_FACE",FACE,{"disambiguationData":[OSD([sQuery(id+"F3.wireOp",EDGE,"E20.5.0"),subQ25,subQ24,sQuery(id+"F4.wireOp",EDGE,"E26.5.0"),subQ23,subQ22])]})])],"derivedFrom":subQ9})])]}),makeQuery(id+"F47.opFillet","BLEND_FACE",FACE,{"disambiguationData":[OSD([subQ5,subQ7]),TDD([makeQuery(id+"F42.boolean.opBoolean","COPY",EDGE,{"disambiguationData":[TD([makeQuery(id+"F17.opLoft","SWEPT_FACE",FACE,{"disambiguationData":[OSD([sQuery(id+"F3.wireOp",EDGE,"E20.4.0"),subQ21,subQ20,sQuery(id+"F4.wireOp",EDGE,"E26.4.0"),subQ19,subQ18])]})])],"derivedFrom":subQ9})])]}),makeQuery(id+"F47.opFillet","BLEND_FACE",FACE,{"disambiguationData":[OSD([subQ5,subQ7]),TDD([makeQuery(id+"F42.boolean.opBoolean","COPY",EDGE,{"disambiguationData":[TD([makeQuery(id+"F18.opLoft","SWEPT_FACE",FACE,{"disambiguationData":[OSD([sQuery(id+"F3.wireOp",EDGE,"E20.3.0"),subQ17,subQ16,sQuery(id+"F4.wireOp",EDGE,"E26.3.0"),subQ15,subQ14])]})])],"derivedFrom":subQ9})])]}),makeQuery(id+"F47.opFillet","BLEND_FACE",FACE,{"disambiguationData":[OSD([subQ5,subQ7]),TDD([makeQuery(id+"F42.boolean.opBoolean","COPY",EDGE,{"disambiguationData":[TD([makeQuery(id+"F19.opLoft","SWEPT_FACE",FACE,{"disambiguationData":[OSD([sQuery(id+"F3.wireOp",EDGE,"E20.2.0"),subQ13,subQ12,sQuery(id+"F4.wireOp",EDGE,"E26.2.0"),subQ11,subQ10])]})])],"derivedFrom":subQ9})])]}),makeQuery(id+"F47.opFillet","BLEND_FACE",FACE,{"disambiguationData":[OSD([subQ5,subQ7]),TDD([makeQuery(id+"F42.boolean.opBoolean","COPY",EDGE,{"disambiguationData":[TD([makeQuery(id+"F20.opLoft","SWEPT_FACE",FACE,{"disambiguationData":[OSD([sQuery(id+"F3.wireOp",EDGE,"E20.1.0"),subQ4,subQ3,sQuery(id+"F4.wireOp",EDGE,"E26.1.0"),subQ2,subQ1])]})])],"derivedFrom":subQ9})])]})]});}
            var Q64;
            {var subQ0=sQuery(id+"F4.wireOp",EDGE,"E26.7.3");var subQ1=sQuery(id+"F4.wireOp",EDGE,"E26.7.2");var subQ2=sQuery(id+"F4.wireOp",EDGE,"E26.7.0");var subQ3=sQuery(id+"F3.wireOp",EDGE,"E20.7.3");var subQ4=sQuery(id+"F3.wireOp",EDGE,"E20.7.1");var subQ5=sQuery(id+"F4.wireOp",EDGE,"E26.7.1");var subQ6=makeQuery(id+"F14.opLoft","SWEPT_FACE",FACE,{"disambiguationData":[OSD([subQ4,sQuery(id+"F3.wireOp",EDGE,"E20.7.2"),subQ3,subQ5,subQ1,subQ0])]});var subQ7=sQuery(id+"F41.wireOp",EDGE,"E34");var subQ8=sQuery(id+"F41.wireOp",EDGE,"E32");Q64=makeQuery(id+"F44.opFillet","BLEND_EDGE",EDGE,{"blendedFrom":[makeQuery(id+"F40.boolean.opBoolean","INTERSECT",EDGE,{"derivedFrom":[subQ6,makeQuery(id+"F40.opExtrude","CAP_FACE",FACE,{"disambiguationData":[OSD([sQuery(id+"F39.wireOp",EDGE,"E29"),sQuery(id+"F39.wireOp",EDGE,"E30")])],"isStart":false})]}),makeQuery(id+"F42.boolean.opBoolean","COPY",FACE,{"disambiguationData":[TD([makeQuery(id+"F14.opLoft","SWEPT_FACE",FACE,{"disambiguationData":[OSD([sQuery(id+"F3.wireOp",EDGE,"E20.7.0"),subQ4,subQ3,subQ2,subQ1,subQ0])]})])],"derivedFrom":makeQuery(id+"F42.opRevolve","SWEPT_FACE",FACE,{"disambiguationData":[OSD([subQ8]),TDD([makeQuery(id+"F41.imprint","IMPRINT",EDGE,{"disambiguationData":[TD([[makeQuery(id+"F41.imprint","INTERSECT",VERTEX,{"disambiguationData":[OD(0.0)],"derivedFrom":[subQ8,subQ7]}),-1.0]])],"derivedFrom":subQ8})])]})})],"blendedInto":[makeQuery(id+"F42.boolean.opBoolean","COPY",FACE,{"disambiguationData":[TD([makeQuery(id+"F14.opLoft","SWEPT_FACE",FACE,{"disambiguationData":[OSD([sQuery(id+"F3.wireOp",EDGE,"E20.7.0"),subQ4,subQ3,subQ2,subQ1,subQ0])]})])],"derivedFrom":makeQuery(id+"F42.opRevolve","SWEPT_FACE",FACE,{"disambiguationData":[OSD([subQ8]),TDD([makeQuery(id+"F41.imprint","IMPRINT",EDGE,{"disambiguationData":[TD([[makeQuery(id+"F41.imprint","INTERSECT",VERTEX,{"disambiguationData":[OD(0.0)],"derivedFrom":[subQ8,subQ7]}),-1.0]])],"derivedFrom":subQ8})])]})})]});}
            var Q65;
            {var subQ0=sQuery(id+"F41.wireOp",EDGE,"E34");var subQ1=sQuery(id+"F41.wireOp",EDGE,"E32");Q65=makeQuery(id+"F42.boolean.opBoolean","INTERSECT",EDGE,{"derivedFrom":[makeQuery(id+"F14.opLoft","SWEPT_FACE",FACE,{"disambiguationData":[OSD([sQuery(id+"F3.wireOp",EDGE,"E20.7.0"),sQuery(id+"F3.wireOp",EDGE,"E20.7.1"),sQuery(id+"F3.wireOp",EDGE,"E20.7.3"),sQuery(id+"F4.wireOp",EDGE,"E26.7.0"),sQuery(id+"F4.wireOp",EDGE,"E26.7.2"),sQuery(id+"F4.wireOp",EDGE,"E26.7.3")])]}),makeQuery(id+"F42.opRevolve","SWEPT_FACE",FACE,{"disambiguationData":[OSD([subQ1]),TDD([makeQuery(id+"F41.imprint","IMPRINT",EDGE,{"disambiguationData":[TD([[makeQuery(id+"F41.imprint","INTERSECT",VERTEX,{"disambiguationData":[OD(0.0)],"derivedFrom":[subQ1,subQ0]}),-1.0]])],"derivedFrom":subQ1})])]})]});}
            var Q66;
            {var subQ0=sQuery(id+"F4.wireOp",EDGE,"E26.8.3");var subQ1=sQuery(id+"F4.wireOp",EDGE,"E26.8.2");var subQ2=sQuery(id+"F4.wireOp",EDGE,"E26.8.0");var subQ3=sQuery(id+"F3.wireOp",EDGE,"E20.8.3");var subQ4=sQuery(id+"F3.wireOp",EDGE,"E20.8.1");var subQ5=sQuery(id+"F4.wireOp",EDGE,"E26.8.1");var subQ6=makeQuery(id+"F13.opLoft","SWEPT_FACE",FACE,{"disambiguationData":[OSD([subQ4,sQuery(id+"F3.wireOp",EDGE,"E20.8.2"),subQ3,subQ5,subQ1,subQ0])]});var subQ7=sQuery(id+"F41.wireOp",EDGE,"E34");var subQ8=sQuery(id+"F41.wireOp",EDGE,"E32");Q66=makeQuery(id+"F44.opFillet","BLEND_EDGE",EDGE,{"blendedFrom":[makeQuery(id+"F40.boolean.opBoolean","INTERSECT",EDGE,{"derivedFrom":[subQ6,makeQuery(id+"F40.opExtrude","CAP_FACE",FACE,{"disambiguationData":[OSD([sQuery(id+"F39.wireOp",EDGE,"E29"),sQuery(id+"F39.wireOp",EDGE,"E30")])],"isStart":false})]}),makeQuery(id+"F42.boolean.opBoolean","COPY",FACE,{"disambiguationData":[TD([makeQuery(id+"F13.opLoft","SWEPT_FACE",FACE,{"disambiguationData":[OSD([sQuery(id+"F3.wireOp",EDGE,"E20.8.0"),subQ4,subQ3,subQ2,subQ1,subQ0])]})])],"derivedFrom":makeQuery(id+"F42.opRevolve","SWEPT_FACE",FACE,{"disambiguationData":[OSD([subQ8]),TDD([makeQuery(id+"F41.imprint","IMPRINT",EDGE,{"disambiguationData":[TD([[makeQuery(id+"F41.imprint","INTERSECT",VERTEX,{"disambiguationData":[OD(0.0)],"derivedFrom":[subQ8,subQ7]}),-1.0]])],"derivedFrom":subQ8})])]})})],"blendedInto":[makeQuery(id+"F42.boolean.opBoolean","COPY",FACE,{"disambiguationData":[TD([makeQuery(id+"F13.opLoft","SWEPT_FACE",FACE,{"disambiguationData":[OSD([sQuery(id+"F3.wireOp",EDGE,"E20.8.0"),subQ4,subQ3,subQ2,subQ1,subQ0])]})])],"derivedFrom":makeQuery(id+"F42.opRevolve","SWEPT_FACE",FACE,{"disambiguationData":[OSD([subQ8]),TDD([makeQuery(id+"F41.imprint","IMPRINT",EDGE,{"disambiguationData":[TD([[makeQuery(id+"F41.imprint","INTERSECT",VERTEX,{"disambiguationData":[OD(0.0)],"derivedFrom":[subQ8,subQ7]}),-1.0]])],"derivedFrom":subQ8})])]})})]});}
            var Q67;
            {var subQ0=sQuery(id+"F41.wireOp",EDGE,"E34");var subQ1=sQuery(id+"F41.wireOp",EDGE,"E32");Q67=makeQuery(id+"F42.boolean.opBoolean","INTERSECT",EDGE,{"derivedFrom":[makeQuery(id+"F13.opLoft","SWEPT_FACE",FACE,{"disambiguationData":[OSD([sQuery(id+"F3.wireOp",EDGE,"E20.8.0"),sQuery(id+"F3.wireOp",EDGE,"E20.8.1"),sQuery(id+"F3.wireOp",EDGE,"E20.8.3"),sQuery(id+"F4.wireOp",EDGE,"E26.8.0"),sQuery(id+"F4.wireOp",EDGE,"E26.8.2"),sQuery(id+"F4.wireOp",EDGE,"E26.8.3")])]}),makeQuery(id+"F42.opRevolve","SWEPT_FACE",FACE,{"disambiguationData":[OSD([subQ1]),TDD([makeQuery(id+"F41.imprint","IMPRINT",EDGE,{"disambiguationData":[TD([[makeQuery(id+"F41.imprint","INTERSECT",VERTEX,{"disambiguationData":[OD(0.0)],"derivedFrom":[subQ1,subQ0]}),-1.0]])],"derivedFrom":subQ1})])]})]});}
            var Q68;
            {var subQ0=sQuery(id+"F4.wireOp",EDGE,"E26.9.3");var subQ1=sQuery(id+"F4.wireOp",EDGE,"E26.9.2");var subQ2=sQuery(id+"F4.wireOp",EDGE,"E26.9.0");var subQ3=sQuery(id+"F3.wireOp",EDGE,"E20.9.3");var subQ4=sQuery(id+"F3.wireOp",EDGE,"E20.9.1");var subQ5=sQuery(id+"F4.wireOp",EDGE,"E26.9.1");var subQ6=makeQuery(id+"F12.opLoft","SWEPT_FACE",FACE,{"disambiguationData":[OSD([subQ4,sQuery(id+"F3.wireOp",EDGE,"E20.9.2"),subQ3,subQ5,subQ1,subQ0])]});var subQ7=sQuery(id+"F41.wireOp",EDGE,"E34");var subQ8=sQuery(id+"F41.wireOp",EDGE,"E32");Q68=makeQuery(id+"F44.opFillet","BLEND_EDGE",EDGE,{"blendedFrom":[makeQuery(id+"F40.boolean.opBoolean","INTERSECT",EDGE,{"derivedFrom":[subQ6,makeQuery(id+"F40.opExtrude","CAP_FACE",FACE,{"disambiguationData":[OSD([sQuery(id+"F39.wireOp",EDGE,"E29"),sQuery(id+"F39.wireOp",EDGE,"E30")])],"isStart":false})]}),makeQuery(id+"F42.boolean.opBoolean","COPY",FACE,{"disambiguationData":[TD([makeQuery(id+"F12.opLoft","SWEPT_FACE",FACE,{"disambiguationData":[OSD([sQuery(id+"F3.wireOp",EDGE,"E20.9.0"),subQ4,subQ3,subQ2,subQ1,subQ0])]})])],"derivedFrom":makeQuery(id+"F42.opRevolve","SWEPT_FACE",FACE,{"disambiguationData":[OSD([subQ8]),TDD([makeQuery(id+"F41.imprint","IMPRINT",EDGE,{"disambiguationData":[TD([[makeQuery(id+"F41.imprint","INTERSECT",VERTEX,{"disambiguationData":[OD(0.0)],"derivedFrom":[subQ8,subQ7]}),-1.0]])],"derivedFrom":subQ8})])]})})],"blendedInto":[makeQuery(id+"F42.boolean.opBoolean","COPY",FACE,{"disambiguationData":[TD([makeQuery(id+"F12.opLoft","SWEPT_FACE",FACE,{"disambiguationData":[OSD([sQuery(id+"F3.wireOp",EDGE,"E20.9.0"),subQ4,subQ3,subQ2,subQ1,subQ0])]})])],"derivedFrom":makeQuery(id+"F42.opRevolve","SWEPT_FACE",FACE,{"disambiguationData":[OSD([subQ8]),TDD([makeQuery(id+"F41.imprint","IMPRINT",EDGE,{"disambiguationData":[TD([[makeQuery(id+"F41.imprint","INTERSECT",VERTEX,{"disambiguationData":[OD(0.0)],"derivedFrom":[subQ8,subQ7]}),-1.0]])],"derivedFrom":subQ8})])]})})]});}
            var Q69;
            {var subQ0=sQuery(id+"F41.wireOp",EDGE,"E34");var subQ1=sQuery(id+"F41.wireOp",EDGE,"E32");Q69=makeQuery(id+"F42.boolean.opBoolean","INTERSECT",EDGE,{"derivedFrom":[makeQuery(id+"F12.opLoft","SWEPT_FACE",FACE,{"disambiguationData":[OSD([sQuery(id+"F3.wireOp",EDGE,"E20.9.0"),sQuery(id+"F3.wireOp",EDGE,"E20.9.1"),sQuery(id+"F3.wireOp",EDGE,"E20.9.3"),sQuery(id+"F4.wireOp",EDGE,"E26.9.0"),sQuery(id+"F4.wireOp",EDGE,"E26.9.2"),sQuery(id+"F4.wireOp",EDGE,"E26.9.3")])]}),makeQuery(id+"F42.opRevolve","SWEPT_FACE",FACE,{"disambiguationData":[OSD([subQ1]),TDD([makeQuery(id+"F41.imprint","IMPRINT",EDGE,{"disambiguationData":[TD([[makeQuery(id+"F41.imprint","INTERSECT",VERTEX,{"disambiguationData":[OD(0.0)],"derivedFrom":[subQ1,subQ0]}),-1.0]])],"derivedFrom":subQ1})])]})]});}
            var Q70;
            {var subQ0=sQuery(id+"F4.wireOp",EDGE,"E26.10.0");var subQ1=sQuery(id+"F4.wireOp",EDGE,"E26.10.1");var subQ2=sQuery(id+"F4.wireOp",EDGE,"E26.10.2");var subQ3=sQuery(id+"F4.wireOp",EDGE,"E26.10.3");var subQ4=sQuery(id+"F3.wireOp",EDGE,"E20.10.3");var subQ5=sQuery(id+"F3.wireOp",EDGE,"E20.10.1");var subQ6=makeQuery(id+"F11.opLoft","SWEPT_FACE",FACE,{"disambiguationData":[OSD([subQ5,sQuery(id+"F3.wireOp",EDGE,"E20.10.2"),subQ4,subQ1,subQ2,subQ3])]});var subQ7=sQuery(id+"F41.wireOp",EDGE,"E34");var subQ8=sQuery(id+"F41.wireOp",EDGE,"E32");Q70=makeQuery(id+"F44.opFillet","BLEND_EDGE",EDGE,{"blendedFrom":[makeQuery(id+"F40.boolean.opBoolean","INTERSECT",EDGE,{"derivedFrom":[subQ6,makeQuery(id+"F40.opExtrude","CAP_FACE",FACE,{"disambiguationData":[OSD([sQuery(id+"F39.wireOp",EDGE,"E29"),sQuery(id+"F39.wireOp",EDGE,"E30")])],"isStart":false})]}),makeQuery(id+"F42.boolean.opBoolean","COPY",FACE,{"disambiguationData":[TD([makeQuery(id+"F11.opLoft","SWEPT_FACE",FACE,{"disambiguationData":[OSD([sQuery(id+"F3.wireOp",EDGE,"E20.10.0"),subQ5,subQ4,subQ0,subQ2,subQ3])]})])],"derivedFrom":makeQuery(id+"F42.opRevolve","SWEPT_FACE",FACE,{"disambiguationData":[OSD([subQ8]),TDD([makeQuery(id+"F41.imprint","IMPRINT",EDGE,{"disambiguationData":[TD([[makeQuery(id+"F41.imprint","INTERSECT",VERTEX,{"disambiguationData":[OD(0.0)],"derivedFrom":[subQ8,subQ7]}),-1.0]])],"derivedFrom":subQ8})])]})})],"blendedInto":[makeQuery(id+"F42.boolean.opBoolean","COPY",FACE,{"disambiguationData":[TD([makeQuery(id+"F11.opLoft","SWEPT_FACE",FACE,{"disambiguationData":[OSD([sQuery(id+"F3.wireOp",EDGE,"E20.10.0"),subQ5,subQ4,subQ0,subQ2,subQ3])]})])],"derivedFrom":makeQuery(id+"F42.opRevolve","SWEPT_FACE",FACE,{"disambiguationData":[OSD([subQ8]),TDD([makeQuery(id+"F41.imprint","IMPRINT",EDGE,{"disambiguationData":[TD([[makeQuery(id+"F41.imprint","INTERSECT",VERTEX,{"disambiguationData":[OD(0.0)],"derivedFrom":[subQ8,subQ7]}),-1.0]])],"derivedFrom":subQ8})])]})})]});}
            var Q71;
            {var subQ0=sQuery(id+"F41.wireOp",EDGE,"E34");var subQ1=sQuery(id+"F41.wireOp",EDGE,"E32");Q71=makeQuery(id+"F42.boolean.opBoolean","INTERSECT",EDGE,{"derivedFrom":[makeQuery(id+"F11.opLoft","SWEPT_FACE",FACE,{"disambiguationData":[OSD([sQuery(id+"F3.wireOp",EDGE,"E20.10.0"),sQuery(id+"F3.wireOp",EDGE,"E20.10.1"),sQuery(id+"F3.wireOp",EDGE,"E20.10.3"),sQuery(id+"F4.wireOp",EDGE,"E26.10.0"),sQuery(id+"F4.wireOp",EDGE,"E26.10.2"),sQuery(id+"F4.wireOp",EDGE,"E26.10.3")])]}),makeQuery(id+"F42.opRevolve","SWEPT_FACE",FACE,{"disambiguationData":[OSD([subQ1]),TDD([makeQuery(id+"F41.imprint","IMPRINT",EDGE,{"disambiguationData":[TD([[makeQuery(id+"F41.imprint","INTERSECT",VERTEX,{"disambiguationData":[OD(0.0)],"derivedFrom":[subQ1,subQ0]}),-1.0]])],"derivedFrom":subQ1})])]})]});}
            var Q72;
            {var subQ0=sQuery(id+"F4.wireOp",EDGE,"E26.11.0");var subQ1=sQuery(id+"F4.wireOp",EDGE,"E26.11.1");var subQ2=sQuery(id+"F4.wireOp",EDGE,"E26.11.2");var subQ3=sQuery(id+"F4.wireOp",EDGE,"E26.11.3");var subQ4=sQuery(id+"F3.wireOp",EDGE,"E20.11.3");var subQ5=sQuery(id+"F3.wireOp",EDGE,"E20.11.1");var subQ6=makeQuery(id+"F10.opLoft","SWEPT_FACE",FACE,{"disambiguationData":[OSD([subQ5,sQuery(id+"F3.wireOp",EDGE,"E20.11.2"),subQ4,subQ1,subQ2,subQ3])]});var subQ7=sQuery(id+"F41.wireOp",EDGE,"E34");var subQ8=sQuery(id+"F41.wireOp",EDGE,"E32");Q72=makeQuery(id+"F44.opFillet","BLEND_EDGE",EDGE,{"blendedFrom":[makeQuery(id+"F40.boolean.opBoolean","INTERSECT",EDGE,{"derivedFrom":[subQ6,makeQuery(id+"F40.opExtrude","CAP_FACE",FACE,{"disambiguationData":[OSD([sQuery(id+"F39.wireOp",EDGE,"E29"),sQuery(id+"F39.wireOp",EDGE,"E30")])],"isStart":false})]}),makeQuery(id+"F42.boolean.opBoolean","COPY",FACE,{"disambiguationData":[TD([makeQuery(id+"F10.opLoft","SWEPT_FACE",FACE,{"disambiguationData":[OSD([sQuery(id+"F3.wireOp",EDGE,"E20.11.0"),subQ5,subQ4,subQ0,subQ2,subQ3])]})])],"derivedFrom":makeQuery(id+"F42.opRevolve","SWEPT_FACE",FACE,{"disambiguationData":[OSD([subQ8]),TDD([makeQuery(id+"F41.imprint","IMPRINT",EDGE,{"disambiguationData":[TD([[makeQuery(id+"F41.imprint","INTERSECT",VERTEX,{"disambiguationData":[OD(0.0)],"derivedFrom":[subQ8,subQ7]}),-1.0]])],"derivedFrom":subQ8})])]})})],"blendedInto":[makeQuery(id+"F42.boolean.opBoolean","COPY",FACE,{"disambiguationData":[TD([makeQuery(id+"F10.opLoft","SWEPT_FACE",FACE,{"disambiguationData":[OSD([sQuery(id+"F3.wireOp",EDGE,"E20.11.0"),subQ5,subQ4,subQ0,subQ2,subQ3])]})])],"derivedFrom":makeQuery(id+"F42.opRevolve","SWEPT_FACE",FACE,{"disambiguationData":[OSD([subQ8]),TDD([makeQuery(id+"F41.imprint","IMPRINT",EDGE,{"disambiguationData":[TD([[makeQuery(id+"F41.imprint","INTERSECT",VERTEX,{"disambiguationData":[OD(0.0)],"derivedFrom":[subQ8,subQ7]}),-1.0]])],"derivedFrom":subQ8})])]})})]});}
            var Q73;
            {var subQ0=sQuery(id+"F41.wireOp",EDGE,"E34");var subQ1=sQuery(id+"F41.wireOp",EDGE,"E32");Q73=makeQuery(id+"F42.boolean.opBoolean","INTERSECT",EDGE,{"derivedFrom":[makeQuery(id+"F10.opLoft","SWEPT_FACE",FACE,{"disambiguationData":[OSD([sQuery(id+"F3.wireOp",EDGE,"E20.11.0"),sQuery(id+"F3.wireOp",EDGE,"E20.11.1"),sQuery(id+"F3.wireOp",EDGE,"E20.11.3"),sQuery(id+"F4.wireOp",EDGE,"E26.11.0"),sQuery(id+"F4.wireOp",EDGE,"E26.11.2"),sQuery(id+"F4.wireOp",EDGE,"E26.11.3")])]}),makeQuery(id+"F42.opRevolve","SWEPT_FACE",FACE,{"disambiguationData":[OSD([subQ1]),TDD([makeQuery(id+"F41.imprint","IMPRINT",EDGE,{"disambiguationData":[TD([[makeQuery(id+"F41.imprint","INTERSECT",VERTEX,{"disambiguationData":[OD(0.0)],"derivedFrom":[subQ1,subQ0]}),-1.0]])],"derivedFrom":subQ1})])]})]});}
            var Q74;
            {var subQ0=sQuery(id+"F4.wireOp",EDGE,"E26.12.0");var subQ1=sQuery(id+"F4.wireOp",EDGE,"E26.12.2");var subQ2=sQuery(id+"F4.wireOp",EDGE,"E26.12.1");var subQ3=sQuery(id+"F4.wireOp",EDGE,"E26.12.3");var subQ4=sQuery(id+"F3.wireOp",EDGE,"E20.12.3");var subQ5=sQuery(id+"F3.wireOp",EDGE,"E20.12.1");var subQ6=makeQuery(id+"F9.opLoft","SWEPT_FACE",FACE,{"disambiguationData":[OSD([subQ5,sQuery(id+"F3.wireOp",EDGE,"E20.12.2"),subQ4,subQ2,subQ1,subQ3])]});var subQ7=sQuery(id+"F41.wireOp",EDGE,"E34");var subQ8=sQuery(id+"F41.wireOp",EDGE,"E32");Q74=makeQuery(id+"F44.opFillet","BLEND_EDGE",EDGE,{"blendedFrom":[makeQuery(id+"F40.boolean.opBoolean","INTERSECT",EDGE,{"derivedFrom":[subQ6,makeQuery(id+"F40.opExtrude","CAP_FACE",FACE,{"disambiguationData":[OSD([sQuery(id+"F39.wireOp",EDGE,"E29"),sQuery(id+"F39.wireOp",EDGE,"E30")])],"isStart":false})]}),makeQuery(id+"F42.boolean.opBoolean","COPY",FACE,{"disambiguationData":[TD([makeQuery(id+"F9.opLoft","SWEPT_FACE",FACE,{"disambiguationData":[OSD([sQuery(id+"F3.wireOp",EDGE,"E20.12.0"),subQ5,subQ4,subQ0,subQ1,subQ3])]})])],"derivedFrom":makeQuery(id+"F42.opRevolve","SWEPT_FACE",FACE,{"disambiguationData":[OSD([subQ8]),TDD([makeQuery(id+"F41.imprint","IMPRINT",EDGE,{"disambiguationData":[TD([[makeQuery(id+"F41.imprint","INTERSECT",VERTEX,{"disambiguationData":[OD(0.0)],"derivedFrom":[subQ8,subQ7]}),-1.0]])],"derivedFrom":subQ8})])]})})],"blendedInto":[makeQuery(id+"F42.boolean.opBoolean","COPY",FACE,{"disambiguationData":[TD([makeQuery(id+"F9.opLoft","SWEPT_FACE",FACE,{"disambiguationData":[OSD([sQuery(id+"F3.wireOp",EDGE,"E20.12.0"),subQ5,subQ4,subQ0,subQ1,subQ3])]})])],"derivedFrom":makeQuery(id+"F42.opRevolve","SWEPT_FACE",FACE,{"disambiguationData":[OSD([subQ8]),TDD([makeQuery(id+"F41.imprint","IMPRINT",EDGE,{"disambiguationData":[TD([[makeQuery(id+"F41.imprint","INTERSECT",VERTEX,{"disambiguationData":[OD(0.0)],"derivedFrom":[subQ8,subQ7]}),-1.0]])],"derivedFrom":subQ8})])]})})]});}
            var Q75;
            {var subQ0=sQuery(id+"F41.wireOp",EDGE,"E34");var subQ1=sQuery(id+"F41.wireOp",EDGE,"E32");Q75=makeQuery(id+"F42.boolean.opBoolean","INTERSECT",EDGE,{"derivedFrom":[makeQuery(id+"F9.opLoft","SWEPT_FACE",FACE,{"disambiguationData":[OSD([sQuery(id+"F3.wireOp",EDGE,"E20.12.0"),sQuery(id+"F3.wireOp",EDGE,"E20.12.1"),sQuery(id+"F3.wireOp",EDGE,"E20.12.3"),sQuery(id+"F4.wireOp",EDGE,"E26.12.0"),sQuery(id+"F4.wireOp",EDGE,"E26.12.2"),sQuery(id+"F4.wireOp",EDGE,"E26.12.3")])]}),makeQuery(id+"F42.opRevolve","SWEPT_FACE",FACE,{"disambiguationData":[OSD([subQ1]),TDD([makeQuery(id+"F41.imprint","IMPRINT",EDGE,{"disambiguationData":[TD([[makeQuery(id+"F41.imprint","INTERSECT",VERTEX,{"disambiguationData":[OD(0.0)],"derivedFrom":[subQ1,subQ0]}),-1.0]])],"derivedFrom":subQ1})])]})]});}
            var Q76;
            {var subQ0=sQuery(id+"F4.wireOp",EDGE,"E26.13.3");var subQ1=sQuery(id+"F4.wireOp",EDGE,"E26.13.2");var subQ2=sQuery(id+"F4.wireOp",EDGE,"E26.13.1");var subQ3=sQuery(id+"F3.wireOp",EDGE,"E20.13.3");var subQ4=sQuery(id+"F3.wireOp",EDGE,"E20.13.1");var subQ5=makeQuery(id+"F8.opLoft","SWEPT_FACE",FACE,{"disambiguationData":[OSD([subQ4,sQuery(id+"F3.wireOp",EDGE,"E20.13.2"),subQ3,subQ2,subQ1,subQ0])]});var subQ6=sQuery(id+"F4.wireOp",EDGE,"E26.13.0");var subQ7=sQuery(id+"F41.wireOp",EDGE,"E34");var subQ8=sQuery(id+"F41.wireOp",EDGE,"E32");Q76=makeQuery(id+"F44.opFillet","BLEND_EDGE",EDGE,{"blendedFrom":[makeQuery(id+"F40.boolean.opBoolean","INTERSECT",EDGE,{"derivedFrom":[subQ5,makeQuery(id+"F40.opExtrude","CAP_FACE",FACE,{"disambiguationData":[OSD([sQuery(id+"F39.wireOp",EDGE,"E29"),sQuery(id+"F39.wireOp",EDGE,"E30")])],"isStart":false})]}),makeQuery(id+"F42.boolean.opBoolean","COPY",FACE,{"disambiguationData":[TD([makeQuery(id+"F8.opLoft","SWEPT_FACE",FACE,{"disambiguationData":[OSD([sQuery(id+"F3.wireOp",EDGE,"E20.13.0"),subQ4,subQ3,subQ6,subQ1,subQ0])]})])],"derivedFrom":makeQuery(id+"F42.opRevolve","SWEPT_FACE",FACE,{"disambiguationData":[OSD([subQ8]),TDD([makeQuery(id+"F41.imprint","IMPRINT",EDGE,{"disambiguationData":[TD([[makeQuery(id+"F41.imprint","INTERSECT",VERTEX,{"disambiguationData":[OD(0.0)],"derivedFrom":[subQ8,subQ7]}),-1.0]])],"derivedFrom":subQ8})])]})})],"blendedInto":[makeQuery(id+"F42.boolean.opBoolean","COPY",FACE,{"disambiguationData":[TD([makeQuery(id+"F8.opLoft","SWEPT_FACE",FACE,{"disambiguationData":[OSD([sQuery(id+"F3.wireOp",EDGE,"E20.13.0"),subQ4,subQ3,subQ6,subQ1,subQ0])]})])],"derivedFrom":makeQuery(id+"F42.opRevolve","SWEPT_FACE",FACE,{"disambiguationData":[OSD([subQ8]),TDD([makeQuery(id+"F41.imprint","IMPRINT",EDGE,{"disambiguationData":[TD([[makeQuery(id+"F41.imprint","INTERSECT",VERTEX,{"disambiguationData":[OD(0.0)],"derivedFrom":[subQ8,subQ7]}),-1.0]])],"derivedFrom":subQ8})])]})})]});}
            var Q77;
            {var subQ0=sQuery(id+"F41.wireOp",EDGE,"E34");var subQ1=sQuery(id+"F41.wireOp",EDGE,"E32");Q77=makeQuery(id+"F42.boolean.opBoolean","INTERSECT",EDGE,{"derivedFrom":[makeQuery(id+"F8.opLoft","SWEPT_FACE",FACE,{"disambiguationData":[OSD([sQuery(id+"F3.wireOp",EDGE,"E20.13.0"),sQuery(id+"F3.wireOp",EDGE,"E20.13.1"),sQuery(id+"F3.wireOp",EDGE,"E20.13.3"),sQuery(id+"F4.wireOp",EDGE,"E26.13.0"),sQuery(id+"F4.wireOp",EDGE,"E26.13.2"),sQuery(id+"F4.wireOp",EDGE,"E26.13.3")])]}),makeQuery(id+"F42.opRevolve","SWEPT_FACE",FACE,{"disambiguationData":[OSD([subQ1]),TDD([makeQuery(id+"F41.imprint","IMPRINT",EDGE,{"disambiguationData":[TD([[makeQuery(id+"F41.imprint","INTERSECT",VERTEX,{"disambiguationData":[OD(0.0)],"derivedFrom":[subQ1,subQ0]}),-1.0]])],"derivedFrom":subQ1})])]})]});}
            var Q78;
            {var subQ0=sQuery(id+"F4.wireOp",EDGE,"E26.14.0");var subQ1=sQuery(id+"F4.wireOp",EDGE,"E26.14.2");var subQ2=sQuery(id+"F4.wireOp",EDGE,"E26.14.1");var subQ3=sQuery(id+"F4.wireOp",EDGE,"E26.14.3");var subQ4=sQuery(id+"F3.wireOp",EDGE,"E20.14.3");var subQ5=sQuery(id+"F3.wireOp",EDGE,"E20.14.1");var subQ6=makeQuery(id+"F7.opLoft","SWEPT_FACE",FACE,{"disambiguationData":[OSD([subQ5,sQuery(id+"F3.wireOp",EDGE,"E20.14.2"),subQ4,subQ2,subQ1,subQ3])]});var subQ7=sQuery(id+"F41.wireOp",EDGE,"E34");var subQ8=sQuery(id+"F41.wireOp",EDGE,"E32");Q78=makeQuery(id+"F44.opFillet","BLEND_EDGE",EDGE,{"blendedFrom":[makeQuery(id+"F40.boolean.opBoolean","INTERSECT",EDGE,{"derivedFrom":[subQ6,makeQuery(id+"F40.opExtrude","CAP_FACE",FACE,{"disambiguationData":[OSD([sQuery(id+"F39.wireOp",EDGE,"E29"),sQuery(id+"F39.wireOp",EDGE,"E30")])],"isStart":false})]}),makeQuery(id+"F42.boolean.opBoolean","COPY",FACE,{"disambiguationData":[TD([makeQuery(id+"F7.opLoft","SWEPT_FACE",FACE,{"disambiguationData":[OSD([sQuery(id+"F3.wireOp",EDGE,"E20.14.0"),subQ5,subQ4,subQ0,subQ1,subQ3])]})])],"derivedFrom":makeQuery(id+"F42.opRevolve","SWEPT_FACE",FACE,{"disambiguationData":[OSD([subQ8]),TDD([makeQuery(id+"F41.imprint","IMPRINT",EDGE,{"disambiguationData":[TD([[makeQuery(id+"F41.imprint","INTERSECT",VERTEX,{"disambiguationData":[OD(0.0)],"derivedFrom":[subQ8,subQ7]}),-1.0]])],"derivedFrom":subQ8})])]})})],"blendedInto":[makeQuery(id+"F42.boolean.opBoolean","COPY",FACE,{"disambiguationData":[TD([makeQuery(id+"F7.opLoft","SWEPT_FACE",FACE,{"disambiguationData":[OSD([sQuery(id+"F3.wireOp",EDGE,"E20.14.0"),subQ5,subQ4,subQ0,subQ1,subQ3])]})])],"derivedFrom":makeQuery(id+"F42.opRevolve","SWEPT_FACE",FACE,{"disambiguationData":[OSD([subQ8]),TDD([makeQuery(id+"F41.imprint","IMPRINT",EDGE,{"disambiguationData":[TD([[makeQuery(id+"F41.imprint","INTERSECT",VERTEX,{"disambiguationData":[OD(0.0)],"derivedFrom":[subQ8,subQ7]}),-1.0]])],"derivedFrom":subQ8})])]})})]});}
            var Q79;
            {var subQ0=sQuery(id+"F41.wireOp",EDGE,"E34");var subQ1=sQuery(id+"F41.wireOp",EDGE,"E32");Q79=makeQuery(id+"F42.boolean.opBoolean","INTERSECT",EDGE,{"derivedFrom":[makeQuery(id+"F7.opLoft","SWEPT_FACE",FACE,{"disambiguationData":[OSD([sQuery(id+"F3.wireOp",EDGE,"E20.14.0"),sQuery(id+"F3.wireOp",EDGE,"E20.14.1"),sQuery(id+"F3.wireOp",EDGE,"E20.14.3"),sQuery(id+"F4.wireOp",EDGE,"E26.14.0"),sQuery(id+"F4.wireOp",EDGE,"E26.14.2"),sQuery(id+"F4.wireOp",EDGE,"E26.14.3")])]}),makeQuery(id+"F42.opRevolve","SWEPT_FACE",FACE,{"disambiguationData":[OSD([subQ1]),TDD([makeQuery(id+"F41.imprint","IMPRINT",EDGE,{"disambiguationData":[TD([[makeQuery(id+"F41.imprint","INTERSECT",VERTEX,{"disambiguationData":[OD(0.0)],"derivedFrom":[subQ1,subQ0]}),-1.0]])],"derivedFrom":subQ1})])]})]});}
            var Q80;
            {var subQ0=sQuery(id+"F4.wireOp",EDGE,"E26.15.3");var subQ1=sQuery(id+"F4.wireOp",EDGE,"E26.15.2");var subQ2=sQuery(id+"F4.wireOp",EDGE,"E26.15.0");var subQ3=sQuery(id+"F3.wireOp",EDGE,"E20.15.3");var subQ4=sQuery(id+"F3.wireOp",EDGE,"E20.15.1");var subQ5=sQuery(id+"F4.wireOp",EDGE,"E26.15.1");var subQ6=makeQuery(id+"F6.opLoft","SWEPT_FACE",FACE,{"disambiguationData":[OSD([subQ4,sQuery(id+"F3.wireOp",EDGE,"E20.15.2"),subQ3,subQ5,subQ1,subQ0])]});var subQ7=sQuery(id+"F41.wireOp",EDGE,"E34");var subQ8=sQuery(id+"F41.wireOp",EDGE,"E32");Q80=makeQuery(id+"F44.opFillet","BLEND_EDGE",EDGE,{"blendedFrom":[makeQuery(id+"F40.boolean.opBoolean","INTERSECT",EDGE,{"derivedFrom":[subQ6,makeQuery(id+"F40.opExtrude","CAP_FACE",FACE,{"disambiguationData":[OSD([sQuery(id+"F39.wireOp",EDGE,"E29"),sQuery(id+"F39.wireOp",EDGE,"E30")])],"isStart":false})]}),makeQuery(id+"F42.boolean.opBoolean","COPY",FACE,{"disambiguationData":[TD([makeQuery(id+"F6.opLoft","SWEPT_FACE",FACE,{"disambiguationData":[OSD([sQuery(id+"F3.wireOp",EDGE,"E20.15.0"),subQ4,subQ3,subQ2,subQ1,subQ0])]})])],"derivedFrom":makeQuery(id+"F42.opRevolve","SWEPT_FACE",FACE,{"disambiguationData":[OSD([subQ8]),TDD([makeQuery(id+"F41.imprint","IMPRINT",EDGE,{"disambiguationData":[TD([[makeQuery(id+"F41.imprint","INTERSECT",VERTEX,{"disambiguationData":[OD(0.0)],"derivedFrom":[subQ8,subQ7]}),-1.0]])],"derivedFrom":subQ8})])]})})],"blendedInto":[makeQuery(id+"F42.boolean.opBoolean","COPY",FACE,{"disambiguationData":[TD([makeQuery(id+"F6.opLoft","SWEPT_FACE",FACE,{"disambiguationData":[OSD([sQuery(id+"F3.wireOp",EDGE,"E20.15.0"),subQ4,subQ3,subQ2,subQ1,subQ0])]})])],"derivedFrom":makeQuery(id+"F42.opRevolve","SWEPT_FACE",FACE,{"disambiguationData":[OSD([subQ8]),TDD([makeQuery(id+"F41.imprint","IMPRINT",EDGE,{"disambiguationData":[TD([[makeQuery(id+"F41.imprint","INTERSECT",VERTEX,{"disambiguationData":[OD(0.0)],"derivedFrom":[subQ8,subQ7]}),-1.0]])],"derivedFrom":subQ8})])]})})]});}
            var Q81;
            {var subQ0=sQuery(id+"F41.wireOp",EDGE,"E34");var subQ1=sQuery(id+"F41.wireOp",EDGE,"E32");Q81=makeQuery(id+"F42.boolean.opBoolean","INTERSECT",EDGE,{"derivedFrom":[makeQuery(id+"F6.opLoft","SWEPT_FACE",FACE,{"disambiguationData":[OSD([sQuery(id+"F3.wireOp",EDGE,"E20.15.0"),sQuery(id+"F3.wireOp",EDGE,"E20.15.1"),sQuery(id+"F3.wireOp",EDGE,"E20.15.3"),sQuery(id+"F4.wireOp",EDGE,"E26.15.0"),sQuery(id+"F4.wireOp",EDGE,"E26.15.2"),sQuery(id+"F4.wireOp",EDGE,"E26.15.3")])]}),makeQuery(id+"F42.opRevolve","SWEPT_FACE",FACE,{"disambiguationData":[OSD([subQ1]),TDD([makeQuery(id+"F41.imprint","IMPRINT",EDGE,{"disambiguationData":[TD([[makeQuery(id+"F41.imprint","INTERSECT",VERTEX,{"disambiguationData":[OD(0.0)],"derivedFrom":[subQ1,subQ0]}),-1.0]])],"derivedFrom":subQ1})])]})]});}
            var Q82;
            {var subQ0=sQuery(id+"F4.wireOp",EDGE,"E23");var subQ1=sQuery(id+"F4.wireOp",EDGE,"E22");var subQ2=sQuery(id+"F4.wireOp",EDGE,"E21");var subQ3=sQuery(id+"F3.wireOp",EDGE,"E18.top");var subQ4=sQuery(id+"F3.wireOp",EDGE,"E18.bottom");var subQ5=sQuery(id+"F4.wireOp",EDGE,"E24");var subQ6=makeQuery(id+"F5.opLoft","SWEPT_FACE",FACE,{"disambiguationData":[OSD([subQ4,subQ3,sQuery(id+"F3.wireOp",EDGE,"E18.right"),subQ1,subQ0,subQ5])]});var subQ7=sQuery(id+"F41.wireOp",EDGE,"E34");var subQ8=sQuery(id+"F41.wireOp",EDGE,"E32");Q82=makeQuery(id+"F44.opFillet","BLEND_EDGE",EDGE,{"blendedFrom":[makeQuery(id+"F40.boolean.opBoolean","INTERSECT",EDGE,{"derivedFrom":[subQ6,makeQuery(id+"F40.opExtrude","CAP_FACE",FACE,{"disambiguationData":[OSD([sQuery(id+"F39.wireOp",EDGE,"E29"),sQuery(id+"F39.wireOp",EDGE,"E30")])],"isStart":false})]}),makeQuery(id+"F42.boolean.opBoolean","COPY",FACE,{"disambiguationData":[TD([makeQuery(id+"F5.opLoft","SWEPT_FACE",FACE,{"disambiguationData":[OSD([subQ4,subQ3,sQuery(id+"F3.wireOp",EDGE,"E18.left"),subQ2,subQ1,subQ0])]})])],"derivedFrom":makeQuery(id+"F42.opRevolve","SWEPT_FACE",FACE,{"disambiguationData":[OSD([subQ8]),TDD([makeQuery(id+"F41.imprint","IMPRINT",EDGE,{"disambiguationData":[TD([[makeQuery(id+"F41.imprint","INTERSECT",VERTEX,{"disambiguationData":[OD(0.0)],"derivedFrom":[subQ8,subQ7]}),-1.0]])],"derivedFrom":subQ8})])]})})],"blendedInto":[makeQuery(id+"F42.boolean.opBoolean","COPY",FACE,{"disambiguationData":[TD([makeQuery(id+"F5.opLoft","SWEPT_FACE",FACE,{"disambiguationData":[OSD([subQ4,subQ3,sQuery(id+"F3.wireOp",EDGE,"E18.left"),subQ2,subQ1,subQ0])]})])],"derivedFrom":makeQuery(id+"F42.opRevolve","SWEPT_FACE",FACE,{"disambiguationData":[OSD([subQ8]),TDD([makeQuery(id+"F41.imprint","IMPRINT",EDGE,{"disambiguationData":[TD([[makeQuery(id+"F41.imprint","INTERSECT",VERTEX,{"disambiguationData":[OD(0.0)],"derivedFrom":[subQ8,subQ7]}),-1.0]])],"derivedFrom":subQ8})])]})})]});}
            var Q83;
            {var subQ0=sQuery(id+"F41.wireOp",EDGE,"E34");var subQ1=sQuery(id+"F41.wireOp",EDGE,"E32");Q83=makeQuery(id+"F42.boolean.opBoolean","INTERSECT",EDGE,{"derivedFrom":[makeQuery(id+"F5.opLoft","SWEPT_FACE",FACE,{"disambiguationData":[OSD([sQuery(id+"F3.wireOp",EDGE,"E18.bottom"),sQuery(id+"F3.wireOp",EDGE,"E18.top"),sQuery(id+"F3.wireOp",EDGE,"E18.left"),sQuery(id+"F4.wireOp",EDGE,"E21"),sQuery(id+"F4.wireOp",EDGE,"E22"),sQuery(id+"F4.wireOp",EDGE,"E23")])]}),makeQuery(id+"F42.opRevolve","SWEPT_FACE",FACE,{"disambiguationData":[OSD([subQ1]),TDD([makeQuery(id+"F41.imprint","IMPRINT",EDGE,{"disambiguationData":[TD([[makeQuery(id+"F41.imprint","INTERSECT",VERTEX,{"disambiguationData":[OD(0.0)],"derivedFrom":[subQ1,subQ0]}),-1.0]])],"derivedFrom":subQ1})])]})]});}
            var Q84;
            {var subQ0=sQuery(id+"F4.wireOp",EDGE,"E26.1.3");var subQ1=sQuery(id+"F4.wireOp",EDGE,"E26.1.2");var subQ2=sQuery(id+"F4.wireOp",EDGE,"E26.1.0");var subQ3=sQuery(id+"F3.wireOp",EDGE,"E20.1.3");var subQ4=sQuery(id+"F3.wireOp",EDGE,"E20.1.1");var subQ5=sQuery(id+"F4.wireOp",EDGE,"E26.1.1");var subQ6=makeQuery(id+"F20.opLoft","SWEPT_FACE",FACE,{"disambiguationData":[OSD([subQ4,sQuery(id+"F3.wireOp",EDGE,"E20.1.2"),subQ3,subQ5,subQ1,subQ0])]});var subQ7=sQuery(id+"F41.wireOp",EDGE,"E34");var subQ8=sQuery(id+"F41.wireOp",EDGE,"E32");Q84=makeQuery(id+"F44.opFillet","BLEND_EDGE",EDGE,{"blendedFrom":[makeQuery(id+"F40.boolean.opBoolean","INTERSECT",EDGE,{"derivedFrom":[subQ6,makeQuery(id+"F40.opExtrude","CAP_FACE",FACE,{"disambiguationData":[OSD([sQuery(id+"F39.wireOp",EDGE,"E29"),sQuery(id+"F39.wireOp",EDGE,"E30")])],"isStart":false})]}),makeQuery(id+"F42.boolean.opBoolean","COPY",FACE,{"disambiguationData":[TD([makeQuery(id+"F20.opLoft","SWEPT_FACE",FACE,{"disambiguationData":[OSD([sQuery(id+"F3.wireOp",EDGE,"E20.1.0"),subQ4,subQ3,subQ2,subQ1,subQ0])]})])],"derivedFrom":makeQuery(id+"F42.opRevolve","SWEPT_FACE",FACE,{"disambiguationData":[OSD([subQ8]),TDD([makeQuery(id+"F41.imprint","IMPRINT",EDGE,{"disambiguationData":[TD([[makeQuery(id+"F41.imprint","INTERSECT",VERTEX,{"disambiguationData":[OD(0.0)],"derivedFrom":[subQ8,subQ7]}),-1.0]])],"derivedFrom":subQ8})])]})})],"blendedInto":[makeQuery(id+"F42.boolean.opBoolean","COPY",FACE,{"disambiguationData":[TD([makeQuery(id+"F20.opLoft","SWEPT_FACE",FACE,{"disambiguationData":[OSD([sQuery(id+"F3.wireOp",EDGE,"E20.1.0"),subQ4,subQ3,subQ2,subQ1,subQ0])]})])],"derivedFrom":makeQuery(id+"F42.opRevolve","SWEPT_FACE",FACE,{"disambiguationData":[OSD([subQ8]),TDD([makeQuery(id+"F41.imprint","IMPRINT",EDGE,{"disambiguationData":[TD([[makeQuery(id+"F41.imprint","INTERSECT",VERTEX,{"disambiguationData":[OD(0.0)],"derivedFrom":[subQ8,subQ7]}),-1.0]])],"derivedFrom":subQ8})])]})})]});}
            var Q85;
            {var subQ0=sQuery(id+"F41.wireOp",EDGE,"E34");var subQ1=sQuery(id+"F41.wireOp",EDGE,"E32");Q85=makeQuery(id+"F42.boolean.opBoolean","INTERSECT",EDGE,{"derivedFrom":[makeQuery(id+"F20.opLoft","SWEPT_FACE",FACE,{"disambiguationData":[OSD([sQuery(id+"F3.wireOp",EDGE,"E20.1.0"),sQuery(id+"F3.wireOp",EDGE,"E20.1.1"),sQuery(id+"F3.wireOp",EDGE,"E20.1.3"),sQuery(id+"F4.wireOp",EDGE,"E26.1.0"),sQuery(id+"F4.wireOp",EDGE,"E26.1.2"),sQuery(id+"F4.wireOp",EDGE,"E26.1.3")])]}),makeQuery(id+"F42.opRevolve","SWEPT_FACE",FACE,{"disambiguationData":[OSD([subQ1]),TDD([makeQuery(id+"F41.imprint","IMPRINT",EDGE,{"disambiguationData":[TD([[makeQuery(id+"F41.imprint","INTERSECT",VERTEX,{"disambiguationData":[OD(0.0)],"derivedFrom":[subQ1,subQ0]}),-1.0]])],"derivedFrom":subQ1})])]})]});}
            var Q86;
            {var subQ0=sQuery(id+"F4.wireOp",EDGE,"E26.2.3");var subQ1=sQuery(id+"F4.wireOp",EDGE,"E26.2.2");var subQ2=sQuery(id+"F4.wireOp",EDGE,"E26.2.1");var subQ3=sQuery(id+"F3.wireOp",EDGE,"E20.2.3");var subQ4=sQuery(id+"F3.wireOp",EDGE,"E20.2.1");var subQ5=makeQuery(id+"F19.opLoft","SWEPT_FACE",FACE,{"disambiguationData":[OSD([subQ4,sQuery(id+"F3.wireOp",EDGE,"E20.2.2"),subQ3,subQ2,subQ1,subQ0])]});var subQ6=sQuery(id+"F4.wireOp",EDGE,"E26.2.0");var subQ7=sQuery(id+"F41.wireOp",EDGE,"E34");var subQ8=sQuery(id+"F41.wireOp",EDGE,"E32");Q86=makeQuery(id+"F44.opFillet","BLEND_EDGE",EDGE,{"blendedFrom":[makeQuery(id+"F40.boolean.opBoolean","INTERSECT",EDGE,{"derivedFrom":[subQ5,makeQuery(id+"F40.opExtrude","CAP_FACE",FACE,{"disambiguationData":[OSD([sQuery(id+"F39.wireOp",EDGE,"E29"),sQuery(id+"F39.wireOp",EDGE,"E30")])],"isStart":false})]}),makeQuery(id+"F42.boolean.opBoolean","COPY",FACE,{"disambiguationData":[TD([makeQuery(id+"F19.opLoft","SWEPT_FACE",FACE,{"disambiguationData":[OSD([sQuery(id+"F3.wireOp",EDGE,"E20.2.0"),subQ4,subQ3,subQ6,subQ1,subQ0])]})])],"derivedFrom":makeQuery(id+"F42.opRevolve","SWEPT_FACE",FACE,{"disambiguationData":[OSD([subQ8]),TDD([makeQuery(id+"F41.imprint","IMPRINT",EDGE,{"disambiguationData":[TD([[makeQuery(id+"F41.imprint","INTERSECT",VERTEX,{"disambiguationData":[OD(0.0)],"derivedFrom":[subQ8,subQ7]}),-1.0]])],"derivedFrom":subQ8})])]})})],"blendedInto":[makeQuery(id+"F42.boolean.opBoolean","COPY",FACE,{"disambiguationData":[TD([makeQuery(id+"F19.opLoft","SWEPT_FACE",FACE,{"disambiguationData":[OSD([sQuery(id+"F3.wireOp",EDGE,"E20.2.0"),subQ4,subQ3,subQ6,subQ1,subQ0])]})])],"derivedFrom":makeQuery(id+"F42.opRevolve","SWEPT_FACE",FACE,{"disambiguationData":[OSD([subQ8]),TDD([makeQuery(id+"F41.imprint","IMPRINT",EDGE,{"disambiguationData":[TD([[makeQuery(id+"F41.imprint","INTERSECT",VERTEX,{"disambiguationData":[OD(0.0)],"derivedFrom":[subQ8,subQ7]}),-1.0]])],"derivedFrom":subQ8})])]})})]});}
            var Q87;
            {var subQ0=sQuery(id+"F41.wireOp",EDGE,"E34");var subQ1=sQuery(id+"F41.wireOp",EDGE,"E32");Q87=makeQuery(id+"F42.boolean.opBoolean","INTERSECT",EDGE,{"derivedFrom":[makeQuery(id+"F19.opLoft","SWEPT_FACE",FACE,{"disambiguationData":[OSD([sQuery(id+"F3.wireOp",EDGE,"E20.2.0"),sQuery(id+"F3.wireOp",EDGE,"E20.2.1"),sQuery(id+"F3.wireOp",EDGE,"E20.2.3"),sQuery(id+"F4.wireOp",EDGE,"E26.2.0"),sQuery(id+"F4.wireOp",EDGE,"E26.2.2"),sQuery(id+"F4.wireOp",EDGE,"E26.2.3")])]}),makeQuery(id+"F42.opRevolve","SWEPT_FACE",FACE,{"disambiguationData":[OSD([subQ1]),TDD([makeQuery(id+"F41.imprint","IMPRINT",EDGE,{"disambiguationData":[TD([[makeQuery(id+"F41.imprint","INTERSECT",VERTEX,{"disambiguationData":[OD(0.0)],"derivedFrom":[subQ1,subQ0]}),-1.0]])],"derivedFrom":subQ1})])]})]});}
            var Q88;
            {var subQ0=sQuery(id+"F4.wireOp",EDGE,"E26.3.0");var subQ1=sQuery(id+"F4.wireOp",EDGE,"E26.3.1");var subQ2=sQuery(id+"F4.wireOp",EDGE,"E26.3.2");var subQ3=sQuery(id+"F4.wireOp",EDGE,"E26.3.3");var subQ4=sQuery(id+"F3.wireOp",EDGE,"E20.3.3");var subQ5=sQuery(id+"F3.wireOp",EDGE,"E20.3.1");var subQ6=makeQuery(id+"F18.opLoft","SWEPT_FACE",FACE,{"disambiguationData":[OSD([subQ5,sQuery(id+"F3.wireOp",EDGE,"E20.3.2"),subQ4,subQ1,subQ2,subQ3])]});var subQ7=sQuery(id+"F41.wireOp",EDGE,"E34");var subQ8=sQuery(id+"F41.wireOp",EDGE,"E32");Q88=makeQuery(id+"F44.opFillet","BLEND_EDGE",EDGE,{"blendedFrom":[makeQuery(id+"F40.boolean.opBoolean","INTERSECT",EDGE,{"derivedFrom":[subQ6,makeQuery(id+"F40.opExtrude","CAP_FACE",FACE,{"disambiguationData":[OSD([sQuery(id+"F39.wireOp",EDGE,"E29"),sQuery(id+"F39.wireOp",EDGE,"E30")])],"isStart":false})]}),makeQuery(id+"F42.boolean.opBoolean","COPY",FACE,{"disambiguationData":[TD([makeQuery(id+"F18.opLoft","SWEPT_FACE",FACE,{"disambiguationData":[OSD([sQuery(id+"F3.wireOp",EDGE,"E20.3.0"),subQ5,subQ4,subQ0,subQ2,subQ3])]})])],"derivedFrom":makeQuery(id+"F42.opRevolve","SWEPT_FACE",FACE,{"disambiguationData":[OSD([subQ8]),TDD([makeQuery(id+"F41.imprint","IMPRINT",EDGE,{"disambiguationData":[TD([[makeQuery(id+"F41.imprint","INTERSECT",VERTEX,{"disambiguationData":[OD(0.0)],"derivedFrom":[subQ8,subQ7]}),-1.0]])],"derivedFrom":subQ8})])]})})],"blendedInto":[makeQuery(id+"F42.boolean.opBoolean","COPY",FACE,{"disambiguationData":[TD([makeQuery(id+"F18.opLoft","SWEPT_FACE",FACE,{"disambiguationData":[OSD([sQuery(id+"F3.wireOp",EDGE,"E20.3.0"),subQ5,subQ4,subQ0,subQ2,subQ3])]})])],"derivedFrom":makeQuery(id+"F42.opRevolve","SWEPT_FACE",FACE,{"disambiguationData":[OSD([subQ8]),TDD([makeQuery(id+"F41.imprint","IMPRINT",EDGE,{"disambiguationData":[TD([[makeQuery(id+"F41.imprint","INTERSECT",VERTEX,{"disambiguationData":[OD(0.0)],"derivedFrom":[subQ8,subQ7]}),-1.0]])],"derivedFrom":subQ8})])]})})]});}
            var Q89;
            {var subQ0=sQuery(id+"F41.wireOp",EDGE,"E34");var subQ1=sQuery(id+"F41.wireOp",EDGE,"E32");Q89=makeQuery(id+"F42.boolean.opBoolean","INTERSECT",EDGE,{"derivedFrom":[makeQuery(id+"F18.opLoft","SWEPT_FACE",FACE,{"disambiguationData":[OSD([sQuery(id+"F3.wireOp",EDGE,"E20.3.0"),sQuery(id+"F3.wireOp",EDGE,"E20.3.1"),sQuery(id+"F3.wireOp",EDGE,"E20.3.3"),sQuery(id+"F4.wireOp",EDGE,"E26.3.0"),sQuery(id+"F4.wireOp",EDGE,"E26.3.2"),sQuery(id+"F4.wireOp",EDGE,"E26.3.3")])]}),makeQuery(id+"F42.opRevolve","SWEPT_FACE",FACE,{"disambiguationData":[OSD([subQ1]),TDD([makeQuery(id+"F41.imprint","IMPRINT",EDGE,{"disambiguationData":[TD([[makeQuery(id+"F41.imprint","INTERSECT",VERTEX,{"disambiguationData":[OD(0.0)],"derivedFrom":[subQ1,subQ0]}),-1.0]])],"derivedFrom":subQ1})])]})]});}
            var Q90;
            {var subQ0=sQuery(id+"F4.wireOp",EDGE,"E26.4.3");var subQ1=sQuery(id+"F4.wireOp",EDGE,"E26.4.2");var subQ2=sQuery(id+"F4.wireOp",EDGE,"E26.4.1");var subQ3=sQuery(id+"F3.wireOp",EDGE,"E20.4.3");var subQ4=sQuery(id+"F3.wireOp",EDGE,"E20.4.1");var subQ5=makeQuery(id+"F17.opLoft","SWEPT_FACE",FACE,{"disambiguationData":[OSD([subQ4,sQuery(id+"F3.wireOp",EDGE,"E20.4.2"),subQ3,subQ2,subQ1,subQ0])]});var subQ6=sQuery(id+"F4.wireOp",EDGE,"E26.4.0");var subQ7=sQuery(id+"F41.wireOp",EDGE,"E34");var subQ8=sQuery(id+"F41.wireOp",EDGE,"E32");Q90=makeQuery(id+"F44.opFillet","BLEND_EDGE",EDGE,{"blendedFrom":[makeQuery(id+"F40.boolean.opBoolean","INTERSECT",EDGE,{"derivedFrom":[subQ5,makeQuery(id+"F40.opExtrude","CAP_FACE",FACE,{"disambiguationData":[OSD([sQuery(id+"F39.wireOp",EDGE,"E29"),sQuery(id+"F39.wireOp",EDGE,"E30")])],"isStart":false})]}),makeQuery(id+"F42.boolean.opBoolean","COPY",FACE,{"disambiguationData":[TD([makeQuery(id+"F17.opLoft","SWEPT_FACE",FACE,{"disambiguationData":[OSD([sQuery(id+"F3.wireOp",EDGE,"E20.4.0"),subQ4,subQ3,subQ6,subQ1,subQ0])]})])],"derivedFrom":makeQuery(id+"F42.opRevolve","SWEPT_FACE",FACE,{"disambiguationData":[OSD([subQ8]),TDD([makeQuery(id+"F41.imprint","IMPRINT",EDGE,{"disambiguationData":[TD([[makeQuery(id+"F41.imprint","INTERSECT",VERTEX,{"disambiguationData":[OD(0.0)],"derivedFrom":[subQ8,subQ7]}),-1.0]])],"derivedFrom":subQ8})])]})})],"blendedInto":[makeQuery(id+"F42.boolean.opBoolean","COPY",FACE,{"disambiguationData":[TD([makeQuery(id+"F17.opLoft","SWEPT_FACE",FACE,{"disambiguationData":[OSD([sQuery(id+"F3.wireOp",EDGE,"E20.4.0"),subQ4,subQ3,subQ6,subQ1,subQ0])]})])],"derivedFrom":makeQuery(id+"F42.opRevolve","SWEPT_FACE",FACE,{"disambiguationData":[OSD([subQ8]),TDD([makeQuery(id+"F41.imprint","IMPRINT",EDGE,{"disambiguationData":[TD([[makeQuery(id+"F41.imprint","INTERSECT",VERTEX,{"disambiguationData":[OD(0.0)],"derivedFrom":[subQ8,subQ7]}),-1.0]])],"derivedFrom":subQ8})])]})})]});}
            var Q91;
            {var subQ0=sQuery(id+"F41.wireOp",EDGE,"E34");var subQ1=sQuery(id+"F41.wireOp",EDGE,"E32");Q91=makeQuery(id+"F42.boolean.opBoolean","INTERSECT",EDGE,{"derivedFrom":[makeQuery(id+"F17.opLoft","SWEPT_FACE",FACE,{"disambiguationData":[OSD([sQuery(id+"F3.wireOp",EDGE,"E20.4.0"),sQuery(id+"F3.wireOp",EDGE,"E20.4.1"),sQuery(id+"F3.wireOp",EDGE,"E20.4.3"),sQuery(id+"F4.wireOp",EDGE,"E26.4.0"),sQuery(id+"F4.wireOp",EDGE,"E26.4.2"),sQuery(id+"F4.wireOp",EDGE,"E26.4.3")])]}),makeQuery(id+"F42.opRevolve","SWEPT_FACE",FACE,{"disambiguationData":[OSD([subQ1]),TDD([makeQuery(id+"F41.imprint","IMPRINT",EDGE,{"disambiguationData":[TD([[makeQuery(id+"F41.imprint","INTERSECT",VERTEX,{"disambiguationData":[OD(0.0)],"derivedFrom":[subQ1,subQ0]}),-1.0]])],"derivedFrom":subQ1})])]})]});}
            var Q92;
            {var subQ0=sQuery(id+"F4.wireOp",EDGE,"E26.5.3");var subQ1=sQuery(id+"F4.wireOp",EDGE,"E26.5.2");var subQ2=sQuery(id+"F4.wireOp",EDGE,"E26.5.1");var subQ3=sQuery(id+"F3.wireOp",EDGE,"E20.5.3");var subQ4=sQuery(id+"F3.wireOp",EDGE,"E20.5.1");var subQ5=makeQuery(id+"F16.opLoft","SWEPT_FACE",FACE,{"disambiguationData":[OSD([subQ4,sQuery(id+"F3.wireOp",EDGE,"E20.5.2"),subQ3,subQ2,subQ1,subQ0])]});var subQ6=sQuery(id+"F4.wireOp",EDGE,"E26.5.0");var subQ7=sQuery(id+"F41.wireOp",EDGE,"E34");var subQ8=sQuery(id+"F41.wireOp",EDGE,"E32");Q92=makeQuery(id+"F44.opFillet","BLEND_EDGE",EDGE,{"blendedFrom":[makeQuery(id+"F40.boolean.opBoolean","INTERSECT",EDGE,{"derivedFrom":[subQ5,makeQuery(id+"F40.opExtrude","CAP_FACE",FACE,{"disambiguationData":[OSD([sQuery(id+"F39.wireOp",EDGE,"E29"),sQuery(id+"F39.wireOp",EDGE,"E30")])],"isStart":false})]}),makeQuery(id+"F42.boolean.opBoolean","COPY",FACE,{"disambiguationData":[TD([makeQuery(id+"F16.opLoft","SWEPT_FACE",FACE,{"disambiguationData":[OSD([sQuery(id+"F3.wireOp",EDGE,"E20.5.0"),subQ4,subQ3,subQ6,subQ1,subQ0])]})])],"derivedFrom":makeQuery(id+"F42.opRevolve","SWEPT_FACE",FACE,{"disambiguationData":[OSD([subQ8]),TDD([makeQuery(id+"F41.imprint","IMPRINT",EDGE,{"disambiguationData":[TD([[makeQuery(id+"F41.imprint","INTERSECT",VERTEX,{"disambiguationData":[OD(0.0)],"derivedFrom":[subQ8,subQ7]}),-1.0]])],"derivedFrom":subQ8})])]})})],"blendedInto":[makeQuery(id+"F42.boolean.opBoolean","COPY",FACE,{"disambiguationData":[TD([makeQuery(id+"F16.opLoft","SWEPT_FACE",FACE,{"disambiguationData":[OSD([sQuery(id+"F3.wireOp",EDGE,"E20.5.0"),subQ4,subQ3,subQ6,subQ1,subQ0])]})])],"derivedFrom":makeQuery(id+"F42.opRevolve","SWEPT_FACE",FACE,{"disambiguationData":[OSD([subQ8]),TDD([makeQuery(id+"F41.imprint","IMPRINT",EDGE,{"disambiguationData":[TD([[makeQuery(id+"F41.imprint","INTERSECT",VERTEX,{"disambiguationData":[OD(0.0)],"derivedFrom":[subQ8,subQ7]}),-1.0]])],"derivedFrom":subQ8})])]})})]});}
            var Q93;
            {var subQ0=sQuery(id+"F41.wireOp",EDGE,"E34");var subQ1=sQuery(id+"F41.wireOp",EDGE,"E32");Q93=makeQuery(id+"F42.boolean.opBoolean","INTERSECT",EDGE,{"derivedFrom":[makeQuery(id+"F16.opLoft","SWEPT_FACE",FACE,{"disambiguationData":[OSD([sQuery(id+"F3.wireOp",EDGE,"E20.5.0"),sQuery(id+"F3.wireOp",EDGE,"E20.5.1"),sQuery(id+"F3.wireOp",EDGE,"E20.5.3"),sQuery(id+"F4.wireOp",EDGE,"E26.5.0"),sQuery(id+"F4.wireOp",EDGE,"E26.5.2"),sQuery(id+"F4.wireOp",EDGE,"E26.5.3")])]}),makeQuery(id+"F42.opRevolve","SWEPT_FACE",FACE,{"disambiguationData":[OSD([subQ1]),TDD([makeQuery(id+"F41.imprint","IMPRINT",EDGE,{"disambiguationData":[TD([[makeQuery(id+"F41.imprint","INTERSECT",VERTEX,{"disambiguationData":[OD(0.0)],"derivedFrom":[subQ1,subQ0]}),-1.0]])],"derivedFrom":subQ1})])]})]});}
            var Q94;
            {var subQ0=sQuery(id+"F4.wireOp",EDGE,"E26.6.3");var subQ1=sQuery(id+"F4.wireOp",EDGE,"E26.6.2");var subQ2=sQuery(id+"F4.wireOp",EDGE,"E26.6.0");var subQ3=sQuery(id+"F3.wireOp",EDGE,"E20.6.3");var subQ4=sQuery(id+"F3.wireOp",EDGE,"E20.6.1");var subQ5=sQuery(id+"F4.wireOp",EDGE,"E26.6.1");var subQ6=makeQuery(id+"F15.opLoft","SWEPT_FACE",FACE,{"disambiguationData":[OSD([subQ4,sQuery(id+"F3.wireOp",EDGE,"E20.6.2"),subQ3,subQ5,subQ1,subQ0])]});var subQ7=sQuery(id+"F41.wireOp",EDGE,"E34");var subQ8=sQuery(id+"F41.wireOp",EDGE,"E32");Q94=makeQuery(id+"F44.opFillet","BLEND_EDGE",EDGE,{"blendedFrom":[makeQuery(id+"F40.boolean.opBoolean","INTERSECT",EDGE,{"derivedFrom":[subQ6,makeQuery(id+"F40.opExtrude","CAP_FACE",FACE,{"disambiguationData":[OSD([sQuery(id+"F39.wireOp",EDGE,"E29"),sQuery(id+"F39.wireOp",EDGE,"E30")])],"isStart":false})]}),makeQuery(id+"F42.boolean.opBoolean","COPY",FACE,{"disambiguationData":[TD([makeQuery(id+"F15.opLoft","SWEPT_FACE",FACE,{"disambiguationData":[OSD([sQuery(id+"F3.wireOp",EDGE,"E20.6.0"),subQ4,subQ3,subQ2,subQ1,subQ0])]})])],"derivedFrom":makeQuery(id+"F42.opRevolve","SWEPT_FACE",FACE,{"disambiguationData":[OSD([subQ8]),TDD([makeQuery(id+"F41.imprint","IMPRINT",EDGE,{"disambiguationData":[TD([[makeQuery(id+"F41.imprint","INTERSECT",VERTEX,{"disambiguationData":[OD(0.0)],"derivedFrom":[subQ8,subQ7]}),-1.0]])],"derivedFrom":subQ8})])]})})],"blendedInto":[makeQuery(id+"F42.boolean.opBoolean","COPY",FACE,{"disambiguationData":[TD([makeQuery(id+"F15.opLoft","SWEPT_FACE",FACE,{"disambiguationData":[OSD([sQuery(id+"F3.wireOp",EDGE,"E20.6.0"),subQ4,subQ3,subQ2,subQ1,subQ0])]})])],"derivedFrom":makeQuery(id+"F42.opRevolve","SWEPT_FACE",FACE,{"disambiguationData":[OSD([subQ8]),TDD([makeQuery(id+"F41.imprint","IMPRINT",EDGE,{"disambiguationData":[TD([[makeQuery(id+"F41.imprint","INTERSECT",VERTEX,{"disambiguationData":[OD(0.0)],"derivedFrom":[subQ8,subQ7]}),-1.0]])],"derivedFrom":subQ8})])]})})]});}
            var Q95;
            {var subQ0=sQuery(id+"F41.wireOp",EDGE,"E34");var subQ1=sQuery(id+"F41.wireOp",EDGE,"E32");Q95=makeQuery(id+"F42.boolean.opBoolean","INTERSECT",EDGE,{"derivedFrom":[makeQuery(id+"F15.opLoft","SWEPT_FACE",FACE,{"disambiguationData":[OSD([sQuery(id+"F3.wireOp",EDGE,"E20.6.0"),sQuery(id+"F3.wireOp",EDGE,"E20.6.1"),sQuery(id+"F3.wireOp",EDGE,"E20.6.3"),sQuery(id+"F4.wireOp",EDGE,"E26.6.0"),sQuery(id+"F4.wireOp",EDGE,"E26.6.2"),sQuery(id+"F4.wireOp",EDGE,"E26.6.3")])]}),makeQuery(id+"F42.opRevolve","SWEPT_FACE",FACE,{"disambiguationData":[OSD([subQ1]),TDD([makeQuery(id+"F41.imprint","IMPRINT",EDGE,{"disambiguationData":[TD([[makeQuery(id+"F41.imprint","INTERSECT",VERTEX,{"disambiguationData":[OD(0.0)],"derivedFrom":[subQ1,subQ0]}),-1.0]])],"derivedFrom":subQ1})])]})]});}
            fillet(context, id + "F49", {"entities" : qUnion([Q0, Q1, Q2, Q3, Q4, Q5, Q6, Q7, Q8, Q9, Q10, Q11, Q12, Q13, Q14, Q15, Q16, Q17, Q18, Q19, Q20, Q21, Q22, Q23, Q24, Q25, Q26, Q27, Q28, Q29, Q30, Q31, Q32, Q33, Q34, Q35, Q36, Q37, Q38, Q39, Q40, Q41, Q42, Q43, Q44, Q45, Q46, Q47, Q48, Q49, Q50, Q51, Q52, Q53, Q54, Q55, Q56, Q57, Q58, Q59, Q60, Q61, Q62, Q63, Q64, Q65, Q66, Q67, Q68, Q69, Q70, Q71, Q72, Q73, Q74, Q75, Q76, Q77, Q78, Q79, Q80, Q81, Q82, Q83, Q84, Q85, Q86, Q87, Q88, Q89, Q90, Q91, Q92, Q93, Q94, Q95]), "radius" : 0.5 * mm, "tangentPropagation" : true, "allowEdgeOverflow" : false});
        }
        {
            var Q0;
            Q0=makeQuery(id+"F1.opRevolve","SWEPT_EDGE",EDGE,{"disambiguationData":[OSD([sQuery(id+"F0.wireOp",EDGE,"E9"),sQuery(id+"F0.wireOp",EDGE,"E10")])]});
            var Q1;
            Q1=makeQuery(id+"F1.opRevolve","SWEPT_EDGE",EDGE,{"disambiguationData":[OSD([sQuery(id+"F0.wireOp",EDGE,"E10"),sQuery(id+"F0.wireOp",EDGE,"E11")])]});
            var Q2;
            Q2=makeQuery(id+"F1.opRevolve","SWEPT_EDGE",EDGE,{"disambiguationData":[OSD([sQuery(id+"F0.wireOp",EDGE,"E13"),sQuery(id+"F0.wireOp",EDGE,"E14")])]});
            var Q3;
            Q3=makeQuery(id+"F1.opRevolve","SWEPT_EDGE",EDGE,{"disambiguationData":[OSD([sQuery(id+"F0.wireOp",EDGE,"E14"),sQuery(id+"F0.wireOp",EDGE,"E15")])]});
            chamfer(context, id + "F50", {"entities" : qUnion([Q0, Q1, Q2, Q3]), "width" : 2 * mm, "tangentPropagation" : true});
        }
        {
            var Q0;
            {var subQ0=sQuery(id+"F0.wireOp",EDGE,"E5");Q0=makeQuery(id+"F46.opChamfer","BLEND_EDGE",EDGE,{"blendedFrom":[makeQuery(id+"F1.opRevolve","SWEPT_EDGE",EDGE,{"disambiguationData":[OSD([subQ0,sQuery(id+"F0.wireOp",EDGE,"E8")])]}),makeQuery(id+"F20.boolean.opBoolean","MERGE",FACE,{"derivedFrom":[makeQuery(id+"F19.boolean.opBoolean","MERGE",FACE,{"derivedFrom":[makeQuery(id+"F18.boolean.opBoolean","MERGE",FACE,{"derivedFrom":[makeQuery(id+"F17.boolean.opBoolean","MERGE",FACE,{"derivedFrom":[makeQuery(id+"F16.boolean.opBoolean","MERGE",FACE,{"derivedFrom":[makeQuery(id+"F15.boolean.opBoolean","MERGE",FACE,{"derivedFrom":[makeQuery(id+"F14.boolean.opBoolean","MERGE",FACE,{"derivedFrom":[makeQuery(id+"F13.boolean.opBoolean","MERGE",FACE,{"derivedFrom":[makeQuery(id+"F12.boolean.opBoolean","MERGE",FACE,{"derivedFrom":[makeQuery(id+"F11.boolean.opBoolean","MERGE",FACE,{"derivedFrom":[makeQuery(id+"F10.boolean.opBoolean","MERGE",FACE,{"derivedFrom":[makeQuery(id+"F9.boolean.opBoolean","MERGE",FACE,{"derivedFrom":[makeQuery(id+"F8.boolean.opBoolean","MERGE",FACE,{"derivedFrom":[makeQuery(id+"F7.boolean.opBoolean","MERGE",FACE,{"derivedFrom":[makeQuery(id+"F6.boolean.opBoolean","MERGE",FACE,{"derivedFrom":[makeQuery(id+"F5.boolean.opBoolean","MERGE",FACE,{"derivedFrom":[makeQuery(id+"F1.opRevolve","SWEPT_FACE",FACE,{"disambiguationData":[OSD([subQ0])]}),makeQuery(id+"F5.opLoft","CAP_FACE",FACE,{"disambiguationData":[OSD([makeQuery(id+"F4.imprint","IMPRINT",FACE,{"disambiguationData":[TD([[makeQuery(id+"F4.imprint","IMPRINT",EDGE,{"derivedFrom":sQuery(id+"F4.wireOp",EDGE,"E21")}),1.0]])]})])],"isStart":true})]}),makeQuery(id+"F6.opLoft","CAP_FACE",FACE,{"disambiguationData":[OSD([makeQuery(id+"F4.imprint","IMPRINT",FACE,{"disambiguationData":[TD([[makeQuery(id+"F4.imprint","IMPRINT",EDGE,{"derivedFrom":sQuery(id+"F4.wireOp",EDGE,"E26.15.0")}),1.0]])]})])],"isStart":true})]}),makeQuery(id+"F7.opLoft","CAP_FACE",FACE,{"disambiguationData":[OSD([makeQuery(id+"F4.imprint","IMPRINT",FACE,{"disambiguationData":[TD([[makeQuery(id+"F4.imprint","IMPRINT",EDGE,{"derivedFrom":sQuery(id+"F4.wireOp",EDGE,"E26.14.0")}),1.0]])]})])],"isStart":true})]}),makeQuery(id+"F8.opLoft","CAP_FACE",FACE,{"disambiguationData":[OSD([makeQuery(id+"F4.imprint","IMPRINT",FACE,{"disambiguationData":[TD([[makeQuery(id+"F4.imprint","IMPRINT",EDGE,{"derivedFrom":sQuery(id+"F4.wireOp",EDGE,"E26.13.0")}),1.0]])]})])],"isStart":true})]}),makeQuery(id+"F9.opLoft","CAP_FACE",FACE,{"disambiguationData":[OSD([makeQuery(id+"F4.imprint","IMPRINT",FACE,{"disambiguationData":[TD([[makeQuery(id+"F4.imprint","IMPRINT",EDGE,{"derivedFrom":sQuery(id+"F4.wireOp",EDGE,"E26.12.0")}),1.0]])]})])],"isStart":true})]}),makeQuery(id+"F10.opLoft","CAP_FACE",FACE,{"disambiguationData":[OSD([makeQuery(id+"F4.imprint","IMPRINT",FACE,{"disambiguationData":[TD([[makeQuery(id+"F4.imprint","IMPRINT",EDGE,{"derivedFrom":sQuery(id+"F4.wireOp",EDGE,"E26.11.0")}),1.0]])]})])],"isStart":true})]}),makeQuery(id+"F11.opLoft","CAP_FACE",FACE,{"disambiguationData":[OSD([makeQuery(id+"F4.imprint","IMPRINT",FACE,{"disambiguationData":[TD([[makeQuery(id+"F4.imprint","IMPRINT",EDGE,{"derivedFrom":sQuery(id+"F4.wireOp",EDGE,"E26.10.0")}),1.0]])]})])],"isStart":true})]}),makeQuery(id+"F12.opLoft","CAP_FACE",FACE,{"disambiguationData":[OSD([makeQuery(id+"F4.imprint","IMPRINT",FACE,{"disambiguationData":[TD([[makeQuery(id+"F4.imprint","IMPRINT",EDGE,{"derivedFrom":sQuery(id+"F4.wireOp",EDGE,"E26.9.0")}),1.0]])]})])],"isStart":true})]}),makeQuery(id+"F13.opLoft","CAP_FACE",FACE,{"disambiguationData":[OSD([makeQuery(id+"F4.imprint","IMPRINT",FACE,{"disambiguationData":[TD([[makeQuery(id+"F4.imprint","IMPRINT",EDGE,{"derivedFrom":sQuery(id+"F4.wireOp",EDGE,"E26.8.0")}),1.0]])]})])],"isStart":true})]}),makeQuery(id+"F14.opLoft","CAP_FACE",FACE,{"disambiguationData":[OSD([makeQuery(id+"F4.imprint","IMPRINT",FACE,{"disambiguationData":[TD([[makeQuery(id+"F4.imprint","IMPRINT",EDGE,{"derivedFrom":sQuery(id+"F4.wireOp",EDGE,"E26.7.0")}),1.0]])]})])],"isStart":true})]}),makeQuery(id+"F15.opLoft","CAP_FACE",FACE,{"disambiguationData":[OSD([makeQuery(id+"F4.imprint","IMPRINT",FACE,{"disambiguationData":[TD([[makeQuery(id+"F4.imprint","IMPRINT",EDGE,{"derivedFrom":sQuery(id+"F4.wireOp",EDGE,"E26.6.0")}),1.0]])]})])],"isStart":true})]}),makeQuery(id+"F16.opLoft","CAP_FACE",FACE,{"disambiguationData":[OSD([makeQuery(id+"F4.imprint","IMPRINT",FACE,{"disambiguationData":[TD([[makeQuery(id+"F4.imprint","IMPRINT",EDGE,{"derivedFrom":sQuery(id+"F4.wireOp",EDGE,"E26.5.0")}),1.0]])]})])],"isStart":true})]}),makeQuery(id+"F17.opLoft","CAP_FACE",FACE,{"disambiguationData":[OSD([makeQuery(id+"F4.imprint","IMPRINT",FACE,{"disambiguationData":[TD([[makeQuery(id+"F4.imprint","IMPRINT",EDGE,{"derivedFrom":sQuery(id+"F4.wireOp",EDGE,"E26.4.0")}),1.0]])]})])],"isStart":true})]}),makeQuery(id+"F18.opLoft","CAP_FACE",FACE,{"disambiguationData":[OSD([makeQuery(id+"F4.imprint","IMPRINT",FACE,{"disambiguationData":[TD([[makeQuery(id+"F4.imprint","IMPRINT",EDGE,{"derivedFrom":sQuery(id+"F4.wireOp",EDGE,"E26.3.0")}),1.0]])]})])],"isStart":true})]}),makeQuery(id+"F19.opLoft","CAP_FACE",FACE,{"disambiguationData":[OSD([makeQuery(id+"F4.imprint","IMPRINT",FACE,{"disambiguationData":[TD([[makeQuery(id+"F4.imprint","IMPRINT",EDGE,{"derivedFrom":sQuery(id+"F4.wireOp",EDGE,"E26.2.0")}),1.0]])]})])],"isStart":true})]}),makeQuery(id+"F20.opLoft","CAP_FACE",FACE,{"disambiguationData":[OSD([makeQuery(id+"F4.imprint","IMPRINT",FACE,{"disambiguationData":[TD([[makeQuery(id+"F4.imprint","IMPRINT",EDGE,{"derivedFrom":sQuery(id+"F4.wireOp",EDGE,"E26.1.0")}),1.0]])]})])],"isStart":true})]})],"blendedInto":[makeQuery(id+"F20.boolean.opBoolean","MERGE",FACE,{"derivedFrom":[makeQuery(id+"F19.boolean.opBoolean","MERGE",FACE,{"derivedFrom":[makeQuery(id+"F18.boolean.opBoolean","MERGE",FACE,{"derivedFrom":[makeQuery(id+"F17.boolean.opBoolean","MERGE",FACE,{"derivedFrom":[makeQuery(id+"F16.boolean.opBoolean","MERGE",FACE,{"derivedFrom":[makeQuery(id+"F15.boolean.opBoolean","MERGE",FACE,{"derivedFrom":[makeQuery(id+"F14.boolean.opBoolean","MERGE",FACE,{"derivedFrom":[makeQuery(id+"F13.boolean.opBoolean","MERGE",FACE,{"derivedFrom":[makeQuery(id+"F12.boolean.opBoolean","MERGE",FACE,{"derivedFrom":[makeQuery(id+"F11.boolean.opBoolean","MERGE",FACE,{"derivedFrom":[makeQuery(id+"F10.boolean.opBoolean","MERGE",FACE,{"derivedFrom":[makeQuery(id+"F9.boolean.opBoolean","MERGE",FACE,{"derivedFrom":[makeQuery(id+"F8.boolean.opBoolean","MERGE",FACE,{"derivedFrom":[makeQuery(id+"F7.boolean.opBoolean","MERGE",FACE,{"derivedFrom":[makeQuery(id+"F6.boolean.opBoolean","MERGE",FACE,{"derivedFrom":[makeQuery(id+"F5.boolean.opBoolean","MERGE",FACE,{"derivedFrom":[makeQuery(id+"F1.opRevolve","SWEPT_FACE",FACE,{"disambiguationData":[OSD([subQ0])]}),makeQuery(id+"F5.opLoft","CAP_FACE",FACE,{"disambiguationData":[OSD([makeQuery(id+"F4.imprint","IMPRINT",FACE,{"disambiguationData":[TD([[makeQuery(id+"F4.imprint","IMPRINT",EDGE,{"derivedFrom":sQuery(id+"F4.wireOp",EDGE,"E21")}),1.0]])]})])],"isStart":true})]}),makeQuery(id+"F6.opLoft","CAP_FACE",FACE,{"disambiguationData":[OSD([makeQuery(id+"F4.imprint","IMPRINT",FACE,{"disambiguationData":[TD([[makeQuery(id+"F4.imprint","IMPRINT",EDGE,{"derivedFrom":sQuery(id+"F4.wireOp",EDGE,"E26.15.0")}),1.0]])]})])],"isStart":true})]}),makeQuery(id+"F7.opLoft","CAP_FACE",FACE,{"disambiguationData":[OSD([makeQuery(id+"F4.imprint","IMPRINT",FACE,{"disambiguationData":[TD([[makeQuery(id+"F4.imprint","IMPRINT",EDGE,{"derivedFrom":sQuery(id+"F4.wireOp",EDGE,"E26.14.0")}),1.0]])]})])],"isStart":true})]}),makeQuery(id+"F8.opLoft","CAP_FACE",FACE,{"disambiguationData":[OSD([makeQuery(id+"F4.imprint","IMPRINT",FACE,{"disambiguationData":[TD([[makeQuery(id+"F4.imprint","IMPRINT",EDGE,{"derivedFrom":sQuery(id+"F4.wireOp",EDGE,"E26.13.0")}),1.0]])]})])],"isStart":true})]}),makeQuery(id+"F9.opLoft","CAP_FACE",FACE,{"disambiguationData":[OSD([makeQuery(id+"F4.imprint","IMPRINT",FACE,{"disambiguationData":[TD([[makeQuery(id+"F4.imprint","IMPRINT",EDGE,{"derivedFrom":sQuery(id+"F4.wireOp",EDGE,"E26.12.0")}),1.0]])]})])],"isStart":true})]}),makeQuery(id+"F10.opLoft","CAP_FACE",FACE,{"disambiguationData":[OSD([makeQuery(id+"F4.imprint","IMPRINT",FACE,{"disambiguationData":[TD([[makeQuery(id+"F4.imprint","IMPRINT",EDGE,{"derivedFrom":sQuery(id+"F4.wireOp",EDGE,"E26.11.0")}),1.0]])]})])],"isStart":true})]}),makeQuery(id+"F11.opLoft","CAP_FACE",FACE,{"disambiguationData":[OSD([makeQuery(id+"F4.imprint","IMPRINT",FACE,{"disambiguationData":[TD([[makeQuery(id+"F4.imprint","IMPRINT",EDGE,{"derivedFrom":sQuery(id+"F4.wireOp",EDGE,"E26.10.0")}),1.0]])]})])],"isStart":true})]}),makeQuery(id+"F12.opLoft","CAP_FACE",FACE,{"disambiguationData":[OSD([makeQuery(id+"F4.imprint","IMPRINT",FACE,{"disambiguationData":[TD([[makeQuery(id+"F4.imprint","IMPRINT",EDGE,{"derivedFrom":sQuery(id+"F4.wireOp",EDGE,"E26.9.0")}),1.0]])]})])],"isStart":true})]}),makeQuery(id+"F13.opLoft","CAP_FACE",FACE,{"disambiguationData":[OSD([makeQuery(id+"F4.imprint","IMPRINT",FACE,{"disambiguationData":[TD([[makeQuery(id+"F4.imprint","IMPRINT",EDGE,{"derivedFrom":sQuery(id+"F4.wireOp",EDGE,"E26.8.0")}),1.0]])]})])],"isStart":true})]}),makeQuery(id+"F14.opLoft","CAP_FACE",FACE,{"disambiguationData":[OSD([makeQuery(id+"F4.imprint","IMPRINT",FACE,{"disambiguationData":[TD([[makeQuery(id+"F4.imprint","IMPRINT",EDGE,{"derivedFrom":sQuery(id+"F4.wireOp",EDGE,"E26.7.0")}),1.0]])]})])],"isStart":true})]}),makeQuery(id+"F15.opLoft","CAP_FACE",FACE,{"disambiguationData":[OSD([makeQuery(id+"F4.imprint","IMPRINT",FACE,{"disambiguationData":[TD([[makeQuery(id+"F4.imprint","IMPRINT",EDGE,{"derivedFrom":sQuery(id+"F4.wireOp",EDGE,"E26.6.0")}),1.0]])]})])],"isStart":true})]}),makeQuery(id+"F16.opLoft","CAP_FACE",FACE,{"disambiguationData":[OSD([makeQuery(id+"F4.imprint","IMPRINT",FACE,{"disambiguationData":[TD([[makeQuery(id+"F4.imprint","IMPRINT",EDGE,{"derivedFrom":sQuery(id+"F4.wireOp",EDGE,"E26.5.0")}),1.0]])]})])],"isStart":true})]}),makeQuery(id+"F17.opLoft","CAP_FACE",FACE,{"disambiguationData":[OSD([makeQuery(id+"F4.imprint","IMPRINT",FACE,{"disambiguationData":[TD([[makeQuery(id+"F4.imprint","IMPRINT",EDGE,{"derivedFrom":sQuery(id+"F4.wireOp",EDGE,"E26.4.0")}),1.0]])]})])],"isStart":true})]}),makeQuery(id+"F18.opLoft","CAP_FACE",FACE,{"disambiguationData":[OSD([makeQuery(id+"F4.imprint","IMPRINT",FACE,{"disambiguationData":[TD([[makeQuery(id+"F4.imprint","IMPRINT",EDGE,{"derivedFrom":sQuery(id+"F4.wireOp",EDGE,"E26.3.0")}),1.0]])]})])],"isStart":true})]}),makeQuery(id+"F19.opLoft","CAP_FACE",FACE,{"disambiguationData":[OSD([makeQuery(id+"F4.imprint","IMPRINT",FACE,{"disambiguationData":[TD([[makeQuery(id+"F4.imprint","IMPRINT",EDGE,{"derivedFrom":sQuery(id+"F4.wireOp",EDGE,"E26.2.0")}),1.0]])]})])],"isStart":true})]}),makeQuery(id+"F20.opLoft","CAP_FACE",FACE,{"disambiguationData":[OSD([makeQuery(id+"F4.imprint","IMPRINT",FACE,{"disambiguationData":[TD([[makeQuery(id+"F4.imprint","IMPRINT",EDGE,{"derivedFrom":sQuery(id+"F4.wireOp",EDGE,"E26.1.0")}),1.0]])]})])],"isStart":true})]})]});}
            fillet(context, id + "F51", {"entities" : qUnion([Q0]), "radius" : 6 * mm, "tangentPropagation" : true, "allowEdgeOverflow" : false});
        }
    });
